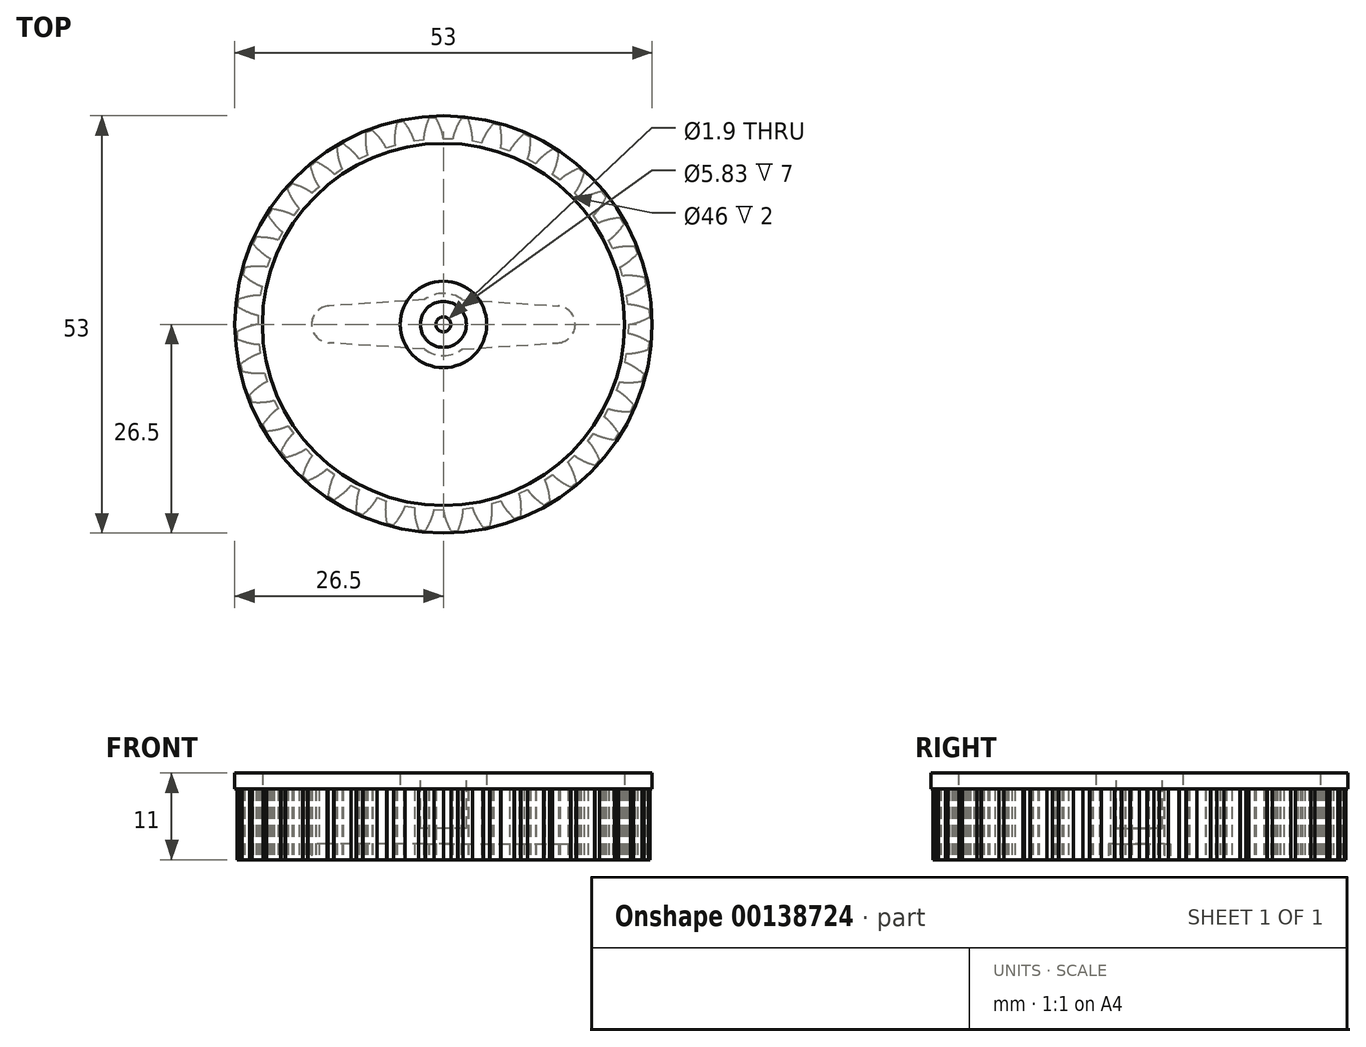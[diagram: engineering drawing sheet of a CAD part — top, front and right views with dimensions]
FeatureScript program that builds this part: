
annotation { "Feature Type Name" : "Feature", "Feature Type Description" : "" }
export const myFeature = defineFeature(function(context is Context, id is Id, definition is map)
    precondition{}
    {
        {
            var Q0;
            Q0=qCreatedBy(makeId("Top.planeOp"),FACE);
            var sketch = newSketch(context, id + "F0", { "sketchPlane" : qUnion([Q0])});
            skLineSegment(sketch, "E0", {"start": v(23.56, 0) * mm, "end": v(23.58, 0) * mm});
            skLineSegment(sketch, "E1", {"start": v(23.58, 0) * mm, "end": v(23.6, 0) * mm});
            skLineSegment(sketch, "E2", {"start": v(23.6, 0) * mm, "end": v(23.62, 0) * mm});
            skLineSegment(sketch, "E3", {"start": v(23.62, 0) * mm, "end": v(23.64, 0.01) * mm});
            skLineSegment(sketch, "E4", {"start": v(23.64, 0.01) * mm, "end": v(23.67, 0.01) * mm});
            skLineSegment(sketch, "E5", {"start": v(23.67, 0.01) * mm, "end": v(23.7, 0.02) * mm});
            skLineSegment(sketch, "E6", {"start": v(23.7, 0.02) * mm, "end": v(23.72, 0.02) * mm});
            skLineSegment(sketch, "E7", {"start": v(23.72, 0.02) * mm, "end": v(23.75, 0.03) * mm});
            skLineSegment(sketch, "E8", {"start": v(23.75, 0.03) * mm, "end": v(23.78, 0.03) * mm});
            skLineSegment(sketch, "E9", {"start": v(23.78, 0.03) * mm, "end": v(23.81, 0.04) * mm});
            skLineSegment(sketch, "E10", {"start": v(23.81, 0.04) * mm, "end": v(23.85, 0.04) * mm});
            skLineSegment(sketch, "E11", {"start": v(23.85, 0.04) * mm, "end": v(23.88, 0.05) * mm});
            skLineSegment(sketch, "E12", {"start": v(23.88, 0.05) * mm, "end": v(23.92, 0.06) * mm});
            skLineSegment(sketch, "E13", {"start": v(23.92, 0.06) * mm, "end": v(23.96, 0.06) * mm});
            skLineSegment(sketch, "E14", {"start": v(23.96, 0.06) * mm, "end": v(24, 0.07) * mm});
            skLineSegment(sketch, "E15", {"start": v(24, 0.07) * mm, "end": v(24.04, 0.08) * mm});
            skLineSegment(sketch, "E16", {"start": v(24.04, 0.08) * mm, "end": v(24.09, 0.1) * mm});
            skLineSegment(sketch, "E17", {"start": v(24.09, 0.1) * mm, "end": v(24.14, 0.1) * mm});
            skLineSegment(sketch, "E18", {"start": v(24.14, 0.1) * mm, "end": v(24.18, 0.11) * mm});
            skLineSegment(sketch, "E19", {"start": v(24.18, 0.11) * mm, "end": v(24.23, 0.13) * mm});
            skLineSegment(sketch, "E20", {"start": v(24.23, 0.13) * mm, "end": v(24.28, 0.14) * mm});
            skLineSegment(sketch, "E21", {"start": v(24.28, 0.14) * mm, "end": v(24.34, 0.15) * mm});
            skLineSegment(sketch, "E22", {"start": v(24.34, 0.15) * mm, "end": v(24.4, 0.17) * mm});
            skLineSegment(sketch, "E23", {"start": v(24.4, 0.17) * mm, "end": v(24.45, 0.19) * mm});
            skLineSegment(sketch, "E24", {"start": v(24.45, 0.19) * mm, "end": v(24.5, 0.2) * mm});
            skLineSegment(sketch, "E25", {"start": v(24.5, 0.2) * mm, "end": v(24.56, 0.22) * mm});
            skLineSegment(sketch, "E26", {"start": v(24.56, 0.22) * mm, "end": v(24.62, 0.24) * mm});
            skLineSegment(sketch, "E27", {"start": v(24.62, 0.24) * mm, "end": v(24.69, 0.26) * mm});
            skLineSegment(sketch, "E28", {"start": v(24.69, 0.26) * mm, "end": v(24.75, 0.28) * mm});
            skLineSegment(sketch, "E29", {"start": v(24.75, 0.28) * mm, "end": v(24.81, 0.3) * mm});
            skLineSegment(sketch, "E30", {"start": v(24.81, 0.3) * mm, "end": v(24.88, 0.33) * mm});
            skLineSegment(sketch, "E31", {"start": v(24.88, 0.33) * mm, "end": v(24.95, 0.35) * mm});
            skLineSegment(sketch, "E32", {"start": v(24.95, 0.35) * mm, "end": v(25.02, 0.38) * mm});
            skLineSegment(sketch, "E33", {"start": v(25.02, 0.38) * mm, "end": v(25.09, 0.4) * mm});
            skLineSegment(sketch, "E34", {"start": v(25.09, 0.4) * mm, "end": v(25.16, 0.44) * mm});
            skLineSegment(sketch, "E35", {"start": v(25.16, 0.44) * mm, "end": v(25.23, 0.47) * mm});
            skLineSegment(sketch, "E36", {"start": v(25.23, 0.47) * mm, "end": v(25.3, 0.5) * mm});
            skLineSegment(sketch, "E37", {"start": v(25.3, 0.5) * mm, "end": v(25.39, 0.53) * mm});
            skLineSegment(sketch, "E38", {"start": v(25.39, 0.53) * mm, "end": v(25.46, 0.57) * mm});
            skLineSegment(sketch, "E39", {"start": v(25.46, 0.57) * mm, "end": v(25.54, 0.6) * mm});
            skLineSegment(sketch, "E40", {"start": v(25.54, 0.6) * mm, "end": v(25.62, 0.64) * mm});
            skLineSegment(sketch, "E41", {"start": v(25.62, 0.64) * mm, "end": v(25.7, 0.68) * mm});
            skLineSegment(sketch, "E42", {"start": v(25.7, 0.68) * mm, "end": v(25.79, 0.72) * mm});
            skLineSegment(sketch, "E43", {"start": v(25.79, 0.72) * mm, "end": v(25.87, 0.76) * mm});
            skLineSegment(sketch, "E44", {"start": v(25.87, 0.76) * mm, "end": v(25.96, 0.8) * mm});
            skLineSegment(sketch, "E45", {"start": v(25.96, 0.8) * mm, "end": v(26.04, 0.85) * mm});
            skLineSegment(sketch, "E46", {"start": v(26.04, 0.85) * mm, "end": v(26.13, 0.9) * mm});
            skLineSegment(sketch, "E47", {"start": v(26.13, 0.9) * mm, "end": v(26.22, 0.94) * mm});
            skLineSegment(sketch, "E48", {"start": v(26.22, 0.94) * mm, "end": v(26.23, 0.99) * mm});
            skLineSegment(sketch, "E49", {"start": v(26.23, 0.99) * mm, "end": v(26.19, 1.82) * mm});
            skLineSegment(sketch, "E50", {"start": v(26.19, 1.82) * mm, "end": v(26.17, 1.86) * mm});
            skLineSegment(sketch, "E51", {"start": v(26.17, 1.86) * mm, "end": v(26.08, 1.9) * mm});
            skLineSegment(sketch, "E52", {"start": v(26.08, 1.9) * mm, "end": v(25.99, 1.94) * mm});
            skLineSegment(sketch, "E53", {"start": v(25.99, 1.94) * mm, "end": v(25.9, 1.97) * mm});
            skLineSegment(sketch, "E54", {"start": v(25.9, 1.97) * mm, "end": v(25.8, 2) * mm});
            skLineSegment(sketch, "E55", {"start": v(25.8, 2) * mm, "end": v(25.72, 2.04) * mm});
            skLineSegment(sketch, "E56", {"start": v(25.72, 2.04) * mm, "end": v(25.63, 2.07) * mm});
            skLineSegment(sketch, "E57", {"start": v(25.63, 2.07) * mm, "end": v(25.55, 2.1) * mm});
            skLineSegment(sketch, "E58", {"start": v(25.55, 2.1) * mm, "end": v(25.46, 2.13) * mm});
            skLineSegment(sketch, "E59", {"start": v(25.46, 2.13) * mm, "end": v(25.38, 2.16) * mm});
            skLineSegment(sketch, "E60", {"start": v(25.38, 2.16) * mm, "end": v(25.3, 2.18) * mm});
            skLineSegment(sketch, "E61", {"start": v(25.3, 2.18) * mm, "end": v(25.22, 2.2) * mm});
            skLineSegment(sketch, "E62", {"start": v(25.22, 2.2) * mm, "end": v(25.14, 2.23) * mm});
            skLineSegment(sketch, "E63", {"start": v(25.14, 2.23) * mm, "end": v(25.06, 2.25) * mm});
            skLineSegment(sketch, "E64", {"start": v(25.06, 2.25) * mm, "end": v(24.99, 2.27) * mm});
            skLineSegment(sketch, "E65", {"start": v(24.99, 2.27) * mm, "end": v(24.92, 2.3) * mm});
            skLineSegment(sketch, "E66", {"start": v(24.92, 2.3) * mm, "end": v(24.84, 2.31) * mm});
            skLineSegment(sketch, "E67", {"start": v(24.84, 2.31) * mm, "end": v(24.77, 2.33) * mm});
            skLineSegment(sketch, "E68", {"start": v(24.77, 2.33) * mm, "end": v(24.7, 2.34) * mm});
            skLineSegment(sketch, "E69", {"start": v(24.7, 2.34) * mm, "end": v(24.64, 2.36) * mm});
            skLineSegment(sketch, "E70", {"start": v(24.64, 2.36) * mm, "end": v(24.57, 2.38) * mm});
            skLineSegment(sketch, "E71", {"start": v(24.57, 2.38) * mm, "end": v(24.5, 2.39) * mm});
            skLineSegment(sketch, "E72", {"start": v(24.5, 2.39) * mm, "end": v(24.45, 2.4) * mm});
            skLineSegment(sketch, "E73", {"start": v(24.45, 2.4) * mm, "end": v(24.39, 2.41) * mm});
            skLineSegment(sketch, "E74", {"start": v(24.39, 2.41) * mm, "end": v(24.33, 2.42) * mm});
            skLineSegment(sketch, "E75", {"start": v(24.33, 2.42) * mm, "end": v(24.27, 2.43) * mm});
            skLineSegment(sketch, "E76", {"start": v(24.27, 2.43) * mm, "end": v(24.21, 2.44) * mm});
            skLineSegment(sketch, "E77", {"start": v(24.21, 2.44) * mm, "end": v(24.16, 2.45) * mm});
            skLineSegment(sketch, "E78", {"start": v(24.16, 2.45) * mm, "end": v(24.1, 2.46) * mm});
            skLineSegment(sketch, "E79", {"start": v(24.1, 2.46) * mm, "end": v(24.06, 2.47) * mm});
            skLineSegment(sketch, "E80", {"start": v(24.06, 2.47) * mm, "end": v(24, 2.47) * mm});
            skLineSegment(sketch, "E81", {"start": v(24, 2.47) * mm, "end": v(23.96, 2.48) * mm});
            skLineSegment(sketch, "E82", {"start": v(23.96, 2.48) * mm, "end": v(23.92, 2.49) * mm});
            skLineSegment(sketch, "E83", {"start": v(23.92, 2.49) * mm, "end": v(23.87, 2.5) * mm});
            skLineSegment(sketch, "E84", {"start": v(23.87, 2.5) * mm, "end": v(23.83, 2.5) * mm});
            skLineSegment(sketch, "E85", {"start": v(23.83, 2.5) * mm, "end": v(23.8, 2.5) * mm});
            skLineSegment(sketch, "E86", {"start": v(23.8, 2.5) * mm, "end": v(23.75, 2.5) * mm});
            skLineSegment(sketch, "E87", {"start": v(23.75, 2.5) * mm, "end": v(23.72, 2.5) * mm});
            skLineSegment(sketch, "E88", {"start": v(23.72, 2.5) * mm, "end": v(23.68, 2.5) * mm});
            skLineSegment(sketch, "E89", {"start": v(23.68, 2.5) * mm, "end": v(23.65, 2.5) * mm});
            skLineSegment(sketch, "E90", {"start": v(23.65, 2.5) * mm, "end": v(23.62, 2.5) * mm});
            skLineSegment(sketch, "E91", {"start": v(23.62, 2.5) * mm, "end": v(23.59, 2.51) * mm});
            skLineSegment(sketch, "E92", {"start": v(23.59, 2.51) * mm, "end": v(23.56, 2.51) * mm});
            skLineSegment(sketch, "E93", {"start": v(23.56, 2.51) * mm, "end": v(23.53, 2.51) * mm});
            skLineSegment(sketch, "E94", {"start": v(23.53, 2.51) * mm, "end": v(23.5, 2.51) * mm});
            skLineSegment(sketch, "E95", {"start": v(23.5, 2.51) * mm, "end": v(23.49, 2.51) * mm});
            skLineSegment(sketch, "E96", {"start": v(23.49, 2.51) * mm, "end": v(23.47, 2.51) * mm});
            skLineSegment(sketch, "E97", {"start": v(23.47, 2.51) * mm, "end": v(23.45, 2.51) * mm});
            skLineSegment(sketch, "E98", {"start": v(23.45, 2.51) * mm, "end": v(23.43, 2.51) * mm});
            skLineSegment(sketch, "E99", {"start": v(23.43, 2.51) * mm, "end": v(23.27, 3.69) * mm});
            skLineSegment(sketch, "E100", {"start": v(23.27, 3.69) * mm, "end": v(23.3, 3.7) * mm});
            skLineSegment(sketch, "E101", {"start": v(23.3, 3.7) * mm, "end": v(23.3, 3.7) * mm});
            skLineSegment(sketch, "E102", {"start": v(23.3, 3.7) * mm, "end": v(23.33, 3.7) * mm});
            skLineSegment(sketch, "E103", {"start": v(23.33, 3.7) * mm, "end": v(23.35, 3.7) * mm});
            skLineSegment(sketch, "E104", {"start": v(23.35, 3.7) * mm, "end": v(23.37, 3.72) * mm});
            skLineSegment(sketch, "E105", {"start": v(23.37, 3.72) * mm, "end": v(23.4, 3.72) * mm});
            skLineSegment(sketch, "E106", {"start": v(23.4, 3.72) * mm, "end": v(23.42, 3.73) * mm});
            skLineSegment(sketch, "E107", {"start": v(23.42, 3.73) * mm, "end": v(23.45, 3.74) * mm});
            skLineSegment(sketch, "E108", {"start": v(23.45, 3.74) * mm, "end": v(23.48, 3.75) * mm});
            skLineSegment(sketch, "E109", {"start": v(23.48, 3.75) * mm, "end": v(23.51, 3.76) * mm});
            skLineSegment(sketch, "E110", {"start": v(23.51, 3.76) * mm, "end": v(23.55, 3.77) * mm});
            skLineSegment(sketch, "E111", {"start": v(23.55, 3.77) * mm, "end": v(23.58, 3.78) * mm});
            skLineSegment(sketch, "E112", {"start": v(23.58, 3.78) * mm, "end": v(23.62, 3.8) * mm});
            skLineSegment(sketch, "E113", {"start": v(23.62, 3.8) * mm, "end": v(23.66, 3.81) * mm});
            skLineSegment(sketch, "E114", {"start": v(23.66, 3.81) * mm, "end": v(23.7, 3.83) * mm});
            skLineSegment(sketch, "E115", {"start": v(23.7, 3.83) * mm, "end": v(23.74, 3.84) * mm});
            skLineSegment(sketch, "E116", {"start": v(23.74, 3.84) * mm, "end": v(23.78, 3.86) * mm});
            skLineSegment(sketch, "E117", {"start": v(23.78, 3.86) * mm, "end": v(23.82, 3.88) * mm});
            skLineSegment(sketch, "E118", {"start": v(23.82, 3.88) * mm, "end": v(23.87, 3.9) * mm});
            skLineSegment(sketch, "E119", {"start": v(23.87, 3.9) * mm, "end": v(23.91, 3.92) * mm});
            skLineSegment(sketch, "E120", {"start": v(23.91, 3.92) * mm, "end": v(23.96, 3.94) * mm});
            skLineSegment(sketch, "E121", {"start": v(23.96, 3.94) * mm, "end": v(24.01, 3.96) * mm});
            skLineSegment(sketch, "E122", {"start": v(24.01, 3.96) * mm, "end": v(24.06, 3.98) * mm});
            skLineSegment(sketch, "E123", {"start": v(24.06, 3.98) * mm, "end": v(24.12, 4) * mm});
            skLineSegment(sketch, "E124", {"start": v(24.12, 4) * mm, "end": v(24.17, 4.03) * mm});
            skLineSegment(sketch, "E125", {"start": v(24.17, 4.03) * mm, "end": v(24.23, 4.06) * mm});
            skLineSegment(sketch, "E126", {"start": v(24.23, 4.06) * mm, "end": v(24.28, 4.09) * mm});
            skLineSegment(sketch, "E127", {"start": v(24.28, 4.09) * mm, "end": v(24.34, 4.12) * mm});
            skLineSegment(sketch, "E128", {"start": v(24.34, 4.12) * mm, "end": v(24.4, 4.15) * mm});
            skLineSegment(sketch, "E129", {"start": v(24.4, 4.15) * mm, "end": v(24.46, 4.18) * mm});
            skLineSegment(sketch, "E130", {"start": v(24.46, 4.18) * mm, "end": v(24.52, 4.22) * mm});
            skLineSegment(sketch, "E131", {"start": v(24.52, 4.22) * mm, "end": v(24.59, 4.25) * mm});
            skLineSegment(sketch, "E132", {"start": v(24.59, 4.25) * mm, "end": v(24.65, 4.29) * mm});
            skLineSegment(sketch, "E133", {"start": v(24.65, 4.29) * mm, "end": v(24.72, 4.33) * mm});
            skLineSegment(sketch, "E134", {"start": v(24.72, 4.33) * mm, "end": v(24.78, 4.37) * mm});
            skLineSegment(sketch, "E135", {"start": v(24.78, 4.37) * mm, "end": v(24.85, 4.4) * mm});
            skLineSegment(sketch, "E136", {"start": v(24.85, 4.4) * mm, "end": v(24.92, 4.45) * mm});
            skLineSegment(sketch, "E137", {"start": v(24.92, 4.45) * mm, "end": v(25, 4.5) * mm});
            skLineSegment(sketch, "E138", {"start": v(25, 4.5) * mm, "end": v(25.06, 4.54) * mm});
            skLineSegment(sketch, "E139", {"start": v(25.06, 4.54) * mm, "end": v(25.13, 4.59) * mm});
            skLineSegment(sketch, "E140", {"start": v(25.13, 4.59) * mm, "end": v(25.2, 4.64) * mm});
            skLineSegment(sketch, "E141", {"start": v(25.2, 4.64) * mm, "end": v(25.28, 4.69) * mm});
            skLineSegment(sketch, "E142", {"start": v(25.28, 4.69) * mm, "end": v(25.36, 4.74) * mm});
            skLineSegment(sketch, "E143", {"start": v(25.36, 4.74) * mm, "end": v(25.44, 4.8) * mm});
            skLineSegment(sketch, "E144", {"start": v(25.44, 4.8) * mm, "end": v(25.51, 4.85) * mm});
            skLineSegment(sketch, "E145", {"start": v(25.51, 4.85) * mm, "end": v(25.6, 4.9) * mm});
            skLineSegment(sketch, "E146", {"start": v(25.6, 4.9) * mm, "end": v(25.67, 4.97) * mm});
            skLineSegment(sketch, "E147", {"start": v(25.67, 4.97) * mm, "end": v(25.75, 5.03) * mm});
            skLineSegment(sketch, "E148", {"start": v(25.75, 5.03) * mm, "end": v(25.75, 5.08) * mm});
            skLineSegment(sketch, "E149", {"start": v(25.75, 5.08) * mm, "end": v(25.58, 5.9) * mm});
            skLineSegment(sketch, "E150", {"start": v(25.58, 5.9) * mm, "end": v(25.56, 5.93) * mm});
            skLineSegment(sketch, "E151", {"start": v(25.56, 5.93) * mm, "end": v(25.46, 5.96) * mm});
            skLineSegment(sketch, "E152", {"start": v(25.46, 5.96) * mm, "end": v(25.36, 5.98) * mm});
            skLineSegment(sketch, "E153", {"start": v(25.36, 5.98) * mm, "end": v(25.27, 6) * mm});
            skLineSegment(sketch, "E154", {"start": v(25.27, 6) * mm, "end": v(25.17, 6.02) * mm});
            skLineSegment(sketch, "E155", {"start": v(25.17, 6.02) * mm, "end": v(25.08, 6.04) * mm});
            skLineSegment(sketch, "E156", {"start": v(25.08, 6.04) * mm, "end": v(25, 6.05) * mm});
            skLineSegment(sketch, "E157", {"start": v(25, 6.05) * mm, "end": v(24.9, 6.07) * mm});
            skLineSegment(sketch, "E158", {"start": v(24.9, 6.07) * mm, "end": v(24.81, 6.09) * mm});
            skLineSegment(sketch, "E159", {"start": v(24.81, 6.09) * mm, "end": v(24.73, 6.1) * mm});
            skLineSegment(sketch, "E160", {"start": v(24.73, 6.1) * mm, "end": v(24.65, 6.11) * mm});
            skLineSegment(sketch, "E161", {"start": v(24.65, 6.11) * mm, "end": v(24.56, 6.12) * mm});
            skLineSegment(sketch, "E162", {"start": v(24.56, 6.12) * mm, "end": v(24.48, 6.13) * mm});
            skLineSegment(sketch, "E163", {"start": v(24.48, 6.13) * mm, "end": v(24.4, 6.14) * mm});
            skLineSegment(sketch, "E164", {"start": v(24.4, 6.14) * mm, "end": v(24.33, 6.15) * mm});
            skLineSegment(sketch, "E165", {"start": v(24.33, 6.15) * mm, "end": v(24.25, 6.16) * mm});
            skLineSegment(sketch, "E166", {"start": v(24.25, 6.16) * mm, "end": v(24.18, 6.17) * mm});
            skLineSegment(sketch, "E167", {"start": v(24.18, 6.17) * mm, "end": v(24.1, 6.17) * mm});
            skLineSegment(sketch, "E168", {"start": v(24.1, 6.17) * mm, "end": v(24.03, 6.18) * mm});
            skLineSegment(sketch, "E169", {"start": v(24.03, 6.18) * mm, "end": v(23.96, 6.19) * mm});
            skLineSegment(sketch, "E170", {"start": v(23.96, 6.19) * mm, "end": v(23.9, 6.19) * mm});
            skLineSegment(sketch, "E171", {"start": v(23.9, 6.19) * mm, "end": v(23.83, 6.2) * mm});
            skLineSegment(sketch, "E172", {"start": v(23.83, 6.2) * mm, "end": v(23.77, 6.2) * mm});
            skLineSegment(sketch, "E173", {"start": v(23.77, 6.2) * mm, "end": v(23.7, 6.2) * mm});
            skLineSegment(sketch, "E174", {"start": v(23.7, 6.2) * mm, "end": v(23.65, 6.2) * mm});
            skLineSegment(sketch, "E175", {"start": v(23.65, 6.2) * mm, "end": v(23.59, 6.2) * mm});
            skLineSegment(sketch, "E176", {"start": v(23.59, 6.2) * mm, "end": v(23.53, 6.2) * mm});
            skLineSegment(sketch, "E177", {"start": v(23.53, 6.2) * mm, "end": v(23.48, 6.2) * mm});
            skLineSegment(sketch, "E178", {"start": v(23.48, 6.2) * mm, "end": v(23.43, 6.2) * mm});
            skLineSegment(sketch, "E179", {"start": v(23.43, 6.2) * mm, "end": v(23.37, 6.2) * mm});
            skLineSegment(sketch, "E180", {"start": v(23.37, 6.2) * mm, "end": v(23.33, 6.2) * mm});
            skLineSegment(sketch, "E181", {"start": v(23.33, 6.2) * mm, "end": v(23.28, 6.2) * mm});
            skLineSegment(sketch, "E182", {"start": v(23.28, 6.2) * mm, "end": v(23.23, 6.2) * mm});
            skLineSegment(sketch, "E183", {"start": v(23.23, 6.2) * mm, "end": v(23.19, 6.2) * mm});
            skLineSegment(sketch, "E184", {"start": v(23.19, 6.2) * mm, "end": v(23.15, 6.2) * mm});
            skLineSegment(sketch, "E185", {"start": v(23.15, 6.2) * mm, "end": v(23.1, 6.19) * mm});
            skLineSegment(sketch, "E186", {"start": v(23.1, 6.19) * mm, "end": v(23.07, 6.19) * mm});
            skLineSegment(sketch, "E187", {"start": v(23.07, 6.19) * mm, "end": v(23.03, 6.18) * mm});
            skLineSegment(sketch, "E188", {"start": v(23.03, 6.18) * mm, "end": v(23, 6.18) * mm});
            skLineSegment(sketch, "E189", {"start": v(23, 6.18) * mm, "end": v(22.96, 6.18) * mm});
            skLineSegment(sketch, "E190", {"start": v(22.96, 6.18) * mm, "end": v(22.93, 6.17) * mm});
            skLineSegment(sketch, "E191", {"start": v(22.93, 6.17) * mm, "end": v(22.9, 6.17) * mm});
            skLineSegment(sketch, "E192", {"start": v(22.9, 6.17) * mm, "end": v(22.88, 6.17) * mm});
            skLineSegment(sketch, "E193", {"start": v(22.88, 6.17) * mm, "end": v(22.85, 6.16) * mm});
            skLineSegment(sketch, "E194", {"start": v(22.85, 6.16) * mm, "end": v(22.83, 6.16) * mm});
            skLineSegment(sketch, "E195", {"start": v(22.83, 6.16) * mm, "end": v(22.8, 6.16) * mm});
            skLineSegment(sketch, "E196", {"start": v(22.8, 6.16) * mm, "end": v(22.78, 6.15) * mm});
            skLineSegment(sketch, "E197", {"start": v(22.78, 6.15) * mm, "end": v(22.77, 6.15) * mm});
            skLineSegment(sketch, "E198", {"start": v(22.77, 6.15) * mm, "end": v(22.75, 6.15) * mm});
            skLineSegment(sketch, "E199", {"start": v(22.75, 6.15) * mm, "end": v(22.4, 7.28) * mm});
            skLineSegment(sketch, "E200", {"start": v(22.4, 7.28) * mm, "end": v(22.43, 7.3) * mm});
            skLineSegment(sketch, "E201", {"start": v(22.43, 7.3) * mm, "end": v(22.44, 7.3) * mm});
            skLineSegment(sketch, "E202", {"start": v(22.44, 7.3) * mm, "end": v(22.46, 7.3) * mm});
            skLineSegment(sketch, "E203", {"start": v(22.46, 7.3) * mm, "end": v(22.48, 7.32) * mm});
            skLineSegment(sketch, "E204", {"start": v(22.48, 7.32) * mm, "end": v(22.5, 7.33) * mm});
            skLineSegment(sketch, "E205", {"start": v(22.5, 7.33) * mm, "end": v(22.53, 7.34) * mm});
            skLineSegment(sketch, "E206", {"start": v(22.53, 7.34) * mm, "end": v(22.55, 7.35) * mm});
            skLineSegment(sketch, "E207", {"start": v(22.55, 7.35) * mm, "end": v(22.58, 7.36) * mm});
            skLineSegment(sketch, "E208", {"start": v(22.58, 7.36) * mm, "end": v(22.6, 7.38) * mm});
            skLineSegment(sketch, "E209", {"start": v(22.6, 7.38) * mm, "end": v(22.64, 7.4) * mm});
            skLineSegment(sketch, "E210", {"start": v(22.64, 7.4) * mm, "end": v(22.67, 7.4) * mm});
            skLineSegment(sketch, "E211", {"start": v(22.67, 7.4) * mm, "end": v(22.7, 7.43) * mm});
            skLineSegment(sketch, "E212", {"start": v(22.7, 7.43) * mm, "end": v(22.73, 7.44) * mm});
            skLineSegment(sketch, "E213", {"start": v(22.73, 7.44) * mm, "end": v(22.77, 7.46) * mm});
            skLineSegment(sketch, "E214", {"start": v(22.77, 7.46) * mm, "end": v(22.8, 7.49) * mm});
            skLineSegment(sketch, "E215", {"start": v(22.8, 7.49) * mm, "end": v(22.84, 7.5) * mm});
            skLineSegment(sketch, "E216", {"start": v(22.84, 7.5) * mm, "end": v(22.88, 7.53) * mm});
            skLineSegment(sketch, "E217", {"start": v(22.88, 7.53) * mm, "end": v(22.92, 7.56) * mm});
            skLineSegment(sketch, "E218", {"start": v(22.92, 7.56) * mm, "end": v(22.96, 7.58) * mm});
            skLineSegment(sketch, "E219", {"start": v(22.96, 7.58) * mm, "end": v(23, 7.6) * mm});
            skLineSegment(sketch, "E220", {"start": v(23, 7.6) * mm, "end": v(23.05, 7.64) * mm});
            skLineSegment(sketch, "E221", {"start": v(23.05, 7.64) * mm, "end": v(23.1, 7.67) * mm});
            skLineSegment(sketch, "E222", {"start": v(23.1, 7.67) * mm, "end": v(23.14, 7.7) * mm});
            skLineSegment(sketch, "E223", {"start": v(23.14, 7.7) * mm, "end": v(23.2, 7.73) * mm});
            skLineSegment(sketch, "E224", {"start": v(23.2, 7.73) * mm, "end": v(23.24, 7.76) * mm});
            skLineSegment(sketch, "E225", {"start": v(23.24, 7.76) * mm, "end": v(23.3, 7.8) * mm});
            skLineSegment(sketch, "E226", {"start": v(23.3, 7.8) * mm, "end": v(23.34, 7.84) * mm});
            skLineSegment(sketch, "E227", {"start": v(23.34, 7.84) * mm, "end": v(23.4, 7.88) * mm});
            skLineSegment(sketch, "E228", {"start": v(23.4, 7.88) * mm, "end": v(23.45, 7.92) * mm});
            skLineSegment(sketch, "E229", {"start": v(23.45, 7.92) * mm, "end": v(23.5, 7.96) * mm});
            skLineSegment(sketch, "E230", {"start": v(23.5, 7.96) * mm, "end": v(23.56, 8) * mm});
            skLineSegment(sketch, "E231", {"start": v(23.56, 8) * mm, "end": v(23.62, 8.05) * mm});
            skLineSegment(sketch, "E232", {"start": v(23.62, 8.05) * mm, "end": v(23.68, 8.1) * mm});
            skLineSegment(sketch, "E233", {"start": v(23.68, 8.1) * mm, "end": v(23.73, 8.14) * mm});
            skLineSegment(sketch, "E234", {"start": v(23.73, 8.14) * mm, "end": v(23.8, 8.2) * mm});
            skLineSegment(sketch, "E235", {"start": v(23.8, 8.2) * mm, "end": v(23.86, 8.24) * mm});
            skLineSegment(sketch, "E236", {"start": v(23.86, 8.24) * mm, "end": v(23.92, 8.3) * mm});
            skLineSegment(sketch, "E237", {"start": v(23.92, 8.3) * mm, "end": v(23.98, 8.35) * mm});
            skLineSegment(sketch, "E238", {"start": v(23.98, 8.35) * mm, "end": v(24.04, 8.4) * mm});
            skLineSegment(sketch, "E239", {"start": v(24.04, 8.4) * mm, "end": v(24.1, 8.46) * mm});
            skLineSegment(sketch, "E240", {"start": v(24.1, 8.46) * mm, "end": v(24.17, 8.53) * mm});
            skLineSegment(sketch, "E241", {"start": v(24.17, 8.53) * mm, "end": v(24.24, 8.59) * mm});
            skLineSegment(sketch, "E242", {"start": v(24.24, 8.59) * mm, "end": v(24.3, 8.65) * mm});
            skLineSegment(sketch, "E243", {"start": v(24.3, 8.65) * mm, "end": v(24.37, 8.72) * mm});
            skLineSegment(sketch, "E244", {"start": v(24.37, 8.72) * mm, "end": v(24.44, 8.78) * mm});
            skLineSegment(sketch, "E245", {"start": v(24.44, 8.78) * mm, "end": v(24.5, 8.85) * mm});
            skLineSegment(sketch, "E246", {"start": v(24.5, 8.85) * mm, "end": v(24.58, 8.92) * mm});
            skLineSegment(sketch, "E247", {"start": v(24.58, 8.92) * mm, "end": v(24.65, 9) * mm});
            skLineSegment(sketch, "E248", {"start": v(24.65, 9) * mm, "end": v(24.64, 9.04) * mm});
            skLineSegment(sketch, "E249", {"start": v(24.64, 9.04) * mm, "end": v(24.34, 9.82) * mm});
            skLineSegment(sketch, "E250", {"start": v(24.34, 9.82) * mm, "end": v(24.32, 9.86) * mm});
            skLineSegment(sketch, "E251", {"start": v(24.32, 9.86) * mm, "end": v(24.21, 9.87) * mm});
            skLineSegment(sketch, "E252", {"start": v(24.21, 9.87) * mm, "end": v(24.12, 9.87) * mm});
            skLineSegment(sketch, "E253", {"start": v(24.12, 9.87) * mm, "end": v(24.02, 9.88) * mm});
            skLineSegment(sketch, "E254", {"start": v(24.02, 9.88) * mm, "end": v(23.92, 9.88) * mm});
            skLineSegment(sketch, "E255", {"start": v(23.92, 9.88) * mm, "end": v(23.83, 9.89) * mm});
            skLineSegment(sketch, "E256", {"start": v(23.83, 9.89) * mm, "end": v(23.74, 9.89) * mm});
            skLineSegment(sketch, "E257", {"start": v(23.74, 9.89) * mm, "end": v(23.65, 9.9) * mm});
            skLineSegment(sketch, "E258", {"start": v(23.65, 9.9) * mm, "end": v(23.56, 9.9) * mm});
            skLineSegment(sketch, "E259", {"start": v(23.56, 9.9) * mm, "end": v(23.47, 9.9) * mm});
            skLineSegment(sketch, "E260", {"start": v(23.47, 9.9) * mm, "end": v(23.39, 9.9) * mm});
            skLineSegment(sketch, "E261", {"start": v(23.39, 9.9) * mm, "end": v(23.3, 9.9) * mm});
            skLineSegment(sketch, "E262", {"start": v(23.3, 9.9) * mm, "end": v(23.22, 9.89) * mm});
            skLineSegment(sketch, "E263", {"start": v(23.22, 9.89) * mm, "end": v(23.14, 9.89) * mm});
            skLineSegment(sketch, "E264", {"start": v(23.14, 9.89) * mm, "end": v(23.06, 9.88) * mm});
            skLineSegment(sketch, "E265", {"start": v(23.06, 9.88) * mm, "end": v(22.99, 9.88) * mm});
            skLineSegment(sketch, "E266", {"start": v(22.99, 9.88) * mm, "end": v(22.91, 9.87) * mm});
            skLineSegment(sketch, "E267", {"start": v(22.91, 9.87) * mm, "end": v(22.84, 9.87) * mm});
            skLineSegment(sketch, "E268", {"start": v(22.84, 9.87) * mm, "end": v(22.77, 9.86) * mm});
            skLineSegment(sketch, "E269", {"start": v(22.77, 9.86) * mm, "end": v(22.7, 9.86) * mm});
            skLineSegment(sketch, "E270", {"start": v(22.7, 9.86) * mm, "end": v(22.64, 9.85) * mm});
            skLineSegment(sketch, "E271", {"start": v(22.64, 9.85) * mm, "end": v(22.57, 9.85) * mm});
            skLineSegment(sketch, "E272", {"start": v(22.57, 9.85) * mm, "end": v(22.5, 9.84) * mm});
            skLineSegment(sketch, "E273", {"start": v(22.5, 9.84) * mm, "end": v(22.45, 9.83) * mm});
            skLineSegment(sketch, "E274", {"start": v(22.45, 9.83) * mm, "end": v(22.39, 9.82) * mm});
            skLineSegment(sketch, "E275", {"start": v(22.39, 9.82) * mm, "end": v(22.33, 9.82) * mm});
            skLineSegment(sketch, "E276", {"start": v(22.33, 9.82) * mm, "end": v(22.27, 9.8) * mm});
            skLineSegment(sketch, "E277", {"start": v(22.27, 9.8) * mm, "end": v(22.22, 9.8) * mm});
            skLineSegment(sketch, "E278", {"start": v(22.22, 9.8) * mm, "end": v(22.17, 9.79) * mm});
            skLineSegment(sketch, "E279", {"start": v(22.17, 9.79) * mm, "end": v(22.12, 9.78) * mm});
            skLineSegment(sketch, "E280", {"start": v(22.12, 9.78) * mm, "end": v(22.07, 9.77) * mm});
            skLineSegment(sketch, "E281", {"start": v(22.07, 9.77) * mm, "end": v(22.02, 9.76) * mm});
            skLineSegment(sketch, "E282", {"start": v(22.02, 9.76) * mm, "end": v(21.98, 9.75) * mm});
            skLineSegment(sketch, "E283", {"start": v(21.98, 9.75) * mm, "end": v(21.93, 9.75) * mm});
            skLineSegment(sketch, "E284", {"start": v(21.93, 9.75) * mm, "end": v(21.9, 9.74) * mm});
            skLineSegment(sketch, "E285", {"start": v(21.9, 9.74) * mm, "end": v(21.85, 9.73) * mm});
            skLineSegment(sketch, "E286", {"start": v(21.85, 9.73) * mm, "end": v(21.82, 9.72) * mm});
            skLineSegment(sketch, "E287", {"start": v(21.82, 9.72) * mm, "end": v(21.78, 9.7) * mm});
            skLineSegment(sketch, "E288", {"start": v(21.78, 9.7) * mm, "end": v(21.75, 9.7) * mm});
            skLineSegment(sketch, "E289", {"start": v(21.75, 9.7) * mm, "end": v(21.72, 9.7) * mm});
            skLineSegment(sketch, "E290", {"start": v(21.72, 9.7) * mm, "end": v(21.69, 9.68) * mm});
            skLineSegment(sketch, "E291", {"start": v(21.69, 9.68) * mm, "end": v(21.66, 9.68) * mm});
            skLineSegment(sketch, "E292", {"start": v(21.66, 9.68) * mm, "end": v(21.63, 9.67) * mm});
            skLineSegment(sketch, "E293", {"start": v(21.63, 9.67) * mm, "end": v(21.6, 9.66) * mm});
            skLineSegment(sketch, "E294", {"start": v(21.6, 9.66) * mm, "end": v(21.58, 9.65) * mm});
            skLineSegment(sketch, "E295", {"start": v(21.58, 9.65) * mm, "end": v(21.56, 9.65) * mm});
            skLineSegment(sketch, "E296", {"start": v(21.56, 9.65) * mm, "end": v(21.54, 9.64) * mm});
            skLineSegment(sketch, "E297", {"start": v(21.54, 9.64) * mm, "end": v(21.52, 9.63) * mm});
            skLineSegment(sketch, "E298", {"start": v(21.52, 9.63) * mm, "end": v(21.5, 9.63) * mm});
            skLineSegment(sketch, "E299", {"start": v(21.5, 9.63) * mm, "end": v(21, 10.7) * mm});
            skLineSegment(sketch, "E300", {"start": v(21, 10.7) * mm, "end": v(21, 10.71) * mm});
            skLineSegment(sketch, "E301", {"start": v(21, 10.71) * mm, "end": v(21.02, 10.72) * mm});
            skLineSegment(sketch, "E302", {"start": v(21.02, 10.72) * mm, "end": v(21.04, 10.73) * mm});
            skLineSegment(sketch, "E303", {"start": v(21.04, 10.73) * mm, "end": v(21.06, 10.74) * mm});
            skLineSegment(sketch, "E304", {"start": v(21.06, 10.74) * mm, "end": v(21.08, 10.76) * mm});
            skLineSegment(sketch, "E305", {"start": v(21.08, 10.76) * mm, "end": v(21.1, 10.77) * mm});
            skLineSegment(sketch, "E306", {"start": v(21.1, 10.77) * mm, "end": v(21.13, 10.79) * mm});
            skLineSegment(sketch, "E307", {"start": v(21.13, 10.79) * mm, "end": v(21.15, 10.8) * mm});
            skLineSegment(sketch, "E308", {"start": v(21.15, 10.8) * mm, "end": v(21.17, 10.82) * mm});
            skLineSegment(sketch, "E309", {"start": v(21.17, 10.82) * mm, "end": v(21.2, 10.84) * mm});
            skLineSegment(sketch, "E310", {"start": v(21.2, 10.84) * mm, "end": v(21.23, 10.86) * mm});
            skLineSegment(sketch, "E311", {"start": v(21.23, 10.86) * mm, "end": v(21.26, 10.89) * mm});
            skLineSegment(sketch, "E312", {"start": v(21.26, 10.89) * mm, "end": v(21.29, 10.9) * mm});
            skLineSegment(sketch, "E313", {"start": v(21.29, 10.9) * mm, "end": v(21.32, 10.93) * mm});
            skLineSegment(sketch, "E314", {"start": v(21.32, 10.93) * mm, "end": v(21.35, 10.96) * mm});
            skLineSegment(sketch, "E315", {"start": v(21.35, 10.96) * mm, "end": v(21.39, 10.99) * mm});
            skLineSegment(sketch, "E316", {"start": v(21.39, 10.99) * mm, "end": v(21.42, 11.02) * mm});
            skLineSegment(sketch, "E317", {"start": v(21.42, 11.02) * mm, "end": v(21.46, 11.05) * mm});
            skLineSegment(sketch, "E318", {"start": v(21.46, 11.05) * mm, "end": v(21.5, 11.08) * mm});
            skLineSegment(sketch, "E319", {"start": v(21.5, 11.08) * mm, "end": v(21.53, 11.11) * mm});
            skLineSegment(sketch, "E320", {"start": v(21.53, 11.11) * mm, "end": v(21.57, 11.15) * mm});
            skLineSegment(sketch, "E321", {"start": v(21.57, 11.15) * mm, "end": v(21.61, 11.19) * mm});
            skLineSegment(sketch, "E322", {"start": v(21.61, 11.19) * mm, "end": v(21.66, 11.22) * mm});
            skLineSegment(sketch, "E323", {"start": v(21.66, 11.22) * mm, "end": v(21.7, 11.26) * mm});
            skLineSegment(sketch, "E324", {"start": v(21.7, 11.26) * mm, "end": v(21.74, 11.3) * mm});
            skLineSegment(sketch, "E325", {"start": v(21.74, 11.3) * mm, "end": v(21.79, 11.35) * mm});
            skLineSegment(sketch, "E326", {"start": v(21.79, 11.35) * mm, "end": v(21.83, 11.4) * mm});
            skLineSegment(sketch, "E327", {"start": v(21.83, 11.4) * mm, "end": v(21.88, 11.44) * mm});
            skLineSegment(sketch, "E328", {"start": v(21.88, 11.44) * mm, "end": v(21.92, 11.49) * mm});
            skLineSegment(sketch, "E329", {"start": v(21.92, 11.49) * mm, "end": v(21.97, 11.54) * mm});
            skLineSegment(sketch, "E330", {"start": v(21.97, 11.54) * mm, "end": v(22.02, 11.59) * mm});
            skLineSegment(sketch, "E331", {"start": v(22.02, 11.59) * mm, "end": v(22.07, 11.64) * mm});
            skLineSegment(sketch, "E332", {"start": v(22.07, 11.64) * mm, "end": v(22.12, 11.7) * mm});
            skLineSegment(sketch, "E333", {"start": v(22.12, 11.7) * mm, "end": v(22.17, 11.75) * mm});
            skLineSegment(sketch, "E334", {"start": v(22.17, 11.75) * mm, "end": v(22.22, 11.81) * mm});
            skLineSegment(sketch, "E335", {"start": v(22.22, 11.81) * mm, "end": v(22.27, 11.87) * mm});
            skLineSegment(sketch, "E336", {"start": v(22.27, 11.87) * mm, "end": v(22.32, 11.93) * mm});
            skLineSegment(sketch, "E337", {"start": v(22.32, 11.93) * mm, "end": v(22.38, 12) * mm});
            skLineSegment(sketch, "E338", {"start": v(22.38, 12) * mm, "end": v(22.43, 12.06) * mm});
            skLineSegment(sketch, "E339", {"start": v(22.43, 12.06) * mm, "end": v(22.49, 12.13) * mm});
            skLineSegment(sketch, "E340", {"start": v(22.49, 12.13) * mm, "end": v(22.54, 12.2) * mm});
            skLineSegment(sketch, "E341", {"start": v(22.54, 12.2) * mm, "end": v(22.6, 12.27) * mm});
            skLineSegment(sketch, "E342", {"start": v(22.6, 12.27) * mm, "end": v(22.65, 12.35) * mm});
            skLineSegment(sketch, "E343", {"start": v(22.65, 12.35) * mm, "end": v(22.7, 12.42) * mm});
            skLineSegment(sketch, "E344", {"start": v(22.7, 12.42) * mm, "end": v(22.76, 12.5) * mm});
            skLineSegment(sketch, "E345", {"start": v(22.76, 12.5) * mm, "end": v(22.82, 12.58) * mm});
            skLineSegment(sketch, "E346", {"start": v(22.82, 12.58) * mm, "end": v(22.88, 12.66) * mm});
            skLineSegment(sketch, "E347", {"start": v(22.88, 12.66) * mm, "end": v(22.94, 12.74) * mm});
            skLineSegment(sketch, "E348", {"start": v(22.94, 12.74) * mm, "end": v(22.92, 12.79) * mm});
            skLineSegment(sketch, "E349", {"start": v(22.92, 12.79) * mm, "end": v(22.5, 13.5) * mm});
            skLineSegment(sketch, "E350", {"start": v(22.5, 13.5) * mm, "end": v(22.47, 13.54) * mm});
            skLineSegment(sketch, "E351", {"start": v(22.47, 13.54) * mm, "end": v(22.37, 13.53) * mm});
            skLineSegment(sketch, "E352", {"start": v(22.37, 13.53) * mm, "end": v(22.27, 13.52) * mm});
            skLineSegment(sketch, "E353", {"start": v(22.27, 13.52) * mm, "end": v(22.18, 13.51) * mm});
            skLineSegment(sketch, "E354", {"start": v(22.18, 13.51) * mm, "end": v(22.08, 13.5) * mm});
            skLineSegment(sketch, "E355", {"start": v(22.08, 13.5) * mm, "end": v(21.99, 13.5) * mm});
            skLineSegment(sketch, "E356", {"start": v(21.99, 13.5) * mm, "end": v(21.9, 13.48) * mm});
            skLineSegment(sketch, "E357", {"start": v(21.9, 13.48) * mm, "end": v(21.8, 13.47) * mm});
            skLineSegment(sketch, "E358", {"start": v(21.8, 13.47) * mm, "end": v(21.72, 13.46) * mm});
            skLineSegment(sketch, "E359", {"start": v(21.72, 13.46) * mm, "end": v(21.63, 13.44) * mm});
            skLineSegment(sketch, "E360", {"start": v(21.63, 13.44) * mm, "end": v(21.55, 13.43) * mm});
            skLineSegment(sketch, "E361", {"start": v(21.55, 13.43) * mm, "end": v(21.47, 13.41) * mm});
            skLineSegment(sketch, "E362", {"start": v(21.47, 13.41) * mm, "end": v(21.39, 13.4) * mm});
            skLineSegment(sketch, "E363", {"start": v(21.39, 13.4) * mm, "end": v(21.31, 13.38) * mm});
            skLineSegment(sketch, "E364", {"start": v(21.31, 13.38) * mm, "end": v(21.23, 13.37) * mm});
            skLineSegment(sketch, "E365", {"start": v(21.23, 13.37) * mm, "end": v(21.16, 13.35) * mm});
            skLineSegment(sketch, "E366", {"start": v(21.16, 13.35) * mm, "end": v(21.09, 13.34) * mm});
            skLineSegment(sketch, "E367", {"start": v(21.09, 13.34) * mm, "end": v(21.02, 13.32) * mm});
            skLineSegment(sketch, "E368", {"start": v(21.02, 13.32) * mm, "end": v(20.95, 13.3) * mm});
            skLineSegment(sketch, "E369", {"start": v(20.95, 13.3) * mm, "end": v(20.88, 13.29) * mm});
            skLineSegment(sketch, "E370", {"start": v(20.88, 13.29) * mm, "end": v(20.82, 13.27) * mm});
            skLineSegment(sketch, "E371", {"start": v(20.82, 13.27) * mm, "end": v(20.75, 13.25) * mm});
            skLineSegment(sketch, "E372", {"start": v(20.75, 13.25) * mm, "end": v(20.7, 13.24) * mm});
            skLineSegment(sketch, "E373", {"start": v(20.7, 13.24) * mm, "end": v(20.63, 13.22) * mm});
            skLineSegment(sketch, "E374", {"start": v(20.63, 13.22) * mm, "end": v(20.57, 13.2) * mm});
            skLineSegment(sketch, "E375", {"start": v(20.57, 13.2) * mm, "end": v(20.52, 13.19) * mm});
            skLineSegment(sketch, "E376", {"start": v(20.52, 13.19) * mm, "end": v(20.46, 13.17) * mm});
            skLineSegment(sketch, "E377", {"start": v(20.46, 13.17) * mm, "end": v(20.41, 13.15) * mm});
            skLineSegment(sketch, "E378", {"start": v(20.41, 13.15) * mm, "end": v(20.36, 13.14) * mm});
            skLineSegment(sketch, "E379", {"start": v(20.36, 13.14) * mm, "end": v(20.31, 13.12) * mm});
            skLineSegment(sketch, "E380", {"start": v(20.31, 13.12) * mm, "end": v(20.27, 13.1) * mm});
            skLineSegment(sketch, "E381", {"start": v(20.27, 13.1) * mm, "end": v(20.22, 13.09) * mm});
            skLineSegment(sketch, "E382", {"start": v(20.22, 13.09) * mm, "end": v(20.18, 13.07) * mm});
            skLineSegment(sketch, "E383", {"start": v(20.18, 13.07) * mm, "end": v(20.14, 13.06) * mm});
            skLineSegment(sketch, "E384", {"start": v(20.14, 13.06) * mm, "end": v(20.1, 13.04) * mm});
            skLineSegment(sketch, "E385", {"start": v(20.1, 13.04) * mm, "end": v(20.06, 13.03) * mm});
            skLineSegment(sketch, "E386", {"start": v(20.06, 13.03) * mm, "end": v(20.03, 13.01) * mm});
            skLineSegment(sketch, "E387", {"start": v(20.03, 13.01) * mm, "end": v(20, 13) * mm});
            skLineSegment(sketch, "E388", {"start": v(20, 13) * mm, "end": v(19.96, 12.98) * mm});
            skLineSegment(sketch, "E389", {"start": v(19.96, 12.98) * mm, "end": v(19.93, 12.97) * mm});
            skLineSegment(sketch, "E390", {"start": v(19.93, 12.97) * mm, "end": v(19.9, 12.96) * mm});
            skLineSegment(sketch, "E391", {"start": v(19.9, 12.96) * mm, "end": v(19.88, 12.94) * mm});
            skLineSegment(sketch, "E392", {"start": v(19.88, 12.94) * mm, "end": v(19.85, 12.93) * mm});
            skLineSegment(sketch, "E393", {"start": v(19.85, 12.93) * mm, "end": v(19.83, 12.92) * mm});
            skLineSegment(sketch, "E394", {"start": v(19.83, 12.92) * mm, "end": v(19.8, 12.91) * mm});
            skLineSegment(sketch, "E395", {"start": v(19.8, 12.91) * mm, "end": v(19.79, 12.9) * mm});
            skLineSegment(sketch, "E396", {"start": v(19.79, 12.9) * mm, "end": v(19.77, 12.9) * mm});
            skLineSegment(sketch, "E397", {"start": v(19.77, 12.9) * mm, "end": v(19.75, 12.88) * mm});
            skLineSegment(sketch, "E398", {"start": v(19.75, 12.88) * mm, "end": v(19.73, 12.88) * mm});
            skLineSegment(sketch, "E399", {"start": v(19.73, 12.88) * mm, "end": v(19.06, 13.85) * mm});
            skLineSegment(sketch, "E400", {"start": v(19.06, 13.85) * mm, "end": v(19.07, 13.87) * mm});
            skLineSegment(sketch, "E401", {"start": v(19.07, 13.87) * mm, "end": v(19.09, 13.88) * mm});
            skLineSegment(sketch, "E402", {"start": v(19.09, 13.88) * mm, "end": v(19.1, 13.9) * mm});
            skLineSegment(sketch, "E403", {"start": v(19.1, 13.9) * mm, "end": v(19.12, 13.9) * mm});
            skLineSegment(sketch, "E404", {"start": v(19.12, 13.9) * mm, "end": v(19.14, 13.92) * mm});
            skLineSegment(sketch, "E405", {"start": v(19.14, 13.92) * mm, "end": v(19.16, 13.94) * mm});
            skLineSegment(sketch, "E406", {"start": v(19.16, 13.94) * mm, "end": v(19.18, 13.96) * mm});
            skLineSegment(sketch, "E407", {"start": v(19.18, 13.96) * mm, "end": v(19.2, 13.98) * mm});
            skLineSegment(sketch, "E408", {"start": v(19.2, 13.98) * mm, "end": v(19.22, 14) * mm});
            skLineSegment(sketch, "E409", {"start": v(19.22, 14) * mm, "end": v(19.24, 14.03) * mm});
            skLineSegment(sketch, "E410", {"start": v(19.24, 14.03) * mm, "end": v(19.27, 14.05) * mm});
            skLineSegment(sketch, "E411", {"start": v(19.27, 14.05) * mm, "end": v(19.3, 14.08) * mm});
            skLineSegment(sketch, "E412", {"start": v(19.3, 14.08) * mm, "end": v(19.32, 14.1) * mm});
            skLineSegment(sketch, "E413", {"start": v(19.32, 14.1) * mm, "end": v(19.35, 14.13) * mm});
            skLineSegment(sketch, "E414", {"start": v(19.35, 14.13) * mm, "end": v(19.38, 14.17) * mm});
            skLineSegment(sketch, "E415", {"start": v(19.38, 14.17) * mm, "end": v(19.4, 14.2) * mm});
            skLineSegment(sketch, "E416", {"start": v(19.4, 14.2) * mm, "end": v(19.44, 14.23) * mm});
            skLineSegment(sketch, "E417", {"start": v(19.44, 14.23) * mm, "end": v(19.47, 14.27) * mm});
            skLineSegment(sketch, "E418", {"start": v(19.47, 14.27) * mm, "end": v(19.5, 14.3) * mm});
            skLineSegment(sketch, "E419", {"start": v(19.5, 14.3) * mm, "end": v(19.53, 14.35) * mm});
            skLineSegment(sketch, "E420", {"start": v(19.53, 14.35) * mm, "end": v(19.56, 14.39) * mm});
            skLineSegment(sketch, "E421", {"start": v(19.56, 14.39) * mm, "end": v(19.6, 14.43) * mm});
            skLineSegment(sketch, "E422", {"start": v(19.6, 14.43) * mm, "end": v(19.63, 14.47) * mm});
            skLineSegment(sketch, "E423", {"start": v(19.63, 14.47) * mm, "end": v(19.67, 14.52) * mm});
            skLineSegment(sketch, "E424", {"start": v(19.67, 14.52) * mm, "end": v(19.7, 14.57) * mm});
            skLineSegment(sketch, "E425", {"start": v(19.7, 14.57) * mm, "end": v(19.74, 14.62) * mm});
            skLineSegment(sketch, "E426", {"start": v(19.74, 14.62) * mm, "end": v(19.78, 14.67) * mm});
            skLineSegment(sketch, "E427", {"start": v(19.78, 14.67) * mm, "end": v(19.82, 14.72) * mm});
            skLineSegment(sketch, "E428", {"start": v(19.82, 14.72) * mm, "end": v(19.86, 14.78) * mm});
            skLineSegment(sketch, "E429", {"start": v(19.86, 14.78) * mm, "end": v(19.9, 14.83) * mm});
            skLineSegment(sketch, "E430", {"start": v(19.9, 14.83) * mm, "end": v(19.94, 14.9) * mm});
            skLineSegment(sketch, "E431", {"start": v(19.94, 14.9) * mm, "end": v(19.98, 14.95) * mm});
            skLineSegment(sketch, "E432", {"start": v(19.98, 14.95) * mm, "end": v(20.02, 15.01) * mm});
            skLineSegment(sketch, "E433", {"start": v(20.02, 15.01) * mm, "end": v(20.06, 15.08) * mm});
            skLineSegment(sketch, "E434", {"start": v(20.06, 15.08) * mm, "end": v(20.1, 15.14) * mm});
            skLineSegment(sketch, "E435", {"start": v(20.1, 15.14) * mm, "end": v(20.14, 15.21) * mm});
            skLineSegment(sketch, "E436", {"start": v(20.14, 15.21) * mm, "end": v(20.18, 15.28) * mm});
            skLineSegment(sketch, "E437", {"start": v(20.18, 15.28) * mm, "end": v(20.23, 15.35) * mm});
            skLineSegment(sketch, "E438", {"start": v(20.23, 15.35) * mm, "end": v(20.27, 15.42) * mm});
            skLineSegment(sketch, "E439", {"start": v(20.27, 15.42) * mm, "end": v(20.31, 15.5) * mm});
            skLineSegment(sketch, "E440", {"start": v(20.31, 15.5) * mm, "end": v(20.35, 15.58) * mm});
            skLineSegment(sketch, "E441", {"start": v(20.35, 15.58) * mm, "end": v(20.4, 15.66) * mm});
            skLineSegment(sketch, "E442", {"start": v(20.4, 15.66) * mm, "end": v(20.44, 15.74) * mm});
            skLineSegment(sketch, "E443", {"start": v(20.44, 15.74) * mm, "end": v(20.49, 15.82) * mm});
            skLineSegment(sketch, "E444", {"start": v(20.49, 15.82) * mm, "end": v(20.53, 15.9) * mm});
            skLineSegment(sketch, "E445", {"start": v(20.53, 15.9) * mm, "end": v(20.57, 16) * mm});
            skLineSegment(sketch, "E446", {"start": v(20.57, 16) * mm, "end": v(20.62, 16.08) * mm});
            skLineSegment(sketch, "E447", {"start": v(20.62, 16.08) * mm, "end": v(20.66, 16.17) * mm});
            skLineSegment(sketch, "E448", {"start": v(20.66, 16.17) * mm, "end": v(20.64, 16.22) * mm});
            skLineSegment(sketch, "E449", {"start": v(20.64, 16.22) * mm, "end": v(20.12, 16.86) * mm});
            skLineSegment(sketch, "E450", {"start": v(20.12, 16.86) * mm, "end": v(20.08, 16.9) * mm});
            skLineSegment(sketch, "E451", {"start": v(20.08, 16.9) * mm, "end": v(19.98, 16.87) * mm});
            skLineSegment(sketch, "E452", {"start": v(19.98, 16.87) * mm, "end": v(19.88, 16.84) * mm});
            skLineSegment(sketch, "E453", {"start": v(19.88, 16.84) * mm, "end": v(19.79, 16.82) * mm});
            skLineSegment(sketch, "E454", {"start": v(19.79, 16.82) * mm, "end": v(19.7, 16.8) * mm});
            skLineSegment(sketch, "E455", {"start": v(19.7, 16.8) * mm, "end": v(19.6, 16.77) * mm});
            skLineSegment(sketch, "E456", {"start": v(19.6, 16.77) * mm, "end": v(19.52, 16.74) * mm});
            skLineSegment(sketch, "E457", {"start": v(19.52, 16.74) * mm, "end": v(19.43, 16.71) * mm});
            skLineSegment(sketch, "E458", {"start": v(19.43, 16.71) * mm, "end": v(19.35, 16.69) * mm});
            skLineSegment(sketch, "E459", {"start": v(19.35, 16.69) * mm, "end": v(19.26, 16.66) * mm});
            skLineSegment(sketch, "E460", {"start": v(19.26, 16.66) * mm, "end": v(19.18, 16.63) * mm});
            skLineSegment(sketch, "E461", {"start": v(19.18, 16.63) * mm, "end": v(19.1, 16.6) * mm});
            skLineSegment(sketch, "E462", {"start": v(19.1, 16.6) * mm, "end": v(19.03, 16.58) * mm});
            skLineSegment(sketch, "E463", {"start": v(19.03, 16.58) * mm, "end": v(18.95, 16.55) * mm});
            skLineSegment(sketch, "E464", {"start": v(18.95, 16.55) * mm, "end": v(18.88, 16.53) * mm});
            skLineSegment(sketch, "E465", {"start": v(18.88, 16.53) * mm, "end": v(18.8, 16.5) * mm});
            skLineSegment(sketch, "E466", {"start": v(18.8, 16.5) * mm, "end": v(18.74, 16.47) * mm});
            skLineSegment(sketch, "E467", {"start": v(18.74, 16.47) * mm, "end": v(18.67, 16.44) * mm});
            skLineSegment(sketch, "E468", {"start": v(18.67, 16.44) * mm, "end": v(18.6, 16.42) * mm});
            skLineSegment(sketch, "E469", {"start": v(18.6, 16.42) * mm, "end": v(18.54, 16.4) * mm});
            skLineSegment(sketch, "E470", {"start": v(18.54, 16.4) * mm, "end": v(18.48, 16.36) * mm});
            skLineSegment(sketch, "E471", {"start": v(18.48, 16.36) * mm, "end": v(18.42, 16.34) * mm});
            skLineSegment(sketch, "E472", {"start": v(18.42, 16.34) * mm, "end": v(18.37, 16.31) * mm});
            skLineSegment(sketch, "E473", {"start": v(18.37, 16.31) * mm, "end": v(18.3, 16.29) * mm});
            skLineSegment(sketch, "E474", {"start": v(18.3, 16.29) * mm, "end": v(18.26, 16.26) * mm});
            skLineSegment(sketch, "E475", {"start": v(18.26, 16.26) * mm, "end": v(18.2, 16.23) * mm});
            skLineSegment(sketch, "E476", {"start": v(18.2, 16.23) * mm, "end": v(18.15, 16.2) * mm});
            skLineSegment(sketch, "E477", {"start": v(18.15, 16.2) * mm, "end": v(18.1, 16.19) * mm});
            skLineSegment(sketch, "E478", {"start": v(18.1, 16.19) * mm, "end": v(18.06, 16.16) * mm});
            skLineSegment(sketch, "E479", {"start": v(18.06, 16.16) * mm, "end": v(18.01, 16.14) * mm});
            skLineSegment(sketch, "E480", {"start": v(18.01, 16.14) * mm, "end": v(17.97, 16.11) * mm});
            skLineSegment(sketch, "E481", {"start": v(17.97, 16.11) * mm, "end": v(17.93, 16.1) * mm});
            skLineSegment(sketch, "E482", {"start": v(17.93, 16.1) * mm, "end": v(17.89, 16.07) * mm});
            skLineSegment(sketch, "E483", {"start": v(17.89, 16.07) * mm, "end": v(17.85, 16.05) * mm});
            skLineSegment(sketch, "E484", {"start": v(17.85, 16.05) * mm, "end": v(17.81, 16.03) * mm});
            skLineSegment(sketch, "E485", {"start": v(17.81, 16.03) * mm, "end": v(17.78, 16) * mm});
            skLineSegment(sketch, "E486", {"start": v(17.78, 16) * mm, "end": v(17.75, 15.98) * mm});
            skLineSegment(sketch, "E487", {"start": v(17.75, 15.98) * mm, "end": v(17.71, 15.97) * mm});
            skLineSegment(sketch, "E488", {"start": v(17.71, 15.97) * mm, "end": v(17.69, 15.95) * mm});
            skLineSegment(sketch, "E489", {"start": v(17.69, 15.95) * mm, "end": v(17.66, 15.93) * mm});
            skLineSegment(sketch, "E490", {"start": v(17.66, 15.93) * mm, "end": v(17.63, 15.91) * mm});
            skLineSegment(sketch, "E491", {"start": v(17.63, 15.91) * mm, "end": v(17.6, 15.9) * mm});
            skLineSegment(sketch, "E492", {"start": v(17.6, 15.9) * mm, "end": v(17.58, 15.88) * mm});
            skLineSegment(sketch, "E493", {"start": v(17.58, 15.88) * mm, "end": v(17.56, 15.86) * mm});
            skLineSegment(sketch, "E494", {"start": v(17.56, 15.86) * mm, "end": v(17.54, 15.85) * mm});
            skLineSegment(sketch, "E495", {"start": v(17.54, 15.85) * mm, "end": v(17.52, 15.84) * mm});
            skLineSegment(sketch, "E496", {"start": v(17.52, 15.84) * mm, "end": v(17.5, 15.83) * mm});
            skLineSegment(sketch, "E497", {"start": v(17.5, 15.83) * mm, "end": v(17.5, 15.81) * mm});
            skLineSegment(sketch, "E498", {"start": v(17.5, 15.81) * mm, "end": v(17.48, 15.8) * mm});
            skLineSegment(sketch, "E499", {"start": v(17.48, 15.8) * mm, "end": v(16.66, 16.66) * mm});
            skLineSegment(sketch, "E500", {"start": v(16.66, 16.66) * mm, "end": v(16.67, 16.68) * mm});
            skLineSegment(sketch, "E501", {"start": v(16.67, 16.68) * mm, "end": v(16.68, 16.7) * mm});
            skLineSegment(sketch, "E502", {"start": v(16.68, 16.7) * mm, "end": v(16.7, 16.7) * mm});
            skLineSegment(sketch, "E503", {"start": v(16.7, 16.7) * mm, "end": v(16.71, 16.73) * mm});
            skLineSegment(sketch, "E504", {"start": v(16.71, 16.73) * mm, "end": v(16.73, 16.75) * mm});
            skLineSegment(sketch, "E505", {"start": v(16.73, 16.75) * mm, "end": v(16.74, 16.77) * mm});
            skLineSegment(sketch, "E506", {"start": v(16.74, 16.77) * mm, "end": v(16.76, 16.79) * mm});
            skLineSegment(sketch, "E507", {"start": v(16.76, 16.79) * mm, "end": v(16.78, 16.81) * mm});
            skLineSegment(sketch, "E508", {"start": v(16.78, 16.81) * mm, "end": v(16.8, 16.84) * mm});
            skLineSegment(sketch, "E509", {"start": v(16.8, 16.84) * mm, "end": v(16.81, 16.86) * mm});
            skLineSegment(sketch, "E510", {"start": v(16.81, 16.86) * mm, "end": v(16.83, 16.9) * mm});
            skLineSegment(sketch, "E511", {"start": v(16.83, 16.9) * mm, "end": v(16.85, 16.92) * mm});
            skLineSegment(sketch, "E512", {"start": v(16.85, 16.92) * mm, "end": v(16.88, 16.95) * mm});
            skLineSegment(sketch, "E513", {"start": v(16.88, 16.95) * mm, "end": v(16.9, 16.99) * mm});
            skLineSegment(sketch, "E514", {"start": v(16.9, 16.99) * mm, "end": v(16.92, 17.02) * mm});
            skLineSegment(sketch, "E515", {"start": v(16.92, 17.02) * mm, "end": v(16.95, 17.06) * mm});
            skLineSegment(sketch, "E516", {"start": v(16.95, 17.06) * mm, "end": v(16.97, 17.1) * mm});
            skLineSegment(sketch, "E517", {"start": v(16.97, 17.1) * mm, "end": v(17, 17.14) * mm});
            skLineSegment(sketch, "E518", {"start": v(17, 17.14) * mm, "end": v(17.02, 17.18) * mm});
            skLineSegment(sketch, "E519", {"start": v(17.02, 17.18) * mm, "end": v(17.05, 17.22) * mm});
            skLineSegment(sketch, "E520", {"start": v(17.05, 17.22) * mm, "end": v(17.07, 17.27) * mm});
            skLineSegment(sketch, "E521", {"start": v(17.07, 17.27) * mm, "end": v(17.1, 17.32) * mm});
            skLineSegment(sketch, "E522", {"start": v(17.1, 17.32) * mm, "end": v(17.13, 17.37) * mm});
            skLineSegment(sketch, "E523", {"start": v(17.13, 17.37) * mm, "end": v(17.16, 17.42) * mm});
            skLineSegment(sketch, "E524", {"start": v(17.16, 17.42) * mm, "end": v(17.18, 17.47) * mm});
            skLineSegment(sketch, "E525", {"start": v(17.18, 17.47) * mm, "end": v(17.21, 17.52) * mm});
            skLineSegment(sketch, "E526", {"start": v(17.21, 17.52) * mm, "end": v(17.24, 17.58) * mm});
            skLineSegment(sketch, "E527", {"start": v(17.24, 17.58) * mm, "end": v(17.27, 17.64) * mm});
            skLineSegment(sketch, "E528", {"start": v(17.27, 17.64) * mm, "end": v(17.3, 17.7) * mm});
            skLineSegment(sketch, "E529", {"start": v(17.3, 17.7) * mm, "end": v(17.33, 17.76) * mm});
            skLineSegment(sketch, "E530", {"start": v(17.33, 17.76) * mm, "end": v(17.36, 17.83) * mm});
            skLineSegment(sketch, "E531", {"start": v(17.36, 17.83) * mm, "end": v(17.4, 17.9) * mm});
            skLineSegment(sketch, "E532", {"start": v(17.4, 17.9) * mm, "end": v(17.42, 17.96) * mm});
            skLineSegment(sketch, "E533", {"start": v(17.42, 17.96) * mm, "end": v(17.45, 18.03) * mm});
            skLineSegment(sketch, "E534", {"start": v(17.45, 18.03) * mm, "end": v(17.48, 18.1) * mm});
            skLineSegment(sketch, "E535", {"start": v(17.48, 18.1) * mm, "end": v(17.51, 18.17) * mm});
            skLineSegment(sketch, "E536", {"start": v(17.51, 18.17) * mm, "end": v(17.54, 18.25) * mm});
            skLineSegment(sketch, "E537", {"start": v(17.54, 18.25) * mm, "end": v(17.57, 18.33) * mm});
            skLineSegment(sketch, "E538", {"start": v(17.57, 18.33) * mm, "end": v(17.6, 18.4) * mm});
            skLineSegment(sketch, "E539", {"start": v(17.6, 18.4) * mm, "end": v(17.64, 18.49) * mm});
            skLineSegment(sketch, "E540", {"start": v(17.64, 18.49) * mm, "end": v(17.67, 18.57) * mm});
            skLineSegment(sketch, "E541", {"start": v(17.67, 18.57) * mm, "end": v(17.7, 18.65) * mm});
            skLineSegment(sketch, "E542", {"start": v(17.7, 18.65) * mm, "end": v(17.73, 18.74) * mm});
            skLineSegment(sketch, "E543", {"start": v(17.73, 18.74) * mm, "end": v(17.76, 18.83) * mm});
            skLineSegment(sketch, "E544", {"start": v(17.76, 18.83) * mm, "end": v(17.79, 18.92) * mm});
            skLineSegment(sketch, "E545", {"start": v(17.79, 18.92) * mm, "end": v(17.82, 19.01) * mm});
            skLineSegment(sketch, "E546", {"start": v(17.82, 19.01) * mm, "end": v(17.85, 19.1) * mm});
            skLineSegment(sketch, "E547", {"start": v(17.85, 19.1) * mm, "end": v(17.88, 19.2) * mm});
            skLineSegment(sketch, "E548", {"start": v(17.88, 19.2) * mm, "end": v(17.85, 19.25) * mm});
            skLineSegment(sketch, "E549", {"start": v(17.85, 19.25) * mm, "end": v(17.23, 19.8) * mm});
            skLineSegment(sketch, "E550", {"start": v(17.23, 19.8) * mm, "end": v(17.19, 19.82) * mm});
            skLineSegment(sketch, "E551", {"start": v(17.19, 19.82) * mm, "end": v(17.1, 19.78) * mm});
            skLineSegment(sketch, "E552", {"start": v(17.1, 19.78) * mm, "end": v(17, 19.75) * mm});
            skLineSegment(sketch, "E553", {"start": v(17, 19.75) * mm, "end": v(16.92, 19.7) * mm});
            skLineSegment(sketch, "E554", {"start": v(16.92, 19.7) * mm, "end": v(16.83, 19.67) * mm});
            skLineSegment(sketch, "E555", {"start": v(16.83, 19.67) * mm, "end": v(16.74, 19.63) * mm});
            skLineSegment(sketch, "E556", {"start": v(16.74, 19.63) * mm, "end": v(16.66, 19.59) * mm});
            skLineSegment(sketch, "E557", {"start": v(16.66, 19.59) * mm, "end": v(16.58, 19.55) * mm});
            skLineSegment(sketch, "E558", {"start": v(16.58, 19.55) * mm, "end": v(16.5, 19.5) * mm});
            skLineSegment(sketch, "E559", {"start": v(16.5, 19.5) * mm, "end": v(16.42, 19.47) * mm});
            skLineSegment(sketch, "E560", {"start": v(16.42, 19.47) * mm, "end": v(16.35, 19.43) * mm});
            skLineSegment(sketch, "E561", {"start": v(16.35, 19.43) * mm, "end": v(16.27, 19.4) * mm});
            skLineSegment(sketch, "E562", {"start": v(16.27, 19.4) * mm, "end": v(16.2, 19.35) * mm});
            skLineSegment(sketch, "E563", {"start": v(16.2, 19.35) * mm, "end": v(16.13, 19.31) * mm});
            skLineSegment(sketch, "E564", {"start": v(16.13, 19.31) * mm, "end": v(16.06, 19.28) * mm});
            skLineSegment(sketch, "E565", {"start": v(16.06, 19.28) * mm, "end": v(16, 19.24) * mm});
            skLineSegment(sketch, "E566", {"start": v(16, 19.24) * mm, "end": v(15.93, 19.2) * mm});
            skLineSegment(sketch, "E567", {"start": v(15.93, 19.2) * mm, "end": v(15.87, 19.16) * mm});
            skLineSegment(sketch, "E568", {"start": v(15.87, 19.16) * mm, "end": v(15.81, 19.13) * mm});
            skLineSegment(sketch, "E569", {"start": v(15.81, 19.13) * mm, "end": v(15.75, 19.1) * mm});
            skLineSegment(sketch, "E570", {"start": v(15.75, 19.1) * mm, "end": v(15.7, 19.05) * mm});
            skLineSegment(sketch, "E571", {"start": v(15.7, 19.05) * mm, "end": v(15.64, 19.02) * mm});
            skLineSegment(sketch, "E572", {"start": v(15.64, 19.02) * mm, "end": v(15.59, 18.98) * mm});
            skLineSegment(sketch, "E573", {"start": v(15.59, 18.98) * mm, "end": v(15.54, 18.95) * mm});
            skLineSegment(sketch, "E574", {"start": v(15.54, 18.95) * mm, "end": v(15.49, 18.92) * mm});
            skLineSegment(sketch, "E575", {"start": v(15.49, 18.92) * mm, "end": v(15.44, 18.88) * mm});
            skLineSegment(sketch, "E576", {"start": v(15.44, 18.88) * mm, "end": v(15.4, 18.85) * mm});
            skLineSegment(sketch, "E577", {"start": v(15.4, 18.85) * mm, "end": v(15.35, 18.82) * mm});
            skLineSegment(sketch, "E578", {"start": v(15.35, 18.82) * mm, "end": v(15.3, 18.79) * mm});
            skLineSegment(sketch, "E579", {"start": v(15.3, 18.79) * mm, "end": v(15.27, 18.76) * mm});
            skLineSegment(sketch, "E580", {"start": v(15.27, 18.76) * mm, "end": v(15.23, 18.73) * mm});
            skLineSegment(sketch, "E581", {"start": v(15.23, 18.73) * mm, "end": v(15.19, 18.7) * mm});
            skLineSegment(sketch, "E582", {"start": v(15.19, 18.7) * mm, "end": v(15.15, 18.67) * mm});
            skLineSegment(sketch, "E583", {"start": v(15.15, 18.67) * mm, "end": v(15.12, 18.64) * mm});
            skLineSegment(sketch, "E584", {"start": v(15.12, 18.64) * mm, "end": v(15.09, 18.61) * mm});
            skLineSegment(sketch, "E585", {"start": v(15.09, 18.61) * mm, "end": v(15.06, 18.59) * mm});
            skLineSegment(sketch, "E586", {"start": v(15.06, 18.59) * mm, "end": v(15.03, 18.56) * mm});
            skLineSegment(sketch, "E587", {"start": v(15.03, 18.56) * mm, "end": v(15, 18.54) * mm});
            skLineSegment(sketch, "E588", {"start": v(15, 18.54) * mm, "end": v(14.97, 18.52) * mm});
            skLineSegment(sketch, "E589", {"start": v(14.97, 18.52) * mm, "end": v(14.95, 18.5) * mm});
            skLineSegment(sketch, "E590", {"start": v(14.95, 18.5) * mm, "end": v(14.93, 18.47) * mm});
            skLineSegment(sketch, "E591", {"start": v(14.93, 18.47) * mm, "end": v(14.9, 18.45) * mm});
            skLineSegment(sketch, "E592", {"start": v(14.9, 18.45) * mm, "end": v(14.88, 18.43) * mm});
            skLineSegment(sketch, "E593", {"start": v(14.88, 18.43) * mm, "end": v(14.86, 18.42) * mm});
            skLineSegment(sketch, "E594", {"start": v(14.86, 18.42) * mm, "end": v(14.85, 18.4) * mm});
            skLineSegment(sketch, "E595", {"start": v(14.85, 18.4) * mm, "end": v(14.83, 18.38) * mm});
            skLineSegment(sketch, "E596", {"start": v(14.83, 18.38) * mm, "end": v(14.82, 18.37) * mm});
            skLineSegment(sketch, "E597", {"start": v(14.82, 18.37) * mm, "end": v(14.8, 18.36) * mm});
            skLineSegment(sketch, "E598", {"start": v(14.8, 18.36) * mm, "end": v(14.79, 18.34) * mm});
            skLineSegment(sketch, "E599", {"start": v(14.79, 18.34) * mm, "end": v(13.85, 19.06) * mm});
            skLineSegment(sketch, "E600", {"start": v(13.85, 19.06) * mm, "end": v(13.86, 19.08) * mm});
            skLineSegment(sketch, "E601", {"start": v(13.86, 19.08) * mm, "end": v(13.87, 19.1) * mm});
            skLineSegment(sketch, "E602", {"start": v(13.87, 19.1) * mm, "end": v(13.88, 19.11) * mm});
            skLineSegment(sketch, "E603", {"start": v(13.88, 19.11) * mm, "end": v(13.89, 19.13) * mm});
            skLineSegment(sketch, "E604", {"start": v(13.89, 19.13) * mm, "end": v(13.9, 19.16) * mm});
            skLineSegment(sketch, "E605", {"start": v(13.9, 19.16) * mm, "end": v(13.91, 19.18) * mm});
            skLineSegment(sketch, "E606", {"start": v(13.91, 19.18) * mm, "end": v(13.93, 19.2) * mm});
            skLineSegment(sketch, "E607", {"start": v(13.93, 19.2) * mm, "end": v(13.94, 19.23) * mm});
            skLineSegment(sketch, "E608", {"start": v(13.94, 19.23) * mm, "end": v(13.95, 19.26) * mm});
            skLineSegment(sketch, "E609", {"start": v(13.95, 19.26) * mm, "end": v(13.97, 19.29) * mm});
            skLineSegment(sketch, "E610", {"start": v(13.97, 19.29) * mm, "end": v(13.98, 19.32) * mm});
            skLineSegment(sketch, "E611", {"start": v(13.98, 19.32) * mm, "end": v(14, 19.35) * mm});
            skLineSegment(sketch, "E612", {"start": v(14, 19.35) * mm, "end": v(14.02, 19.39) * mm});
            skLineSegment(sketch, "E613", {"start": v(14.02, 19.39) * mm, "end": v(14.03, 19.42) * mm});
            skLineSegment(sketch, "E614", {"start": v(14.03, 19.42) * mm, "end": v(14.05, 19.46) * mm});
            skLineSegment(sketch, "E615", {"start": v(14.05, 19.46) * mm, "end": v(14.07, 19.5) * mm});
            skLineSegment(sketch, "E616", {"start": v(14.07, 19.5) * mm, "end": v(14.09, 19.54) * mm});
            skLineSegment(sketch, "E617", {"start": v(14.09, 19.54) * mm, "end": v(14.1, 19.59) * mm});
            skLineSegment(sketch, "E618", {"start": v(14.1, 19.59) * mm, "end": v(14.12, 19.63) * mm});
            skLineSegment(sketch, "E619", {"start": v(14.12, 19.63) * mm, "end": v(14.14, 19.68) * mm});
            skLineSegment(sketch, "E620", {"start": v(14.14, 19.68) * mm, "end": v(14.16, 19.73) * mm});
            skLineSegment(sketch, "E621", {"start": v(14.16, 19.73) * mm, "end": v(14.18, 19.78) * mm});
            skLineSegment(sketch, "E622", {"start": v(14.18, 19.78) * mm, "end": v(14.2, 19.83) * mm});
            skLineSegment(sketch, "E623", {"start": v(14.2, 19.83) * mm, "end": v(14.22, 19.89) * mm});
            skLineSegment(sketch, "E624", {"start": v(14.22, 19.89) * mm, "end": v(14.24, 19.94) * mm});
            skLineSegment(sketch, "E625", {"start": v(14.24, 19.94) * mm, "end": v(14.26, 20) * mm});
            skLineSegment(sketch, "E626", {"start": v(14.26, 20) * mm, "end": v(14.28, 20.06) * mm});
            skLineSegment(sketch, "E627", {"start": v(14.28, 20.06) * mm, "end": v(14.3, 20.12) * mm});
            skLineSegment(sketch, "E628", {"start": v(14.3, 20.12) * mm, "end": v(14.32, 20.19) * mm});
            skLineSegment(sketch, "E629", {"start": v(14.32, 20.19) * mm, "end": v(14.34, 20.25) * mm});
            skLineSegment(sketch, "E630", {"start": v(14.34, 20.25) * mm, "end": v(14.36, 20.32) * mm});
            skLineSegment(sketch, "E631", {"start": v(14.36, 20.32) * mm, "end": v(14.38, 20.4) * mm});
            skLineSegment(sketch, "E632", {"start": v(14.38, 20.4) * mm, "end": v(14.4, 20.46) * mm});
            skLineSegment(sketch, "E633", {"start": v(14.4, 20.46) * mm, "end": v(14.42, 20.54) * mm});
            skLineSegment(sketch, "E634", {"start": v(14.42, 20.54) * mm, "end": v(14.44, 20.61) * mm});
            skLineSegment(sketch, "E635", {"start": v(14.44, 20.61) * mm, "end": v(14.45, 20.69) * mm});
            skLineSegment(sketch, "E636", {"start": v(14.45, 20.69) * mm, "end": v(14.47, 20.77) * mm});
            skLineSegment(sketch, "E637", {"start": v(14.47, 20.77) * mm, "end": v(14.5, 20.85) * mm});
            skLineSegment(sketch, "E638", {"start": v(14.5, 20.85) * mm, "end": v(14.5, 20.93) * mm});
            skLineSegment(sketch, "E639", {"start": v(14.5, 20.93) * mm, "end": v(14.53, 21.02) * mm});
            skLineSegment(sketch, "E640", {"start": v(14.53, 21.02) * mm, "end": v(14.54, 21.1) * mm});
            skLineSegment(sketch, "E641", {"start": v(14.54, 21.1) * mm, "end": v(14.56, 21.2) * mm});
            skLineSegment(sketch, "E642", {"start": v(14.56, 21.2) * mm, "end": v(14.58, 21.28) * mm});
            skLineSegment(sketch, "E643", {"start": v(14.58, 21.28) * mm, "end": v(14.6, 21.38) * mm});
            skLineSegment(sketch, "E644", {"start": v(14.6, 21.38) * mm, "end": v(14.6, 21.47) * mm});
            skLineSegment(sketch, "E645", {"start": v(14.6, 21.47) * mm, "end": v(14.62, 21.57) * mm});
            skLineSegment(sketch, "E646", {"start": v(14.62, 21.57) * mm, "end": v(14.64, 21.67) * mm});
            skLineSegment(sketch, "E647", {"start": v(14.64, 21.67) * mm, "end": v(14.65, 21.77) * mm});
            skLineSegment(sketch, "E648", {"start": v(14.65, 21.77) * mm, "end": v(14.62, 21.8) * mm});
            skLineSegment(sketch, "E649", {"start": v(14.62, 21.8) * mm, "end": v(13.92, 22.25) * mm});
            skLineSegment(sketch, "E650", {"start": v(13.92, 22.25) * mm, "end": v(13.88, 22.27) * mm});
            skLineSegment(sketch, "E651", {"start": v(13.88, 22.27) * mm, "end": v(13.79, 22.22) * mm});
            skLineSegment(sketch, "E652", {"start": v(13.79, 22.22) * mm, "end": v(13.7, 22.16) * mm});
            skLineSegment(sketch, "E653", {"start": v(13.7, 22.16) * mm, "end": v(13.62, 22.1) * mm});
            skLineSegment(sketch, "E654", {"start": v(13.62, 22.1) * mm, "end": v(13.54, 22.06) * mm});
            skLineSegment(sketch, "E655", {"start": v(13.54, 22.06) * mm, "end": v(13.47, 22) * mm});
            skLineSegment(sketch, "E656", {"start": v(13.47, 22) * mm, "end": v(13.4, 21.95) * mm});
            skLineSegment(sketch, "E657", {"start": v(13.4, 21.95) * mm, "end": v(13.32, 21.9) * mm});
            skLineSegment(sketch, "E658", {"start": v(13.32, 21.9) * mm, "end": v(13.24, 21.85) * mm});
            skLineSegment(sketch, "E659", {"start": v(13.24, 21.85) * mm, "end": v(13.17, 21.8) * mm});
            skLineSegment(sketch, "E660", {"start": v(13.17, 21.8) * mm, "end": v(13.1, 21.75) * mm});
            skLineSegment(sketch, "E661", {"start": v(13.1, 21.75) * mm, "end": v(13.04, 21.7) * mm});
            skLineSegment(sketch, "E662", {"start": v(13.04, 21.7) * mm, "end": v(12.97, 21.65) * mm});
            skLineSegment(sketch, "E663", {"start": v(12.97, 21.65) * mm, "end": v(12.91, 21.6) * mm});
            skLineSegment(sketch, "E664", {"start": v(12.91, 21.6) * mm, "end": v(12.85, 21.55) * mm});
            skLineSegment(sketch, "E665", {"start": v(12.85, 21.55) * mm, "end": v(12.8, 21.5) * mm});
            skLineSegment(sketch, "E666", {"start": v(12.8, 21.5) * mm, "end": v(12.73, 21.46) * mm});
            skLineSegment(sketch, "E667", {"start": v(12.73, 21.46) * mm, "end": v(12.68, 21.41) * mm});
            skLineSegment(sketch, "E668", {"start": v(12.68, 21.41) * mm, "end": v(12.62, 21.36) * mm});
            skLineSegment(sketch, "E669", {"start": v(12.62, 21.36) * mm, "end": v(12.57, 21.32) * mm});
            skLineSegment(sketch, "E670", {"start": v(12.57, 21.32) * mm, "end": v(12.52, 21.28) * mm});
            skLineSegment(sketch, "E671", {"start": v(12.52, 21.28) * mm, "end": v(12.47, 21.23) * mm});
            skLineSegment(sketch, "E672", {"start": v(12.47, 21.23) * mm, "end": v(12.43, 21.19) * mm});
            skLineSegment(sketch, "E673", {"start": v(12.43, 21.19) * mm, "end": v(12.38, 21.15) * mm});
            skLineSegment(sketch, "E674", {"start": v(12.38, 21.15) * mm, "end": v(12.34, 21.1) * mm});
            skLineSegment(sketch, "E675", {"start": v(12.34, 21.1) * mm, "end": v(12.3, 21.07) * mm});
            skLineSegment(sketch, "E676", {"start": v(12.3, 21.07) * mm, "end": v(12.26, 21.03) * mm});
            skLineSegment(sketch, "E677", {"start": v(12.26, 21.03) * mm, "end": v(12.22, 20.99) * mm});
            skLineSegment(sketch, "E678", {"start": v(12.22, 20.99) * mm, "end": v(12.18, 20.95) * mm});
            skLineSegment(sketch, "E679", {"start": v(12.18, 20.95) * mm, "end": v(12.14, 20.91) * mm});
            skLineSegment(sketch, "E680", {"start": v(12.14, 20.91) * mm, "end": v(12.1, 20.88) * mm});
            skLineSegment(sketch, "E681", {"start": v(12.1, 20.88) * mm, "end": v(12.08, 20.84) * mm});
            skLineSegment(sketch, "E682", {"start": v(12.08, 20.84) * mm, "end": v(12.05, 20.8) * mm});
            skLineSegment(sketch, "E683", {"start": v(12.05, 20.8) * mm, "end": v(12.02, 20.78) * mm});
            skLineSegment(sketch, "E684", {"start": v(12.02, 20.78) * mm, "end": v(11.99, 20.75) * mm});
            skLineSegment(sketch, "E685", {"start": v(11.99, 20.75) * mm, "end": v(11.96, 20.72) * mm});
            skLineSegment(sketch, "E686", {"start": v(11.96, 20.72) * mm, "end": v(11.94, 20.69) * mm});
            skLineSegment(sketch, "E687", {"start": v(11.94, 20.69) * mm, "end": v(11.91, 20.66) * mm});
            skLineSegment(sketch, "E688", {"start": v(11.91, 20.66) * mm, "end": v(11.9, 20.63) * mm});
            skLineSegment(sketch, "E689", {"start": v(11.9, 20.63) * mm, "end": v(11.87, 20.6) * mm});
            skLineSegment(sketch, "E690", {"start": v(11.87, 20.6) * mm, "end": v(11.85, 20.58) * mm});
            skLineSegment(sketch, "E691", {"start": v(11.85, 20.58) * mm, "end": v(11.83, 20.56) * mm});
            skLineSegment(sketch, "E692", {"start": v(11.83, 20.56) * mm, "end": v(11.82, 20.54) * mm});
            skLineSegment(sketch, "E693", {"start": v(11.82, 20.54) * mm, "end": v(11.8, 20.52) * mm});
            skLineSegment(sketch, "E694", {"start": v(11.8, 20.52) * mm, "end": v(11.79, 20.5) * mm});
            skLineSegment(sketch, "E695", {"start": v(11.79, 20.5) * mm, "end": v(11.77, 20.48) * mm});
            skLineSegment(sketch, "E696", {"start": v(11.77, 20.48) * mm, "end": v(11.76, 20.46) * mm});
            skLineSegment(sketch, "E697", {"start": v(11.76, 20.46) * mm, "end": v(11.75, 20.45) * mm});
            skLineSegment(sketch, "E698", {"start": v(11.75, 20.45) * mm, "end": v(11.74, 20.43) * mm});
            skLineSegment(sketch, "E699", {"start": v(11.74, 20.43) * mm, "end": v(10.7, 21) * mm});
            skLineSegment(sketch, "E700", {"start": v(10.7, 21) * mm, "end": v(10.7, 21.01) * mm});
            skLineSegment(sketch, "E701", {"start": v(10.7, 21.01) * mm, "end": v(10.7, 21.03) * mm});
            skLineSegment(sketch, "E702", {"start": v(10.7, 21.03) * mm, "end": v(10.72, 21.05) * mm});
            skLineSegment(sketch, "E703", {"start": v(10.72, 21.05) * mm, "end": v(10.72, 21.07) * mm});
            skLineSegment(sketch, "E704", {"start": v(10.72, 21.07) * mm, "end": v(10.73, 21.1) * mm});
            skLineSegment(sketch, "E705", {"start": v(10.73, 21.1) * mm, "end": v(10.74, 21.12) * mm});
            skLineSegment(sketch, "E706", {"start": v(10.74, 21.12) * mm, "end": v(10.75, 21.14) * mm});
            skLineSegment(sketch, "E707", {"start": v(10.75, 21.14) * mm, "end": v(10.76, 21.17) * mm});
            skLineSegment(sketch, "E708", {"start": v(10.76, 21.17) * mm, "end": v(10.77, 21.2) * mm});
            skLineSegment(sketch, "E709", {"start": v(10.77, 21.2) * mm, "end": v(10.78, 21.23) * mm});
            skLineSegment(sketch, "E710", {"start": v(10.78, 21.23) * mm, "end": v(10.79, 21.27) * mm});
            skLineSegment(sketch, "E711", {"start": v(10.79, 21.27) * mm, "end": v(10.8, 21.3) * mm});
            skLineSegment(sketch, "E712", {"start": v(10.8, 21.3) * mm, "end": v(10.81, 21.34) * mm});
            skLineSegment(sketch, "E713", {"start": v(10.81, 21.34) * mm, "end": v(10.82, 21.38) * mm});
            skLineSegment(sketch, "E714", {"start": v(10.82, 21.38) * mm, "end": v(10.83, 21.42) * mm});
            skLineSegment(sketch, "E715", {"start": v(10.83, 21.42) * mm, "end": v(10.84, 21.46) * mm});
            skLineSegment(sketch, "E716", {"start": v(10.84, 21.46) * mm, "end": v(10.86, 21.5) * mm});
            skLineSegment(sketch, "E717", {"start": v(10.86, 21.5) * mm, "end": v(10.87, 21.55) * mm});
            skLineSegment(sketch, "E718", {"start": v(10.87, 21.55) * mm, "end": v(10.88, 21.6) * mm});
            skLineSegment(sketch, "E719", {"start": v(10.88, 21.6) * mm, "end": v(10.89, 21.65) * mm});
            skLineSegment(sketch, "E720", {"start": v(10.89, 21.65) * mm, "end": v(10.9, 21.7) * mm});
            skLineSegment(sketch, "E721", {"start": v(10.9, 21.7) * mm, "end": v(10.91, 21.75) * mm});
            skLineSegment(sketch, "E722", {"start": v(10.91, 21.75) * mm, "end": v(10.92, 21.8) * mm});
            skLineSegment(sketch, "E723", {"start": v(10.92, 21.8) * mm, "end": v(10.93, 21.87) * mm});
            skLineSegment(sketch, "E724", {"start": v(10.93, 21.87) * mm, "end": v(10.94, 21.93) * mm});
            skLineSegment(sketch, "E725", {"start": v(10.94, 21.93) * mm, "end": v(10.95, 21.99) * mm});
            skLineSegment(sketch, "E726", {"start": v(10.95, 21.99) * mm, "end": v(10.96, 22.05) * mm});
            skLineSegment(sketch, "E727", {"start": v(10.96, 22.05) * mm, "end": v(10.97, 22.11) * mm});
            skLineSegment(sketch, "E728", {"start": v(10.97, 22.11) * mm, "end": v(10.98, 22.18) * mm});
            skLineSegment(sketch, "E729", {"start": v(10.98, 22.18) * mm, "end": v(11, 22.25) * mm});
            skLineSegment(sketch, "E730", {"start": v(11, 22.25) * mm, "end": v(11, 22.32) * mm});
            skLineSegment(sketch, "E731", {"start": v(11, 22.32) * mm, "end": v(11.01, 22.39) * mm});
            skLineSegment(sketch, "E732", {"start": v(11.01, 22.39) * mm, "end": v(11.02, 22.46) * mm});
            skLineSegment(sketch, "E733", {"start": v(11.02, 22.46) * mm, "end": v(11.03, 22.54) * mm});
            skLineSegment(sketch, "E734", {"start": v(11.03, 22.54) * mm, "end": v(11.03, 22.62) * mm});
            skLineSegment(sketch, "E735", {"start": v(11.03, 22.62) * mm, "end": v(11.04, 22.7) * mm});
            skLineSegment(sketch, "E736", {"start": v(11.04, 22.7) * mm, "end": v(11.05, 22.78) * mm});
            skLineSegment(sketch, "E737", {"start": v(11.05, 22.78) * mm, "end": v(11.05, 22.86) * mm});
            skLineSegment(sketch, "E738", {"start": v(11.05, 22.86) * mm, "end": v(11.06, 22.95) * mm});
            skLineSegment(sketch, "E739", {"start": v(11.06, 22.95) * mm, "end": v(11.06, 23.03) * mm});
            skLineSegment(sketch, "E740", {"start": v(11.06, 23.03) * mm, "end": v(11.06, 23.12) * mm});
            skLineSegment(sketch, "E741", {"start": v(11.06, 23.12) * mm, "end": v(11.07, 23.21) * mm});
            skLineSegment(sketch, "E742", {"start": v(11.07, 23.21) * mm, "end": v(11.07, 23.3) * mm});
            skLineSegment(sketch, "E743", {"start": v(11.07, 23.3) * mm, "end": v(11.07, 23.4) * mm});
            skLineSegment(sketch, "E744", {"start": v(11.07, 23.4) * mm, "end": v(11.07, 23.5) * mm});
            skLineSegment(sketch, "E745", {"start": v(11.07, 23.5) * mm, "end": v(11.07, 23.59) * mm});
            skLineSegment(sketch, "E746", {"start": v(11.07, 23.59) * mm, "end": v(11.07, 23.69) * mm});
            skLineSegment(sketch, "E747", {"start": v(11.07, 23.69) * mm, "end": v(11.07, 23.8) * mm});
            skLineSegment(sketch, "E748", {"start": v(11.07, 23.8) * mm, "end": v(11.03, 23.82) * mm});
            skLineSegment(sketch, "E749", {"start": v(11.03, 23.82) * mm, "end": v(10.27, 24.16) * mm});
            skLineSegment(sketch, "E750", {"start": v(10.27, 24.16) * mm, "end": v(10.22, 24.17) * mm});
            skLineSegment(sketch, "E751", {"start": v(10.22, 24.17) * mm, "end": v(10.14, 24.1) * mm});
            skLineSegment(sketch, "E752", {"start": v(10.14, 24.1) * mm, "end": v(10.07, 24.03) * mm});
            skLineSegment(sketch, "E753", {"start": v(10.07, 24.03) * mm, "end": v(10, 23.97) * mm});
            skLineSegment(sketch, "E754", {"start": v(10, 23.97) * mm, "end": v(9.93, 23.9) * mm});
            skLineSegment(sketch, "E755", {"start": v(9.93, 23.9) * mm, "end": v(9.86, 23.84) * mm});
            skLineSegment(sketch, "E756", {"start": v(9.86, 23.84) * mm, "end": v(9.8, 23.78) * mm});
            skLineSegment(sketch, "E757", {"start": v(9.8, 23.78) * mm, "end": v(9.73, 23.71) * mm});
            skLineSegment(sketch, "E758", {"start": v(9.73, 23.71) * mm, "end": v(9.66, 23.65) * mm});
            skLineSegment(sketch, "E759", {"start": v(9.66, 23.65) * mm, "end": v(9.6, 23.6) * mm});
            skLineSegment(sketch, "E760", {"start": v(9.6, 23.6) * mm, "end": v(9.54, 23.53) * mm});
            skLineSegment(sketch, "E761", {"start": v(9.54, 23.53) * mm, "end": v(9.48, 23.47) * mm});
            skLineSegment(sketch, "E762", {"start": v(9.48, 23.47) * mm, "end": v(9.43, 23.41) * mm});
            skLineSegment(sketch, "E763", {"start": v(9.43, 23.41) * mm, "end": v(9.37, 23.35) * mm});
            skLineSegment(sketch, "E764", {"start": v(9.37, 23.35) * mm, "end": v(9.32, 23.3) * mm});
            skLineSegment(sketch, "E765", {"start": v(9.32, 23.3) * mm, "end": v(9.27, 23.24) * mm});
            skLineSegment(sketch, "E766", {"start": v(9.27, 23.24) * mm, "end": v(9.22, 23.18) * mm});
            skLineSegment(sketch, "E767", {"start": v(9.22, 23.18) * mm, "end": v(9.17, 23.13) * mm});
            skLineSegment(sketch, "E768", {"start": v(9.17, 23.13) * mm, "end": v(9.13, 23.08) * mm});
            skLineSegment(sketch, "E769", {"start": v(9.13, 23.08) * mm, "end": v(9.08, 23.02) * mm});
            skLineSegment(sketch, "E770", {"start": v(9.08, 23.02) * mm, "end": v(9.04, 22.97) * mm});
            skLineSegment(sketch, "E771", {"start": v(9.04, 22.97) * mm, "end": v(9, 22.92) * mm});
            skLineSegment(sketch, "E772", {"start": v(9, 22.92) * mm, "end": v(8.96, 22.87) * mm});
            skLineSegment(sketch, "E773", {"start": v(8.96, 22.87) * mm, "end": v(8.92, 22.82) * mm});
            skLineSegment(sketch, "E774", {"start": v(8.92, 22.82) * mm, "end": v(8.88, 22.78) * mm});
            skLineSegment(sketch, "E775", {"start": v(8.88, 22.78) * mm, "end": v(8.85, 22.73) * mm});
            skLineSegment(sketch, "E776", {"start": v(8.85, 22.73) * mm, "end": v(8.82, 22.68) * mm});
            skLineSegment(sketch, "E777", {"start": v(8.82, 22.68) * mm, "end": v(8.78, 22.64) * mm});
            skLineSegment(sketch, "E778", {"start": v(8.78, 22.64) * mm, "end": v(8.75, 22.6) * mm});
            skLineSegment(sketch, "E779", {"start": v(8.75, 22.6) * mm, "end": v(8.72, 22.56) * mm});
            skLineSegment(sketch, "E780", {"start": v(8.72, 22.56) * mm, "end": v(8.7, 22.52) * mm});
            skLineSegment(sketch, "E781", {"start": v(8.7, 22.52) * mm, "end": v(8.67, 22.48) * mm});
            skLineSegment(sketch, "E782", {"start": v(8.67, 22.48) * mm, "end": v(8.64, 22.44) * mm});
            skLineSegment(sketch, "E783", {"start": v(8.64, 22.44) * mm, "end": v(8.62, 22.4) * mm});
            skLineSegment(sketch, "E784", {"start": v(8.62, 22.4) * mm, "end": v(8.6, 22.37) * mm});
            skLineSegment(sketch, "E785", {"start": v(8.6, 22.37) * mm, "end": v(8.57, 22.33) * mm});
            skLineSegment(sketch, "E786", {"start": v(8.57, 22.33) * mm, "end": v(8.55, 22.3) * mm});
            skLineSegment(sketch, "E787", {"start": v(8.55, 22.3) * mm, "end": v(8.54, 22.27) * mm});
            skLineSegment(sketch, "E788", {"start": v(8.54, 22.27) * mm, "end": v(8.52, 22.24) * mm});
            skLineSegment(sketch, "E789", {"start": v(8.52, 22.24) * mm, "end": v(8.5, 22.2) * mm});
            skLineSegment(sketch, "E790", {"start": v(8.5, 22.2) * mm, "end": v(8.49, 22.18) * mm});
            skLineSegment(sketch, "E791", {"start": v(8.49, 22.18) * mm, "end": v(8.47, 22.16) * mm});
            skLineSegment(sketch, "E792", {"start": v(8.47, 22.16) * mm, "end": v(8.46, 22.13) * mm});
            skLineSegment(sketch, "E793", {"start": v(8.46, 22.13) * mm, "end": v(8.45, 22.1) * mm});
            skLineSegment(sketch, "E794", {"start": v(8.45, 22.1) * mm, "end": v(8.43, 22.09) * mm});
            skLineSegment(sketch, "E795", {"start": v(8.43, 22.09) * mm, "end": v(8.42, 22.07) * mm});
            skLineSegment(sketch, "E796", {"start": v(8.42, 22.07) * mm, "end": v(8.42, 22.05) * mm});
            skLineSegment(sketch, "E797", {"start": v(8.42, 22.05) * mm, "end": v(8.4, 22.03) * mm});
            skLineSegment(sketch, "E798", {"start": v(8.4, 22.03) * mm, "end": v(8.4, 22.02) * mm});
            skLineSegment(sketch, "E799", {"start": v(8.4, 22.02) * mm, "end": v(7.28, 22.4) * mm});
            skLineSegment(sketch, "E800", {"start": v(7.28, 22.4) * mm, "end": v(7.28, 22.43) * mm});
            skLineSegment(sketch, "E801", {"start": v(7.28, 22.43) * mm, "end": v(7.29, 22.45) * mm});
            skLineSegment(sketch, "E802", {"start": v(7.29, 22.45) * mm, "end": v(7.3, 22.47) * mm});
            skLineSegment(sketch, "E803", {"start": v(7.3, 22.47) * mm, "end": v(7.3, 22.49) * mm});
            skLineSegment(sketch, "E804", {"start": v(7.3, 22.49) * mm, "end": v(7.3, 22.51) * mm});
            skLineSegment(sketch, "E805", {"start": v(7.3, 22.51) * mm, "end": v(7.3, 22.54) * mm});
            skLineSegment(sketch, "E806", {"start": v(7.3, 22.54) * mm, "end": v(7.3, 22.57) * mm});
            skLineSegment(sketch, "E807", {"start": v(7.3, 22.57) * mm, "end": v(7.31, 22.6) * mm});
            skLineSegment(sketch, "E808", {"start": v(7.31, 22.6) * mm, "end": v(7.32, 22.63) * mm});
            skLineSegment(sketch, "E809", {"start": v(7.32, 22.63) * mm, "end": v(7.32, 22.66) * mm});
            skLineSegment(sketch, "E810", {"start": v(7.32, 22.66) * mm, "end": v(7.33, 22.7) * mm});
            skLineSegment(sketch, "E811", {"start": v(7.33, 22.7) * mm, "end": v(7.33, 22.73) * mm});
            skLineSegment(sketch, "E812", {"start": v(7.33, 22.73) * mm, "end": v(7.34, 22.77) * mm});
            skLineSegment(sketch, "E813", {"start": v(7.34, 22.77) * mm, "end": v(7.34, 22.8) * mm});
            skLineSegment(sketch, "E814", {"start": v(7.34, 22.8) * mm, "end": v(7.35, 22.85) * mm});
            skLineSegment(sketch, "E815", {"start": v(7.35, 22.85) * mm, "end": v(7.35, 22.9) * mm});
            skLineSegment(sketch, "E816", {"start": v(7.35, 22.9) * mm, "end": v(7.36, 22.94) * mm});
            skLineSegment(sketch, "E817", {"start": v(7.36, 22.94) * mm, "end": v(7.36, 22.99) * mm});
            skLineSegment(sketch, "E818", {"start": v(7.36, 22.99) * mm, "end": v(7.37, 23.03) * mm});
            skLineSegment(sketch, "E819", {"start": v(7.37, 23.03) * mm, "end": v(7.37, 23.09) * mm});
            skLineSegment(sketch, "E820", {"start": v(7.37, 23.09) * mm, "end": v(7.37, 23.14) * mm});
            skLineSegment(sketch, "E821", {"start": v(7.37, 23.14) * mm, "end": v(7.37, 23.2) * mm});
            skLineSegment(sketch, "E822", {"start": v(7.37, 23.2) * mm, "end": v(7.38, 23.25) * mm});
            skLineSegment(sketch, "E823", {"start": v(7.38, 23.25) * mm, "end": v(7.38, 23.3) * mm});
            skLineSegment(sketch, "E824", {"start": v(7.38, 23.3) * mm, "end": v(7.38, 23.37) * mm});
            skLineSegment(sketch, "E825", {"start": v(7.38, 23.37) * mm, "end": v(7.38, 23.43) * mm});
            skLineSegment(sketch, "E826", {"start": v(7.38, 23.43) * mm, "end": v(7.38, 23.5) * mm});
            skLineSegment(sketch, "E827", {"start": v(7.38, 23.5) * mm, "end": v(7.38, 23.56) * mm});
            skLineSegment(sketch, "E828", {"start": v(7.38, 23.56) * mm, "end": v(7.38, 23.62) * mm});
            skLineSegment(sketch, "E829", {"start": v(7.38, 23.62) * mm, "end": v(7.38, 23.7) * mm});
            skLineSegment(sketch, "E830", {"start": v(7.38, 23.7) * mm, "end": v(7.38, 23.76) * mm});
            skLineSegment(sketch, "E831", {"start": v(7.38, 23.76) * mm, "end": v(7.37, 23.84) * mm});
            skLineSegment(sketch, "E832", {"start": v(7.37, 23.84) * mm, "end": v(7.37, 23.91) * mm});
            skLineSegment(sketch, "E833", {"start": v(7.37, 23.91) * mm, "end": v(7.36, 23.99) * mm});
            skLineSegment(sketch, "E834", {"start": v(7.36, 23.99) * mm, "end": v(7.36, 24.06) * mm});
            skLineSegment(sketch, "E835", {"start": v(7.36, 24.06) * mm, "end": v(7.35, 24.14) * mm});
            skLineSegment(sketch, "E836", {"start": v(7.35, 24.14) * mm, "end": v(7.35, 24.22) * mm});
            skLineSegment(sketch, "E837", {"start": v(7.35, 24.22) * mm, "end": v(7.34, 24.3) * mm});
            skLineSegment(sketch, "E838", {"start": v(7.34, 24.3) * mm, "end": v(7.33, 24.4) * mm});
            skLineSegment(sketch, "E839", {"start": v(7.33, 24.4) * mm, "end": v(7.32, 24.48) * mm});
            skLineSegment(sketch, "E840", {"start": v(7.32, 24.48) * mm, "end": v(7.31, 24.57) * mm});
            skLineSegment(sketch, "E841", {"start": v(7.31, 24.57) * mm, "end": v(7.3, 24.66) * mm});
            skLineSegment(sketch, "E842", {"start": v(7.3, 24.66) * mm, "end": v(7.29, 24.75) * mm});
            skLineSegment(sketch, "E843", {"start": v(7.29, 24.75) * mm, "end": v(7.27, 24.84) * mm});
            skLineSegment(sketch, "E844", {"start": v(7.27, 24.84) * mm, "end": v(7.26, 24.93) * mm});
            skLineSegment(sketch, "E845", {"start": v(7.26, 24.93) * mm, "end": v(7.24, 25.03) * mm});
            skLineSegment(sketch, "E846", {"start": v(7.24, 25.03) * mm, "end": v(7.23, 25.13) * mm});
            skLineSegment(sketch, "E847", {"start": v(7.23, 25.13) * mm, "end": v(7.2, 25.23) * mm});
            skLineSegment(sketch, "E848", {"start": v(7.2, 25.23) * mm, "end": v(7.17, 25.25) * mm});
            skLineSegment(sketch, "E849", {"start": v(7.17, 25.25) * mm, "end": v(6.36, 25.47) * mm});
            skLineSegment(sketch, "E850", {"start": v(6.36, 25.47) * mm, "end": v(6.32, 25.47) * mm});
            skLineSegment(sketch, "E851", {"start": v(6.32, 25.47) * mm, "end": v(6.25, 25.39) * mm});
            skLineSegment(sketch, "E852", {"start": v(6.25, 25.39) * mm, "end": v(6.19, 25.31) * mm});
            skLineSegment(sketch, "E853", {"start": v(6.19, 25.31) * mm, "end": v(6.13, 25.24) * mm});
            skLineSegment(sketch, "E854", {"start": v(6.13, 25.24) * mm, "end": v(6.07, 25.16) * mm});
            skLineSegment(sketch, "E855", {"start": v(6.07, 25.16) * mm, "end": v(6, 25.09) * mm});
            skLineSegment(sketch, "E856", {"start": v(6, 25.09) * mm, "end": v(5.95, 25.02) * mm});
            skLineSegment(sketch, "E857", {"start": v(5.95, 25.02) * mm, "end": v(5.9, 24.94) * mm});
            skLineSegment(sketch, "E858", {"start": v(5.9, 24.94) * mm, "end": v(5.84, 24.87) * mm});
            skLineSegment(sketch, "E859", {"start": v(5.84, 24.87) * mm, "end": v(5.8, 24.8) * mm});
            skLineSegment(sketch, "E860", {"start": v(5.8, 24.8) * mm, "end": v(5.74, 24.73) * mm});
            skLineSegment(sketch, "E861", {"start": v(5.74, 24.73) * mm, "end": v(5.7, 24.67) * mm});
            skLineSegment(sketch, "E862", {"start": v(5.7, 24.67) * mm, "end": v(5.65, 24.6) * mm});
            skLineSegment(sketch, "E863", {"start": v(5.65, 24.6) * mm, "end": v(5.6, 24.53) * mm});
            skLineSegment(sketch, "E864", {"start": v(5.6, 24.53) * mm, "end": v(5.56, 24.47) * mm});
            skLineSegment(sketch, "E865", {"start": v(5.56, 24.47) * mm, "end": v(5.52, 24.4) * mm});
            skLineSegment(sketch, "E866", {"start": v(5.52, 24.4) * mm, "end": v(5.48, 24.34) * mm});
            skLineSegment(sketch, "E867", {"start": v(5.48, 24.34) * mm, "end": v(5.44, 24.28) * mm});
            skLineSegment(sketch, "E868", {"start": v(5.44, 24.28) * mm, "end": v(5.4, 24.22) * mm});
            skLineSegment(sketch, "E869", {"start": v(5.4, 24.22) * mm, "end": v(5.37, 24.16) * mm});
            skLineSegment(sketch, "E870", {"start": v(5.37, 24.16) * mm, "end": v(5.33, 24.1) * mm});
            skLineSegment(sketch, "E871", {"start": v(5.33, 24.1) * mm, "end": v(5.3, 24.05) * mm});
            skLineSegment(sketch, "E872", {"start": v(5.3, 24.05) * mm, "end": v(5.27, 24) * mm});
            skLineSegment(sketch, "E873", {"start": v(5.27, 24) * mm, "end": v(5.24, 23.94) * mm});
            skLineSegment(sketch, "E874", {"start": v(5.24, 23.94) * mm, "end": v(5.21, 23.89) * mm});
            skLineSegment(sketch, "E875", {"start": v(5.21, 23.89) * mm, "end": v(5.18, 23.83) * mm});
            skLineSegment(sketch, "E876", {"start": v(5.18, 23.83) * mm, "end": v(5.16, 23.78) * mm});
            skLineSegment(sketch, "E877", {"start": v(5.16, 23.78) * mm, "end": v(5.13, 23.74) * mm});
            skLineSegment(sketch, "E878", {"start": v(5.13, 23.74) * mm, "end": v(5.1, 23.69) * mm});
            skLineSegment(sketch, "E879", {"start": v(5.1, 23.69) * mm, "end": v(5.09, 23.64) * mm});
            skLineSegment(sketch, "E880", {"start": v(5.09, 23.64) * mm, "end": v(5.07, 23.6) * mm});
            skLineSegment(sketch, "E881", {"start": v(5.07, 23.6) * mm, "end": v(5.05, 23.56) * mm});
            skLineSegment(sketch, "E882", {"start": v(5.05, 23.56) * mm, "end": v(5.03, 23.51) * mm});
            skLineSegment(sketch, "E883", {"start": v(5.03, 23.51) * mm, "end": v(5, 23.47) * mm});
            skLineSegment(sketch, "E884", {"start": v(5, 23.47) * mm, "end": v(5, 23.44) * mm});
            skLineSegment(sketch, "E885", {"start": v(5, 23.44) * mm, "end": v(4.98, 23.4) * mm});
            skLineSegment(sketch, "E886", {"start": v(4.98, 23.4) * mm, "end": v(4.96, 23.36) * mm});
            skLineSegment(sketch, "E887", {"start": v(4.96, 23.36) * mm, "end": v(4.95, 23.33) * mm});
            skLineSegment(sketch, "E888", {"start": v(4.95, 23.33) * mm, "end": v(4.93, 23.3) * mm});
            skLineSegment(sketch, "E889", {"start": v(4.93, 23.3) * mm, "end": v(4.92, 23.27) * mm});
            skLineSegment(sketch, "E890", {"start": v(4.92, 23.27) * mm, "end": v(4.91, 23.24) * mm});
            skLineSegment(sketch, "E891", {"start": v(4.91, 23.24) * mm, "end": v(4.9, 23.2) * mm});
            skLineSegment(sketch, "E892", {"start": v(4.9, 23.2) * mm, "end": v(4.9, 23.18) * mm});
            skLineSegment(sketch, "E893", {"start": v(4.9, 23.18) * mm, "end": v(4.88, 23.16) * mm});
            skLineSegment(sketch, "E894", {"start": v(4.88, 23.16) * mm, "end": v(4.88, 23.13) * mm});
            skLineSegment(sketch, "E895", {"start": v(4.88, 23.13) * mm, "end": v(4.87, 23.11) * mm});
            skLineSegment(sketch, "E896", {"start": v(4.87, 23.11) * mm, "end": v(4.86, 23.1) * mm});
            skLineSegment(sketch, "E897", {"start": v(4.86, 23.1) * mm, "end": v(4.86, 23.08) * mm});
            skLineSegment(sketch, "E898", {"start": v(4.86, 23.08) * mm, "end": v(4.85, 23.06) * mm});
            skLineSegment(sketch, "E899", {"start": v(4.85, 23.06) * mm, "end": v(3.69, 23.27) * mm});
            skLineSegment(sketch, "E900", {"start": v(3.69, 23.27) * mm, "end": v(3.68, 23.3) * mm});
            skLineSegment(sketch, "E901", {"start": v(3.68, 23.3) * mm, "end": v(3.69, 23.31) * mm});
            skLineSegment(sketch, "E902", {"start": v(3.69, 23.31) * mm, "end": v(3.69, 23.33) * mm});
            skLineSegment(sketch, "E903", {"start": v(3.69, 23.33) * mm, "end": v(3.69, 23.35) * mm});
            skLineSegment(sketch, "E904", {"start": v(3.69, 23.35) * mm, "end": v(3.69, 23.38) * mm});
            skLineSegment(sketch, "E905", {"start": v(3.69, 23.38) * mm, "end": v(3.69, 23.4) * mm});
            skLineSegment(sketch, "E906", {"start": v(3.69, 23.4) * mm, "end": v(3.69, 23.43) * mm});
            skLineSegment(sketch, "E907", {"start": v(3.69, 23.43) * mm, "end": v(3.7, 23.46) * mm});
            skLineSegment(sketch, "E908", {"start": v(3.7, 23.46) * mm, "end": v(3.7, 23.5) * mm});
            skLineSegment(sketch, "E909", {"start": v(3.7, 23.5) * mm, "end": v(3.7, 23.53) * mm});
            skLineSegment(sketch, "E910", {"start": v(3.7, 23.53) * mm, "end": v(3.69, 23.56) * mm});
            skLineSegment(sketch, "E911", {"start": v(3.69, 23.56) * mm, "end": v(3.69, 23.6) * mm});
            skLineSegment(sketch, "E912", {"start": v(3.69, 23.6) * mm, "end": v(3.69, 23.64) * mm});
            skLineSegment(sketch, "E913", {"start": v(3.69, 23.64) * mm, "end": v(3.69, 23.68) * mm});
            skLineSegment(sketch, "E914", {"start": v(3.69, 23.68) * mm, "end": v(3.68, 23.72) * mm});
            skLineSegment(sketch, "E915", {"start": v(3.68, 23.72) * mm, "end": v(3.68, 23.76) * mm});
            skLineSegment(sketch, "E916", {"start": v(3.68, 23.76) * mm, "end": v(3.68, 23.8) * mm});
            skLineSegment(sketch, "E917", {"start": v(3.68, 23.8) * mm, "end": v(3.68, 23.85) * mm});
            skLineSegment(sketch, "E918", {"start": v(3.68, 23.85) * mm, "end": v(3.67, 23.9) * mm});
            skLineSegment(sketch, "E919", {"start": v(3.67, 23.9) * mm, "end": v(3.67, 23.95) * mm});
            skLineSegment(sketch, "E920", {"start": v(3.67, 23.95) * mm, "end": v(3.66, 24) * mm});
            skLineSegment(sketch, "E921", {"start": v(3.66, 24) * mm, "end": v(3.66, 24.06) * mm});
            skLineSegment(sketch, "E922", {"start": v(3.66, 24.06) * mm, "end": v(3.65, 24.12) * mm});
            skLineSegment(sketch, "E923", {"start": v(3.65, 24.12) * mm, "end": v(3.64, 24.17) * mm});
            skLineSegment(sketch, "E924", {"start": v(3.64, 24.17) * mm, "end": v(3.63, 24.23) * mm});
            skLineSegment(sketch, "E925", {"start": v(3.63, 24.23) * mm, "end": v(3.62, 24.3) * mm});
            skLineSegment(sketch, "E926", {"start": v(3.62, 24.3) * mm, "end": v(3.61, 24.36) * mm});
            skLineSegment(sketch, "E927", {"start": v(3.61, 24.36) * mm, "end": v(3.6, 24.42) * mm});
            skLineSegment(sketch, "E928", {"start": v(3.6, 24.42) * mm, "end": v(3.6, 24.49) * mm});
            skLineSegment(sketch, "E929", {"start": v(3.6, 24.49) * mm, "end": v(3.58, 24.56) * mm});
            skLineSegment(sketch, "E930", {"start": v(3.58, 24.56) * mm, "end": v(3.57, 24.63) * mm});
            skLineSegment(sketch, "E931", {"start": v(3.57, 24.63) * mm, "end": v(3.55, 24.7) * mm});
            skLineSegment(sketch, "E932", {"start": v(3.55, 24.7) * mm, "end": v(3.54, 24.77) * mm});
            skLineSegment(sketch, "E933", {"start": v(3.54, 24.77) * mm, "end": v(3.52, 24.84) * mm});
            skLineSegment(sketch, "E934", {"start": v(3.52, 24.84) * mm, "end": v(3.5, 24.92) * mm});
            skLineSegment(sketch, "E935", {"start": v(3.5, 24.92) * mm, "end": v(3.49, 25) * mm});
            skLineSegment(sketch, "E936", {"start": v(3.49, 25) * mm, "end": v(3.47, 25.08) * mm});
            skLineSegment(sketch, "E937", {"start": v(3.47, 25.08) * mm, "end": v(3.45, 25.16) * mm});
            skLineSegment(sketch, "E938", {"start": v(3.45, 25.16) * mm, "end": v(3.42, 25.24) * mm});
            skLineSegment(sketch, "E939", {"start": v(3.42, 25.24) * mm, "end": v(3.4, 25.32) * mm});
            skLineSegment(sketch, "E940", {"start": v(3.4, 25.32) * mm, "end": v(3.38, 25.4) * mm});
            skLineSegment(sketch, "E941", {"start": v(3.38, 25.4) * mm, "end": v(3.35, 25.5) * mm});
            skLineSegment(sketch, "E942", {"start": v(3.35, 25.5) * mm, "end": v(3.33, 25.58) * mm});
            skLineSegment(sketch, "E943", {"start": v(3.33, 25.58) * mm, "end": v(3.3, 25.67) * mm});
            skLineSegment(sketch, "E944", {"start": v(3.3, 25.67) * mm, "end": v(3.27, 25.76) * mm});
            skLineSegment(sketch, "E945", {"start": v(3.27, 25.76) * mm, "end": v(3.24, 25.86) * mm});
            skLineSegment(sketch, "E946", {"start": v(3.24, 25.86) * mm, "end": v(3.2, 25.95) * mm});
            skLineSegment(sketch, "E947", {"start": v(3.2, 25.95) * mm, "end": v(3.17, 26.05) * mm});
            skLineSegment(sketch, "E948", {"start": v(3.17, 26.05) * mm, "end": v(3.13, 26.06) * mm});
            skLineSegment(sketch, "E949", {"start": v(3.13, 26.06) * mm, "end": v(2.3, 26.15) * mm});
            skLineSegment(sketch, "E950", {"start": v(2.3, 26.15) * mm, "end": v(2.25, 26.14) * mm});
            skLineSegment(sketch, "E951", {"start": v(2.25, 26.14) * mm, "end": v(2.2, 26.05) * mm});
            skLineSegment(sketch, "E952", {"start": v(2.2, 26.05) * mm, "end": v(2.15, 25.97) * mm});
            skLineSegment(sketch, "E953", {"start": v(2.15, 25.97) * mm, "end": v(2.1, 25.88) * mm});
            skLineSegment(sketch, "E954", {"start": v(2.1, 25.88) * mm, "end": v(2.05, 25.8) * mm});
            skLineSegment(sketch, "E955", {"start": v(2.05, 25.8) * mm, "end": v(2, 25.72) * mm});
            skLineSegment(sketch, "E956", {"start": v(2, 25.72) * mm, "end": v(1.96, 25.64) * mm});
            skLineSegment(sketch, "E957", {"start": v(1.96, 25.64) * mm, "end": v(1.92, 25.56) * mm});
            skLineSegment(sketch, "E958", {"start": v(1.92, 25.56) * mm, "end": v(1.88, 25.48) * mm});
            skLineSegment(sketch, "E959", {"start": v(1.88, 25.48) * mm, "end": v(1.84, 25.4) * mm});
            skLineSegment(sketch, "E960", {"start": v(1.84, 25.4) * mm, "end": v(1.8, 25.33) * mm});
            skLineSegment(sketch, "E961", {"start": v(1.8, 25.33) * mm, "end": v(1.77, 25.25) * mm});
            skLineSegment(sketch, "E962", {"start": v(1.77, 25.25) * mm, "end": v(1.73, 25.18) * mm});
            skLineSegment(sketch, "E963", {"start": v(1.73, 25.18) * mm, "end": v(1.7, 25.1) * mm});
            skLineSegment(sketch, "E964", {"start": v(1.7, 25.1) * mm, "end": v(1.67, 25.04) * mm});
            skLineSegment(sketch, "E965", {"start": v(1.67, 25.04) * mm, "end": v(1.63, 24.97) * mm});
            skLineSegment(sketch, "E966", {"start": v(1.63, 24.97) * mm, "end": v(1.6, 24.9) * mm});
            skLineSegment(sketch, "E967", {"start": v(1.6, 24.9) * mm, "end": v(1.58, 24.83) * mm});
            skLineSegment(sketch, "E968", {"start": v(1.58, 24.83) * mm, "end": v(1.55, 24.77) * mm});
            skLineSegment(sketch, "E969", {"start": v(1.55, 24.77) * mm, "end": v(1.52, 24.7) * mm});
            skLineSegment(sketch, "E970", {"start": v(1.52, 24.7) * mm, "end": v(1.5, 24.64) * mm});
            skLineSegment(sketch, "E971", {"start": v(1.5, 24.64) * mm, "end": v(1.47, 24.58) * mm});
            skLineSegment(sketch, "E972", {"start": v(1.47, 24.58) * mm, "end": v(1.45, 24.52) * mm});
            skLineSegment(sketch, "E973", {"start": v(1.45, 24.52) * mm, "end": v(1.43, 24.46) * mm});
            skLineSegment(sketch, "E974", {"start": v(1.43, 24.46) * mm, "end": v(1.41, 24.4) * mm});
            skLineSegment(sketch, "E975", {"start": v(1.41, 24.4) * mm, "end": v(1.4, 24.35) * mm});
            skLineSegment(sketch, "E976", {"start": v(1.4, 24.35) * mm, "end": v(1.37, 24.3) * mm});
            skLineSegment(sketch, "E977", {"start": v(1.37, 24.3) * mm, "end": v(1.36, 24.25) * mm});
            skLineSegment(sketch, "E978", {"start": v(1.36, 24.25) * mm, "end": v(1.34, 24.2) * mm});
            skLineSegment(sketch, "E979", {"start": v(1.34, 24.2) * mm, "end": v(1.33, 24.15) * mm});
            skLineSegment(sketch, "E980", {"start": v(1.33, 24.15) * mm, "end": v(1.31, 24.1) * mm});
            skLineSegment(sketch, "E981", {"start": v(1.31, 24.1) * mm, "end": v(1.3, 24.05) * mm});
            skLineSegment(sketch, "E982", {"start": v(1.3, 24.05) * mm, "end": v(1.29, 24.01) * mm});
            skLineSegment(sketch, "E983", {"start": v(1.29, 24.01) * mm, "end": v(1.27, 23.97) * mm});
            skLineSegment(sketch, "E984", {"start": v(1.27, 23.97) * mm, "end": v(1.26, 23.93) * mm});
            skLineSegment(sketch, "E985", {"start": v(1.26, 23.93) * mm, "end": v(1.25, 23.89) * mm});
            skLineSegment(sketch, "E986", {"start": v(1.25, 23.89) * mm, "end": v(1.25, 23.85) * mm});
            skLineSegment(sketch, "E987", {"start": v(1.25, 23.85) * mm, "end": v(1.24, 23.82) * mm});
            skLineSegment(sketch, "E988", {"start": v(1.24, 23.82) * mm, "end": v(1.23, 23.78) * mm});
            skLineSegment(sketch, "E989", {"start": v(1.23, 23.78) * mm, "end": v(1.22, 23.75) * mm});
            skLineSegment(sketch, "E990", {"start": v(1.22, 23.75) * mm, "end": v(1.22, 23.72) * mm});
            skLineSegment(sketch, "E991", {"start": v(1.22, 23.72) * mm, "end": v(1.21, 23.69) * mm});
            skLineSegment(sketch, "E992", {"start": v(1.21, 23.69) * mm, "end": v(1.2, 23.66) * mm});
            skLineSegment(sketch, "E993", {"start": v(1.2, 23.66) * mm, "end": v(1.2, 23.64) * mm});
            skLineSegment(sketch, "E994", {"start": v(1.2, 23.64) * mm, "end": v(1.2, 23.61) * mm});
            skLineSegment(sketch, "E995", {"start": v(1.2, 23.61) * mm, "end": v(1.2, 23.6) * mm});
            skLineSegment(sketch, "E996", {"start": v(1.2, 23.6) * mm, "end": v(1.2, 23.57) * mm});
            skLineSegment(sketch, "E997", {"start": v(1.2, 23.57) * mm, "end": v(1.19, 23.55) * mm});
            skLineSegment(sketch, "E998", {"start": v(1.19, 23.55) * mm, "end": v(1.18, 23.53) * mm});
            skLineSegment(sketch, "E999", {"start": v(1.18, 23.53) * mm, "end": v(0, 23.56) * mm});
            skLineSegment(sketch, "E1000", {"start": v(0, 23.56) * mm, "end": v(0, 23.58) * mm});
            skLineSegment(sketch, "E1001", {"start": v(0, 23.58) * mm, "end": v(0, 23.6) * mm});
            skLineSegment(sketch, "E1002", {"start": v(0, 23.6) * mm, "end": v(0, 23.62) * mm});
            skLineSegment(sketch, "E1003", {"start": v(0, 23.62) * mm, "end": v(-0.01, 23.64) * mm});
            skLineSegment(sketch, "E1004", {"start": v(-0.01, 23.64) * mm, "end": v(-0.01, 23.67) * mm});
            skLineSegment(sketch, "E1005", {"start": v(-0.01, 23.67) * mm, "end": v(-0.02, 23.7) * mm});
            skLineSegment(sketch, "E1006", {"start": v(-0.02, 23.7) * mm, "end": v(-0.02, 23.72) * mm});
            skLineSegment(sketch, "E1007", {"start": v(-0.02, 23.72) * mm, "end": v(-0.03, 23.75) * mm});
            skLineSegment(sketch, "E1008", {"start": v(-0.03, 23.75) * mm, "end": v(-0.03, 23.78) * mm});
            skLineSegment(sketch, "E1009", {"start": v(-0.03, 23.78) * mm, "end": v(-0.04, 23.81) * mm});
            skLineSegment(sketch, "E1010", {"start": v(-0.04, 23.81) * mm, "end": v(-0.04, 23.85) * mm});
            skLineSegment(sketch, "E1011", {"start": v(-0.04, 23.85) * mm, "end": v(-0.05, 23.88) * mm});
            skLineSegment(sketch, "E1012", {"start": v(-0.05, 23.88) * mm, "end": v(-0.06, 23.92) * mm});
            skLineSegment(sketch, "E1013", {"start": v(-0.06, 23.92) * mm, "end": v(-0.06, 23.96) * mm});
            skLineSegment(sketch, "E1014", {"start": v(-0.06, 23.96) * mm, "end": v(-0.07, 24) * mm});
            skLineSegment(sketch, "E1015", {"start": v(-0.07, 24) * mm, "end": v(-0.08, 24.04) * mm});
            skLineSegment(sketch, "E1016", {"start": v(-0.08, 24.04) * mm, "end": v(-0.1, 24.09) * mm});
            skLineSegment(sketch, "E1017", {"start": v(-0.1, 24.09) * mm, "end": v(-0.1, 24.14) * mm});
            skLineSegment(sketch, "E1018", {"start": v(-0.1, 24.14) * mm, "end": v(-0.11, 24.18) * mm});
            skLineSegment(sketch, "E1019", {"start": v(-0.11, 24.18) * mm, "end": v(-0.13, 24.23) * mm});
            skLineSegment(sketch, "E1020", {"start": v(-0.13, 24.23) * mm, "end": v(-0.14, 24.28) * mm});
            skLineSegment(sketch, "E1021", {"start": v(-0.14, 24.28) * mm, "end": v(-0.15, 24.34) * mm});
            skLineSegment(sketch, "E1022", {"start": v(-0.15, 24.34) * mm, "end": v(-0.17, 24.4) * mm});
            skLineSegment(sketch, "E1023", {"start": v(-0.17, 24.4) * mm, "end": v(-0.19, 24.45) * mm});
            skLineSegment(sketch, "E1024", {"start": v(-0.19, 24.45) * mm, "end": v(-0.2, 24.5) * mm});
            skLineSegment(sketch, "E1025", {"start": v(-0.2, 24.5) * mm, "end": v(-0.22, 24.56) * mm});
            skLineSegment(sketch, "E1026", {"start": v(-0.22, 24.56) * mm, "end": v(-0.24, 24.62) * mm});
            skLineSegment(sketch, "E1027", {"start": v(-0.24, 24.62) * mm, "end": v(-0.26, 24.69) * mm});
            skLineSegment(sketch, "E1028", {"start": v(-0.26, 24.69) * mm, "end": v(-0.28, 24.75) * mm});
            skLineSegment(sketch, "E1029", {"start": v(-0.28, 24.75) * mm, "end": v(-0.3, 24.81) * mm});
            skLineSegment(sketch, "E1030", {"start": v(-0.3, 24.81) * mm, "end": v(-0.33, 24.88) * mm});
            skLineSegment(sketch, "E1031", {"start": v(-0.33, 24.88) * mm, "end": v(-0.35, 24.95) * mm});
            skLineSegment(sketch, "E1032", {"start": v(-0.35, 24.95) * mm, "end": v(-0.38, 25.02) * mm});
            skLineSegment(sketch, "E1033", {"start": v(-0.38, 25.02) * mm, "end": v(-0.4, 25.09) * mm});
            skLineSegment(sketch, "E1034", {"start": v(-0.4, 25.09) * mm, "end": v(-0.44, 25.16) * mm});
            skLineSegment(sketch, "E1035", {"start": v(-0.44, 25.16) * mm, "end": v(-0.47, 25.23) * mm});
            skLineSegment(sketch, "E1036", {"start": v(-0.47, 25.23) * mm, "end": v(-0.5, 25.3) * mm});
            skLineSegment(sketch, "E1037", {"start": v(-0.5, 25.3) * mm, "end": v(-0.53, 25.39) * mm});
            skLineSegment(sketch, "E1038", {"start": v(-0.53, 25.39) * mm, "end": v(-0.57, 25.46) * mm});
            skLineSegment(sketch, "E1039", {"start": v(-0.57, 25.46) * mm, "end": v(-0.6, 25.54) * mm});
            skLineSegment(sketch, "E1040", {"start": v(-0.6, 25.54) * mm, "end": v(-0.64, 25.62) * mm});
            skLineSegment(sketch, "E1041", {"start": v(-0.64, 25.62) * mm, "end": v(-0.68, 25.7) * mm});
            skLineSegment(sketch, "E1042", {"start": v(-0.68, 25.7) * mm, "end": v(-0.72, 25.79) * mm});
            skLineSegment(sketch, "E1043", {"start": v(-0.72, 25.79) * mm, "end": v(-0.76, 25.87) * mm});
            skLineSegment(sketch, "E1044", {"start": v(-0.76, 25.87) * mm, "end": v(-0.8, 25.96) * mm});
            skLineSegment(sketch, "E1045", {"start": v(-0.8, 25.96) * mm, "end": v(-0.85, 26.04) * mm});
            skLineSegment(sketch, "E1046", {"start": v(-0.85, 26.04) * mm, "end": v(-0.9, 26.13) * mm});
            skLineSegment(sketch, "E1047", {"start": v(-0.9, 26.13) * mm, "end": v(-0.94, 26.22) * mm});
            skLineSegment(sketch, "E1048", {"start": v(-0.94, 26.22) * mm, "end": v(-0.99, 26.23) * mm});
            skLineSegment(sketch, "E1049", {"start": v(-0.99, 26.23) * mm, "end": v(-1.82, 26.19) * mm});
            skLineSegment(sketch, "E1050", {"start": v(-1.82, 26.19) * mm, "end": v(-1.86, 26.17) * mm});
            skLineSegment(sketch, "E1051", {"start": v(-1.86, 26.17) * mm, "end": v(-1.9, 26.08) * mm});
            skLineSegment(sketch, "E1052", {"start": v(-1.9, 26.08) * mm, "end": v(-1.94, 25.99) * mm});
            skLineSegment(sketch, "E1053", {"start": v(-1.94, 25.99) * mm, "end": v(-1.97, 25.9) * mm});
            skLineSegment(sketch, "E1054", {"start": v(-1.97, 25.9) * mm, "end": v(-2, 25.8) * mm});
            skLineSegment(sketch, "E1055", {"start": v(-2, 25.8) * mm, "end": v(-2.04, 25.72) * mm});
            skLineSegment(sketch, "E1056", {"start": v(-2.04, 25.72) * mm, "end": v(-2.07, 25.63) * mm});
            skLineSegment(sketch, "E1057", {"start": v(-2.07, 25.63) * mm, "end": v(-2.1, 25.55) * mm});
            skLineSegment(sketch, "E1058", {"start": v(-2.1, 25.55) * mm, "end": v(-2.13, 25.46) * mm});
            skLineSegment(sketch, "E1059", {"start": v(-2.13, 25.46) * mm, "end": v(-2.16, 25.38) * mm});
            skLineSegment(sketch, "E1060", {"start": v(-2.16, 25.38) * mm, "end": v(-2.18, 25.3) * mm});
            skLineSegment(sketch, "E1061", {"start": v(-2.18, 25.3) * mm, "end": v(-2.2, 25.22) * mm});
            skLineSegment(sketch, "E1062", {"start": v(-2.2, 25.22) * mm, "end": v(-2.23, 25.14) * mm});
            skLineSegment(sketch, "E1063", {"start": v(-2.23, 25.14) * mm, "end": v(-2.25, 25.06) * mm});
            skLineSegment(sketch, "E1064", {"start": v(-2.25, 25.06) * mm, "end": v(-2.27, 24.99) * mm});
            skLineSegment(sketch, "E1065", {"start": v(-2.27, 24.99) * mm, "end": v(-2.3, 24.92) * mm});
            skLineSegment(sketch, "E1066", {"start": v(-2.3, 24.92) * mm, "end": v(-2.31, 24.84) * mm});
            skLineSegment(sketch, "E1067", {"start": v(-2.31, 24.84) * mm, "end": v(-2.33, 24.77) * mm});
            skLineSegment(sketch, "E1068", {"start": v(-2.33, 24.77) * mm, "end": v(-2.34, 24.7) * mm});
            skLineSegment(sketch, "E1069", {"start": v(-2.34, 24.7) * mm, "end": v(-2.36, 24.64) * mm});
            skLineSegment(sketch, "E1070", {"start": v(-2.36, 24.64) * mm, "end": v(-2.38, 24.57) * mm});
            skLineSegment(sketch, "E1071", {"start": v(-2.38, 24.57) * mm, "end": v(-2.39, 24.5) * mm});
            skLineSegment(sketch, "E1072", {"start": v(-2.39, 24.5) * mm, "end": v(-2.4, 24.45) * mm});
            skLineSegment(sketch, "E1073", {"start": v(-2.4, 24.45) * mm, "end": v(-2.41, 24.39) * mm});
            skLineSegment(sketch, "E1074", {"start": v(-2.41, 24.39) * mm, "end": v(-2.42, 24.33) * mm});
            skLineSegment(sketch, "E1075", {"start": v(-2.42, 24.33) * mm, "end": v(-2.43, 24.27) * mm});
            skLineSegment(sketch, "E1076", {"start": v(-2.43, 24.27) * mm, "end": v(-2.44, 24.21) * mm});
            skLineSegment(sketch, "E1077", {"start": v(-2.44, 24.21) * mm, "end": v(-2.45, 24.16) * mm});
            skLineSegment(sketch, "E1078", {"start": v(-2.45, 24.16) * mm, "end": v(-2.46, 24.1) * mm});
            skLineSegment(sketch, "E1079", {"start": v(-2.46, 24.1) * mm, "end": v(-2.47, 24.06) * mm});
            skLineSegment(sketch, "E1080", {"start": v(-2.47, 24.06) * mm, "end": v(-2.47, 24) * mm});
            skLineSegment(sketch, "E1081", {"start": v(-2.47, 24) * mm, "end": v(-2.48, 23.96) * mm});
            skLineSegment(sketch, "E1082", {"start": v(-2.48, 23.96) * mm, "end": v(-2.49, 23.92) * mm});
            skLineSegment(sketch, "E1083", {"start": v(-2.49, 23.92) * mm, "end": v(-2.5, 23.87) * mm});
            skLineSegment(sketch, "E1084", {"start": v(-2.5, 23.87) * mm, "end": v(-2.5, 23.83) * mm});
            skLineSegment(sketch, "E1085", {"start": v(-2.5, 23.83) * mm, "end": v(-2.5, 23.8) * mm});
            skLineSegment(sketch, "E1086", {"start": v(-2.5, 23.8) * mm, "end": v(-2.5, 23.75) * mm});
            skLineSegment(sketch, "E1087", {"start": v(-2.5, 23.75) * mm, "end": v(-2.5, 23.72) * mm});
            skLineSegment(sketch, "E1088", {"start": v(-2.5, 23.72) * mm, "end": v(-2.5, 23.68) * mm});
            skLineSegment(sketch, "E1089", {"start": v(-2.5, 23.68) * mm, "end": v(-2.5, 23.65) * mm});
            skLineSegment(sketch, "E1090", {"start": v(-2.5, 23.65) * mm, "end": v(-2.5, 23.62) * mm});
            skLineSegment(sketch, "E1091", {"start": v(-2.5, 23.62) * mm, "end": v(-2.51, 23.59) * mm});
            skLineSegment(sketch, "E1092", {"start": v(-2.51, 23.59) * mm, "end": v(-2.51, 23.56) * mm});
            skLineSegment(sketch, "E1093", {"start": v(-2.51, 23.56) * mm, "end": v(-2.51, 23.53) * mm});
            skLineSegment(sketch, "E1094", {"start": v(-2.51, 23.53) * mm, "end": v(-2.51, 23.5) * mm});
            skLineSegment(sketch, "E1095", {"start": v(-2.51, 23.5) * mm, "end": v(-2.51, 23.49) * mm});
            skLineSegment(sketch, "E1096", {"start": v(-2.51, 23.49) * mm, "end": v(-2.51, 23.47) * mm});
            skLineSegment(sketch, "E1097", {"start": v(-2.51, 23.47) * mm, "end": v(-2.51, 23.45) * mm});
            skLineSegment(sketch, "E1098", {"start": v(-2.51, 23.45) * mm, "end": v(-2.51, 23.43) * mm});
            skLineSegment(sketch, "E1099", {"start": v(-2.51, 23.43) * mm, "end": v(-3.69, 23.27) * mm});
            skLineSegment(sketch, "E1100", {"start": v(-3.69, 23.27) * mm, "end": v(-3.7, 23.3) * mm});
            skLineSegment(sketch, "E1101", {"start": v(-3.7, 23.3) * mm, "end": v(-3.7, 23.3) * mm});
            skLineSegment(sketch, "E1102", {"start": v(-3.7, 23.3) * mm, "end": v(-3.7, 23.33) * mm});
            skLineSegment(sketch, "E1103", {"start": v(-3.7, 23.33) * mm, "end": v(-3.7, 23.35) * mm});
            skLineSegment(sketch, "E1104", {"start": v(-3.7, 23.35) * mm, "end": v(-3.72, 23.37) * mm});
            skLineSegment(sketch, "E1105", {"start": v(-3.72, 23.37) * mm, "end": v(-3.72, 23.4) * mm});
            skLineSegment(sketch, "E1106", {"start": v(-3.72, 23.4) * mm, "end": v(-3.73, 23.42) * mm});
            skLineSegment(sketch, "E1107", {"start": v(-3.73, 23.42) * mm, "end": v(-3.74, 23.45) * mm});
            skLineSegment(sketch, "E1108", {"start": v(-3.74, 23.45) * mm, "end": v(-3.75, 23.48) * mm});
            skLineSegment(sketch, "E1109", {"start": v(-3.75, 23.48) * mm, "end": v(-3.76, 23.51) * mm});
            skLineSegment(sketch, "E1110", {"start": v(-3.76, 23.51) * mm, "end": v(-3.77, 23.55) * mm});
            skLineSegment(sketch, "E1111", {"start": v(-3.77, 23.55) * mm, "end": v(-3.78, 23.58) * mm});
            skLineSegment(sketch, "E1112", {"start": v(-3.78, 23.58) * mm, "end": v(-3.8, 23.62) * mm});
            skLineSegment(sketch, "E1113", {"start": v(-3.8, 23.62) * mm, "end": v(-3.81, 23.66) * mm});
            skLineSegment(sketch, "E1114", {"start": v(-3.81, 23.66) * mm, "end": v(-3.83, 23.7) * mm});
            skLineSegment(sketch, "E1115", {"start": v(-3.83, 23.7) * mm, "end": v(-3.84, 23.74) * mm});
            skLineSegment(sketch, "E1116", {"start": v(-3.84, 23.74) * mm, "end": v(-3.86, 23.78) * mm});
            skLineSegment(sketch, "E1117", {"start": v(-3.86, 23.78) * mm, "end": v(-3.88, 23.82) * mm});
            skLineSegment(sketch, "E1118", {"start": v(-3.88, 23.82) * mm, "end": v(-3.9, 23.87) * mm});
            skLineSegment(sketch, "E1119", {"start": v(-3.9, 23.87) * mm, "end": v(-3.92, 23.91) * mm});
            skLineSegment(sketch, "E1120", {"start": v(-3.92, 23.91) * mm, "end": v(-3.94, 23.96) * mm});
            skLineSegment(sketch, "E1121", {"start": v(-3.94, 23.96) * mm, "end": v(-3.96, 24.01) * mm});
            skLineSegment(sketch, "E1122", {"start": v(-3.96, 24.01) * mm, "end": v(-3.98, 24.06) * mm});
            skLineSegment(sketch, "E1123", {"start": v(-3.98, 24.06) * mm, "end": v(-4, 24.12) * mm});
            skLineSegment(sketch, "E1124", {"start": v(-4, 24.12) * mm, "end": v(-4.03, 24.17) * mm});
            skLineSegment(sketch, "E1125", {"start": v(-4.03, 24.17) * mm, "end": v(-4.06, 24.23) * mm});
            skLineSegment(sketch, "E1126", {"start": v(-4.06, 24.23) * mm, "end": v(-4.09, 24.28) * mm});
            skLineSegment(sketch, "E1127", {"start": v(-4.09, 24.28) * mm, "end": v(-4.12, 24.34) * mm});
            skLineSegment(sketch, "E1128", {"start": v(-4.12, 24.34) * mm, "end": v(-4.15, 24.4) * mm});
            skLineSegment(sketch, "E1129", {"start": v(-4.15, 24.4) * mm, "end": v(-4.18, 24.46) * mm});
            skLineSegment(sketch, "E1130", {"start": v(-4.18, 24.46) * mm, "end": v(-4.22, 24.52) * mm});
            skLineSegment(sketch, "E1131", {"start": v(-4.22, 24.52) * mm, "end": v(-4.25, 24.59) * mm});
            skLineSegment(sketch, "E1132", {"start": v(-4.25, 24.59) * mm, "end": v(-4.29, 24.65) * mm});
            skLineSegment(sketch, "E1133", {"start": v(-4.29, 24.65) * mm, "end": v(-4.33, 24.72) * mm});
            skLineSegment(sketch, "E1134", {"start": v(-4.33, 24.72) * mm, "end": v(-4.37, 24.78) * mm});
            skLineSegment(sketch, "E1135", {"start": v(-4.37, 24.78) * mm, "end": v(-4.4, 24.85) * mm});
            skLineSegment(sketch, "E1136", {"start": v(-4.4, 24.85) * mm, "end": v(-4.45, 24.92) * mm});
            skLineSegment(sketch, "E1137", {"start": v(-4.45, 24.92) * mm, "end": v(-4.5, 25) * mm});
            skLineSegment(sketch, "E1138", {"start": v(-4.5, 25) * mm, "end": v(-4.54, 25.06) * mm});
            skLineSegment(sketch, "E1139", {"start": v(-4.54, 25.06) * mm, "end": v(-4.59, 25.13) * mm});
            skLineSegment(sketch, "E1140", {"start": v(-4.59, 25.13) * mm, "end": v(-4.64, 25.2) * mm});
            skLineSegment(sketch, "E1141", {"start": v(-4.64, 25.2) * mm, "end": v(-4.69, 25.28) * mm});
            skLineSegment(sketch, "E1142", {"start": v(-4.69, 25.28) * mm, "end": v(-4.74, 25.36) * mm});
            skLineSegment(sketch, "E1143", {"start": v(-4.74, 25.36) * mm, "end": v(-4.8, 25.44) * mm});
            skLineSegment(sketch, "E1144", {"start": v(-4.8, 25.44) * mm, "end": v(-4.85, 25.51) * mm});
            skLineSegment(sketch, "E1145", {"start": v(-4.85, 25.51) * mm, "end": v(-4.9, 25.6) * mm});
            skLineSegment(sketch, "E1146", {"start": v(-4.9, 25.6) * mm, "end": v(-4.97, 25.67) * mm});
            skLineSegment(sketch, "E1147", {"start": v(-4.97, 25.67) * mm, "end": v(-5.03, 25.75) * mm});
            skLineSegment(sketch, "E1148", {"start": v(-5.03, 25.75) * mm, "end": v(-5.08, 25.75) * mm});
            skLineSegment(sketch, "E1149", {"start": v(-5.08, 25.75) * mm, "end": v(-5.9, 25.58) * mm});
            skLineSegment(sketch, "E1150", {"start": v(-5.9, 25.58) * mm, "end": v(-5.93, 25.56) * mm});
            skLineSegment(sketch, "E1151", {"start": v(-5.93, 25.56) * mm, "end": v(-5.96, 25.46) * mm});
            skLineSegment(sketch, "E1152", {"start": v(-5.96, 25.46) * mm, "end": v(-5.98, 25.36) * mm});
            skLineSegment(sketch, "E1153", {"start": v(-5.98, 25.36) * mm, "end": v(-6, 25.27) * mm});
            skLineSegment(sketch, "E1154", {"start": v(-6, 25.27) * mm, "end": v(-6.02, 25.17) * mm});
            skLineSegment(sketch, "E1155", {"start": v(-6.02, 25.17) * mm, "end": v(-6.04, 25.08) * mm});
            skLineSegment(sketch, "E1156", {"start": v(-6.04, 25.08) * mm, "end": v(-6.05, 25) * mm});
            skLineSegment(sketch, "E1157", {"start": v(-6.05, 25) * mm, "end": v(-6.07, 24.9) * mm});
            skLineSegment(sketch, "E1158", {"start": v(-6.07, 24.9) * mm, "end": v(-6.09, 24.81) * mm});
            skLineSegment(sketch, "E1159", {"start": v(-6.09, 24.81) * mm, "end": v(-6.1, 24.73) * mm});
            skLineSegment(sketch, "E1160", {"start": v(-6.1, 24.73) * mm, "end": v(-6.11, 24.65) * mm});
            skLineSegment(sketch, "E1161", {"start": v(-6.11, 24.65) * mm, "end": v(-6.12, 24.56) * mm});
            skLineSegment(sketch, "E1162", {"start": v(-6.12, 24.56) * mm, "end": v(-6.13, 24.48) * mm});
            skLineSegment(sketch, "E1163", {"start": v(-6.13, 24.48) * mm, "end": v(-6.14, 24.4) * mm});
            skLineSegment(sketch, "E1164", {"start": v(-6.14, 24.4) * mm, "end": v(-6.15, 24.33) * mm});
            skLineSegment(sketch, "E1165", {"start": v(-6.15, 24.33) * mm, "end": v(-6.16, 24.25) * mm});
            skLineSegment(sketch, "E1166", {"start": v(-6.16, 24.25) * mm, "end": v(-6.17, 24.18) * mm});
            skLineSegment(sketch, "E1167", {"start": v(-6.17, 24.18) * mm, "end": v(-6.17, 24.1) * mm});
            skLineSegment(sketch, "E1168", {"start": v(-6.17, 24.1) * mm, "end": v(-6.18, 24.03) * mm});
            skLineSegment(sketch, "E1169", {"start": v(-6.18, 24.03) * mm, "end": v(-6.19, 23.96) * mm});
            skLineSegment(sketch, "E1170", {"start": v(-6.19, 23.96) * mm, "end": v(-6.19, 23.9) * mm});
            skLineSegment(sketch, "E1171", {"start": v(-6.19, 23.9) * mm, "end": v(-6.2, 23.83) * mm});
            skLineSegment(sketch, "E1172", {"start": v(-6.2, 23.83) * mm, "end": v(-6.2, 23.77) * mm});
            skLineSegment(sketch, "E1173", {"start": v(-6.2, 23.77) * mm, "end": v(-6.2, 23.7) * mm});
            skLineSegment(sketch, "E1174", {"start": v(-6.2, 23.7) * mm, "end": v(-6.2, 23.65) * mm});
            skLineSegment(sketch, "E1175", {"start": v(-6.2, 23.65) * mm, "end": v(-6.2, 23.59) * mm});
            skLineSegment(sketch, "E1176", {"start": v(-6.2, 23.59) * mm, "end": v(-6.2, 23.53) * mm});
            skLineSegment(sketch, "E1177", {"start": v(-6.2, 23.53) * mm, "end": v(-6.2, 23.48) * mm});
            skLineSegment(sketch, "E1178", {"start": v(-6.2, 23.48) * mm, "end": v(-6.2, 23.43) * mm});
            skLineSegment(sketch, "E1179", {"start": v(-6.2, 23.43) * mm, "end": v(-6.2, 23.37) * mm});
            skLineSegment(sketch, "E1180", {"start": v(-6.2, 23.37) * mm, "end": v(-6.2, 23.33) * mm});
            skLineSegment(sketch, "E1181", {"start": v(-6.2, 23.33) * mm, "end": v(-6.2, 23.28) * mm});
            skLineSegment(sketch, "E1182", {"start": v(-6.2, 23.28) * mm, "end": v(-6.2, 23.23) * mm});
            skLineSegment(sketch, "E1183", {"start": v(-6.2, 23.23) * mm, "end": v(-6.2, 23.19) * mm});
            skLineSegment(sketch, "E1184", {"start": v(-6.2, 23.19) * mm, "end": v(-6.2, 23.15) * mm});
            skLineSegment(sketch, "E1185", {"start": v(-6.2, 23.15) * mm, "end": v(-6.19, 23.1) * mm});
            skLineSegment(sketch, "E1186", {"start": v(-6.19, 23.1) * mm, "end": v(-6.19, 23.07) * mm});
            skLineSegment(sketch, "E1187", {"start": v(-6.19, 23.07) * mm, "end": v(-6.18, 23.03) * mm});
            skLineSegment(sketch, "E1188", {"start": v(-6.18, 23.03) * mm, "end": v(-6.18, 23) * mm});
            skLineSegment(sketch, "E1189", {"start": v(-6.18, 23) * mm, "end": v(-6.18, 22.96) * mm});
            skLineSegment(sketch, "E1190", {"start": v(-6.18, 22.96) * mm, "end": v(-6.17, 22.93) * mm});
            skLineSegment(sketch, "E1191", {"start": v(-6.17, 22.93) * mm, "end": v(-6.17, 22.9) * mm});
            skLineSegment(sketch, "E1192", {"start": v(-6.17, 22.9) * mm, "end": v(-6.17, 22.88) * mm});
            skLineSegment(sketch, "E1193", {"start": v(-6.17, 22.88) * mm, "end": v(-6.16, 22.85) * mm});
            skLineSegment(sketch, "E1194", {"start": v(-6.16, 22.85) * mm, "end": v(-6.16, 22.83) * mm});
            skLineSegment(sketch, "E1195", {"start": v(-6.16, 22.83) * mm, "end": v(-6.16, 22.8) * mm});
            skLineSegment(sketch, "E1196", {"start": v(-6.16, 22.8) * mm, "end": v(-6.15, 22.78) * mm});
            skLineSegment(sketch, "E1197", {"start": v(-6.15, 22.78) * mm, "end": v(-6.15, 22.77) * mm});
            skLineSegment(sketch, "E1198", {"start": v(-6.15, 22.77) * mm, "end": v(-6.15, 22.75) * mm});
            skLineSegment(sketch, "E1199", {"start": v(-6.15, 22.75) * mm, "end": v(-7.28, 22.4) * mm});
            skLineSegment(sketch, "E1200", {"start": v(-7.28, 22.4) * mm, "end": v(-7.3, 22.43) * mm});
            skLineSegment(sketch, "E1201", {"start": v(-7.3, 22.43) * mm, "end": v(-7.3, 22.44) * mm});
            skLineSegment(sketch, "E1202", {"start": v(-7.3, 22.44) * mm, "end": v(-7.3, 22.46) * mm});
            skLineSegment(sketch, "E1203", {"start": v(-7.3, 22.46) * mm, "end": v(-7.32, 22.48) * mm});
            skLineSegment(sketch, "E1204", {"start": v(-7.32, 22.48) * mm, "end": v(-7.33, 22.5) * mm});
            skLineSegment(sketch, "E1205", {"start": v(-7.33, 22.5) * mm, "end": v(-7.34, 22.53) * mm});
            skLineSegment(sketch, "E1206", {"start": v(-7.34, 22.53) * mm, "end": v(-7.35, 22.55) * mm});
            skLineSegment(sketch, "E1207", {"start": v(-7.35, 22.55) * mm, "end": v(-7.36, 22.58) * mm});
            skLineSegment(sketch, "E1208", {"start": v(-7.36, 22.58) * mm, "end": v(-7.38, 22.6) * mm});
            skLineSegment(sketch, "E1209", {"start": v(-7.38, 22.6) * mm, "end": v(-7.4, 22.64) * mm});
            skLineSegment(sketch, "E1210", {"start": v(-7.4, 22.64) * mm, "end": v(-7.4, 22.67) * mm});
            skLineSegment(sketch, "E1211", {"start": v(-7.4, 22.67) * mm, "end": v(-7.43, 22.7) * mm});
            skLineSegment(sketch, "E1212", {"start": v(-7.43, 22.7) * mm, "end": v(-7.44, 22.73) * mm});
            skLineSegment(sketch, "E1213", {"start": v(-7.44, 22.73) * mm, "end": v(-7.46, 22.77) * mm});
            skLineSegment(sketch, "E1214", {"start": v(-7.46, 22.77) * mm, "end": v(-7.49, 22.8) * mm});
            skLineSegment(sketch, "E1215", {"start": v(-7.49, 22.8) * mm, "end": v(-7.5, 22.84) * mm});
            skLineSegment(sketch, "E1216", {"start": v(-7.5, 22.84) * mm, "end": v(-7.53, 22.88) * mm});
            skLineSegment(sketch, "E1217", {"start": v(-7.53, 22.88) * mm, "end": v(-7.56, 22.92) * mm});
            skLineSegment(sketch, "E1218", {"start": v(-7.56, 22.92) * mm, "end": v(-7.58, 22.96) * mm});
            skLineSegment(sketch, "E1219", {"start": v(-7.58, 22.96) * mm, "end": v(-7.6, 23) * mm});
            skLineSegment(sketch, "E1220", {"start": v(-7.6, 23) * mm, "end": v(-7.64, 23.05) * mm});
            skLineSegment(sketch, "E1221", {"start": v(-7.64, 23.05) * mm, "end": v(-7.67, 23.1) * mm});
            skLineSegment(sketch, "E1222", {"start": v(-7.67, 23.1) * mm, "end": v(-7.7, 23.14) * mm});
            skLineSegment(sketch, "E1223", {"start": v(-7.7, 23.14) * mm, "end": v(-7.73, 23.2) * mm});
            skLineSegment(sketch, "E1224", {"start": v(-7.73, 23.2) * mm, "end": v(-7.76, 23.24) * mm});
            skLineSegment(sketch, "E1225", {"start": v(-7.76, 23.24) * mm, "end": v(-7.8, 23.3) * mm});
            skLineSegment(sketch, "E1226", {"start": v(-7.8, 23.3) * mm, "end": v(-7.84, 23.34) * mm});
            skLineSegment(sketch, "E1227", {"start": v(-7.84, 23.34) * mm, "end": v(-7.88, 23.4) * mm});
            skLineSegment(sketch, "E1228", {"start": v(-7.88, 23.4) * mm, "end": v(-7.92, 23.45) * mm});
            skLineSegment(sketch, "E1229", {"start": v(-7.92, 23.45) * mm, "end": v(-7.96, 23.5) * mm});
            skLineSegment(sketch, "E1230", {"start": v(-7.96, 23.5) * mm, "end": v(-8, 23.56) * mm});
            skLineSegment(sketch, "E1231", {"start": v(-8, 23.56) * mm, "end": v(-8.05, 23.62) * mm});
            skLineSegment(sketch, "E1232", {"start": v(-8.05, 23.62) * mm, "end": v(-8.1, 23.68) * mm});
            skLineSegment(sketch, "E1233", {"start": v(-8.1, 23.68) * mm, "end": v(-8.14, 23.73) * mm});
            skLineSegment(sketch, "E1234", {"start": v(-8.14, 23.73) * mm, "end": v(-8.2, 23.8) * mm});
            skLineSegment(sketch, "E1235", {"start": v(-8.2, 23.8) * mm, "end": v(-8.24, 23.86) * mm});
            skLineSegment(sketch, "E1236", {"start": v(-8.24, 23.86) * mm, "end": v(-8.3, 23.92) * mm});
            skLineSegment(sketch, "E1237", {"start": v(-8.3, 23.92) * mm, "end": v(-8.35, 23.98) * mm});
            skLineSegment(sketch, "E1238", {"start": v(-8.35, 23.98) * mm, "end": v(-8.4, 24.04) * mm});
            skLineSegment(sketch, "E1239", {"start": v(-8.4, 24.04) * mm, "end": v(-8.46, 24.1) * mm});
            skLineSegment(sketch, "E1240", {"start": v(-8.46, 24.1) * mm, "end": v(-8.53, 24.17) * mm});
            skLineSegment(sketch, "E1241", {"start": v(-8.53, 24.17) * mm, "end": v(-8.59, 24.24) * mm});
            skLineSegment(sketch, "E1242", {"start": v(-8.59, 24.24) * mm, "end": v(-8.65, 24.3) * mm});
            skLineSegment(sketch, "E1243", {"start": v(-8.65, 24.3) * mm, "end": v(-8.72, 24.37) * mm});
            skLineSegment(sketch, "E1244", {"start": v(-8.72, 24.37) * mm, "end": v(-8.78, 24.44) * mm});
            skLineSegment(sketch, "E1245", {"start": v(-8.78, 24.44) * mm, "end": v(-8.85, 24.5) * mm});
            skLineSegment(sketch, "E1246", {"start": v(-8.85, 24.5) * mm, "end": v(-8.92, 24.58) * mm});
            skLineSegment(sketch, "E1247", {"start": v(-8.92, 24.58) * mm, "end": v(-9, 24.65) * mm});
            skLineSegment(sketch, "E1248", {"start": v(-9, 24.65) * mm, "end": v(-9.04, 24.64) * mm});
            skLineSegment(sketch, "E1249", {"start": v(-9.04, 24.64) * mm, "end": v(-9.82, 24.34) * mm});
            skLineSegment(sketch, "E1250", {"start": v(-9.82, 24.34) * mm, "end": v(-9.86, 24.32) * mm});
            skLineSegment(sketch, "E1251", {"start": v(-9.86, 24.32) * mm, "end": v(-9.87, 24.21) * mm});
            skLineSegment(sketch, "E1252", {"start": v(-9.87, 24.21) * mm, "end": v(-9.87, 24.12) * mm});
            skLineSegment(sketch, "E1253", {"start": v(-9.87, 24.12) * mm, "end": v(-9.88, 24.02) * mm});
            skLineSegment(sketch, "E1254", {"start": v(-9.88, 24.02) * mm, "end": v(-9.88, 23.92) * mm});
            skLineSegment(sketch, "E1255", {"start": v(-9.88, 23.92) * mm, "end": v(-9.89, 23.83) * mm});
            skLineSegment(sketch, "E1256", {"start": v(-9.89, 23.83) * mm, "end": v(-9.89, 23.74) * mm});
            skLineSegment(sketch, "E1257", {"start": v(-9.89, 23.74) * mm, "end": v(-9.9, 23.65) * mm});
            skLineSegment(sketch, "E1258", {"start": v(-9.9, 23.65) * mm, "end": v(-9.9, 23.56) * mm});
            skLineSegment(sketch, "E1259", {"start": v(-9.9, 23.56) * mm, "end": v(-9.9, 23.47) * mm});
            skLineSegment(sketch, "E1260", {"start": v(-9.9, 23.47) * mm, "end": v(-9.9, 23.39) * mm});
            skLineSegment(sketch, "E1261", {"start": v(-9.9, 23.39) * mm, "end": v(-9.9, 23.3) * mm});
            skLineSegment(sketch, "E1262", {"start": v(-9.9, 23.3) * mm, "end": v(-9.89, 23.22) * mm});
            skLineSegment(sketch, "E1263", {"start": v(-9.89, 23.22) * mm, "end": v(-9.89, 23.14) * mm});
            skLineSegment(sketch, "E1264", {"start": v(-9.89, 23.14) * mm, "end": v(-9.88, 23.06) * mm});
            skLineSegment(sketch, "E1265", {"start": v(-9.88, 23.06) * mm, "end": v(-9.88, 22.99) * mm});
            skLineSegment(sketch, "E1266", {"start": v(-9.88, 22.99) * mm, "end": v(-9.87, 22.91) * mm});
            skLineSegment(sketch, "E1267", {"start": v(-9.87, 22.91) * mm, "end": v(-9.87, 22.84) * mm});
            skLineSegment(sketch, "E1268", {"start": v(-9.87, 22.84) * mm, "end": v(-9.86, 22.77) * mm});
            skLineSegment(sketch, "E1269", {"start": v(-9.86, 22.77) * mm, "end": v(-9.86, 22.7) * mm});
            skLineSegment(sketch, "E1270", {"start": v(-9.86, 22.7) * mm, "end": v(-9.85, 22.64) * mm});
            skLineSegment(sketch, "E1271", {"start": v(-9.85, 22.64) * mm, "end": v(-9.85, 22.57) * mm});
            skLineSegment(sketch, "E1272", {"start": v(-9.85, 22.57) * mm, "end": v(-9.84, 22.5) * mm});
            skLineSegment(sketch, "E1273", {"start": v(-9.84, 22.5) * mm, "end": v(-9.83, 22.45) * mm});
            skLineSegment(sketch, "E1274", {"start": v(-9.83, 22.45) * mm, "end": v(-9.82, 22.39) * mm});
            skLineSegment(sketch, "E1275", {"start": v(-9.82, 22.39) * mm, "end": v(-9.82, 22.33) * mm});
            skLineSegment(sketch, "E1276", {"start": v(-9.82, 22.33) * mm, "end": v(-9.8, 22.27) * mm});
            skLineSegment(sketch, "E1277", {"start": v(-9.8, 22.27) * mm, "end": v(-9.8, 22.22) * mm});
            skLineSegment(sketch, "E1278", {"start": v(-9.8, 22.22) * mm, "end": v(-9.79, 22.17) * mm});
            skLineSegment(sketch, "E1279", {"start": v(-9.79, 22.17) * mm, "end": v(-9.78, 22.12) * mm});
            skLineSegment(sketch, "E1280", {"start": v(-9.78, 22.12) * mm, "end": v(-9.77, 22.07) * mm});
            skLineSegment(sketch, "E1281", {"start": v(-9.77, 22.07) * mm, "end": v(-9.76, 22.02) * mm});
            skLineSegment(sketch, "E1282", {"start": v(-9.76, 22.02) * mm, "end": v(-9.75, 21.98) * mm});
            skLineSegment(sketch, "E1283", {"start": v(-9.75, 21.98) * mm, "end": v(-9.75, 21.93) * mm});
            skLineSegment(sketch, "E1284", {"start": v(-9.75, 21.93) * mm, "end": v(-9.74, 21.9) * mm});
            skLineSegment(sketch, "E1285", {"start": v(-9.74, 21.9) * mm, "end": v(-9.73, 21.85) * mm});
            skLineSegment(sketch, "E1286", {"start": v(-9.73, 21.85) * mm, "end": v(-9.72, 21.82) * mm});
            skLineSegment(sketch, "E1287", {"start": v(-9.72, 21.82) * mm, "end": v(-9.7, 21.78) * mm});
            skLineSegment(sketch, "E1288", {"start": v(-9.7, 21.78) * mm, "end": v(-9.7, 21.75) * mm});
            skLineSegment(sketch, "E1289", {"start": v(-9.7, 21.75) * mm, "end": v(-9.7, 21.72) * mm});
            skLineSegment(sketch, "E1290", {"start": v(-9.7, 21.72) * mm, "end": v(-9.68, 21.69) * mm});
            skLineSegment(sketch, "E1291", {"start": v(-9.68, 21.69) * mm, "end": v(-9.68, 21.66) * mm});
            skLineSegment(sketch, "E1292", {"start": v(-9.68, 21.66) * mm, "end": v(-9.67, 21.63) * mm});
            skLineSegment(sketch, "E1293", {"start": v(-9.67, 21.63) * mm, "end": v(-9.66, 21.6) * mm});
            skLineSegment(sketch, "E1294", {"start": v(-9.66, 21.6) * mm, "end": v(-9.65, 21.58) * mm});
            skLineSegment(sketch, "E1295", {"start": v(-9.65, 21.58) * mm, "end": v(-9.65, 21.56) * mm});
            skLineSegment(sketch, "E1296", {"start": v(-9.65, 21.56) * mm, "end": v(-9.64, 21.54) * mm});
            skLineSegment(sketch, "E1297", {"start": v(-9.64, 21.54) * mm, "end": v(-9.63, 21.52) * mm});
            skLineSegment(sketch, "E1298", {"start": v(-9.63, 21.52) * mm, "end": v(-9.63, 21.5) * mm});
            skLineSegment(sketch, "E1299", {"start": v(-9.63, 21.5) * mm, "end": v(-10.7, 21) * mm});
            skLineSegment(sketch, "E1300", {"start": v(-10.7, 21) * mm, "end": v(-10.71, 21) * mm});
            skLineSegment(sketch, "E1301", {"start": v(-10.71, 21) * mm, "end": v(-10.72, 21.02) * mm});
            skLineSegment(sketch, "E1302", {"start": v(-10.72, 21.02) * mm, "end": v(-10.73, 21.04) * mm});
            skLineSegment(sketch, "E1303", {"start": v(-10.73, 21.04) * mm, "end": v(-10.74, 21.06) * mm});
            skLineSegment(sketch, "E1304", {"start": v(-10.74, 21.06) * mm, "end": v(-10.76, 21.08) * mm});
            skLineSegment(sketch, "E1305", {"start": v(-10.76, 21.08) * mm, "end": v(-10.77, 21.1) * mm});
            skLineSegment(sketch, "E1306", {"start": v(-10.77, 21.1) * mm, "end": v(-10.79, 21.13) * mm});
            skLineSegment(sketch, "E1307", {"start": v(-10.79, 21.13) * mm, "end": v(-10.8, 21.15) * mm});
            skLineSegment(sketch, "E1308", {"start": v(-10.8, 21.15) * mm, "end": v(-10.82, 21.17) * mm});
            skLineSegment(sketch, "E1309", {"start": v(-10.82, 21.17) * mm, "end": v(-10.84, 21.2) * mm});
            skLineSegment(sketch, "E1310", {"start": v(-10.84, 21.2) * mm, "end": v(-10.86, 21.23) * mm});
            skLineSegment(sketch, "E1311", {"start": v(-10.86, 21.23) * mm, "end": v(-10.89, 21.26) * mm});
            skLineSegment(sketch, "E1312", {"start": v(-10.89, 21.26) * mm, "end": v(-10.9, 21.29) * mm});
            skLineSegment(sketch, "E1313", {"start": v(-10.9, 21.29) * mm, "end": v(-10.93, 21.32) * mm});
            skLineSegment(sketch, "E1314", {"start": v(-10.93, 21.32) * mm, "end": v(-10.96, 21.35) * mm});
            skLineSegment(sketch, "E1315", {"start": v(-10.96, 21.35) * mm, "end": v(-10.99, 21.39) * mm});
            skLineSegment(sketch, "E1316", {"start": v(-10.99, 21.39) * mm, "end": v(-11.02, 21.42) * mm});
            skLineSegment(sketch, "E1317", {"start": v(-11.02, 21.42) * mm, "end": v(-11.05, 21.46) * mm});
            skLineSegment(sketch, "E1318", {"start": v(-11.05, 21.46) * mm, "end": v(-11.08, 21.5) * mm});
            skLineSegment(sketch, "E1319", {"start": v(-11.08, 21.5) * mm, "end": v(-11.11, 21.53) * mm});
            skLineSegment(sketch, "E1320", {"start": v(-11.11, 21.53) * mm, "end": v(-11.15, 21.57) * mm});
            skLineSegment(sketch, "E1321", {"start": v(-11.15, 21.57) * mm, "end": v(-11.19, 21.61) * mm});
            skLineSegment(sketch, "E1322", {"start": v(-11.19, 21.61) * mm, "end": v(-11.22, 21.66) * mm});
            skLineSegment(sketch, "E1323", {"start": v(-11.22, 21.66) * mm, "end": v(-11.26, 21.7) * mm});
            skLineSegment(sketch, "E1324", {"start": v(-11.26, 21.7) * mm, "end": v(-11.3, 21.74) * mm});
            skLineSegment(sketch, "E1325", {"start": v(-11.3, 21.74) * mm, "end": v(-11.35, 21.79) * mm});
            skLineSegment(sketch, "E1326", {"start": v(-11.35, 21.79) * mm, "end": v(-11.4, 21.83) * mm});
            skLineSegment(sketch, "E1327", {"start": v(-11.4, 21.83) * mm, "end": v(-11.44, 21.88) * mm});
            skLineSegment(sketch, "E1328", {"start": v(-11.44, 21.88) * mm, "end": v(-11.49, 21.92) * mm});
            skLineSegment(sketch, "E1329", {"start": v(-11.49, 21.92) * mm, "end": v(-11.54, 21.97) * mm});
            skLineSegment(sketch, "E1330", {"start": v(-11.54, 21.97) * mm, "end": v(-11.59, 22.02) * mm});
            skLineSegment(sketch, "E1331", {"start": v(-11.59, 22.02) * mm, "end": v(-11.64, 22.07) * mm});
            skLineSegment(sketch, "E1332", {"start": v(-11.64, 22.07) * mm, "end": v(-11.7, 22.12) * mm});
            skLineSegment(sketch, "E1333", {"start": v(-11.7, 22.12) * mm, "end": v(-11.75, 22.17) * mm});
            skLineSegment(sketch, "E1334", {"start": v(-11.75, 22.17) * mm, "end": v(-11.81, 22.22) * mm});
            skLineSegment(sketch, "E1335", {"start": v(-11.81, 22.22) * mm, "end": v(-11.87, 22.27) * mm});
            skLineSegment(sketch, "E1336", {"start": v(-11.87, 22.27) * mm, "end": v(-11.93, 22.32) * mm});
            skLineSegment(sketch, "E1337", {"start": v(-11.93, 22.32) * mm, "end": v(-12, 22.38) * mm});
            skLineSegment(sketch, "E1338", {"start": v(-12, 22.38) * mm, "end": v(-12.06, 22.43) * mm});
            skLineSegment(sketch, "E1339", {"start": v(-12.06, 22.43) * mm, "end": v(-12.13, 22.49) * mm});
            skLineSegment(sketch, "E1340", {"start": v(-12.13, 22.49) * mm, "end": v(-12.2, 22.54) * mm});
            skLineSegment(sketch, "E1341", {"start": v(-12.2, 22.54) * mm, "end": v(-12.27, 22.6) * mm});
            skLineSegment(sketch, "E1342", {"start": v(-12.27, 22.6) * mm, "end": v(-12.35, 22.65) * mm});
            skLineSegment(sketch, "E1343", {"start": v(-12.35, 22.65) * mm, "end": v(-12.42, 22.7) * mm});
            skLineSegment(sketch, "E1344", {"start": v(-12.42, 22.7) * mm, "end": v(-12.5, 22.76) * mm});
            skLineSegment(sketch, "E1345", {"start": v(-12.5, 22.76) * mm, "end": v(-12.58, 22.82) * mm});
            skLineSegment(sketch, "E1346", {"start": v(-12.58, 22.82) * mm, "end": v(-12.66, 22.88) * mm});
            skLineSegment(sketch, "E1347", {"start": v(-12.66, 22.88) * mm, "end": v(-12.74, 22.94) * mm});
            skLineSegment(sketch, "E1348", {"start": v(-12.74, 22.94) * mm, "end": v(-12.79, 22.92) * mm});
            skLineSegment(sketch, "E1349", {"start": v(-12.79, 22.92) * mm, "end": v(-13.5, 22.5) * mm});
            skLineSegment(sketch, "E1350", {"start": v(-13.5, 22.5) * mm, "end": v(-13.54, 22.47) * mm});
            skLineSegment(sketch, "E1351", {"start": v(-13.54, 22.47) * mm, "end": v(-13.53, 22.37) * mm});
            skLineSegment(sketch, "E1352", {"start": v(-13.53, 22.37) * mm, "end": v(-13.52, 22.27) * mm});
            skLineSegment(sketch, "E1353", {"start": v(-13.52, 22.27) * mm, "end": v(-13.51, 22.18) * mm});
            skLineSegment(sketch, "E1354", {"start": v(-13.51, 22.18) * mm, "end": v(-13.5, 22.08) * mm});
            skLineSegment(sketch, "E1355", {"start": v(-13.5, 22.08) * mm, "end": v(-13.5, 21.99) * mm});
            skLineSegment(sketch, "E1356", {"start": v(-13.5, 21.99) * mm, "end": v(-13.48, 21.9) * mm});
            skLineSegment(sketch, "E1357", {"start": v(-13.48, 21.9) * mm, "end": v(-13.47, 21.8) * mm});
            skLineSegment(sketch, "E1358", {"start": v(-13.47, 21.8) * mm, "end": v(-13.46, 21.72) * mm});
            skLineSegment(sketch, "E1359", {"start": v(-13.46, 21.72) * mm, "end": v(-13.44, 21.63) * mm});
            skLineSegment(sketch, "E1360", {"start": v(-13.44, 21.63) * mm, "end": v(-13.43, 21.55) * mm});
            skLineSegment(sketch, "E1361", {"start": v(-13.43, 21.55) * mm, "end": v(-13.41, 21.47) * mm});
            skLineSegment(sketch, "E1362", {"start": v(-13.41, 21.47) * mm, "end": v(-13.4, 21.39) * mm});
            skLineSegment(sketch, "E1363", {"start": v(-13.4, 21.39) * mm, "end": v(-13.38, 21.31) * mm});
            skLineSegment(sketch, "E1364", {"start": v(-13.38, 21.31) * mm, "end": v(-13.37, 21.23) * mm});
            skLineSegment(sketch, "E1365", {"start": v(-13.37, 21.23) * mm, "end": v(-13.35, 21.16) * mm});
            skLineSegment(sketch, "E1366", {"start": v(-13.35, 21.16) * mm, "end": v(-13.34, 21.09) * mm});
            skLineSegment(sketch, "E1367", {"start": v(-13.34, 21.09) * mm, "end": v(-13.32, 21.02) * mm});
            skLineSegment(sketch, "E1368", {"start": v(-13.32, 21.02) * mm, "end": v(-13.3, 20.95) * mm});
            skLineSegment(sketch, "E1369", {"start": v(-13.3, 20.95) * mm, "end": v(-13.29, 20.88) * mm});
            skLineSegment(sketch, "E1370", {"start": v(-13.29, 20.88) * mm, "end": v(-13.27, 20.82) * mm});
            skLineSegment(sketch, "E1371", {"start": v(-13.27, 20.82) * mm, "end": v(-13.25, 20.75) * mm});
            skLineSegment(sketch, "E1372", {"start": v(-13.25, 20.75) * mm, "end": v(-13.24, 20.7) * mm});
            skLineSegment(sketch, "E1373", {"start": v(-13.24, 20.7) * mm, "end": v(-13.22, 20.63) * mm});
            skLineSegment(sketch, "E1374", {"start": v(-13.22, 20.63) * mm, "end": v(-13.2, 20.57) * mm});
            skLineSegment(sketch, "E1375", {"start": v(-13.2, 20.57) * mm, "end": v(-13.19, 20.52) * mm});
            skLineSegment(sketch, "E1376", {"start": v(-13.19, 20.52) * mm, "end": v(-13.17, 20.46) * mm});
            skLineSegment(sketch, "E1377", {"start": v(-13.17, 20.46) * mm, "end": v(-13.15, 20.41) * mm});
            skLineSegment(sketch, "E1378", {"start": v(-13.15, 20.41) * mm, "end": v(-13.14, 20.36) * mm});
            skLineSegment(sketch, "E1379", {"start": v(-13.14, 20.36) * mm, "end": v(-13.12, 20.31) * mm});
            skLineSegment(sketch, "E1380", {"start": v(-13.12, 20.31) * mm, "end": v(-13.1, 20.27) * mm});
            skLineSegment(sketch, "E1381", {"start": v(-13.1, 20.27) * mm, "end": v(-13.09, 20.22) * mm});
            skLineSegment(sketch, "E1382", {"start": v(-13.09, 20.22) * mm, "end": v(-13.07, 20.18) * mm});
            skLineSegment(sketch, "E1383", {"start": v(-13.07, 20.18) * mm, "end": v(-13.06, 20.14) * mm});
            skLineSegment(sketch, "E1384", {"start": v(-13.06, 20.14) * mm, "end": v(-13.04, 20.1) * mm});
            skLineSegment(sketch, "E1385", {"start": v(-13.04, 20.1) * mm, "end": v(-13.03, 20.06) * mm});
            skLineSegment(sketch, "E1386", {"start": v(-13.03, 20.06) * mm, "end": v(-13.01, 20.03) * mm});
            skLineSegment(sketch, "E1387", {"start": v(-13.01, 20.03) * mm, "end": v(-13, 20) * mm});
            skLineSegment(sketch, "E1388", {"start": v(-13, 20) * mm, "end": v(-12.98, 19.96) * mm});
            skLineSegment(sketch, "E1389", {"start": v(-12.98, 19.96) * mm, "end": v(-12.97, 19.93) * mm});
            skLineSegment(sketch, "E1390", {"start": v(-12.97, 19.93) * mm, "end": v(-12.96, 19.9) * mm});
            skLineSegment(sketch, "E1391", {"start": v(-12.96, 19.9) * mm, "end": v(-12.94, 19.88) * mm});
            skLineSegment(sketch, "E1392", {"start": v(-12.94, 19.88) * mm, "end": v(-12.93, 19.85) * mm});
            skLineSegment(sketch, "E1393", {"start": v(-12.93, 19.85) * mm, "end": v(-12.92, 19.83) * mm});
            skLineSegment(sketch, "E1394", {"start": v(-12.92, 19.83) * mm, "end": v(-12.91, 19.8) * mm});
            skLineSegment(sketch, "E1395", {"start": v(-12.91, 19.8) * mm, "end": v(-12.9, 19.79) * mm});
            skLineSegment(sketch, "E1396", {"start": v(-12.9, 19.79) * mm, "end": v(-12.9, 19.77) * mm});
            skLineSegment(sketch, "E1397", {"start": v(-12.9, 19.77) * mm, "end": v(-12.88, 19.75) * mm});
            skLineSegment(sketch, "E1398", {"start": v(-12.88, 19.75) * mm, "end": v(-12.88, 19.73) * mm});
            skLineSegment(sketch, "E1399", {"start": v(-12.88, 19.73) * mm, "end": v(-13.85, 19.06) * mm});
            skLineSegment(sketch, "E1400", {"start": v(-13.85, 19.06) * mm, "end": v(-13.87, 19.07) * mm});
            skLineSegment(sketch, "E1401", {"start": v(-13.87, 19.07) * mm, "end": v(-13.88, 19.09) * mm});
            skLineSegment(sketch, "E1402", {"start": v(-13.88, 19.09) * mm, "end": v(-13.9, 19.1) * mm});
            skLineSegment(sketch, "E1403", {"start": v(-13.9, 19.1) * mm, "end": v(-13.9, 19.12) * mm});
            skLineSegment(sketch, "E1404", {"start": v(-13.9, 19.12) * mm, "end": v(-13.92, 19.14) * mm});
            skLineSegment(sketch, "E1405", {"start": v(-13.92, 19.14) * mm, "end": v(-13.94, 19.16) * mm});
            skLineSegment(sketch, "E1406", {"start": v(-13.94, 19.16) * mm, "end": v(-13.96, 19.18) * mm});
            skLineSegment(sketch, "E1407", {"start": v(-13.96, 19.18) * mm, "end": v(-13.98, 19.2) * mm});
            skLineSegment(sketch, "E1408", {"start": v(-13.98, 19.2) * mm, "end": v(-14, 19.22) * mm});
            skLineSegment(sketch, "E1409", {"start": v(-14, 19.22) * mm, "end": v(-14.03, 19.24) * mm});
            skLineSegment(sketch, "E1410", {"start": v(-14.03, 19.24) * mm, "end": v(-14.05, 19.27) * mm});
            skLineSegment(sketch, "E1411", {"start": v(-14.05, 19.27) * mm, "end": v(-14.08, 19.3) * mm});
            skLineSegment(sketch, "E1412", {"start": v(-14.08, 19.3) * mm, "end": v(-14.1, 19.32) * mm});
            skLineSegment(sketch, "E1413", {"start": v(-14.1, 19.32) * mm, "end": v(-14.13, 19.35) * mm});
            skLineSegment(sketch, "E1414", {"start": v(-14.13, 19.35) * mm, "end": v(-14.17, 19.38) * mm});
            skLineSegment(sketch, "E1415", {"start": v(-14.17, 19.38) * mm, "end": v(-14.2, 19.4) * mm});
            skLineSegment(sketch, "E1416", {"start": v(-14.2, 19.4) * mm, "end": v(-14.23, 19.44) * mm});
            skLineSegment(sketch, "E1417", {"start": v(-14.23, 19.44) * mm, "end": v(-14.27, 19.47) * mm});
            skLineSegment(sketch, "E1418", {"start": v(-14.27, 19.47) * mm, "end": v(-14.3, 19.5) * mm});
            skLineSegment(sketch, "E1419", {"start": v(-14.3, 19.5) * mm, "end": v(-14.35, 19.53) * mm});
            skLineSegment(sketch, "E1420", {"start": v(-14.35, 19.53) * mm, "end": v(-14.39, 19.56) * mm});
            skLineSegment(sketch, "E1421", {"start": v(-14.39, 19.56) * mm, "end": v(-14.43, 19.6) * mm});
            skLineSegment(sketch, "E1422", {"start": v(-14.43, 19.6) * mm, "end": v(-14.47, 19.63) * mm});
            skLineSegment(sketch, "E1423", {"start": v(-14.47, 19.63) * mm, "end": v(-14.52, 19.67) * mm});
            skLineSegment(sketch, "E1424", {"start": v(-14.52, 19.67) * mm, "end": v(-14.57, 19.7) * mm});
            skLineSegment(sketch, "E1425", {"start": v(-14.57, 19.7) * mm, "end": v(-14.62, 19.74) * mm});
            skLineSegment(sketch, "E1426", {"start": v(-14.62, 19.74) * mm, "end": v(-14.67, 19.78) * mm});
            skLineSegment(sketch, "E1427", {"start": v(-14.67, 19.78) * mm, "end": v(-14.72, 19.82) * mm});
            skLineSegment(sketch, "E1428", {"start": v(-14.72, 19.82) * mm, "end": v(-14.78, 19.86) * mm});
            skLineSegment(sketch, "E1429", {"start": v(-14.78, 19.86) * mm, "end": v(-14.83, 19.9) * mm});
            skLineSegment(sketch, "E1430", {"start": v(-14.83, 19.9) * mm, "end": v(-14.9, 19.94) * mm});
            skLineSegment(sketch, "E1431", {"start": v(-14.9, 19.94) * mm, "end": v(-14.95, 19.98) * mm});
            skLineSegment(sketch, "E1432", {"start": v(-14.95, 19.98) * mm, "end": v(-15.01, 20.02) * mm});
            skLineSegment(sketch, "E1433", {"start": v(-15.01, 20.02) * mm, "end": v(-15.08, 20.06) * mm});
            skLineSegment(sketch, "E1434", {"start": v(-15.08, 20.06) * mm, "end": v(-15.14, 20.1) * mm});
            skLineSegment(sketch, "E1435", {"start": v(-15.14, 20.1) * mm, "end": v(-15.21, 20.14) * mm});
            skLineSegment(sketch, "E1436", {"start": v(-15.21, 20.14) * mm, "end": v(-15.28, 20.18) * mm});
            skLineSegment(sketch, "E1437", {"start": v(-15.28, 20.18) * mm, "end": v(-15.35, 20.23) * mm});
            skLineSegment(sketch, "E1438", {"start": v(-15.35, 20.23) * mm, "end": v(-15.42, 20.27) * mm});
            skLineSegment(sketch, "E1439", {"start": v(-15.42, 20.27) * mm, "end": v(-15.5, 20.31) * mm});
            skLineSegment(sketch, "E1440", {"start": v(-15.5, 20.31) * mm, "end": v(-15.58, 20.35) * mm});
            skLineSegment(sketch, "E1441", {"start": v(-15.58, 20.35) * mm, "end": v(-15.66, 20.4) * mm});
            skLineSegment(sketch, "E1442", {"start": v(-15.66, 20.4) * mm, "end": v(-15.74, 20.44) * mm});
            skLineSegment(sketch, "E1443", {"start": v(-15.74, 20.44) * mm, "end": v(-15.82, 20.49) * mm});
            skLineSegment(sketch, "E1444", {"start": v(-15.82, 20.49) * mm, "end": v(-15.9, 20.53) * mm});
            skLineSegment(sketch, "E1445", {"start": v(-15.9, 20.53) * mm, "end": v(-16, 20.57) * mm});
            skLineSegment(sketch, "E1446", {"start": v(-16, 20.57) * mm, "end": v(-16.08, 20.62) * mm});
            skLineSegment(sketch, "E1447", {"start": v(-16.08, 20.62) * mm, "end": v(-16.17, 20.66) * mm});
            skLineSegment(sketch, "E1448", {"start": v(-16.17, 20.66) * mm, "end": v(-16.22, 20.64) * mm});
            skLineSegment(sketch, "E1449", {"start": v(-16.22, 20.64) * mm, "end": v(-16.86, 20.12) * mm});
            skLineSegment(sketch, "E1450", {"start": v(-16.86, 20.12) * mm, "end": v(-16.9, 20.08) * mm});
            skLineSegment(sketch, "E1451", {"start": v(-16.9, 20.08) * mm, "end": v(-16.87, 19.98) * mm});
            skLineSegment(sketch, "E1452", {"start": v(-16.87, 19.98) * mm, "end": v(-16.84, 19.88) * mm});
            skLineSegment(sketch, "E1453", {"start": v(-16.84, 19.88) * mm, "end": v(-16.82, 19.79) * mm});
            skLineSegment(sketch, "E1454", {"start": v(-16.82, 19.79) * mm, "end": v(-16.8, 19.7) * mm});
            skLineSegment(sketch, "E1455", {"start": v(-16.8, 19.7) * mm, "end": v(-16.77, 19.6) * mm});
            skLineSegment(sketch, "E1456", {"start": v(-16.77, 19.6) * mm, "end": v(-16.74, 19.52) * mm});
            skLineSegment(sketch, "E1457", {"start": v(-16.74, 19.52) * mm, "end": v(-16.71, 19.43) * mm});
            skLineSegment(sketch, "E1458", {"start": v(-16.71, 19.43) * mm, "end": v(-16.69, 19.35) * mm});
            skLineSegment(sketch, "E1459", {"start": v(-16.69, 19.35) * mm, "end": v(-16.66, 19.26) * mm});
            skLineSegment(sketch, "E1460", {"start": v(-16.66, 19.26) * mm, "end": v(-16.63, 19.18) * mm});
            skLineSegment(sketch, "E1461", {"start": v(-16.63, 19.18) * mm, "end": v(-16.6, 19.1) * mm});
            skLineSegment(sketch, "E1462", {"start": v(-16.6, 19.1) * mm, "end": v(-16.58, 19.03) * mm});
            skLineSegment(sketch, "E1463", {"start": v(-16.58, 19.03) * mm, "end": v(-16.55, 18.95) * mm});
            skLineSegment(sketch, "E1464", {"start": v(-16.55, 18.95) * mm, "end": v(-16.53, 18.88) * mm});
            skLineSegment(sketch, "E1465", {"start": v(-16.53, 18.88) * mm, "end": v(-16.5, 18.8) * mm});
            skLineSegment(sketch, "E1466", {"start": v(-16.5, 18.8) * mm, "end": v(-16.47, 18.74) * mm});
            skLineSegment(sketch, "E1467", {"start": v(-16.47, 18.74) * mm, "end": v(-16.44, 18.67) * mm});
            skLineSegment(sketch, "E1468", {"start": v(-16.44, 18.67) * mm, "end": v(-16.42, 18.6) * mm});
            skLineSegment(sketch, "E1469", {"start": v(-16.42, 18.6) * mm, "end": v(-16.4, 18.54) * mm});
            skLineSegment(sketch, "E1470", {"start": v(-16.4, 18.54) * mm, "end": v(-16.36, 18.48) * mm});
            skLineSegment(sketch, "E1471", {"start": v(-16.36, 18.48) * mm, "end": v(-16.34, 18.42) * mm});
            skLineSegment(sketch, "E1472", {"start": v(-16.34, 18.42) * mm, "end": v(-16.31, 18.37) * mm});
            skLineSegment(sketch, "E1473", {"start": v(-16.31, 18.37) * mm, "end": v(-16.29, 18.3) * mm});
            skLineSegment(sketch, "E1474", {"start": v(-16.29, 18.3) * mm, "end": v(-16.26, 18.26) * mm});
            skLineSegment(sketch, "E1475", {"start": v(-16.26, 18.26) * mm, "end": v(-16.23, 18.2) * mm});
            skLineSegment(sketch, "E1476", {"start": v(-16.23, 18.2) * mm, "end": v(-16.2, 18.15) * mm});
            skLineSegment(sketch, "E1477", {"start": v(-16.2, 18.15) * mm, "end": v(-16.19, 18.1) * mm});
            skLineSegment(sketch, "E1478", {"start": v(-16.19, 18.1) * mm, "end": v(-16.16, 18.06) * mm});
            skLineSegment(sketch, "E1479", {"start": v(-16.16, 18.06) * mm, "end": v(-16.14, 18.01) * mm});
            skLineSegment(sketch, "E1480", {"start": v(-16.14, 18.01) * mm, "end": v(-16.11, 17.97) * mm});
            skLineSegment(sketch, "E1481", {"start": v(-16.11, 17.97) * mm, "end": v(-16.1, 17.93) * mm});
            skLineSegment(sketch, "E1482", {"start": v(-16.1, 17.93) * mm, "end": v(-16.07, 17.89) * mm});
            skLineSegment(sketch, "E1483", {"start": v(-16.07, 17.89) * mm, "end": v(-16.05, 17.85) * mm});
            skLineSegment(sketch, "E1484", {"start": v(-16.05, 17.85) * mm, "end": v(-16.03, 17.81) * mm});
            skLineSegment(sketch, "E1485", {"start": v(-16.03, 17.81) * mm, "end": v(-16, 17.78) * mm});
            skLineSegment(sketch, "E1486", {"start": v(-16, 17.78) * mm, "end": v(-15.98, 17.75) * mm});
            skLineSegment(sketch, "E1487", {"start": v(-15.98, 17.75) * mm, "end": v(-15.97, 17.71) * mm});
            skLineSegment(sketch, "E1488", {"start": v(-15.97, 17.71) * mm, "end": v(-15.95, 17.69) * mm});
            skLineSegment(sketch, "E1489", {"start": v(-15.95, 17.69) * mm, "end": v(-15.93, 17.66) * mm});
            skLineSegment(sketch, "E1490", {"start": v(-15.93, 17.66) * mm, "end": v(-15.91, 17.63) * mm});
            skLineSegment(sketch, "E1491", {"start": v(-15.91, 17.63) * mm, "end": v(-15.9, 17.6) * mm});
            skLineSegment(sketch, "E1492", {"start": v(-15.9, 17.6) * mm, "end": v(-15.88, 17.58) * mm});
            skLineSegment(sketch, "E1493", {"start": v(-15.88, 17.58) * mm, "end": v(-15.86, 17.56) * mm});
            skLineSegment(sketch, "E1494", {"start": v(-15.86, 17.56) * mm, "end": v(-15.85, 17.54) * mm});
            skLineSegment(sketch, "E1495", {"start": v(-15.85, 17.54) * mm, "end": v(-15.84, 17.52) * mm});
            skLineSegment(sketch, "E1496", {"start": v(-15.84, 17.52) * mm, "end": v(-15.83, 17.5) * mm});
            skLineSegment(sketch, "E1497", {"start": v(-15.83, 17.5) * mm, "end": v(-15.81, 17.5) * mm});
            skLineSegment(sketch, "E1498", {"start": v(-15.81, 17.5) * mm, "end": v(-15.8, 17.48) * mm});
            skLineSegment(sketch, "E1499", {"start": v(-15.8, 17.48) * mm, "end": v(-16.66, 16.66) * mm});
            skLineSegment(sketch, "E1500", {"start": v(-16.66, 16.66) * mm, "end": v(-16.68, 16.67) * mm});
            skLineSegment(sketch, "E1501", {"start": v(-16.68, 16.67) * mm, "end": v(-16.7, 16.68) * mm});
            skLineSegment(sketch, "E1502", {"start": v(-16.7, 16.68) * mm, "end": v(-16.7, 16.7) * mm});
            skLineSegment(sketch, "E1503", {"start": v(-16.7, 16.7) * mm, "end": v(-16.73, 16.71) * mm});
            skLineSegment(sketch, "E1504", {"start": v(-16.73, 16.71) * mm, "end": v(-16.75, 16.73) * mm});
            skLineSegment(sketch, "E1505", {"start": v(-16.75, 16.73) * mm, "end": v(-16.77, 16.74) * mm});
            skLineSegment(sketch, "E1506", {"start": v(-16.77, 16.74) * mm, "end": v(-16.79, 16.76) * mm});
            skLineSegment(sketch, "E1507", {"start": v(-16.79, 16.76) * mm, "end": v(-16.81, 16.78) * mm});
            skLineSegment(sketch, "E1508", {"start": v(-16.81, 16.78) * mm, "end": v(-16.84, 16.8) * mm});
            skLineSegment(sketch, "E1509", {"start": v(-16.84, 16.8) * mm, "end": v(-16.86, 16.81) * mm});
            skLineSegment(sketch, "E1510", {"start": v(-16.86, 16.81) * mm, "end": v(-16.9, 16.83) * mm});
            skLineSegment(sketch, "E1511", {"start": v(-16.9, 16.83) * mm, "end": v(-16.92, 16.85) * mm});
            skLineSegment(sketch, "E1512", {"start": v(-16.92, 16.85) * mm, "end": v(-16.95, 16.88) * mm});
            skLineSegment(sketch, "E1513", {"start": v(-16.95, 16.88) * mm, "end": v(-16.99, 16.9) * mm});
            skLineSegment(sketch, "E1514", {"start": v(-16.99, 16.9) * mm, "end": v(-17.02, 16.92) * mm});
            skLineSegment(sketch, "E1515", {"start": v(-17.02, 16.92) * mm, "end": v(-17.06, 16.95) * mm});
            skLineSegment(sketch, "E1516", {"start": v(-17.06, 16.95) * mm, "end": v(-17.1, 16.97) * mm});
            skLineSegment(sketch, "E1517", {"start": v(-17.1, 16.97) * mm, "end": v(-17.14, 17) * mm});
            skLineSegment(sketch, "E1518", {"start": v(-17.14, 17) * mm, "end": v(-17.18, 17.02) * mm});
            skLineSegment(sketch, "E1519", {"start": v(-17.18, 17.02) * mm, "end": v(-17.22, 17.05) * mm});
            skLineSegment(sketch, "E1520", {"start": v(-17.22, 17.05) * mm, "end": v(-17.27, 17.07) * mm});
            skLineSegment(sketch, "E1521", {"start": v(-17.27, 17.07) * mm, "end": v(-17.32, 17.1) * mm});
            skLineSegment(sketch, "E1522", {"start": v(-17.32, 17.1) * mm, "end": v(-17.37, 17.13) * mm});
            skLineSegment(sketch, "E1523", {"start": v(-17.37, 17.13) * mm, "end": v(-17.42, 17.16) * mm});
            skLineSegment(sketch, "E1524", {"start": v(-17.42, 17.16) * mm, "end": v(-17.47, 17.18) * mm});
            skLineSegment(sketch, "E1525", {"start": v(-17.47, 17.18) * mm, "end": v(-17.52, 17.21) * mm});
            skLineSegment(sketch, "E1526", {"start": v(-17.52, 17.21) * mm, "end": v(-17.58, 17.24) * mm});
            skLineSegment(sketch, "E1527", {"start": v(-17.58, 17.24) * mm, "end": v(-17.64, 17.27) * mm});
            skLineSegment(sketch, "E1528", {"start": v(-17.64, 17.27) * mm, "end": v(-17.7, 17.3) * mm});
            skLineSegment(sketch, "E1529", {"start": v(-17.7, 17.3) * mm, "end": v(-17.76, 17.33) * mm});
            skLineSegment(sketch, "E1530", {"start": v(-17.76, 17.33) * mm, "end": v(-17.83, 17.36) * mm});
            skLineSegment(sketch, "E1531", {"start": v(-17.83, 17.36) * mm, "end": v(-17.9, 17.4) * mm});
            skLineSegment(sketch, "E1532", {"start": v(-17.9, 17.4) * mm, "end": v(-17.96, 17.42) * mm});
            skLineSegment(sketch, "E1533", {"start": v(-17.96, 17.42) * mm, "end": v(-18.03, 17.45) * mm});
            skLineSegment(sketch, "E1534", {"start": v(-18.03, 17.45) * mm, "end": v(-18.1, 17.48) * mm});
            skLineSegment(sketch, "E1535", {"start": v(-18.1, 17.48) * mm, "end": v(-18.17, 17.51) * mm});
            skLineSegment(sketch, "E1536", {"start": v(-18.17, 17.51) * mm, "end": v(-18.25, 17.54) * mm});
            skLineSegment(sketch, "E1537", {"start": v(-18.25, 17.54) * mm, "end": v(-18.33, 17.57) * mm});
            skLineSegment(sketch, "E1538", {"start": v(-18.33, 17.57) * mm, "end": v(-18.4, 17.6) * mm});
            skLineSegment(sketch, "E1539", {"start": v(-18.4, 17.6) * mm, "end": v(-18.49, 17.64) * mm});
            skLineSegment(sketch, "E1540", {"start": v(-18.49, 17.64) * mm, "end": v(-18.57, 17.67) * mm});
            skLineSegment(sketch, "E1541", {"start": v(-18.57, 17.67) * mm, "end": v(-18.65, 17.7) * mm});
            skLineSegment(sketch, "E1542", {"start": v(-18.65, 17.7) * mm, "end": v(-18.74, 17.73) * mm});
            skLineSegment(sketch, "E1543", {"start": v(-18.74, 17.73) * mm, "end": v(-18.83, 17.76) * mm});
            skLineSegment(sketch, "E1544", {"start": v(-18.83, 17.76) * mm, "end": v(-18.92, 17.79) * mm});
            skLineSegment(sketch, "E1545", {"start": v(-18.92, 17.79) * mm, "end": v(-19.01, 17.82) * mm});
            skLineSegment(sketch, "E1546", {"start": v(-19.01, 17.82) * mm, "end": v(-19.1, 17.85) * mm});
            skLineSegment(sketch, "E1547", {"start": v(-19.1, 17.85) * mm, "end": v(-19.2, 17.88) * mm});
            skLineSegment(sketch, "E1548", {"start": v(-19.2, 17.88) * mm, "end": v(-19.25, 17.85) * mm});
            skLineSegment(sketch, "E1549", {"start": v(-19.25, 17.85) * mm, "end": v(-19.8, 17.23) * mm});
            skLineSegment(sketch, "E1550", {"start": v(-19.8, 17.23) * mm, "end": v(-19.82, 17.19) * mm});
            skLineSegment(sketch, "E1551", {"start": v(-19.82, 17.19) * mm, "end": v(-19.78, 17.1) * mm});
            skLineSegment(sketch, "E1552", {"start": v(-19.78, 17.1) * mm, "end": v(-19.75, 17) * mm});
            skLineSegment(sketch, "E1553", {"start": v(-19.75, 17) * mm, "end": v(-19.7, 16.92) * mm});
            skLineSegment(sketch, "E1554", {"start": v(-19.7, 16.92) * mm, "end": v(-19.67, 16.83) * mm});
            skLineSegment(sketch, "E1555", {"start": v(-19.67, 16.83) * mm, "end": v(-19.63, 16.74) * mm});
            skLineSegment(sketch, "E1556", {"start": v(-19.63, 16.74) * mm, "end": v(-19.59, 16.66) * mm});
            skLineSegment(sketch, "E1557", {"start": v(-19.59, 16.66) * mm, "end": v(-19.55, 16.58) * mm});
            skLineSegment(sketch, "E1558", {"start": v(-19.55, 16.58) * mm, "end": v(-19.5, 16.5) * mm});
            skLineSegment(sketch, "E1559", {"start": v(-19.5, 16.5) * mm, "end": v(-19.47, 16.42) * mm});
            skLineSegment(sketch, "E1560", {"start": v(-19.47, 16.42) * mm, "end": v(-19.43, 16.35) * mm});
            skLineSegment(sketch, "E1561", {"start": v(-19.43, 16.35) * mm, "end": v(-19.4, 16.27) * mm});
            skLineSegment(sketch, "E1562", {"start": v(-19.4, 16.27) * mm, "end": v(-19.35, 16.2) * mm});
            skLineSegment(sketch, "E1563", {"start": v(-19.35, 16.2) * mm, "end": v(-19.31, 16.13) * mm});
            skLineSegment(sketch, "E1564", {"start": v(-19.31, 16.13) * mm, "end": v(-19.28, 16.06) * mm});
            skLineSegment(sketch, "E1565", {"start": v(-19.28, 16.06) * mm, "end": v(-19.24, 16) * mm});
            skLineSegment(sketch, "E1566", {"start": v(-19.24, 16) * mm, "end": v(-19.2, 15.93) * mm});
            skLineSegment(sketch, "E1567", {"start": v(-19.2, 15.93) * mm, "end": v(-19.16, 15.87) * mm});
            skLineSegment(sketch, "E1568", {"start": v(-19.16, 15.87) * mm, "end": v(-19.13, 15.81) * mm});
            skLineSegment(sketch, "E1569", {"start": v(-19.13, 15.81) * mm, "end": v(-19.1, 15.75) * mm});
            skLineSegment(sketch, "E1570", {"start": v(-19.1, 15.75) * mm, "end": v(-19.05, 15.7) * mm});
            skLineSegment(sketch, "E1571", {"start": v(-19.05, 15.7) * mm, "end": v(-19.02, 15.64) * mm});
            skLineSegment(sketch, "E1572", {"start": v(-19.02, 15.64) * mm, "end": v(-18.98, 15.59) * mm});
            skLineSegment(sketch, "E1573", {"start": v(-18.98, 15.59) * mm, "end": v(-18.95, 15.54) * mm});
            skLineSegment(sketch, "E1574", {"start": v(-18.95, 15.54) * mm, "end": v(-18.92, 15.49) * mm});
            skLineSegment(sketch, "E1575", {"start": v(-18.92, 15.49) * mm, "end": v(-18.88, 15.44) * mm});
            skLineSegment(sketch, "E1576", {"start": v(-18.88, 15.44) * mm, "end": v(-18.85, 15.4) * mm});
            skLineSegment(sketch, "E1577", {"start": v(-18.85, 15.4) * mm, "end": v(-18.82, 15.35) * mm});
            skLineSegment(sketch, "E1578", {"start": v(-18.82, 15.35) * mm, "end": v(-18.79, 15.3) * mm});
            skLineSegment(sketch, "E1579", {"start": v(-18.79, 15.3) * mm, "end": v(-18.76, 15.27) * mm});
            skLineSegment(sketch, "E1580", {"start": v(-18.76, 15.27) * mm, "end": v(-18.73, 15.23) * mm});
            skLineSegment(sketch, "E1581", {"start": v(-18.73, 15.23) * mm, "end": v(-18.7, 15.19) * mm});
            skLineSegment(sketch, "E1582", {"start": v(-18.7, 15.19) * mm, "end": v(-18.67, 15.15) * mm});
            skLineSegment(sketch, "E1583", {"start": v(-18.67, 15.15) * mm, "end": v(-18.64, 15.12) * mm});
            skLineSegment(sketch, "E1584", {"start": v(-18.64, 15.12) * mm, "end": v(-18.61, 15.09) * mm});
            skLineSegment(sketch, "E1585", {"start": v(-18.61, 15.09) * mm, "end": v(-18.59, 15.06) * mm});
            skLineSegment(sketch, "E1586", {"start": v(-18.59, 15.06) * mm, "end": v(-18.56, 15.03) * mm});
            skLineSegment(sketch, "E1587", {"start": v(-18.56, 15.03) * mm, "end": v(-18.54, 15) * mm});
            skLineSegment(sketch, "E1588", {"start": v(-18.54, 15) * mm, "end": v(-18.52, 14.97) * mm});
            skLineSegment(sketch, "E1589", {"start": v(-18.52, 14.97) * mm, "end": v(-18.5, 14.95) * mm});
            skLineSegment(sketch, "E1590", {"start": v(-18.5, 14.95) * mm, "end": v(-18.47, 14.93) * mm});
            skLineSegment(sketch, "E1591", {"start": v(-18.47, 14.93) * mm, "end": v(-18.45, 14.9) * mm});
            skLineSegment(sketch, "E1592", {"start": v(-18.45, 14.9) * mm, "end": v(-18.43, 14.88) * mm});
            skLineSegment(sketch, "E1593", {"start": v(-18.43, 14.88) * mm, "end": v(-18.42, 14.86) * mm});
            skLineSegment(sketch, "E1594", {"start": v(-18.42, 14.86) * mm, "end": v(-18.4, 14.85) * mm});
            skLineSegment(sketch, "E1595", {"start": v(-18.4, 14.85) * mm, "end": v(-18.38, 14.83) * mm});
            skLineSegment(sketch, "E1596", {"start": v(-18.38, 14.83) * mm, "end": v(-18.37, 14.82) * mm});
            skLineSegment(sketch, "E1597", {"start": v(-18.37, 14.82) * mm, "end": v(-18.36, 14.8) * mm});
            skLineSegment(sketch, "E1598", {"start": v(-18.36, 14.8) * mm, "end": v(-18.34, 14.79) * mm});
            skLineSegment(sketch, "E1599", {"start": v(-18.34, 14.79) * mm, "end": v(-19.06, 13.85) * mm});
            skLineSegment(sketch, "E1600", {"start": v(-19.06, 13.85) * mm, "end": v(-19.08, 13.86) * mm});
            skLineSegment(sketch, "E1601", {"start": v(-19.08, 13.86) * mm, "end": v(-19.1, 13.87) * mm});
            skLineSegment(sketch, "E1602", {"start": v(-19.1, 13.87) * mm, "end": v(-19.11, 13.88) * mm});
            skLineSegment(sketch, "E1603", {"start": v(-19.11, 13.88) * mm, "end": v(-19.13, 13.89) * mm});
            skLineSegment(sketch, "E1604", {"start": v(-19.13, 13.89) * mm, "end": v(-19.16, 13.9) * mm});
            skLineSegment(sketch, "E1605", {"start": v(-19.16, 13.9) * mm, "end": v(-19.18, 13.91) * mm});
            skLineSegment(sketch, "E1606", {"start": v(-19.18, 13.91) * mm, "end": v(-19.2, 13.93) * mm});
            skLineSegment(sketch, "E1607", {"start": v(-19.2, 13.93) * mm, "end": v(-19.23, 13.94) * mm});
            skLineSegment(sketch, "E1608", {"start": v(-19.23, 13.94) * mm, "end": v(-19.26, 13.95) * mm});
            skLineSegment(sketch, "E1609", {"start": v(-19.26, 13.95) * mm, "end": v(-19.29, 13.97) * mm});
            skLineSegment(sketch, "E1610", {"start": v(-19.29, 13.97) * mm, "end": v(-19.32, 13.98) * mm});
            skLineSegment(sketch, "E1611", {"start": v(-19.32, 13.98) * mm, "end": v(-19.35, 14) * mm});
            skLineSegment(sketch, "E1612", {"start": v(-19.35, 14) * mm, "end": v(-19.39, 14.02) * mm});
            skLineSegment(sketch, "E1613", {"start": v(-19.39, 14.02) * mm, "end": v(-19.42, 14.03) * mm});
            skLineSegment(sketch, "E1614", {"start": v(-19.42, 14.03) * mm, "end": v(-19.46, 14.05) * mm});
            skLineSegment(sketch, "E1615", {"start": v(-19.46, 14.05) * mm, "end": v(-19.5, 14.07) * mm});
            skLineSegment(sketch, "E1616", {"start": v(-19.5, 14.07) * mm, "end": v(-19.54, 14.09) * mm});
            skLineSegment(sketch, "E1617", {"start": v(-19.54, 14.09) * mm, "end": v(-19.59, 14.1) * mm});
            skLineSegment(sketch, "E1618", {"start": v(-19.59, 14.1) * mm, "end": v(-19.63, 14.12) * mm});
            skLineSegment(sketch, "E1619", {"start": v(-19.63, 14.12) * mm, "end": v(-19.68, 14.14) * mm});
            skLineSegment(sketch, "E1620", {"start": v(-19.68, 14.14) * mm, "end": v(-19.73, 14.16) * mm});
            skLineSegment(sketch, "E1621", {"start": v(-19.73, 14.16) * mm, "end": v(-19.78, 14.18) * mm});
            skLineSegment(sketch, "E1622", {"start": v(-19.78, 14.18) * mm, "end": v(-19.83, 14.2) * mm});
            skLineSegment(sketch, "E1623", {"start": v(-19.83, 14.2) * mm, "end": v(-19.89, 14.22) * mm});
            skLineSegment(sketch, "E1624", {"start": v(-19.89, 14.22) * mm, "end": v(-19.94, 14.24) * mm});
            skLineSegment(sketch, "E1625", {"start": v(-19.94, 14.24) * mm, "end": v(-20, 14.26) * mm});
            skLineSegment(sketch, "E1626", {"start": v(-20, 14.26) * mm, "end": v(-20.06, 14.28) * mm});
            skLineSegment(sketch, "E1627", {"start": v(-20.06, 14.28) * mm, "end": v(-20.12, 14.3) * mm});
            skLineSegment(sketch, "E1628", {"start": v(-20.12, 14.3) * mm, "end": v(-20.19, 14.32) * mm});
            skLineSegment(sketch, "E1629", {"start": v(-20.19, 14.32) * mm, "end": v(-20.25, 14.34) * mm});
            skLineSegment(sketch, "E1630", {"start": v(-20.25, 14.34) * mm, "end": v(-20.32, 14.36) * mm});
            skLineSegment(sketch, "E1631", {"start": v(-20.32, 14.36) * mm, "end": v(-20.4, 14.38) * mm});
            skLineSegment(sketch, "E1632", {"start": v(-20.4, 14.38) * mm, "end": v(-20.46, 14.4) * mm});
            skLineSegment(sketch, "E1633", {"start": v(-20.46, 14.4) * mm, "end": v(-20.54, 14.42) * mm});
            skLineSegment(sketch, "E1634", {"start": v(-20.54, 14.42) * mm, "end": v(-20.61, 14.44) * mm});
            skLineSegment(sketch, "E1635", {"start": v(-20.61, 14.44) * mm, "end": v(-20.69, 14.45) * mm});
            skLineSegment(sketch, "E1636", {"start": v(-20.69, 14.45) * mm, "end": v(-20.77, 14.47) * mm});
            skLineSegment(sketch, "E1637", {"start": v(-20.77, 14.47) * mm, "end": v(-20.85, 14.5) * mm});
            skLineSegment(sketch, "E1638", {"start": v(-20.85, 14.5) * mm, "end": v(-20.93, 14.5) * mm});
            skLineSegment(sketch, "E1639", {"start": v(-20.93, 14.5) * mm, "end": v(-21.02, 14.53) * mm});
            skLineSegment(sketch, "E1640", {"start": v(-21.02, 14.53) * mm, "end": v(-21.1, 14.54) * mm});
            skLineSegment(sketch, "E1641", {"start": v(-21.1, 14.54) * mm, "end": v(-21.2, 14.56) * mm});
            skLineSegment(sketch, "E1642", {"start": v(-21.2, 14.56) * mm, "end": v(-21.28, 14.58) * mm});
            skLineSegment(sketch, "E1643", {"start": v(-21.28, 14.58) * mm, "end": v(-21.38, 14.6) * mm});
            skLineSegment(sketch, "E1644", {"start": v(-21.38, 14.6) * mm, "end": v(-21.47, 14.6) * mm});
            skLineSegment(sketch, "E1645", {"start": v(-21.47, 14.6) * mm, "end": v(-21.57, 14.62) * mm});
            skLineSegment(sketch, "E1646", {"start": v(-21.57, 14.62) * mm, "end": v(-21.67, 14.64) * mm});
            skLineSegment(sketch, "E1647", {"start": v(-21.67, 14.64) * mm, "end": v(-21.77, 14.65) * mm});
            skLineSegment(sketch, "E1648", {"start": v(-21.77, 14.65) * mm, "end": v(-21.8, 14.62) * mm});
            skLineSegment(sketch, "E1649", {"start": v(-21.8, 14.62) * mm, "end": v(-22.25, 13.92) * mm});
            skLineSegment(sketch, "E1650", {"start": v(-22.25, 13.92) * mm, "end": v(-22.27, 13.88) * mm});
            skLineSegment(sketch, "E1651", {"start": v(-22.27, 13.88) * mm, "end": v(-22.22, 13.79) * mm});
            skLineSegment(sketch, "E1652", {"start": v(-22.22, 13.79) * mm, "end": v(-22.16, 13.7) * mm});
            skLineSegment(sketch, "E1653", {"start": v(-22.16, 13.7) * mm, "end": v(-22.1, 13.62) * mm});
            skLineSegment(sketch, "E1654", {"start": v(-22.1, 13.62) * mm, "end": v(-22.06, 13.54) * mm});
            skLineSegment(sketch, "E1655", {"start": v(-22.06, 13.54) * mm, "end": v(-22, 13.47) * mm});
            skLineSegment(sketch, "E1656", {"start": v(-22, 13.47) * mm, "end": v(-21.95, 13.4) * mm});
            skLineSegment(sketch, "E1657", {"start": v(-21.95, 13.4) * mm, "end": v(-21.9, 13.32) * mm});
            skLineSegment(sketch, "E1658", {"start": v(-21.9, 13.32) * mm, "end": v(-21.85, 13.24) * mm});
            skLineSegment(sketch, "E1659", {"start": v(-21.85, 13.24) * mm, "end": v(-21.8, 13.17) * mm});
            skLineSegment(sketch, "E1660", {"start": v(-21.8, 13.17) * mm, "end": v(-21.75, 13.1) * mm});
            skLineSegment(sketch, "E1661", {"start": v(-21.75, 13.1) * mm, "end": v(-21.7, 13.04) * mm});
            skLineSegment(sketch, "E1662", {"start": v(-21.7, 13.04) * mm, "end": v(-21.65, 12.97) * mm});
            skLineSegment(sketch, "E1663", {"start": v(-21.65, 12.97) * mm, "end": v(-21.6, 12.91) * mm});
            skLineSegment(sketch, "E1664", {"start": v(-21.6, 12.91) * mm, "end": v(-21.55, 12.85) * mm});
            skLineSegment(sketch, "E1665", {"start": v(-21.55, 12.85) * mm, "end": v(-21.5, 12.8) * mm});
            skLineSegment(sketch, "E1666", {"start": v(-21.5, 12.8) * mm, "end": v(-21.46, 12.73) * mm});
            skLineSegment(sketch, "E1667", {"start": v(-21.46, 12.73) * mm, "end": v(-21.41, 12.68) * mm});
            skLineSegment(sketch, "E1668", {"start": v(-21.41, 12.68) * mm, "end": v(-21.36, 12.62) * mm});
            skLineSegment(sketch, "E1669", {"start": v(-21.36, 12.62) * mm, "end": v(-21.32, 12.57) * mm});
            skLineSegment(sketch, "E1670", {"start": v(-21.32, 12.57) * mm, "end": v(-21.28, 12.52) * mm});
            skLineSegment(sketch, "E1671", {"start": v(-21.28, 12.52) * mm, "end": v(-21.23, 12.47) * mm});
            skLineSegment(sketch, "E1672", {"start": v(-21.23, 12.47) * mm, "end": v(-21.19, 12.43) * mm});
            skLineSegment(sketch, "E1673", {"start": v(-21.19, 12.43) * mm, "end": v(-21.15, 12.38) * mm});
            skLineSegment(sketch, "E1674", {"start": v(-21.15, 12.38) * mm, "end": v(-21.1, 12.34) * mm});
            skLineSegment(sketch, "E1675", {"start": v(-21.1, 12.34) * mm, "end": v(-21.07, 12.3) * mm});
            skLineSegment(sketch, "E1676", {"start": v(-21.07, 12.3) * mm, "end": v(-21.03, 12.26) * mm});
            skLineSegment(sketch, "E1677", {"start": v(-21.03, 12.26) * mm, "end": v(-20.99, 12.22) * mm});
            skLineSegment(sketch, "E1678", {"start": v(-20.99, 12.22) * mm, "end": v(-20.95, 12.18) * mm});
            skLineSegment(sketch, "E1679", {"start": v(-20.95, 12.18) * mm, "end": v(-20.91, 12.14) * mm});
            skLineSegment(sketch, "E1680", {"start": v(-20.91, 12.14) * mm, "end": v(-20.88, 12.1) * mm});
            skLineSegment(sketch, "E1681", {"start": v(-20.88, 12.1) * mm, "end": v(-20.84, 12.08) * mm});
            skLineSegment(sketch, "E1682", {"start": v(-20.84, 12.08) * mm, "end": v(-20.8, 12.05) * mm});
            skLineSegment(sketch, "E1683", {"start": v(-20.8, 12.05) * mm, "end": v(-20.78, 12.02) * mm});
            skLineSegment(sketch, "E1684", {"start": v(-20.78, 12.02) * mm, "end": v(-20.75, 11.99) * mm});
            skLineSegment(sketch, "E1685", {"start": v(-20.75, 11.99) * mm, "end": v(-20.72, 11.96) * mm});
            skLineSegment(sketch, "E1686", {"start": v(-20.72, 11.96) * mm, "end": v(-20.69, 11.94) * mm});
            skLineSegment(sketch, "E1687", {"start": v(-20.69, 11.94) * mm, "end": v(-20.66, 11.91) * mm});
            skLineSegment(sketch, "E1688", {"start": v(-20.66, 11.91) * mm, "end": v(-20.63, 11.9) * mm});
            skLineSegment(sketch, "E1689", {"start": v(-20.63, 11.9) * mm, "end": v(-20.6, 11.87) * mm});
            skLineSegment(sketch, "E1690", {"start": v(-20.6, 11.87) * mm, "end": v(-20.58, 11.85) * mm});
            skLineSegment(sketch, "E1691", {"start": v(-20.58, 11.85) * mm, "end": v(-20.56, 11.83) * mm});
            skLineSegment(sketch, "E1692", {"start": v(-20.56, 11.83) * mm, "end": v(-20.54, 11.82) * mm});
            skLineSegment(sketch, "E1693", {"start": v(-20.54, 11.82) * mm, "end": v(-20.52, 11.8) * mm});
            skLineSegment(sketch, "E1694", {"start": v(-20.52, 11.8) * mm, "end": v(-20.5, 11.79) * mm});
            skLineSegment(sketch, "E1695", {"start": v(-20.5, 11.79) * mm, "end": v(-20.48, 11.77) * mm});
            skLineSegment(sketch, "E1696", {"start": v(-20.48, 11.77) * mm, "end": v(-20.46, 11.76) * mm});
            skLineSegment(sketch, "E1697", {"start": v(-20.46, 11.76) * mm, "end": v(-20.45, 11.75) * mm});
            skLineSegment(sketch, "E1698", {"start": v(-20.45, 11.75) * mm, "end": v(-20.43, 11.74) * mm});
            skLineSegment(sketch, "E1699", {"start": v(-20.43, 11.74) * mm, "end": v(-21, 10.7) * mm});
            skLineSegment(sketch, "E1700", {"start": v(-21, 10.7) * mm, "end": v(-21.01, 10.7) * mm});
            skLineSegment(sketch, "E1701", {"start": v(-21.01, 10.7) * mm, "end": v(-21.03, 10.7) * mm});
            skLineSegment(sketch, "E1702", {"start": v(-21.03, 10.7) * mm, "end": v(-21.05, 10.72) * mm});
            skLineSegment(sketch, "E1703", {"start": v(-21.05, 10.72) * mm, "end": v(-21.07, 10.72) * mm});
            skLineSegment(sketch, "E1704", {"start": v(-21.07, 10.72) * mm, "end": v(-21.1, 10.73) * mm});
            skLineSegment(sketch, "E1705", {"start": v(-21.1, 10.73) * mm, "end": v(-21.12, 10.74) * mm});
            skLineSegment(sketch, "E1706", {"start": v(-21.12, 10.74) * mm, "end": v(-21.14, 10.75) * mm});
            skLineSegment(sketch, "E1707", {"start": v(-21.14, 10.75) * mm, "end": v(-21.17, 10.76) * mm});
            skLineSegment(sketch, "E1708", {"start": v(-21.17, 10.76) * mm, "end": v(-21.2, 10.77) * mm});
            skLineSegment(sketch, "E1709", {"start": v(-21.2, 10.77) * mm, "end": v(-21.23, 10.78) * mm});
            skLineSegment(sketch, "E1710", {"start": v(-21.23, 10.78) * mm, "end": v(-21.27, 10.79) * mm});
            skLineSegment(sketch, "E1711", {"start": v(-21.27, 10.79) * mm, "end": v(-21.3, 10.8) * mm});
            skLineSegment(sketch, "E1712", {"start": v(-21.3, 10.8) * mm, "end": v(-21.34, 10.81) * mm});
            skLineSegment(sketch, "E1713", {"start": v(-21.34, 10.81) * mm, "end": v(-21.38, 10.82) * mm});
            skLineSegment(sketch, "E1714", {"start": v(-21.38, 10.82) * mm, "end": v(-21.42, 10.83) * mm});
            skLineSegment(sketch, "E1715", {"start": v(-21.42, 10.83) * mm, "end": v(-21.46, 10.84) * mm});
            skLineSegment(sketch, "E1716", {"start": v(-21.46, 10.84) * mm, "end": v(-21.5, 10.86) * mm});
            skLineSegment(sketch, "E1717", {"start": v(-21.5, 10.86) * mm, "end": v(-21.55, 10.87) * mm});
            skLineSegment(sketch, "E1718", {"start": v(-21.55, 10.87) * mm, "end": v(-21.6, 10.88) * mm});
            skLineSegment(sketch, "E1719", {"start": v(-21.6, 10.88) * mm, "end": v(-21.65, 10.89) * mm});
            skLineSegment(sketch, "E1720", {"start": v(-21.65, 10.89) * mm, "end": v(-21.7, 10.9) * mm});
            skLineSegment(sketch, "E1721", {"start": v(-21.7, 10.9) * mm, "end": v(-21.75, 10.91) * mm});
            skLineSegment(sketch, "E1722", {"start": v(-21.75, 10.91) * mm, "end": v(-21.8, 10.92) * mm});
            skLineSegment(sketch, "E1723", {"start": v(-21.8, 10.92) * mm, "end": v(-21.87, 10.93) * mm});
            skLineSegment(sketch, "E1724", {"start": v(-21.87, 10.93) * mm, "end": v(-21.93, 10.94) * mm});
            skLineSegment(sketch, "E1725", {"start": v(-21.93, 10.94) * mm, "end": v(-21.99, 10.95) * mm});
            skLineSegment(sketch, "E1726", {"start": v(-21.99, 10.95) * mm, "end": v(-22.05, 10.96) * mm});
            skLineSegment(sketch, "E1727", {"start": v(-22.05, 10.96) * mm, "end": v(-22.11, 10.97) * mm});
            skLineSegment(sketch, "E1728", {"start": v(-22.11, 10.97) * mm, "end": v(-22.18, 10.98) * mm});
            skLineSegment(sketch, "E1729", {"start": v(-22.18, 10.98) * mm, "end": v(-22.25, 11) * mm});
            skLineSegment(sketch, "E1730", {"start": v(-22.25, 11) * mm, "end": v(-22.32, 11) * mm});
            skLineSegment(sketch, "E1731", {"start": v(-22.32, 11) * mm, "end": v(-22.39, 11.01) * mm});
            skLineSegment(sketch, "E1732", {"start": v(-22.39, 11.01) * mm, "end": v(-22.46, 11.02) * mm});
            skLineSegment(sketch, "E1733", {"start": v(-22.46, 11.02) * mm, "end": v(-22.54, 11.03) * mm});
            skLineSegment(sketch, "E1734", {"start": v(-22.54, 11.03) * mm, "end": v(-22.62, 11.03) * mm});
            skLineSegment(sketch, "E1735", {"start": v(-22.62, 11.03) * mm, "end": v(-22.7, 11.04) * mm});
            skLineSegment(sketch, "E1736", {"start": v(-22.7, 11.04) * mm, "end": v(-22.78, 11.05) * mm});
            skLineSegment(sketch, "E1737", {"start": v(-22.78, 11.05) * mm, "end": v(-22.86, 11.05) * mm});
            skLineSegment(sketch, "E1738", {"start": v(-22.86, 11.05) * mm, "end": v(-22.95, 11.06) * mm});
            skLineSegment(sketch, "E1739", {"start": v(-22.95, 11.06) * mm, "end": v(-23.03, 11.06) * mm});
            skLineSegment(sketch, "E1740", {"start": v(-23.03, 11.06) * mm, "end": v(-23.12, 11.06) * mm});
            skLineSegment(sketch, "E1741", {"start": v(-23.12, 11.06) * mm, "end": v(-23.21, 11.07) * mm});
            skLineSegment(sketch, "E1742", {"start": v(-23.21, 11.07) * mm, "end": v(-23.3, 11.07) * mm});
            skLineSegment(sketch, "E1743", {"start": v(-23.3, 11.07) * mm, "end": v(-23.4, 11.07) * mm});
            skLineSegment(sketch, "E1744", {"start": v(-23.4, 11.07) * mm, "end": v(-23.5, 11.07) * mm});
            skLineSegment(sketch, "E1745", {"start": v(-23.5, 11.07) * mm, "end": v(-23.59, 11.07) * mm});
            skLineSegment(sketch, "E1746", {"start": v(-23.59, 11.07) * mm, "end": v(-23.69, 11.07) * mm});
            skLineSegment(sketch, "E1747", {"start": v(-23.69, 11.07) * mm, "end": v(-23.8, 11.07) * mm});
            skLineSegment(sketch, "E1748", {"start": v(-23.8, 11.07) * mm, "end": v(-23.82, 11.03) * mm});
            skLineSegment(sketch, "E1749", {"start": v(-23.82, 11.03) * mm, "end": v(-24.16, 10.27) * mm});
            skLineSegment(sketch, "E1750", {"start": v(-24.16, 10.27) * mm, "end": v(-24.17, 10.22) * mm});
            skLineSegment(sketch, "E1751", {"start": v(-24.17, 10.22) * mm, "end": v(-24.1, 10.14) * mm});
            skLineSegment(sketch, "E1752", {"start": v(-24.1, 10.14) * mm, "end": v(-24.03, 10.07) * mm});
            skLineSegment(sketch, "E1753", {"start": v(-24.03, 10.07) * mm, "end": v(-23.97, 10) * mm});
            skLineSegment(sketch, "E1754", {"start": v(-23.97, 10) * mm, "end": v(-23.9, 9.93) * mm});
            skLineSegment(sketch, "E1755", {"start": v(-23.9, 9.93) * mm, "end": v(-23.84, 9.86) * mm});
            skLineSegment(sketch, "E1756", {"start": v(-23.84, 9.86) * mm, "end": v(-23.78, 9.8) * mm});
            skLineSegment(sketch, "E1757", {"start": v(-23.78, 9.8) * mm, "end": v(-23.71, 9.73) * mm});
            skLineSegment(sketch, "E1758", {"start": v(-23.71, 9.73) * mm, "end": v(-23.65, 9.66) * mm});
            skLineSegment(sketch, "E1759", {"start": v(-23.65, 9.66) * mm, "end": v(-23.6, 9.6) * mm});
            skLineSegment(sketch, "E1760", {"start": v(-23.6, 9.6) * mm, "end": v(-23.53, 9.54) * mm});
            skLineSegment(sketch, "E1761", {"start": v(-23.53, 9.54) * mm, "end": v(-23.47, 9.48) * mm});
            skLineSegment(sketch, "E1762", {"start": v(-23.47, 9.48) * mm, "end": v(-23.41, 9.43) * mm});
            skLineSegment(sketch, "E1763", {"start": v(-23.41, 9.43) * mm, "end": v(-23.35, 9.37) * mm});
            skLineSegment(sketch, "E1764", {"start": v(-23.35, 9.37) * mm, "end": v(-23.3, 9.32) * mm});
            skLineSegment(sketch, "E1765", {"start": v(-23.3, 9.32) * mm, "end": v(-23.24, 9.27) * mm});
            skLineSegment(sketch, "E1766", {"start": v(-23.24, 9.27) * mm, "end": v(-23.18, 9.22) * mm});
            skLineSegment(sketch, "E1767", {"start": v(-23.18, 9.22) * mm, "end": v(-23.13, 9.17) * mm});
            skLineSegment(sketch, "E1768", {"start": v(-23.13, 9.17) * mm, "end": v(-23.08, 9.13) * mm});
            skLineSegment(sketch, "E1769", {"start": v(-23.08, 9.13) * mm, "end": v(-23.02, 9.08) * mm});
            skLineSegment(sketch, "E1770", {"start": v(-23.02, 9.08) * mm, "end": v(-22.97, 9.04) * mm});
            skLineSegment(sketch, "E1771", {"start": v(-22.97, 9.04) * mm, "end": v(-22.92, 9) * mm});
            skLineSegment(sketch, "E1772", {"start": v(-22.92, 9) * mm, "end": v(-22.87, 8.96) * mm});
            skLineSegment(sketch, "E1773", {"start": v(-22.87, 8.96) * mm, "end": v(-22.82, 8.92) * mm});
            skLineSegment(sketch, "E1774", {"start": v(-22.82, 8.92) * mm, "end": v(-22.78, 8.88) * mm});
            skLineSegment(sketch, "E1775", {"start": v(-22.78, 8.88) * mm, "end": v(-22.73, 8.85) * mm});
            skLineSegment(sketch, "E1776", {"start": v(-22.73, 8.85) * mm, "end": v(-22.68, 8.82) * mm});
            skLineSegment(sketch, "E1777", {"start": v(-22.68, 8.82) * mm, "end": v(-22.64, 8.78) * mm});
            skLineSegment(sketch, "E1778", {"start": v(-22.64, 8.78) * mm, "end": v(-22.6, 8.75) * mm});
            skLineSegment(sketch, "E1779", {"start": v(-22.6, 8.75) * mm, "end": v(-22.56, 8.72) * mm});
            skLineSegment(sketch, "E1780", {"start": v(-22.56, 8.72) * mm, "end": v(-22.52, 8.7) * mm});
            skLineSegment(sketch, "E1781", {"start": v(-22.52, 8.7) * mm, "end": v(-22.48, 8.67) * mm});
            skLineSegment(sketch, "E1782", {"start": v(-22.48, 8.67) * mm, "end": v(-22.44, 8.64) * mm});
            skLineSegment(sketch, "E1783", {"start": v(-22.44, 8.64) * mm, "end": v(-22.4, 8.62) * mm});
            skLineSegment(sketch, "E1784", {"start": v(-22.4, 8.62) * mm, "end": v(-22.37, 8.6) * mm});
            skLineSegment(sketch, "E1785", {"start": v(-22.37, 8.6) * mm, "end": v(-22.33, 8.57) * mm});
            skLineSegment(sketch, "E1786", {"start": v(-22.33, 8.57) * mm, "end": v(-22.3, 8.55) * mm});
            skLineSegment(sketch, "E1787", {"start": v(-22.3, 8.55) * mm, "end": v(-22.27, 8.54) * mm});
            skLineSegment(sketch, "E1788", {"start": v(-22.27, 8.54) * mm, "end": v(-22.24, 8.52) * mm});
            skLineSegment(sketch, "E1789", {"start": v(-22.24, 8.52) * mm, "end": v(-22.2, 8.5) * mm});
            skLineSegment(sketch, "E1790", {"start": v(-22.2, 8.5) * mm, "end": v(-22.18, 8.49) * mm});
            skLineSegment(sketch, "E1791", {"start": v(-22.18, 8.49) * mm, "end": v(-22.16, 8.47) * mm});
            skLineSegment(sketch, "E1792", {"start": v(-22.16, 8.47) * mm, "end": v(-22.13, 8.46) * mm});
            skLineSegment(sketch, "E1793", {"start": v(-22.13, 8.46) * mm, "end": v(-22.1, 8.45) * mm});
            skLineSegment(sketch, "E1794", {"start": v(-22.1, 8.45) * mm, "end": v(-22.09, 8.43) * mm});
            skLineSegment(sketch, "E1795", {"start": v(-22.09, 8.43) * mm, "end": v(-22.07, 8.42) * mm});
            skLineSegment(sketch, "E1796", {"start": v(-22.07, 8.42) * mm, "end": v(-22.05, 8.42) * mm});
            skLineSegment(sketch, "E1797", {"start": v(-22.05, 8.42) * mm, "end": v(-22.03, 8.4) * mm});
            skLineSegment(sketch, "E1798", {"start": v(-22.03, 8.4) * mm, "end": v(-22.02, 8.4) * mm});
            skLineSegment(sketch, "E1799", {"start": v(-22.02, 8.4) * mm, "end": v(-22.4, 7.28) * mm});
            skLineSegment(sketch, "E1800", {"start": v(-22.4, 7.28) * mm, "end": v(-22.43, 7.28) * mm});
            skLineSegment(sketch, "E1801", {"start": v(-22.43, 7.28) * mm, "end": v(-22.45, 7.29) * mm});
            skLineSegment(sketch, "E1802", {"start": v(-22.45, 7.29) * mm, "end": v(-22.47, 7.3) * mm});
            skLineSegment(sketch, "E1803", {"start": v(-22.47, 7.3) * mm, "end": v(-22.49, 7.3) * mm});
            skLineSegment(sketch, "E1804", {"start": v(-22.49, 7.3) * mm, "end": v(-22.51, 7.3) * mm});
            skLineSegment(sketch, "E1805", {"start": v(-22.51, 7.3) * mm, "end": v(-22.54, 7.3) * mm});
            skLineSegment(sketch, "E1806", {"start": v(-22.54, 7.3) * mm, "end": v(-22.57, 7.3) * mm});
            skLineSegment(sketch, "E1807", {"start": v(-22.57, 7.3) * mm, "end": v(-22.6, 7.31) * mm});
            skLineSegment(sketch, "E1808", {"start": v(-22.6, 7.31) * mm, "end": v(-22.63, 7.32) * mm});
            skLineSegment(sketch, "E1809", {"start": v(-22.63, 7.32) * mm, "end": v(-22.66, 7.32) * mm});
            skLineSegment(sketch, "E1810", {"start": v(-22.66, 7.32) * mm, "end": v(-22.7, 7.33) * mm});
            skLineSegment(sketch, "E1811", {"start": v(-22.7, 7.33) * mm, "end": v(-22.73, 7.33) * mm});
            skLineSegment(sketch, "E1812", {"start": v(-22.73, 7.33) * mm, "end": v(-22.77, 7.34) * mm});
            skLineSegment(sketch, "E1813", {"start": v(-22.77, 7.34) * mm, "end": v(-22.8, 7.34) * mm});
            skLineSegment(sketch, "E1814", {"start": v(-22.8, 7.34) * mm, "end": v(-22.85, 7.35) * mm});
            skLineSegment(sketch, "E1815", {"start": v(-22.85, 7.35) * mm, "end": v(-22.9, 7.35) * mm});
            skLineSegment(sketch, "E1816", {"start": v(-22.9, 7.35) * mm, "end": v(-22.94, 7.36) * mm});
            skLineSegment(sketch, "E1817", {"start": v(-22.94, 7.36) * mm, "end": v(-22.99, 7.36) * mm});
            skLineSegment(sketch, "E1818", {"start": v(-22.99, 7.36) * mm, "end": v(-23.03, 7.37) * mm});
            skLineSegment(sketch, "E1819", {"start": v(-23.03, 7.37) * mm, "end": v(-23.09, 7.37) * mm});
            skLineSegment(sketch, "E1820", {"start": v(-23.09, 7.37) * mm, "end": v(-23.14, 7.37) * mm});
            skLineSegment(sketch, "E1821", {"start": v(-23.14, 7.37) * mm, "end": v(-23.2, 7.37) * mm});
            skLineSegment(sketch, "E1822", {"start": v(-23.2, 7.37) * mm, "end": v(-23.25, 7.38) * mm});
            skLineSegment(sketch, "E1823", {"start": v(-23.25, 7.38) * mm, "end": v(-23.3, 7.38) * mm});
            skLineSegment(sketch, "E1824", {"start": v(-23.3, 7.38) * mm, "end": v(-23.37, 7.38) * mm});
            skLineSegment(sketch, "E1825", {"start": v(-23.37, 7.38) * mm, "end": v(-23.43, 7.38) * mm});
            skLineSegment(sketch, "E1826", {"start": v(-23.43, 7.38) * mm, "end": v(-23.5, 7.38) * mm});
            skLineSegment(sketch, "E1827", {"start": v(-23.5, 7.38) * mm, "end": v(-23.56, 7.38) * mm});
            skLineSegment(sketch, "E1828", {"start": v(-23.56, 7.38) * mm, "end": v(-23.62, 7.38) * mm});
            skLineSegment(sketch, "E1829", {"start": v(-23.62, 7.38) * mm, "end": v(-23.7, 7.38) * mm});
            skLineSegment(sketch, "E1830", {"start": v(-23.7, 7.38) * mm, "end": v(-23.76, 7.38) * mm});
            skLineSegment(sketch, "E1831", {"start": v(-23.76, 7.38) * mm, "end": v(-23.84, 7.37) * mm});
            skLineSegment(sketch, "E1832", {"start": v(-23.84, 7.37) * mm, "end": v(-23.91, 7.37) * mm});
            skLineSegment(sketch, "E1833", {"start": v(-23.91, 7.37) * mm, "end": v(-23.99, 7.36) * mm});
            skLineSegment(sketch, "E1834", {"start": v(-23.99, 7.36) * mm, "end": v(-24.06, 7.36) * mm});
            skLineSegment(sketch, "E1835", {"start": v(-24.06, 7.36) * mm, "end": v(-24.14, 7.35) * mm});
            skLineSegment(sketch, "E1836", {"start": v(-24.14, 7.35) * mm, "end": v(-24.22, 7.35) * mm});
            skLineSegment(sketch, "E1837", {"start": v(-24.22, 7.35) * mm, "end": v(-24.3, 7.34) * mm});
            skLineSegment(sketch, "E1838", {"start": v(-24.3, 7.34) * mm, "end": v(-24.4, 7.33) * mm});
            skLineSegment(sketch, "E1839", {"start": v(-24.4, 7.33) * mm, "end": v(-24.48, 7.32) * mm});
            skLineSegment(sketch, "E1840", {"start": v(-24.48, 7.32) * mm, "end": v(-24.57, 7.31) * mm});
            skLineSegment(sketch, "E1841", {"start": v(-24.57, 7.31) * mm, "end": v(-24.66, 7.3) * mm});
            skLineSegment(sketch, "E1842", {"start": v(-24.66, 7.3) * mm, "end": v(-24.75, 7.29) * mm});
            skLineSegment(sketch, "E1843", {"start": v(-24.75, 7.29) * mm, "end": v(-24.84, 7.27) * mm});
            skLineSegment(sketch, "E1844", {"start": v(-24.84, 7.27) * mm, "end": v(-24.93, 7.26) * mm});
            skLineSegment(sketch, "E1845", {"start": v(-24.93, 7.26) * mm, "end": v(-25.03, 7.24) * mm});
            skLineSegment(sketch, "E1846", {"start": v(-25.03, 7.24) * mm, "end": v(-25.13, 7.23) * mm});
            skLineSegment(sketch, "E1847", {"start": v(-25.13, 7.23) * mm, "end": v(-25.23, 7.2) * mm});
            skLineSegment(sketch, "E1848", {"start": v(-25.23, 7.2) * mm, "end": v(-25.25, 7.17) * mm});
            skLineSegment(sketch, "E1849", {"start": v(-25.25, 7.17) * mm, "end": v(-25.47, 6.36) * mm});
            skLineSegment(sketch, "E1850", {"start": v(-25.47, 6.36) * mm, "end": v(-25.47, 6.32) * mm});
            skLineSegment(sketch, "E1851", {"start": v(-25.47, 6.32) * mm, "end": v(-25.39, 6.25) * mm});
            skLineSegment(sketch, "E1852", {"start": v(-25.39, 6.25) * mm, "end": v(-25.31, 6.19) * mm});
            skLineSegment(sketch, "E1853", {"start": v(-25.31, 6.19) * mm, "end": v(-25.24, 6.13) * mm});
            skLineSegment(sketch, "E1854", {"start": v(-25.24, 6.13) * mm, "end": v(-25.16, 6.07) * mm});
            skLineSegment(sketch, "E1855", {"start": v(-25.16, 6.07) * mm, "end": v(-25.09, 6) * mm});
            skLineSegment(sketch, "E1856", {"start": v(-25.09, 6) * mm, "end": v(-25.02, 5.95) * mm});
            skLineSegment(sketch, "E1857", {"start": v(-25.02, 5.95) * mm, "end": v(-24.94, 5.9) * mm});
            skLineSegment(sketch, "E1858", {"start": v(-24.94, 5.9) * mm, "end": v(-24.87, 5.84) * mm});
            skLineSegment(sketch, "E1859", {"start": v(-24.87, 5.84) * mm, "end": v(-24.8, 5.8) * mm});
            skLineSegment(sketch, "E1860", {"start": v(-24.8, 5.8) * mm, "end": v(-24.73, 5.74) * mm});
            skLineSegment(sketch, "E1861", {"start": v(-24.73, 5.74) * mm, "end": v(-24.67, 5.7) * mm});
            skLineSegment(sketch, "E1862", {"start": v(-24.67, 5.7) * mm, "end": v(-24.6, 5.65) * mm});
            skLineSegment(sketch, "E1863", {"start": v(-24.6, 5.65) * mm, "end": v(-24.53, 5.6) * mm});
            skLineSegment(sketch, "E1864", {"start": v(-24.53, 5.6) * mm, "end": v(-24.47, 5.56) * mm});
            skLineSegment(sketch, "E1865", {"start": v(-24.47, 5.56) * mm, "end": v(-24.4, 5.52) * mm});
            skLineSegment(sketch, "E1866", {"start": v(-24.4, 5.52) * mm, "end": v(-24.34, 5.48) * mm});
            skLineSegment(sketch, "E1867", {"start": v(-24.34, 5.48) * mm, "end": v(-24.28, 5.44) * mm});
            skLineSegment(sketch, "E1868", {"start": v(-24.28, 5.44) * mm, "end": v(-24.22, 5.4) * mm});
            skLineSegment(sketch, "E1869", {"start": v(-24.22, 5.4) * mm, "end": v(-24.16, 5.37) * mm});
            skLineSegment(sketch, "E1870", {"start": v(-24.16, 5.37) * mm, "end": v(-24.1, 5.33) * mm});
            skLineSegment(sketch, "E1871", {"start": v(-24.1, 5.33) * mm, "end": v(-24.05, 5.3) * mm});
            skLineSegment(sketch, "E1872", {"start": v(-24.05, 5.3) * mm, "end": v(-24, 5.27) * mm});
            skLineSegment(sketch, "E1873", {"start": v(-24, 5.27) * mm, "end": v(-23.94, 5.24) * mm});
            skLineSegment(sketch, "E1874", {"start": v(-23.94, 5.24) * mm, "end": v(-23.89, 5.21) * mm});
            skLineSegment(sketch, "E1875", {"start": v(-23.89, 5.21) * mm, "end": v(-23.83, 5.18) * mm});
            skLineSegment(sketch, "E1876", {"start": v(-23.83, 5.18) * mm, "end": v(-23.78, 5.16) * mm});
            skLineSegment(sketch, "E1877", {"start": v(-23.78, 5.16) * mm, "end": v(-23.74, 5.13) * mm});
            skLineSegment(sketch, "E1878", {"start": v(-23.74, 5.13) * mm, "end": v(-23.69, 5.1) * mm});
            skLineSegment(sketch, "E1879", {"start": v(-23.69, 5.1) * mm, "end": v(-23.64, 5.09) * mm});
            skLineSegment(sketch, "E1880", {"start": v(-23.64, 5.09) * mm, "end": v(-23.6, 5.07) * mm});
            skLineSegment(sketch, "E1881", {"start": v(-23.6, 5.07) * mm, "end": v(-23.56, 5.05) * mm});
            skLineSegment(sketch, "E1882", {"start": v(-23.56, 5.05) * mm, "end": v(-23.51, 5.03) * mm});
            skLineSegment(sketch, "E1883", {"start": v(-23.51, 5.03) * mm, "end": v(-23.47, 5) * mm});
            skLineSegment(sketch, "E1884", {"start": v(-23.47, 5) * mm, "end": v(-23.44, 5) * mm});
            skLineSegment(sketch, "E1885", {"start": v(-23.44, 5) * mm, "end": v(-23.4, 4.98) * mm});
            skLineSegment(sketch, "E1886", {"start": v(-23.4, 4.98) * mm, "end": v(-23.36, 4.96) * mm});
            skLineSegment(sketch, "E1887", {"start": v(-23.36, 4.96) * mm, "end": v(-23.33, 4.95) * mm});
            skLineSegment(sketch, "E1888", {"start": v(-23.33, 4.95) * mm, "end": v(-23.3, 4.93) * mm});
            skLineSegment(sketch, "E1889", {"start": v(-23.3, 4.93) * mm, "end": v(-23.27, 4.92) * mm});
            skLineSegment(sketch, "E1890", {"start": v(-23.27, 4.92) * mm, "end": v(-23.24, 4.91) * mm});
            skLineSegment(sketch, "E1891", {"start": v(-23.24, 4.91) * mm, "end": v(-23.2, 4.9) * mm});
            skLineSegment(sketch, "E1892", {"start": v(-23.2, 4.9) * mm, "end": v(-23.18, 4.9) * mm});
            skLineSegment(sketch, "E1893", {"start": v(-23.18, 4.9) * mm, "end": v(-23.16, 4.88) * mm});
            skLineSegment(sketch, "E1894", {"start": v(-23.16, 4.88) * mm, "end": v(-23.13, 4.88) * mm});
            skLineSegment(sketch, "E1895", {"start": v(-23.13, 4.88) * mm, "end": v(-23.11, 4.87) * mm});
            skLineSegment(sketch, "E1896", {"start": v(-23.11, 4.87) * mm, "end": v(-23.1, 4.86) * mm});
            skLineSegment(sketch, "E1897", {"start": v(-23.1, 4.86) * mm, "end": v(-23.08, 4.86) * mm});
            skLineSegment(sketch, "E1898", {"start": v(-23.08, 4.86) * mm, "end": v(-23.06, 4.85) * mm});
            skLineSegment(sketch, "E1899", {"start": v(-23.06, 4.85) * mm, "end": v(-23.27, 3.69) * mm});
            skLineSegment(sketch, "E1900", {"start": v(-23.27, 3.69) * mm, "end": v(-23.3, 3.68) * mm});
            skLineSegment(sketch, "E1901", {"start": v(-23.3, 3.68) * mm, "end": v(-23.31, 3.69) * mm});
            skLineSegment(sketch, "E1902", {"start": v(-23.31, 3.69) * mm, "end": v(-23.33, 3.69) * mm});
            skLineSegment(sketch, "E1903", {"start": v(-23.33, 3.69) * mm, "end": v(-23.35, 3.69) * mm});
            skLineSegment(sketch, "E1904", {"start": v(-23.35, 3.69) * mm, "end": v(-23.38, 3.69) * mm});
            skLineSegment(sketch, "E1905", {"start": v(-23.38, 3.69) * mm, "end": v(-23.4, 3.69) * mm});
            skLineSegment(sketch, "E1906", {"start": v(-23.4, 3.69) * mm, "end": v(-23.43, 3.69) * mm});
            skLineSegment(sketch, "E1907", {"start": v(-23.43, 3.69) * mm, "end": v(-23.46, 3.7) * mm});
            skLineSegment(sketch, "E1908", {"start": v(-23.46, 3.7) * mm, "end": v(-23.5, 3.7) * mm});
            skLineSegment(sketch, "E1909", {"start": v(-23.5, 3.7) * mm, "end": v(-23.53, 3.7) * mm});
            skLineSegment(sketch, "E1910", {"start": v(-23.53, 3.7) * mm, "end": v(-23.56, 3.69) * mm});
            skLineSegment(sketch, "E1911", {"start": v(-23.56, 3.69) * mm, "end": v(-23.6, 3.69) * mm});
            skLineSegment(sketch, "E1912", {"start": v(-23.6, 3.69) * mm, "end": v(-23.64, 3.69) * mm});
            skLineSegment(sketch, "E1913", {"start": v(-23.64, 3.69) * mm, "end": v(-23.68, 3.69) * mm});
            skLineSegment(sketch, "E1914", {"start": v(-23.68, 3.69) * mm, "end": v(-23.72, 3.68) * mm});
            skLineSegment(sketch, "E1915", {"start": v(-23.72, 3.68) * mm, "end": v(-23.76, 3.68) * mm});
            skLineSegment(sketch, "E1916", {"start": v(-23.76, 3.68) * mm, "end": v(-23.8, 3.68) * mm});
            skLineSegment(sketch, "E1917", {"start": v(-23.8, 3.68) * mm, "end": v(-23.85, 3.68) * mm});
            skLineSegment(sketch, "E1918", {"start": v(-23.85, 3.68) * mm, "end": v(-23.9, 3.67) * mm});
            skLineSegment(sketch, "E1919", {"start": v(-23.9, 3.67) * mm, "end": v(-23.95, 3.67) * mm});
            skLineSegment(sketch, "E1920", {"start": v(-23.95, 3.67) * mm, "end": v(-24, 3.66) * mm});
            skLineSegment(sketch, "E1921", {"start": v(-24, 3.66) * mm, "end": v(-24.06, 3.66) * mm});
            skLineSegment(sketch, "E1922", {"start": v(-24.06, 3.66) * mm, "end": v(-24.12, 3.65) * mm});
            skLineSegment(sketch, "E1923", {"start": v(-24.12, 3.65) * mm, "end": v(-24.17, 3.64) * mm});
            skLineSegment(sketch, "E1924", {"start": v(-24.17, 3.64) * mm, "end": v(-24.23, 3.63) * mm});
            skLineSegment(sketch, "E1925", {"start": v(-24.23, 3.63) * mm, "end": v(-24.3, 3.62) * mm});
            skLineSegment(sketch, "E1926", {"start": v(-24.3, 3.62) * mm, "end": v(-24.36, 3.61) * mm});
            skLineSegment(sketch, "E1927", {"start": v(-24.36, 3.61) * mm, "end": v(-24.42, 3.6) * mm});
            skLineSegment(sketch, "E1928", {"start": v(-24.42, 3.6) * mm, "end": v(-24.49, 3.6) * mm});
            skLineSegment(sketch, "E1929", {"start": v(-24.49, 3.6) * mm, "end": v(-24.56, 3.58) * mm});
            skLineSegment(sketch, "E1930", {"start": v(-24.56, 3.58) * mm, "end": v(-24.63, 3.57) * mm});
            skLineSegment(sketch, "E1931", {"start": v(-24.63, 3.57) * mm, "end": v(-24.7, 3.55) * mm});
            skLineSegment(sketch, "E1932", {"start": v(-24.7, 3.55) * mm, "end": v(-24.77, 3.54) * mm});
            skLineSegment(sketch, "E1933", {"start": v(-24.77, 3.54) * mm, "end": v(-24.84, 3.52) * mm});
            skLineSegment(sketch, "E1934", {"start": v(-24.84, 3.52) * mm, "end": v(-24.92, 3.5) * mm});
            skLineSegment(sketch, "E1935", {"start": v(-24.92, 3.5) * mm, "end": v(-25, 3.49) * mm});
            skLineSegment(sketch, "E1936", {"start": v(-25, 3.49) * mm, "end": v(-25.08, 3.47) * mm});
            skLineSegment(sketch, "E1937", {"start": v(-25.08, 3.47) * mm, "end": v(-25.16, 3.45) * mm});
            skLineSegment(sketch, "E1938", {"start": v(-25.16, 3.45) * mm, "end": v(-25.24, 3.42) * mm});
            skLineSegment(sketch, "E1939", {"start": v(-25.24, 3.42) * mm, "end": v(-25.32, 3.4) * mm});
            skLineSegment(sketch, "E1940", {"start": v(-25.32, 3.4) * mm, "end": v(-25.4, 3.38) * mm});
            skLineSegment(sketch, "E1941", {"start": v(-25.4, 3.38) * mm, "end": v(-25.5, 3.35) * mm});
            skLineSegment(sketch, "E1942", {"start": v(-25.5, 3.35) * mm, "end": v(-25.58, 3.33) * mm});
            skLineSegment(sketch, "E1943", {"start": v(-25.58, 3.33) * mm, "end": v(-25.67, 3.3) * mm});
            skLineSegment(sketch, "E1944", {"start": v(-25.67, 3.3) * mm, "end": v(-25.76, 3.27) * mm});
            skLineSegment(sketch, "E1945", {"start": v(-25.76, 3.27) * mm, "end": v(-25.86, 3.24) * mm});
            skLineSegment(sketch, "E1946", {"start": v(-25.86, 3.24) * mm, "end": v(-25.95, 3.2) * mm});
            skLineSegment(sketch, "E1947", {"start": v(-25.95, 3.2) * mm, "end": v(-26.05, 3.17) * mm});
            skLineSegment(sketch, "E1948", {"start": v(-26.05, 3.17) * mm, "end": v(-26.06, 3.13) * mm});
            skLineSegment(sketch, "E1949", {"start": v(-26.06, 3.13) * mm, "end": v(-26.15, 2.3) * mm});
            skLineSegment(sketch, "E1950", {"start": v(-26.15, 2.3) * mm, "end": v(-26.14, 2.25) * mm});
            skLineSegment(sketch, "E1951", {"start": v(-26.14, 2.25) * mm, "end": v(-26.05, 2.2) * mm});
            skLineSegment(sketch, "E1952", {"start": v(-26.05, 2.2) * mm, "end": v(-25.97, 2.15) * mm});
            skLineSegment(sketch, "E1953", {"start": v(-25.97, 2.15) * mm, "end": v(-25.88, 2.1) * mm});
            skLineSegment(sketch, "E1954", {"start": v(-25.88, 2.1) * mm, "end": v(-25.8, 2.05) * mm});
            skLineSegment(sketch, "E1955", {"start": v(-25.8, 2.05) * mm, "end": v(-25.72, 2) * mm});
            skLineSegment(sketch, "E1956", {"start": v(-25.72, 2) * mm, "end": v(-25.64, 1.96) * mm});
            skLineSegment(sketch, "E1957", {"start": v(-25.64, 1.96) * mm, "end": v(-25.56, 1.92) * mm});
            skLineSegment(sketch, "E1958", {"start": v(-25.56, 1.92) * mm, "end": v(-25.48, 1.88) * mm});
            skLineSegment(sketch, "E1959", {"start": v(-25.48, 1.88) * mm, "end": v(-25.4, 1.84) * mm});
            skLineSegment(sketch, "E1960", {"start": v(-25.4, 1.84) * mm, "end": v(-25.33, 1.8) * mm});
            skLineSegment(sketch, "E1961", {"start": v(-25.33, 1.8) * mm, "end": v(-25.25, 1.77) * mm});
            skLineSegment(sketch, "E1962", {"start": v(-25.25, 1.77) * mm, "end": v(-25.18, 1.73) * mm});
            skLineSegment(sketch, "E1963", {"start": v(-25.18, 1.73) * mm, "end": v(-25.1, 1.7) * mm});
            skLineSegment(sketch, "E1964", {"start": v(-25.1, 1.7) * mm, "end": v(-25.04, 1.67) * mm});
            skLineSegment(sketch, "E1965", {"start": v(-25.04, 1.67) * mm, "end": v(-24.97, 1.63) * mm});
            skLineSegment(sketch, "E1966", {"start": v(-24.97, 1.63) * mm, "end": v(-24.9, 1.6) * mm});
            skLineSegment(sketch, "E1967", {"start": v(-24.9, 1.6) * mm, "end": v(-24.83, 1.58) * mm});
            skLineSegment(sketch, "E1968", {"start": v(-24.83, 1.58) * mm, "end": v(-24.77, 1.55) * mm});
            skLineSegment(sketch, "E1969", {"start": v(-24.77, 1.55) * mm, "end": v(-24.7, 1.52) * mm});
            skLineSegment(sketch, "E1970", {"start": v(-24.7, 1.52) * mm, "end": v(-24.64, 1.5) * mm});
            skLineSegment(sketch, "E1971", {"start": v(-24.64, 1.5) * mm, "end": v(-24.58, 1.47) * mm});
            skLineSegment(sketch, "E1972", {"start": v(-24.58, 1.47) * mm, "end": v(-24.52, 1.45) * mm});
            skLineSegment(sketch, "E1973", {"start": v(-24.52, 1.45) * mm, "end": v(-24.46, 1.43) * mm});
            skLineSegment(sketch, "E1974", {"start": v(-24.46, 1.43) * mm, "end": v(-24.4, 1.41) * mm});
            skLineSegment(sketch, "E1975", {"start": v(-24.4, 1.41) * mm, "end": v(-24.35, 1.4) * mm});
            skLineSegment(sketch, "E1976", {"start": v(-24.35, 1.4) * mm, "end": v(-24.3, 1.37) * mm});
            skLineSegment(sketch, "E1977", {"start": v(-24.3, 1.37) * mm, "end": v(-24.25, 1.36) * mm});
            skLineSegment(sketch, "E1978", {"start": v(-24.25, 1.36) * mm, "end": v(-24.2, 1.34) * mm});
            skLineSegment(sketch, "E1979", {"start": v(-24.2, 1.34) * mm, "end": v(-24.15, 1.33) * mm});
            skLineSegment(sketch, "E1980", {"start": v(-24.15, 1.33) * mm, "end": v(-24.1, 1.31) * mm});
            skLineSegment(sketch, "E1981", {"start": v(-24.1, 1.31) * mm, "end": v(-24.05, 1.3) * mm});
            skLineSegment(sketch, "E1982", {"start": v(-24.05, 1.3) * mm, "end": v(-24.01, 1.29) * mm});
            skLineSegment(sketch, "E1983", {"start": v(-24.01, 1.29) * mm, "end": v(-23.97, 1.27) * mm});
            skLineSegment(sketch, "E1984", {"start": v(-23.97, 1.27) * mm, "end": v(-23.93, 1.26) * mm});
            skLineSegment(sketch, "E1985", {"start": v(-23.93, 1.26) * mm, "end": v(-23.89, 1.25) * mm});
            skLineSegment(sketch, "E1986", {"start": v(-23.89, 1.25) * mm, "end": v(-23.85, 1.25) * mm});
            skLineSegment(sketch, "E1987", {"start": v(-23.85, 1.25) * mm, "end": v(-23.82, 1.24) * mm});
            skLineSegment(sketch, "E1988", {"start": v(-23.82, 1.24) * mm, "end": v(-23.78, 1.23) * mm});
            skLineSegment(sketch, "E1989", {"start": v(-23.78, 1.23) * mm, "end": v(-23.75, 1.22) * mm});
            skLineSegment(sketch, "E1990", {"start": v(-23.75, 1.22) * mm, "end": v(-23.72, 1.22) * mm});
            skLineSegment(sketch, "E1991", {"start": v(-23.72, 1.22) * mm, "end": v(-23.69, 1.21) * mm});
            skLineSegment(sketch, "E1992", {"start": v(-23.69, 1.21) * mm, "end": v(-23.66, 1.2) * mm});
            skLineSegment(sketch, "E1993", {"start": v(-23.66, 1.2) * mm, "end": v(-23.64, 1.2) * mm});
            skLineSegment(sketch, "E1994", {"start": v(-23.64, 1.2) * mm, "end": v(-23.61, 1.2) * mm});
            skLineSegment(sketch, "E1995", {"start": v(-23.61, 1.2) * mm, "end": v(-23.6, 1.2) * mm});
            skLineSegment(sketch, "E1996", {"start": v(-23.6, 1.2) * mm, "end": v(-23.57, 1.2) * mm});
            skLineSegment(sketch, "E1997", {"start": v(-23.57, 1.2) * mm, "end": v(-23.55, 1.19) * mm});
            skLineSegment(sketch, "E1998", {"start": v(-23.55, 1.19) * mm, "end": v(-23.53, 1.18) * mm});
            skLineSegment(sketch, "E1999", {"start": v(-23.53, 1.18) * mm, "end": v(-23.56, 0) * mm});
            skLineSegment(sketch, "E2000", {"start": v(-23.56, 0) * mm, "end": v(-23.58, 0) * mm});
            skLineSegment(sketch, "E2001", {"start": v(-23.58, 0) * mm, "end": v(-23.6, 0) * mm});
            skLineSegment(sketch, "E2002", {"start": v(-23.6, 0) * mm, "end": v(-23.62, 0) * mm});
            skLineSegment(sketch, "E2003", {"start": v(-23.62, 0) * mm, "end": v(-23.64, -0.01) * mm});
            skLineSegment(sketch, "E2004", {"start": v(-23.64, -0.01) * mm, "end": v(-23.67, -0.01) * mm});
            skLineSegment(sketch, "E2005", {"start": v(-23.67, -0.01) * mm, "end": v(-23.7, -0.02) * mm});
            skLineSegment(sketch, "E2006", {"start": v(-23.7, -0.02) * mm, "end": v(-23.72, -0.02) * mm});
            skLineSegment(sketch, "E2007", {"start": v(-23.72, -0.02) * mm, "end": v(-23.75, -0.03) * mm});
            skLineSegment(sketch, "E2008", {"start": v(-23.75, -0.03) * mm, "end": v(-23.78, -0.03) * mm});
            skLineSegment(sketch, "E2009", {"start": v(-23.78, -0.03) * mm, "end": v(-23.81, -0.04) * mm});
            skLineSegment(sketch, "E2010", {"start": v(-23.81, -0.04) * mm, "end": v(-23.85, -0.04) * mm});
            skLineSegment(sketch, "E2011", {"start": v(-23.85, -0.04) * mm, "end": v(-23.88, -0.05) * mm});
            skLineSegment(sketch, "E2012", {"start": v(-23.88, -0.05) * mm, "end": v(-23.92, -0.06) * mm});
            skLineSegment(sketch, "E2013", {"start": v(-23.92, -0.06) * mm, "end": v(-23.96, -0.06) * mm});
            skLineSegment(sketch, "E2014", {"start": v(-23.96, -0.06) * mm, "end": v(-24, -0.07) * mm});
            skLineSegment(sketch, "E2015", {"start": v(-24, -0.07) * mm, "end": v(-24.04, -0.08) * mm});
            skLineSegment(sketch, "E2016", {"start": v(-24.04, -0.08) * mm, "end": v(-24.09, -0.1) * mm});
            skLineSegment(sketch, "E2017", {"start": v(-24.09, -0.1) * mm, "end": v(-24.14, -0.1) * mm});
            skLineSegment(sketch, "E2018", {"start": v(-24.14, -0.1) * mm, "end": v(-24.18, -0.11) * mm});
            skLineSegment(sketch, "E2019", {"start": v(-24.18, -0.11) * mm, "end": v(-24.23, -0.13) * mm});
            skLineSegment(sketch, "E2020", {"start": v(-24.23, -0.13) * mm, "end": v(-24.28, -0.14) * mm});
            skLineSegment(sketch, "E2021", {"start": v(-24.28, -0.14) * mm, "end": v(-24.34, -0.15) * mm});
            skLineSegment(sketch, "E2022", {"start": v(-24.34, -0.15) * mm, "end": v(-24.4, -0.17) * mm});
            skLineSegment(sketch, "E2023", {"start": v(-24.4, -0.17) * mm, "end": v(-24.45, -0.19) * mm});
            skLineSegment(sketch, "E2024", {"start": v(-24.45, -0.19) * mm, "end": v(-24.5, -0.2) * mm});
            skLineSegment(sketch, "E2025", {"start": v(-24.5, -0.2) * mm, "end": v(-24.56, -0.22) * mm});
            skLineSegment(sketch, "E2026", {"start": v(-24.56, -0.22) * mm, "end": v(-24.62, -0.24) * mm});
            skLineSegment(sketch, "E2027", {"start": v(-24.62, -0.24) * mm, "end": v(-24.69, -0.26) * mm});
            skLineSegment(sketch, "E2028", {"start": v(-24.69, -0.26) * mm, "end": v(-24.75, -0.28) * mm});
            skLineSegment(sketch, "E2029", {"start": v(-24.75, -0.28) * mm, "end": v(-24.81, -0.3) * mm});
            skLineSegment(sketch, "E2030", {"start": v(-24.81, -0.3) * mm, "end": v(-24.88, -0.33) * mm});
            skLineSegment(sketch, "E2031", {"start": v(-24.88, -0.33) * mm, "end": v(-24.95, -0.35) * mm});
            skLineSegment(sketch, "E2032", {"start": v(-24.95, -0.35) * mm, "end": v(-25.02, -0.38) * mm});
            skLineSegment(sketch, "E2033", {"start": v(-25.02, -0.38) * mm, "end": v(-25.09, -0.4) * mm});
            skLineSegment(sketch, "E2034", {"start": v(-25.09, -0.4) * mm, "end": v(-25.16, -0.44) * mm});
            skLineSegment(sketch, "E2035", {"start": v(-25.16, -0.44) * mm, "end": v(-25.23, -0.47) * mm});
            skLineSegment(sketch, "E2036", {"start": v(-25.23, -0.47) * mm, "end": v(-25.3, -0.5) * mm});
            skLineSegment(sketch, "E2037", {"start": v(-25.3, -0.5) * mm, "end": v(-25.39, -0.53) * mm});
            skLineSegment(sketch, "E2038", {"start": v(-25.39, -0.53) * mm, "end": v(-25.46, -0.57) * mm});
            skLineSegment(sketch, "E2039", {"start": v(-25.46, -0.57) * mm, "end": v(-25.54, -0.6) * mm});
            skLineSegment(sketch, "E2040", {"start": v(-25.54, -0.6) * mm, "end": v(-25.62, -0.64) * mm});
            skLineSegment(sketch, "E2041", {"start": v(-25.62, -0.64) * mm, "end": v(-25.7, -0.68) * mm});
            skLineSegment(sketch, "E2042", {"start": v(-25.7, -0.68) * mm, "end": v(-25.79, -0.72) * mm});
            skLineSegment(sketch, "E2043", {"start": v(-25.79, -0.72) * mm, "end": v(-25.87, -0.76) * mm});
            skLineSegment(sketch, "E2044", {"start": v(-25.87, -0.76) * mm, "end": v(-25.96, -0.8) * mm});
            skLineSegment(sketch, "E2045", {"start": v(-25.96, -0.8) * mm, "end": v(-26.04, -0.85) * mm});
            skLineSegment(sketch, "E2046", {"start": v(-26.04, -0.85) * mm, "end": v(-26.13, -0.9) * mm});
            skLineSegment(sketch, "E2047", {"start": v(-26.13, -0.9) * mm, "end": v(-26.22, -0.94) * mm});
            skLineSegment(sketch, "E2048", {"start": v(-26.22, -0.94) * mm, "end": v(-26.23, -0.99) * mm});
            skLineSegment(sketch, "E2049", {"start": v(-26.23, -0.99) * mm, "end": v(-26.19, -1.82) * mm});
            skLineSegment(sketch, "E2050", {"start": v(-26.19, -1.82) * mm, "end": v(-26.17, -1.86) * mm});
            skLineSegment(sketch, "E2051", {"start": v(-26.17, -1.86) * mm, "end": v(-26.08, -1.9) * mm});
            skLineSegment(sketch, "E2052", {"start": v(-26.08, -1.9) * mm, "end": v(-25.99, -1.94) * mm});
            skLineSegment(sketch, "E2053", {"start": v(-25.99, -1.94) * mm, "end": v(-25.9, -1.97) * mm});
            skLineSegment(sketch, "E2054", {"start": v(-25.9, -1.97) * mm, "end": v(-25.8, -2) * mm});
            skLineSegment(sketch, "E2055", {"start": v(-25.8, -2) * mm, "end": v(-25.72, -2.04) * mm});
            skLineSegment(sketch, "E2056", {"start": v(-25.72, -2.04) * mm, "end": v(-25.63, -2.07) * mm});
            skLineSegment(sketch, "E2057", {"start": v(-25.63, -2.07) * mm, "end": v(-25.55, -2.1) * mm});
            skLineSegment(sketch, "E2058", {"start": v(-25.55, -2.1) * mm, "end": v(-25.46, -2.13) * mm});
            skLineSegment(sketch, "E2059", {"start": v(-25.46, -2.13) * mm, "end": v(-25.38, -2.16) * mm});
            skLineSegment(sketch, "E2060", {"start": v(-25.38, -2.16) * mm, "end": v(-25.3, -2.18) * mm});
            skLineSegment(sketch, "E2061", {"start": v(-25.3, -2.18) * mm, "end": v(-25.22, -2.2) * mm});
            skLineSegment(sketch, "E2062", {"start": v(-25.22, -2.2) * mm, "end": v(-25.14, -2.23) * mm});
            skLineSegment(sketch, "E2063", {"start": v(-25.14, -2.23) * mm, "end": v(-25.06, -2.25) * mm});
            skLineSegment(sketch, "E2064", {"start": v(-25.06, -2.25) * mm, "end": v(-24.99, -2.27) * mm});
            skLineSegment(sketch, "E2065", {"start": v(-24.99, -2.27) * mm, "end": v(-24.92, -2.3) * mm});
            skLineSegment(sketch, "E2066", {"start": v(-24.92, -2.3) * mm, "end": v(-24.84, -2.31) * mm});
            skLineSegment(sketch, "E2067", {"start": v(-24.84, -2.31) * mm, "end": v(-24.77, -2.33) * mm});
            skLineSegment(sketch, "E2068", {"start": v(-24.77, -2.33) * mm, "end": v(-24.7, -2.34) * mm});
            skLineSegment(sketch, "E2069", {"start": v(-24.7, -2.34) * mm, "end": v(-24.64, -2.36) * mm});
            skLineSegment(sketch, "E2070", {"start": v(-24.64, -2.36) * mm, "end": v(-24.57, -2.38) * mm});
            skLineSegment(sketch, "E2071", {"start": v(-24.57, -2.38) * mm, "end": v(-24.5, -2.39) * mm});
            skLineSegment(sketch, "E2072", {"start": v(-24.5, -2.39) * mm, "end": v(-24.45, -2.4) * mm});
            skLineSegment(sketch, "E2073", {"start": v(-24.45, -2.4) * mm, "end": v(-24.39, -2.41) * mm});
            skLineSegment(sketch, "E2074", {"start": v(-24.39, -2.41) * mm, "end": v(-24.33, -2.42) * mm});
            skLineSegment(sketch, "E2075", {"start": v(-24.33, -2.42) * mm, "end": v(-24.27, -2.43) * mm});
            skLineSegment(sketch, "E2076", {"start": v(-24.27, -2.43) * mm, "end": v(-24.21, -2.44) * mm});
            skLineSegment(sketch, "E2077", {"start": v(-24.21, -2.44) * mm, "end": v(-24.16, -2.45) * mm});
            skLineSegment(sketch, "E2078", {"start": v(-24.16, -2.45) * mm, "end": v(-24.1, -2.46) * mm});
            skLineSegment(sketch, "E2079", {"start": v(-24.1, -2.46) * mm, "end": v(-24.06, -2.47) * mm});
            skLineSegment(sketch, "E2080", {"start": v(-24.06, -2.47) * mm, "end": v(-24, -2.47) * mm});
            skLineSegment(sketch, "E2081", {"start": v(-24, -2.47) * mm, "end": v(-23.96, -2.48) * mm});
            skLineSegment(sketch, "E2082", {"start": v(-23.96, -2.48) * mm, "end": v(-23.92, -2.49) * mm});
            skLineSegment(sketch, "E2083", {"start": v(-23.92, -2.49) * mm, "end": v(-23.87, -2.5) * mm});
            skLineSegment(sketch, "E2084", {"start": v(-23.87, -2.5) * mm, "end": v(-23.83, -2.5) * mm});
            skLineSegment(sketch, "E2085", {"start": v(-23.83, -2.5) * mm, "end": v(-23.8, -2.5) * mm});
            skLineSegment(sketch, "E2086", {"start": v(-23.8, -2.5) * mm, "end": v(-23.75, -2.5) * mm});
            skLineSegment(sketch, "E2087", {"start": v(-23.75, -2.5) * mm, "end": v(-23.72, -2.5) * mm});
            skLineSegment(sketch, "E2088", {"start": v(-23.72, -2.5) * mm, "end": v(-23.68, -2.5) * mm});
            skLineSegment(sketch, "E2089", {"start": v(-23.68, -2.5) * mm, "end": v(-23.65, -2.5) * mm});
            skLineSegment(sketch, "E2090", {"start": v(-23.65, -2.5) * mm, "end": v(-23.62, -2.5) * mm});
            skLineSegment(sketch, "E2091", {"start": v(-23.62, -2.5) * mm, "end": v(-23.59, -2.51) * mm});
            skLineSegment(sketch, "E2092", {"start": v(-23.59, -2.51) * mm, "end": v(-23.56, -2.51) * mm});
            skLineSegment(sketch, "E2093", {"start": v(-23.56, -2.51) * mm, "end": v(-23.53, -2.51) * mm});
            skLineSegment(sketch, "E2094", {"start": v(-23.53, -2.51) * mm, "end": v(-23.5, -2.51) * mm});
            skLineSegment(sketch, "E2095", {"start": v(-23.5, -2.51) * mm, "end": v(-23.49, -2.51) * mm});
            skLineSegment(sketch, "E2096", {"start": v(-23.49, -2.51) * mm, "end": v(-23.47, -2.51) * mm});
            skLineSegment(sketch, "E2097", {"start": v(-23.47, -2.51) * mm, "end": v(-23.45, -2.51) * mm});
            skLineSegment(sketch, "E2098", {"start": v(-23.45, -2.51) * mm, "end": v(-23.43, -2.51) * mm});
            skLineSegment(sketch, "E2099", {"start": v(-23.43, -2.51) * mm, "end": v(-23.27, -3.69) * mm});
            skLineSegment(sketch, "E2100", {"start": v(-23.27, -3.69) * mm, "end": v(-23.3, -3.7) * mm});
            skLineSegment(sketch, "E2101", {"start": v(-23.3, -3.7) * mm, "end": v(-23.3, -3.7) * mm});
            skLineSegment(sketch, "E2102", {"start": v(-23.3, -3.7) * mm, "end": v(-23.33, -3.7) * mm});
            skLineSegment(sketch, "E2103", {"start": v(-23.33, -3.7) * mm, "end": v(-23.35, -3.7) * mm});
            skLineSegment(sketch, "E2104", {"start": v(-23.35, -3.7) * mm, "end": v(-23.37, -3.72) * mm});
            skLineSegment(sketch, "E2105", {"start": v(-23.37, -3.72) * mm, "end": v(-23.4, -3.72) * mm});
            skLineSegment(sketch, "E2106", {"start": v(-23.4, -3.72) * mm, "end": v(-23.42, -3.73) * mm});
            skLineSegment(sketch, "E2107", {"start": v(-23.42, -3.73) * mm, "end": v(-23.45, -3.74) * mm});
            skLineSegment(sketch, "E2108", {"start": v(-23.45, -3.74) * mm, "end": v(-23.48, -3.75) * mm});
            skLineSegment(sketch, "E2109", {"start": v(-23.48, -3.75) * mm, "end": v(-23.51, -3.76) * mm});
            skLineSegment(sketch, "E2110", {"start": v(-23.51, -3.76) * mm, "end": v(-23.55, -3.77) * mm});
            skLineSegment(sketch, "E2111", {"start": v(-23.55, -3.77) * mm, "end": v(-23.58, -3.78) * mm});
            skLineSegment(sketch, "E2112", {"start": v(-23.58, -3.78) * mm, "end": v(-23.62, -3.8) * mm});
            skLineSegment(sketch, "E2113", {"start": v(-23.62, -3.8) * mm, "end": v(-23.66, -3.81) * mm});
            skLineSegment(sketch, "E2114", {"start": v(-23.66, -3.81) * mm, "end": v(-23.7, -3.83) * mm});
            skLineSegment(sketch, "E2115", {"start": v(-23.7, -3.83) * mm, "end": v(-23.74, -3.84) * mm});
            skLineSegment(sketch, "E2116", {"start": v(-23.74, -3.84) * mm, "end": v(-23.78, -3.86) * mm});
            skLineSegment(sketch, "E2117", {"start": v(-23.78, -3.86) * mm, "end": v(-23.82, -3.88) * mm});
            skLineSegment(sketch, "E2118", {"start": v(-23.82, -3.88) * mm, "end": v(-23.87, -3.9) * mm});
            skLineSegment(sketch, "E2119", {"start": v(-23.87, -3.9) * mm, "end": v(-23.91, -3.92) * mm});
            skLineSegment(sketch, "E2120", {"start": v(-23.91, -3.92) * mm, "end": v(-23.96, -3.94) * mm});
            skLineSegment(sketch, "E2121", {"start": v(-23.96, -3.94) * mm, "end": v(-24.01, -3.96) * mm});
            skLineSegment(sketch, "E2122", {"start": v(-24.01, -3.96) * mm, "end": v(-24.06, -3.98) * mm});
            skLineSegment(sketch, "E2123", {"start": v(-24.06, -3.98) * mm, "end": v(-24.12, -4) * mm});
            skLineSegment(sketch, "E2124", {"start": v(-24.12, -4) * mm, "end": v(-24.17, -4.03) * mm});
            skLineSegment(sketch, "E2125", {"start": v(-24.17, -4.03) * mm, "end": v(-24.23, -4.06) * mm});
            skLineSegment(sketch, "E2126", {"start": v(-24.23, -4.06) * mm, "end": v(-24.28, -4.09) * mm});
            skLineSegment(sketch, "E2127", {"start": v(-24.28, -4.09) * mm, "end": v(-24.34, -4.12) * mm});
            skLineSegment(sketch, "E2128", {"start": v(-24.34, -4.12) * mm, "end": v(-24.4, -4.15) * mm});
            skLineSegment(sketch, "E2129", {"start": v(-24.4, -4.15) * mm, "end": v(-24.46, -4.18) * mm});
            skLineSegment(sketch, "E2130", {"start": v(-24.46, -4.18) * mm, "end": v(-24.52, -4.22) * mm});
            skLineSegment(sketch, "E2131", {"start": v(-24.52, -4.22) * mm, "end": v(-24.59, -4.25) * mm});
            skLineSegment(sketch, "E2132", {"start": v(-24.59, -4.25) * mm, "end": v(-24.65, -4.29) * mm});
            skLineSegment(sketch, "E2133", {"start": v(-24.65, -4.29) * mm, "end": v(-24.72, -4.33) * mm});
            skLineSegment(sketch, "E2134", {"start": v(-24.72, -4.33) * mm, "end": v(-24.78, -4.37) * mm});
            skLineSegment(sketch, "E2135", {"start": v(-24.78, -4.37) * mm, "end": v(-24.85, -4.4) * mm});
            skLineSegment(sketch, "E2136", {"start": v(-24.85, -4.4) * mm, "end": v(-24.92, -4.45) * mm});
            skLineSegment(sketch, "E2137", {"start": v(-24.92, -4.45) * mm, "end": v(-25, -4.5) * mm});
            skLineSegment(sketch, "E2138", {"start": v(-25, -4.5) * mm, "end": v(-25.06, -4.54) * mm});
            skLineSegment(sketch, "E2139", {"start": v(-25.06, -4.54) * mm, "end": v(-25.13, -4.59) * mm});
            skLineSegment(sketch, "E2140", {"start": v(-25.13, -4.59) * mm, "end": v(-25.2, -4.64) * mm});
            skLineSegment(sketch, "E2141", {"start": v(-25.2, -4.64) * mm, "end": v(-25.28, -4.69) * mm});
            skLineSegment(sketch, "E2142", {"start": v(-25.28, -4.69) * mm, "end": v(-25.36, -4.74) * mm});
            skLineSegment(sketch, "E2143", {"start": v(-25.36, -4.74) * mm, "end": v(-25.44, -4.8) * mm});
            skLineSegment(sketch, "E2144", {"start": v(-25.44, -4.8) * mm, "end": v(-25.51, -4.85) * mm});
            skLineSegment(sketch, "E2145", {"start": v(-25.51, -4.85) * mm, "end": v(-25.6, -4.9) * mm});
            skLineSegment(sketch, "E2146", {"start": v(-25.6, -4.9) * mm, "end": v(-25.67, -4.97) * mm});
            skLineSegment(sketch, "E2147", {"start": v(-25.67, -4.97) * mm, "end": v(-25.75, -5.03) * mm});
            skLineSegment(sketch, "E2148", {"start": v(-25.75, -5.03) * mm, "end": v(-25.75, -5.08) * mm});
            skLineSegment(sketch, "E2149", {"start": v(-25.75, -5.08) * mm, "end": v(-25.58, -5.9) * mm});
            skLineSegment(sketch, "E2150", {"start": v(-25.58, -5.9) * mm, "end": v(-25.56, -5.93) * mm});
            skLineSegment(sketch, "E2151", {"start": v(-25.56, -5.93) * mm, "end": v(-25.46, -5.96) * mm});
            skLineSegment(sketch, "E2152", {"start": v(-25.46, -5.96) * mm, "end": v(-25.36, -5.98) * mm});
            skLineSegment(sketch, "E2153", {"start": v(-25.36, -5.98) * mm, "end": v(-25.27, -6) * mm});
            skLineSegment(sketch, "E2154", {"start": v(-25.27, -6) * mm, "end": v(-25.17, -6.02) * mm});
            skLineSegment(sketch, "E2155", {"start": v(-25.17, -6.02) * mm, "end": v(-25.08, -6.04) * mm});
            skLineSegment(sketch, "E2156", {"start": v(-25.08, -6.04) * mm, "end": v(-25, -6.05) * mm});
            skLineSegment(sketch, "E2157", {"start": v(-25, -6.05) * mm, "end": v(-24.9, -6.07) * mm});
            skLineSegment(sketch, "E2158", {"start": v(-24.9, -6.07) * mm, "end": v(-24.81, -6.09) * mm});
            skLineSegment(sketch, "E2159", {"start": v(-24.81, -6.09) * mm, "end": v(-24.73, -6.1) * mm});
            skLineSegment(sketch, "E2160", {"start": v(-24.73, -6.1) * mm, "end": v(-24.65, -6.11) * mm});
            skLineSegment(sketch, "E2161", {"start": v(-24.65, -6.11) * mm, "end": v(-24.56, -6.12) * mm});
            skLineSegment(sketch, "E2162", {"start": v(-24.56, -6.12) * mm, "end": v(-24.48, -6.13) * mm});
            skLineSegment(sketch, "E2163", {"start": v(-24.48, -6.13) * mm, "end": v(-24.4, -6.14) * mm});
            skLineSegment(sketch, "E2164", {"start": v(-24.4, -6.14) * mm, "end": v(-24.33, -6.15) * mm});
            skLineSegment(sketch, "E2165", {"start": v(-24.33, -6.15) * mm, "end": v(-24.25, -6.16) * mm});
            skLineSegment(sketch, "E2166", {"start": v(-24.25, -6.16) * mm, "end": v(-24.18, -6.17) * mm});
            skLineSegment(sketch, "E2167", {"start": v(-24.18, -6.17) * mm, "end": v(-24.1, -6.17) * mm});
            skLineSegment(sketch, "E2168", {"start": v(-24.1, -6.17) * mm, "end": v(-24.03, -6.18) * mm});
            skLineSegment(sketch, "E2169", {"start": v(-24.03, -6.18) * mm, "end": v(-23.96, -6.19) * mm});
            skLineSegment(sketch, "E2170", {"start": v(-23.96, -6.19) * mm, "end": v(-23.9, -6.19) * mm});
            skLineSegment(sketch, "E2171", {"start": v(-23.9, -6.19) * mm, "end": v(-23.83, -6.2) * mm});
            skLineSegment(sketch, "E2172", {"start": v(-23.83, -6.2) * mm, "end": v(-23.77, -6.2) * mm});
            skLineSegment(sketch, "E2173", {"start": v(-23.77, -6.2) * mm, "end": v(-23.7, -6.2) * mm});
            skLineSegment(sketch, "E2174", {"start": v(-23.7, -6.2) * mm, "end": v(-23.65, -6.2) * mm});
            skLineSegment(sketch, "E2175", {"start": v(-23.65, -6.2) * mm, "end": v(-23.59, -6.2) * mm});
            skLineSegment(sketch, "E2176", {"start": v(-23.59, -6.2) * mm, "end": v(-23.53, -6.2) * mm});
            skLineSegment(sketch, "E2177", {"start": v(-23.53, -6.2) * mm, "end": v(-23.48, -6.2) * mm});
            skLineSegment(sketch, "E2178", {"start": v(-23.48, -6.2) * mm, "end": v(-23.43, -6.2) * mm});
            skLineSegment(sketch, "E2179", {"start": v(-23.43, -6.2) * mm, "end": v(-23.37, -6.2) * mm});
            skLineSegment(sketch, "E2180", {"start": v(-23.37, -6.2) * mm, "end": v(-23.33, -6.2) * mm});
            skLineSegment(sketch, "E2181", {"start": v(-23.33, -6.2) * mm, "end": v(-23.28, -6.2) * mm});
            skLineSegment(sketch, "E2182", {"start": v(-23.28, -6.2) * mm, "end": v(-23.23, -6.2) * mm});
            skLineSegment(sketch, "E2183", {"start": v(-23.23, -6.2) * mm, "end": v(-23.19, -6.2) * mm});
            skLineSegment(sketch, "E2184", {"start": v(-23.19, -6.2) * mm, "end": v(-23.15, -6.2) * mm});
            skLineSegment(sketch, "E2185", {"start": v(-23.15, -6.2) * mm, "end": v(-23.1, -6.19) * mm});
            skLineSegment(sketch, "E2186", {"start": v(-23.1, -6.19) * mm, "end": v(-23.07, -6.19) * mm});
            skLineSegment(sketch, "E2187", {"start": v(-23.07, -6.19) * mm, "end": v(-23.03, -6.18) * mm});
            skLineSegment(sketch, "E2188", {"start": v(-23.03, -6.18) * mm, "end": v(-23, -6.18) * mm});
            skLineSegment(sketch, "E2189", {"start": v(-23, -6.18) * mm, "end": v(-22.96, -6.18) * mm});
            skLineSegment(sketch, "E2190", {"start": v(-22.96, -6.18) * mm, "end": v(-22.93, -6.17) * mm});
            skLineSegment(sketch, "E2191", {"start": v(-22.93, -6.17) * mm, "end": v(-22.9, -6.17) * mm});
            skLineSegment(sketch, "E2192", {"start": v(-22.9, -6.17) * mm, "end": v(-22.88, -6.17) * mm});
            skLineSegment(sketch, "E2193", {"start": v(-22.88, -6.17) * mm, "end": v(-22.85, -6.16) * mm});
            skLineSegment(sketch, "E2194", {"start": v(-22.85, -6.16) * mm, "end": v(-22.83, -6.16) * mm});
            skLineSegment(sketch, "E2195", {"start": v(-22.83, -6.16) * mm, "end": v(-22.8, -6.16) * mm});
            skLineSegment(sketch, "E2196", {"start": v(-22.8, -6.16) * mm, "end": v(-22.78, -6.15) * mm});
            skLineSegment(sketch, "E2197", {"start": v(-22.78, -6.15) * mm, "end": v(-22.77, -6.15) * mm});
            skLineSegment(sketch, "E2198", {"start": v(-22.77, -6.15) * mm, "end": v(-22.75, -6.15) * mm});
            skLineSegment(sketch, "E2199", {"start": v(-22.75, -6.15) * mm, "end": v(-22.4, -7.28) * mm});
            skLineSegment(sketch, "E2200", {"start": v(-22.4, -7.28) * mm, "end": v(-22.43, -7.3) * mm});
            skLineSegment(sketch, "E2201", {"start": v(-22.43, -7.3) * mm, "end": v(-22.44, -7.3) * mm});
            skLineSegment(sketch, "E2202", {"start": v(-22.44, -7.3) * mm, "end": v(-22.46, -7.3) * mm});
            skLineSegment(sketch, "E2203", {"start": v(-22.46, -7.3) * mm, "end": v(-22.48, -7.32) * mm});
            skLineSegment(sketch, "E2204", {"start": v(-22.48, -7.32) * mm, "end": v(-22.5, -7.33) * mm});
            skLineSegment(sketch, "E2205", {"start": v(-22.5, -7.33) * mm, "end": v(-22.53, -7.34) * mm});
            skLineSegment(sketch, "E2206", {"start": v(-22.53, -7.34) * mm, "end": v(-22.55, -7.35) * mm});
            skLineSegment(sketch, "E2207", {"start": v(-22.55, -7.35) * mm, "end": v(-22.58, -7.36) * mm});
            skLineSegment(sketch, "E2208", {"start": v(-22.58, -7.36) * mm, "end": v(-22.6, -7.38) * mm});
            skLineSegment(sketch, "E2209", {"start": v(-22.6, -7.38) * mm, "end": v(-22.64, -7.4) * mm});
            skLineSegment(sketch, "E2210", {"start": v(-22.64, -7.4) * mm, "end": v(-22.67, -7.4) * mm});
            skLineSegment(sketch, "E2211", {"start": v(-22.67, -7.4) * mm, "end": v(-22.7, -7.43) * mm});
            skLineSegment(sketch, "E2212", {"start": v(-22.7, -7.43) * mm, "end": v(-22.73, -7.44) * mm});
            skLineSegment(sketch, "E2213", {"start": v(-22.73, -7.44) * mm, "end": v(-22.77, -7.46) * mm});
            skLineSegment(sketch, "E2214", {"start": v(-22.77, -7.46) * mm, "end": v(-22.8, -7.49) * mm});
            skLineSegment(sketch, "E2215", {"start": v(-22.8, -7.49) * mm, "end": v(-22.84, -7.5) * mm});
            skLineSegment(sketch, "E2216", {"start": v(-22.84, -7.5) * mm, "end": v(-22.88, -7.53) * mm});
            skLineSegment(sketch, "E2217", {"start": v(-22.88, -7.53) * mm, "end": v(-22.92, -7.56) * mm});
            skLineSegment(sketch, "E2218", {"start": v(-22.92, -7.56) * mm, "end": v(-22.96, -7.58) * mm});
            skLineSegment(sketch, "E2219", {"start": v(-22.96, -7.58) * mm, "end": v(-23, -7.6) * mm});
            skLineSegment(sketch, "E2220", {"start": v(-23, -7.6) * mm, "end": v(-23.05, -7.64) * mm});
            skLineSegment(sketch, "E2221", {"start": v(-23.05, -7.64) * mm, "end": v(-23.1, -7.67) * mm});
            skLineSegment(sketch, "E2222", {"start": v(-23.1, -7.67) * mm, "end": v(-23.14, -7.7) * mm});
            skLineSegment(sketch, "E2223", {"start": v(-23.14, -7.7) * mm, "end": v(-23.2, -7.73) * mm});
            skLineSegment(sketch, "E2224", {"start": v(-23.2, -7.73) * mm, "end": v(-23.24, -7.76) * mm});
            skLineSegment(sketch, "E2225", {"start": v(-23.24, -7.76) * mm, "end": v(-23.3, -7.8) * mm});
            skLineSegment(sketch, "E2226", {"start": v(-23.3, -7.8) * mm, "end": v(-23.34, -7.84) * mm});
            skLineSegment(sketch, "E2227", {"start": v(-23.34, -7.84) * mm, "end": v(-23.4, -7.88) * mm});
            skLineSegment(sketch, "E2228", {"start": v(-23.4, -7.88) * mm, "end": v(-23.45, -7.92) * mm});
            skLineSegment(sketch, "E2229", {"start": v(-23.45, -7.92) * mm, "end": v(-23.5, -7.96) * mm});
            skLineSegment(sketch, "E2230", {"start": v(-23.5, -7.96) * mm, "end": v(-23.56, -8) * mm});
            skLineSegment(sketch, "E2231", {"start": v(-23.56, -8) * mm, "end": v(-23.62, -8.05) * mm});
            skLineSegment(sketch, "E2232", {"start": v(-23.62, -8.05) * mm, "end": v(-23.68, -8.1) * mm});
            skLineSegment(sketch, "E2233", {"start": v(-23.68, -8.1) * mm, "end": v(-23.73, -8.14) * mm});
            skLineSegment(sketch, "E2234", {"start": v(-23.73, -8.14) * mm, "end": v(-23.8, -8.2) * mm});
            skLineSegment(sketch, "E2235", {"start": v(-23.8, -8.2) * mm, "end": v(-23.86, -8.24) * mm});
            skLineSegment(sketch, "E2236", {"start": v(-23.86, -8.24) * mm, "end": v(-23.92, -8.3) * mm});
            skLineSegment(sketch, "E2237", {"start": v(-23.92, -8.3) * mm, "end": v(-23.98, -8.35) * mm});
            skLineSegment(sketch, "E2238", {"start": v(-23.98, -8.35) * mm, "end": v(-24.04, -8.4) * mm});
            skLineSegment(sketch, "E2239", {"start": v(-24.04, -8.4) * mm, "end": v(-24.1, -8.46) * mm});
            skLineSegment(sketch, "E2240", {"start": v(-24.1, -8.46) * mm, "end": v(-24.17, -8.53) * mm});
            skLineSegment(sketch, "E2241", {"start": v(-24.17, -8.53) * mm, "end": v(-24.24, -8.59) * mm});
            skLineSegment(sketch, "E2242", {"start": v(-24.24, -8.59) * mm, "end": v(-24.3, -8.65) * mm});
            skLineSegment(sketch, "E2243", {"start": v(-24.3, -8.65) * mm, "end": v(-24.37, -8.72) * mm});
            skLineSegment(sketch, "E2244", {"start": v(-24.37, -8.72) * mm, "end": v(-24.44, -8.78) * mm});
            skLineSegment(sketch, "E2245", {"start": v(-24.44, -8.78) * mm, "end": v(-24.5, -8.85) * mm});
            skLineSegment(sketch, "E2246", {"start": v(-24.5, -8.85) * mm, "end": v(-24.58, -8.92) * mm});
            skLineSegment(sketch, "E2247", {"start": v(-24.58, -8.92) * mm, "end": v(-24.65, -9) * mm});
            skLineSegment(sketch, "E2248", {"start": v(-24.65, -9) * mm, "end": v(-24.64, -9.04) * mm});
            skLineSegment(sketch, "E2249", {"start": v(-24.64, -9.04) * mm, "end": v(-24.34, -9.82) * mm});
            skLineSegment(sketch, "E2250", {"start": v(-24.34, -9.82) * mm, "end": v(-24.32, -9.86) * mm});
            skLineSegment(sketch, "E2251", {"start": v(-24.32, -9.86) * mm, "end": v(-24.21, -9.87) * mm});
            skLineSegment(sketch, "E2252", {"start": v(-24.21, -9.87) * mm, "end": v(-24.12, -9.87) * mm});
            skLineSegment(sketch, "E2253", {"start": v(-24.12, -9.87) * mm, "end": v(-24.02, -9.88) * mm});
            skLineSegment(sketch, "E2254", {"start": v(-24.02, -9.88) * mm, "end": v(-23.92, -9.88) * mm});
            skLineSegment(sketch, "E2255", {"start": v(-23.92, -9.88) * mm, "end": v(-23.83, -9.89) * mm});
            skLineSegment(sketch, "E2256", {"start": v(-23.83, -9.89) * mm, "end": v(-23.74, -9.89) * mm});
            skLineSegment(sketch, "E2257", {"start": v(-23.74, -9.89) * mm, "end": v(-23.65, -9.9) * mm});
            skLineSegment(sketch, "E2258", {"start": v(-23.65, -9.9) * mm, "end": v(-23.56, -9.9) * mm});
            skLineSegment(sketch, "E2259", {"start": v(-23.56, -9.9) * mm, "end": v(-23.47, -9.9) * mm});
            skLineSegment(sketch, "E2260", {"start": v(-23.47, -9.9) * mm, "end": v(-23.39, -9.9) * mm});
            skLineSegment(sketch, "E2261", {"start": v(-23.39, -9.9) * mm, "end": v(-23.3, -9.9) * mm});
            skLineSegment(sketch, "E2262", {"start": v(-23.3, -9.9) * mm, "end": v(-23.22, -9.89) * mm});
            skLineSegment(sketch, "E2263", {"start": v(-23.22, -9.89) * mm, "end": v(-23.14, -9.89) * mm});
            skLineSegment(sketch, "E2264", {"start": v(-23.14, -9.89) * mm, "end": v(-23.06, -9.88) * mm});
            skLineSegment(sketch, "E2265", {"start": v(-23.06, -9.88) * mm, "end": v(-22.99, -9.88) * mm});
            skLineSegment(sketch, "E2266", {"start": v(-22.99, -9.88) * mm, "end": v(-22.91, -9.87) * mm});
            skLineSegment(sketch, "E2267", {"start": v(-22.91, -9.87) * mm, "end": v(-22.84, -9.87) * mm});
            skLineSegment(sketch, "E2268", {"start": v(-22.84, -9.87) * mm, "end": v(-22.77, -9.86) * mm});
            skLineSegment(sketch, "E2269", {"start": v(-22.77, -9.86) * mm, "end": v(-22.7, -9.86) * mm});
            skLineSegment(sketch, "E2270", {"start": v(-22.7, -9.86) * mm, "end": v(-22.64, -9.85) * mm});
            skLineSegment(sketch, "E2271", {"start": v(-22.64, -9.85) * mm, "end": v(-22.57, -9.85) * mm});
            skLineSegment(sketch, "E2272", {"start": v(-22.57, -9.85) * mm, "end": v(-22.5, -9.84) * mm});
            skLineSegment(sketch, "E2273", {"start": v(-22.5, -9.84) * mm, "end": v(-22.45, -9.83) * mm});
            skLineSegment(sketch, "E2274", {"start": v(-22.45, -9.83) * mm, "end": v(-22.39, -9.82) * mm});
            skLineSegment(sketch, "E2275", {"start": v(-22.39, -9.82) * mm, "end": v(-22.33, -9.82) * mm});
            skLineSegment(sketch, "E2276", {"start": v(-22.33, -9.82) * mm, "end": v(-22.27, -9.8) * mm});
            skLineSegment(sketch, "E2277", {"start": v(-22.27, -9.8) * mm, "end": v(-22.22, -9.8) * mm});
            skLineSegment(sketch, "E2278", {"start": v(-22.22, -9.8) * mm, "end": v(-22.17, -9.79) * mm});
            skLineSegment(sketch, "E2279", {"start": v(-22.17, -9.79) * mm, "end": v(-22.12, -9.78) * mm});
            skLineSegment(sketch, "E2280", {"start": v(-22.12, -9.78) * mm, "end": v(-22.07, -9.77) * mm});
            skLineSegment(sketch, "E2281", {"start": v(-22.07, -9.77) * mm, "end": v(-22.02, -9.76) * mm});
            skLineSegment(sketch, "E2282", {"start": v(-22.02, -9.76) * mm, "end": v(-21.98, -9.75) * mm});
            skLineSegment(sketch, "E2283", {"start": v(-21.98, -9.75) * mm, "end": v(-21.93, -9.75) * mm});
            skLineSegment(sketch, "E2284", {"start": v(-21.93, -9.75) * mm, "end": v(-21.9, -9.74) * mm});
            skLineSegment(sketch, "E2285", {"start": v(-21.9, -9.74) * mm, "end": v(-21.85, -9.73) * mm});
            skLineSegment(sketch, "E2286", {"start": v(-21.85, -9.73) * mm, "end": v(-21.82, -9.72) * mm});
            skLineSegment(sketch, "E2287", {"start": v(-21.82, -9.72) * mm, "end": v(-21.78, -9.7) * mm});
            skLineSegment(sketch, "E2288", {"start": v(-21.78, -9.7) * mm, "end": v(-21.75, -9.7) * mm});
            skLineSegment(sketch, "E2289", {"start": v(-21.75, -9.7) * mm, "end": v(-21.72, -9.7) * mm});
            skLineSegment(sketch, "E2290", {"start": v(-21.72, -9.7) * mm, "end": v(-21.69, -9.68) * mm});
            skLineSegment(sketch, "E2291", {"start": v(-21.69, -9.68) * mm, "end": v(-21.66, -9.68) * mm});
            skLineSegment(sketch, "E2292", {"start": v(-21.66, -9.68) * mm, "end": v(-21.63, -9.67) * mm});
            skLineSegment(sketch, "E2293", {"start": v(-21.63, -9.67) * mm, "end": v(-21.6, -9.66) * mm});
            skLineSegment(sketch, "E2294", {"start": v(-21.6, -9.66) * mm, "end": v(-21.58, -9.65) * mm});
            skLineSegment(sketch, "E2295", {"start": v(-21.58, -9.65) * mm, "end": v(-21.56, -9.65) * mm});
            skLineSegment(sketch, "E2296", {"start": v(-21.56, -9.65) * mm, "end": v(-21.54, -9.64) * mm});
            skLineSegment(sketch, "E2297", {"start": v(-21.54, -9.64) * mm, "end": v(-21.52, -9.63) * mm});
            skLineSegment(sketch, "E2298", {"start": v(-21.52, -9.63) * mm, "end": v(-21.5, -9.63) * mm});
            skLineSegment(sketch, "E2299", {"start": v(-21.5, -9.63) * mm, "end": v(-21, -10.7) * mm});
            skLineSegment(sketch, "E2300", {"start": v(-21, -10.7) * mm, "end": v(-21, -10.71) * mm});
            skLineSegment(sketch, "E2301", {"start": v(-21, -10.71) * mm, "end": v(-21.02, -10.72) * mm});
            skLineSegment(sketch, "E2302", {"start": v(-21.02, -10.72) * mm, "end": v(-21.04, -10.73) * mm});
            skLineSegment(sketch, "E2303", {"start": v(-21.04, -10.73) * mm, "end": v(-21.06, -10.74) * mm});
            skLineSegment(sketch, "E2304", {"start": v(-21.06, -10.74) * mm, "end": v(-21.08, -10.76) * mm});
            skLineSegment(sketch, "E2305", {"start": v(-21.08, -10.76) * mm, "end": v(-21.1, -10.77) * mm});
            skLineSegment(sketch, "E2306", {"start": v(-21.1, -10.77) * mm, "end": v(-21.13, -10.79) * mm});
            skLineSegment(sketch, "E2307", {"start": v(-21.13, -10.79) * mm, "end": v(-21.15, -10.8) * mm});
            skLineSegment(sketch, "E2308", {"start": v(-21.15, -10.8) * mm, "end": v(-21.17, -10.82) * mm});
            skLineSegment(sketch, "E2309", {"start": v(-21.17, -10.82) * mm, "end": v(-21.2, -10.84) * mm});
            skLineSegment(sketch, "E2310", {"start": v(-21.2, -10.84) * mm, "end": v(-21.23, -10.86) * mm});
            skLineSegment(sketch, "E2311", {"start": v(-21.23, -10.86) * mm, "end": v(-21.26, -10.89) * mm});
            skLineSegment(sketch, "E2312", {"start": v(-21.26, -10.89) * mm, "end": v(-21.29, -10.9) * mm});
            skLineSegment(sketch, "E2313", {"start": v(-21.29, -10.9) * mm, "end": v(-21.32, -10.93) * mm});
            skLineSegment(sketch, "E2314", {"start": v(-21.32, -10.93) * mm, "end": v(-21.35, -10.96) * mm});
            skLineSegment(sketch, "E2315", {"start": v(-21.35, -10.96) * mm, "end": v(-21.39, -10.99) * mm});
            skLineSegment(sketch, "E2316", {"start": v(-21.39, -10.99) * mm, "end": v(-21.42, -11.02) * mm});
            skLineSegment(sketch, "E2317", {"start": v(-21.42, -11.02) * mm, "end": v(-21.46, -11.05) * mm});
            skLineSegment(sketch, "E2318", {"start": v(-21.46, -11.05) * mm, "end": v(-21.5, -11.08) * mm});
            skLineSegment(sketch, "E2319", {"start": v(-21.5, -11.08) * mm, "end": v(-21.53, -11.11) * mm});
            skLineSegment(sketch, "E2320", {"start": v(-21.53, -11.11) * mm, "end": v(-21.57, -11.15) * mm});
            skLineSegment(sketch, "E2321", {"start": v(-21.57, -11.15) * mm, "end": v(-21.61, -11.19) * mm});
            skLineSegment(sketch, "E2322", {"start": v(-21.61, -11.19) * mm, "end": v(-21.66, -11.22) * mm});
            skLineSegment(sketch, "E2323", {"start": v(-21.66, -11.22) * mm, "end": v(-21.7, -11.26) * mm});
            skLineSegment(sketch, "E2324", {"start": v(-21.7, -11.26) * mm, "end": v(-21.74, -11.3) * mm});
            skLineSegment(sketch, "E2325", {"start": v(-21.74, -11.3) * mm, "end": v(-21.79, -11.35) * mm});
            skLineSegment(sketch, "E2326", {"start": v(-21.79, -11.35) * mm, "end": v(-21.83, -11.4) * mm});
            skLineSegment(sketch, "E2327", {"start": v(-21.83, -11.4) * mm, "end": v(-21.88, -11.44) * mm});
            skLineSegment(sketch, "E2328", {"start": v(-21.88, -11.44) * mm, "end": v(-21.92, -11.49) * mm});
            skLineSegment(sketch, "E2329", {"start": v(-21.92, -11.49) * mm, "end": v(-21.97, -11.54) * mm});
            skLineSegment(sketch, "E2330", {"start": v(-21.97, -11.54) * mm, "end": v(-22.02, -11.59) * mm});
            skLineSegment(sketch, "E2331", {"start": v(-22.02, -11.59) * mm, "end": v(-22.07, -11.64) * mm});
            skLineSegment(sketch, "E2332", {"start": v(-22.07, -11.64) * mm, "end": v(-22.12, -11.7) * mm});
            skLineSegment(sketch, "E2333", {"start": v(-22.12, -11.7) * mm, "end": v(-22.17, -11.75) * mm});
            skLineSegment(sketch, "E2334", {"start": v(-22.17, -11.75) * mm, "end": v(-22.22, -11.81) * mm});
            skLineSegment(sketch, "E2335", {"start": v(-22.22, -11.81) * mm, "end": v(-22.27, -11.87) * mm});
            skLineSegment(sketch, "E2336", {"start": v(-22.27, -11.87) * mm, "end": v(-22.32, -11.93) * mm});
            skLineSegment(sketch, "E2337", {"start": v(-22.32, -11.93) * mm, "end": v(-22.38, -12) * mm});
            skLineSegment(sketch, "E2338", {"start": v(-22.38, -12) * mm, "end": v(-22.43, -12.06) * mm});
            skLineSegment(sketch, "E2339", {"start": v(-22.43, -12.06) * mm, "end": v(-22.49, -12.13) * mm});
            skLineSegment(sketch, "E2340", {"start": v(-22.49, -12.13) * mm, "end": v(-22.54, -12.2) * mm});
            skLineSegment(sketch, "E2341", {"start": v(-22.54, -12.2) * mm, "end": v(-22.6, -12.27) * mm});
            skLineSegment(sketch, "E2342", {"start": v(-22.6, -12.27) * mm, "end": v(-22.65, -12.35) * mm});
            skLineSegment(sketch, "E2343", {"start": v(-22.65, -12.35) * mm, "end": v(-22.7, -12.42) * mm});
            skLineSegment(sketch, "E2344", {"start": v(-22.7, -12.42) * mm, "end": v(-22.76, -12.5) * mm});
            skLineSegment(sketch, "E2345", {"start": v(-22.76, -12.5) * mm, "end": v(-22.82, -12.58) * mm});
            skLineSegment(sketch, "E2346", {"start": v(-22.82, -12.58) * mm, "end": v(-22.88, -12.66) * mm});
            skLineSegment(sketch, "E2347", {"start": v(-22.88, -12.66) * mm, "end": v(-22.94, -12.74) * mm});
            skLineSegment(sketch, "E2348", {"start": v(-22.94, -12.74) * mm, "end": v(-22.92, -12.79) * mm});
            skLineSegment(sketch, "E2349", {"start": v(-22.92, -12.79) * mm, "end": v(-22.5, -13.5) * mm});
            skLineSegment(sketch, "E2350", {"start": v(-22.5, -13.5) * mm, "end": v(-22.47, -13.54) * mm});
            skLineSegment(sketch, "E2351", {"start": v(-22.47, -13.54) * mm, "end": v(-22.37, -13.53) * mm});
            skLineSegment(sketch, "E2352", {"start": v(-22.37, -13.53) * mm, "end": v(-22.27, -13.52) * mm});
            skLineSegment(sketch, "E2353", {"start": v(-22.27, -13.52) * mm, "end": v(-22.18, -13.51) * mm});
            skLineSegment(sketch, "E2354", {"start": v(-22.18, -13.51) * mm, "end": v(-22.08, -13.5) * mm});
            skLineSegment(sketch, "E2355", {"start": v(-22.08, -13.5) * mm, "end": v(-21.99, -13.5) * mm});
            skLineSegment(sketch, "E2356", {"start": v(-21.99, -13.5) * mm, "end": v(-21.9, -13.48) * mm});
            skLineSegment(sketch, "E2357", {"start": v(-21.9, -13.48) * mm, "end": v(-21.8, -13.47) * mm});
            skLineSegment(sketch, "E2358", {"start": v(-21.8, -13.47) * mm, "end": v(-21.72, -13.46) * mm});
            skLineSegment(sketch, "E2359", {"start": v(-21.72, -13.46) * mm, "end": v(-21.63, -13.44) * mm});
            skLineSegment(sketch, "E2360", {"start": v(-21.63, -13.44) * mm, "end": v(-21.55, -13.43) * mm});
            skLineSegment(sketch, "E2361", {"start": v(-21.55, -13.43) * mm, "end": v(-21.47, -13.41) * mm});
            skLineSegment(sketch, "E2362", {"start": v(-21.47, -13.41) * mm, "end": v(-21.39, -13.4) * mm});
            skLineSegment(sketch, "E2363", {"start": v(-21.39, -13.4) * mm, "end": v(-21.31, -13.38) * mm});
            skLineSegment(sketch, "E2364", {"start": v(-21.31, -13.38) * mm, "end": v(-21.23, -13.37) * mm});
            skLineSegment(sketch, "E2365", {"start": v(-21.23, -13.37) * mm, "end": v(-21.16, -13.35) * mm});
            skLineSegment(sketch, "E2366", {"start": v(-21.16, -13.35) * mm, "end": v(-21.09, -13.34) * mm});
            skLineSegment(sketch, "E2367", {"start": v(-21.09, -13.34) * mm, "end": v(-21.02, -13.32) * mm});
            skLineSegment(sketch, "E2368", {"start": v(-21.02, -13.32) * mm, "end": v(-20.95, -13.3) * mm});
            skLineSegment(sketch, "E2369", {"start": v(-20.95, -13.3) * mm, "end": v(-20.88, -13.29) * mm});
            skLineSegment(sketch, "E2370", {"start": v(-20.88, -13.29) * mm, "end": v(-20.82, -13.27) * mm});
            skLineSegment(sketch, "E2371", {"start": v(-20.82, -13.27) * mm, "end": v(-20.75, -13.25) * mm});
            skLineSegment(sketch, "E2372", {"start": v(-20.75, -13.25) * mm, "end": v(-20.7, -13.24) * mm});
            skLineSegment(sketch, "E2373", {"start": v(-20.7, -13.24) * mm, "end": v(-20.63, -13.22) * mm});
            skLineSegment(sketch, "E2374", {"start": v(-20.63, -13.22) * mm, "end": v(-20.57, -13.2) * mm});
            skLineSegment(sketch, "E2375", {"start": v(-20.57, -13.2) * mm, "end": v(-20.52, -13.19) * mm});
            skLineSegment(sketch, "E2376", {"start": v(-20.52, -13.19) * mm, "end": v(-20.46, -13.17) * mm});
            skLineSegment(sketch, "E2377", {"start": v(-20.46, -13.17) * mm, "end": v(-20.41, -13.15) * mm});
            skLineSegment(sketch, "E2378", {"start": v(-20.41, -13.15) * mm, "end": v(-20.36, -13.14) * mm});
            skLineSegment(sketch, "E2379", {"start": v(-20.36, -13.14) * mm, "end": v(-20.31, -13.12) * mm});
            skLineSegment(sketch, "E2380", {"start": v(-20.31, -13.12) * mm, "end": v(-20.27, -13.1) * mm});
            skLineSegment(sketch, "E2381", {"start": v(-20.27, -13.1) * mm, "end": v(-20.22, -13.09) * mm});
            skLineSegment(sketch, "E2382", {"start": v(-20.22, -13.09) * mm, "end": v(-20.18, -13.07) * mm});
            skLineSegment(sketch, "E2383", {"start": v(-20.18, -13.07) * mm, "end": v(-20.14, -13.06) * mm});
            skLineSegment(sketch, "E2384", {"start": v(-20.14, -13.06) * mm, "end": v(-20.1, -13.04) * mm});
            skLineSegment(sketch, "E2385", {"start": v(-20.1, -13.04) * mm, "end": v(-20.06, -13.03) * mm});
            skLineSegment(sketch, "E2386", {"start": v(-20.06, -13.03) * mm, "end": v(-20.03, -13.01) * mm});
            skLineSegment(sketch, "E2387", {"start": v(-20.03, -13.01) * mm, "end": v(-20, -13) * mm});
            skLineSegment(sketch, "E2388", {"start": v(-20, -13) * mm, "end": v(-19.96, -12.98) * mm});
            skLineSegment(sketch, "E2389", {"start": v(-19.96, -12.98) * mm, "end": v(-19.93, -12.97) * mm});
            skLineSegment(sketch, "E2390", {"start": v(-19.93, -12.97) * mm, "end": v(-19.9, -12.96) * mm});
            skLineSegment(sketch, "E2391", {"start": v(-19.9, -12.96) * mm, "end": v(-19.88, -12.94) * mm});
            skLineSegment(sketch, "E2392", {"start": v(-19.88, -12.94) * mm, "end": v(-19.85, -12.93) * mm});
            skLineSegment(sketch, "E2393", {"start": v(-19.85, -12.93) * mm, "end": v(-19.83, -12.92) * mm});
            skLineSegment(sketch, "E2394", {"start": v(-19.83, -12.92) * mm, "end": v(-19.8, -12.91) * mm});
            skLineSegment(sketch, "E2395", {"start": v(-19.8, -12.91) * mm, "end": v(-19.79, -12.9) * mm});
            skLineSegment(sketch, "E2396", {"start": v(-19.79, -12.9) * mm, "end": v(-19.77, -12.9) * mm});
            skLineSegment(sketch, "E2397", {"start": v(-19.77, -12.9) * mm, "end": v(-19.75, -12.88) * mm});
            skLineSegment(sketch, "E2398", {"start": v(-19.75, -12.88) * mm, "end": v(-19.73, -12.88) * mm});
            skLineSegment(sketch, "E2399", {"start": v(-19.73, -12.88) * mm, "end": v(-19.06, -13.85) * mm});
            skLineSegment(sketch, "E2400", {"start": v(-19.06, -13.85) * mm, "end": v(-19.07, -13.87) * mm});
            skLineSegment(sketch, "E2401", {"start": v(-19.07, -13.87) * mm, "end": v(-19.09, -13.88) * mm});
            skLineSegment(sketch, "E2402", {"start": v(-19.09, -13.88) * mm, "end": v(-19.1, -13.9) * mm});
            skLineSegment(sketch, "E2403", {"start": v(-19.1, -13.9) * mm, "end": v(-19.12, -13.9) * mm});
            skLineSegment(sketch, "E2404", {"start": v(-19.12, -13.9) * mm, "end": v(-19.14, -13.92) * mm});
            skLineSegment(sketch, "E2405", {"start": v(-19.14, -13.92) * mm, "end": v(-19.16, -13.94) * mm});
            skLineSegment(sketch, "E2406", {"start": v(-19.16, -13.94) * mm, "end": v(-19.18, -13.96) * mm});
            skLineSegment(sketch, "E2407", {"start": v(-19.18, -13.96) * mm, "end": v(-19.2, -13.98) * mm});
            skLineSegment(sketch, "E2408", {"start": v(-19.2, -13.98) * mm, "end": v(-19.22, -14) * mm});
            skLineSegment(sketch, "E2409", {"start": v(-19.22, -14) * mm, "end": v(-19.24, -14.03) * mm});
            skLineSegment(sketch, "E2410", {"start": v(-19.24, -14.03) * mm, "end": v(-19.27, -14.05) * mm});
            skLineSegment(sketch, "E2411", {"start": v(-19.27, -14.05) * mm, "end": v(-19.3, -14.08) * mm});
            skLineSegment(sketch, "E2412", {"start": v(-19.3, -14.08) * mm, "end": v(-19.32, -14.1) * mm});
            skLineSegment(sketch, "E2413", {"start": v(-19.32, -14.1) * mm, "end": v(-19.35, -14.13) * mm});
            skLineSegment(sketch, "E2414", {"start": v(-19.35, -14.13) * mm, "end": v(-19.38, -14.17) * mm});
            skLineSegment(sketch, "E2415", {"start": v(-19.38, -14.17) * mm, "end": v(-19.4, -14.2) * mm});
            skLineSegment(sketch, "E2416", {"start": v(-19.4, -14.2) * mm, "end": v(-19.44, -14.23) * mm});
            skLineSegment(sketch, "E2417", {"start": v(-19.44, -14.23) * mm, "end": v(-19.47, -14.27) * mm});
            skLineSegment(sketch, "E2418", {"start": v(-19.47, -14.27) * mm, "end": v(-19.5, -14.3) * mm});
            skLineSegment(sketch, "E2419", {"start": v(-19.5, -14.3) * mm, "end": v(-19.53, -14.35) * mm});
            skLineSegment(sketch, "E2420", {"start": v(-19.53, -14.35) * mm, "end": v(-19.56, -14.39) * mm});
            skLineSegment(sketch, "E2421", {"start": v(-19.56, -14.39) * mm, "end": v(-19.6, -14.43) * mm});
            skLineSegment(sketch, "E2422", {"start": v(-19.6, -14.43) * mm, "end": v(-19.63, -14.47) * mm});
            skLineSegment(sketch, "E2423", {"start": v(-19.63, -14.47) * mm, "end": v(-19.67, -14.52) * mm});
            skLineSegment(sketch, "E2424", {"start": v(-19.67, -14.52) * mm, "end": v(-19.7, -14.57) * mm});
            skLineSegment(sketch, "E2425", {"start": v(-19.7, -14.57) * mm, "end": v(-19.74, -14.62) * mm});
            skLineSegment(sketch, "E2426", {"start": v(-19.74, -14.62) * mm, "end": v(-19.78, -14.67) * mm});
            skLineSegment(sketch, "E2427", {"start": v(-19.78, -14.67) * mm, "end": v(-19.82, -14.72) * mm});
            skLineSegment(sketch, "E2428", {"start": v(-19.82, -14.72) * mm, "end": v(-19.86, -14.78) * mm});
            skLineSegment(sketch, "E2429", {"start": v(-19.86, -14.78) * mm, "end": v(-19.9, -14.83) * mm});
            skLineSegment(sketch, "E2430", {"start": v(-19.9, -14.83) * mm, "end": v(-19.94, -14.9) * mm});
            skLineSegment(sketch, "E2431", {"start": v(-19.94, -14.9) * mm, "end": v(-19.98, -14.95) * mm});
            skLineSegment(sketch, "E2432", {"start": v(-19.98, -14.95) * mm, "end": v(-20.02, -15.01) * mm});
            skLineSegment(sketch, "E2433", {"start": v(-20.02, -15.01) * mm, "end": v(-20.06, -15.08) * mm});
            skLineSegment(sketch, "E2434", {"start": v(-20.06, -15.08) * mm, "end": v(-20.1, -15.14) * mm});
            skLineSegment(sketch, "E2435", {"start": v(-20.1, -15.14) * mm, "end": v(-20.14, -15.21) * mm});
            skLineSegment(sketch, "E2436", {"start": v(-20.14, -15.21) * mm, "end": v(-20.18, -15.28) * mm});
            skLineSegment(sketch, "E2437", {"start": v(-20.18, -15.28) * mm, "end": v(-20.23, -15.35) * mm});
            skLineSegment(sketch, "E2438", {"start": v(-20.23, -15.35) * mm, "end": v(-20.27, -15.42) * mm});
            skLineSegment(sketch, "E2439", {"start": v(-20.27, -15.42) * mm, "end": v(-20.31, -15.5) * mm});
            skLineSegment(sketch, "E2440", {"start": v(-20.31, -15.5) * mm, "end": v(-20.35, -15.58) * mm});
            skLineSegment(sketch, "E2441", {"start": v(-20.35, -15.58) * mm, "end": v(-20.4, -15.66) * mm});
            skLineSegment(sketch, "E2442", {"start": v(-20.4, -15.66) * mm, "end": v(-20.44, -15.74) * mm});
            skLineSegment(sketch, "E2443", {"start": v(-20.44, -15.74) * mm, "end": v(-20.49, -15.82) * mm});
            skLineSegment(sketch, "E2444", {"start": v(-20.49, -15.82) * mm, "end": v(-20.53, -15.9) * mm});
            skLineSegment(sketch, "E2445", {"start": v(-20.53, -15.9) * mm, "end": v(-20.57, -16) * mm});
            skLineSegment(sketch, "E2446", {"start": v(-20.57, -16) * mm, "end": v(-20.62, -16.08) * mm});
            skLineSegment(sketch, "E2447", {"start": v(-20.62, -16.08) * mm, "end": v(-20.66, -16.17) * mm});
            skLineSegment(sketch, "E2448", {"start": v(-20.66, -16.17) * mm, "end": v(-20.64, -16.22) * mm});
            skLineSegment(sketch, "E2449", {"start": v(-20.64, -16.22) * mm, "end": v(-20.12, -16.86) * mm});
            skLineSegment(sketch, "E2450", {"start": v(-20.12, -16.86) * mm, "end": v(-20.08, -16.9) * mm});
            skLineSegment(sketch, "E2451", {"start": v(-20.08, -16.9) * mm, "end": v(-19.98, -16.87) * mm});
            skLineSegment(sketch, "E2452", {"start": v(-19.98, -16.87) * mm, "end": v(-19.88, -16.84) * mm});
            skLineSegment(sketch, "E2453", {"start": v(-19.88, -16.84) * mm, "end": v(-19.79, -16.82) * mm});
            skLineSegment(sketch, "E2454", {"start": v(-19.79, -16.82) * mm, "end": v(-19.7, -16.8) * mm});
            skLineSegment(sketch, "E2455", {"start": v(-19.7, -16.8) * mm, "end": v(-19.6, -16.77) * mm});
            skLineSegment(sketch, "E2456", {"start": v(-19.6, -16.77) * mm, "end": v(-19.52, -16.74) * mm});
            skLineSegment(sketch, "E2457", {"start": v(-19.52, -16.74) * mm, "end": v(-19.43, -16.71) * mm});
            skLineSegment(sketch, "E2458", {"start": v(-19.43, -16.71) * mm, "end": v(-19.35, -16.69) * mm});
            skLineSegment(sketch, "E2459", {"start": v(-19.35, -16.69) * mm, "end": v(-19.26, -16.66) * mm});
            skLineSegment(sketch, "E2460", {"start": v(-19.26, -16.66) * mm, "end": v(-19.18, -16.63) * mm});
            skLineSegment(sketch, "E2461", {"start": v(-19.18, -16.63) * mm, "end": v(-19.1, -16.6) * mm});
            skLineSegment(sketch, "E2462", {"start": v(-19.1, -16.6) * mm, "end": v(-19.03, -16.58) * mm});
            skLineSegment(sketch, "E2463", {"start": v(-19.03, -16.58) * mm, "end": v(-18.95, -16.55) * mm});
            skLineSegment(sketch, "E2464", {"start": v(-18.95, -16.55) * mm, "end": v(-18.88, -16.53) * mm});
            skLineSegment(sketch, "E2465", {"start": v(-18.88, -16.53) * mm, "end": v(-18.8, -16.5) * mm});
            skLineSegment(sketch, "E2466", {"start": v(-18.8, -16.5) * mm, "end": v(-18.74, -16.47) * mm});
            skLineSegment(sketch, "E2467", {"start": v(-18.74, -16.47) * mm, "end": v(-18.67, -16.44) * mm});
            skLineSegment(sketch, "E2468", {"start": v(-18.67, -16.44) * mm, "end": v(-18.6, -16.42) * mm});
            skLineSegment(sketch, "E2469", {"start": v(-18.6, -16.42) * mm, "end": v(-18.54, -16.4) * mm});
            skLineSegment(sketch, "E2470", {"start": v(-18.54, -16.4) * mm, "end": v(-18.48, -16.36) * mm});
            skLineSegment(sketch, "E2471", {"start": v(-18.48, -16.36) * mm, "end": v(-18.42, -16.34) * mm});
            skLineSegment(sketch, "E2472", {"start": v(-18.42, -16.34) * mm, "end": v(-18.37, -16.31) * mm});
            skLineSegment(sketch, "E2473", {"start": v(-18.37, -16.31) * mm, "end": v(-18.3, -16.29) * mm});
            skLineSegment(sketch, "E2474", {"start": v(-18.3, -16.29) * mm, "end": v(-18.26, -16.26) * mm});
            skLineSegment(sketch, "E2475", {"start": v(-18.26, -16.26) * mm, "end": v(-18.2, -16.23) * mm});
            skLineSegment(sketch, "E2476", {"start": v(-18.2, -16.23) * mm, "end": v(-18.15, -16.2) * mm});
            skLineSegment(sketch, "E2477", {"start": v(-18.15, -16.2) * mm, "end": v(-18.1, -16.19) * mm});
            skLineSegment(sketch, "E2478", {"start": v(-18.1, -16.19) * mm, "end": v(-18.06, -16.16) * mm});
            skLineSegment(sketch, "E2479", {"start": v(-18.06, -16.16) * mm, "end": v(-18.01, -16.14) * mm});
            skLineSegment(sketch, "E2480", {"start": v(-18.01, -16.14) * mm, "end": v(-17.97, -16.11) * mm});
            skLineSegment(sketch, "E2481", {"start": v(-17.97, -16.11) * mm, "end": v(-17.93, -16.1) * mm});
            skLineSegment(sketch, "E2482", {"start": v(-17.93, -16.1) * mm, "end": v(-17.89, -16.07) * mm});
            skLineSegment(sketch, "E2483", {"start": v(-17.89, -16.07) * mm, "end": v(-17.85, -16.05) * mm});
            skLineSegment(sketch, "E2484", {"start": v(-17.85, -16.05) * mm, "end": v(-17.81, -16.03) * mm});
            skLineSegment(sketch, "E2485", {"start": v(-17.81, -16.03) * mm, "end": v(-17.78, -16) * mm});
            skLineSegment(sketch, "E2486", {"start": v(-17.78, -16) * mm, "end": v(-17.75, -15.98) * mm});
            skLineSegment(sketch, "E2487", {"start": v(-17.75, -15.98) * mm, "end": v(-17.71, -15.97) * mm});
            skLineSegment(sketch, "E2488", {"start": v(-17.71, -15.97) * mm, "end": v(-17.69, -15.95) * mm});
            skLineSegment(sketch, "E2489", {"start": v(-17.69, -15.95) * mm, "end": v(-17.66, -15.93) * mm});
            skLineSegment(sketch, "E2490", {"start": v(-17.66, -15.93) * mm, "end": v(-17.63, -15.91) * mm});
            skLineSegment(sketch, "E2491", {"start": v(-17.63, -15.91) * mm, "end": v(-17.6, -15.9) * mm});
            skLineSegment(sketch, "E2492", {"start": v(-17.6, -15.9) * mm, "end": v(-17.58, -15.88) * mm});
            skLineSegment(sketch, "E2493", {"start": v(-17.58, -15.88) * mm, "end": v(-17.56, -15.86) * mm});
            skLineSegment(sketch, "E2494", {"start": v(-17.56, -15.86) * mm, "end": v(-17.54, -15.85) * mm});
            skLineSegment(sketch, "E2495", {"start": v(-17.54, -15.85) * mm, "end": v(-17.52, -15.84) * mm});
            skLineSegment(sketch, "E2496", {"start": v(-17.52, -15.84) * mm, "end": v(-17.5, -15.83) * mm});
            skLineSegment(sketch, "E2497", {"start": v(-17.5, -15.83) * mm, "end": v(-17.5, -15.81) * mm});
            skLineSegment(sketch, "E2498", {"start": v(-17.5, -15.81) * mm, "end": v(-17.48, -15.8) * mm});
            skLineSegment(sketch, "E2499", {"start": v(-17.48, -15.8) * mm, "end": v(-16.66, -16.66) * mm});
            skLineSegment(sketch, "E2500", {"start": v(-16.66, -16.66) * mm, "end": v(-16.67, -16.68) * mm});
            skLineSegment(sketch, "E2501", {"start": v(-16.67, -16.68) * mm, "end": v(-16.68, -16.7) * mm});
            skLineSegment(sketch, "E2502", {"start": v(-16.68, -16.7) * mm, "end": v(-16.7, -16.7) * mm});
            skLineSegment(sketch, "E2503", {"start": v(-16.7, -16.7) * mm, "end": v(-16.71, -16.73) * mm});
            skLineSegment(sketch, "E2504", {"start": v(-16.71, -16.73) * mm, "end": v(-16.73, -16.75) * mm});
            skLineSegment(sketch, "E2505", {"start": v(-16.73, -16.75) * mm, "end": v(-16.74, -16.77) * mm});
            skLineSegment(sketch, "E2506", {"start": v(-16.74, -16.77) * mm, "end": v(-16.76, -16.79) * mm});
            skLineSegment(sketch, "E2507", {"start": v(-16.76, -16.79) * mm, "end": v(-16.78, -16.81) * mm});
            skLineSegment(sketch, "E2508", {"start": v(-16.78, -16.81) * mm, "end": v(-16.8, -16.84) * mm});
            skLineSegment(sketch, "E2509", {"start": v(-16.8, -16.84) * mm, "end": v(-16.81, -16.86) * mm});
            skLineSegment(sketch, "E2510", {"start": v(-16.81, -16.86) * mm, "end": v(-16.83, -16.9) * mm});
            skLineSegment(sketch, "E2511", {"start": v(-16.83, -16.9) * mm, "end": v(-16.85, -16.92) * mm});
            skLineSegment(sketch, "E2512", {"start": v(-16.85, -16.92) * mm, "end": v(-16.88, -16.95) * mm});
            skLineSegment(sketch, "E2513", {"start": v(-16.88, -16.95) * mm, "end": v(-16.9, -16.99) * mm});
            skLineSegment(sketch, "E2514", {"start": v(-16.9, -16.99) * mm, "end": v(-16.92, -17.02) * mm});
            skLineSegment(sketch, "E2515", {"start": v(-16.92, -17.02) * mm, "end": v(-16.95, -17.06) * mm});
            skLineSegment(sketch, "E2516", {"start": v(-16.95, -17.06) * mm, "end": v(-16.97, -17.1) * mm});
            skLineSegment(sketch, "E2517", {"start": v(-16.97, -17.1) * mm, "end": v(-17, -17.14) * mm});
            skLineSegment(sketch, "E2518", {"start": v(-17, -17.14) * mm, "end": v(-17.02, -17.18) * mm});
            skLineSegment(sketch, "E2519", {"start": v(-17.02, -17.18) * mm, "end": v(-17.05, -17.22) * mm});
            skLineSegment(sketch, "E2520", {"start": v(-17.05, -17.22) * mm, "end": v(-17.07, -17.27) * mm});
            skLineSegment(sketch, "E2521", {"start": v(-17.07, -17.27) * mm, "end": v(-17.1, -17.32) * mm});
            skLineSegment(sketch, "E2522", {"start": v(-17.1, -17.32) * mm, "end": v(-17.13, -17.37) * mm});
            skLineSegment(sketch, "E2523", {"start": v(-17.13, -17.37) * mm, "end": v(-17.16, -17.42) * mm});
            skLineSegment(sketch, "E2524", {"start": v(-17.16, -17.42) * mm, "end": v(-17.18, -17.47) * mm});
            skLineSegment(sketch, "E2525", {"start": v(-17.18, -17.47) * mm, "end": v(-17.21, -17.52) * mm});
            skLineSegment(sketch, "E2526", {"start": v(-17.21, -17.52) * mm, "end": v(-17.24, -17.58) * mm});
            skLineSegment(sketch, "E2527", {"start": v(-17.24, -17.58) * mm, "end": v(-17.27, -17.64) * mm});
            skLineSegment(sketch, "E2528", {"start": v(-17.27, -17.64) * mm, "end": v(-17.3, -17.7) * mm});
            skLineSegment(sketch, "E2529", {"start": v(-17.3, -17.7) * mm, "end": v(-17.33, -17.76) * mm});
            skLineSegment(sketch, "E2530", {"start": v(-17.33, -17.76) * mm, "end": v(-17.36, -17.83) * mm});
            skLineSegment(sketch, "E2531", {"start": v(-17.36, -17.83) * mm, "end": v(-17.4, -17.9) * mm});
            skLineSegment(sketch, "E2532", {"start": v(-17.4, -17.9) * mm, "end": v(-17.42, -17.96) * mm});
            skLineSegment(sketch, "E2533", {"start": v(-17.42, -17.96) * mm, "end": v(-17.45, -18.03) * mm});
            skLineSegment(sketch, "E2534", {"start": v(-17.45, -18.03) * mm, "end": v(-17.48, -18.1) * mm});
            skLineSegment(sketch, "E2535", {"start": v(-17.48, -18.1) * mm, "end": v(-17.51, -18.17) * mm});
            skLineSegment(sketch, "E2536", {"start": v(-17.51, -18.17) * mm, "end": v(-17.54, -18.25) * mm});
            skLineSegment(sketch, "E2537", {"start": v(-17.54, -18.25) * mm, "end": v(-17.57, -18.33) * mm});
            skLineSegment(sketch, "E2538", {"start": v(-17.57, -18.33) * mm, "end": v(-17.6, -18.4) * mm});
            skLineSegment(sketch, "E2539", {"start": v(-17.6, -18.4) * mm, "end": v(-17.64, -18.49) * mm});
            skLineSegment(sketch, "E2540", {"start": v(-17.64, -18.49) * mm, "end": v(-17.67, -18.57) * mm});
            skLineSegment(sketch, "E2541", {"start": v(-17.67, -18.57) * mm, "end": v(-17.7, -18.65) * mm});
            skLineSegment(sketch, "E2542", {"start": v(-17.7, -18.65) * mm, "end": v(-17.73, -18.74) * mm});
            skLineSegment(sketch, "E2543", {"start": v(-17.73, -18.74) * mm, "end": v(-17.76, -18.83) * mm});
            skLineSegment(sketch, "E2544", {"start": v(-17.76, -18.83) * mm, "end": v(-17.79, -18.92) * mm});
            skLineSegment(sketch, "E2545", {"start": v(-17.79, -18.92) * mm, "end": v(-17.82, -19.01) * mm});
            skLineSegment(sketch, "E2546", {"start": v(-17.82, -19.01) * mm, "end": v(-17.85, -19.1) * mm});
            skLineSegment(sketch, "E2547", {"start": v(-17.85, -19.1) * mm, "end": v(-17.88, -19.2) * mm});
            skLineSegment(sketch, "E2548", {"start": v(-17.88, -19.2) * mm, "end": v(-17.85, -19.25) * mm});
            skLineSegment(sketch, "E2549", {"start": v(-17.85, -19.25) * mm, "end": v(-17.23, -19.8) * mm});
            skLineSegment(sketch, "E2550", {"start": v(-17.23, -19.8) * mm, "end": v(-17.19, -19.82) * mm});
            skLineSegment(sketch, "E2551", {"start": v(-17.19, -19.82) * mm, "end": v(-17.1, -19.78) * mm});
            skLineSegment(sketch, "E2552", {"start": v(-17.1, -19.78) * mm, "end": v(-17, -19.75) * mm});
            skLineSegment(sketch, "E2553", {"start": v(-17, -19.75) * mm, "end": v(-16.92, -19.7) * mm});
            skLineSegment(sketch, "E2554", {"start": v(-16.92, -19.7) * mm, "end": v(-16.83, -19.67) * mm});
            skLineSegment(sketch, "E2555", {"start": v(-16.83, -19.67) * mm, "end": v(-16.74, -19.63) * mm});
            skLineSegment(sketch, "E2556", {"start": v(-16.74, -19.63) * mm, "end": v(-16.66, -19.59) * mm});
            skLineSegment(sketch, "E2557", {"start": v(-16.66, -19.59) * mm, "end": v(-16.58, -19.55) * mm});
            skLineSegment(sketch, "E2558", {"start": v(-16.58, -19.55) * mm, "end": v(-16.5, -19.5) * mm});
            skLineSegment(sketch, "E2559", {"start": v(-16.5, -19.5) * mm, "end": v(-16.42, -19.47) * mm});
            skLineSegment(sketch, "E2560", {"start": v(-16.42, -19.47) * mm, "end": v(-16.35, -19.43) * mm});
            skLineSegment(sketch, "E2561", {"start": v(-16.35, -19.43) * mm, "end": v(-16.27, -19.4) * mm});
            skLineSegment(sketch, "E2562", {"start": v(-16.27, -19.4) * mm, "end": v(-16.2, -19.35) * mm});
            skLineSegment(sketch, "E2563", {"start": v(-16.2, -19.35) * mm, "end": v(-16.13, -19.31) * mm});
            skLineSegment(sketch, "E2564", {"start": v(-16.13, -19.31) * mm, "end": v(-16.06, -19.28) * mm});
            skLineSegment(sketch, "E2565", {"start": v(-16.06, -19.28) * mm, "end": v(-16, -19.24) * mm});
            skLineSegment(sketch, "E2566", {"start": v(-16, -19.24) * mm, "end": v(-15.93, -19.2) * mm});
            skLineSegment(sketch, "E2567", {"start": v(-15.93, -19.2) * mm, "end": v(-15.87, -19.16) * mm});
            skLineSegment(sketch, "E2568", {"start": v(-15.87, -19.16) * mm, "end": v(-15.81, -19.13) * mm});
            skLineSegment(sketch, "E2569", {"start": v(-15.81, -19.13) * mm, "end": v(-15.75, -19.1) * mm});
            skLineSegment(sketch, "E2570", {"start": v(-15.75, -19.1) * mm, "end": v(-15.7, -19.05) * mm});
            skLineSegment(sketch, "E2571", {"start": v(-15.7, -19.05) * mm, "end": v(-15.64, -19.02) * mm});
            skLineSegment(sketch, "E2572", {"start": v(-15.64, -19.02) * mm, "end": v(-15.59, -18.98) * mm});
            skLineSegment(sketch, "E2573", {"start": v(-15.59, -18.98) * mm, "end": v(-15.54, -18.95) * mm});
            skLineSegment(sketch, "E2574", {"start": v(-15.54, -18.95) * mm, "end": v(-15.49, -18.92) * mm});
            skLineSegment(sketch, "E2575", {"start": v(-15.49, -18.92) * mm, "end": v(-15.44, -18.88) * mm});
            skLineSegment(sketch, "E2576", {"start": v(-15.44, -18.88) * mm, "end": v(-15.4, -18.85) * mm});
            skLineSegment(sketch, "E2577", {"start": v(-15.4, -18.85) * mm, "end": v(-15.35, -18.82) * mm});
            skLineSegment(sketch, "E2578", {"start": v(-15.35, -18.82) * mm, "end": v(-15.3, -18.79) * mm});
            skLineSegment(sketch, "E2579", {"start": v(-15.3, -18.79) * mm, "end": v(-15.27, -18.76) * mm});
            skLineSegment(sketch, "E2580", {"start": v(-15.27, -18.76) * mm, "end": v(-15.23, -18.73) * mm});
            skLineSegment(sketch, "E2581", {"start": v(-15.23, -18.73) * mm, "end": v(-15.19, -18.7) * mm});
            skLineSegment(sketch, "E2582", {"start": v(-15.19, -18.7) * mm, "end": v(-15.15, -18.67) * mm});
            skLineSegment(sketch, "E2583", {"start": v(-15.15, -18.67) * mm, "end": v(-15.12, -18.64) * mm});
            skLineSegment(sketch, "E2584", {"start": v(-15.12, -18.64) * mm, "end": v(-15.09, -18.61) * mm});
            skLineSegment(sketch, "E2585", {"start": v(-15.09, -18.61) * mm, "end": v(-15.06, -18.59) * mm});
            skLineSegment(sketch, "E2586", {"start": v(-15.06, -18.59) * mm, "end": v(-15.03, -18.56) * mm});
            skLineSegment(sketch, "E2587", {"start": v(-15.03, -18.56) * mm, "end": v(-15, -18.54) * mm});
            skLineSegment(sketch, "E2588", {"start": v(-15, -18.54) * mm, "end": v(-14.97, -18.52) * mm});
            skLineSegment(sketch, "E2589", {"start": v(-14.97, -18.52) * mm, "end": v(-14.95, -18.5) * mm});
            skLineSegment(sketch, "E2590", {"start": v(-14.95, -18.5) * mm, "end": v(-14.93, -18.47) * mm});
            skLineSegment(sketch, "E2591", {"start": v(-14.93, -18.47) * mm, "end": v(-14.9, -18.45) * mm});
            skLineSegment(sketch, "E2592", {"start": v(-14.9, -18.45) * mm, "end": v(-14.88, -18.43) * mm});
            skLineSegment(sketch, "E2593", {"start": v(-14.88, -18.43) * mm, "end": v(-14.86, -18.42) * mm});
            skLineSegment(sketch, "E2594", {"start": v(-14.86, -18.42) * mm, "end": v(-14.85, -18.4) * mm});
            skLineSegment(sketch, "E2595", {"start": v(-14.85, -18.4) * mm, "end": v(-14.83, -18.38) * mm});
            skLineSegment(sketch, "E2596", {"start": v(-14.83, -18.38) * mm, "end": v(-14.82, -18.37) * mm});
            skLineSegment(sketch, "E2597", {"start": v(-14.82, -18.37) * mm, "end": v(-14.8, -18.36) * mm});
            skLineSegment(sketch, "E2598", {"start": v(-14.8, -18.36) * mm, "end": v(-14.79, -18.34) * mm});
            skLineSegment(sketch, "E2599", {"start": v(-14.79, -18.34) * mm, "end": v(-13.85, -19.06) * mm});
            skLineSegment(sketch, "E2600", {"start": v(-13.85, -19.06) * mm, "end": v(-13.86, -19.08) * mm});
            skLineSegment(sketch, "E2601", {"start": v(-13.86, -19.08) * mm, "end": v(-13.87, -19.1) * mm});
            skLineSegment(sketch, "E2602", {"start": v(-13.87, -19.1) * mm, "end": v(-13.88, -19.11) * mm});
            skLineSegment(sketch, "E2603", {"start": v(-13.88, -19.11) * mm, "end": v(-13.89, -19.13) * mm});
            skLineSegment(sketch, "E2604", {"start": v(-13.89, -19.13) * mm, "end": v(-13.9, -19.16) * mm});
            skLineSegment(sketch, "E2605", {"start": v(-13.9, -19.16) * mm, "end": v(-13.91, -19.18) * mm});
            skLineSegment(sketch, "E2606", {"start": v(-13.91, -19.18) * mm, "end": v(-13.93, -19.2) * mm});
            skLineSegment(sketch, "E2607", {"start": v(-13.93, -19.2) * mm, "end": v(-13.94, -19.23) * mm});
            skLineSegment(sketch, "E2608", {"start": v(-13.94, -19.23) * mm, "end": v(-13.95, -19.26) * mm});
            skLineSegment(sketch, "E2609", {"start": v(-13.95, -19.26) * mm, "end": v(-13.97, -19.29) * mm});
            skLineSegment(sketch, "E2610", {"start": v(-13.97, -19.29) * mm, "end": v(-13.98, -19.32) * mm});
            skLineSegment(sketch, "E2611", {"start": v(-13.98, -19.32) * mm, "end": v(-14, -19.35) * mm});
            skLineSegment(sketch, "E2612", {"start": v(-14, -19.35) * mm, "end": v(-14.02, -19.39) * mm});
            skLineSegment(sketch, "E2613", {"start": v(-14.02, -19.39) * mm, "end": v(-14.03, -19.42) * mm});
            skLineSegment(sketch, "E2614", {"start": v(-14.03, -19.42) * mm, "end": v(-14.05, -19.46) * mm});
            skLineSegment(sketch, "E2615", {"start": v(-14.05, -19.46) * mm, "end": v(-14.07, -19.5) * mm});
            skLineSegment(sketch, "E2616", {"start": v(-14.07, -19.5) * mm, "end": v(-14.09, -19.54) * mm});
            skLineSegment(sketch, "E2617", {"start": v(-14.09, -19.54) * mm, "end": v(-14.1, -19.59) * mm});
            skLineSegment(sketch, "E2618", {"start": v(-14.1, -19.59) * mm, "end": v(-14.12, -19.63) * mm});
            skLineSegment(sketch, "E2619", {"start": v(-14.12, -19.63) * mm, "end": v(-14.14, -19.68) * mm});
            skLineSegment(sketch, "E2620", {"start": v(-14.14, -19.68) * mm, "end": v(-14.16, -19.73) * mm});
            skLineSegment(sketch, "E2621", {"start": v(-14.16, -19.73) * mm, "end": v(-14.18, -19.78) * mm});
            skLineSegment(sketch, "E2622", {"start": v(-14.18, -19.78) * mm, "end": v(-14.2, -19.83) * mm});
            skLineSegment(sketch, "E2623", {"start": v(-14.2, -19.83) * mm, "end": v(-14.22, -19.89) * mm});
            skLineSegment(sketch, "E2624", {"start": v(-14.22, -19.89) * mm, "end": v(-14.24, -19.94) * mm});
            skLineSegment(sketch, "E2625", {"start": v(-14.24, -19.94) * mm, "end": v(-14.26, -20) * mm});
            skLineSegment(sketch, "E2626", {"start": v(-14.26, -20) * mm, "end": v(-14.28, -20.06) * mm});
            skLineSegment(sketch, "E2627", {"start": v(-14.28, -20.06) * mm, "end": v(-14.3, -20.12) * mm});
            skLineSegment(sketch, "E2628", {"start": v(-14.3, -20.12) * mm, "end": v(-14.32, -20.19) * mm});
            skLineSegment(sketch, "E2629", {"start": v(-14.32, -20.19) * mm, "end": v(-14.34, -20.25) * mm});
            skLineSegment(sketch, "E2630", {"start": v(-14.34, -20.25) * mm, "end": v(-14.36, -20.32) * mm});
            skLineSegment(sketch, "E2631", {"start": v(-14.36, -20.32) * mm, "end": v(-14.38, -20.4) * mm});
            skLineSegment(sketch, "E2632", {"start": v(-14.38, -20.4) * mm, "end": v(-14.4, -20.46) * mm});
            skLineSegment(sketch, "E2633", {"start": v(-14.4, -20.46) * mm, "end": v(-14.42, -20.54) * mm});
            skLineSegment(sketch, "E2634", {"start": v(-14.42, -20.54) * mm, "end": v(-14.44, -20.61) * mm});
            skLineSegment(sketch, "E2635", {"start": v(-14.44, -20.61) * mm, "end": v(-14.45, -20.69) * mm});
            skLineSegment(sketch, "E2636", {"start": v(-14.45, -20.69) * mm, "end": v(-14.47, -20.77) * mm});
            skLineSegment(sketch, "E2637", {"start": v(-14.47, -20.77) * mm, "end": v(-14.5, -20.85) * mm});
            skLineSegment(sketch, "E2638", {"start": v(-14.5, -20.85) * mm, "end": v(-14.5, -20.93) * mm});
            skLineSegment(sketch, "E2639", {"start": v(-14.5, -20.93) * mm, "end": v(-14.53, -21.02) * mm});
            skLineSegment(sketch, "E2640", {"start": v(-14.53, -21.02) * mm, "end": v(-14.54, -21.1) * mm});
            skLineSegment(sketch, "E2641", {"start": v(-14.54, -21.1) * mm, "end": v(-14.56, -21.2) * mm});
            skLineSegment(sketch, "E2642", {"start": v(-14.56, -21.2) * mm, "end": v(-14.58, -21.28) * mm});
            skLineSegment(sketch, "E2643", {"start": v(-14.58, -21.28) * mm, "end": v(-14.6, -21.38) * mm});
            skLineSegment(sketch, "E2644", {"start": v(-14.6, -21.38) * mm, "end": v(-14.6, -21.47) * mm});
            skLineSegment(sketch, "E2645", {"start": v(-14.6, -21.47) * mm, "end": v(-14.62, -21.57) * mm});
            skLineSegment(sketch, "E2646", {"start": v(-14.62, -21.57) * mm, "end": v(-14.64, -21.67) * mm});
            skLineSegment(sketch, "E2647", {"start": v(-14.64, -21.67) * mm, "end": v(-14.65, -21.77) * mm});
            skLineSegment(sketch, "E2648", {"start": v(-14.65, -21.77) * mm, "end": v(-14.62, -21.8) * mm});
            skLineSegment(sketch, "E2649", {"start": v(-14.62, -21.8) * mm, "end": v(-13.92, -22.25) * mm});
            skLineSegment(sketch, "E2650", {"start": v(-13.92, -22.25) * mm, "end": v(-13.88, -22.27) * mm});
            skLineSegment(sketch, "E2651", {"start": v(-13.88, -22.27) * mm, "end": v(-13.79, -22.22) * mm});
            skLineSegment(sketch, "E2652", {"start": v(-13.79, -22.22) * mm, "end": v(-13.7, -22.16) * mm});
            skLineSegment(sketch, "E2653", {"start": v(-13.7, -22.16) * mm, "end": v(-13.62, -22.1) * mm});
            skLineSegment(sketch, "E2654", {"start": v(-13.62, -22.1) * mm, "end": v(-13.54, -22.06) * mm});
            skLineSegment(sketch, "E2655", {"start": v(-13.54, -22.06) * mm, "end": v(-13.47, -22) * mm});
            skLineSegment(sketch, "E2656", {"start": v(-13.47, -22) * mm, "end": v(-13.4, -21.95) * mm});
            skLineSegment(sketch, "E2657", {"start": v(-13.4, -21.95) * mm, "end": v(-13.32, -21.9) * mm});
            skLineSegment(sketch, "E2658", {"start": v(-13.32, -21.9) * mm, "end": v(-13.24, -21.85) * mm});
            skLineSegment(sketch, "E2659", {"start": v(-13.24, -21.85) * mm, "end": v(-13.17, -21.8) * mm});
            skLineSegment(sketch, "E2660", {"start": v(-13.17, -21.8) * mm, "end": v(-13.1, -21.75) * mm});
            skLineSegment(sketch, "E2661", {"start": v(-13.1, -21.75) * mm, "end": v(-13.04, -21.7) * mm});
            skLineSegment(sketch, "E2662", {"start": v(-13.04, -21.7) * mm, "end": v(-12.97, -21.65) * mm});
            skLineSegment(sketch, "E2663", {"start": v(-12.97, -21.65) * mm, "end": v(-12.91, -21.6) * mm});
            skLineSegment(sketch, "E2664", {"start": v(-12.91, -21.6) * mm, "end": v(-12.85, -21.55) * mm});
            skLineSegment(sketch, "E2665", {"start": v(-12.85, -21.55) * mm, "end": v(-12.8, -21.5) * mm});
            skLineSegment(sketch, "E2666", {"start": v(-12.8, -21.5) * mm, "end": v(-12.73, -21.46) * mm});
            skLineSegment(sketch, "E2667", {"start": v(-12.73, -21.46) * mm, "end": v(-12.68, -21.41) * mm});
            skLineSegment(sketch, "E2668", {"start": v(-12.68, -21.41) * mm, "end": v(-12.62, -21.36) * mm});
            skLineSegment(sketch, "E2669", {"start": v(-12.62, -21.36) * mm, "end": v(-12.57, -21.32) * mm});
            skLineSegment(sketch, "E2670", {"start": v(-12.57, -21.32) * mm, "end": v(-12.52, -21.28) * mm});
            skLineSegment(sketch, "E2671", {"start": v(-12.52, -21.28) * mm, "end": v(-12.47, -21.23) * mm});
            skLineSegment(sketch, "E2672", {"start": v(-12.47, -21.23) * mm, "end": v(-12.43, -21.19) * mm});
            skLineSegment(sketch, "E2673", {"start": v(-12.43, -21.19) * mm, "end": v(-12.38, -21.15) * mm});
            skLineSegment(sketch, "E2674", {"start": v(-12.38, -21.15) * mm, "end": v(-12.34, -21.1) * mm});
            skLineSegment(sketch, "E2675", {"start": v(-12.34, -21.1) * mm, "end": v(-12.3, -21.07) * mm});
            skLineSegment(sketch, "E2676", {"start": v(-12.3, -21.07) * mm, "end": v(-12.26, -21.03) * mm});
            skLineSegment(sketch, "E2677", {"start": v(-12.26, -21.03) * mm, "end": v(-12.22, -20.99) * mm});
            skLineSegment(sketch, "E2678", {"start": v(-12.22, -20.99) * mm, "end": v(-12.18, -20.95) * mm});
            skLineSegment(sketch, "E2679", {"start": v(-12.18, -20.95) * mm, "end": v(-12.14, -20.91) * mm});
            skLineSegment(sketch, "E2680", {"start": v(-12.14, -20.91) * mm, "end": v(-12.1, -20.88) * mm});
            skLineSegment(sketch, "E2681", {"start": v(-12.1, -20.88) * mm, "end": v(-12.08, -20.84) * mm});
            skLineSegment(sketch, "E2682", {"start": v(-12.08, -20.84) * mm, "end": v(-12.05, -20.8) * mm});
            skLineSegment(sketch, "E2683", {"start": v(-12.05, -20.8) * mm, "end": v(-12.02, -20.78) * mm});
            skLineSegment(sketch, "E2684", {"start": v(-12.02, -20.78) * mm, "end": v(-11.99, -20.75) * mm});
            skLineSegment(sketch, "E2685", {"start": v(-11.99, -20.75) * mm, "end": v(-11.96, -20.72) * mm});
            skLineSegment(sketch, "E2686", {"start": v(-11.96, -20.72) * mm, "end": v(-11.94, -20.69) * mm});
            skLineSegment(sketch, "E2687", {"start": v(-11.94, -20.69) * mm, "end": v(-11.91, -20.66) * mm});
            skLineSegment(sketch, "E2688", {"start": v(-11.91, -20.66) * mm, "end": v(-11.9, -20.63) * mm});
            skLineSegment(sketch, "E2689", {"start": v(-11.9, -20.63) * mm, "end": v(-11.87, -20.6) * mm});
            skLineSegment(sketch, "E2690", {"start": v(-11.87, -20.6) * mm, "end": v(-11.85, -20.58) * mm});
            skLineSegment(sketch, "E2691", {"start": v(-11.85, -20.58) * mm, "end": v(-11.83, -20.56) * mm});
            skLineSegment(sketch, "E2692", {"start": v(-11.83, -20.56) * mm, "end": v(-11.82, -20.54) * mm});
            skLineSegment(sketch, "E2693", {"start": v(-11.82, -20.54) * mm, "end": v(-11.8, -20.52) * mm});
            skLineSegment(sketch, "E2694", {"start": v(-11.8, -20.52) * mm, "end": v(-11.79, -20.5) * mm});
            skLineSegment(sketch, "E2695", {"start": v(-11.79, -20.5) * mm, "end": v(-11.77, -20.48) * mm});
            skLineSegment(sketch, "E2696", {"start": v(-11.77, -20.48) * mm, "end": v(-11.76, -20.46) * mm});
            skLineSegment(sketch, "E2697", {"start": v(-11.76, -20.46) * mm, "end": v(-11.75, -20.45) * mm});
            skLineSegment(sketch, "E2698", {"start": v(-11.75, -20.45) * mm, "end": v(-11.74, -20.43) * mm});
            skLineSegment(sketch, "E2699", {"start": v(-11.74, -20.43) * mm, "end": v(-10.7, -21) * mm});
            skLineSegment(sketch, "E2700", {"start": v(-10.7, -21) * mm, "end": v(-10.7, -21.01) * mm});
            skLineSegment(sketch, "E2701", {"start": v(-10.7, -21.01) * mm, "end": v(-10.7, -21.03) * mm});
            skLineSegment(sketch, "E2702", {"start": v(-10.7, -21.03) * mm, "end": v(-10.72, -21.05) * mm});
            skLineSegment(sketch, "E2703", {"start": v(-10.72, -21.05) * mm, "end": v(-10.72, -21.07) * mm});
            skLineSegment(sketch, "E2704", {"start": v(-10.72, -21.07) * mm, "end": v(-10.73, -21.1) * mm});
            skLineSegment(sketch, "E2705", {"start": v(-10.73, -21.1) * mm, "end": v(-10.74, -21.12) * mm});
            skLineSegment(sketch, "E2706", {"start": v(-10.74, -21.12) * mm, "end": v(-10.75, -21.14) * mm});
            skLineSegment(sketch, "E2707", {"start": v(-10.75, -21.14) * mm, "end": v(-10.76, -21.17) * mm});
            skLineSegment(sketch, "E2708", {"start": v(-10.76, -21.17) * mm, "end": v(-10.77, -21.2) * mm});
            skLineSegment(sketch, "E2709", {"start": v(-10.77, -21.2) * mm, "end": v(-10.78, -21.23) * mm});
            skLineSegment(sketch, "E2710", {"start": v(-10.78, -21.23) * mm, "end": v(-10.79, -21.27) * mm});
            skLineSegment(sketch, "E2711", {"start": v(-10.79, -21.27) * mm, "end": v(-10.8, -21.3) * mm});
            skLineSegment(sketch, "E2712", {"start": v(-10.8, -21.3) * mm, "end": v(-10.81, -21.34) * mm});
            skLineSegment(sketch, "E2713", {"start": v(-10.81, -21.34) * mm, "end": v(-10.82, -21.38) * mm});
            skLineSegment(sketch, "E2714", {"start": v(-10.82, -21.38) * mm, "end": v(-10.83, -21.42) * mm});
            skLineSegment(sketch, "E2715", {"start": v(-10.83, -21.42) * mm, "end": v(-10.84, -21.46) * mm});
            skLineSegment(sketch, "E2716", {"start": v(-10.84, -21.46) * mm, "end": v(-10.86, -21.5) * mm});
            skLineSegment(sketch, "E2717", {"start": v(-10.86, -21.5) * mm, "end": v(-10.87, -21.55) * mm});
            skLineSegment(sketch, "E2718", {"start": v(-10.87, -21.55) * mm, "end": v(-10.88, -21.6) * mm});
            skLineSegment(sketch, "E2719", {"start": v(-10.88, -21.6) * mm, "end": v(-10.89, -21.65) * mm});
            skLineSegment(sketch, "E2720", {"start": v(-10.89, -21.65) * mm, "end": v(-10.9, -21.7) * mm});
            skLineSegment(sketch, "E2721", {"start": v(-10.9, -21.7) * mm, "end": v(-10.91, -21.75) * mm});
            skLineSegment(sketch, "E2722", {"start": v(-10.91, -21.75) * mm, "end": v(-10.92, -21.8) * mm});
            skLineSegment(sketch, "E2723", {"start": v(-10.92, -21.8) * mm, "end": v(-10.93, -21.87) * mm});
            skLineSegment(sketch, "E2724", {"start": v(-10.93, -21.87) * mm, "end": v(-10.94, -21.93) * mm});
            skLineSegment(sketch, "E2725", {"start": v(-10.94, -21.93) * mm, "end": v(-10.95, -21.99) * mm});
            skLineSegment(sketch, "E2726", {"start": v(-10.95, -21.99) * mm, "end": v(-10.96, -22.05) * mm});
            skLineSegment(sketch, "E2727", {"start": v(-10.96, -22.05) * mm, "end": v(-10.97, -22.11) * mm});
            skLineSegment(sketch, "E2728", {"start": v(-10.97, -22.11) * mm, "end": v(-10.98, -22.18) * mm});
            skLineSegment(sketch, "E2729", {"start": v(-10.98, -22.18) * mm, "end": v(-11, -22.25) * mm});
            skLineSegment(sketch, "E2730", {"start": v(-11, -22.25) * mm, "end": v(-11, -22.32) * mm});
            skLineSegment(sketch, "E2731", {"start": v(-11, -22.32) * mm, "end": v(-11.01, -22.39) * mm});
            skLineSegment(sketch, "E2732", {"start": v(-11.01, -22.39) * mm, "end": v(-11.02, -22.46) * mm});
            skLineSegment(sketch, "E2733", {"start": v(-11.02, -22.46) * mm, "end": v(-11.03, -22.54) * mm});
            skLineSegment(sketch, "E2734", {"start": v(-11.03, -22.54) * mm, "end": v(-11.03, -22.62) * mm});
            skLineSegment(sketch, "E2735", {"start": v(-11.03, -22.62) * mm, "end": v(-11.04, -22.7) * mm});
            skLineSegment(sketch, "E2736", {"start": v(-11.04, -22.7) * mm, "end": v(-11.05, -22.78) * mm});
            skLineSegment(sketch, "E2737", {"start": v(-11.05, -22.78) * mm, "end": v(-11.05, -22.86) * mm});
            skLineSegment(sketch, "E2738", {"start": v(-11.05, -22.86) * mm, "end": v(-11.06, -22.95) * mm});
            skLineSegment(sketch, "E2739", {"start": v(-11.06, -22.95) * mm, "end": v(-11.06, -23.03) * mm});
            skLineSegment(sketch, "E2740", {"start": v(-11.06, -23.03) * mm, "end": v(-11.06, -23.12) * mm});
            skLineSegment(sketch, "E2741", {"start": v(-11.06, -23.12) * mm, "end": v(-11.07, -23.21) * mm});
            skLineSegment(sketch, "E2742", {"start": v(-11.07, -23.21) * mm, "end": v(-11.07, -23.3) * mm});
            skLineSegment(sketch, "E2743", {"start": v(-11.07, -23.3) * mm, "end": v(-11.07, -23.4) * mm});
            skLineSegment(sketch, "E2744", {"start": v(-11.07, -23.4) * mm, "end": v(-11.07, -23.5) * mm});
            skLineSegment(sketch, "E2745", {"start": v(-11.07, -23.5) * mm, "end": v(-11.07, -23.59) * mm});
            skLineSegment(sketch, "E2746", {"start": v(-11.07, -23.59) * mm, "end": v(-11.07, -23.69) * mm});
            skLineSegment(sketch, "E2747", {"start": v(-11.07, -23.69) * mm, "end": v(-11.07, -23.8) * mm});
            skLineSegment(sketch, "E2748", {"start": v(-11.07, -23.8) * mm, "end": v(-11.03, -23.82) * mm});
            skLineSegment(sketch, "E2749", {"start": v(-11.03, -23.82) * mm, "end": v(-10.27, -24.16) * mm});
            skLineSegment(sketch, "E2750", {"start": v(-10.27, -24.16) * mm, "end": v(-10.22, -24.17) * mm});
            skLineSegment(sketch, "E2751", {"start": v(-10.22, -24.17) * mm, "end": v(-10.14, -24.1) * mm});
            skLineSegment(sketch, "E2752", {"start": v(-10.14, -24.1) * mm, "end": v(-10.07, -24.03) * mm});
            skLineSegment(sketch, "E2753", {"start": v(-10.07, -24.03) * mm, "end": v(-10, -23.97) * mm});
            skLineSegment(sketch, "E2754", {"start": v(-10, -23.97) * mm, "end": v(-9.93, -23.9) * mm});
            skLineSegment(sketch, "E2755", {"start": v(-9.93, -23.9) * mm, "end": v(-9.86, -23.84) * mm});
            skLineSegment(sketch, "E2756", {"start": v(-9.86, -23.84) * mm, "end": v(-9.8, -23.78) * mm});
            skLineSegment(sketch, "E2757", {"start": v(-9.8, -23.78) * mm, "end": v(-9.73, -23.71) * mm});
            skLineSegment(sketch, "E2758", {"start": v(-9.73, -23.71) * mm, "end": v(-9.66, -23.65) * mm});
            skLineSegment(sketch, "E2759", {"start": v(-9.66, -23.65) * mm, "end": v(-9.6, -23.6) * mm});
            skLineSegment(sketch, "E2760", {"start": v(-9.6, -23.6) * mm, "end": v(-9.54, -23.53) * mm});
            skLineSegment(sketch, "E2761", {"start": v(-9.54, -23.53) * mm, "end": v(-9.48, -23.47) * mm});
            skLineSegment(sketch, "E2762", {"start": v(-9.48, -23.47) * mm, "end": v(-9.43, -23.41) * mm});
            skLineSegment(sketch, "E2763", {"start": v(-9.43, -23.41) * mm, "end": v(-9.37, -23.35) * mm});
            skLineSegment(sketch, "E2764", {"start": v(-9.37, -23.35) * mm, "end": v(-9.32, -23.3) * mm});
            skLineSegment(sketch, "E2765", {"start": v(-9.32, -23.3) * mm, "end": v(-9.27, -23.24) * mm});
            skLineSegment(sketch, "E2766", {"start": v(-9.27, -23.24) * mm, "end": v(-9.22, -23.18) * mm});
            skLineSegment(sketch, "E2767", {"start": v(-9.22, -23.18) * mm, "end": v(-9.17, -23.13) * mm});
            skLineSegment(sketch, "E2768", {"start": v(-9.17, -23.13) * mm, "end": v(-9.13, -23.08) * mm});
            skLineSegment(sketch, "E2769", {"start": v(-9.13, -23.08) * mm, "end": v(-9.08, -23.02) * mm});
            skLineSegment(sketch, "E2770", {"start": v(-9.08, -23.02) * mm, "end": v(-9.04, -22.97) * mm});
            skLineSegment(sketch, "E2771", {"start": v(-9.04, -22.97) * mm, "end": v(-9, -22.92) * mm});
            skLineSegment(sketch, "E2772", {"start": v(-9, -22.92) * mm, "end": v(-8.96, -22.87) * mm});
            skLineSegment(sketch, "E2773", {"start": v(-8.96, -22.87) * mm, "end": v(-8.92, -22.82) * mm});
            skLineSegment(sketch, "E2774", {"start": v(-8.92, -22.82) * mm, "end": v(-8.88, -22.78) * mm});
            skLineSegment(sketch, "E2775", {"start": v(-8.88, -22.78) * mm, "end": v(-8.85, -22.73) * mm});
            skLineSegment(sketch, "E2776", {"start": v(-8.85, -22.73) * mm, "end": v(-8.82, -22.68) * mm});
            skLineSegment(sketch, "E2777", {"start": v(-8.82, -22.68) * mm, "end": v(-8.78, -22.64) * mm});
            skLineSegment(sketch, "E2778", {"start": v(-8.78, -22.64) * mm, "end": v(-8.75, -22.6) * mm});
            skLineSegment(sketch, "E2779", {"start": v(-8.75, -22.6) * mm, "end": v(-8.72, -22.56) * mm});
            skLineSegment(sketch, "E2780", {"start": v(-8.72, -22.56) * mm, "end": v(-8.7, -22.52) * mm});
            skLineSegment(sketch, "E2781", {"start": v(-8.7, -22.52) * mm, "end": v(-8.67, -22.48) * mm});
            skLineSegment(sketch, "E2782", {"start": v(-8.67, -22.48) * mm, "end": v(-8.64, -22.44) * mm});
            skLineSegment(sketch, "E2783", {"start": v(-8.64, -22.44) * mm, "end": v(-8.62, -22.4) * mm});
            skLineSegment(sketch, "E2784", {"start": v(-8.62, -22.4) * mm, "end": v(-8.6, -22.37) * mm});
            skLineSegment(sketch, "E2785", {"start": v(-8.6, -22.37) * mm, "end": v(-8.57, -22.33) * mm});
            skLineSegment(sketch, "E2786", {"start": v(-8.57, -22.33) * mm, "end": v(-8.55, -22.3) * mm});
            skLineSegment(sketch, "E2787", {"start": v(-8.55, -22.3) * mm, "end": v(-8.54, -22.27) * mm});
            skLineSegment(sketch, "E2788", {"start": v(-8.54, -22.27) * mm, "end": v(-8.52, -22.24) * mm});
            skLineSegment(sketch, "E2789", {"start": v(-8.52, -22.24) * mm, "end": v(-8.5, -22.2) * mm});
            skLineSegment(sketch, "E2790", {"start": v(-8.5, -22.2) * mm, "end": v(-8.49, -22.18) * mm});
            skLineSegment(sketch, "E2791", {"start": v(-8.49, -22.18) * mm, "end": v(-8.47, -22.16) * mm});
            skLineSegment(sketch, "E2792", {"start": v(-8.47, -22.16) * mm, "end": v(-8.46, -22.13) * mm});
            skLineSegment(sketch, "E2793", {"start": v(-8.46, -22.13) * mm, "end": v(-8.45, -22.1) * mm});
            skLineSegment(sketch, "E2794", {"start": v(-8.45, -22.1) * mm, "end": v(-8.43, -22.09) * mm});
            skLineSegment(sketch, "E2795", {"start": v(-8.43, -22.09) * mm, "end": v(-8.42, -22.07) * mm});
            skLineSegment(sketch, "E2796", {"start": v(-8.42, -22.07) * mm, "end": v(-8.42, -22.05) * mm});
            skLineSegment(sketch, "E2797", {"start": v(-8.42, -22.05) * mm, "end": v(-8.4, -22.03) * mm});
            skLineSegment(sketch, "E2798", {"start": v(-8.4, -22.03) * mm, "end": v(-8.4, -22.02) * mm});
            skLineSegment(sketch, "E2799", {"start": v(-8.4, -22.02) * mm, "end": v(-7.28, -22.4) * mm});
            skLineSegment(sketch, "E2800", {"start": v(-7.28, -22.4) * mm, "end": v(-7.28, -22.43) * mm});
            skLineSegment(sketch, "E2801", {"start": v(-7.28, -22.43) * mm, "end": v(-7.29, -22.45) * mm});
            skLineSegment(sketch, "E2802", {"start": v(-7.29, -22.45) * mm, "end": v(-7.3, -22.47) * mm});
            skLineSegment(sketch, "E2803", {"start": v(-7.3, -22.47) * mm, "end": v(-7.3, -22.49) * mm});
            skLineSegment(sketch, "E2804", {"start": v(-7.3, -22.49) * mm, "end": v(-7.3, -22.51) * mm});
            skLineSegment(sketch, "E2805", {"start": v(-7.3, -22.51) * mm, "end": v(-7.3, -22.54) * mm});
            skLineSegment(sketch, "E2806", {"start": v(-7.3, -22.54) * mm, "end": v(-7.3, -22.57) * mm});
            skLineSegment(sketch, "E2807", {"start": v(-7.3, -22.57) * mm, "end": v(-7.31, -22.6) * mm});
            skLineSegment(sketch, "E2808", {"start": v(-7.31, -22.6) * mm, "end": v(-7.32, -22.63) * mm});
            skLineSegment(sketch, "E2809", {"start": v(-7.32, -22.63) * mm, "end": v(-7.32, -22.66) * mm});
            skLineSegment(sketch, "E2810", {"start": v(-7.32, -22.66) * mm, "end": v(-7.33, -22.7) * mm});
            skLineSegment(sketch, "E2811", {"start": v(-7.33, -22.7) * mm, "end": v(-7.33, -22.73) * mm});
            skLineSegment(sketch, "E2812", {"start": v(-7.33, -22.73) * mm, "end": v(-7.34, -22.77) * mm});
            skLineSegment(sketch, "E2813", {"start": v(-7.34, -22.77) * mm, "end": v(-7.34, -22.8) * mm});
            skLineSegment(sketch, "E2814", {"start": v(-7.34, -22.8) * mm, "end": v(-7.35, -22.85) * mm});
            skLineSegment(sketch, "E2815", {"start": v(-7.35, -22.85) * mm, "end": v(-7.35, -22.9) * mm});
            skLineSegment(sketch, "E2816", {"start": v(-7.35, -22.9) * mm, "end": v(-7.36, -22.94) * mm});
            skLineSegment(sketch, "E2817", {"start": v(-7.36, -22.94) * mm, "end": v(-7.36, -22.99) * mm});
            skLineSegment(sketch, "E2818", {"start": v(-7.36, -22.99) * mm, "end": v(-7.37, -23.03) * mm});
            skLineSegment(sketch, "E2819", {"start": v(-7.37, -23.03) * mm, "end": v(-7.37, -23.09) * mm});
            skLineSegment(sketch, "E2820", {"start": v(-7.37, -23.09) * mm, "end": v(-7.37, -23.14) * mm});
            skLineSegment(sketch, "E2821", {"start": v(-7.37, -23.14) * mm, "end": v(-7.37, -23.2) * mm});
            skLineSegment(sketch, "E2822", {"start": v(-7.37, -23.2) * mm, "end": v(-7.38, -23.25) * mm});
            skLineSegment(sketch, "E2823", {"start": v(-7.38, -23.25) * mm, "end": v(-7.38, -23.3) * mm});
            skLineSegment(sketch, "E2824", {"start": v(-7.38, -23.3) * mm, "end": v(-7.38, -23.37) * mm});
            skLineSegment(sketch, "E2825", {"start": v(-7.38, -23.37) * mm, "end": v(-7.38, -23.43) * mm});
            skLineSegment(sketch, "E2826", {"start": v(-7.38, -23.43) * mm, "end": v(-7.38, -23.5) * mm});
            skLineSegment(sketch, "E2827", {"start": v(-7.38, -23.5) * mm, "end": v(-7.38, -23.56) * mm});
            skLineSegment(sketch, "E2828", {"start": v(-7.38, -23.56) * mm, "end": v(-7.38, -23.62) * mm});
            skLineSegment(sketch, "E2829", {"start": v(-7.38, -23.62) * mm, "end": v(-7.38, -23.7) * mm});
            skLineSegment(sketch, "E2830", {"start": v(-7.38, -23.7) * mm, "end": v(-7.38, -23.76) * mm});
            skLineSegment(sketch, "E2831", {"start": v(-7.38, -23.76) * mm, "end": v(-7.37, -23.84) * mm});
            skLineSegment(sketch, "E2832", {"start": v(-7.37, -23.84) * mm, "end": v(-7.37, -23.91) * mm});
            skLineSegment(sketch, "E2833", {"start": v(-7.37, -23.91) * mm, "end": v(-7.36, -23.99) * mm});
            skLineSegment(sketch, "E2834", {"start": v(-7.36, -23.99) * mm, "end": v(-7.36, -24.06) * mm});
            skLineSegment(sketch, "E2835", {"start": v(-7.36, -24.06) * mm, "end": v(-7.35, -24.14) * mm});
            skLineSegment(sketch, "E2836", {"start": v(-7.35, -24.14) * mm, "end": v(-7.35, -24.22) * mm});
            skLineSegment(sketch, "E2837", {"start": v(-7.35, -24.22) * mm, "end": v(-7.34, -24.3) * mm});
            skLineSegment(sketch, "E2838", {"start": v(-7.34, -24.3) * mm, "end": v(-7.33, -24.4) * mm});
            skLineSegment(sketch, "E2839", {"start": v(-7.33, -24.4) * mm, "end": v(-7.32, -24.48) * mm});
            skLineSegment(sketch, "E2840", {"start": v(-7.32, -24.48) * mm, "end": v(-7.31, -24.57) * mm});
            skLineSegment(sketch, "E2841", {"start": v(-7.31, -24.57) * mm, "end": v(-7.3, -24.66) * mm});
            skLineSegment(sketch, "E2842", {"start": v(-7.3, -24.66) * mm, "end": v(-7.29, -24.75) * mm});
            skLineSegment(sketch, "E2843", {"start": v(-7.29, -24.75) * mm, "end": v(-7.27, -24.84) * mm});
            skLineSegment(sketch, "E2844", {"start": v(-7.27, -24.84) * mm, "end": v(-7.26, -24.93) * mm});
            skLineSegment(sketch, "E2845", {"start": v(-7.26, -24.93) * mm, "end": v(-7.24, -25.03) * mm});
            skLineSegment(sketch, "E2846", {"start": v(-7.24, -25.03) * mm, "end": v(-7.23, -25.13) * mm});
            skLineSegment(sketch, "E2847", {"start": v(-7.23, -25.13) * mm, "end": v(-7.2, -25.23) * mm});
            skLineSegment(sketch, "E2848", {"start": v(-7.2, -25.23) * mm, "end": v(-7.17, -25.25) * mm});
            skLineSegment(sketch, "E2849", {"start": v(-7.17, -25.25) * mm, "end": v(-6.36, -25.47) * mm});
            skLineSegment(sketch, "E2850", {"start": v(-6.36, -25.47) * mm, "end": v(-6.32, -25.47) * mm});
            skLineSegment(sketch, "E2851", {"start": v(-6.32, -25.47) * mm, "end": v(-6.25, -25.39) * mm});
            skLineSegment(sketch, "E2852", {"start": v(-6.25, -25.39) * mm, "end": v(-6.19, -25.31) * mm});
            skLineSegment(sketch, "E2853", {"start": v(-6.19, -25.31) * mm, "end": v(-6.13, -25.24) * mm});
            skLineSegment(sketch, "E2854", {"start": v(-6.13, -25.24) * mm, "end": v(-6.07, -25.16) * mm});
            skLineSegment(sketch, "E2855", {"start": v(-6.07, -25.16) * mm, "end": v(-6, -25.09) * mm});
            skLineSegment(sketch, "E2856", {"start": v(-6, -25.09) * mm, "end": v(-5.95, -25.02) * mm});
            skLineSegment(sketch, "E2857", {"start": v(-5.95, -25.02) * mm, "end": v(-5.9, -24.94) * mm});
            skLineSegment(sketch, "E2858", {"start": v(-5.9, -24.94) * mm, "end": v(-5.84, -24.87) * mm});
            skLineSegment(sketch, "E2859", {"start": v(-5.84, -24.87) * mm, "end": v(-5.8, -24.8) * mm});
            skLineSegment(sketch, "E2860", {"start": v(-5.8, -24.8) * mm, "end": v(-5.74, -24.73) * mm});
            skLineSegment(sketch, "E2861", {"start": v(-5.74, -24.73) * mm, "end": v(-5.7, -24.67) * mm});
            skLineSegment(sketch, "E2862", {"start": v(-5.7, -24.67) * mm, "end": v(-5.65, -24.6) * mm});
            skLineSegment(sketch, "E2863", {"start": v(-5.65, -24.6) * mm, "end": v(-5.6, -24.53) * mm});
            skLineSegment(sketch, "E2864", {"start": v(-5.6, -24.53) * mm, "end": v(-5.56, -24.47) * mm});
            skLineSegment(sketch, "E2865", {"start": v(-5.56, -24.47) * mm, "end": v(-5.52, -24.4) * mm});
            skLineSegment(sketch, "E2866", {"start": v(-5.52, -24.4) * mm, "end": v(-5.48, -24.34) * mm});
            skLineSegment(sketch, "E2867", {"start": v(-5.48, -24.34) * mm, "end": v(-5.44, -24.28) * mm});
            skLineSegment(sketch, "E2868", {"start": v(-5.44, -24.28) * mm, "end": v(-5.4, -24.22) * mm});
            skLineSegment(sketch, "E2869", {"start": v(-5.4, -24.22) * mm, "end": v(-5.37, -24.16) * mm});
            skLineSegment(sketch, "E2870", {"start": v(-5.37, -24.16) * mm, "end": v(-5.33, -24.1) * mm});
            skLineSegment(sketch, "E2871", {"start": v(-5.33, -24.1) * mm, "end": v(-5.3, -24.05) * mm});
            skLineSegment(sketch, "E2872", {"start": v(-5.3, -24.05) * mm, "end": v(-5.27, -24) * mm});
            skLineSegment(sketch, "E2873", {"start": v(-5.27, -24) * mm, "end": v(-5.24, -23.94) * mm});
            skLineSegment(sketch, "E2874", {"start": v(-5.24, -23.94) * mm, "end": v(-5.21, -23.89) * mm});
            skLineSegment(sketch, "E2875", {"start": v(-5.21, -23.89) * mm, "end": v(-5.18, -23.83) * mm});
            skLineSegment(sketch, "E2876", {"start": v(-5.18, -23.83) * mm, "end": v(-5.16, -23.78) * mm});
            skLineSegment(sketch, "E2877", {"start": v(-5.16, -23.78) * mm, "end": v(-5.13, -23.74) * mm});
            skLineSegment(sketch, "E2878", {"start": v(-5.13, -23.74) * mm, "end": v(-5.1, -23.69) * mm});
            skLineSegment(sketch, "E2879", {"start": v(-5.1, -23.69) * mm, "end": v(-5.09, -23.64) * mm});
            skLineSegment(sketch, "E2880", {"start": v(-5.09, -23.64) * mm, "end": v(-5.07, -23.6) * mm});
            skLineSegment(sketch, "E2881", {"start": v(-5.07, -23.6) * mm, "end": v(-5.05, -23.56) * mm});
            skLineSegment(sketch, "E2882", {"start": v(-5.05, -23.56) * mm, "end": v(-5.03, -23.51) * mm});
            skLineSegment(sketch, "E2883", {"start": v(-5.03, -23.51) * mm, "end": v(-5, -23.47) * mm});
            skLineSegment(sketch, "E2884", {"start": v(-5, -23.47) * mm, "end": v(-5, -23.44) * mm});
            skLineSegment(sketch, "E2885", {"start": v(-5, -23.44) * mm, "end": v(-4.98, -23.4) * mm});
            skLineSegment(sketch, "E2886", {"start": v(-4.98, -23.4) * mm, "end": v(-4.96, -23.36) * mm});
            skLineSegment(sketch, "E2887", {"start": v(-4.96, -23.36) * mm, "end": v(-4.95, -23.33) * mm});
            skLineSegment(sketch, "E2888", {"start": v(-4.95, -23.33) * mm, "end": v(-4.93, -23.3) * mm});
            skLineSegment(sketch, "E2889", {"start": v(-4.93, -23.3) * mm, "end": v(-4.92, -23.27) * mm});
            skLineSegment(sketch, "E2890", {"start": v(-4.92, -23.27) * mm, "end": v(-4.91, -23.24) * mm});
            skLineSegment(sketch, "E2891", {"start": v(-4.91, -23.24) * mm, "end": v(-4.9, -23.2) * mm});
            skLineSegment(sketch, "E2892", {"start": v(-4.9, -23.2) * mm, "end": v(-4.9, -23.18) * mm});
            skLineSegment(sketch, "E2893", {"start": v(-4.9, -23.18) * mm, "end": v(-4.88, -23.16) * mm});
            skLineSegment(sketch, "E2894", {"start": v(-4.88, -23.16) * mm, "end": v(-4.88, -23.13) * mm});
            skLineSegment(sketch, "E2895", {"start": v(-4.88, -23.13) * mm, "end": v(-4.87, -23.11) * mm});
            skLineSegment(sketch, "E2896", {"start": v(-4.87, -23.11) * mm, "end": v(-4.86, -23.1) * mm});
            skLineSegment(sketch, "E2897", {"start": v(-4.86, -23.1) * mm, "end": v(-4.86, -23.08) * mm});
            skLineSegment(sketch, "E2898", {"start": v(-4.86, -23.08) * mm, "end": v(-4.85, -23.06) * mm});
            skLineSegment(sketch, "E2899", {"start": v(-4.85, -23.06) * mm, "end": v(-3.69, -23.27) * mm});
            skLineSegment(sketch, "E2900", {"start": v(-3.69, -23.27) * mm, "end": v(-3.68, -23.3) * mm});
            skLineSegment(sketch, "E2901", {"start": v(-3.68, -23.3) * mm, "end": v(-3.69, -23.31) * mm});
            skLineSegment(sketch, "E2902", {"start": v(-3.69, -23.31) * mm, "end": v(-3.69, -23.33) * mm});
            skLineSegment(sketch, "E2903", {"start": v(-3.69, -23.33) * mm, "end": v(-3.69, -23.35) * mm});
            skLineSegment(sketch, "E2904", {"start": v(-3.69, -23.35) * mm, "end": v(-3.69, -23.38) * mm});
            skLineSegment(sketch, "E2905", {"start": v(-3.69, -23.38) * mm, "end": v(-3.69, -23.4) * mm});
            skLineSegment(sketch, "E2906", {"start": v(-3.69, -23.4) * mm, "end": v(-3.69, -23.43) * mm});
            skLineSegment(sketch, "E2907", {"start": v(-3.69, -23.43) * mm, "end": v(-3.7, -23.46) * mm});
            skLineSegment(sketch, "E2908", {"start": v(-3.7, -23.46) * mm, "end": v(-3.7, -23.5) * mm});
            skLineSegment(sketch, "E2909", {"start": v(-3.7, -23.5) * mm, "end": v(-3.7, -23.53) * mm});
            skLineSegment(sketch, "E2910", {"start": v(-3.7, -23.53) * mm, "end": v(-3.69, -23.56) * mm});
            skLineSegment(sketch, "E2911", {"start": v(-3.69, -23.56) * mm, "end": v(-3.69, -23.6) * mm});
            skLineSegment(sketch, "E2912", {"start": v(-3.69, -23.6) * mm, "end": v(-3.69, -23.64) * mm});
            skLineSegment(sketch, "E2913", {"start": v(-3.69, -23.64) * mm, "end": v(-3.69, -23.68) * mm});
            skLineSegment(sketch, "E2914", {"start": v(-3.69, -23.68) * mm, "end": v(-3.68, -23.72) * mm});
            skLineSegment(sketch, "E2915", {"start": v(-3.68, -23.72) * mm, "end": v(-3.68, -23.76) * mm});
            skLineSegment(sketch, "E2916", {"start": v(-3.68, -23.76) * mm, "end": v(-3.68, -23.8) * mm});
            skLineSegment(sketch, "E2917", {"start": v(-3.68, -23.8) * mm, "end": v(-3.68, -23.85) * mm});
            skLineSegment(sketch, "E2918", {"start": v(-3.68, -23.85) * mm, "end": v(-3.67, -23.9) * mm});
            skLineSegment(sketch, "E2919", {"start": v(-3.67, -23.9) * mm, "end": v(-3.67, -23.95) * mm});
            skLineSegment(sketch, "E2920", {"start": v(-3.67, -23.95) * mm, "end": v(-3.66, -24) * mm});
            skLineSegment(sketch, "E2921", {"start": v(-3.66, -24) * mm, "end": v(-3.66, -24.06) * mm});
            skLineSegment(sketch, "E2922", {"start": v(-3.66, -24.06) * mm, "end": v(-3.65, -24.12) * mm});
            skLineSegment(sketch, "E2923", {"start": v(-3.65, -24.12) * mm, "end": v(-3.64, -24.17) * mm});
            skLineSegment(sketch, "E2924", {"start": v(-3.64, -24.17) * mm, "end": v(-3.63, -24.23) * mm});
            skLineSegment(sketch, "E2925", {"start": v(-3.63, -24.23) * mm, "end": v(-3.62, -24.3) * mm});
            skLineSegment(sketch, "E2926", {"start": v(-3.62, -24.3) * mm, "end": v(-3.61, -24.36) * mm});
            skLineSegment(sketch, "E2927", {"start": v(-3.61, -24.36) * mm, "end": v(-3.6, -24.42) * mm});
            skLineSegment(sketch, "E2928", {"start": v(-3.6, -24.42) * mm, "end": v(-3.6, -24.49) * mm});
            skLineSegment(sketch, "E2929", {"start": v(-3.6, -24.49) * mm, "end": v(-3.58, -24.56) * mm});
            skLineSegment(sketch, "E2930", {"start": v(-3.58, -24.56) * mm, "end": v(-3.57, -24.63) * mm});
            skLineSegment(sketch, "E2931", {"start": v(-3.57, -24.63) * mm, "end": v(-3.55, -24.7) * mm});
            skLineSegment(sketch, "E2932", {"start": v(-3.55, -24.7) * mm, "end": v(-3.54, -24.77) * mm});
            skLineSegment(sketch, "E2933", {"start": v(-3.54, -24.77) * mm, "end": v(-3.52, -24.84) * mm});
            skLineSegment(sketch, "E2934", {"start": v(-3.52, -24.84) * mm, "end": v(-3.5, -24.92) * mm});
            skLineSegment(sketch, "E2935", {"start": v(-3.5, -24.92) * mm, "end": v(-3.49, -25) * mm});
            skLineSegment(sketch, "E2936", {"start": v(-3.49, -25) * mm, "end": v(-3.47, -25.08) * mm});
            skLineSegment(sketch, "E2937", {"start": v(-3.47, -25.08) * mm, "end": v(-3.45, -25.16) * mm});
            skLineSegment(sketch, "E2938", {"start": v(-3.45, -25.16) * mm, "end": v(-3.42, -25.24) * mm});
            skLineSegment(sketch, "E2939", {"start": v(-3.42, -25.24) * mm, "end": v(-3.4, -25.32) * mm});
            skLineSegment(sketch, "E2940", {"start": v(-3.4, -25.32) * mm, "end": v(-3.38, -25.4) * mm});
            skLineSegment(sketch, "E2941", {"start": v(-3.38, -25.4) * mm, "end": v(-3.35, -25.5) * mm});
            skLineSegment(sketch, "E2942", {"start": v(-3.35, -25.5) * mm, "end": v(-3.33, -25.58) * mm});
            skLineSegment(sketch, "E2943", {"start": v(-3.33, -25.58) * mm, "end": v(-3.3, -25.67) * mm});
            skLineSegment(sketch, "E2944", {"start": v(-3.3, -25.67) * mm, "end": v(-3.27, -25.76) * mm});
            skLineSegment(sketch, "E2945", {"start": v(-3.27, -25.76) * mm, "end": v(-3.24, -25.86) * mm});
            skLineSegment(sketch, "E2946", {"start": v(-3.24, -25.86) * mm, "end": v(-3.2, -25.95) * mm});
            skLineSegment(sketch, "E2947", {"start": v(-3.2, -25.95) * mm, "end": v(-3.17, -26.05) * mm});
            skLineSegment(sketch, "E2948", {"start": v(-3.17, -26.05) * mm, "end": v(-3.13, -26.06) * mm});
            skLineSegment(sketch, "E2949", {"start": v(-3.13, -26.06) * mm, "end": v(-2.3, -26.15) * mm});
            skLineSegment(sketch, "E2950", {"start": v(-2.3, -26.15) * mm, "end": v(-2.25, -26.14) * mm});
            skLineSegment(sketch, "E2951", {"start": v(-2.25, -26.14) * mm, "end": v(-2.2, -26.05) * mm});
            skLineSegment(sketch, "E2952", {"start": v(-2.2, -26.05) * mm, "end": v(-2.15, -25.97) * mm});
            skLineSegment(sketch, "E2953", {"start": v(-2.15, -25.97) * mm, "end": v(-2.1, -25.88) * mm});
            skLineSegment(sketch, "E2954", {"start": v(-2.1, -25.88) * mm, "end": v(-2.05, -25.8) * mm});
            skLineSegment(sketch, "E2955", {"start": v(-2.05, -25.8) * mm, "end": v(-2, -25.72) * mm});
            skLineSegment(sketch, "E2956", {"start": v(-2, -25.72) * mm, "end": v(-1.96, -25.64) * mm});
            skLineSegment(sketch, "E2957", {"start": v(-1.96, -25.64) * mm, "end": v(-1.92, -25.56) * mm});
            skLineSegment(sketch, "E2958", {"start": v(-1.92, -25.56) * mm, "end": v(-1.88, -25.48) * mm});
            skLineSegment(sketch, "E2959", {"start": v(-1.88, -25.48) * mm, "end": v(-1.84, -25.4) * mm});
            skLineSegment(sketch, "E2960", {"start": v(-1.84, -25.4) * mm, "end": v(-1.8, -25.33) * mm});
            skLineSegment(sketch, "E2961", {"start": v(-1.8, -25.33) * mm, "end": v(-1.77, -25.25) * mm});
            skLineSegment(sketch, "E2962", {"start": v(-1.77, -25.25) * mm, "end": v(-1.73, -25.18) * mm});
            skLineSegment(sketch, "E2963", {"start": v(-1.73, -25.18) * mm, "end": v(-1.7, -25.1) * mm});
            skLineSegment(sketch, "E2964", {"start": v(-1.7, -25.1) * mm, "end": v(-1.67, -25.04) * mm});
            skLineSegment(sketch, "E2965", {"start": v(-1.67, -25.04) * mm, "end": v(-1.63, -24.97) * mm});
            skLineSegment(sketch, "E2966", {"start": v(-1.63, -24.97) * mm, "end": v(-1.6, -24.9) * mm});
            skLineSegment(sketch, "E2967", {"start": v(-1.6, -24.9) * mm, "end": v(-1.58, -24.83) * mm});
            skLineSegment(sketch, "E2968", {"start": v(-1.58, -24.83) * mm, "end": v(-1.55, -24.77) * mm});
            skLineSegment(sketch, "E2969", {"start": v(-1.55, -24.77) * mm, "end": v(-1.52, -24.7) * mm});
            skLineSegment(sketch, "E2970", {"start": v(-1.52, -24.7) * mm, "end": v(-1.5, -24.64) * mm});
            skLineSegment(sketch, "E2971", {"start": v(-1.5, -24.64) * mm, "end": v(-1.47, -24.58) * mm});
            skLineSegment(sketch, "E2972", {"start": v(-1.47, -24.58) * mm, "end": v(-1.45, -24.52) * mm});
            skLineSegment(sketch, "E2973", {"start": v(-1.45, -24.52) * mm, "end": v(-1.43, -24.46) * mm});
            skLineSegment(sketch, "E2974", {"start": v(-1.43, -24.46) * mm, "end": v(-1.41, -24.4) * mm});
            skLineSegment(sketch, "E2975", {"start": v(-1.41, -24.4) * mm, "end": v(-1.4, -24.35) * mm});
            skLineSegment(sketch, "E2976", {"start": v(-1.4, -24.35) * mm, "end": v(-1.37, -24.3) * mm});
            skLineSegment(sketch, "E2977", {"start": v(-1.37, -24.3) * mm, "end": v(-1.36, -24.25) * mm});
            skLineSegment(sketch, "E2978", {"start": v(-1.36, -24.25) * mm, "end": v(-1.34, -24.2) * mm});
            skLineSegment(sketch, "E2979", {"start": v(-1.34, -24.2) * mm, "end": v(-1.33, -24.15) * mm});
            skLineSegment(sketch, "E2980", {"start": v(-1.33, -24.15) * mm, "end": v(-1.31, -24.1) * mm});
            skLineSegment(sketch, "E2981", {"start": v(-1.31, -24.1) * mm, "end": v(-1.3, -24.05) * mm});
            skLineSegment(sketch, "E2982", {"start": v(-1.3, -24.05) * mm, "end": v(-1.29, -24.01) * mm});
            skLineSegment(sketch, "E2983", {"start": v(-1.29, -24.01) * mm, "end": v(-1.27, -23.97) * mm});
            skLineSegment(sketch, "E2984", {"start": v(-1.27, -23.97) * mm, "end": v(-1.26, -23.93) * mm});
            skLineSegment(sketch, "E2985", {"start": v(-1.26, -23.93) * mm, "end": v(-1.25, -23.89) * mm});
            skLineSegment(sketch, "E2986", {"start": v(-1.25, -23.89) * mm, "end": v(-1.25, -23.85) * mm});
            skLineSegment(sketch, "E2987", {"start": v(-1.25, -23.85) * mm, "end": v(-1.24, -23.82) * mm});
            skLineSegment(sketch, "E2988", {"start": v(-1.24, -23.82) * mm, "end": v(-1.23, -23.78) * mm});
            skLineSegment(sketch, "E2989", {"start": v(-1.23, -23.78) * mm, "end": v(-1.22, -23.75) * mm});
            skLineSegment(sketch, "E2990", {"start": v(-1.22, -23.75) * mm, "end": v(-1.22, -23.72) * mm});
            skLineSegment(sketch, "E2991", {"start": v(-1.22, -23.72) * mm, "end": v(-1.21, -23.69) * mm});
            skLineSegment(sketch, "E2992", {"start": v(-1.21, -23.69) * mm, "end": v(-1.2, -23.66) * mm});
            skLineSegment(sketch, "E2993", {"start": v(-1.2, -23.66) * mm, "end": v(-1.2, -23.64) * mm});
            skLineSegment(sketch, "E2994", {"start": v(-1.2, -23.64) * mm, "end": v(-1.2, -23.61) * mm});
            skLineSegment(sketch, "E2995", {"start": v(-1.2, -23.61) * mm, "end": v(-1.2, -23.6) * mm});
            skLineSegment(sketch, "E2996", {"start": v(-1.2, -23.6) * mm, "end": v(-1.2, -23.57) * mm});
            skLineSegment(sketch, "E2997", {"start": v(-1.2, -23.57) * mm, "end": v(-1.19, -23.55) * mm});
            skLineSegment(sketch, "E2998", {"start": v(-1.19, -23.55) * mm, "end": v(-1.18, -23.53) * mm});
            skLineSegment(sketch, "E2999", {"start": v(-1.18, -23.53) * mm, "end": v(0, -23.56) * mm});
            skLineSegment(sketch, "E3000", {"start": v(0, -23.56) * mm, "end": v(0, -23.58) * mm});
            skLineSegment(sketch, "E3001", {"start": v(0, -23.58) * mm, "end": v(0, -23.6) * mm});
            skLineSegment(sketch, "E3002", {"start": v(0, -23.6) * mm, "end": v(0, -23.62) * mm});
            skLineSegment(sketch, "E3003", {"start": v(0, -23.62) * mm, "end": v(0.01, -23.64) * mm});
            skLineSegment(sketch, "E3004", {"start": v(0.01, -23.64) * mm, "end": v(0.01, -23.67) * mm});
            skLineSegment(sketch, "E3005", {"start": v(0.01, -23.67) * mm, "end": v(0.02, -23.7) * mm});
            skLineSegment(sketch, "E3006", {"start": v(0.02, -23.7) * mm, "end": v(0.02, -23.72) * mm});
            skLineSegment(sketch, "E3007", {"start": v(0.02, -23.72) * mm, "end": v(0.03, -23.75) * mm});
            skLineSegment(sketch, "E3008", {"start": v(0.03, -23.75) * mm, "end": v(0.03, -23.78) * mm});
            skLineSegment(sketch, "E3009", {"start": v(0.03, -23.78) * mm, "end": v(0.04, -23.81) * mm});
            skLineSegment(sketch, "E3010", {"start": v(0.04, -23.81) * mm, "end": v(0.04, -23.85) * mm});
            skLineSegment(sketch, "E3011", {"start": v(0.04, -23.85) * mm, "end": v(0.05, -23.88) * mm});
            skLineSegment(sketch, "E3012", {"start": v(0.05, -23.88) * mm, "end": v(0.06, -23.92) * mm});
            skLineSegment(sketch, "E3013", {"start": v(0.06, -23.92) * mm, "end": v(0.06, -23.96) * mm});
            skLineSegment(sketch, "E3014", {"start": v(0.06, -23.96) * mm, "end": v(0.07, -24) * mm});
            skLineSegment(sketch, "E3015", {"start": v(0.07, -24) * mm, "end": v(0.08, -24.04) * mm});
            skLineSegment(sketch, "E3016", {"start": v(0.08, -24.04) * mm, "end": v(0.1, -24.09) * mm});
            skLineSegment(sketch, "E3017", {"start": v(0.1, -24.09) * mm, "end": v(0.1, -24.14) * mm});
            skLineSegment(sketch, "E3018", {"start": v(0.1, -24.14) * mm, "end": v(0.11, -24.18) * mm});
            skLineSegment(sketch, "E3019", {"start": v(0.11, -24.18) * mm, "end": v(0.13, -24.23) * mm});
            skLineSegment(sketch, "E3020", {"start": v(0.13, -24.23) * mm, "end": v(0.14, -24.28) * mm});
            skLineSegment(sketch, "E3021", {"start": v(0.14, -24.28) * mm, "end": v(0.15, -24.34) * mm});
            skLineSegment(sketch, "E3022", {"start": v(0.15, -24.34) * mm, "end": v(0.17, -24.4) * mm});
            skLineSegment(sketch, "E3023", {"start": v(0.17, -24.4) * mm, "end": v(0.19, -24.45) * mm});
            skLineSegment(sketch, "E3024", {"start": v(0.19, -24.45) * mm, "end": v(0.2, -24.5) * mm});
            skLineSegment(sketch, "E3025", {"start": v(0.2, -24.5) * mm, "end": v(0.22, -24.56) * mm});
            skLineSegment(sketch, "E3026", {"start": v(0.22, -24.56) * mm, "end": v(0.24, -24.62) * mm});
            skLineSegment(sketch, "E3027", {"start": v(0.24, -24.62) * mm, "end": v(0.26, -24.69) * mm});
            skLineSegment(sketch, "E3028", {"start": v(0.26, -24.69) * mm, "end": v(0.28, -24.75) * mm});
            skLineSegment(sketch, "E3029", {"start": v(0.28, -24.75) * mm, "end": v(0.3, -24.81) * mm});
            skLineSegment(sketch, "E3030", {"start": v(0.3, -24.81) * mm, "end": v(0.33, -24.88) * mm});
            skLineSegment(sketch, "E3031", {"start": v(0.33, -24.88) * mm, "end": v(0.35, -24.95) * mm});
            skLineSegment(sketch, "E3032", {"start": v(0.35, -24.95) * mm, "end": v(0.38, -25.02) * mm});
            skLineSegment(sketch, "E3033", {"start": v(0.38, -25.02) * mm, "end": v(0.4, -25.09) * mm});
            skLineSegment(sketch, "E3034", {"start": v(0.4, -25.09) * mm, "end": v(0.44, -25.16) * mm});
            skLineSegment(sketch, "E3035", {"start": v(0.44, -25.16) * mm, "end": v(0.47, -25.23) * mm});
            skLineSegment(sketch, "E3036", {"start": v(0.47, -25.23) * mm, "end": v(0.5, -25.3) * mm});
            skLineSegment(sketch, "E3037", {"start": v(0.5, -25.3) * mm, "end": v(0.53, -25.39) * mm});
            skLineSegment(sketch, "E3038", {"start": v(0.53, -25.39) * mm, "end": v(0.57, -25.46) * mm});
            skLineSegment(sketch, "E3039", {"start": v(0.57, -25.46) * mm, "end": v(0.6, -25.54) * mm});
            skLineSegment(sketch, "E3040", {"start": v(0.6, -25.54) * mm, "end": v(0.64, -25.62) * mm});
            skLineSegment(sketch, "E3041", {"start": v(0.64, -25.62) * mm, "end": v(0.68, -25.7) * mm});
            skLineSegment(sketch, "E3042", {"start": v(0.68, -25.7) * mm, "end": v(0.72, -25.79) * mm});
            skLineSegment(sketch, "E3043", {"start": v(0.72, -25.79) * mm, "end": v(0.76, -25.87) * mm});
            skLineSegment(sketch, "E3044", {"start": v(0.76, -25.87) * mm, "end": v(0.8, -25.96) * mm});
            skLineSegment(sketch, "E3045", {"start": v(0.8, -25.96) * mm, "end": v(0.85, -26.04) * mm});
            skLineSegment(sketch, "E3046", {"start": v(0.85, -26.04) * mm, "end": v(0.9, -26.13) * mm});
            skLineSegment(sketch, "E3047", {"start": v(0.9, -26.13) * mm, "end": v(0.94, -26.22) * mm});
            skLineSegment(sketch, "E3048", {"start": v(0.94, -26.22) * mm, "end": v(0.99, -26.23) * mm});
            skLineSegment(sketch, "E3049", {"start": v(0.99, -26.23) * mm, "end": v(1.82, -26.19) * mm});
            skLineSegment(sketch, "E3050", {"start": v(1.82, -26.19) * mm, "end": v(1.86, -26.17) * mm});
            skLineSegment(sketch, "E3051", {"start": v(1.86, -26.17) * mm, "end": v(1.9, -26.08) * mm});
            skLineSegment(sketch, "E3052", {"start": v(1.9, -26.08) * mm, "end": v(1.94, -25.99) * mm});
            skLineSegment(sketch, "E3053", {"start": v(1.94, -25.99) * mm, "end": v(1.97, -25.9) * mm});
            skLineSegment(sketch, "E3054", {"start": v(1.97, -25.9) * mm, "end": v(2, -25.8) * mm});
            skLineSegment(sketch, "E3055", {"start": v(2, -25.8) * mm, "end": v(2.04, -25.72) * mm});
            skLineSegment(sketch, "E3056", {"start": v(2.04, -25.72) * mm, "end": v(2.07, -25.63) * mm});
            skLineSegment(sketch, "E3057", {"start": v(2.07, -25.63) * mm, "end": v(2.1, -25.55) * mm});
            skLineSegment(sketch, "E3058", {"start": v(2.1, -25.55) * mm, "end": v(2.13, -25.46) * mm});
            skLineSegment(sketch, "E3059", {"start": v(2.13, -25.46) * mm, "end": v(2.16, -25.38) * mm});
            skLineSegment(sketch, "E3060", {"start": v(2.16, -25.38) * mm, "end": v(2.18, -25.3) * mm});
            skLineSegment(sketch, "E3061", {"start": v(2.18, -25.3) * mm, "end": v(2.2, -25.22) * mm});
            skLineSegment(sketch, "E3062", {"start": v(2.2, -25.22) * mm, "end": v(2.23, -25.14) * mm});
            skLineSegment(sketch, "E3063", {"start": v(2.23, -25.14) * mm, "end": v(2.25, -25.06) * mm});
            skLineSegment(sketch, "E3064", {"start": v(2.25, -25.06) * mm, "end": v(2.27, -24.99) * mm});
            skLineSegment(sketch, "E3065", {"start": v(2.27, -24.99) * mm, "end": v(2.3, -24.92) * mm});
            skLineSegment(sketch, "E3066", {"start": v(2.3, -24.92) * mm, "end": v(2.31, -24.84) * mm});
            skLineSegment(sketch, "E3067", {"start": v(2.31, -24.84) * mm, "end": v(2.33, -24.77) * mm});
            skLineSegment(sketch, "E3068", {"start": v(2.33, -24.77) * mm, "end": v(2.34, -24.7) * mm});
            skLineSegment(sketch, "E3069", {"start": v(2.34, -24.7) * mm, "end": v(2.36, -24.64) * mm});
            skLineSegment(sketch, "E3070", {"start": v(2.36, -24.64) * mm, "end": v(2.38, -24.57) * mm});
            skLineSegment(sketch, "E3071", {"start": v(2.38, -24.57) * mm, "end": v(2.39, -24.5) * mm});
            skLineSegment(sketch, "E3072", {"start": v(2.39, -24.5) * mm, "end": v(2.4, -24.45) * mm});
            skLineSegment(sketch, "E3073", {"start": v(2.4, -24.45) * mm, "end": v(2.41, -24.39) * mm});
            skLineSegment(sketch, "E3074", {"start": v(2.41, -24.39) * mm, "end": v(2.42, -24.33) * mm});
            skLineSegment(sketch, "E3075", {"start": v(2.42, -24.33) * mm, "end": v(2.43, -24.27) * mm});
            skLineSegment(sketch, "E3076", {"start": v(2.43, -24.27) * mm, "end": v(2.44, -24.21) * mm});
            skLineSegment(sketch, "E3077", {"start": v(2.44, -24.21) * mm, "end": v(2.45, -24.16) * mm});
            skLineSegment(sketch, "E3078", {"start": v(2.45, -24.16) * mm, "end": v(2.46, -24.1) * mm});
            skLineSegment(sketch, "E3079", {"start": v(2.46, -24.1) * mm, "end": v(2.47, -24.06) * mm});
            skLineSegment(sketch, "E3080", {"start": v(2.47, -24.06) * mm, "end": v(2.47, -24) * mm});
            skLineSegment(sketch, "E3081", {"start": v(2.47, -24) * mm, "end": v(2.48, -23.96) * mm});
            skLineSegment(sketch, "E3082", {"start": v(2.48, -23.96) * mm, "end": v(2.49, -23.92) * mm});
            skLineSegment(sketch, "E3083", {"start": v(2.49, -23.92) * mm, "end": v(2.5, -23.87) * mm});
            skLineSegment(sketch, "E3084", {"start": v(2.5, -23.87) * mm, "end": v(2.5, -23.83) * mm});
            skLineSegment(sketch, "E3085", {"start": v(2.5, -23.83) * mm, "end": v(2.5, -23.8) * mm});
            skLineSegment(sketch, "E3086", {"start": v(2.5, -23.8) * mm, "end": v(2.5, -23.75) * mm});
            skLineSegment(sketch, "E3087", {"start": v(2.5, -23.75) * mm, "end": v(2.5, -23.72) * mm});
            skLineSegment(sketch, "E3088", {"start": v(2.5, -23.72) * mm, "end": v(2.5, -23.68) * mm});
            skLineSegment(sketch, "E3089", {"start": v(2.5, -23.68) * mm, "end": v(2.5, -23.65) * mm});
            skLineSegment(sketch, "E3090", {"start": v(2.5, -23.65) * mm, "end": v(2.5, -23.62) * mm});
            skLineSegment(sketch, "E3091", {"start": v(2.5, -23.62) * mm, "end": v(2.51, -23.59) * mm});
            skLineSegment(sketch, "E3092", {"start": v(2.51, -23.59) * mm, "end": v(2.51, -23.56) * mm});
            skLineSegment(sketch, "E3093", {"start": v(2.51, -23.56) * mm, "end": v(2.51, -23.53) * mm});
            skLineSegment(sketch, "E3094", {"start": v(2.51, -23.53) * mm, "end": v(2.51, -23.5) * mm});
            skLineSegment(sketch, "E3095", {"start": v(2.51, -23.5) * mm, "end": v(2.51, -23.49) * mm});
            skLineSegment(sketch, "E3096", {"start": v(2.51, -23.49) * mm, "end": v(2.51, -23.47) * mm});
            skLineSegment(sketch, "E3097", {"start": v(2.51, -23.47) * mm, "end": v(2.51, -23.45) * mm});
            skLineSegment(sketch, "E3098", {"start": v(2.51, -23.45) * mm, "end": v(2.51, -23.43) * mm});
            skLineSegment(sketch, "E3099", {"start": v(2.51, -23.43) * mm, "end": v(3.69, -23.27) * mm});
            skLineSegment(sketch, "E3100", {"start": v(3.69, -23.27) * mm, "end": v(3.7, -23.3) * mm});
            skLineSegment(sketch, "E3101", {"start": v(3.7, -23.3) * mm, "end": v(3.7, -23.3) * mm});
            skLineSegment(sketch, "E3102", {"start": v(3.7, -23.3) * mm, "end": v(3.7, -23.33) * mm});
            skLineSegment(sketch, "E3103", {"start": v(3.7, -23.33) * mm, "end": v(3.7, -23.35) * mm});
            skLineSegment(sketch, "E3104", {"start": v(3.7, -23.35) * mm, "end": v(3.72, -23.37) * mm});
            skLineSegment(sketch, "E3105", {"start": v(3.72, -23.37) * mm, "end": v(3.72, -23.4) * mm});
            skLineSegment(sketch, "E3106", {"start": v(3.72, -23.4) * mm, "end": v(3.73, -23.42) * mm});
            skLineSegment(sketch, "E3107", {"start": v(3.73, -23.42) * mm, "end": v(3.74, -23.45) * mm});
            skLineSegment(sketch, "E3108", {"start": v(3.74, -23.45) * mm, "end": v(3.75, -23.48) * mm});
            skLineSegment(sketch, "E3109", {"start": v(3.75, -23.48) * mm, "end": v(3.76, -23.51) * mm});
            skLineSegment(sketch, "E3110", {"start": v(3.76, -23.51) * mm, "end": v(3.77, -23.55) * mm});
            skLineSegment(sketch, "E3111", {"start": v(3.77, -23.55) * mm, "end": v(3.78, -23.58) * mm});
            skLineSegment(sketch, "E3112", {"start": v(3.78, -23.58) * mm, "end": v(3.8, -23.62) * mm});
            skLineSegment(sketch, "E3113", {"start": v(3.8, -23.62) * mm, "end": v(3.81, -23.66) * mm});
            skLineSegment(sketch, "E3114", {"start": v(3.81, -23.66) * mm, "end": v(3.83, -23.7) * mm});
            skLineSegment(sketch, "E3115", {"start": v(3.83, -23.7) * mm, "end": v(3.84, -23.74) * mm});
            skLineSegment(sketch, "E3116", {"start": v(3.84, -23.74) * mm, "end": v(3.86, -23.78) * mm});
            skLineSegment(sketch, "E3117", {"start": v(3.86, -23.78) * mm, "end": v(3.88, -23.82) * mm});
            skLineSegment(sketch, "E3118", {"start": v(3.88, -23.82) * mm, "end": v(3.9, -23.87) * mm});
            skLineSegment(sketch, "E3119", {"start": v(3.9, -23.87) * mm, "end": v(3.92, -23.91) * mm});
            skLineSegment(sketch, "E3120", {"start": v(3.92, -23.91) * mm, "end": v(3.94, -23.96) * mm});
            skLineSegment(sketch, "E3121", {"start": v(3.94, -23.96) * mm, "end": v(3.96, -24.01) * mm});
            skLineSegment(sketch, "E3122", {"start": v(3.96, -24.01) * mm, "end": v(3.98, -24.06) * mm});
            skLineSegment(sketch, "E3123", {"start": v(3.98, -24.06) * mm, "end": v(4, -24.12) * mm});
            skLineSegment(sketch, "E3124", {"start": v(4, -24.12) * mm, "end": v(4.03, -24.17) * mm});
            skLineSegment(sketch, "E3125", {"start": v(4.03, -24.17) * mm, "end": v(4.06, -24.23) * mm});
            skLineSegment(sketch, "E3126", {"start": v(4.06, -24.23) * mm, "end": v(4.09, -24.28) * mm});
            skLineSegment(sketch, "E3127", {"start": v(4.09, -24.28) * mm, "end": v(4.12, -24.34) * mm});
            skLineSegment(sketch, "E3128", {"start": v(4.12, -24.34) * mm, "end": v(4.15, -24.4) * mm});
            skLineSegment(sketch, "E3129", {"start": v(4.15, -24.4) * mm, "end": v(4.18, -24.46) * mm});
            skLineSegment(sketch, "E3130", {"start": v(4.18, -24.46) * mm, "end": v(4.22, -24.52) * mm});
            skLineSegment(sketch, "E3131", {"start": v(4.22, -24.52) * mm, "end": v(4.25, -24.59) * mm});
            skLineSegment(sketch, "E3132", {"start": v(4.25, -24.59) * mm, "end": v(4.29, -24.65) * mm});
            skLineSegment(sketch, "E3133", {"start": v(4.29, -24.65) * mm, "end": v(4.33, -24.72) * mm});
            skLineSegment(sketch, "E3134", {"start": v(4.33, -24.72) * mm, "end": v(4.37, -24.78) * mm});
            skLineSegment(sketch, "E3135", {"start": v(4.37, -24.78) * mm, "end": v(4.4, -24.85) * mm});
            skLineSegment(sketch, "E3136", {"start": v(4.4, -24.85) * mm, "end": v(4.45, -24.92) * mm});
            skLineSegment(sketch, "E3137", {"start": v(4.45, -24.92) * mm, "end": v(4.5, -25) * mm});
            skLineSegment(sketch, "E3138", {"start": v(4.5, -25) * mm, "end": v(4.54, -25.06) * mm});
            skLineSegment(sketch, "E3139", {"start": v(4.54, -25.06) * mm, "end": v(4.59, -25.13) * mm});
            skLineSegment(sketch, "E3140", {"start": v(4.59, -25.13) * mm, "end": v(4.64, -25.2) * mm});
            skLineSegment(sketch, "E3141", {"start": v(4.64, -25.2) * mm, "end": v(4.69, -25.28) * mm});
            skLineSegment(sketch, "E3142", {"start": v(4.69, -25.28) * mm, "end": v(4.74, -25.36) * mm});
            skLineSegment(sketch, "E3143", {"start": v(4.74, -25.36) * mm, "end": v(4.8, -25.44) * mm});
            skLineSegment(sketch, "E3144", {"start": v(4.8, -25.44) * mm, "end": v(4.85, -25.51) * mm});
            skLineSegment(sketch, "E3145", {"start": v(4.85, -25.51) * mm, "end": v(4.9, -25.6) * mm});
            skLineSegment(sketch, "E3146", {"start": v(4.9, -25.6) * mm, "end": v(4.97, -25.67) * mm});
            skLineSegment(sketch, "E3147", {"start": v(4.97, -25.67) * mm, "end": v(5.03, -25.75) * mm});
            skLineSegment(sketch, "E3148", {"start": v(5.03, -25.75) * mm, "end": v(5.08, -25.75) * mm});
            skLineSegment(sketch, "E3149", {"start": v(5.08, -25.75) * mm, "end": v(5.9, -25.58) * mm});
            skLineSegment(sketch, "E3150", {"start": v(5.9, -25.58) * mm, "end": v(5.93, -25.56) * mm});
            skLineSegment(sketch, "E3151", {"start": v(5.93, -25.56) * mm, "end": v(5.96, -25.46) * mm});
            skLineSegment(sketch, "E3152", {"start": v(5.96, -25.46) * mm, "end": v(5.98, -25.36) * mm});
            skLineSegment(sketch, "E3153", {"start": v(5.98, -25.36) * mm, "end": v(6, -25.27) * mm});
            skLineSegment(sketch, "E3154", {"start": v(6, -25.27) * mm, "end": v(6.02, -25.17) * mm});
            skLineSegment(sketch, "E3155", {"start": v(6.02, -25.17) * mm, "end": v(6.04, -25.08) * mm});
            skLineSegment(sketch, "E3156", {"start": v(6.04, -25.08) * mm, "end": v(6.05, -25) * mm});
            skLineSegment(sketch, "E3157", {"start": v(6.05, -25) * mm, "end": v(6.07, -24.9) * mm});
            skLineSegment(sketch, "E3158", {"start": v(6.07, -24.9) * mm, "end": v(6.09, -24.81) * mm});
            skLineSegment(sketch, "E3159", {"start": v(6.09, -24.81) * mm, "end": v(6.1, -24.73) * mm});
            skLineSegment(sketch, "E3160", {"start": v(6.1, -24.73) * mm, "end": v(6.11, -24.65) * mm});
            skLineSegment(sketch, "E3161", {"start": v(6.11, -24.65) * mm, "end": v(6.12, -24.56) * mm});
            skLineSegment(sketch, "E3162", {"start": v(6.12, -24.56) * mm, "end": v(6.13, -24.48) * mm});
            skLineSegment(sketch, "E3163", {"start": v(6.13, -24.48) * mm, "end": v(6.14, -24.4) * mm});
            skLineSegment(sketch, "E3164", {"start": v(6.14, -24.4) * mm, "end": v(6.15, -24.33) * mm});
            skLineSegment(sketch, "E3165", {"start": v(6.15, -24.33) * mm, "end": v(6.16, -24.25) * mm});
            skLineSegment(sketch, "E3166", {"start": v(6.16, -24.25) * mm, "end": v(6.17, -24.18) * mm});
            skLineSegment(sketch, "E3167", {"start": v(6.17, -24.18) * mm, "end": v(6.17, -24.1) * mm});
            skLineSegment(sketch, "E3168", {"start": v(6.17, -24.1) * mm, "end": v(6.18, -24.03) * mm});
            skLineSegment(sketch, "E3169", {"start": v(6.18, -24.03) * mm, "end": v(6.19, -23.96) * mm});
            skLineSegment(sketch, "E3170", {"start": v(6.19, -23.96) * mm, "end": v(6.19, -23.9) * mm});
            skLineSegment(sketch, "E3171", {"start": v(6.19, -23.9) * mm, "end": v(6.2, -23.83) * mm});
            skLineSegment(sketch, "E3172", {"start": v(6.2, -23.83) * mm, "end": v(6.2, -23.77) * mm});
            skLineSegment(sketch, "E3173", {"start": v(6.2, -23.77) * mm, "end": v(6.2, -23.7) * mm});
            skLineSegment(sketch, "E3174", {"start": v(6.2, -23.7) * mm, "end": v(6.2, -23.65) * mm});
            skLineSegment(sketch, "E3175", {"start": v(6.2, -23.65) * mm, "end": v(6.2, -23.59) * mm});
            skLineSegment(sketch, "E3176", {"start": v(6.2, -23.59) * mm, "end": v(6.2, -23.53) * mm});
            skLineSegment(sketch, "E3177", {"start": v(6.2, -23.53) * mm, "end": v(6.2, -23.48) * mm});
            skLineSegment(sketch, "E3178", {"start": v(6.2, -23.48) * mm, "end": v(6.2, -23.43) * mm});
            skLineSegment(sketch, "E3179", {"start": v(6.2, -23.43) * mm, "end": v(6.2, -23.37) * mm});
            skLineSegment(sketch, "E3180", {"start": v(6.2, -23.37) * mm, "end": v(6.2, -23.33) * mm});
            skLineSegment(sketch, "E3181", {"start": v(6.2, -23.33) * mm, "end": v(6.2, -23.28) * mm});
            skLineSegment(sketch, "E3182", {"start": v(6.2, -23.28) * mm, "end": v(6.2, -23.23) * mm});
            skLineSegment(sketch, "E3183", {"start": v(6.2, -23.23) * mm, "end": v(6.2, -23.19) * mm});
            skLineSegment(sketch, "E3184", {"start": v(6.2, -23.19) * mm, "end": v(6.2, -23.15) * mm});
            skLineSegment(sketch, "E3185", {"start": v(6.2, -23.15) * mm, "end": v(6.19, -23.1) * mm});
            skLineSegment(sketch, "E3186", {"start": v(6.19, -23.1) * mm, "end": v(6.19, -23.07) * mm});
            skLineSegment(sketch, "E3187", {"start": v(6.19, -23.07) * mm, "end": v(6.18, -23.03) * mm});
            skLineSegment(sketch, "E3188", {"start": v(6.18, -23.03) * mm, "end": v(6.18, -23) * mm});
            skLineSegment(sketch, "E3189", {"start": v(6.18, -23) * mm, "end": v(6.18, -22.96) * mm});
            skLineSegment(sketch, "E3190", {"start": v(6.18, -22.96) * mm, "end": v(6.17, -22.93) * mm});
            skLineSegment(sketch, "E3191", {"start": v(6.17, -22.93) * mm, "end": v(6.17, -22.9) * mm});
            skLineSegment(sketch, "E3192", {"start": v(6.17, -22.9) * mm, "end": v(6.17, -22.88) * mm});
            skLineSegment(sketch, "E3193", {"start": v(6.17, -22.88) * mm, "end": v(6.16, -22.85) * mm});
            skLineSegment(sketch, "E3194", {"start": v(6.16, -22.85) * mm, "end": v(6.16, -22.83) * mm});
            skLineSegment(sketch, "E3195", {"start": v(6.16, -22.83) * mm, "end": v(6.16, -22.8) * mm});
            skLineSegment(sketch, "E3196", {"start": v(6.16, -22.8) * mm, "end": v(6.15, -22.78) * mm});
            skLineSegment(sketch, "E3197", {"start": v(6.15, -22.78) * mm, "end": v(6.15, -22.77) * mm});
            skLineSegment(sketch, "E3198", {"start": v(6.15, -22.77) * mm, "end": v(6.15, -22.75) * mm});
            skLineSegment(sketch, "E3199", {"start": v(6.15, -22.75) * mm, "end": v(7.28, -22.4) * mm});
            skLineSegment(sketch, "E3200", {"start": v(7.28, -22.4) * mm, "end": v(7.3, -22.43) * mm});
            skLineSegment(sketch, "E3201", {"start": v(7.3, -22.43) * mm, "end": v(7.3, -22.44) * mm});
            skLineSegment(sketch, "E3202", {"start": v(7.3, -22.44) * mm, "end": v(7.3, -22.46) * mm});
            skLineSegment(sketch, "E3203", {"start": v(7.3, -22.46) * mm, "end": v(7.32, -22.48) * mm});
            skLineSegment(sketch, "E3204", {"start": v(7.32, -22.48) * mm, "end": v(7.33, -22.5) * mm});
            skLineSegment(sketch, "E3205", {"start": v(7.33, -22.5) * mm, "end": v(7.34, -22.53) * mm});
            skLineSegment(sketch, "E3206", {"start": v(7.34, -22.53) * mm, "end": v(7.35, -22.55) * mm});
            skLineSegment(sketch, "E3207", {"start": v(7.35, -22.55) * mm, "end": v(7.36, -22.58) * mm});
            skLineSegment(sketch, "E3208", {"start": v(7.36, -22.58) * mm, "end": v(7.38, -22.6) * mm});
            skLineSegment(sketch, "E3209", {"start": v(7.38, -22.6) * mm, "end": v(7.4, -22.64) * mm});
            skLineSegment(sketch, "E3210", {"start": v(7.4, -22.64) * mm, "end": v(7.4, -22.67) * mm});
            skLineSegment(sketch, "E3211", {"start": v(7.4, -22.67) * mm, "end": v(7.43, -22.7) * mm});
            skLineSegment(sketch, "E3212", {"start": v(7.43, -22.7) * mm, "end": v(7.44, -22.73) * mm});
            skLineSegment(sketch, "E3213", {"start": v(7.44, -22.73) * mm, "end": v(7.46, -22.77) * mm});
            skLineSegment(sketch, "E3214", {"start": v(7.46, -22.77) * mm, "end": v(7.49, -22.8) * mm});
            skLineSegment(sketch, "E3215", {"start": v(7.49, -22.8) * mm, "end": v(7.5, -22.84) * mm});
            skLineSegment(sketch, "E3216", {"start": v(7.5, -22.84) * mm, "end": v(7.53, -22.88) * mm});
            skLineSegment(sketch, "E3217", {"start": v(7.53, -22.88) * mm, "end": v(7.56, -22.92) * mm});
            skLineSegment(sketch, "E3218", {"start": v(7.56, -22.92) * mm, "end": v(7.58, -22.96) * mm});
            skLineSegment(sketch, "E3219", {"start": v(7.58, -22.96) * mm, "end": v(7.6, -23) * mm});
            skLineSegment(sketch, "E3220", {"start": v(7.6, -23) * mm, "end": v(7.64, -23.05) * mm});
            skLineSegment(sketch, "E3221", {"start": v(7.64, -23.05) * mm, "end": v(7.67, -23.1) * mm});
            skLineSegment(sketch, "E3222", {"start": v(7.67, -23.1) * mm, "end": v(7.7, -23.14) * mm});
            skLineSegment(sketch, "E3223", {"start": v(7.7, -23.14) * mm, "end": v(7.73, -23.2) * mm});
            skLineSegment(sketch, "E3224", {"start": v(7.73, -23.2) * mm, "end": v(7.76, -23.24) * mm});
            skLineSegment(sketch, "E3225", {"start": v(7.76, -23.24) * mm, "end": v(7.8, -23.3) * mm});
            skLineSegment(sketch, "E3226", {"start": v(7.8, -23.3) * mm, "end": v(7.84, -23.34) * mm});
            skLineSegment(sketch, "E3227", {"start": v(7.84, -23.34) * mm, "end": v(7.88, -23.4) * mm});
            skLineSegment(sketch, "E3228", {"start": v(7.88, -23.4) * mm, "end": v(7.92, -23.45) * mm});
            skLineSegment(sketch, "E3229", {"start": v(7.92, -23.45) * mm, "end": v(7.96, -23.5) * mm});
            skLineSegment(sketch, "E3230", {"start": v(7.96, -23.5) * mm, "end": v(8, -23.56) * mm});
            skLineSegment(sketch, "E3231", {"start": v(8, -23.56) * mm, "end": v(8.05, -23.62) * mm});
            skLineSegment(sketch, "E3232", {"start": v(8.05, -23.62) * mm, "end": v(8.1, -23.68) * mm});
            skLineSegment(sketch, "E3233", {"start": v(8.1, -23.68) * mm, "end": v(8.14, -23.73) * mm});
            skLineSegment(sketch, "E3234", {"start": v(8.14, -23.73) * mm, "end": v(8.2, -23.8) * mm});
            skLineSegment(sketch, "E3235", {"start": v(8.2, -23.8) * mm, "end": v(8.24, -23.86) * mm});
            skLineSegment(sketch, "E3236", {"start": v(8.24, -23.86) * mm, "end": v(8.3, -23.92) * mm});
            skLineSegment(sketch, "E3237", {"start": v(8.3, -23.92) * mm, "end": v(8.35, -23.98) * mm});
            skLineSegment(sketch, "E3238", {"start": v(8.35, -23.98) * mm, "end": v(8.4, -24.04) * mm});
            skLineSegment(sketch, "E3239", {"start": v(8.4, -24.04) * mm, "end": v(8.46, -24.1) * mm});
            skLineSegment(sketch, "E3240", {"start": v(8.46, -24.1) * mm, "end": v(8.53, -24.17) * mm});
            skLineSegment(sketch, "E3241", {"start": v(8.53, -24.17) * mm, "end": v(8.59, -24.24) * mm});
            skLineSegment(sketch, "E3242", {"start": v(8.59, -24.24) * mm, "end": v(8.65, -24.3) * mm});
            skLineSegment(sketch, "E3243", {"start": v(8.65, -24.3) * mm, "end": v(8.72, -24.37) * mm});
            skLineSegment(sketch, "E3244", {"start": v(8.72, -24.37) * mm, "end": v(8.78, -24.44) * mm});
            skLineSegment(sketch, "E3245", {"start": v(8.78, -24.44) * mm, "end": v(8.85, -24.5) * mm});
            skLineSegment(sketch, "E3246", {"start": v(8.85, -24.5) * mm, "end": v(8.92, -24.58) * mm});
            skLineSegment(sketch, "E3247", {"start": v(8.92, -24.58) * mm, "end": v(9, -24.65) * mm});
            skLineSegment(sketch, "E3248", {"start": v(9, -24.65) * mm, "end": v(9.04, -24.64) * mm});
            skLineSegment(sketch, "E3249", {"start": v(9.04, -24.64) * mm, "end": v(9.82, -24.34) * mm});
            skLineSegment(sketch, "E3250", {"start": v(9.82, -24.34) * mm, "end": v(9.86, -24.32) * mm});
            skLineSegment(sketch, "E3251", {"start": v(9.86, -24.32) * mm, "end": v(9.87, -24.21) * mm});
            skLineSegment(sketch, "E3252", {"start": v(9.87, -24.21) * mm, "end": v(9.87, -24.12) * mm});
            skLineSegment(sketch, "E3253", {"start": v(9.87, -24.12) * mm, "end": v(9.88, -24.02) * mm});
            skLineSegment(sketch, "E3254", {"start": v(9.88, -24.02) * mm, "end": v(9.88, -23.92) * mm});
            skLineSegment(sketch, "E3255", {"start": v(9.88, -23.92) * mm, "end": v(9.89, -23.83) * mm});
            skLineSegment(sketch, "E3256", {"start": v(9.89, -23.83) * mm, "end": v(9.89, -23.74) * mm});
            skLineSegment(sketch, "E3257", {"start": v(9.89, -23.74) * mm, "end": v(9.9, -23.65) * mm});
            skLineSegment(sketch, "E3258", {"start": v(9.9, -23.65) * mm, "end": v(9.9, -23.56) * mm});
            skLineSegment(sketch, "E3259", {"start": v(9.9, -23.56) * mm, "end": v(9.9, -23.47) * mm});
            skLineSegment(sketch, "E3260", {"start": v(9.9, -23.47) * mm, "end": v(9.9, -23.39) * mm});
            skLineSegment(sketch, "E3261", {"start": v(9.9, -23.39) * mm, "end": v(9.9, -23.3) * mm});
            skLineSegment(sketch, "E3262", {"start": v(9.9, -23.3) * mm, "end": v(9.89, -23.22) * mm});
            skLineSegment(sketch, "E3263", {"start": v(9.89, -23.22) * mm, "end": v(9.89, -23.14) * mm});
            skLineSegment(sketch, "E3264", {"start": v(9.89, -23.14) * mm, "end": v(9.88, -23.06) * mm});
            skLineSegment(sketch, "E3265", {"start": v(9.88, -23.06) * mm, "end": v(9.88, -22.99) * mm});
            skLineSegment(sketch, "E3266", {"start": v(9.88, -22.99) * mm, "end": v(9.87, -22.91) * mm});
            skLineSegment(sketch, "E3267", {"start": v(9.87, -22.91) * mm, "end": v(9.87, -22.84) * mm});
            skLineSegment(sketch, "E3268", {"start": v(9.87, -22.84) * mm, "end": v(9.86, -22.77) * mm});
            skLineSegment(sketch, "E3269", {"start": v(9.86, -22.77) * mm, "end": v(9.86, -22.7) * mm});
            skLineSegment(sketch, "E3270", {"start": v(9.86, -22.7) * mm, "end": v(9.85, -22.64) * mm});
            skLineSegment(sketch, "E3271", {"start": v(9.85, -22.64) * mm, "end": v(9.85, -22.57) * mm});
            skLineSegment(sketch, "E3272", {"start": v(9.85, -22.57) * mm, "end": v(9.84, -22.5) * mm});
            skLineSegment(sketch, "E3273", {"start": v(9.84, -22.5) * mm, "end": v(9.83, -22.45) * mm});
            skLineSegment(sketch, "E3274", {"start": v(9.83, -22.45) * mm, "end": v(9.82, -22.39) * mm});
            skLineSegment(sketch, "E3275", {"start": v(9.82, -22.39) * mm, "end": v(9.82, -22.33) * mm});
            skLineSegment(sketch, "E3276", {"start": v(9.82, -22.33) * mm, "end": v(9.8, -22.27) * mm});
            skLineSegment(sketch, "E3277", {"start": v(9.8, -22.27) * mm, "end": v(9.8, -22.22) * mm});
            skLineSegment(sketch, "E3278", {"start": v(9.8, -22.22) * mm, "end": v(9.79, -22.17) * mm});
            skLineSegment(sketch, "E3279", {"start": v(9.79, -22.17) * mm, "end": v(9.78, -22.12) * mm});
            skLineSegment(sketch, "E3280", {"start": v(9.78, -22.12) * mm, "end": v(9.77, -22.07) * mm});
            skLineSegment(sketch, "E3281", {"start": v(9.77, -22.07) * mm, "end": v(9.76, -22.02) * mm});
            skLineSegment(sketch, "E3282", {"start": v(9.76, -22.02) * mm, "end": v(9.75, -21.98) * mm});
            skLineSegment(sketch, "E3283", {"start": v(9.75, -21.98) * mm, "end": v(9.75, -21.93) * mm});
            skLineSegment(sketch, "E3284", {"start": v(9.75, -21.93) * mm, "end": v(9.74, -21.9) * mm});
            skLineSegment(sketch, "E3285", {"start": v(9.74, -21.9) * mm, "end": v(9.73, -21.85) * mm});
            skLineSegment(sketch, "E3286", {"start": v(9.73, -21.85) * mm, "end": v(9.72, -21.82) * mm});
            skLineSegment(sketch, "E3287", {"start": v(9.72, -21.82) * mm, "end": v(9.7, -21.78) * mm});
            skLineSegment(sketch, "E3288", {"start": v(9.7, -21.78) * mm, "end": v(9.7, -21.75) * mm});
            skLineSegment(sketch, "E3289", {"start": v(9.7, -21.75) * mm, "end": v(9.7, -21.72) * mm});
            skLineSegment(sketch, "E3290", {"start": v(9.7, -21.72) * mm, "end": v(9.68, -21.69) * mm});
            skLineSegment(sketch, "E3291", {"start": v(9.68, -21.69) * mm, "end": v(9.68, -21.66) * mm});
            skLineSegment(sketch, "E3292", {"start": v(9.68, -21.66) * mm, "end": v(9.67, -21.63) * mm});
            skLineSegment(sketch, "E3293", {"start": v(9.67, -21.63) * mm, "end": v(9.66, -21.6) * mm});
            skLineSegment(sketch, "E3294", {"start": v(9.66, -21.6) * mm, "end": v(9.65, -21.58) * mm});
            skLineSegment(sketch, "E3295", {"start": v(9.65, -21.58) * mm, "end": v(9.65, -21.56) * mm});
            skLineSegment(sketch, "E3296", {"start": v(9.65, -21.56) * mm, "end": v(9.64, -21.54) * mm});
            skLineSegment(sketch, "E3297", {"start": v(9.64, -21.54) * mm, "end": v(9.63, -21.52) * mm});
            skLineSegment(sketch, "E3298", {"start": v(9.63, -21.52) * mm, "end": v(9.63, -21.5) * mm});
            skLineSegment(sketch, "E3299", {"start": v(9.63, -21.5) * mm, "end": v(10.7, -21) * mm});
            skLineSegment(sketch, "E3300", {"start": v(10.7, -21) * mm, "end": v(10.71, -21) * mm});
            skLineSegment(sketch, "E3301", {"start": v(10.71, -21) * mm, "end": v(10.72, -21.02) * mm});
            skLineSegment(sketch, "E3302", {"start": v(10.72, -21.02) * mm, "end": v(10.73, -21.04) * mm});
            skLineSegment(sketch, "E3303", {"start": v(10.73, -21.04) * mm, "end": v(10.74, -21.06) * mm});
            skLineSegment(sketch, "E3304", {"start": v(10.74, -21.06) * mm, "end": v(10.76, -21.08) * mm});
            skLineSegment(sketch, "E3305", {"start": v(10.76, -21.08) * mm, "end": v(10.77, -21.1) * mm});
            skLineSegment(sketch, "E3306", {"start": v(10.77, -21.1) * mm, "end": v(10.79, -21.13) * mm});
            skLineSegment(sketch, "E3307", {"start": v(10.79, -21.13) * mm, "end": v(10.8, -21.15) * mm});
            skLineSegment(sketch, "E3308", {"start": v(10.8, -21.15) * mm, "end": v(10.82, -21.17) * mm});
            skLineSegment(sketch, "E3309", {"start": v(10.82, -21.17) * mm, "end": v(10.84, -21.2) * mm});
            skLineSegment(sketch, "E3310", {"start": v(10.84, -21.2) * mm, "end": v(10.86, -21.23) * mm});
            skLineSegment(sketch, "E3311", {"start": v(10.86, -21.23) * mm, "end": v(10.89, -21.26) * mm});
            skLineSegment(sketch, "E3312", {"start": v(10.89, -21.26) * mm, "end": v(10.9, -21.29) * mm});
            skLineSegment(sketch, "E3313", {"start": v(10.9, -21.29) * mm, "end": v(10.93, -21.32) * mm});
            skLineSegment(sketch, "E3314", {"start": v(10.93, -21.32) * mm, "end": v(10.96, -21.35) * mm});
            skLineSegment(sketch, "E3315", {"start": v(10.96, -21.35) * mm, "end": v(10.99, -21.39) * mm});
            skLineSegment(sketch, "E3316", {"start": v(10.99, -21.39) * mm, "end": v(11.02, -21.42) * mm});
            skLineSegment(sketch, "E3317", {"start": v(11.02, -21.42) * mm, "end": v(11.05, -21.46) * mm});
            skLineSegment(sketch, "E3318", {"start": v(11.05, -21.46) * mm, "end": v(11.08, -21.5) * mm});
            skLineSegment(sketch, "E3319", {"start": v(11.08, -21.5) * mm, "end": v(11.11, -21.53) * mm});
            skLineSegment(sketch, "E3320", {"start": v(11.11, -21.53) * mm, "end": v(11.15, -21.57) * mm});
            skLineSegment(sketch, "E3321", {"start": v(11.15, -21.57) * mm, "end": v(11.19, -21.61) * mm});
            skLineSegment(sketch, "E3322", {"start": v(11.19, -21.61) * mm, "end": v(11.22, -21.66) * mm});
            skLineSegment(sketch, "E3323", {"start": v(11.22, -21.66) * mm, "end": v(11.26, -21.7) * mm});
            skLineSegment(sketch, "E3324", {"start": v(11.26, -21.7) * mm, "end": v(11.3, -21.74) * mm});
            skLineSegment(sketch, "E3325", {"start": v(11.3, -21.74) * mm, "end": v(11.35, -21.79) * mm});
            skLineSegment(sketch, "E3326", {"start": v(11.35, -21.79) * mm, "end": v(11.4, -21.83) * mm});
            skLineSegment(sketch, "E3327", {"start": v(11.4, -21.83) * mm, "end": v(11.44, -21.88) * mm});
            skLineSegment(sketch, "E3328", {"start": v(11.44, -21.88) * mm, "end": v(11.49, -21.92) * mm});
            skLineSegment(sketch, "E3329", {"start": v(11.49, -21.92) * mm, "end": v(11.54, -21.97) * mm});
            skLineSegment(sketch, "E3330", {"start": v(11.54, -21.97) * mm, "end": v(11.59, -22.02) * mm});
            skLineSegment(sketch, "E3331", {"start": v(11.59, -22.02) * mm, "end": v(11.64, -22.07) * mm});
            skLineSegment(sketch, "E3332", {"start": v(11.64, -22.07) * mm, "end": v(11.7, -22.12) * mm});
            skLineSegment(sketch, "E3333", {"start": v(11.7, -22.12) * mm, "end": v(11.75, -22.17) * mm});
            skLineSegment(sketch, "E3334", {"start": v(11.75, -22.17) * mm, "end": v(11.81, -22.22) * mm});
            skLineSegment(sketch, "E3335", {"start": v(11.81, -22.22) * mm, "end": v(11.87, -22.27) * mm});
            skLineSegment(sketch, "E3336", {"start": v(11.87, -22.27) * mm, "end": v(11.93, -22.32) * mm});
            skLineSegment(sketch, "E3337", {"start": v(11.93, -22.32) * mm, "end": v(12, -22.38) * mm});
            skLineSegment(sketch, "E3338", {"start": v(12, -22.38) * mm, "end": v(12.06, -22.43) * mm});
            skLineSegment(sketch, "E3339", {"start": v(12.06, -22.43) * mm, "end": v(12.13, -22.49) * mm});
            skLineSegment(sketch, "E3340", {"start": v(12.13, -22.49) * mm, "end": v(12.2, -22.54) * mm});
            skLineSegment(sketch, "E3341", {"start": v(12.2, -22.54) * mm, "end": v(12.27, -22.6) * mm});
            skLineSegment(sketch, "E3342", {"start": v(12.27, -22.6) * mm, "end": v(12.35, -22.65) * mm});
            skLineSegment(sketch, "E3343", {"start": v(12.35, -22.65) * mm, "end": v(12.42, -22.7) * mm});
            skLineSegment(sketch, "E3344", {"start": v(12.42, -22.7) * mm, "end": v(12.5, -22.76) * mm});
            skLineSegment(sketch, "E3345", {"start": v(12.5, -22.76) * mm, "end": v(12.58, -22.82) * mm});
            skLineSegment(sketch, "E3346", {"start": v(12.58, -22.82) * mm, "end": v(12.66, -22.88) * mm});
            skLineSegment(sketch, "E3347", {"start": v(12.66, -22.88) * mm, "end": v(12.74, -22.94) * mm});
            skLineSegment(sketch, "E3348", {"start": v(12.74, -22.94) * mm, "end": v(12.79, -22.92) * mm});
            skLineSegment(sketch, "E3349", {"start": v(12.79, -22.92) * mm, "end": v(13.5, -22.5) * mm});
            skLineSegment(sketch, "E3350", {"start": v(13.5, -22.5) * mm, "end": v(13.54, -22.47) * mm});
            skLineSegment(sketch, "E3351", {"start": v(13.54, -22.47) * mm, "end": v(13.53, -22.37) * mm});
            skLineSegment(sketch, "E3352", {"start": v(13.53, -22.37) * mm, "end": v(13.52, -22.27) * mm});
            skLineSegment(sketch, "E3353", {"start": v(13.52, -22.27) * mm, "end": v(13.51, -22.18) * mm});
            skLineSegment(sketch, "E3354", {"start": v(13.51, -22.18) * mm, "end": v(13.5, -22.08) * mm});
            skLineSegment(sketch, "E3355", {"start": v(13.5, -22.08) * mm, "end": v(13.5, -21.99) * mm});
            skLineSegment(sketch, "E3356", {"start": v(13.5, -21.99) * mm, "end": v(13.48, -21.9) * mm});
            skLineSegment(sketch, "E3357", {"start": v(13.48, -21.9) * mm, "end": v(13.47, -21.8) * mm});
            skLineSegment(sketch, "E3358", {"start": v(13.47, -21.8) * mm, "end": v(13.46, -21.72) * mm});
            skLineSegment(sketch, "E3359", {"start": v(13.46, -21.72) * mm, "end": v(13.44, -21.63) * mm});
            skLineSegment(sketch, "E3360", {"start": v(13.44, -21.63) * mm, "end": v(13.43, -21.55) * mm});
            skLineSegment(sketch, "E3361", {"start": v(13.43, -21.55) * mm, "end": v(13.41, -21.47) * mm});
            skLineSegment(sketch, "E3362", {"start": v(13.41, -21.47) * mm, "end": v(13.4, -21.39) * mm});
            skLineSegment(sketch, "E3363", {"start": v(13.4, -21.39) * mm, "end": v(13.38, -21.31) * mm});
            skLineSegment(sketch, "E3364", {"start": v(13.38, -21.31) * mm, "end": v(13.37, -21.23) * mm});
            skLineSegment(sketch, "E3365", {"start": v(13.37, -21.23) * mm, "end": v(13.35, -21.16) * mm});
            skLineSegment(sketch, "E3366", {"start": v(13.35, -21.16) * mm, "end": v(13.34, -21.09) * mm});
            skLineSegment(sketch, "E3367", {"start": v(13.34, -21.09) * mm, "end": v(13.32, -21.02) * mm});
            skLineSegment(sketch, "E3368", {"start": v(13.32, -21.02) * mm, "end": v(13.3, -20.95) * mm});
            skLineSegment(sketch, "E3369", {"start": v(13.3, -20.95) * mm, "end": v(13.29, -20.88) * mm});
            skLineSegment(sketch, "E3370", {"start": v(13.29, -20.88) * mm, "end": v(13.27, -20.82) * mm});
            skLineSegment(sketch, "E3371", {"start": v(13.27, -20.82) * mm, "end": v(13.25, -20.75) * mm});
            skLineSegment(sketch, "E3372", {"start": v(13.25, -20.75) * mm, "end": v(13.24, -20.7) * mm});
            skLineSegment(sketch, "E3373", {"start": v(13.24, -20.7) * mm, "end": v(13.22, -20.63) * mm});
            skLineSegment(sketch, "E3374", {"start": v(13.22, -20.63) * mm, "end": v(13.2, -20.57) * mm});
            skLineSegment(sketch, "E3375", {"start": v(13.2, -20.57) * mm, "end": v(13.19, -20.52) * mm});
            skLineSegment(sketch, "E3376", {"start": v(13.19, -20.52) * mm, "end": v(13.17, -20.46) * mm});
            skLineSegment(sketch, "E3377", {"start": v(13.17, -20.46) * mm, "end": v(13.15, -20.41) * mm});
            skLineSegment(sketch, "E3378", {"start": v(13.15, -20.41) * mm, "end": v(13.14, -20.36) * mm});
            skLineSegment(sketch, "E3379", {"start": v(13.14, -20.36) * mm, "end": v(13.12, -20.31) * mm});
            skLineSegment(sketch, "E3380", {"start": v(13.12, -20.31) * mm, "end": v(13.1, -20.27) * mm});
            skLineSegment(sketch, "E3381", {"start": v(13.1, -20.27) * mm, "end": v(13.09, -20.22) * mm});
            skLineSegment(sketch, "E3382", {"start": v(13.09, -20.22) * mm, "end": v(13.07, -20.18) * mm});
            skLineSegment(sketch, "E3383", {"start": v(13.07, -20.18) * mm, "end": v(13.06, -20.14) * mm});
            skLineSegment(sketch, "E3384", {"start": v(13.06, -20.14) * mm, "end": v(13.04, -20.1) * mm});
            skLineSegment(sketch, "E3385", {"start": v(13.04, -20.1) * mm, "end": v(13.03, -20.06) * mm});
            skLineSegment(sketch, "E3386", {"start": v(13.03, -20.06) * mm, "end": v(13.01, -20.03) * mm});
            skLineSegment(sketch, "E3387", {"start": v(13.01, -20.03) * mm, "end": v(13, -20) * mm});
            skLineSegment(sketch, "E3388", {"start": v(13, -20) * mm, "end": v(12.98, -19.96) * mm});
            skLineSegment(sketch, "E3389", {"start": v(12.98, -19.96) * mm, "end": v(12.97, -19.93) * mm});
            skLineSegment(sketch, "E3390", {"start": v(12.97, -19.93) * mm, "end": v(12.96, -19.9) * mm});
            skLineSegment(sketch, "E3391", {"start": v(12.96, -19.9) * mm, "end": v(12.94, -19.88) * mm});
            skLineSegment(sketch, "E3392", {"start": v(12.94, -19.88) * mm, "end": v(12.93, -19.85) * mm});
            skLineSegment(sketch, "E3393", {"start": v(12.93, -19.85) * mm, "end": v(12.92, -19.83) * mm});
            skLineSegment(sketch, "E3394", {"start": v(12.92, -19.83) * mm, "end": v(12.91, -19.8) * mm});
            skLineSegment(sketch, "E3395", {"start": v(12.91, -19.8) * mm, "end": v(12.9, -19.79) * mm});
            skLineSegment(sketch, "E3396", {"start": v(12.9, -19.79) * mm, "end": v(12.9, -19.77) * mm});
            skLineSegment(sketch, "E3397", {"start": v(12.9, -19.77) * mm, "end": v(12.88, -19.75) * mm});
            skLineSegment(sketch, "E3398", {"start": v(12.88, -19.75) * mm, "end": v(12.88, -19.73) * mm});
            skLineSegment(sketch, "E3399", {"start": v(12.88, -19.73) * mm, "end": v(13.85, -19.06) * mm});
            skLineSegment(sketch, "E3400", {"start": v(13.85, -19.06) * mm, "end": v(13.87, -19.07) * mm});
            skLineSegment(sketch, "E3401", {"start": v(13.87, -19.07) * mm, "end": v(13.88, -19.09) * mm});
            skLineSegment(sketch, "E3402", {"start": v(13.88, -19.09) * mm, "end": v(13.9, -19.1) * mm});
            skLineSegment(sketch, "E3403", {"start": v(13.9, -19.1) * mm, "end": v(13.9, -19.12) * mm});
            skLineSegment(sketch, "E3404", {"start": v(13.9, -19.12) * mm, "end": v(13.92, -19.14) * mm});
            skLineSegment(sketch, "E3405", {"start": v(13.92, -19.14) * mm, "end": v(13.94, -19.16) * mm});
            skLineSegment(sketch, "E3406", {"start": v(13.94, -19.16) * mm, "end": v(13.96, -19.18) * mm});
            skLineSegment(sketch, "E3407", {"start": v(13.96, -19.18) * mm, "end": v(13.98, -19.2) * mm});
            skLineSegment(sketch, "E3408", {"start": v(13.98, -19.2) * mm, "end": v(14, -19.22) * mm});
            skLineSegment(sketch, "E3409", {"start": v(14, -19.22) * mm, "end": v(14.03, -19.24) * mm});
            skLineSegment(sketch, "E3410", {"start": v(14.03, -19.24) * mm, "end": v(14.05, -19.27) * mm});
            skLineSegment(sketch, "E3411", {"start": v(14.05, -19.27) * mm, "end": v(14.08, -19.3) * mm});
            skLineSegment(sketch, "E3412", {"start": v(14.08, -19.3) * mm, "end": v(14.1, -19.32) * mm});
            skLineSegment(sketch, "E3413", {"start": v(14.1, -19.32) * mm, "end": v(14.13, -19.35) * mm});
            skLineSegment(sketch, "E3414", {"start": v(14.13, -19.35) * mm, "end": v(14.17, -19.38) * mm});
            skLineSegment(sketch, "E3415", {"start": v(14.17, -19.38) * mm, "end": v(14.2, -19.4) * mm});
            skLineSegment(sketch, "E3416", {"start": v(14.2, -19.4) * mm, "end": v(14.23, -19.44) * mm});
            skLineSegment(sketch, "E3417", {"start": v(14.23, -19.44) * mm, "end": v(14.27, -19.47) * mm});
            skLineSegment(sketch, "E3418", {"start": v(14.27, -19.47) * mm, "end": v(14.3, -19.5) * mm});
            skLineSegment(sketch, "E3419", {"start": v(14.3, -19.5) * mm, "end": v(14.35, -19.53) * mm});
            skLineSegment(sketch, "E3420", {"start": v(14.35, -19.53) * mm, "end": v(14.39, -19.56) * mm});
            skLineSegment(sketch, "E3421", {"start": v(14.39, -19.56) * mm, "end": v(14.43, -19.6) * mm});
            skLineSegment(sketch, "E3422", {"start": v(14.43, -19.6) * mm, "end": v(14.47, -19.63) * mm});
            skLineSegment(sketch, "E3423", {"start": v(14.47, -19.63) * mm, "end": v(14.52, -19.67) * mm});
            skLineSegment(sketch, "E3424", {"start": v(14.52, -19.67) * mm, "end": v(14.57, -19.7) * mm});
            skLineSegment(sketch, "E3425", {"start": v(14.57, -19.7) * mm, "end": v(14.62, -19.74) * mm});
            skLineSegment(sketch, "E3426", {"start": v(14.62, -19.74) * mm, "end": v(14.67, -19.78) * mm});
            skLineSegment(sketch, "E3427", {"start": v(14.67, -19.78) * mm, "end": v(14.72, -19.82) * mm});
            skLineSegment(sketch, "E3428", {"start": v(14.72, -19.82) * mm, "end": v(14.78, -19.86) * mm});
            skLineSegment(sketch, "E3429", {"start": v(14.78, -19.86) * mm, "end": v(14.83, -19.9) * mm});
            skLineSegment(sketch, "E3430", {"start": v(14.83, -19.9) * mm, "end": v(14.9, -19.94) * mm});
            skLineSegment(sketch, "E3431", {"start": v(14.9, -19.94) * mm, "end": v(14.95, -19.98) * mm});
            skLineSegment(sketch, "E3432", {"start": v(14.95, -19.98) * mm, "end": v(15.01, -20.02) * mm});
            skLineSegment(sketch, "E3433", {"start": v(15.01, -20.02) * mm, "end": v(15.08, -20.06) * mm});
            skLineSegment(sketch, "E3434", {"start": v(15.08, -20.06) * mm, "end": v(15.14, -20.1) * mm});
            skLineSegment(sketch, "E3435", {"start": v(15.14, -20.1) * mm, "end": v(15.21, -20.14) * mm});
            skLineSegment(sketch, "E3436", {"start": v(15.21, -20.14) * mm, "end": v(15.28, -20.18) * mm});
            skLineSegment(sketch, "E3437", {"start": v(15.28, -20.18) * mm, "end": v(15.35, -20.23) * mm});
            skLineSegment(sketch, "E3438", {"start": v(15.35, -20.23) * mm, "end": v(15.42, -20.27) * mm});
            skLineSegment(sketch, "E3439", {"start": v(15.42, -20.27) * mm, "end": v(15.5, -20.31) * mm});
            skLineSegment(sketch, "E3440", {"start": v(15.5, -20.31) * mm, "end": v(15.58, -20.35) * mm});
            skLineSegment(sketch, "E3441", {"start": v(15.58, -20.35) * mm, "end": v(15.66, -20.4) * mm});
            skLineSegment(sketch, "E3442", {"start": v(15.66, -20.4) * mm, "end": v(15.74, -20.44) * mm});
            skLineSegment(sketch, "E3443", {"start": v(15.74, -20.44) * mm, "end": v(15.82, -20.49) * mm});
            skLineSegment(sketch, "E3444", {"start": v(15.82, -20.49) * mm, "end": v(15.9, -20.53) * mm});
            skLineSegment(sketch, "E3445", {"start": v(15.9, -20.53) * mm, "end": v(16, -20.57) * mm});
            skLineSegment(sketch, "E3446", {"start": v(16, -20.57) * mm, "end": v(16.08, -20.62) * mm});
            skLineSegment(sketch, "E3447", {"start": v(16.08, -20.62) * mm, "end": v(16.17, -20.66) * mm});
            skLineSegment(sketch, "E3448", {"start": v(16.17, -20.66) * mm, "end": v(16.22, -20.64) * mm});
            skLineSegment(sketch, "E3449", {"start": v(16.22, -20.64) * mm, "end": v(16.86, -20.12) * mm});
            skLineSegment(sketch, "E3450", {"start": v(16.86, -20.12) * mm, "end": v(16.9, -20.08) * mm});
            skLineSegment(sketch, "E3451", {"start": v(16.9, -20.08) * mm, "end": v(16.87, -19.98) * mm});
            skLineSegment(sketch, "E3452", {"start": v(16.87, -19.98) * mm, "end": v(16.84, -19.88) * mm});
            skLineSegment(sketch, "E3453", {"start": v(16.84, -19.88) * mm, "end": v(16.82, -19.79) * mm});
            skLineSegment(sketch, "E3454", {"start": v(16.82, -19.79) * mm, "end": v(16.8, -19.7) * mm});
            skLineSegment(sketch, "E3455", {"start": v(16.8, -19.7) * mm, "end": v(16.77, -19.6) * mm});
            skLineSegment(sketch, "E3456", {"start": v(16.77, -19.6) * mm, "end": v(16.74, -19.52) * mm});
            skLineSegment(sketch, "E3457", {"start": v(16.74, -19.52) * mm, "end": v(16.71, -19.43) * mm});
            skLineSegment(sketch, "E3458", {"start": v(16.71, -19.43) * mm, "end": v(16.69, -19.35) * mm});
            skLineSegment(sketch, "E3459", {"start": v(16.69, -19.35) * mm, "end": v(16.66, -19.26) * mm});
            skLineSegment(sketch, "E3460", {"start": v(16.66, -19.26) * mm, "end": v(16.63, -19.18) * mm});
            skLineSegment(sketch, "E3461", {"start": v(16.63, -19.18) * mm, "end": v(16.6, -19.1) * mm});
            skLineSegment(sketch, "E3462", {"start": v(16.6, -19.1) * mm, "end": v(16.58, -19.03) * mm});
            skLineSegment(sketch, "E3463", {"start": v(16.58, -19.03) * mm, "end": v(16.55, -18.95) * mm});
            skLineSegment(sketch, "E3464", {"start": v(16.55, -18.95) * mm, "end": v(16.53, -18.88) * mm});
            skLineSegment(sketch, "E3465", {"start": v(16.53, -18.88) * mm, "end": v(16.5, -18.8) * mm});
            skLineSegment(sketch, "E3466", {"start": v(16.5, -18.8) * mm, "end": v(16.47, -18.74) * mm});
            skLineSegment(sketch, "E3467", {"start": v(16.47, -18.74) * mm, "end": v(16.44, -18.67) * mm});
            skLineSegment(sketch, "E3468", {"start": v(16.44, -18.67) * mm, "end": v(16.42, -18.6) * mm});
            skLineSegment(sketch, "E3469", {"start": v(16.42, -18.6) * mm, "end": v(16.4, -18.54) * mm});
            skLineSegment(sketch, "E3470", {"start": v(16.4, -18.54) * mm, "end": v(16.36, -18.48) * mm});
            skLineSegment(sketch, "E3471", {"start": v(16.36, -18.48) * mm, "end": v(16.34, -18.42) * mm});
            skLineSegment(sketch, "E3472", {"start": v(16.34, -18.42) * mm, "end": v(16.31, -18.37) * mm});
            skLineSegment(sketch, "E3473", {"start": v(16.31, -18.37) * mm, "end": v(16.29, -18.3) * mm});
            skLineSegment(sketch, "E3474", {"start": v(16.29, -18.3) * mm, "end": v(16.26, -18.26) * mm});
            skLineSegment(sketch, "E3475", {"start": v(16.26, -18.26) * mm, "end": v(16.23, -18.2) * mm});
            skLineSegment(sketch, "E3476", {"start": v(16.23, -18.2) * mm, "end": v(16.2, -18.15) * mm});
            skLineSegment(sketch, "E3477", {"start": v(16.2, -18.15) * mm, "end": v(16.19, -18.1) * mm});
            skLineSegment(sketch, "E3478", {"start": v(16.19, -18.1) * mm, "end": v(16.16, -18.06) * mm});
            skLineSegment(sketch, "E3479", {"start": v(16.16, -18.06) * mm, "end": v(16.14, -18.01) * mm});
            skLineSegment(sketch, "E3480", {"start": v(16.14, -18.01) * mm, "end": v(16.11, -17.97) * mm});
            skLineSegment(sketch, "E3481", {"start": v(16.11, -17.97) * mm, "end": v(16.1, -17.93) * mm});
            skLineSegment(sketch, "E3482", {"start": v(16.1, -17.93) * mm, "end": v(16.07, -17.89) * mm});
            skLineSegment(sketch, "E3483", {"start": v(16.07, -17.89) * mm, "end": v(16.05, -17.85) * mm});
            skLineSegment(sketch, "E3484", {"start": v(16.05, -17.85) * mm, "end": v(16.03, -17.81) * mm});
            skLineSegment(sketch, "E3485", {"start": v(16.03, -17.81) * mm, "end": v(16, -17.78) * mm});
            skLineSegment(sketch, "E3486", {"start": v(16, -17.78) * mm, "end": v(15.98, -17.75) * mm});
            skLineSegment(sketch, "E3487", {"start": v(15.98, -17.75) * mm, "end": v(15.97, -17.71) * mm});
            skLineSegment(sketch, "E3488", {"start": v(15.97, -17.71) * mm, "end": v(15.95, -17.69) * mm});
            skLineSegment(sketch, "E3489", {"start": v(15.95, -17.69) * mm, "end": v(15.93, -17.66) * mm});
            skLineSegment(sketch, "E3490", {"start": v(15.93, -17.66) * mm, "end": v(15.91, -17.63) * mm});
            skLineSegment(sketch, "E3491", {"start": v(15.91, -17.63) * mm, "end": v(15.9, -17.6) * mm});
            skLineSegment(sketch, "E3492", {"start": v(15.9, -17.6) * mm, "end": v(15.88, -17.58) * mm});
            skLineSegment(sketch, "E3493", {"start": v(15.88, -17.58) * mm, "end": v(15.86, -17.56) * mm});
            skLineSegment(sketch, "E3494", {"start": v(15.86, -17.56) * mm, "end": v(15.85, -17.54) * mm});
            skLineSegment(sketch, "E3495", {"start": v(15.85, -17.54) * mm, "end": v(15.84, -17.52) * mm});
            skLineSegment(sketch, "E3496", {"start": v(15.84, -17.52) * mm, "end": v(15.83, -17.5) * mm});
            skLineSegment(sketch, "E3497", {"start": v(15.83, -17.5) * mm, "end": v(15.81, -17.5) * mm});
            skLineSegment(sketch, "E3498", {"start": v(15.81, -17.5) * mm, "end": v(15.8, -17.48) * mm});
            skLineSegment(sketch, "E3499", {"start": v(15.8, -17.48) * mm, "end": v(16.66, -16.66) * mm});
            skLineSegment(sketch, "E3500", {"start": v(16.66, -16.66) * mm, "end": v(16.68, -16.67) * mm});
            skLineSegment(sketch, "E3501", {"start": v(16.68, -16.67) * mm, "end": v(16.7, -16.68) * mm});
            skLineSegment(sketch, "E3502", {"start": v(16.7, -16.68) * mm, "end": v(16.7, -16.7) * mm});
            skLineSegment(sketch, "E3503", {"start": v(16.7, -16.7) * mm, "end": v(16.73, -16.71) * mm});
            skLineSegment(sketch, "E3504", {"start": v(16.73, -16.71) * mm, "end": v(16.75, -16.73) * mm});
            skLineSegment(sketch, "E3505", {"start": v(16.75, -16.73) * mm, "end": v(16.77, -16.74) * mm});
            skLineSegment(sketch, "E3506", {"start": v(16.77, -16.74) * mm, "end": v(16.79, -16.76) * mm});
            skLineSegment(sketch, "E3507", {"start": v(16.79, -16.76) * mm, "end": v(16.81, -16.78) * mm});
            skLineSegment(sketch, "E3508", {"start": v(16.81, -16.78) * mm, "end": v(16.84, -16.8) * mm});
            skLineSegment(sketch, "E3509", {"start": v(16.84, -16.8) * mm, "end": v(16.86, -16.81) * mm});
            skLineSegment(sketch, "E3510", {"start": v(16.86, -16.81) * mm, "end": v(16.9, -16.83) * mm});
            skLineSegment(sketch, "E3511", {"start": v(16.9, -16.83) * mm, "end": v(16.92, -16.85) * mm});
            skLineSegment(sketch, "E3512", {"start": v(16.92, -16.85) * mm, "end": v(16.95, -16.88) * mm});
            skLineSegment(sketch, "E3513", {"start": v(16.95, -16.88) * mm, "end": v(16.99, -16.9) * mm});
            skLineSegment(sketch, "E3514", {"start": v(16.99, -16.9) * mm, "end": v(17.02, -16.92) * mm});
            skLineSegment(sketch, "E3515", {"start": v(17.02, -16.92) * mm, "end": v(17.06, -16.95) * mm});
            skLineSegment(sketch, "E3516", {"start": v(17.06, -16.95) * mm, "end": v(17.1, -16.97) * mm});
            skLineSegment(sketch, "E3517", {"start": v(17.1, -16.97) * mm, "end": v(17.14, -17) * mm});
            skLineSegment(sketch, "E3518", {"start": v(17.14, -17) * mm, "end": v(17.18, -17.02) * mm});
            skLineSegment(sketch, "E3519", {"start": v(17.18, -17.02) * mm, "end": v(17.22, -17.05) * mm});
            skLineSegment(sketch, "E3520", {"start": v(17.22, -17.05) * mm, "end": v(17.27, -17.07) * mm});
            skLineSegment(sketch, "E3521", {"start": v(17.27, -17.07) * mm, "end": v(17.32, -17.1) * mm});
            skLineSegment(sketch, "E3522", {"start": v(17.32, -17.1) * mm, "end": v(17.37, -17.13) * mm});
            skLineSegment(sketch, "E3523", {"start": v(17.37, -17.13) * mm, "end": v(17.42, -17.16) * mm});
            skLineSegment(sketch, "E3524", {"start": v(17.42, -17.16) * mm, "end": v(17.47, -17.18) * mm});
            skLineSegment(sketch, "E3525", {"start": v(17.47, -17.18) * mm, "end": v(17.52, -17.21) * mm});
            skLineSegment(sketch, "E3526", {"start": v(17.52, -17.21) * mm, "end": v(17.58, -17.24) * mm});
            skLineSegment(sketch, "E3527", {"start": v(17.58, -17.24) * mm, "end": v(17.64, -17.27) * mm});
            skLineSegment(sketch, "E3528", {"start": v(17.64, -17.27) * mm, "end": v(17.7, -17.3) * mm});
            skLineSegment(sketch, "E3529", {"start": v(17.7, -17.3) * mm, "end": v(17.76, -17.33) * mm});
            skLineSegment(sketch, "E3530", {"start": v(17.76, -17.33) * mm, "end": v(17.83, -17.36) * mm});
            skLineSegment(sketch, "E3531", {"start": v(17.83, -17.36) * mm, "end": v(17.9, -17.4) * mm});
            skLineSegment(sketch, "E3532", {"start": v(17.9, -17.4) * mm, "end": v(17.96, -17.42) * mm});
            skLineSegment(sketch, "E3533", {"start": v(17.96, -17.42) * mm, "end": v(18.03, -17.45) * mm});
            skLineSegment(sketch, "E3534", {"start": v(18.03, -17.45) * mm, "end": v(18.1, -17.48) * mm});
            skLineSegment(sketch, "E3535", {"start": v(18.1, -17.48) * mm, "end": v(18.17, -17.51) * mm});
            skLineSegment(sketch, "E3536", {"start": v(18.17, -17.51) * mm, "end": v(18.25, -17.54) * mm});
            skLineSegment(sketch, "E3537", {"start": v(18.25, -17.54) * mm, "end": v(18.33, -17.57) * mm});
            skLineSegment(sketch, "E3538", {"start": v(18.33, -17.57) * mm, "end": v(18.4, -17.6) * mm});
            skLineSegment(sketch, "E3539", {"start": v(18.4, -17.6) * mm, "end": v(18.49, -17.64) * mm});
            skLineSegment(sketch, "E3540", {"start": v(18.49, -17.64) * mm, "end": v(18.57, -17.67) * mm});
            skLineSegment(sketch, "E3541", {"start": v(18.57, -17.67) * mm, "end": v(18.65, -17.7) * mm});
            skLineSegment(sketch, "E3542", {"start": v(18.65, -17.7) * mm, "end": v(18.74, -17.73) * mm});
            skLineSegment(sketch, "E3543", {"start": v(18.74, -17.73) * mm, "end": v(18.83, -17.76) * mm});
            skLineSegment(sketch, "E3544", {"start": v(18.83, -17.76) * mm, "end": v(18.92, -17.79) * mm});
            skLineSegment(sketch, "E3545", {"start": v(18.92, -17.79) * mm, "end": v(19.01, -17.82) * mm});
            skLineSegment(sketch, "E3546", {"start": v(19.01, -17.82) * mm, "end": v(19.1, -17.85) * mm});
            skLineSegment(sketch, "E3547", {"start": v(19.1, -17.85) * mm, "end": v(19.2, -17.88) * mm});
            skLineSegment(sketch, "E3548", {"start": v(19.2, -17.88) * mm, "end": v(19.25, -17.85) * mm});
            skLineSegment(sketch, "E3549", {"start": v(19.25, -17.85) * mm, "end": v(19.8, -17.23) * mm});
            skLineSegment(sketch, "E3550", {"start": v(19.8, -17.23) * mm, "end": v(19.82, -17.19) * mm});
            skLineSegment(sketch, "E3551", {"start": v(19.82, -17.19) * mm, "end": v(19.78, -17.1) * mm});
            skLineSegment(sketch, "E3552", {"start": v(19.78, -17.1) * mm, "end": v(19.75, -17) * mm});
            skLineSegment(sketch, "E3553", {"start": v(19.75, -17) * mm, "end": v(19.7, -16.92) * mm});
            skLineSegment(sketch, "E3554", {"start": v(19.7, -16.92) * mm, "end": v(19.67, -16.83) * mm});
            skLineSegment(sketch, "E3555", {"start": v(19.67, -16.83) * mm, "end": v(19.63, -16.74) * mm});
            skLineSegment(sketch, "E3556", {"start": v(19.63, -16.74) * mm, "end": v(19.59, -16.66) * mm});
            skLineSegment(sketch, "E3557", {"start": v(19.59, -16.66) * mm, "end": v(19.55, -16.58) * mm});
            skLineSegment(sketch, "E3558", {"start": v(19.55, -16.58) * mm, "end": v(19.5, -16.5) * mm});
            skLineSegment(sketch, "E3559", {"start": v(19.5, -16.5) * mm, "end": v(19.47, -16.42) * mm});
            skLineSegment(sketch, "E3560", {"start": v(19.47, -16.42) * mm, "end": v(19.43, -16.35) * mm});
            skLineSegment(sketch, "E3561", {"start": v(19.43, -16.35) * mm, "end": v(19.4, -16.27) * mm});
            skLineSegment(sketch, "E3562", {"start": v(19.4, -16.27) * mm, "end": v(19.35, -16.2) * mm});
            skLineSegment(sketch, "E3563", {"start": v(19.35, -16.2) * mm, "end": v(19.31, -16.13) * mm});
            skLineSegment(sketch, "E3564", {"start": v(19.31, -16.13) * mm, "end": v(19.28, -16.06) * mm});
            skLineSegment(sketch, "E3565", {"start": v(19.28, -16.06) * mm, "end": v(19.24, -16) * mm});
            skLineSegment(sketch, "E3566", {"start": v(19.24, -16) * mm, "end": v(19.2, -15.93) * mm});
            skLineSegment(sketch, "E3567", {"start": v(19.2, -15.93) * mm, "end": v(19.16, -15.87) * mm});
            skLineSegment(sketch, "E3568", {"start": v(19.16, -15.87) * mm, "end": v(19.13, -15.81) * mm});
            skLineSegment(sketch, "E3569", {"start": v(19.13, -15.81) * mm, "end": v(19.1, -15.75) * mm});
            skLineSegment(sketch, "E3570", {"start": v(19.1, -15.75) * mm, "end": v(19.05, -15.7) * mm});
            skLineSegment(sketch, "E3571", {"start": v(19.05, -15.7) * mm, "end": v(19.02, -15.64) * mm});
            skLineSegment(sketch, "E3572", {"start": v(19.02, -15.64) * mm, "end": v(18.98, -15.59) * mm});
            skLineSegment(sketch, "E3573", {"start": v(18.98, -15.59) * mm, "end": v(18.95, -15.54) * mm});
            skLineSegment(sketch, "E3574", {"start": v(18.95, -15.54) * mm, "end": v(18.92, -15.49) * mm});
            skLineSegment(sketch, "E3575", {"start": v(18.92, -15.49) * mm, "end": v(18.88, -15.44) * mm});
            skLineSegment(sketch, "E3576", {"start": v(18.88, -15.44) * mm, "end": v(18.85, -15.4) * mm});
            skLineSegment(sketch, "E3577", {"start": v(18.85, -15.4) * mm, "end": v(18.82, -15.35) * mm});
            skLineSegment(sketch, "E3578", {"start": v(18.82, -15.35) * mm, "end": v(18.79, -15.3) * mm});
            skLineSegment(sketch, "E3579", {"start": v(18.79, -15.3) * mm, "end": v(18.76, -15.27) * mm});
            skLineSegment(sketch, "E3580", {"start": v(18.76, -15.27) * mm, "end": v(18.73, -15.23) * mm});
            skLineSegment(sketch, "E3581", {"start": v(18.73, -15.23) * mm, "end": v(18.7, -15.19) * mm});
            skLineSegment(sketch, "E3582", {"start": v(18.7, -15.19) * mm, "end": v(18.67, -15.15) * mm});
            skLineSegment(sketch, "E3583", {"start": v(18.67, -15.15) * mm, "end": v(18.64, -15.12) * mm});
            skLineSegment(sketch, "E3584", {"start": v(18.64, -15.12) * mm, "end": v(18.61, -15.09) * mm});
            skLineSegment(sketch, "E3585", {"start": v(18.61, -15.09) * mm, "end": v(18.59, -15.06) * mm});
            skLineSegment(sketch, "E3586", {"start": v(18.59, -15.06) * mm, "end": v(18.56, -15.03) * mm});
            skLineSegment(sketch, "E3587", {"start": v(18.56, -15.03) * mm, "end": v(18.54, -15) * mm});
            skLineSegment(sketch, "E3588", {"start": v(18.54, -15) * mm, "end": v(18.52, -14.97) * mm});
            skLineSegment(sketch, "E3589", {"start": v(18.52, -14.97) * mm, "end": v(18.5, -14.95) * mm});
            skLineSegment(sketch, "E3590", {"start": v(18.5, -14.95) * mm, "end": v(18.47, -14.93) * mm});
            skLineSegment(sketch, "E3591", {"start": v(18.47, -14.93) * mm, "end": v(18.45, -14.9) * mm});
            skLineSegment(sketch, "E3592", {"start": v(18.45, -14.9) * mm, "end": v(18.43, -14.88) * mm});
            skLineSegment(sketch, "E3593", {"start": v(18.43, -14.88) * mm, "end": v(18.42, -14.86) * mm});
            skLineSegment(sketch, "E3594", {"start": v(18.42, -14.86) * mm, "end": v(18.4, -14.85) * mm});
            skLineSegment(sketch, "E3595", {"start": v(18.4, -14.85) * mm, "end": v(18.38, -14.83) * mm});
            skLineSegment(sketch, "E3596", {"start": v(18.38, -14.83) * mm, "end": v(18.37, -14.82) * mm});
            skLineSegment(sketch, "E3597", {"start": v(18.37, -14.82) * mm, "end": v(18.36, -14.8) * mm});
            skLineSegment(sketch, "E3598", {"start": v(18.36, -14.8) * mm, "end": v(18.34, -14.79) * mm});
            skLineSegment(sketch, "E3599", {"start": v(18.34, -14.79) * mm, "end": v(19.06, -13.85) * mm});
            skLineSegment(sketch, "E3600", {"start": v(19.06, -13.85) * mm, "end": v(19.08, -13.86) * mm});
            skLineSegment(sketch, "E3601", {"start": v(19.08, -13.86) * mm, "end": v(19.1, -13.87) * mm});
            skLineSegment(sketch, "E3602", {"start": v(19.1, -13.87) * mm, "end": v(19.11, -13.88) * mm});
            skLineSegment(sketch, "E3603", {"start": v(19.11, -13.88) * mm, "end": v(19.13, -13.89) * mm});
            skLineSegment(sketch, "E3604", {"start": v(19.13, -13.89) * mm, "end": v(19.16, -13.9) * mm});
            skLineSegment(sketch, "E3605", {"start": v(19.16, -13.9) * mm, "end": v(19.18, -13.91) * mm});
            skLineSegment(sketch, "E3606", {"start": v(19.18, -13.91) * mm, "end": v(19.2, -13.93) * mm});
            skLineSegment(sketch, "E3607", {"start": v(19.2, -13.93) * mm, "end": v(19.23, -13.94) * mm});
            skLineSegment(sketch, "E3608", {"start": v(19.23, -13.94) * mm, "end": v(19.26, -13.95) * mm});
            skLineSegment(sketch, "E3609", {"start": v(19.26, -13.95) * mm, "end": v(19.29, -13.97) * mm});
            skLineSegment(sketch, "E3610", {"start": v(19.29, -13.97) * mm, "end": v(19.32, -13.98) * mm});
            skLineSegment(sketch, "E3611", {"start": v(19.32, -13.98) * mm, "end": v(19.35, -14) * mm});
            skLineSegment(sketch, "E3612", {"start": v(19.35, -14) * mm, "end": v(19.39, -14.02) * mm});
            skLineSegment(sketch, "E3613", {"start": v(19.39, -14.02) * mm, "end": v(19.42, -14.03) * mm});
            skLineSegment(sketch, "E3614", {"start": v(19.42, -14.03) * mm, "end": v(19.46, -14.05) * mm});
            skLineSegment(sketch, "E3615", {"start": v(19.46, -14.05) * mm, "end": v(19.5, -14.07) * mm});
            skLineSegment(sketch, "E3616", {"start": v(19.5, -14.07) * mm, "end": v(19.54, -14.09) * mm});
            skLineSegment(sketch, "E3617", {"start": v(19.54, -14.09) * mm, "end": v(19.59, -14.1) * mm});
            skLineSegment(sketch, "E3618", {"start": v(19.59, -14.1) * mm, "end": v(19.63, -14.12) * mm});
            skLineSegment(sketch, "E3619", {"start": v(19.63, -14.12) * mm, "end": v(19.68, -14.14) * mm});
            skLineSegment(sketch, "E3620", {"start": v(19.68, -14.14) * mm, "end": v(19.73, -14.16) * mm});
            skLineSegment(sketch, "E3621", {"start": v(19.73, -14.16) * mm, "end": v(19.78, -14.18) * mm});
            skLineSegment(sketch, "E3622", {"start": v(19.78, -14.18) * mm, "end": v(19.83, -14.2) * mm});
            skLineSegment(sketch, "E3623", {"start": v(19.83, -14.2) * mm, "end": v(19.89, -14.22) * mm});
            skLineSegment(sketch, "E3624", {"start": v(19.89, -14.22) * mm, "end": v(19.94, -14.24) * mm});
            skLineSegment(sketch, "E3625", {"start": v(19.94, -14.24) * mm, "end": v(20, -14.26) * mm});
            skLineSegment(sketch, "E3626", {"start": v(20, -14.26) * mm, "end": v(20.06, -14.28) * mm});
            skLineSegment(sketch, "E3627", {"start": v(20.06, -14.28) * mm, "end": v(20.12, -14.3) * mm});
            skLineSegment(sketch, "E3628", {"start": v(20.12, -14.3) * mm, "end": v(20.19, -14.32) * mm});
            skLineSegment(sketch, "E3629", {"start": v(20.19, -14.32) * mm, "end": v(20.25, -14.34) * mm});
            skLineSegment(sketch, "E3630", {"start": v(20.25, -14.34) * mm, "end": v(20.32, -14.36) * mm});
            skLineSegment(sketch, "E3631", {"start": v(20.32, -14.36) * mm, "end": v(20.4, -14.38) * mm});
            skLineSegment(sketch, "E3632", {"start": v(20.4, -14.38) * mm, "end": v(20.46, -14.4) * mm});
            skLineSegment(sketch, "E3633", {"start": v(20.46, -14.4) * mm, "end": v(20.54, -14.42) * mm});
            skLineSegment(sketch, "E3634", {"start": v(20.54, -14.42) * mm, "end": v(20.61, -14.44) * mm});
            skLineSegment(sketch, "E3635", {"start": v(20.61, -14.44) * mm, "end": v(20.69, -14.45) * mm});
            skLineSegment(sketch, "E3636", {"start": v(20.69, -14.45) * mm, "end": v(20.77, -14.47) * mm});
            skLineSegment(sketch, "E3637", {"start": v(20.77, -14.47) * mm, "end": v(20.85, -14.5) * mm});
            skLineSegment(sketch, "E3638", {"start": v(20.85, -14.5) * mm, "end": v(20.93, -14.5) * mm});
            skLineSegment(sketch, "E3639", {"start": v(20.93, -14.5) * mm, "end": v(21.02, -14.53) * mm});
            skLineSegment(sketch, "E3640", {"start": v(21.02, -14.53) * mm, "end": v(21.1, -14.54) * mm});
            skLineSegment(sketch, "E3641", {"start": v(21.1, -14.54) * mm, "end": v(21.2, -14.56) * mm});
            skLineSegment(sketch, "E3642", {"start": v(21.2, -14.56) * mm, "end": v(21.28, -14.58) * mm});
            skLineSegment(sketch, "E3643", {"start": v(21.28, -14.58) * mm, "end": v(21.38, -14.6) * mm});
            skLineSegment(sketch, "E3644", {"start": v(21.38, -14.6) * mm, "end": v(21.47, -14.6) * mm});
            skLineSegment(sketch, "E3645", {"start": v(21.47, -14.6) * mm, "end": v(21.57, -14.62) * mm});
            skLineSegment(sketch, "E3646", {"start": v(21.57, -14.62) * mm, "end": v(21.67, -14.64) * mm});
            skLineSegment(sketch, "E3647", {"start": v(21.67, -14.64) * mm, "end": v(21.77, -14.65) * mm});
            skLineSegment(sketch, "E3648", {"start": v(21.77, -14.65) * mm, "end": v(21.8, -14.62) * mm});
            skLineSegment(sketch, "E3649", {"start": v(21.8, -14.62) * mm, "end": v(22.25, -13.92) * mm});
            skLineSegment(sketch, "E3650", {"start": v(22.25, -13.92) * mm, "end": v(22.27, -13.88) * mm});
            skLineSegment(sketch, "E3651", {"start": v(22.27, -13.88) * mm, "end": v(22.22, -13.79) * mm});
            skLineSegment(sketch, "E3652", {"start": v(22.22, -13.79) * mm, "end": v(22.16, -13.7) * mm});
            skLineSegment(sketch, "E3653", {"start": v(22.16, -13.7) * mm, "end": v(22.1, -13.62) * mm});
            skLineSegment(sketch, "E3654", {"start": v(22.1, -13.62) * mm, "end": v(22.06, -13.54) * mm});
            skLineSegment(sketch, "E3655", {"start": v(22.06, -13.54) * mm, "end": v(22, -13.47) * mm});
            skLineSegment(sketch, "E3656", {"start": v(22, -13.47) * mm, "end": v(21.95, -13.4) * mm});
            skLineSegment(sketch, "E3657", {"start": v(21.95, -13.4) * mm, "end": v(21.9, -13.32) * mm});
            skLineSegment(sketch, "E3658", {"start": v(21.9, -13.32) * mm, "end": v(21.85, -13.24) * mm});
            skLineSegment(sketch, "E3659", {"start": v(21.85, -13.24) * mm, "end": v(21.8, -13.17) * mm});
            skLineSegment(sketch, "E3660", {"start": v(21.8, -13.17) * mm, "end": v(21.75, -13.1) * mm});
            skLineSegment(sketch, "E3661", {"start": v(21.75, -13.1) * mm, "end": v(21.7, -13.04) * mm});
            skLineSegment(sketch, "E3662", {"start": v(21.7, -13.04) * mm, "end": v(21.65, -12.97) * mm});
            skLineSegment(sketch, "E3663", {"start": v(21.65, -12.97) * mm, "end": v(21.6, -12.91) * mm});
            skLineSegment(sketch, "E3664", {"start": v(21.6, -12.91) * mm, "end": v(21.55, -12.85) * mm});
            skLineSegment(sketch, "E3665", {"start": v(21.55, -12.85) * mm, "end": v(21.5, -12.8) * mm});
            skLineSegment(sketch, "E3666", {"start": v(21.5, -12.8) * mm, "end": v(21.46, -12.73) * mm});
            skLineSegment(sketch, "E3667", {"start": v(21.46, -12.73) * mm, "end": v(21.41, -12.68) * mm});
            skLineSegment(sketch, "E3668", {"start": v(21.41, -12.68) * mm, "end": v(21.36, -12.62) * mm});
            skLineSegment(sketch, "E3669", {"start": v(21.36, -12.62) * mm, "end": v(21.32, -12.57) * mm});
            skLineSegment(sketch, "E3670", {"start": v(21.32, -12.57) * mm, "end": v(21.28, -12.52) * mm});
            skLineSegment(sketch, "E3671", {"start": v(21.28, -12.52) * mm, "end": v(21.23, -12.47) * mm});
            skLineSegment(sketch, "E3672", {"start": v(21.23, -12.47) * mm, "end": v(21.19, -12.43) * mm});
            skLineSegment(sketch, "E3673", {"start": v(21.19, -12.43) * mm, "end": v(21.15, -12.38) * mm});
            skLineSegment(sketch, "E3674", {"start": v(21.15, -12.38) * mm, "end": v(21.1, -12.34) * mm});
            skLineSegment(sketch, "E3675", {"start": v(21.1, -12.34) * mm, "end": v(21.07, -12.3) * mm});
            skLineSegment(sketch, "E3676", {"start": v(21.07, -12.3) * mm, "end": v(21.03, -12.26) * mm});
            skLineSegment(sketch, "E3677", {"start": v(21.03, -12.26) * mm, "end": v(20.99, -12.22) * mm});
            skLineSegment(sketch, "E3678", {"start": v(20.99, -12.22) * mm, "end": v(20.95, -12.18) * mm});
            skLineSegment(sketch, "E3679", {"start": v(20.95, -12.18) * mm, "end": v(20.91, -12.14) * mm});
            skLineSegment(sketch, "E3680", {"start": v(20.91, -12.14) * mm, "end": v(20.88, -12.1) * mm});
            skLineSegment(sketch, "E3681", {"start": v(20.88, -12.1) * mm, "end": v(20.84, -12.08) * mm});
            skLineSegment(sketch, "E3682", {"start": v(20.84, -12.08) * mm, "end": v(20.8, -12.05) * mm});
            skLineSegment(sketch, "E3683", {"start": v(20.8, -12.05) * mm, "end": v(20.78, -12.02) * mm});
            skLineSegment(sketch, "E3684", {"start": v(20.78, -12.02) * mm, "end": v(20.75, -11.99) * mm});
            skLineSegment(sketch, "E3685", {"start": v(20.75, -11.99) * mm, "end": v(20.72, -11.96) * mm});
            skLineSegment(sketch, "E3686", {"start": v(20.72, -11.96) * mm, "end": v(20.69, -11.94) * mm});
            skLineSegment(sketch, "E3687", {"start": v(20.69, -11.94) * mm, "end": v(20.66, -11.91) * mm});
            skLineSegment(sketch, "E3688", {"start": v(20.66, -11.91) * mm, "end": v(20.63, -11.9) * mm});
            skLineSegment(sketch, "E3689", {"start": v(20.63, -11.9) * mm, "end": v(20.6, -11.87) * mm});
            skLineSegment(sketch, "E3690", {"start": v(20.6, -11.87) * mm, "end": v(20.58, -11.85) * mm});
            skLineSegment(sketch, "E3691", {"start": v(20.58, -11.85) * mm, "end": v(20.56, -11.83) * mm});
            skLineSegment(sketch, "E3692", {"start": v(20.56, -11.83) * mm, "end": v(20.54, -11.82) * mm});
            skLineSegment(sketch, "E3693", {"start": v(20.54, -11.82) * mm, "end": v(20.52, -11.8) * mm});
            skLineSegment(sketch, "E3694", {"start": v(20.52, -11.8) * mm, "end": v(20.5, -11.79) * mm});
            skLineSegment(sketch, "E3695", {"start": v(20.5, -11.79) * mm, "end": v(20.48, -11.77) * mm});
            skLineSegment(sketch, "E3696", {"start": v(20.48, -11.77) * mm, "end": v(20.46, -11.76) * mm});
            skLineSegment(sketch, "E3697", {"start": v(20.46, -11.76) * mm, "end": v(20.45, -11.75) * mm});
            skLineSegment(sketch, "E3698", {"start": v(20.45, -11.75) * mm, "end": v(20.43, -11.74) * mm});
            skLineSegment(sketch, "E3699", {"start": v(20.43, -11.74) * mm, "end": v(21, -10.7) * mm});
            skLineSegment(sketch, "E3700", {"start": v(21, -10.7) * mm, "end": v(21.01, -10.7) * mm});
            skLineSegment(sketch, "E3701", {"start": v(21.01, -10.7) * mm, "end": v(21.03, -10.7) * mm});
            skLineSegment(sketch, "E3702", {"start": v(21.03, -10.7) * mm, "end": v(21.05, -10.72) * mm});
            skLineSegment(sketch, "E3703", {"start": v(21.05, -10.72) * mm, "end": v(21.07, -10.72) * mm});
            skLineSegment(sketch, "E3704", {"start": v(21.07, -10.72) * mm, "end": v(21.1, -10.73) * mm});
            skLineSegment(sketch, "E3705", {"start": v(21.1, -10.73) * mm, "end": v(21.12, -10.74) * mm});
            skLineSegment(sketch, "E3706", {"start": v(21.12, -10.74) * mm, "end": v(21.14, -10.75) * mm});
            skLineSegment(sketch, "E3707", {"start": v(21.14, -10.75) * mm, "end": v(21.17, -10.76) * mm});
            skLineSegment(sketch, "E3708", {"start": v(21.17, -10.76) * mm, "end": v(21.2, -10.77) * mm});
            skLineSegment(sketch, "E3709", {"start": v(21.2, -10.77) * mm, "end": v(21.23, -10.78) * mm});
            skLineSegment(sketch, "E3710", {"start": v(21.23, -10.78) * mm, "end": v(21.27, -10.79) * mm});
            skLineSegment(sketch, "E3711", {"start": v(21.27, -10.79) * mm, "end": v(21.3, -10.8) * mm});
            skLineSegment(sketch, "E3712", {"start": v(21.3, -10.8) * mm, "end": v(21.34, -10.81) * mm});
            skLineSegment(sketch, "E3713", {"start": v(21.34, -10.81) * mm, "end": v(21.38, -10.82) * mm});
            skLineSegment(sketch, "E3714", {"start": v(21.38, -10.82) * mm, "end": v(21.42, -10.83) * mm});
            skLineSegment(sketch, "E3715", {"start": v(21.42, -10.83) * mm, "end": v(21.46, -10.84) * mm});
            skLineSegment(sketch, "E3716", {"start": v(21.46, -10.84) * mm, "end": v(21.5, -10.86) * mm});
            skLineSegment(sketch, "E3717", {"start": v(21.5, -10.86) * mm, "end": v(21.55, -10.87) * mm});
            skLineSegment(sketch, "E3718", {"start": v(21.55, -10.87) * mm, "end": v(21.6, -10.88) * mm});
            skLineSegment(sketch, "E3719", {"start": v(21.6, -10.88) * mm, "end": v(21.65, -10.89) * mm});
            skLineSegment(sketch, "E3720", {"start": v(21.65, -10.89) * mm, "end": v(21.7, -10.9) * mm});
            skLineSegment(sketch, "E3721", {"start": v(21.7, -10.9) * mm, "end": v(21.75, -10.91) * mm});
            skLineSegment(sketch, "E3722", {"start": v(21.75, -10.91) * mm, "end": v(21.8, -10.92) * mm});
            skLineSegment(sketch, "E3723", {"start": v(21.8, -10.92) * mm, "end": v(21.87, -10.93) * mm});
            skLineSegment(sketch, "E3724", {"start": v(21.87, -10.93) * mm, "end": v(21.93, -10.94) * mm});
            skLineSegment(sketch, "E3725", {"start": v(21.93, -10.94) * mm, "end": v(21.99, -10.95) * mm});
            skLineSegment(sketch, "E3726", {"start": v(21.99, -10.95) * mm, "end": v(22.05, -10.96) * mm});
            skLineSegment(sketch, "E3727", {"start": v(22.05, -10.96) * mm, "end": v(22.11, -10.97) * mm});
            skLineSegment(sketch, "E3728", {"start": v(22.11, -10.97) * mm, "end": v(22.18, -10.98) * mm});
            skLineSegment(sketch, "E3729", {"start": v(22.18, -10.98) * mm, "end": v(22.25, -11) * mm});
            skLineSegment(sketch, "E3730", {"start": v(22.25, -11) * mm, "end": v(22.32, -11) * mm});
            skLineSegment(sketch, "E3731", {"start": v(22.32, -11) * mm, "end": v(22.39, -11.01) * mm});
            skLineSegment(sketch, "E3732", {"start": v(22.39, -11.01) * mm, "end": v(22.46, -11.02) * mm});
            skLineSegment(sketch, "E3733", {"start": v(22.46, -11.02) * mm, "end": v(22.54, -11.03) * mm});
            skLineSegment(sketch, "E3734", {"start": v(22.54, -11.03) * mm, "end": v(22.62, -11.03) * mm});
            skLineSegment(sketch, "E3735", {"start": v(22.62, -11.03) * mm, "end": v(22.7, -11.04) * mm});
            skLineSegment(sketch, "E3736", {"start": v(22.7, -11.04) * mm, "end": v(22.78, -11.05) * mm});
            skLineSegment(sketch, "E3737", {"start": v(22.78, -11.05) * mm, "end": v(22.86, -11.05) * mm});
            skLineSegment(sketch, "E3738", {"start": v(22.86, -11.05) * mm, "end": v(22.95, -11.06) * mm});
            skLineSegment(sketch, "E3739", {"start": v(22.95, -11.06) * mm, "end": v(23.03, -11.06) * mm});
            skLineSegment(sketch, "E3740", {"start": v(23.03, -11.06) * mm, "end": v(23.12, -11.06) * mm});
            skLineSegment(sketch, "E3741", {"start": v(23.12, -11.06) * mm, "end": v(23.21, -11.07) * mm});
            skLineSegment(sketch, "E3742", {"start": v(23.21, -11.07) * mm, "end": v(23.3, -11.07) * mm});
            skLineSegment(sketch, "E3743", {"start": v(23.3, -11.07) * mm, "end": v(23.4, -11.07) * mm});
            skLineSegment(sketch, "E3744", {"start": v(23.4, -11.07) * mm, "end": v(23.5, -11.07) * mm});
            skLineSegment(sketch, "E3745", {"start": v(23.5, -11.07) * mm, "end": v(23.59, -11.07) * mm});
            skLineSegment(sketch, "E3746", {"start": v(23.59, -11.07) * mm, "end": v(23.69, -11.07) * mm});
            skLineSegment(sketch, "E3747", {"start": v(23.69, -11.07) * mm, "end": v(23.8, -11.07) * mm});
            skLineSegment(sketch, "E3748", {"start": v(23.8, -11.07) * mm, "end": v(23.82, -11.03) * mm});
            skLineSegment(sketch, "E3749", {"start": v(23.82, -11.03) * mm, "end": v(24.16, -10.27) * mm});
            skLineSegment(sketch, "E3750", {"start": v(24.16, -10.27) * mm, "end": v(24.17, -10.22) * mm});
            skLineSegment(sketch, "E3751", {"start": v(24.17, -10.22) * mm, "end": v(24.1, -10.14) * mm});
            skLineSegment(sketch, "E3752", {"start": v(24.1, -10.14) * mm, "end": v(24.03, -10.07) * mm});
            skLineSegment(sketch, "E3753", {"start": v(24.03, -10.07) * mm, "end": v(23.97, -10) * mm});
            skLineSegment(sketch, "E3754", {"start": v(23.97, -10) * mm, "end": v(23.9, -9.93) * mm});
            skLineSegment(sketch, "E3755", {"start": v(23.9, -9.93) * mm, "end": v(23.84, -9.86) * mm});
            skLineSegment(sketch, "E3756", {"start": v(23.84, -9.86) * mm, "end": v(23.78, -9.8) * mm});
            skLineSegment(sketch, "E3757", {"start": v(23.78, -9.8) * mm, "end": v(23.71, -9.73) * mm});
            skLineSegment(sketch, "E3758", {"start": v(23.71, -9.73) * mm, "end": v(23.65, -9.66) * mm});
            skLineSegment(sketch, "E3759", {"start": v(23.65, -9.66) * mm, "end": v(23.6, -9.6) * mm});
            skLineSegment(sketch, "E3760", {"start": v(23.6, -9.6) * mm, "end": v(23.53, -9.54) * mm});
            skLineSegment(sketch, "E3761", {"start": v(23.53, -9.54) * mm, "end": v(23.47, -9.48) * mm});
            skLineSegment(sketch, "E3762", {"start": v(23.47, -9.48) * mm, "end": v(23.41, -9.43) * mm});
            skLineSegment(sketch, "E3763", {"start": v(23.41, -9.43) * mm, "end": v(23.35, -9.37) * mm});
            skLineSegment(sketch, "E3764", {"start": v(23.35, -9.37) * mm, "end": v(23.3, -9.32) * mm});
            skLineSegment(sketch, "E3765", {"start": v(23.3, -9.32) * mm, "end": v(23.24, -9.27) * mm});
            skLineSegment(sketch, "E3766", {"start": v(23.24, -9.27) * mm, "end": v(23.18, -9.22) * mm});
            skLineSegment(sketch, "E3767", {"start": v(23.18, -9.22) * mm, "end": v(23.13, -9.17) * mm});
            skLineSegment(sketch, "E3768", {"start": v(23.13, -9.17) * mm, "end": v(23.08, -9.13) * mm});
            skLineSegment(sketch, "E3769", {"start": v(23.08, -9.13) * mm, "end": v(23.02, -9.08) * mm});
            skLineSegment(sketch, "E3770", {"start": v(23.02, -9.08) * mm, "end": v(22.97, -9.04) * mm});
            skLineSegment(sketch, "E3771", {"start": v(22.97, -9.04) * mm, "end": v(22.92, -9) * mm});
            skLineSegment(sketch, "E3772", {"start": v(22.92, -9) * mm, "end": v(22.87, -8.96) * mm});
            skLineSegment(sketch, "E3773", {"start": v(22.87, -8.96) * mm, "end": v(22.82, -8.92) * mm});
            skLineSegment(sketch, "E3774", {"start": v(22.82, -8.92) * mm, "end": v(22.78, -8.88) * mm});
            skLineSegment(sketch, "E3775", {"start": v(22.78, -8.88) * mm, "end": v(22.73, -8.85) * mm});
            skLineSegment(sketch, "E3776", {"start": v(22.73, -8.85) * mm, "end": v(22.68, -8.82) * mm});
            skLineSegment(sketch, "E3777", {"start": v(22.68, -8.82) * mm, "end": v(22.64, -8.78) * mm});
            skLineSegment(sketch, "E3778", {"start": v(22.64, -8.78) * mm, "end": v(22.6, -8.75) * mm});
            skLineSegment(sketch, "E3779", {"start": v(22.6, -8.75) * mm, "end": v(22.56, -8.72) * mm});
            skLineSegment(sketch, "E3780", {"start": v(22.56, -8.72) * mm, "end": v(22.52, -8.7) * mm});
            skLineSegment(sketch, "E3781", {"start": v(22.52, -8.7) * mm, "end": v(22.48, -8.67) * mm});
            skLineSegment(sketch, "E3782", {"start": v(22.48, -8.67) * mm, "end": v(22.44, -8.64) * mm});
            skLineSegment(sketch, "E3783", {"start": v(22.44, -8.64) * mm, "end": v(22.4, -8.62) * mm});
            skLineSegment(sketch, "E3784", {"start": v(22.4, -8.62) * mm, "end": v(22.37, -8.6) * mm});
            skLineSegment(sketch, "E3785", {"start": v(22.37, -8.6) * mm, "end": v(22.33, -8.57) * mm});
            skLineSegment(sketch, "E3786", {"start": v(22.33, -8.57) * mm, "end": v(22.3, -8.55) * mm});
            skLineSegment(sketch, "E3787", {"start": v(22.3, -8.55) * mm, "end": v(22.27, -8.54) * mm});
            skLineSegment(sketch, "E3788", {"start": v(22.27, -8.54) * mm, "end": v(22.24, -8.52) * mm});
            skLineSegment(sketch, "E3789", {"start": v(22.24, -8.52) * mm, "end": v(22.2, -8.5) * mm});
            skLineSegment(sketch, "E3790", {"start": v(22.2, -8.5) * mm, "end": v(22.18, -8.49) * mm});
            skLineSegment(sketch, "E3791", {"start": v(22.18, -8.49) * mm, "end": v(22.16, -8.47) * mm});
            skLineSegment(sketch, "E3792", {"start": v(22.16, -8.47) * mm, "end": v(22.13, -8.46) * mm});
            skLineSegment(sketch, "E3793", {"start": v(22.13, -8.46) * mm, "end": v(22.1, -8.45) * mm});
            skLineSegment(sketch, "E3794", {"start": v(22.1, -8.45) * mm, "end": v(22.09, -8.43) * mm});
            skLineSegment(sketch, "E3795", {"start": v(22.09, -8.43) * mm, "end": v(22.07, -8.42) * mm});
            skLineSegment(sketch, "E3796", {"start": v(22.07, -8.42) * mm, "end": v(22.05, -8.42) * mm});
            skLineSegment(sketch, "E3797", {"start": v(22.05, -8.42) * mm, "end": v(22.03, -8.4) * mm});
            skLineSegment(sketch, "E3798", {"start": v(22.03, -8.4) * mm, "end": v(22.02, -8.4) * mm});
            skLineSegment(sketch, "E3799", {"start": v(22.02, -8.4) * mm, "end": v(22.4, -7.28) * mm});
            skLineSegment(sketch, "E3800", {"start": v(22.4, -7.28) * mm, "end": v(22.43, -7.28) * mm});
            skLineSegment(sketch, "E3801", {"start": v(22.43, -7.28) * mm, "end": v(22.45, -7.29) * mm});
            skLineSegment(sketch, "E3802", {"start": v(22.45, -7.29) * mm, "end": v(22.47, -7.3) * mm});
            skLineSegment(sketch, "E3803", {"start": v(22.47, -7.3) * mm, "end": v(22.49, -7.3) * mm});
            skLineSegment(sketch, "E3804", {"start": v(22.49, -7.3) * mm, "end": v(22.51, -7.3) * mm});
            skLineSegment(sketch, "E3805", {"start": v(22.51, -7.3) * mm, "end": v(22.54, -7.3) * mm});
            skLineSegment(sketch, "E3806", {"start": v(22.54, -7.3) * mm, "end": v(22.57, -7.3) * mm});
            skLineSegment(sketch, "E3807", {"start": v(22.57, -7.3) * mm, "end": v(22.6, -7.31) * mm});
            skLineSegment(sketch, "E3808", {"start": v(22.6, -7.31) * mm, "end": v(22.63, -7.32) * mm});
            skLineSegment(sketch, "E3809", {"start": v(22.63, -7.32) * mm, "end": v(22.66, -7.32) * mm});
            skLineSegment(sketch, "E3810", {"start": v(22.66, -7.32) * mm, "end": v(22.7, -7.33) * mm});
            skLineSegment(sketch, "E3811", {"start": v(22.7, -7.33) * mm, "end": v(22.73, -7.33) * mm});
            skLineSegment(sketch, "E3812", {"start": v(22.73, -7.33) * mm, "end": v(22.77, -7.34) * mm});
            skLineSegment(sketch, "E3813", {"start": v(22.77, -7.34) * mm, "end": v(22.8, -7.34) * mm});
            skLineSegment(sketch, "E3814", {"start": v(22.8, -7.34) * mm, "end": v(22.85, -7.35) * mm});
            skLineSegment(sketch, "E3815", {"start": v(22.85, -7.35) * mm, "end": v(22.9, -7.35) * mm});
            skLineSegment(sketch, "E3816", {"start": v(22.9, -7.35) * mm, "end": v(22.94, -7.36) * mm});
            skLineSegment(sketch, "E3817", {"start": v(22.94, -7.36) * mm, "end": v(22.99, -7.36) * mm});
            skLineSegment(sketch, "E3818", {"start": v(22.99, -7.36) * mm, "end": v(23.03, -7.37) * mm});
            skLineSegment(sketch, "E3819", {"start": v(23.03, -7.37) * mm, "end": v(23.09, -7.37) * mm});
            skLineSegment(sketch, "E3820", {"start": v(23.09, -7.37) * mm, "end": v(23.14, -7.37) * mm});
            skLineSegment(sketch, "E3821", {"start": v(23.14, -7.37) * mm, "end": v(23.2, -7.37) * mm});
            skLineSegment(sketch, "E3822", {"start": v(23.2, -7.37) * mm, "end": v(23.25, -7.38) * mm});
            skLineSegment(sketch, "E3823", {"start": v(23.25, -7.38) * mm, "end": v(23.3, -7.38) * mm});
            skLineSegment(sketch, "E3824", {"start": v(23.3, -7.38) * mm, "end": v(23.37, -7.38) * mm});
            skLineSegment(sketch, "E3825", {"start": v(23.37, -7.38) * mm, "end": v(23.43, -7.38) * mm});
            skLineSegment(sketch, "E3826", {"start": v(23.43, -7.38) * mm, "end": v(23.5, -7.38) * mm});
            skLineSegment(sketch, "E3827", {"start": v(23.5, -7.38) * mm, "end": v(23.56, -7.38) * mm});
            skLineSegment(sketch, "E3828", {"start": v(23.56, -7.38) * mm, "end": v(23.62, -7.38) * mm});
            skLineSegment(sketch, "E3829", {"start": v(23.62, -7.38) * mm, "end": v(23.7, -7.38) * mm});
            skLineSegment(sketch, "E3830", {"start": v(23.7, -7.38) * mm, "end": v(23.76, -7.38) * mm});
            skLineSegment(sketch, "E3831", {"start": v(23.76, -7.38) * mm, "end": v(23.84, -7.37) * mm});
            skLineSegment(sketch, "E3832", {"start": v(23.84, -7.37) * mm, "end": v(23.91, -7.37) * mm});
            skLineSegment(sketch, "E3833", {"start": v(23.91, -7.37) * mm, "end": v(23.99, -7.36) * mm});
            skLineSegment(sketch, "E3834", {"start": v(23.99, -7.36) * mm, "end": v(24.06, -7.36) * mm});
            skLineSegment(sketch, "E3835", {"start": v(24.06, -7.36) * mm, "end": v(24.14, -7.35) * mm});
            skLineSegment(sketch, "E3836", {"start": v(24.14, -7.35) * mm, "end": v(24.22, -7.35) * mm});
            skLineSegment(sketch, "E3837", {"start": v(24.22, -7.35) * mm, "end": v(24.3, -7.34) * mm});
            skLineSegment(sketch, "E3838", {"start": v(24.3, -7.34) * mm, "end": v(24.4, -7.33) * mm});
            skLineSegment(sketch, "E3839", {"start": v(24.4, -7.33) * mm, "end": v(24.48, -7.32) * mm});
            skLineSegment(sketch, "E3840", {"start": v(24.48, -7.32) * mm, "end": v(24.57, -7.31) * mm});
            skLineSegment(sketch, "E3841", {"start": v(24.57, -7.31) * mm, "end": v(24.66, -7.3) * mm});
            skLineSegment(sketch, "E3842", {"start": v(24.66, -7.3) * mm, "end": v(24.75, -7.29) * mm});
            skLineSegment(sketch, "E3843", {"start": v(24.75, -7.29) * mm, "end": v(24.84, -7.27) * mm});
            skLineSegment(sketch, "E3844", {"start": v(24.84, -7.27) * mm, "end": v(24.93, -7.26) * mm});
            skLineSegment(sketch, "E3845", {"start": v(24.93, -7.26) * mm, "end": v(25.03, -7.24) * mm});
            skLineSegment(sketch, "E3846", {"start": v(25.03, -7.24) * mm, "end": v(25.13, -7.23) * mm});
            skLineSegment(sketch, "E3847", {"start": v(25.13, -7.23) * mm, "end": v(25.23, -7.2) * mm});
            skLineSegment(sketch, "E3848", {"start": v(25.23, -7.2) * mm, "end": v(25.25, -7.17) * mm});
            skLineSegment(sketch, "E3849", {"start": v(25.25, -7.17) * mm, "end": v(25.47, -6.36) * mm});
            skLineSegment(sketch, "E3850", {"start": v(25.47, -6.36) * mm, "end": v(25.47, -6.32) * mm});
            skLineSegment(sketch, "E3851", {"start": v(25.47, -6.32) * mm, "end": v(25.39, -6.25) * mm});
            skLineSegment(sketch, "E3852", {"start": v(25.39, -6.25) * mm, "end": v(25.31, -6.19) * mm});
            skLineSegment(sketch, "E3853", {"start": v(25.31, -6.19) * mm, "end": v(25.24, -6.13) * mm});
            skLineSegment(sketch, "E3854", {"start": v(25.24, -6.13) * mm, "end": v(25.16, -6.07) * mm});
            skLineSegment(sketch, "E3855", {"start": v(25.16, -6.07) * mm, "end": v(25.09, -6) * mm});
            skLineSegment(sketch, "E3856", {"start": v(25.09, -6) * mm, "end": v(25.02, -5.95) * mm});
            skLineSegment(sketch, "E3857", {"start": v(25.02, -5.95) * mm, "end": v(24.94, -5.9) * mm});
            skLineSegment(sketch, "E3858", {"start": v(24.94, -5.9) * mm, "end": v(24.87, -5.84) * mm});
            skLineSegment(sketch, "E3859", {"start": v(24.87, -5.84) * mm, "end": v(24.8, -5.8) * mm});
            skLineSegment(sketch, "E3860", {"start": v(24.8, -5.8) * mm, "end": v(24.73, -5.74) * mm});
            skLineSegment(sketch, "E3861", {"start": v(24.73, -5.74) * mm, "end": v(24.67, -5.7) * mm});
            skLineSegment(sketch, "E3862", {"start": v(24.67, -5.7) * mm, "end": v(24.6, -5.65) * mm});
            skLineSegment(sketch, "E3863", {"start": v(24.6, -5.65) * mm, "end": v(24.53, -5.6) * mm});
            skLineSegment(sketch, "E3864", {"start": v(24.53, -5.6) * mm, "end": v(24.47, -5.56) * mm});
            skLineSegment(sketch, "E3865", {"start": v(24.47, -5.56) * mm, "end": v(24.4, -5.52) * mm});
            skLineSegment(sketch, "E3866", {"start": v(24.4, -5.52) * mm, "end": v(24.34, -5.48) * mm});
            skLineSegment(sketch, "E3867", {"start": v(24.34, -5.48) * mm, "end": v(24.28, -5.44) * mm});
            skLineSegment(sketch, "E3868", {"start": v(24.28, -5.44) * mm, "end": v(24.22, -5.4) * mm});
            skLineSegment(sketch, "E3869", {"start": v(24.22, -5.4) * mm, "end": v(24.16, -5.37) * mm});
            skLineSegment(sketch, "E3870", {"start": v(24.16, -5.37) * mm, "end": v(24.1, -5.33) * mm});
            skLineSegment(sketch, "E3871", {"start": v(24.1, -5.33) * mm, "end": v(24.05, -5.3) * mm});
            skLineSegment(sketch, "E3872", {"start": v(24.05, -5.3) * mm, "end": v(24, -5.27) * mm});
            skLineSegment(sketch, "E3873", {"start": v(24, -5.27) * mm, "end": v(23.94, -5.24) * mm});
            skLineSegment(sketch, "E3874", {"start": v(23.94, -5.24) * mm, "end": v(23.89, -5.21) * mm});
            skLineSegment(sketch, "E3875", {"start": v(23.89, -5.21) * mm, "end": v(23.83, -5.18) * mm});
            skLineSegment(sketch, "E3876", {"start": v(23.83, -5.18) * mm, "end": v(23.78, -5.16) * mm});
            skLineSegment(sketch, "E3877", {"start": v(23.78, -5.16) * mm, "end": v(23.74, -5.13) * mm});
            skLineSegment(sketch, "E3878", {"start": v(23.74, -5.13) * mm, "end": v(23.69, -5.1) * mm});
            skLineSegment(sketch, "E3879", {"start": v(23.69, -5.1) * mm, "end": v(23.64, -5.09) * mm});
            skLineSegment(sketch, "E3880", {"start": v(23.64, -5.09) * mm, "end": v(23.6, -5.07) * mm});
            skLineSegment(sketch, "E3881", {"start": v(23.6, -5.07) * mm, "end": v(23.56, -5.05) * mm});
            skLineSegment(sketch, "E3882", {"start": v(23.56, -5.05) * mm, "end": v(23.51, -5.03) * mm});
            skLineSegment(sketch, "E3883", {"start": v(23.51, -5.03) * mm, "end": v(23.47, -5) * mm});
            skLineSegment(sketch, "E3884", {"start": v(23.47, -5) * mm, "end": v(23.44, -5) * mm});
            skLineSegment(sketch, "E3885", {"start": v(23.44, -5) * mm, "end": v(23.4, -4.98) * mm});
            skLineSegment(sketch, "E3886", {"start": v(23.4, -4.98) * mm, "end": v(23.36, -4.96) * mm});
            skLineSegment(sketch, "E3887", {"start": v(23.36, -4.96) * mm, "end": v(23.33, -4.95) * mm});
            skLineSegment(sketch, "E3888", {"start": v(23.33, -4.95) * mm, "end": v(23.3, -4.93) * mm});
            skLineSegment(sketch, "E3889", {"start": v(23.3, -4.93) * mm, "end": v(23.27, -4.92) * mm});
            skLineSegment(sketch, "E3890", {"start": v(23.27, -4.92) * mm, "end": v(23.24, -4.91) * mm});
            skLineSegment(sketch, "E3891", {"start": v(23.24, -4.91) * mm, "end": v(23.2, -4.9) * mm});
            skLineSegment(sketch, "E3892", {"start": v(23.2, -4.9) * mm, "end": v(23.18, -4.9) * mm});
            skLineSegment(sketch, "E3893", {"start": v(23.18, -4.9) * mm, "end": v(23.16, -4.88) * mm});
            skLineSegment(sketch, "E3894", {"start": v(23.16, -4.88) * mm, "end": v(23.13, -4.88) * mm});
            skLineSegment(sketch, "E3895", {"start": v(23.13, -4.88) * mm, "end": v(23.11, -4.87) * mm});
            skLineSegment(sketch, "E3896", {"start": v(23.11, -4.87) * mm, "end": v(23.1, -4.86) * mm});
            skLineSegment(sketch, "E3897", {"start": v(23.1, -4.86) * mm, "end": v(23.08, -4.86) * mm});
            skLineSegment(sketch, "E3898", {"start": v(23.08, -4.86) * mm, "end": v(23.06, -4.85) * mm});
            skLineSegment(sketch, "E3899", {"start": v(23.06, -4.85) * mm, "end": v(23.27, -3.69) * mm});
            skLineSegment(sketch, "E3900", {"start": v(23.27, -3.69) * mm, "end": v(23.3, -3.68) * mm});
            skLineSegment(sketch, "E3901", {"start": v(23.3, -3.68) * mm, "end": v(23.31, -3.69) * mm});
            skLineSegment(sketch, "E3902", {"start": v(23.31, -3.69) * mm, "end": v(23.33, -3.69) * mm});
            skLineSegment(sketch, "E3903", {"start": v(23.33, -3.69) * mm, "end": v(23.35, -3.69) * mm});
            skLineSegment(sketch, "E3904", {"start": v(23.35, -3.69) * mm, "end": v(23.38, -3.69) * mm});
            skLineSegment(sketch, "E3905", {"start": v(23.38, -3.69) * mm, "end": v(23.4, -3.69) * mm});
            skLineSegment(sketch, "E3906", {"start": v(23.4, -3.69) * mm, "end": v(23.43, -3.69) * mm});
            skLineSegment(sketch, "E3907", {"start": v(23.43, -3.69) * mm, "end": v(23.46, -3.7) * mm});
            skLineSegment(sketch, "E3908", {"start": v(23.46, -3.7) * mm, "end": v(23.5, -3.7) * mm});
            skLineSegment(sketch, "E3909", {"start": v(23.5, -3.7) * mm, "end": v(23.53, -3.7) * mm});
            skLineSegment(sketch, "E3910", {"start": v(23.53, -3.7) * mm, "end": v(23.56, -3.69) * mm});
            skLineSegment(sketch, "E3911", {"start": v(23.56, -3.69) * mm, "end": v(23.6, -3.69) * mm});
            skLineSegment(sketch, "E3912", {"start": v(23.6, -3.69) * mm, "end": v(23.64, -3.69) * mm});
            skLineSegment(sketch, "E3913", {"start": v(23.64, -3.69) * mm, "end": v(23.68, -3.69) * mm});
            skLineSegment(sketch, "E3914", {"start": v(23.68, -3.69) * mm, "end": v(23.72, -3.68) * mm});
            skLineSegment(sketch, "E3915", {"start": v(23.72, -3.68) * mm, "end": v(23.76, -3.68) * mm});
            skLineSegment(sketch, "E3916", {"start": v(23.76, -3.68) * mm, "end": v(23.8, -3.68) * mm});
            skLineSegment(sketch, "E3917", {"start": v(23.8, -3.68) * mm, "end": v(23.85, -3.68) * mm});
            skLineSegment(sketch, "E3918", {"start": v(23.85, -3.68) * mm, "end": v(23.9, -3.67) * mm});
            skLineSegment(sketch, "E3919", {"start": v(23.9, -3.67) * mm, "end": v(23.95, -3.67) * mm});
            skLineSegment(sketch, "E3920", {"start": v(23.95, -3.67) * mm, "end": v(24, -3.66) * mm});
            skLineSegment(sketch, "E3921", {"start": v(24, -3.66) * mm, "end": v(24.06, -3.66) * mm});
            skLineSegment(sketch, "E3922", {"start": v(24.06, -3.66) * mm, "end": v(24.12, -3.65) * mm});
            skLineSegment(sketch, "E3923", {"start": v(24.12, -3.65) * mm, "end": v(24.17, -3.64) * mm});
            skLineSegment(sketch, "E3924", {"start": v(24.17, -3.64) * mm, "end": v(24.23, -3.63) * mm});
            skLineSegment(sketch, "E3925", {"start": v(24.23, -3.63) * mm, "end": v(24.3, -3.62) * mm});
            skLineSegment(sketch, "E3926", {"start": v(24.3, -3.62) * mm, "end": v(24.36, -3.61) * mm});
            skLineSegment(sketch, "E3927", {"start": v(24.36, -3.61) * mm, "end": v(24.42, -3.6) * mm});
            skLineSegment(sketch, "E3928", {"start": v(24.42, -3.6) * mm, "end": v(24.49, -3.6) * mm});
            skLineSegment(sketch, "E3929", {"start": v(24.49, -3.6) * mm, "end": v(24.56, -3.58) * mm});
            skLineSegment(sketch, "E3930", {"start": v(24.56, -3.58) * mm, "end": v(24.63, -3.57) * mm});
            skLineSegment(sketch, "E3931", {"start": v(24.63, -3.57) * mm, "end": v(24.7, -3.55) * mm});
            skLineSegment(sketch, "E3932", {"start": v(24.7, -3.55) * mm, "end": v(24.77, -3.54) * mm});
            skLineSegment(sketch, "E3933", {"start": v(24.77, -3.54) * mm, "end": v(24.84, -3.52) * mm});
            skLineSegment(sketch, "E3934", {"start": v(24.84, -3.52) * mm, "end": v(24.92, -3.5) * mm});
            skLineSegment(sketch, "E3935", {"start": v(24.92, -3.5) * mm, "end": v(25, -3.49) * mm});
            skLineSegment(sketch, "E3936", {"start": v(25, -3.49) * mm, "end": v(25.08, -3.47) * mm});
            skLineSegment(sketch, "E3937", {"start": v(25.08, -3.47) * mm, "end": v(25.16, -3.45) * mm});
            skLineSegment(sketch, "E3938", {"start": v(25.16, -3.45) * mm, "end": v(25.24, -3.42) * mm});
            skLineSegment(sketch, "E3939", {"start": v(25.24, -3.42) * mm, "end": v(25.32, -3.4) * mm});
            skLineSegment(sketch, "E3940", {"start": v(25.32, -3.4) * mm, "end": v(25.4, -3.38) * mm});
            skLineSegment(sketch, "E3941", {"start": v(25.4, -3.38) * mm, "end": v(25.5, -3.35) * mm});
            skLineSegment(sketch, "E3942", {"start": v(25.5, -3.35) * mm, "end": v(25.58, -3.33) * mm});
            skLineSegment(sketch, "E3943", {"start": v(25.58, -3.33) * mm, "end": v(25.67, -3.3) * mm});
            skLineSegment(sketch, "E3944", {"start": v(25.67, -3.3) * mm, "end": v(25.76, -3.27) * mm});
            skLineSegment(sketch, "E3945", {"start": v(25.76, -3.27) * mm, "end": v(25.86, -3.24) * mm});
            skLineSegment(sketch, "E3946", {"start": v(25.86, -3.24) * mm, "end": v(25.95, -3.2) * mm});
            skLineSegment(sketch, "E3947", {"start": v(25.95, -3.2) * mm, "end": v(26.05, -3.17) * mm});
            skLineSegment(sketch, "E3948", {"start": v(26.05, -3.17) * mm, "end": v(26.06, -3.13) * mm});
            skLineSegment(sketch, "E3949", {"start": v(26.06, -3.13) * mm, "end": v(26.15, -2.3) * mm});
            skLineSegment(sketch, "E3950", {"start": v(26.15, -2.3) * mm, "end": v(26.14, -2.25) * mm});
            skLineSegment(sketch, "E3951", {"start": v(26.14, -2.25) * mm, "end": v(26.05, -2.2) * mm});
            skLineSegment(sketch, "E3952", {"start": v(26.05, -2.2) * mm, "end": v(25.97, -2.15) * mm});
            skLineSegment(sketch, "E3953", {"start": v(25.97, -2.15) * mm, "end": v(25.88, -2.1) * mm});
            skLineSegment(sketch, "E3954", {"start": v(25.88, -2.1) * mm, "end": v(25.8, -2.05) * mm});
            skLineSegment(sketch, "E3955", {"start": v(25.8, -2.05) * mm, "end": v(25.72, -2) * mm});
            skLineSegment(sketch, "E3956", {"start": v(25.72, -2) * mm, "end": v(25.64, -1.96) * mm});
            skLineSegment(sketch, "E3957", {"start": v(25.64, -1.96) * mm, "end": v(25.56, -1.92) * mm});
            skLineSegment(sketch, "E3958", {"start": v(25.56, -1.92) * mm, "end": v(25.48, -1.88) * mm});
            skLineSegment(sketch, "E3959", {"start": v(25.48, -1.88) * mm, "end": v(25.4, -1.84) * mm});
            skLineSegment(sketch, "E3960", {"start": v(25.4, -1.84) * mm, "end": v(25.33, -1.8) * mm});
            skLineSegment(sketch, "E3961", {"start": v(25.33, -1.8) * mm, "end": v(25.25, -1.77) * mm});
            skLineSegment(sketch, "E3962", {"start": v(25.25, -1.77) * mm, "end": v(25.18, -1.73) * mm});
            skLineSegment(sketch, "E3963", {"start": v(25.18, -1.73) * mm, "end": v(25.1, -1.7) * mm});
            skLineSegment(sketch, "E3964", {"start": v(25.1, -1.7) * mm, "end": v(25.04, -1.67) * mm});
            skLineSegment(sketch, "E3965", {"start": v(25.04, -1.67) * mm, "end": v(24.97, -1.63) * mm});
            skLineSegment(sketch, "E3966", {"start": v(24.97, -1.63) * mm, "end": v(24.9, -1.6) * mm});
            skLineSegment(sketch, "E3967", {"start": v(24.9, -1.6) * mm, "end": v(24.83, -1.58) * mm});
            skLineSegment(sketch, "E3968", {"start": v(24.83, -1.58) * mm, "end": v(24.77, -1.55) * mm});
            skLineSegment(sketch, "E3969", {"start": v(24.77, -1.55) * mm, "end": v(24.7, -1.52) * mm});
            skLineSegment(sketch, "E3970", {"start": v(24.7, -1.52) * mm, "end": v(24.64, -1.5) * mm});
            skLineSegment(sketch, "E3971", {"start": v(24.64, -1.5) * mm, "end": v(24.58, -1.47) * mm});
            skLineSegment(sketch, "E3972", {"start": v(24.58, -1.47) * mm, "end": v(24.52, -1.45) * mm});
            skLineSegment(sketch, "E3973", {"start": v(24.52, -1.45) * mm, "end": v(24.46, -1.43) * mm});
            skLineSegment(sketch, "E3974", {"start": v(24.46, -1.43) * mm, "end": v(24.4, -1.41) * mm});
            skLineSegment(sketch, "E3975", {"start": v(24.4, -1.41) * mm, "end": v(24.35, -1.4) * mm});
            skLineSegment(sketch, "E3976", {"start": v(24.35, -1.4) * mm, "end": v(24.3, -1.37) * mm});
            skLineSegment(sketch, "E3977", {"start": v(24.3, -1.37) * mm, "end": v(24.25, -1.36) * mm});
            skLineSegment(sketch, "E3978", {"start": v(24.25, -1.36) * mm, "end": v(24.2, -1.34) * mm});
            skLineSegment(sketch, "E3979", {"start": v(24.2, -1.34) * mm, "end": v(24.15, -1.33) * mm});
            skLineSegment(sketch, "E3980", {"start": v(24.15, -1.33) * mm, "end": v(24.1, -1.31) * mm});
            skLineSegment(sketch, "E3981", {"start": v(24.1, -1.31) * mm, "end": v(24.05, -1.3) * mm});
            skLineSegment(sketch, "E3982", {"start": v(24.05, -1.3) * mm, "end": v(24.01, -1.29) * mm});
            skLineSegment(sketch, "E3983", {"start": v(24.01, -1.29) * mm, "end": v(23.97, -1.27) * mm});
            skLineSegment(sketch, "E3984", {"start": v(23.97, -1.27) * mm, "end": v(23.93, -1.26) * mm});
            skLineSegment(sketch, "E3985", {"start": v(23.93, -1.26) * mm, "end": v(23.89, -1.25) * mm});
            skLineSegment(sketch, "E3986", {"start": v(23.89, -1.25) * mm, "end": v(23.85, -1.25) * mm});
            skLineSegment(sketch, "E3987", {"start": v(23.85, -1.25) * mm, "end": v(23.82, -1.24) * mm});
            skLineSegment(sketch, "E3988", {"start": v(23.82, -1.24) * mm, "end": v(23.78, -1.23) * mm});
            skLineSegment(sketch, "E3989", {"start": v(23.78, -1.23) * mm, "end": v(23.75, -1.22) * mm});
            skLineSegment(sketch, "E3990", {"start": v(23.75, -1.22) * mm, "end": v(23.72, -1.22) * mm});
            skLineSegment(sketch, "E3991", {"start": v(23.72, -1.22) * mm, "end": v(23.69, -1.21) * mm});
            skLineSegment(sketch, "E3992", {"start": v(23.69, -1.21) * mm, "end": v(23.66, -1.2) * mm});
            skLineSegment(sketch, "E3993", {"start": v(23.66, -1.2) * mm, "end": v(23.64, -1.2) * mm});
            skLineSegment(sketch, "E3994", {"start": v(23.64, -1.2) * mm, "end": v(23.61, -1.2) * mm});
            skLineSegment(sketch, "E3995", {"start": v(23.61, -1.2) * mm, "end": v(23.6, -1.2) * mm});
            skLineSegment(sketch, "E3996", {"start": v(23.6, -1.2) * mm, "end": v(23.57, -1.2) * mm});
            skLineSegment(sketch, "E3997", {"start": v(23.57, -1.2) * mm, "end": v(23.55, -1.19) * mm});
            skLineSegment(sketch, "E3998", {"start": v(23.55, -1.19) * mm, "end": v(23.53, -1.18) * mm});
            skLineSegment(sketch, "E3999", {"start": v(23.53, -1.18) * mm, "end": v(23.56, 0) * mm});
            skSolve(sketch);
        }
        {
            var Q0;
            Q0=makeQuery(id+"F0.imprint","IMPRINT",FACE,{"disambiguationData":[TD([[makeQuery(id+"F0.imprint","IMPRINT",EDGE,{"derivedFrom":sQuery(id+"F0.wireOp",EDGE,"E0")}),1.0]])]});
            extrude(context, id + "F1", {"entities" : qUnion([Q0]), "depth" : 9 * mm});
        }
        {
            var Q0;
            Q0=qCreatedBy(makeId("Top.planeOp"),FACE);
            var sketch = newSketch(context, id + "F2", { "sketchPlane" : qUnion([Q0])});
            skCircle(sketch, "E4000", {"center": v(0, 0) * mm, "radius": 0.95 * mm});
            skSolve(sketch);
        }
        {
            var Q0;
            Q0=qSketchRegion(id+"F2",true);
            extrude(context, id + "F3", {"entities" : qUnion([Q0]), "operationType" : NewBodyOperationType.REMOVE, "endBound" : BoundingType.THROUGH_ALL, "depth" : 25 * mm});
        }
        {
            var Q0;
            Q0=makeQuery(id+"F1.opExtrude","CAP_FACE",FACE,{"disambiguationData":[OSD([sQuery(id+"F0.wireOp",EDGE,"E0"),sQuery(id+"F0.wireOp",EDGE,"E1"),sQuery(id+"F0.wireOp",EDGE,"E2"),sQuery(id+"F0.wireOp",EDGE,"E3"),sQuery(id+"F0.wireOp",EDGE,"E4"),sQuery(id+"F0.wireOp",EDGE,"E5"),sQuery(id+"F0.wireOp",EDGE,"E6"),sQuery(id+"F0.wireOp",EDGE,"E7"),sQuery(id+"F0.wireOp",EDGE,"E8"),sQuery(id+"F0.wireOp",EDGE,"E9"),sQuery(id+"F0.wireOp",EDGE,"E10"),sQuery(id+"F0.wireOp",EDGE,"E11"),sQuery(id+"F0.wireOp",EDGE,"E12"),sQuery(id+"F0.wireOp",EDGE,"E13"),sQuery(id+"F0.wireOp",EDGE,"E14"),sQuery(id+"F0.wireOp",EDGE,"E15"),sQuery(id+"F0.wireOp",EDGE,"E16"),sQuery(id+"F0.wireOp",EDGE,"E17"),sQuery(id+"F0.wireOp",EDGE,"E18"),sQuery(id+"F0.wireOp",EDGE,"E19"),sQuery(id+"F0.wireOp",EDGE,"E20"),sQuery(id+"F0.wireOp",EDGE,"E21"),sQuery(id+"F0.wireOp",EDGE,"E22"),sQuery(id+"F0.wireOp",EDGE,"E23"),sQuery(id+"F0.wireOp",EDGE,"E24"),sQuery(id+"F0.wireOp",EDGE,"E25"),sQuery(id+"F0.wireOp",EDGE,"E26"),sQuery(id+"F0.wireOp",EDGE,"E27"),sQuery(id+"F0.wireOp",EDGE,"E28"),sQuery(id+"F0.wireOp",EDGE,"E29"),sQuery(id+"F0.wireOp",EDGE,"E30"),sQuery(id+"F0.wireOp",EDGE,"E31"),sQuery(id+"F0.wireOp",EDGE,"E32"),sQuery(id+"F0.wireOp",EDGE,"E33"),sQuery(id+"F0.wireOp",EDGE,"E34"),sQuery(id+"F0.wireOp",EDGE,"E35"),sQuery(id+"F0.wireOp",EDGE,"E36"),sQuery(id+"F0.wireOp",EDGE,"E37"),sQuery(id+"F0.wireOp",EDGE,"E38"),sQuery(id+"F0.wireOp",EDGE,"E39"),sQuery(id+"F0.wireOp",EDGE,"E40"),sQuery(id+"F0.wireOp",EDGE,"E41"),sQuery(id+"F0.wireOp",EDGE,"E42"),sQuery(id+"F0.wireOp",EDGE,"E43"),sQuery(id+"F0.wireOp",EDGE,"E44"),sQuery(id+"F0.wireOp",EDGE,"E45"),sQuery(id+"F0.wireOp",EDGE,"E46"),sQuery(id+"F0.wireOp",EDGE,"E47"),sQuery(id+"F0.wireOp",EDGE,"E48"),sQuery(id+"F0.wireOp",EDGE,"E49"),sQuery(id+"F0.wireOp",EDGE,"E50"),sQuery(id+"F0.wireOp",EDGE,"E51"),sQuery(id+"F0.wireOp",EDGE,"E52"),sQuery(id+"F0.wireOp",EDGE,"E53"),sQuery(id+"F0.wireOp",EDGE,"E54"),sQuery(id+"F0.wireOp",EDGE,"E55"),sQuery(id+"F0.wireOp",EDGE,"E56"),sQuery(id+"F0.wireOp",EDGE,"E57"),sQuery(id+"F0.wireOp",EDGE,"E58"),sQuery(id+"F0.wireOp",EDGE,"E59"),sQuery(id+"F0.wireOp",EDGE,"E60"),sQuery(id+"F0.wireOp",EDGE,"E61"),sQuery(id+"F0.wireOp",EDGE,"E62"),sQuery(id+"F0.wireOp",EDGE,"E63"),sQuery(id+"F0.wireOp",EDGE,"E64"),sQuery(id+"F0.wireOp",EDGE,"E65"),sQuery(id+"F0.wireOp",EDGE,"E66"),sQuery(id+"F0.wireOp",EDGE,"E67"),sQuery(id+"F0.wireOp",EDGE,"E68"),sQuery(id+"F0.wireOp",EDGE,"E69"),sQuery(id+"F0.wireOp",EDGE,"E70"),sQuery(id+"F0.wireOp",EDGE,"E71"),sQuery(id+"F0.wireOp",EDGE,"E72"),sQuery(id+"F0.wireOp",EDGE,"E73"),sQuery(id+"F0.wireOp",EDGE,"E74"),sQuery(id+"F0.wireOp",EDGE,"E75"),sQuery(id+"F0.wireOp",EDGE,"E76"),sQuery(id+"F0.wireOp",EDGE,"E77"),sQuery(id+"F0.wireOp",EDGE,"E78"),sQuery(id+"F0.wireOp",EDGE,"E79"),sQuery(id+"F0.wireOp",EDGE,"E80"),sQuery(id+"F0.wireOp",EDGE,"E81"),sQuery(id+"F0.wireOp",EDGE,"E82"),sQuery(id+"F0.wireOp",EDGE,"E83"),sQuery(id+"F0.wireOp",EDGE,"E84"),sQuery(id+"F0.wireOp",EDGE,"E85"),sQuery(id+"F0.wireOp",EDGE,"E86"),sQuery(id+"F0.wireOp",EDGE,"E87"),sQuery(id+"F0.wireOp",EDGE,"E88"),sQuery(id+"F0.wireOp",EDGE,"E89"),sQuery(id+"F0.wireOp",EDGE,"E90"),sQuery(id+"F0.wireOp",EDGE,"E91"),sQuery(id+"F0.wireOp",EDGE,"E92"),sQuery(id+"F0.wireOp",EDGE,"E93"),sQuery(id+"F0.wireOp",EDGE,"E94"),sQuery(id+"F0.wireOp",EDGE,"E95"),sQuery(id+"F0.wireOp",EDGE,"E96"),sQuery(id+"F0.wireOp",EDGE,"E97"),sQuery(id+"F0.wireOp",EDGE,"E98"),sQuery(id+"F0.wireOp",EDGE,"E99"),sQuery(id+"F0.wireOp",EDGE,"E100"),sQuery(id+"F0.wireOp",EDGE,"E101"),sQuery(id+"F0.wireOp",EDGE,"E102"),sQuery(id+"F0.wireOp",EDGE,"E103"),sQuery(id+"F0.wireOp",EDGE,"E104"),sQuery(id+"F0.wireOp",EDGE,"E105"),sQuery(id+"F0.wireOp",EDGE,"E106"),sQuery(id+"F0.wireOp",EDGE,"E107"),sQuery(id+"F0.wireOp",EDGE,"E108"),sQuery(id+"F0.wireOp",EDGE,"E109"),sQuery(id+"F0.wireOp",EDGE,"E110"),sQuery(id+"F0.wireOp",EDGE,"E111"),sQuery(id+"F0.wireOp",EDGE,"E112"),sQuery(id+"F0.wireOp",EDGE,"E113"),sQuery(id+"F0.wireOp",EDGE,"E114"),sQuery(id+"F0.wireOp",EDGE,"E115"),sQuery(id+"F0.wireOp",EDGE,"E116"),sQuery(id+"F0.wireOp",EDGE,"E117"),sQuery(id+"F0.wireOp",EDGE,"E118"),sQuery(id+"F0.wireOp",EDGE,"E119"),sQuery(id+"F0.wireOp",EDGE,"E120"),sQuery(id+"F0.wireOp",EDGE,"E121"),sQuery(id+"F0.wireOp",EDGE,"E122"),sQuery(id+"F0.wireOp",EDGE,"E123"),sQuery(id+"F0.wireOp",EDGE,"E124"),sQuery(id+"F0.wireOp",EDGE,"E125"),sQuery(id+"F0.wireOp",EDGE,"E126"),sQuery(id+"F0.wireOp",EDGE,"E127"),sQuery(id+"F0.wireOp",EDGE,"E128"),sQuery(id+"F0.wireOp",EDGE,"E129"),sQuery(id+"F0.wireOp",EDGE,"E130"),sQuery(id+"F0.wireOp",EDGE,"E131"),sQuery(id+"F0.wireOp",EDGE,"E132"),sQuery(id+"F0.wireOp",EDGE,"E133"),sQuery(id+"F0.wireOp",EDGE,"E134"),sQuery(id+"F0.wireOp",EDGE,"E135"),sQuery(id+"F0.wireOp",EDGE,"E136"),sQuery(id+"F0.wireOp",EDGE,"E137"),sQuery(id+"F0.wireOp",EDGE,"E138"),sQuery(id+"F0.wireOp",EDGE,"E139"),sQuery(id+"F0.wireOp",EDGE,"E140"),sQuery(id+"F0.wireOp",EDGE,"E141"),sQuery(id+"F0.wireOp",EDGE,"E142"),sQuery(id+"F0.wireOp",EDGE,"E143"),sQuery(id+"F0.wireOp",EDGE,"E144"),sQuery(id+"F0.wireOp",EDGE,"E145"),sQuery(id+"F0.wireOp",EDGE,"E146"),sQuery(id+"F0.wireOp",EDGE,"E147"),sQuery(id+"F0.wireOp",EDGE,"E148"),sQuery(id+"F0.wireOp",EDGE,"E149"),sQuery(id+"F0.wireOp",EDGE,"E150"),sQuery(id+"F0.wireOp",EDGE,"E151"),sQuery(id+"F0.wireOp",EDGE,"E152"),sQuery(id+"F0.wireOp",EDGE,"E153"),sQuery(id+"F0.wireOp",EDGE,"E154"),sQuery(id+"F0.wireOp",EDGE,"E155"),sQuery(id+"F0.wireOp",EDGE,"E156"),sQuery(id+"F0.wireOp",EDGE,"E157"),sQuery(id+"F0.wireOp",EDGE,"E158"),sQuery(id+"F0.wireOp",EDGE,"E159"),sQuery(id+"F0.wireOp",EDGE,"E160"),sQuery(id+"F0.wireOp",EDGE,"E161"),sQuery(id+"F0.wireOp",EDGE,"E162"),sQuery(id+"F0.wireOp",EDGE,"E163"),sQuery(id+"F0.wireOp",EDGE,"E164"),sQuery(id+"F0.wireOp",EDGE,"E165"),sQuery(id+"F0.wireOp",EDGE,"E166"),sQuery(id+"F0.wireOp",EDGE,"E167"),sQuery(id+"F0.wireOp",EDGE,"E168"),sQuery(id+"F0.wireOp",EDGE,"E169"),sQuery(id+"F0.wireOp",EDGE,"E170"),sQuery(id+"F0.wireOp",EDGE,"E171"),sQuery(id+"F0.wireOp",EDGE,"E172"),sQuery(id+"F0.wireOp",EDGE,"E173"),sQuery(id+"F0.wireOp",EDGE,"E174"),sQuery(id+"F0.wireOp",EDGE,"E175"),sQuery(id+"F0.wireOp",EDGE,"E176"),sQuery(id+"F0.wireOp",EDGE,"E177"),sQuery(id+"F0.wireOp",EDGE,"E178"),sQuery(id+"F0.wireOp",EDGE,"E179"),sQuery(id+"F0.wireOp",EDGE,"E180"),sQuery(id+"F0.wireOp",EDGE,"E181"),sQuery(id+"F0.wireOp",EDGE,"E182"),sQuery(id+"F0.wireOp",EDGE,"E183"),sQuery(id+"F0.wireOp",EDGE,"E184"),sQuery(id+"F0.wireOp",EDGE,"E185"),sQuery(id+"F0.wireOp",EDGE,"E186"),sQuery(id+"F0.wireOp",EDGE,"E187"),sQuery(id+"F0.wireOp",EDGE,"E188"),sQuery(id+"F0.wireOp",EDGE,"E189"),sQuery(id+"F0.wireOp",EDGE,"E190"),sQuery(id+"F0.wireOp",EDGE,"E191"),sQuery(id+"F0.wireOp",EDGE,"E192"),sQuery(id+"F0.wireOp",EDGE,"E193"),sQuery(id+"F0.wireOp",EDGE,"E194"),sQuery(id+"F0.wireOp",EDGE,"E195"),sQuery(id+"F0.wireOp",EDGE,"E196"),sQuery(id+"F0.wireOp",EDGE,"E197"),sQuery(id+"F0.wireOp",EDGE,"E198"),sQuery(id+"F0.wireOp",EDGE,"E199"),sQuery(id+"F0.wireOp",EDGE,"E200"),sQuery(id+"F0.wireOp",EDGE,"E201"),sQuery(id+"F0.wireOp",EDGE,"E202"),sQuery(id+"F0.wireOp",EDGE,"E203"),sQuery(id+"F0.wireOp",EDGE,"E204"),sQuery(id+"F0.wireOp",EDGE,"E205"),sQuery(id+"F0.wireOp",EDGE,"E206"),sQuery(id+"F0.wireOp",EDGE,"E207"),sQuery(id+"F0.wireOp",EDGE,"E208"),sQuery(id+"F0.wireOp",EDGE,"E209"),sQuery(id+"F0.wireOp",EDGE,"E210"),sQuery(id+"F0.wireOp",EDGE,"E211"),sQuery(id+"F0.wireOp",EDGE,"E212"),sQuery(id+"F0.wireOp",EDGE,"E213"),sQuery(id+"F0.wireOp",EDGE,"E214"),sQuery(id+"F0.wireOp",EDGE,"E215"),sQuery(id+"F0.wireOp",EDGE,"E216"),sQuery(id+"F0.wireOp",EDGE,"E217"),sQuery(id+"F0.wireOp",EDGE,"E218"),sQuery(id+"F0.wireOp",EDGE,"E219"),sQuery(id+"F0.wireOp",EDGE,"E220"),sQuery(id+"F0.wireOp",EDGE,"E221"),sQuery(id+"F0.wireOp",EDGE,"E222"),sQuery(id+"F0.wireOp",EDGE,"E223"),sQuery(id+"F0.wireOp",EDGE,"E224"),sQuery(id+"F0.wireOp",EDGE,"E225"),sQuery(id+"F0.wireOp",EDGE,"E226"),sQuery(id+"F0.wireOp",EDGE,"E227"),sQuery(id+"F0.wireOp",EDGE,"E228"),sQuery(id+"F0.wireOp",EDGE,"E229"),sQuery(id+"F0.wireOp",EDGE,"E230"),sQuery(id+"F0.wireOp",EDGE,"E231"),sQuery(id+"F0.wireOp",EDGE,"E232"),sQuery(id+"F0.wireOp",EDGE,"E233"),sQuery(id+"F0.wireOp",EDGE,"E234"),sQuery(id+"F0.wireOp",EDGE,"E235"),sQuery(id+"F0.wireOp",EDGE,"E236"),sQuery(id+"F0.wireOp",EDGE,"E237"),sQuery(id+"F0.wireOp",EDGE,"E238"),sQuery(id+"F0.wireOp",EDGE,"E239"),sQuery(id+"F0.wireOp",EDGE,"E240"),sQuery(id+"F0.wireOp",EDGE,"E241"),sQuery(id+"F0.wireOp",EDGE,"E242"),sQuery(id+"F0.wireOp",EDGE,"E243"),sQuery(id+"F0.wireOp",EDGE,"E244"),sQuery(id+"F0.wireOp",EDGE,"E245"),sQuery(id+"F0.wireOp",EDGE,"E246"),sQuery(id+"F0.wireOp",EDGE,"E247"),sQuery(id+"F0.wireOp",EDGE,"E248"),sQuery(id+"F0.wireOp",EDGE,"E249"),sQuery(id+"F0.wireOp",EDGE,"E250"),sQuery(id+"F0.wireOp",EDGE,"E251"),sQuery(id+"F0.wireOp",EDGE,"E252"),sQuery(id+"F0.wireOp",EDGE,"E253"),sQuery(id+"F0.wireOp",EDGE,"E254"),sQuery(id+"F0.wireOp",EDGE,"E255"),sQuery(id+"F0.wireOp",EDGE,"E256"),sQuery(id+"F0.wireOp",EDGE,"E257"),sQuery(id+"F0.wireOp",EDGE,"E258"),sQuery(id+"F0.wireOp",EDGE,"E259"),sQuery(id+"F0.wireOp",EDGE,"E260"),sQuery(id+"F0.wireOp",EDGE,"E261"),sQuery(id+"F0.wireOp",EDGE,"E262"),sQuery(id+"F0.wireOp",EDGE,"E263"),sQuery(id+"F0.wireOp",EDGE,"E264"),sQuery(id+"F0.wireOp",EDGE,"E265"),sQuery(id+"F0.wireOp",EDGE,"E266"),sQuery(id+"F0.wireOp",EDGE,"E267"),sQuery(id+"F0.wireOp",EDGE,"E268"),sQuery(id+"F0.wireOp",EDGE,"E269"),sQuery(id+"F0.wireOp",EDGE,"E270"),sQuery(id+"F0.wireOp",EDGE,"E271"),sQuery(id+"F0.wireOp",EDGE,"E272"),sQuery(id+"F0.wireOp",EDGE,"E273"),sQuery(id+"F0.wireOp",EDGE,"E274"),sQuery(id+"F0.wireOp",EDGE,"E275"),sQuery(id+"F0.wireOp",EDGE,"E276"),sQuery(id+"F0.wireOp",EDGE,"E277"),sQuery(id+"F0.wireOp",EDGE,"E278"),sQuery(id+"F0.wireOp",EDGE,"E279"),sQuery(id+"F0.wireOp",EDGE,"E280"),sQuery(id+"F0.wireOp",EDGE,"E281"),sQuery(id+"F0.wireOp",EDGE,"E282"),sQuery(id+"F0.wireOp",EDGE,"E283"),sQuery(id+"F0.wireOp",EDGE,"E284"),sQuery(id+"F0.wireOp",EDGE,"E285"),sQuery(id+"F0.wireOp",EDGE,"E286"),sQuery(id+"F0.wireOp",EDGE,"E287"),sQuery(id+"F0.wireOp",EDGE,"E288"),sQuery(id+"F0.wireOp",EDGE,"E289"),sQuery(id+"F0.wireOp",EDGE,"E290"),sQuery(id+"F0.wireOp",EDGE,"E291"),sQuery(id+"F0.wireOp",EDGE,"E292"),sQuery(id+"F0.wireOp",EDGE,"E293"),sQuery(id+"F0.wireOp",EDGE,"E294"),sQuery(id+"F0.wireOp",EDGE,"E295"),sQuery(id+"F0.wireOp",EDGE,"E296"),sQuery(id+"F0.wireOp",EDGE,"E297"),sQuery(id+"F0.wireOp",EDGE,"E298"),sQuery(id+"F0.wireOp",EDGE,"E299"),sQuery(id+"F0.wireOp",EDGE,"E300"),sQuery(id+"F0.wireOp",EDGE,"E301"),sQuery(id+"F0.wireOp",EDGE,"E302"),sQuery(id+"F0.wireOp",EDGE,"E303"),sQuery(id+"F0.wireOp",EDGE,"E304"),sQuery(id+"F0.wireOp",EDGE,"E305"),sQuery(id+"F0.wireOp",EDGE,"E306"),sQuery(id+"F0.wireOp",EDGE,"E307"),sQuery(id+"F0.wireOp",EDGE,"E308"),sQuery(id+"F0.wireOp",EDGE,"E309"),sQuery(id+"F0.wireOp",EDGE,"E310"),sQuery(id+"F0.wireOp",EDGE,"E311"),sQuery(id+"F0.wireOp",EDGE,"E312"),sQuery(id+"F0.wireOp",EDGE,"E313"),sQuery(id+"F0.wireOp",EDGE,"E314"),sQuery(id+"F0.wireOp",EDGE,"E315"),sQuery(id+"F0.wireOp",EDGE,"E316"),sQuery(id+"F0.wireOp",EDGE,"E317"),sQuery(id+"F0.wireOp",EDGE,"E318"),sQuery(id+"F0.wireOp",EDGE,"E319"),sQuery(id+"F0.wireOp",EDGE,"E320"),sQuery(id+"F0.wireOp",EDGE,"E321"),sQuery(id+"F0.wireOp",EDGE,"E322"),sQuery(id+"F0.wireOp",EDGE,"E323"),sQuery(id+"F0.wireOp",EDGE,"E324"),sQuery(id+"F0.wireOp",EDGE,"E325"),sQuery(id+"F0.wireOp",EDGE,"E326"),sQuery(id+"F0.wireOp",EDGE,"E327"),sQuery(id+"F0.wireOp",EDGE,"E328"),sQuery(id+"F0.wireOp",EDGE,"E329"),sQuery(id+"F0.wireOp",EDGE,"E330"),sQuery(id+"F0.wireOp",EDGE,"E331"),sQuery(id+"F0.wireOp",EDGE,"E332"),sQuery(id+"F0.wireOp",EDGE,"E333"),sQuery(id+"F0.wireOp",EDGE,"E334"),sQuery(id+"F0.wireOp",EDGE,"E335"),sQuery(id+"F0.wireOp",EDGE,"E336"),sQuery(id+"F0.wireOp",EDGE,"E337"),sQuery(id+"F0.wireOp",EDGE,"E338"),sQuery(id+"F0.wireOp",EDGE,"E339"),sQuery(id+"F0.wireOp",EDGE,"E340"),sQuery(id+"F0.wireOp",EDGE,"E341"),sQuery(id+"F0.wireOp",EDGE,"E342"),sQuery(id+"F0.wireOp",EDGE,"E343"),sQuery(id+"F0.wireOp",EDGE,"E344"),sQuery(id+"F0.wireOp",EDGE,"E345"),sQuery(id+"F0.wireOp",EDGE,"E346"),sQuery(id+"F0.wireOp",EDGE,"E347"),sQuery(id+"F0.wireOp",EDGE,"E348"),sQuery(id+"F0.wireOp",EDGE,"E349"),sQuery(id+"F0.wireOp",EDGE,"E350"),sQuery(id+"F0.wireOp",EDGE,"E351"),sQuery(id+"F0.wireOp",EDGE,"E352"),sQuery(id+"F0.wireOp",EDGE,"E353"),sQuery(id+"F0.wireOp",EDGE,"E354"),sQuery(id+"F0.wireOp",EDGE,"E355"),sQuery(id+"F0.wireOp",EDGE,"E356"),sQuery(id+"F0.wireOp",EDGE,"E357"),sQuery(id+"F0.wireOp",EDGE,"E358"),sQuery(id+"F0.wireOp",EDGE,"E359"),sQuery(id+"F0.wireOp",EDGE,"E360"),sQuery(id+"F0.wireOp",EDGE,"E361"),sQuery(id+"F0.wireOp",EDGE,"E362"),sQuery(id+"F0.wireOp",EDGE,"E363"),sQuery(id+"F0.wireOp",EDGE,"E364"),sQuery(id+"F0.wireOp",EDGE,"E365"),sQuery(id+"F0.wireOp",EDGE,"E366"),sQuery(id+"F0.wireOp",EDGE,"E367"),sQuery(id+"F0.wireOp",EDGE,"E368"),sQuery(id+"F0.wireOp",EDGE,"E369"),sQuery(id+"F0.wireOp",EDGE,"E370"),sQuery(id+"F0.wireOp",EDGE,"E371"),sQuery(id+"F0.wireOp",EDGE,"E372"),sQuery(id+"F0.wireOp",EDGE,"E373"),sQuery(id+"F0.wireOp",EDGE,"E374"),sQuery(id+"F0.wireOp",EDGE,"E375"),sQuery(id+"F0.wireOp",EDGE,"E376"),sQuery(id+"F0.wireOp",EDGE,"E377"),sQuery(id+"F0.wireOp",EDGE,"E378"),sQuery(id+"F0.wireOp",EDGE,"E379"),sQuery(id+"F0.wireOp",EDGE,"E380"),sQuery(id+"F0.wireOp",EDGE,"E381"),sQuery(id+"F0.wireOp",EDGE,"E382"),sQuery(id+"F0.wireOp",EDGE,"E383"),sQuery(id+"F0.wireOp",EDGE,"E384"),sQuery(id+"F0.wireOp",EDGE,"E385"),sQuery(id+"F0.wireOp",EDGE,"E386"),sQuery(id+"F0.wireOp",EDGE,"E387"),sQuery(id+"F0.wireOp",EDGE,"E388"),sQuery(id+"F0.wireOp",EDGE,"E389"),sQuery(id+"F0.wireOp",EDGE,"E390"),sQuery(id+"F0.wireOp",EDGE,"E391"),sQuery(id+"F0.wireOp",EDGE,"E392"),sQuery(id+"F0.wireOp",EDGE,"E393"),sQuery(id+"F0.wireOp",EDGE,"E394"),sQuery(id+"F0.wireOp",EDGE,"E395"),sQuery(id+"F0.wireOp",EDGE,"E396"),sQuery(id+"F0.wireOp",EDGE,"E397"),sQuery(id+"F0.wireOp",EDGE,"E398"),sQuery(id+"F0.wireOp",EDGE,"E399"),sQuery(id+"F0.wireOp",EDGE,"E400"),sQuery(id+"F0.wireOp",EDGE,"E401"),sQuery(id+"F0.wireOp",EDGE,"E402"),sQuery(id+"F0.wireOp",EDGE,"E403"),sQuery(id+"F0.wireOp",EDGE,"E404"),sQuery(id+"F0.wireOp",EDGE,"E405"),sQuery(id+"F0.wireOp",EDGE,"E406"),sQuery(id+"F0.wireOp",EDGE,"E407"),sQuery(id+"F0.wireOp",EDGE,"E408"),sQuery(id+"F0.wireOp",EDGE,"E409"),sQuery(id+"F0.wireOp",EDGE,"E410"),sQuery(id+"F0.wireOp",EDGE,"E411"),sQuery(id+"F0.wireOp",EDGE,"E412"),sQuery(id+"F0.wireOp",EDGE,"E413"),sQuery(id+"F0.wireOp",EDGE,"E414"),sQuery(id+"F0.wireOp",EDGE,"E415"),sQuery(id+"F0.wireOp",EDGE,"E416"),sQuery(id+"F0.wireOp",EDGE,"E417"),sQuery(id+"F0.wireOp",EDGE,"E418"),sQuery(id+"F0.wireOp",EDGE,"E419"),sQuery(id+"F0.wireOp",EDGE,"E420"),sQuery(id+"F0.wireOp",EDGE,"E421"),sQuery(id+"F0.wireOp",EDGE,"E422"),sQuery(id+"F0.wireOp",EDGE,"E423"),sQuery(id+"F0.wireOp",EDGE,"E424"),sQuery(id+"F0.wireOp",EDGE,"E425"),sQuery(id+"F0.wireOp",EDGE,"E426"),sQuery(id+"F0.wireOp",EDGE,"E427"),sQuery(id+"F0.wireOp",EDGE,"E428"),sQuery(id+"F0.wireOp",EDGE,"E429"),sQuery(id+"F0.wireOp",EDGE,"E430"),sQuery(id+"F0.wireOp",EDGE,"E431"),sQuery(id+"F0.wireOp",EDGE,"E432"),sQuery(id+"F0.wireOp",EDGE,"E433"),sQuery(id+"F0.wireOp",EDGE,"E434"),sQuery(id+"F0.wireOp",EDGE,"E435"),sQuery(id+"F0.wireOp",EDGE,"E436"),sQuery(id+"F0.wireOp",EDGE,"E437"),sQuery(id+"F0.wireOp",EDGE,"E438"),sQuery(id+"F0.wireOp",EDGE,"E439"),sQuery(id+"F0.wireOp",EDGE,"E440"),sQuery(id+"F0.wireOp",EDGE,"E441"),sQuery(id+"F0.wireOp",EDGE,"E442"),sQuery(id+"F0.wireOp",EDGE,"E443"),sQuery(id+"F0.wireOp",EDGE,"E444"),sQuery(id+"F0.wireOp",EDGE,"E445"),sQuery(id+"F0.wireOp",EDGE,"E446"),sQuery(id+"F0.wireOp",EDGE,"E447"),sQuery(id+"F0.wireOp",EDGE,"E448"),sQuery(id+"F0.wireOp",EDGE,"E449"),sQuery(id+"F0.wireOp",EDGE,"E450"),sQuery(id+"F0.wireOp",EDGE,"E451"),sQuery(id+"F0.wireOp",EDGE,"E452"),sQuery(id+"F0.wireOp",EDGE,"E453"),sQuery(id+"F0.wireOp",EDGE,"E454"),sQuery(id+"F0.wireOp",EDGE,"E455"),sQuery(id+"F0.wireOp",EDGE,"E456"),sQuery(id+"F0.wireOp",EDGE,"E457"),sQuery(id+"F0.wireOp",EDGE,"E458"),sQuery(id+"F0.wireOp",EDGE,"E459"),sQuery(id+"F0.wireOp",EDGE,"E460"),sQuery(id+"F0.wireOp",EDGE,"E461"),sQuery(id+"F0.wireOp",EDGE,"E462"),sQuery(id+"F0.wireOp",EDGE,"E463"),sQuery(id+"F0.wireOp",EDGE,"E464"),sQuery(id+"F0.wireOp",EDGE,"E465"),sQuery(id+"F0.wireOp",EDGE,"E466"),sQuery(id+"F0.wireOp",EDGE,"E467"),sQuery(id+"F0.wireOp",EDGE,"E468"),sQuery(id+"F0.wireOp",EDGE,"E469"),sQuery(id+"F0.wireOp",EDGE,"E470"),sQuery(id+"F0.wireOp",EDGE,"E471"),sQuery(id+"F0.wireOp",EDGE,"E472"),sQuery(id+"F0.wireOp",EDGE,"E473"),sQuery(id+"F0.wireOp",EDGE,"E474"),sQuery(id+"F0.wireOp",EDGE,"E475"),sQuery(id+"F0.wireOp",EDGE,"E476"),sQuery(id+"F0.wireOp",EDGE,"E477"),sQuery(id+"F0.wireOp",EDGE,"E478"),sQuery(id+"F0.wireOp",EDGE,"E479"),sQuery(id+"F0.wireOp",EDGE,"E480"),sQuery(id+"F0.wireOp",EDGE,"E481"),sQuery(id+"F0.wireOp",EDGE,"E482"),sQuery(id+"F0.wireOp",EDGE,"E483"),sQuery(id+"F0.wireOp",EDGE,"E484"),sQuery(id+"F0.wireOp",EDGE,"E485"),sQuery(id+"F0.wireOp",EDGE,"E486"),sQuery(id+"F0.wireOp",EDGE,"E487"),sQuery(id+"F0.wireOp",EDGE,"E488"),sQuery(id+"F0.wireOp",EDGE,"E489"),sQuery(id+"F0.wireOp",EDGE,"E490"),sQuery(id+"F0.wireOp",EDGE,"E491"),sQuery(id+"F0.wireOp",EDGE,"E492"),sQuery(id+"F0.wireOp",EDGE,"E493"),sQuery(id+"F0.wireOp",EDGE,"E494"),sQuery(id+"F0.wireOp",EDGE,"E495"),sQuery(id+"F0.wireOp",EDGE,"E496"),sQuery(id+"F0.wireOp",EDGE,"E497"),sQuery(id+"F0.wireOp",EDGE,"E498"),sQuery(id+"F0.wireOp",EDGE,"E499"),sQuery(id+"F0.wireOp",EDGE,"E500"),sQuery(id+"F0.wireOp",EDGE,"E501"),sQuery(id+"F0.wireOp",EDGE,"E502"),sQuery(id+"F0.wireOp",EDGE,"E503"),sQuery(id+"F0.wireOp",EDGE,"E504"),sQuery(id+"F0.wireOp",EDGE,"E505"),sQuery(id+"F0.wireOp",EDGE,"E506"),sQuery(id+"F0.wireOp",EDGE,"E507"),sQuery(id+"F0.wireOp",EDGE,"E508"),sQuery(id+"F0.wireOp",EDGE,"E509"),sQuery(id+"F0.wireOp",EDGE,"E510"),sQuery(id+"F0.wireOp",EDGE,"E511"),sQuery(id+"F0.wireOp",EDGE,"E512"),sQuery(id+"F0.wireOp",EDGE,"E513"),sQuery(id+"F0.wireOp",EDGE,"E514"),sQuery(id+"F0.wireOp",EDGE,"E515"),sQuery(id+"F0.wireOp",EDGE,"E516"),sQuery(id+"F0.wireOp",EDGE,"E517"),sQuery(id+"F0.wireOp",EDGE,"E518"),sQuery(id+"F0.wireOp",EDGE,"E519"),sQuery(id+"F0.wireOp",EDGE,"E520"),sQuery(id+"F0.wireOp",EDGE,"E521"),sQuery(id+"F0.wireOp",EDGE,"E522"),sQuery(id+"F0.wireOp",EDGE,"E523"),sQuery(id+"F0.wireOp",EDGE,"E524"),sQuery(id+"F0.wireOp",EDGE,"E525"),sQuery(id+"F0.wireOp",EDGE,"E526"),sQuery(id+"F0.wireOp",EDGE,"E527"),sQuery(id+"F0.wireOp",EDGE,"E528"),sQuery(id+"F0.wireOp",EDGE,"E529"),sQuery(id+"F0.wireOp",EDGE,"E530"),sQuery(id+"F0.wireOp",EDGE,"E531"),sQuery(id+"F0.wireOp",EDGE,"E532"),sQuery(id+"F0.wireOp",EDGE,"E533"),sQuery(id+"F0.wireOp",EDGE,"E534"),sQuery(id+"F0.wireOp",EDGE,"E535"),sQuery(id+"F0.wireOp",EDGE,"E536"),sQuery(id+"F0.wireOp",EDGE,"E537"),sQuery(id+"F0.wireOp",EDGE,"E538"),sQuery(id+"F0.wireOp",EDGE,"E539"),sQuery(id+"F0.wireOp",EDGE,"E540"),sQuery(id+"F0.wireOp",EDGE,"E541"),sQuery(id+"F0.wireOp",EDGE,"E542"),sQuery(id+"F0.wireOp",EDGE,"E543"),sQuery(id+"F0.wireOp",EDGE,"E544"),sQuery(id+"F0.wireOp",EDGE,"E545"),sQuery(id+"F0.wireOp",EDGE,"E546"),sQuery(id+"F0.wireOp",EDGE,"E547"),sQuery(id+"F0.wireOp",EDGE,"E548"),sQuery(id+"F0.wireOp",EDGE,"E549"),sQuery(id+"F0.wireOp",EDGE,"E550"),sQuery(id+"F0.wireOp",EDGE,"E551"),sQuery(id+"F0.wireOp",EDGE,"E552"),sQuery(id+"F0.wireOp",EDGE,"E553"),sQuery(id+"F0.wireOp",EDGE,"E554"),sQuery(id+"F0.wireOp",EDGE,"E555"),sQuery(id+"F0.wireOp",EDGE,"E556"),sQuery(id+"F0.wireOp",EDGE,"E557"),sQuery(id+"F0.wireOp",EDGE,"E558"),sQuery(id+"F0.wireOp",EDGE,"E559"),sQuery(id+"F0.wireOp",EDGE,"E560"),sQuery(id+"F0.wireOp",EDGE,"E561"),sQuery(id+"F0.wireOp",EDGE,"E562"),sQuery(id+"F0.wireOp",EDGE,"E563"),sQuery(id+"F0.wireOp",EDGE,"E564"),sQuery(id+"F0.wireOp",EDGE,"E565"),sQuery(id+"F0.wireOp",EDGE,"E566"),sQuery(id+"F0.wireOp",EDGE,"E567"),sQuery(id+"F0.wireOp",EDGE,"E568"),sQuery(id+"F0.wireOp",EDGE,"E569"),sQuery(id+"F0.wireOp",EDGE,"E570"),sQuery(id+"F0.wireOp",EDGE,"E571"),sQuery(id+"F0.wireOp",EDGE,"E572"),sQuery(id+"F0.wireOp",EDGE,"E573"),sQuery(id+"F0.wireOp",EDGE,"E574"),sQuery(id+"F0.wireOp",EDGE,"E575"),sQuery(id+"F0.wireOp",EDGE,"E576"),sQuery(id+"F0.wireOp",EDGE,"E577"),sQuery(id+"F0.wireOp",EDGE,"E578"),sQuery(id+"F0.wireOp",EDGE,"E579"),sQuery(id+"F0.wireOp",EDGE,"E580"),sQuery(id+"F0.wireOp",EDGE,"E581"),sQuery(id+"F0.wireOp",EDGE,"E582"),sQuery(id+"F0.wireOp",EDGE,"E583"),sQuery(id+"F0.wireOp",EDGE,"E584"),sQuery(id+"F0.wireOp",EDGE,"E585"),sQuery(id+"F0.wireOp",EDGE,"E586"),sQuery(id+"F0.wireOp",EDGE,"E587"),sQuery(id+"F0.wireOp",EDGE,"E588"),sQuery(id+"F0.wireOp",EDGE,"E589"),sQuery(id+"F0.wireOp",EDGE,"E590"),sQuery(id+"F0.wireOp",EDGE,"E591"),sQuery(id+"F0.wireOp",EDGE,"E592"),sQuery(id+"F0.wireOp",EDGE,"E593"),sQuery(id+"F0.wireOp",EDGE,"E594"),sQuery(id+"F0.wireOp",EDGE,"E595"),sQuery(id+"F0.wireOp",EDGE,"E596"),sQuery(id+"F0.wireOp",EDGE,"E597"),sQuery(id+"F0.wireOp",EDGE,"E598"),sQuery(id+"F0.wireOp",EDGE,"E599"),sQuery(id+"F0.wireOp",EDGE,"E600"),sQuery(id+"F0.wireOp",EDGE,"E601"),sQuery(id+"F0.wireOp",EDGE,"E602"),sQuery(id+"F0.wireOp",EDGE,"E603"),sQuery(id+"F0.wireOp",EDGE,"E604"),sQuery(id+"F0.wireOp",EDGE,"E605"),sQuery(id+"F0.wireOp",EDGE,"E606"),sQuery(id+"F0.wireOp",EDGE,"E607"),sQuery(id+"F0.wireOp",EDGE,"E608"),sQuery(id+"F0.wireOp",EDGE,"E609"),sQuery(id+"F0.wireOp",EDGE,"E610"),sQuery(id+"F0.wireOp",EDGE,"E611"),sQuery(id+"F0.wireOp",EDGE,"E612"),sQuery(id+"F0.wireOp",EDGE,"E613"),sQuery(id+"F0.wireOp",EDGE,"E614"),sQuery(id+"F0.wireOp",EDGE,"E615"),sQuery(id+"F0.wireOp",EDGE,"E616"),sQuery(id+"F0.wireOp",EDGE,"E617"),sQuery(id+"F0.wireOp",EDGE,"E618"),sQuery(id+"F0.wireOp",EDGE,"E619"),sQuery(id+"F0.wireOp",EDGE,"E620"),sQuery(id+"F0.wireOp",EDGE,"E621"),sQuery(id+"F0.wireOp",EDGE,"E622"),sQuery(id+"F0.wireOp",EDGE,"E623"),sQuery(id+"F0.wireOp",EDGE,"E624"),sQuery(id+"F0.wireOp",EDGE,"E625"),sQuery(id+"F0.wireOp",EDGE,"E626"),sQuery(id+"F0.wireOp",EDGE,"E627"),sQuery(id+"F0.wireOp",EDGE,"E628"),sQuery(id+"F0.wireOp",EDGE,"E629"),sQuery(id+"F0.wireOp",EDGE,"E630"),sQuery(id+"F0.wireOp",EDGE,"E631"),sQuery(id+"F0.wireOp",EDGE,"E632"),sQuery(id+"F0.wireOp",EDGE,"E633"),sQuery(id+"F0.wireOp",EDGE,"E634"),sQuery(id+"F0.wireOp",EDGE,"E635"),sQuery(id+"F0.wireOp",EDGE,"E636"),sQuery(id+"F0.wireOp",EDGE,"E637"),sQuery(id+"F0.wireOp",EDGE,"E638"),sQuery(id+"F0.wireOp",EDGE,"E639"),sQuery(id+"F0.wireOp",EDGE,"E640"),sQuery(id+"F0.wireOp",EDGE,"E641"),sQuery(id+"F0.wireOp",EDGE,"E642"),sQuery(id+"F0.wireOp",EDGE,"E643"),sQuery(id+"F0.wireOp",EDGE,"E644"),sQuery(id+"F0.wireOp",EDGE,"E645"),sQuery(id+"F0.wireOp",EDGE,"E646"),sQuery(id+"F0.wireOp",EDGE,"E647"),sQuery(id+"F0.wireOp",EDGE,"E648"),sQuery(id+"F0.wireOp",EDGE,"E649"),sQuery(id+"F0.wireOp",EDGE,"E650"),sQuery(id+"F0.wireOp",EDGE,"E651"),sQuery(id+"F0.wireOp",EDGE,"E652"),sQuery(id+"F0.wireOp",EDGE,"E653"),sQuery(id+"F0.wireOp",EDGE,"E654"),sQuery(id+"F0.wireOp",EDGE,"E655"),sQuery(id+"F0.wireOp",EDGE,"E656"),sQuery(id+"F0.wireOp",EDGE,"E657"),sQuery(id+"F0.wireOp",EDGE,"E658"),sQuery(id+"F0.wireOp",EDGE,"E659"),sQuery(id+"F0.wireOp",EDGE,"E660"),sQuery(id+"F0.wireOp",EDGE,"E661"),sQuery(id+"F0.wireOp",EDGE,"E662"),sQuery(id+"F0.wireOp",EDGE,"E663"),sQuery(id+"F0.wireOp",EDGE,"E664"),sQuery(id+"F0.wireOp",EDGE,"E665"),sQuery(id+"F0.wireOp",EDGE,"E666"),sQuery(id+"F0.wireOp",EDGE,"E667"),sQuery(id+"F0.wireOp",EDGE,"E668"),sQuery(id+"F0.wireOp",EDGE,"E669"),sQuery(id+"F0.wireOp",EDGE,"E670"),sQuery(id+"F0.wireOp",EDGE,"E671"),sQuery(id+"F0.wireOp",EDGE,"E672"),sQuery(id+"F0.wireOp",EDGE,"E673"),sQuery(id+"F0.wireOp",EDGE,"E674"),sQuery(id+"F0.wireOp",EDGE,"E675"),sQuery(id+"F0.wireOp",EDGE,"E676"),sQuery(id+"F0.wireOp",EDGE,"E677"),sQuery(id+"F0.wireOp",EDGE,"E678"),sQuery(id+"F0.wireOp",EDGE,"E679"),sQuery(id+"F0.wireOp",EDGE,"E680"),sQuery(id+"F0.wireOp",EDGE,"E681"),sQuery(id+"F0.wireOp",EDGE,"E682"),sQuery(id+"F0.wireOp",EDGE,"E683"),sQuery(id+"F0.wireOp",EDGE,"E684"),sQuery(id+"F0.wireOp",EDGE,"E685"),sQuery(id+"F0.wireOp",EDGE,"E686"),sQuery(id+"F0.wireOp",EDGE,"E687"),sQuery(id+"F0.wireOp",EDGE,"E688"),sQuery(id+"F0.wireOp",EDGE,"E689"),sQuery(id+"F0.wireOp",EDGE,"E690"),sQuery(id+"F0.wireOp",EDGE,"E691"),sQuery(id+"F0.wireOp",EDGE,"E692"),sQuery(id+"F0.wireOp",EDGE,"E693"),sQuery(id+"F0.wireOp",EDGE,"E694"),sQuery(id+"F0.wireOp",EDGE,"E695"),sQuery(id+"F0.wireOp",EDGE,"E696"),sQuery(id+"F0.wireOp",EDGE,"E697"),sQuery(id+"F0.wireOp",EDGE,"E698"),sQuery(id+"F0.wireOp",EDGE,"E699"),sQuery(id+"F0.wireOp",EDGE,"E700"),sQuery(id+"F0.wireOp",EDGE,"E701"),sQuery(id+"F0.wireOp",EDGE,"E702"),sQuery(id+"F0.wireOp",EDGE,"E703"),sQuery(id+"F0.wireOp",EDGE,"E704"),sQuery(id+"F0.wireOp",EDGE,"E705"),sQuery(id+"F0.wireOp",EDGE,"E706"),sQuery(id+"F0.wireOp",EDGE,"E707"),sQuery(id+"F0.wireOp",EDGE,"E708"),sQuery(id+"F0.wireOp",EDGE,"E709"),sQuery(id+"F0.wireOp",EDGE,"E710"),sQuery(id+"F0.wireOp",EDGE,"E711"),sQuery(id+"F0.wireOp",EDGE,"E712"),sQuery(id+"F0.wireOp",EDGE,"E713"),sQuery(id+"F0.wireOp",EDGE,"E714"),sQuery(id+"F0.wireOp",EDGE,"E715"),sQuery(id+"F0.wireOp",EDGE,"E716"),sQuery(id+"F0.wireOp",EDGE,"E717"),sQuery(id+"F0.wireOp",EDGE,"E718"),sQuery(id+"F0.wireOp",EDGE,"E719"),sQuery(id+"F0.wireOp",EDGE,"E720"),sQuery(id+"F0.wireOp",EDGE,"E721"),sQuery(id+"F0.wireOp",EDGE,"E722"),sQuery(id+"F0.wireOp",EDGE,"E723"),sQuery(id+"F0.wireOp",EDGE,"E724"),sQuery(id+"F0.wireOp",EDGE,"E725"),sQuery(id+"F0.wireOp",EDGE,"E726"),sQuery(id+"F0.wireOp",EDGE,"E727"),sQuery(id+"F0.wireOp",EDGE,"E728"),sQuery(id+"F0.wireOp",EDGE,"E729"),sQuery(id+"F0.wireOp",EDGE,"E730"),sQuery(id+"F0.wireOp",EDGE,"E731"),sQuery(id+"F0.wireOp",EDGE,"E732"),sQuery(id+"F0.wireOp",EDGE,"E733"),sQuery(id+"F0.wireOp",EDGE,"E734"),sQuery(id+"F0.wireOp",EDGE,"E735"),sQuery(id+"F0.wireOp",EDGE,"E736"),sQuery(id+"F0.wireOp",EDGE,"E737"),sQuery(id+"F0.wireOp",EDGE,"E738"),sQuery(id+"F0.wireOp",EDGE,"E739"),sQuery(id+"F0.wireOp",EDGE,"E740"),sQuery(id+"F0.wireOp",EDGE,"E741"),sQuery(id+"F0.wireOp",EDGE,"E742"),sQuery(id+"F0.wireOp",EDGE,"E743"),sQuery(id+"F0.wireOp",EDGE,"E744"),sQuery(id+"F0.wireOp",EDGE,"E745"),sQuery(id+"F0.wireOp",EDGE,"E746"),sQuery(id+"F0.wireOp",EDGE,"E747"),sQuery(id+"F0.wireOp",EDGE,"E748"),sQuery(id+"F0.wireOp",EDGE,"E749"),sQuery(id+"F0.wireOp",EDGE,"E750"),sQuery(id+"F0.wireOp",EDGE,"E751"),sQuery(id+"F0.wireOp",EDGE,"E752"),sQuery(id+"F0.wireOp",EDGE,"E753"),sQuery(id+"F0.wireOp",EDGE,"E754"),sQuery(id+"F0.wireOp",EDGE,"E755"),sQuery(id+"F0.wireOp",EDGE,"E756"),sQuery(id+"F0.wireOp",EDGE,"E757"),sQuery(id+"F0.wireOp",EDGE,"E758"),sQuery(id+"F0.wireOp",EDGE,"E759"),sQuery(id+"F0.wireOp",EDGE,"E760"),sQuery(id+"F0.wireOp",EDGE,"E761"),sQuery(id+"F0.wireOp",EDGE,"E762"),sQuery(id+"F0.wireOp",EDGE,"E763"),sQuery(id+"F0.wireOp",EDGE,"E764"),sQuery(id+"F0.wireOp",EDGE,"E765"),sQuery(id+"F0.wireOp",EDGE,"E766"),sQuery(id+"F0.wireOp",EDGE,"E767"),sQuery(id+"F0.wireOp",EDGE,"E768"),sQuery(id+"F0.wireOp",EDGE,"E769"),sQuery(id+"F0.wireOp",EDGE,"E770"),sQuery(id+"F0.wireOp",EDGE,"E771"),sQuery(id+"F0.wireOp",EDGE,"E772"),sQuery(id+"F0.wireOp",EDGE,"E773"),sQuery(id+"F0.wireOp",EDGE,"E774"),sQuery(id+"F0.wireOp",EDGE,"E775"),sQuery(id+"F0.wireOp",EDGE,"E776"),sQuery(id+"F0.wireOp",EDGE,"E777"),sQuery(id+"F0.wireOp",EDGE,"E778"),sQuery(id+"F0.wireOp",EDGE,"E779"),sQuery(id+"F0.wireOp",EDGE,"E780"),sQuery(id+"F0.wireOp",EDGE,"E781"),sQuery(id+"F0.wireOp",EDGE,"E782"),sQuery(id+"F0.wireOp",EDGE,"E783"),sQuery(id+"F0.wireOp",EDGE,"E784"),sQuery(id+"F0.wireOp",EDGE,"E785"),sQuery(id+"F0.wireOp",EDGE,"E786"),sQuery(id+"F0.wireOp",EDGE,"E787"),sQuery(id+"F0.wireOp",EDGE,"E788"),sQuery(id+"F0.wireOp",EDGE,"E789"),sQuery(id+"F0.wireOp",EDGE,"E790"),sQuery(id+"F0.wireOp",EDGE,"E791"),sQuery(id+"F0.wireOp",EDGE,"E792"),sQuery(id+"F0.wireOp",EDGE,"E793"),sQuery(id+"F0.wireOp",EDGE,"E794"),sQuery(id+"F0.wireOp",EDGE,"E795"),sQuery(id+"F0.wireOp",EDGE,"E796"),sQuery(id+"F0.wireOp",EDGE,"E797"),sQuery(id+"F0.wireOp",EDGE,"E798"),sQuery(id+"F0.wireOp",EDGE,"E799"),sQuery(id+"F0.wireOp",EDGE,"E800"),sQuery(id+"F0.wireOp",EDGE,"E801"),sQuery(id+"F0.wireOp",EDGE,"E802"),sQuery(id+"F0.wireOp",EDGE,"E803"),sQuery(id+"F0.wireOp",EDGE,"E804"),sQuery(id+"F0.wireOp",EDGE,"E805"),sQuery(id+"F0.wireOp",EDGE,"E806"),sQuery(id+"F0.wireOp",EDGE,"E807"),sQuery(id+"F0.wireOp",EDGE,"E808"),sQuery(id+"F0.wireOp",EDGE,"E809"),sQuery(id+"F0.wireOp",EDGE,"E810"),sQuery(id+"F0.wireOp",EDGE,"E811"),sQuery(id+"F0.wireOp",EDGE,"E812"),sQuery(id+"F0.wireOp",EDGE,"E813"),sQuery(id+"F0.wireOp",EDGE,"E814"),sQuery(id+"F0.wireOp",EDGE,"E815"),sQuery(id+"F0.wireOp",EDGE,"E816"),sQuery(id+"F0.wireOp",EDGE,"E817"),sQuery(id+"F0.wireOp",EDGE,"E818"),sQuery(id+"F0.wireOp",EDGE,"E819"),sQuery(id+"F0.wireOp",EDGE,"E820"),sQuery(id+"F0.wireOp",EDGE,"E821"),sQuery(id+"F0.wireOp",EDGE,"E822"),sQuery(id+"F0.wireOp",EDGE,"E823"),sQuery(id+"F0.wireOp",EDGE,"E824"),sQuery(id+"F0.wireOp",EDGE,"E825"),sQuery(id+"F0.wireOp",EDGE,"E826"),sQuery(id+"F0.wireOp",EDGE,"E827"),sQuery(id+"F0.wireOp",EDGE,"E828"),sQuery(id+"F0.wireOp",EDGE,"E829"),sQuery(id+"F0.wireOp",EDGE,"E830"),sQuery(id+"F0.wireOp",EDGE,"E831"),sQuery(id+"F0.wireOp",EDGE,"E832"),sQuery(id+"F0.wireOp",EDGE,"E833"),sQuery(id+"F0.wireOp",EDGE,"E834"),sQuery(id+"F0.wireOp",EDGE,"E835"),sQuery(id+"F0.wireOp",EDGE,"E836"),sQuery(id+"F0.wireOp",EDGE,"E837"),sQuery(id+"F0.wireOp",EDGE,"E838"),sQuery(id+"F0.wireOp",EDGE,"E839"),sQuery(id+"F0.wireOp",EDGE,"E840"),sQuery(id+"F0.wireOp",EDGE,"E841"),sQuery(id+"F0.wireOp",EDGE,"E842"),sQuery(id+"F0.wireOp",EDGE,"E843"),sQuery(id+"F0.wireOp",EDGE,"E844"),sQuery(id+"F0.wireOp",EDGE,"E845"),sQuery(id+"F0.wireOp",EDGE,"E846"),sQuery(id+"F0.wireOp",EDGE,"E847"),sQuery(id+"F0.wireOp",EDGE,"E848"),sQuery(id+"F0.wireOp",EDGE,"E849"),sQuery(id+"F0.wireOp",EDGE,"E850"),sQuery(id+"F0.wireOp",EDGE,"E851"),sQuery(id+"F0.wireOp",EDGE,"E852"),sQuery(id+"F0.wireOp",EDGE,"E853"),sQuery(id+"F0.wireOp",EDGE,"E854"),sQuery(id+"F0.wireOp",EDGE,"E855"),sQuery(id+"F0.wireOp",EDGE,"E856"),sQuery(id+"F0.wireOp",EDGE,"E857"),sQuery(id+"F0.wireOp",EDGE,"E858"),sQuery(id+"F0.wireOp",EDGE,"E859"),sQuery(id+"F0.wireOp",EDGE,"E860"),sQuery(id+"F0.wireOp",EDGE,"E861"),sQuery(id+"F0.wireOp",EDGE,"E862"),sQuery(id+"F0.wireOp",EDGE,"E863"),sQuery(id+"F0.wireOp",EDGE,"E864"),sQuery(id+"F0.wireOp",EDGE,"E865"),sQuery(id+"F0.wireOp",EDGE,"E866"),sQuery(id+"F0.wireOp",EDGE,"E867"),sQuery(id+"F0.wireOp",EDGE,"E868"),sQuery(id+"F0.wireOp",EDGE,"E869"),sQuery(id+"F0.wireOp",EDGE,"E870"),sQuery(id+"F0.wireOp",EDGE,"E871"),sQuery(id+"F0.wireOp",EDGE,"E872"),sQuery(id+"F0.wireOp",EDGE,"E873"),sQuery(id+"F0.wireOp",EDGE,"E874"),sQuery(id+"F0.wireOp",EDGE,"E875"),sQuery(id+"F0.wireOp",EDGE,"E876"),sQuery(id+"F0.wireOp",EDGE,"E877"),sQuery(id+"F0.wireOp",EDGE,"E878"),sQuery(id+"F0.wireOp",EDGE,"E879"),sQuery(id+"F0.wireOp",EDGE,"E880"),sQuery(id+"F0.wireOp",EDGE,"E881"),sQuery(id+"F0.wireOp",EDGE,"E882"),sQuery(id+"F0.wireOp",EDGE,"E883"),sQuery(id+"F0.wireOp",EDGE,"E884"),sQuery(id+"F0.wireOp",EDGE,"E885"),sQuery(id+"F0.wireOp",EDGE,"E886"),sQuery(id+"F0.wireOp",EDGE,"E887"),sQuery(id+"F0.wireOp",EDGE,"E888"),sQuery(id+"F0.wireOp",EDGE,"E889"),sQuery(id+"F0.wireOp",EDGE,"E890"),sQuery(id+"F0.wireOp",EDGE,"E891"),sQuery(id+"F0.wireOp",EDGE,"E892"),sQuery(id+"F0.wireOp",EDGE,"E893"),sQuery(id+"F0.wireOp",EDGE,"E894"),sQuery(id+"F0.wireOp",EDGE,"E895"),sQuery(id+"F0.wireOp",EDGE,"E896"),sQuery(id+"F0.wireOp",EDGE,"E897"),sQuery(id+"F0.wireOp",EDGE,"E898"),sQuery(id+"F0.wireOp",EDGE,"E899"),sQuery(id+"F0.wireOp",EDGE,"E900"),sQuery(id+"F0.wireOp",EDGE,"E901"),sQuery(id+"F0.wireOp",EDGE,"E902"),sQuery(id+"F0.wireOp",EDGE,"E903"),sQuery(id+"F0.wireOp",EDGE,"E904"),sQuery(id+"F0.wireOp",EDGE,"E905"),sQuery(id+"F0.wireOp",EDGE,"E906"),sQuery(id+"F0.wireOp",EDGE,"E907"),sQuery(id+"F0.wireOp",EDGE,"E908"),sQuery(id+"F0.wireOp",EDGE,"E909"),sQuery(id+"F0.wireOp",EDGE,"E910"),sQuery(id+"F0.wireOp",EDGE,"E911"),sQuery(id+"F0.wireOp",EDGE,"E912"),sQuery(id+"F0.wireOp",EDGE,"E913"),sQuery(id+"F0.wireOp",EDGE,"E914"),sQuery(id+"F0.wireOp",EDGE,"E915"),sQuery(id+"F0.wireOp",EDGE,"E916"),sQuery(id+"F0.wireOp",EDGE,"E917"),sQuery(id+"F0.wireOp",EDGE,"E918"),sQuery(id+"F0.wireOp",EDGE,"E919"),sQuery(id+"F0.wireOp",EDGE,"E920"),sQuery(id+"F0.wireOp",EDGE,"E921"),sQuery(id+"F0.wireOp",EDGE,"E922"),sQuery(id+"F0.wireOp",EDGE,"E923"),sQuery(id+"F0.wireOp",EDGE,"E924"),sQuery(id+"F0.wireOp",EDGE,"E925"),sQuery(id+"F0.wireOp",EDGE,"E926"),sQuery(id+"F0.wireOp",EDGE,"E927"),sQuery(id+"F0.wireOp",EDGE,"E928"),sQuery(id+"F0.wireOp",EDGE,"E929"),sQuery(id+"F0.wireOp",EDGE,"E930"),sQuery(id+"F0.wireOp",EDGE,"E931"),sQuery(id+"F0.wireOp",EDGE,"E932"),sQuery(id+"F0.wireOp",EDGE,"E933"),sQuery(id+"F0.wireOp",EDGE,"E934"),sQuery(id+"F0.wireOp",EDGE,"E935"),sQuery(id+"F0.wireOp",EDGE,"E936"),sQuery(id+"F0.wireOp",EDGE,"E937"),sQuery(id+"F0.wireOp",EDGE,"E938"),sQuery(id+"F0.wireOp",EDGE,"E939"),sQuery(id+"F0.wireOp",EDGE,"E940"),sQuery(id+"F0.wireOp",EDGE,"E941"),sQuery(id+"F0.wireOp",EDGE,"E942"),sQuery(id+"F0.wireOp",EDGE,"E943"),sQuery(id+"F0.wireOp",EDGE,"E944"),sQuery(id+"F0.wireOp",EDGE,"E945"),sQuery(id+"F0.wireOp",EDGE,"E946"),sQuery(id+"F0.wireOp",EDGE,"E947"),sQuery(id+"F0.wireOp",EDGE,"E948"),sQuery(id+"F0.wireOp",EDGE,"E949"),sQuery(id+"F0.wireOp",EDGE,"E950"),sQuery(id+"F0.wireOp",EDGE,"E951"),sQuery(id+"F0.wireOp",EDGE,"E952"),sQuery(id+"F0.wireOp",EDGE,"E953"),sQuery(id+"F0.wireOp",EDGE,"E954"),sQuery(id+"F0.wireOp",EDGE,"E955"),sQuery(id+"F0.wireOp",EDGE,"E956"),sQuery(id+"F0.wireOp",EDGE,"E957"),sQuery(id+"F0.wireOp",EDGE,"E958"),sQuery(id+"F0.wireOp",EDGE,"E959"),sQuery(id+"F0.wireOp",EDGE,"E960"),sQuery(id+"F0.wireOp",EDGE,"E961"),sQuery(id+"F0.wireOp",EDGE,"E962"),sQuery(id+"F0.wireOp",EDGE,"E963"),sQuery(id+"F0.wireOp",EDGE,"E964"),sQuery(id+"F0.wireOp",EDGE,"E965"),sQuery(id+"F0.wireOp",EDGE,"E966"),sQuery(id+"F0.wireOp",EDGE,"E967"),sQuery(id+"F0.wireOp",EDGE,"E968"),sQuery(id+"F0.wireOp",EDGE,"E969"),sQuery(id+"F0.wireOp",EDGE,"E970"),sQuery(id+"F0.wireOp",EDGE,"E971"),sQuery(id+"F0.wireOp",EDGE,"E972"),sQuery(id+"F0.wireOp",EDGE,"E973"),sQuery(id+"F0.wireOp",EDGE,"E974"),sQuery(id+"F0.wireOp",EDGE,"E975"),sQuery(id+"F0.wireOp",EDGE,"E976"),sQuery(id+"F0.wireOp",EDGE,"E977"),sQuery(id+"F0.wireOp",EDGE,"E978"),sQuery(id+"F0.wireOp",EDGE,"E979"),sQuery(id+"F0.wireOp",EDGE,"E980"),sQuery(id+"F0.wireOp",EDGE,"E981"),sQuery(id+"F0.wireOp",EDGE,"E982"),sQuery(id+"F0.wireOp",EDGE,"E983"),sQuery(id+"F0.wireOp",EDGE,"E984"),sQuery(id+"F0.wireOp",EDGE,"E985"),sQuery(id+"F0.wireOp",EDGE,"E986"),sQuery(id+"F0.wireOp",EDGE,"E987"),sQuery(id+"F0.wireOp",EDGE,"E988"),sQuery(id+"F0.wireOp",EDGE,"E989"),sQuery(id+"F0.wireOp",EDGE,"E990"),sQuery(id+"F0.wireOp",EDGE,"E991"),sQuery(id+"F0.wireOp",EDGE,"E992"),sQuery(id+"F0.wireOp",EDGE,"E993"),sQuery(id+"F0.wireOp",EDGE,"E994"),sQuery(id+"F0.wireOp",EDGE,"E995"),sQuery(id+"F0.wireOp",EDGE,"E996"),sQuery(id+"F0.wireOp",EDGE,"E997"),sQuery(id+"F0.wireOp",EDGE,"E998"),sQuery(id+"F0.wireOp",EDGE,"E999"),sQuery(id+"F0.wireOp",EDGE,"E1000"),sQuery(id+"F0.wireOp",EDGE,"E1001"),sQuery(id+"F0.wireOp",EDGE,"E1002"),sQuery(id+"F0.wireOp",EDGE,"E1003"),sQuery(id+"F0.wireOp",EDGE,"E1004"),sQuery(id+"F0.wireOp",EDGE,"E1005"),sQuery(id+"F0.wireOp",EDGE,"E1006"),sQuery(id+"F0.wireOp",EDGE,"E1007"),sQuery(id+"F0.wireOp",EDGE,"E1008"),sQuery(id+"F0.wireOp",EDGE,"E1009"),sQuery(id+"F0.wireOp",EDGE,"E1010"),sQuery(id+"F0.wireOp",EDGE,"E1011"),sQuery(id+"F0.wireOp",EDGE,"E1012"),sQuery(id+"F0.wireOp",EDGE,"E1013"),sQuery(id+"F0.wireOp",EDGE,"E1014"),sQuery(id+"F0.wireOp",EDGE,"E1015"),sQuery(id+"F0.wireOp",EDGE,"E1016"),sQuery(id+"F0.wireOp",EDGE,"E1017"),sQuery(id+"F0.wireOp",EDGE,"E1018"),sQuery(id+"F0.wireOp",EDGE,"E1019"),sQuery(id+"F0.wireOp",EDGE,"E1020"),sQuery(id+"F0.wireOp",EDGE,"E1021"),sQuery(id+"F0.wireOp",EDGE,"E1022"),sQuery(id+"F0.wireOp",EDGE,"E1023"),sQuery(id+"F0.wireOp",EDGE,"E1024"),sQuery(id+"F0.wireOp",EDGE,"E1025"),sQuery(id+"F0.wireOp",EDGE,"E1026"),sQuery(id+"F0.wireOp",EDGE,"E1027"),sQuery(id+"F0.wireOp",EDGE,"E1028"),sQuery(id+"F0.wireOp",EDGE,"E1029"),sQuery(id+"F0.wireOp",EDGE,"E1030"),sQuery(id+"F0.wireOp",EDGE,"E1031"),sQuery(id+"F0.wireOp",EDGE,"E1032"),sQuery(id+"F0.wireOp",EDGE,"E1033"),sQuery(id+"F0.wireOp",EDGE,"E1034"),sQuery(id+"F0.wireOp",EDGE,"E1035"),sQuery(id+"F0.wireOp",EDGE,"E1036"),sQuery(id+"F0.wireOp",EDGE,"E1037"),sQuery(id+"F0.wireOp",EDGE,"E1038"),sQuery(id+"F0.wireOp",EDGE,"E1039"),sQuery(id+"F0.wireOp",EDGE,"E1040"),sQuery(id+"F0.wireOp",EDGE,"E1041"),sQuery(id+"F0.wireOp",EDGE,"E1042"),sQuery(id+"F0.wireOp",EDGE,"E1043"),sQuery(id+"F0.wireOp",EDGE,"E1044"),sQuery(id+"F0.wireOp",EDGE,"E1045"),sQuery(id+"F0.wireOp",EDGE,"E1046"),sQuery(id+"F0.wireOp",EDGE,"E1047"),sQuery(id+"F0.wireOp",EDGE,"E1048"),sQuery(id+"F0.wireOp",EDGE,"E1049"),sQuery(id+"F0.wireOp",EDGE,"E1050"),sQuery(id+"F0.wireOp",EDGE,"E1051"),sQuery(id+"F0.wireOp",EDGE,"E1052"),sQuery(id+"F0.wireOp",EDGE,"E1053"),sQuery(id+"F0.wireOp",EDGE,"E1054"),sQuery(id+"F0.wireOp",EDGE,"E1055"),sQuery(id+"F0.wireOp",EDGE,"E1056"),sQuery(id+"F0.wireOp",EDGE,"E1057"),sQuery(id+"F0.wireOp",EDGE,"E1058"),sQuery(id+"F0.wireOp",EDGE,"E1059"),sQuery(id+"F0.wireOp",EDGE,"E1060"),sQuery(id+"F0.wireOp",EDGE,"E1061"),sQuery(id+"F0.wireOp",EDGE,"E1062"),sQuery(id+"F0.wireOp",EDGE,"E1063"),sQuery(id+"F0.wireOp",EDGE,"E1064"),sQuery(id+"F0.wireOp",EDGE,"E1065"),sQuery(id+"F0.wireOp",EDGE,"E1066"),sQuery(id+"F0.wireOp",EDGE,"E1067"),sQuery(id+"F0.wireOp",EDGE,"E1068"),sQuery(id+"F0.wireOp",EDGE,"E1069"),sQuery(id+"F0.wireOp",EDGE,"E1070"),sQuery(id+"F0.wireOp",EDGE,"E1071"),sQuery(id+"F0.wireOp",EDGE,"E1072"),sQuery(id+"F0.wireOp",EDGE,"E1073"),sQuery(id+"F0.wireOp",EDGE,"E1074"),sQuery(id+"F0.wireOp",EDGE,"E1075"),sQuery(id+"F0.wireOp",EDGE,"E1076"),sQuery(id+"F0.wireOp",EDGE,"E1077"),sQuery(id+"F0.wireOp",EDGE,"E1078"),sQuery(id+"F0.wireOp",EDGE,"E1079"),sQuery(id+"F0.wireOp",EDGE,"E1080"),sQuery(id+"F0.wireOp",EDGE,"E1081"),sQuery(id+"F0.wireOp",EDGE,"E1082"),sQuery(id+"F0.wireOp",EDGE,"E1083"),sQuery(id+"F0.wireOp",EDGE,"E1084"),sQuery(id+"F0.wireOp",EDGE,"E1085"),sQuery(id+"F0.wireOp",EDGE,"E1086"),sQuery(id+"F0.wireOp",EDGE,"E1087"),sQuery(id+"F0.wireOp",EDGE,"E1088"),sQuery(id+"F0.wireOp",EDGE,"E1089"),sQuery(id+"F0.wireOp",EDGE,"E1090"),sQuery(id+"F0.wireOp",EDGE,"E1091"),sQuery(id+"F0.wireOp",EDGE,"E1092"),sQuery(id+"F0.wireOp",EDGE,"E1093"),sQuery(id+"F0.wireOp",EDGE,"E1094"),sQuery(id+"F0.wireOp",EDGE,"E1095"),sQuery(id+"F0.wireOp",EDGE,"E1096"),sQuery(id+"F0.wireOp",EDGE,"E1097"),sQuery(id+"F0.wireOp",EDGE,"E1098"),sQuery(id+"F0.wireOp",EDGE,"E1099"),sQuery(id+"F0.wireOp",EDGE,"E1100"),sQuery(id+"F0.wireOp",EDGE,"E1101"),sQuery(id+"F0.wireOp",EDGE,"E1102"),sQuery(id+"F0.wireOp",EDGE,"E1103"),sQuery(id+"F0.wireOp",EDGE,"E1104"),sQuery(id+"F0.wireOp",EDGE,"E1105"),sQuery(id+"F0.wireOp",EDGE,"E1106"),sQuery(id+"F0.wireOp",EDGE,"E1107"),sQuery(id+"F0.wireOp",EDGE,"E1108"),sQuery(id+"F0.wireOp",EDGE,"E1109"),sQuery(id+"F0.wireOp",EDGE,"E1110"),sQuery(id+"F0.wireOp",EDGE,"E1111"),sQuery(id+"F0.wireOp",EDGE,"E1112"),sQuery(id+"F0.wireOp",EDGE,"E1113"),sQuery(id+"F0.wireOp",EDGE,"E1114"),sQuery(id+"F0.wireOp",EDGE,"E1115"),sQuery(id+"F0.wireOp",EDGE,"E1116"),sQuery(id+"F0.wireOp",EDGE,"E1117"),sQuery(id+"F0.wireOp",EDGE,"E1118"),sQuery(id+"F0.wireOp",EDGE,"E1119"),sQuery(id+"F0.wireOp",EDGE,"E1120"),sQuery(id+"F0.wireOp",EDGE,"E1121"),sQuery(id+"F0.wireOp",EDGE,"E1122"),sQuery(id+"F0.wireOp",EDGE,"E1123"),sQuery(id+"F0.wireOp",EDGE,"E1124"),sQuery(id+"F0.wireOp",EDGE,"E1125"),sQuery(id+"F0.wireOp",EDGE,"E1126"),sQuery(id+"F0.wireOp",EDGE,"E1127"),sQuery(id+"F0.wireOp",EDGE,"E1128"),sQuery(id+"F0.wireOp",EDGE,"E1129"),sQuery(id+"F0.wireOp",EDGE,"E1130"),sQuery(id+"F0.wireOp",EDGE,"E1131"),sQuery(id+"F0.wireOp",EDGE,"E1132"),sQuery(id+"F0.wireOp",EDGE,"E1133"),sQuery(id+"F0.wireOp",EDGE,"E1134"),sQuery(id+"F0.wireOp",EDGE,"E1135"),sQuery(id+"F0.wireOp",EDGE,"E1136"),sQuery(id+"F0.wireOp",EDGE,"E1137"),sQuery(id+"F0.wireOp",EDGE,"E1138"),sQuery(id+"F0.wireOp",EDGE,"E1139"),sQuery(id+"F0.wireOp",EDGE,"E1140"),sQuery(id+"F0.wireOp",EDGE,"E1141"),sQuery(id+"F0.wireOp",EDGE,"E1142"),sQuery(id+"F0.wireOp",EDGE,"E1143"),sQuery(id+"F0.wireOp",EDGE,"E1144"),sQuery(id+"F0.wireOp",EDGE,"E1145"),sQuery(id+"F0.wireOp",EDGE,"E1146"),sQuery(id+"F0.wireOp",EDGE,"E1147"),sQuery(id+"F0.wireOp",EDGE,"E1148"),sQuery(id+"F0.wireOp",EDGE,"E1149"),sQuery(id+"F0.wireOp",EDGE,"E1150"),sQuery(id+"F0.wireOp",EDGE,"E1151"),sQuery(id+"F0.wireOp",EDGE,"E1152"),sQuery(id+"F0.wireOp",EDGE,"E1153"),sQuery(id+"F0.wireOp",EDGE,"E1154"),sQuery(id+"F0.wireOp",EDGE,"E1155"),sQuery(id+"F0.wireOp",EDGE,"E1156"),sQuery(id+"F0.wireOp",EDGE,"E1157"),sQuery(id+"F0.wireOp",EDGE,"E1158"),sQuery(id+"F0.wireOp",EDGE,"E1159"),sQuery(id+"F0.wireOp",EDGE,"E1160"),sQuery(id+"F0.wireOp",EDGE,"E1161"),sQuery(id+"F0.wireOp",EDGE,"E1162"),sQuery(id+"F0.wireOp",EDGE,"E1163"),sQuery(id+"F0.wireOp",EDGE,"E1164"),sQuery(id+"F0.wireOp",EDGE,"E1165"),sQuery(id+"F0.wireOp",EDGE,"E1166"),sQuery(id+"F0.wireOp",EDGE,"E1167"),sQuery(id+"F0.wireOp",EDGE,"E1168"),sQuery(id+"F0.wireOp",EDGE,"E1169"),sQuery(id+"F0.wireOp",EDGE,"E1170"),sQuery(id+"F0.wireOp",EDGE,"E1171"),sQuery(id+"F0.wireOp",EDGE,"E1172"),sQuery(id+"F0.wireOp",EDGE,"E1173"),sQuery(id+"F0.wireOp",EDGE,"E1174"),sQuery(id+"F0.wireOp",EDGE,"E1175"),sQuery(id+"F0.wireOp",EDGE,"E1176"),sQuery(id+"F0.wireOp",EDGE,"E1177"),sQuery(id+"F0.wireOp",EDGE,"E1178"),sQuery(id+"F0.wireOp",EDGE,"E1179"),sQuery(id+"F0.wireOp",EDGE,"E1180"),sQuery(id+"F0.wireOp",EDGE,"E1181"),sQuery(id+"F0.wireOp",EDGE,"E1182"),sQuery(id+"F0.wireOp",EDGE,"E1183"),sQuery(id+"F0.wireOp",EDGE,"E1184"),sQuery(id+"F0.wireOp",EDGE,"E1185"),sQuery(id+"F0.wireOp",EDGE,"E1186"),sQuery(id+"F0.wireOp",EDGE,"E1187"),sQuery(id+"F0.wireOp",EDGE,"E1188"),sQuery(id+"F0.wireOp",EDGE,"E1189"),sQuery(id+"F0.wireOp",EDGE,"E1190"),sQuery(id+"F0.wireOp",EDGE,"E1191"),sQuery(id+"F0.wireOp",EDGE,"E1192"),sQuery(id+"F0.wireOp",EDGE,"E1193"),sQuery(id+"F0.wireOp",EDGE,"E1194"),sQuery(id+"F0.wireOp",EDGE,"E1195"),sQuery(id+"F0.wireOp",EDGE,"E1196"),sQuery(id+"F0.wireOp",EDGE,"E1197"),sQuery(id+"F0.wireOp",EDGE,"E1198"),sQuery(id+"F0.wireOp",EDGE,"E1199"),sQuery(id+"F0.wireOp",EDGE,"E1200"),sQuery(id+"F0.wireOp",EDGE,"E1201"),sQuery(id+"F0.wireOp",EDGE,"E1202"),sQuery(id+"F0.wireOp",EDGE,"E1203"),sQuery(id+"F0.wireOp",EDGE,"E1204"),sQuery(id+"F0.wireOp",EDGE,"E1205"),sQuery(id+"F0.wireOp",EDGE,"E1206"),sQuery(id+"F0.wireOp",EDGE,"E1207"),sQuery(id+"F0.wireOp",EDGE,"E1208"),sQuery(id+"F0.wireOp",EDGE,"E1209"),sQuery(id+"F0.wireOp",EDGE,"E1210"),sQuery(id+"F0.wireOp",EDGE,"E1211"),sQuery(id+"F0.wireOp",EDGE,"E1212"),sQuery(id+"F0.wireOp",EDGE,"E1213"),sQuery(id+"F0.wireOp",EDGE,"E1214"),sQuery(id+"F0.wireOp",EDGE,"E1215"),sQuery(id+"F0.wireOp",EDGE,"E1216"),sQuery(id+"F0.wireOp",EDGE,"E1217"),sQuery(id+"F0.wireOp",EDGE,"E1218"),sQuery(id+"F0.wireOp",EDGE,"E1219"),sQuery(id+"F0.wireOp",EDGE,"E1220"),sQuery(id+"F0.wireOp",EDGE,"E1221"),sQuery(id+"F0.wireOp",EDGE,"E1222"),sQuery(id+"F0.wireOp",EDGE,"E1223"),sQuery(id+"F0.wireOp",EDGE,"E1224"),sQuery(id+"F0.wireOp",EDGE,"E1225"),sQuery(id+"F0.wireOp",EDGE,"E1226"),sQuery(id+"F0.wireOp",EDGE,"E1227"),sQuery(id+"F0.wireOp",EDGE,"E1228"),sQuery(id+"F0.wireOp",EDGE,"E1229"),sQuery(id+"F0.wireOp",EDGE,"E1230"),sQuery(id+"F0.wireOp",EDGE,"E1231"),sQuery(id+"F0.wireOp",EDGE,"E1232"),sQuery(id+"F0.wireOp",EDGE,"E1233"),sQuery(id+"F0.wireOp",EDGE,"E1234"),sQuery(id+"F0.wireOp",EDGE,"E1235"),sQuery(id+"F0.wireOp",EDGE,"E1236"),sQuery(id+"F0.wireOp",EDGE,"E1237"),sQuery(id+"F0.wireOp",EDGE,"E1238"),sQuery(id+"F0.wireOp",EDGE,"E1239"),sQuery(id+"F0.wireOp",EDGE,"E1240"),sQuery(id+"F0.wireOp",EDGE,"E1241"),sQuery(id+"F0.wireOp",EDGE,"E1242"),sQuery(id+"F0.wireOp",EDGE,"E1243"),sQuery(id+"F0.wireOp",EDGE,"E1244"),sQuery(id+"F0.wireOp",EDGE,"E1245"),sQuery(id+"F0.wireOp",EDGE,"E1246"),sQuery(id+"F0.wireOp",EDGE,"E1247"),sQuery(id+"F0.wireOp",EDGE,"E1248"),sQuery(id+"F0.wireOp",EDGE,"E1249"),sQuery(id+"F0.wireOp",EDGE,"E1250"),sQuery(id+"F0.wireOp",EDGE,"E1251"),sQuery(id+"F0.wireOp",EDGE,"E1252"),sQuery(id+"F0.wireOp",EDGE,"E1253"),sQuery(id+"F0.wireOp",EDGE,"E1254"),sQuery(id+"F0.wireOp",EDGE,"E1255"),sQuery(id+"F0.wireOp",EDGE,"E1256"),sQuery(id+"F0.wireOp",EDGE,"E1257"),sQuery(id+"F0.wireOp",EDGE,"E1258"),sQuery(id+"F0.wireOp",EDGE,"E1259"),sQuery(id+"F0.wireOp",EDGE,"E1260"),sQuery(id+"F0.wireOp",EDGE,"E1261"),sQuery(id+"F0.wireOp",EDGE,"E1262"),sQuery(id+"F0.wireOp",EDGE,"E1263"),sQuery(id+"F0.wireOp",EDGE,"E1264"),sQuery(id+"F0.wireOp",EDGE,"E1265"),sQuery(id+"F0.wireOp",EDGE,"E1266"),sQuery(id+"F0.wireOp",EDGE,"E1267"),sQuery(id+"F0.wireOp",EDGE,"E1268"),sQuery(id+"F0.wireOp",EDGE,"E1269"),sQuery(id+"F0.wireOp",EDGE,"E1270"),sQuery(id+"F0.wireOp",EDGE,"E1271"),sQuery(id+"F0.wireOp",EDGE,"E1272"),sQuery(id+"F0.wireOp",EDGE,"E1273"),sQuery(id+"F0.wireOp",EDGE,"E1274"),sQuery(id+"F0.wireOp",EDGE,"E1275"),sQuery(id+"F0.wireOp",EDGE,"E1276"),sQuery(id+"F0.wireOp",EDGE,"E1277"),sQuery(id+"F0.wireOp",EDGE,"E1278"),sQuery(id+"F0.wireOp",EDGE,"E1279"),sQuery(id+"F0.wireOp",EDGE,"E1280"),sQuery(id+"F0.wireOp",EDGE,"E1281"),sQuery(id+"F0.wireOp",EDGE,"E1282"),sQuery(id+"F0.wireOp",EDGE,"E1283"),sQuery(id+"F0.wireOp",EDGE,"E1284"),sQuery(id+"F0.wireOp",EDGE,"E1285"),sQuery(id+"F0.wireOp",EDGE,"E1286"),sQuery(id+"F0.wireOp",EDGE,"E1287"),sQuery(id+"F0.wireOp",EDGE,"E1288"),sQuery(id+"F0.wireOp",EDGE,"E1289"),sQuery(id+"F0.wireOp",EDGE,"E1290"),sQuery(id+"F0.wireOp",EDGE,"E1291"),sQuery(id+"F0.wireOp",EDGE,"E1292"),sQuery(id+"F0.wireOp",EDGE,"E1293"),sQuery(id+"F0.wireOp",EDGE,"E1294"),sQuery(id+"F0.wireOp",EDGE,"E1295"),sQuery(id+"F0.wireOp",EDGE,"E1296"),sQuery(id+"F0.wireOp",EDGE,"E1297"),sQuery(id+"F0.wireOp",EDGE,"E1298"),sQuery(id+"F0.wireOp",EDGE,"E1299"),sQuery(id+"F0.wireOp",EDGE,"E1300"),sQuery(id+"F0.wireOp",EDGE,"E1301"),sQuery(id+"F0.wireOp",EDGE,"E1302"),sQuery(id+"F0.wireOp",EDGE,"E1303"),sQuery(id+"F0.wireOp",EDGE,"E1304"),sQuery(id+"F0.wireOp",EDGE,"E1305"),sQuery(id+"F0.wireOp",EDGE,"E1306"),sQuery(id+"F0.wireOp",EDGE,"E1307"),sQuery(id+"F0.wireOp",EDGE,"E1308"),sQuery(id+"F0.wireOp",EDGE,"E1309"),sQuery(id+"F0.wireOp",EDGE,"E1310"),sQuery(id+"F0.wireOp",EDGE,"E1311"),sQuery(id+"F0.wireOp",EDGE,"E1312"),sQuery(id+"F0.wireOp",EDGE,"E1313"),sQuery(id+"F0.wireOp",EDGE,"E1314"),sQuery(id+"F0.wireOp",EDGE,"E1315"),sQuery(id+"F0.wireOp",EDGE,"E1316"),sQuery(id+"F0.wireOp",EDGE,"E1317"),sQuery(id+"F0.wireOp",EDGE,"E1318"),sQuery(id+"F0.wireOp",EDGE,"E1319"),sQuery(id+"F0.wireOp",EDGE,"E1320"),sQuery(id+"F0.wireOp",EDGE,"E1321"),sQuery(id+"F0.wireOp",EDGE,"E1322"),sQuery(id+"F0.wireOp",EDGE,"E1323"),sQuery(id+"F0.wireOp",EDGE,"E1324"),sQuery(id+"F0.wireOp",EDGE,"E1325"),sQuery(id+"F0.wireOp",EDGE,"E1326"),sQuery(id+"F0.wireOp",EDGE,"E1327"),sQuery(id+"F0.wireOp",EDGE,"E1328"),sQuery(id+"F0.wireOp",EDGE,"E1329"),sQuery(id+"F0.wireOp",EDGE,"E1330"),sQuery(id+"F0.wireOp",EDGE,"E1331"),sQuery(id+"F0.wireOp",EDGE,"E1332"),sQuery(id+"F0.wireOp",EDGE,"E1333"),sQuery(id+"F0.wireOp",EDGE,"E1334"),sQuery(id+"F0.wireOp",EDGE,"E1335"),sQuery(id+"F0.wireOp",EDGE,"E1336"),sQuery(id+"F0.wireOp",EDGE,"E1337"),sQuery(id+"F0.wireOp",EDGE,"E1338"),sQuery(id+"F0.wireOp",EDGE,"E1339"),sQuery(id+"F0.wireOp",EDGE,"E1340"),sQuery(id+"F0.wireOp",EDGE,"E1341"),sQuery(id+"F0.wireOp",EDGE,"E1342"),sQuery(id+"F0.wireOp",EDGE,"E1343"),sQuery(id+"F0.wireOp",EDGE,"E1344"),sQuery(id+"F0.wireOp",EDGE,"E1345"),sQuery(id+"F0.wireOp",EDGE,"E1346"),sQuery(id+"F0.wireOp",EDGE,"E1347"),sQuery(id+"F0.wireOp",EDGE,"E1348"),sQuery(id+"F0.wireOp",EDGE,"E1349"),sQuery(id+"F0.wireOp",EDGE,"E1350"),sQuery(id+"F0.wireOp",EDGE,"E1351"),sQuery(id+"F0.wireOp",EDGE,"E1352"),sQuery(id+"F0.wireOp",EDGE,"E1353"),sQuery(id+"F0.wireOp",EDGE,"E1354"),sQuery(id+"F0.wireOp",EDGE,"E1355"),sQuery(id+"F0.wireOp",EDGE,"E1356"),sQuery(id+"F0.wireOp",EDGE,"E1357"),sQuery(id+"F0.wireOp",EDGE,"E1358"),sQuery(id+"F0.wireOp",EDGE,"E1359"),sQuery(id+"F0.wireOp",EDGE,"E1360"),sQuery(id+"F0.wireOp",EDGE,"E1361"),sQuery(id+"F0.wireOp",EDGE,"E1362"),sQuery(id+"F0.wireOp",EDGE,"E1363"),sQuery(id+"F0.wireOp",EDGE,"E1364"),sQuery(id+"F0.wireOp",EDGE,"E1365"),sQuery(id+"F0.wireOp",EDGE,"E1366"),sQuery(id+"F0.wireOp",EDGE,"E1367"),sQuery(id+"F0.wireOp",EDGE,"E1368"),sQuery(id+"F0.wireOp",EDGE,"E1369"),sQuery(id+"F0.wireOp",EDGE,"E1370"),sQuery(id+"F0.wireOp",EDGE,"E1371"),sQuery(id+"F0.wireOp",EDGE,"E1372"),sQuery(id+"F0.wireOp",EDGE,"E1373"),sQuery(id+"F0.wireOp",EDGE,"E1374"),sQuery(id+"F0.wireOp",EDGE,"E1375"),sQuery(id+"F0.wireOp",EDGE,"E1376"),sQuery(id+"F0.wireOp",EDGE,"E1377"),sQuery(id+"F0.wireOp",EDGE,"E1378"),sQuery(id+"F0.wireOp",EDGE,"E1379"),sQuery(id+"F0.wireOp",EDGE,"E1380"),sQuery(id+"F0.wireOp",EDGE,"E1381"),sQuery(id+"F0.wireOp",EDGE,"E1382"),sQuery(id+"F0.wireOp",EDGE,"E1383"),sQuery(id+"F0.wireOp",EDGE,"E1384"),sQuery(id+"F0.wireOp",EDGE,"E1385"),sQuery(id+"F0.wireOp",EDGE,"E1386"),sQuery(id+"F0.wireOp",EDGE,"E1387"),sQuery(id+"F0.wireOp",EDGE,"E1388"),sQuery(id+"F0.wireOp",EDGE,"E1389"),sQuery(id+"F0.wireOp",EDGE,"E1390"),sQuery(id+"F0.wireOp",EDGE,"E1391"),sQuery(id+"F0.wireOp",EDGE,"E1392"),sQuery(id+"F0.wireOp",EDGE,"E1393"),sQuery(id+"F0.wireOp",EDGE,"E1394"),sQuery(id+"F0.wireOp",EDGE,"E1395"),sQuery(id+"F0.wireOp",EDGE,"E1396"),sQuery(id+"F0.wireOp",EDGE,"E1397"),sQuery(id+"F0.wireOp",EDGE,"E1398"),sQuery(id+"F0.wireOp",EDGE,"E1399"),sQuery(id+"F0.wireOp",EDGE,"E1400"),sQuery(id+"F0.wireOp",EDGE,"E1401"),sQuery(id+"F0.wireOp",EDGE,"E1402"),sQuery(id+"F0.wireOp",EDGE,"E1403"),sQuery(id+"F0.wireOp",EDGE,"E1404"),sQuery(id+"F0.wireOp",EDGE,"E1405"),sQuery(id+"F0.wireOp",EDGE,"E1406"),sQuery(id+"F0.wireOp",EDGE,"E1407"),sQuery(id+"F0.wireOp",EDGE,"E1408"),sQuery(id+"F0.wireOp",EDGE,"E1409"),sQuery(id+"F0.wireOp",EDGE,"E1410"),sQuery(id+"F0.wireOp",EDGE,"E1411"),sQuery(id+"F0.wireOp",EDGE,"E1412"),sQuery(id+"F0.wireOp",EDGE,"E1413"),sQuery(id+"F0.wireOp",EDGE,"E1414"),sQuery(id+"F0.wireOp",EDGE,"E1415"),sQuery(id+"F0.wireOp",EDGE,"E1416"),sQuery(id+"F0.wireOp",EDGE,"E1417"),sQuery(id+"F0.wireOp",EDGE,"E1418"),sQuery(id+"F0.wireOp",EDGE,"E1419"),sQuery(id+"F0.wireOp",EDGE,"E1420"),sQuery(id+"F0.wireOp",EDGE,"E1421"),sQuery(id+"F0.wireOp",EDGE,"E1422"),sQuery(id+"F0.wireOp",EDGE,"E1423"),sQuery(id+"F0.wireOp",EDGE,"E1424"),sQuery(id+"F0.wireOp",EDGE,"E1425"),sQuery(id+"F0.wireOp",EDGE,"E1426"),sQuery(id+"F0.wireOp",EDGE,"E1427"),sQuery(id+"F0.wireOp",EDGE,"E1428"),sQuery(id+"F0.wireOp",EDGE,"E1429"),sQuery(id+"F0.wireOp",EDGE,"E1430"),sQuery(id+"F0.wireOp",EDGE,"E1431"),sQuery(id+"F0.wireOp",EDGE,"E1432"),sQuery(id+"F0.wireOp",EDGE,"E1433"),sQuery(id+"F0.wireOp",EDGE,"E1434"),sQuery(id+"F0.wireOp",EDGE,"E1435"),sQuery(id+"F0.wireOp",EDGE,"E1436"),sQuery(id+"F0.wireOp",EDGE,"E1437"),sQuery(id+"F0.wireOp",EDGE,"E1438"),sQuery(id+"F0.wireOp",EDGE,"E1439"),sQuery(id+"F0.wireOp",EDGE,"E1440"),sQuery(id+"F0.wireOp",EDGE,"E1441"),sQuery(id+"F0.wireOp",EDGE,"E1442"),sQuery(id+"F0.wireOp",EDGE,"E1443"),sQuery(id+"F0.wireOp",EDGE,"E1444"),sQuery(id+"F0.wireOp",EDGE,"E1445"),sQuery(id+"F0.wireOp",EDGE,"E1446"),sQuery(id+"F0.wireOp",EDGE,"E1447"),sQuery(id+"F0.wireOp",EDGE,"E1448"),sQuery(id+"F0.wireOp",EDGE,"E1449"),sQuery(id+"F0.wireOp",EDGE,"E1450"),sQuery(id+"F0.wireOp",EDGE,"E1451"),sQuery(id+"F0.wireOp",EDGE,"E1452"),sQuery(id+"F0.wireOp",EDGE,"E1453"),sQuery(id+"F0.wireOp",EDGE,"E1454"),sQuery(id+"F0.wireOp",EDGE,"E1455"),sQuery(id+"F0.wireOp",EDGE,"E1456"),sQuery(id+"F0.wireOp",EDGE,"E1457"),sQuery(id+"F0.wireOp",EDGE,"E1458"),sQuery(id+"F0.wireOp",EDGE,"E1459"),sQuery(id+"F0.wireOp",EDGE,"E1460"),sQuery(id+"F0.wireOp",EDGE,"E1461"),sQuery(id+"F0.wireOp",EDGE,"E1462"),sQuery(id+"F0.wireOp",EDGE,"E1463"),sQuery(id+"F0.wireOp",EDGE,"E1464"),sQuery(id+"F0.wireOp",EDGE,"E1465"),sQuery(id+"F0.wireOp",EDGE,"E1466"),sQuery(id+"F0.wireOp",EDGE,"E1467"),sQuery(id+"F0.wireOp",EDGE,"E1468"),sQuery(id+"F0.wireOp",EDGE,"E1469"),sQuery(id+"F0.wireOp",EDGE,"E1470"),sQuery(id+"F0.wireOp",EDGE,"E1471"),sQuery(id+"F0.wireOp",EDGE,"E1472"),sQuery(id+"F0.wireOp",EDGE,"E1473"),sQuery(id+"F0.wireOp",EDGE,"E1474"),sQuery(id+"F0.wireOp",EDGE,"E1475"),sQuery(id+"F0.wireOp",EDGE,"E1476"),sQuery(id+"F0.wireOp",EDGE,"E1477"),sQuery(id+"F0.wireOp",EDGE,"E1478"),sQuery(id+"F0.wireOp",EDGE,"E1479"),sQuery(id+"F0.wireOp",EDGE,"E1480"),sQuery(id+"F0.wireOp",EDGE,"E1481"),sQuery(id+"F0.wireOp",EDGE,"E1482"),sQuery(id+"F0.wireOp",EDGE,"E1483"),sQuery(id+"F0.wireOp",EDGE,"E1484"),sQuery(id+"F0.wireOp",EDGE,"E1485"),sQuery(id+"F0.wireOp",EDGE,"E1486"),sQuery(id+"F0.wireOp",EDGE,"E1487"),sQuery(id+"F0.wireOp",EDGE,"E1488"),sQuery(id+"F0.wireOp",EDGE,"E1489"),sQuery(id+"F0.wireOp",EDGE,"E1490"),sQuery(id+"F0.wireOp",EDGE,"E1491"),sQuery(id+"F0.wireOp",EDGE,"E1492"),sQuery(id+"F0.wireOp",EDGE,"E1493"),sQuery(id+"F0.wireOp",EDGE,"E1494"),sQuery(id+"F0.wireOp",EDGE,"E1495"),sQuery(id+"F0.wireOp",EDGE,"E1496"),sQuery(id+"F0.wireOp",EDGE,"E1497"),sQuery(id+"F0.wireOp",EDGE,"E1498"),sQuery(id+"F0.wireOp",EDGE,"E1499"),sQuery(id+"F0.wireOp",EDGE,"E1500"),sQuery(id+"F0.wireOp",EDGE,"E1501"),sQuery(id+"F0.wireOp",EDGE,"E1502"),sQuery(id+"F0.wireOp",EDGE,"E1503"),sQuery(id+"F0.wireOp",EDGE,"E1504"),sQuery(id+"F0.wireOp",EDGE,"E1505"),sQuery(id+"F0.wireOp",EDGE,"E1506"),sQuery(id+"F0.wireOp",EDGE,"E1507"),sQuery(id+"F0.wireOp",EDGE,"E1508"),sQuery(id+"F0.wireOp",EDGE,"E1509"),sQuery(id+"F0.wireOp",EDGE,"E1510"),sQuery(id+"F0.wireOp",EDGE,"E1511"),sQuery(id+"F0.wireOp",EDGE,"E1512"),sQuery(id+"F0.wireOp",EDGE,"E1513"),sQuery(id+"F0.wireOp",EDGE,"E1514"),sQuery(id+"F0.wireOp",EDGE,"E1515"),sQuery(id+"F0.wireOp",EDGE,"E1516"),sQuery(id+"F0.wireOp",EDGE,"E1517"),sQuery(id+"F0.wireOp",EDGE,"E1518"),sQuery(id+"F0.wireOp",EDGE,"E1519"),sQuery(id+"F0.wireOp",EDGE,"E1520"),sQuery(id+"F0.wireOp",EDGE,"E1521"),sQuery(id+"F0.wireOp",EDGE,"E1522"),sQuery(id+"F0.wireOp",EDGE,"E1523"),sQuery(id+"F0.wireOp",EDGE,"E1524"),sQuery(id+"F0.wireOp",EDGE,"E1525"),sQuery(id+"F0.wireOp",EDGE,"E1526"),sQuery(id+"F0.wireOp",EDGE,"E1527"),sQuery(id+"F0.wireOp",EDGE,"E1528"),sQuery(id+"F0.wireOp",EDGE,"E1529"),sQuery(id+"F0.wireOp",EDGE,"E1530"),sQuery(id+"F0.wireOp",EDGE,"E1531"),sQuery(id+"F0.wireOp",EDGE,"E1532"),sQuery(id+"F0.wireOp",EDGE,"E1533"),sQuery(id+"F0.wireOp",EDGE,"E1534"),sQuery(id+"F0.wireOp",EDGE,"E1535"),sQuery(id+"F0.wireOp",EDGE,"E1536"),sQuery(id+"F0.wireOp",EDGE,"E1537"),sQuery(id+"F0.wireOp",EDGE,"E1538"),sQuery(id+"F0.wireOp",EDGE,"E1539"),sQuery(id+"F0.wireOp",EDGE,"E1540"),sQuery(id+"F0.wireOp",EDGE,"E1541"),sQuery(id+"F0.wireOp",EDGE,"E1542"),sQuery(id+"F0.wireOp",EDGE,"E1543"),sQuery(id+"F0.wireOp",EDGE,"E1544"),sQuery(id+"F0.wireOp",EDGE,"E1545"),sQuery(id+"F0.wireOp",EDGE,"E1546"),sQuery(id+"F0.wireOp",EDGE,"E1547"),sQuery(id+"F0.wireOp",EDGE,"E1548"),sQuery(id+"F0.wireOp",EDGE,"E1549"),sQuery(id+"F0.wireOp",EDGE,"E1550"),sQuery(id+"F0.wireOp",EDGE,"E1551"),sQuery(id+"F0.wireOp",EDGE,"E1552"),sQuery(id+"F0.wireOp",EDGE,"E1553"),sQuery(id+"F0.wireOp",EDGE,"E1554"),sQuery(id+"F0.wireOp",EDGE,"E1555"),sQuery(id+"F0.wireOp",EDGE,"E1556"),sQuery(id+"F0.wireOp",EDGE,"E1557"),sQuery(id+"F0.wireOp",EDGE,"E1558"),sQuery(id+"F0.wireOp",EDGE,"E1559"),sQuery(id+"F0.wireOp",EDGE,"E1560"),sQuery(id+"F0.wireOp",EDGE,"E1561"),sQuery(id+"F0.wireOp",EDGE,"E1562"),sQuery(id+"F0.wireOp",EDGE,"E1563"),sQuery(id+"F0.wireOp",EDGE,"E1564"),sQuery(id+"F0.wireOp",EDGE,"E1565"),sQuery(id+"F0.wireOp",EDGE,"E1566"),sQuery(id+"F0.wireOp",EDGE,"E1567"),sQuery(id+"F0.wireOp",EDGE,"E1568"),sQuery(id+"F0.wireOp",EDGE,"E1569"),sQuery(id+"F0.wireOp",EDGE,"E1570"),sQuery(id+"F0.wireOp",EDGE,"E1571"),sQuery(id+"F0.wireOp",EDGE,"E1572"),sQuery(id+"F0.wireOp",EDGE,"E1573"),sQuery(id+"F0.wireOp",EDGE,"E1574"),sQuery(id+"F0.wireOp",EDGE,"E1575"),sQuery(id+"F0.wireOp",EDGE,"E1576"),sQuery(id+"F0.wireOp",EDGE,"E1577"),sQuery(id+"F0.wireOp",EDGE,"E1578"),sQuery(id+"F0.wireOp",EDGE,"E1579"),sQuery(id+"F0.wireOp",EDGE,"E1580"),sQuery(id+"F0.wireOp",EDGE,"E1581"),sQuery(id+"F0.wireOp",EDGE,"E1582"),sQuery(id+"F0.wireOp",EDGE,"E1583"),sQuery(id+"F0.wireOp",EDGE,"E1584"),sQuery(id+"F0.wireOp",EDGE,"E1585"),sQuery(id+"F0.wireOp",EDGE,"E1586"),sQuery(id+"F0.wireOp",EDGE,"E1587"),sQuery(id+"F0.wireOp",EDGE,"E1588"),sQuery(id+"F0.wireOp",EDGE,"E1589"),sQuery(id+"F0.wireOp",EDGE,"E1590"),sQuery(id+"F0.wireOp",EDGE,"E1591"),sQuery(id+"F0.wireOp",EDGE,"E1592"),sQuery(id+"F0.wireOp",EDGE,"E1593"),sQuery(id+"F0.wireOp",EDGE,"E1594"),sQuery(id+"F0.wireOp",EDGE,"E1595"),sQuery(id+"F0.wireOp",EDGE,"E1596"),sQuery(id+"F0.wireOp",EDGE,"E1597"),sQuery(id+"F0.wireOp",EDGE,"E1598"),sQuery(id+"F0.wireOp",EDGE,"E1599"),sQuery(id+"F0.wireOp",EDGE,"E1600"),sQuery(id+"F0.wireOp",EDGE,"E1601"),sQuery(id+"F0.wireOp",EDGE,"E1602"),sQuery(id+"F0.wireOp",EDGE,"E1603"),sQuery(id+"F0.wireOp",EDGE,"E1604"),sQuery(id+"F0.wireOp",EDGE,"E1605"),sQuery(id+"F0.wireOp",EDGE,"E1606"),sQuery(id+"F0.wireOp",EDGE,"E1607"),sQuery(id+"F0.wireOp",EDGE,"E1608"),sQuery(id+"F0.wireOp",EDGE,"E1609"),sQuery(id+"F0.wireOp",EDGE,"E1610"),sQuery(id+"F0.wireOp",EDGE,"E1611"),sQuery(id+"F0.wireOp",EDGE,"E1612"),sQuery(id+"F0.wireOp",EDGE,"E1613"),sQuery(id+"F0.wireOp",EDGE,"E1614"),sQuery(id+"F0.wireOp",EDGE,"E1615"),sQuery(id+"F0.wireOp",EDGE,"E1616"),sQuery(id+"F0.wireOp",EDGE,"E1617"),sQuery(id+"F0.wireOp",EDGE,"E1618"),sQuery(id+"F0.wireOp",EDGE,"E1619"),sQuery(id+"F0.wireOp",EDGE,"E1620"),sQuery(id+"F0.wireOp",EDGE,"E1621"),sQuery(id+"F0.wireOp",EDGE,"E1622"),sQuery(id+"F0.wireOp",EDGE,"E1623"),sQuery(id+"F0.wireOp",EDGE,"E1624"),sQuery(id+"F0.wireOp",EDGE,"E1625"),sQuery(id+"F0.wireOp",EDGE,"E1626"),sQuery(id+"F0.wireOp",EDGE,"E1627"),sQuery(id+"F0.wireOp",EDGE,"E1628"),sQuery(id+"F0.wireOp",EDGE,"E1629"),sQuery(id+"F0.wireOp",EDGE,"E1630"),sQuery(id+"F0.wireOp",EDGE,"E1631"),sQuery(id+"F0.wireOp",EDGE,"E1632"),sQuery(id+"F0.wireOp",EDGE,"E1633"),sQuery(id+"F0.wireOp",EDGE,"E1634"),sQuery(id+"F0.wireOp",EDGE,"E1635"),sQuery(id+"F0.wireOp",EDGE,"E1636"),sQuery(id+"F0.wireOp",EDGE,"E1637"),sQuery(id+"F0.wireOp",EDGE,"E1638"),sQuery(id+"F0.wireOp",EDGE,"E1639"),sQuery(id+"F0.wireOp",EDGE,"E1640"),sQuery(id+"F0.wireOp",EDGE,"E1641"),sQuery(id+"F0.wireOp",EDGE,"E1642"),sQuery(id+"F0.wireOp",EDGE,"E1643"),sQuery(id+"F0.wireOp",EDGE,"E1644"),sQuery(id+"F0.wireOp",EDGE,"E1645"),sQuery(id+"F0.wireOp",EDGE,"E1646"),sQuery(id+"F0.wireOp",EDGE,"E1647"),sQuery(id+"F0.wireOp",EDGE,"E1648"),sQuery(id+"F0.wireOp",EDGE,"E1649"),sQuery(id+"F0.wireOp",EDGE,"E1650"),sQuery(id+"F0.wireOp",EDGE,"E1651"),sQuery(id+"F0.wireOp",EDGE,"E1652"),sQuery(id+"F0.wireOp",EDGE,"E1653"),sQuery(id+"F0.wireOp",EDGE,"E1654"),sQuery(id+"F0.wireOp",EDGE,"E1655"),sQuery(id+"F0.wireOp",EDGE,"E1656"),sQuery(id+"F0.wireOp",EDGE,"E1657"),sQuery(id+"F0.wireOp",EDGE,"E1658"),sQuery(id+"F0.wireOp",EDGE,"E1659"),sQuery(id+"F0.wireOp",EDGE,"E1660"),sQuery(id+"F0.wireOp",EDGE,"E1661"),sQuery(id+"F0.wireOp",EDGE,"E1662"),sQuery(id+"F0.wireOp",EDGE,"E1663"),sQuery(id+"F0.wireOp",EDGE,"E1664"),sQuery(id+"F0.wireOp",EDGE,"E1665"),sQuery(id+"F0.wireOp",EDGE,"E1666"),sQuery(id+"F0.wireOp",EDGE,"E1667"),sQuery(id+"F0.wireOp",EDGE,"E1668"),sQuery(id+"F0.wireOp",EDGE,"E1669"),sQuery(id+"F0.wireOp",EDGE,"E1670"),sQuery(id+"F0.wireOp",EDGE,"E1671"),sQuery(id+"F0.wireOp",EDGE,"E1672"),sQuery(id+"F0.wireOp",EDGE,"E1673"),sQuery(id+"F0.wireOp",EDGE,"E1674"),sQuery(id+"F0.wireOp",EDGE,"E1675"),sQuery(id+"F0.wireOp",EDGE,"E1676"),sQuery(id+"F0.wireOp",EDGE,"E1677"),sQuery(id+"F0.wireOp",EDGE,"E1678"),sQuery(id+"F0.wireOp",EDGE,"E1679"),sQuery(id+"F0.wireOp",EDGE,"E1680"),sQuery(id+"F0.wireOp",EDGE,"E1681"),sQuery(id+"F0.wireOp",EDGE,"E1682"),sQuery(id+"F0.wireOp",EDGE,"E1683"),sQuery(id+"F0.wireOp",EDGE,"E1684"),sQuery(id+"F0.wireOp",EDGE,"E1685"),sQuery(id+"F0.wireOp",EDGE,"E1686"),sQuery(id+"F0.wireOp",EDGE,"E1687"),sQuery(id+"F0.wireOp",EDGE,"E1688"),sQuery(id+"F0.wireOp",EDGE,"E1689"),sQuery(id+"F0.wireOp",EDGE,"E1690"),sQuery(id+"F0.wireOp",EDGE,"E1691"),sQuery(id+"F0.wireOp",EDGE,"E1692"),sQuery(id+"F0.wireOp",EDGE,"E1693"),sQuery(id+"F0.wireOp",EDGE,"E1694"),sQuery(id+"F0.wireOp",EDGE,"E1695"),sQuery(id+"F0.wireOp",EDGE,"E1696"),sQuery(id+"F0.wireOp",EDGE,"E1697"),sQuery(id+"F0.wireOp",EDGE,"E1698"),sQuery(id+"F0.wireOp",EDGE,"E1699"),sQuery(id+"F0.wireOp",EDGE,"E1700"),sQuery(id+"F0.wireOp",EDGE,"E1701"),sQuery(id+"F0.wireOp",EDGE,"E1702"),sQuery(id+"F0.wireOp",EDGE,"E1703"),sQuery(id+"F0.wireOp",EDGE,"E1704"),sQuery(id+"F0.wireOp",EDGE,"E1705"),sQuery(id+"F0.wireOp",EDGE,"E1706"),sQuery(id+"F0.wireOp",EDGE,"E1707"),sQuery(id+"F0.wireOp",EDGE,"E1708"),sQuery(id+"F0.wireOp",EDGE,"E1709"),sQuery(id+"F0.wireOp",EDGE,"E1710"),sQuery(id+"F0.wireOp",EDGE,"E1711"),sQuery(id+"F0.wireOp",EDGE,"E1712"),sQuery(id+"F0.wireOp",EDGE,"E1713"),sQuery(id+"F0.wireOp",EDGE,"E1714"),sQuery(id+"F0.wireOp",EDGE,"E1715"),sQuery(id+"F0.wireOp",EDGE,"E1716"),sQuery(id+"F0.wireOp",EDGE,"E1717"),sQuery(id+"F0.wireOp",EDGE,"E1718"),sQuery(id+"F0.wireOp",EDGE,"E1719"),sQuery(id+"F0.wireOp",EDGE,"E1720"),sQuery(id+"F0.wireOp",EDGE,"E1721"),sQuery(id+"F0.wireOp",EDGE,"E1722"),sQuery(id+"F0.wireOp",EDGE,"E1723"),sQuery(id+"F0.wireOp",EDGE,"E1724"),sQuery(id+"F0.wireOp",EDGE,"E1725"),sQuery(id+"F0.wireOp",EDGE,"E1726"),sQuery(id+"F0.wireOp",EDGE,"E1727"),sQuery(id+"F0.wireOp",EDGE,"E1728"),sQuery(id+"F0.wireOp",EDGE,"E1729"),sQuery(id+"F0.wireOp",EDGE,"E1730"),sQuery(id+"F0.wireOp",EDGE,"E1731"),sQuery(id+"F0.wireOp",EDGE,"E1732"),sQuery(id+"F0.wireOp",EDGE,"E1733"),sQuery(id+"F0.wireOp",EDGE,"E1734"),sQuery(id+"F0.wireOp",EDGE,"E1735"),sQuery(id+"F0.wireOp",EDGE,"E1736"),sQuery(id+"F0.wireOp",EDGE,"E1737"),sQuery(id+"F0.wireOp",EDGE,"E1738"),sQuery(id+"F0.wireOp",EDGE,"E1739"),sQuery(id+"F0.wireOp",EDGE,"E1740"),sQuery(id+"F0.wireOp",EDGE,"E1741"),sQuery(id+"F0.wireOp",EDGE,"E1742"),sQuery(id+"F0.wireOp",EDGE,"E1743"),sQuery(id+"F0.wireOp",EDGE,"E1744"),sQuery(id+"F0.wireOp",EDGE,"E1745"),sQuery(id+"F0.wireOp",EDGE,"E1746"),sQuery(id+"F0.wireOp",EDGE,"E1747"),sQuery(id+"F0.wireOp",EDGE,"E1748"),sQuery(id+"F0.wireOp",EDGE,"E1749"),sQuery(id+"F0.wireOp",EDGE,"E1750"),sQuery(id+"F0.wireOp",EDGE,"E1751"),sQuery(id+"F0.wireOp",EDGE,"E1752"),sQuery(id+"F0.wireOp",EDGE,"E1753"),sQuery(id+"F0.wireOp",EDGE,"E1754"),sQuery(id+"F0.wireOp",EDGE,"E1755"),sQuery(id+"F0.wireOp",EDGE,"E1756"),sQuery(id+"F0.wireOp",EDGE,"E1757"),sQuery(id+"F0.wireOp",EDGE,"E1758"),sQuery(id+"F0.wireOp",EDGE,"E1759"),sQuery(id+"F0.wireOp",EDGE,"E1760"),sQuery(id+"F0.wireOp",EDGE,"E1761"),sQuery(id+"F0.wireOp",EDGE,"E1762"),sQuery(id+"F0.wireOp",EDGE,"E1763"),sQuery(id+"F0.wireOp",EDGE,"E1764"),sQuery(id+"F0.wireOp",EDGE,"E1765"),sQuery(id+"F0.wireOp",EDGE,"E1766"),sQuery(id+"F0.wireOp",EDGE,"E1767"),sQuery(id+"F0.wireOp",EDGE,"E1768"),sQuery(id+"F0.wireOp",EDGE,"E1769"),sQuery(id+"F0.wireOp",EDGE,"E1770"),sQuery(id+"F0.wireOp",EDGE,"E1771"),sQuery(id+"F0.wireOp",EDGE,"E1772"),sQuery(id+"F0.wireOp",EDGE,"E1773"),sQuery(id+"F0.wireOp",EDGE,"E1774"),sQuery(id+"F0.wireOp",EDGE,"E1775"),sQuery(id+"F0.wireOp",EDGE,"E1776"),sQuery(id+"F0.wireOp",EDGE,"E1777"),sQuery(id+"F0.wireOp",EDGE,"E1778"),sQuery(id+"F0.wireOp",EDGE,"E1779"),sQuery(id+"F0.wireOp",EDGE,"E1780"),sQuery(id+"F0.wireOp",EDGE,"E1781"),sQuery(id+"F0.wireOp",EDGE,"E1782"),sQuery(id+"F0.wireOp",EDGE,"E1783"),sQuery(id+"F0.wireOp",EDGE,"E1784"),sQuery(id+"F0.wireOp",EDGE,"E1785"),sQuery(id+"F0.wireOp",EDGE,"E1786"),sQuery(id+"F0.wireOp",EDGE,"E1787"),sQuery(id+"F0.wireOp",EDGE,"E1788"),sQuery(id+"F0.wireOp",EDGE,"E1789"),sQuery(id+"F0.wireOp",EDGE,"E1790"),sQuery(id+"F0.wireOp",EDGE,"E1791"),sQuery(id+"F0.wireOp",EDGE,"E1792"),sQuery(id+"F0.wireOp",EDGE,"E1793"),sQuery(id+"F0.wireOp",EDGE,"E1794"),sQuery(id+"F0.wireOp",EDGE,"E1795"),sQuery(id+"F0.wireOp",EDGE,"E1796"),sQuery(id+"F0.wireOp",EDGE,"E1797"),sQuery(id+"F0.wireOp",EDGE,"E1798"),sQuery(id+"F0.wireOp",EDGE,"E1799"),sQuery(id+"F0.wireOp",EDGE,"E1800"),sQuery(id+"F0.wireOp",EDGE,"E1801"),sQuery(id+"F0.wireOp",EDGE,"E1802"),sQuery(id+"F0.wireOp",EDGE,"E1803"),sQuery(id+"F0.wireOp",EDGE,"E1804"),sQuery(id+"F0.wireOp",EDGE,"E1805"),sQuery(id+"F0.wireOp",EDGE,"E1806"),sQuery(id+"F0.wireOp",EDGE,"E1807"),sQuery(id+"F0.wireOp",EDGE,"E1808"),sQuery(id+"F0.wireOp",EDGE,"E1809"),sQuery(id+"F0.wireOp",EDGE,"E1810"),sQuery(id+"F0.wireOp",EDGE,"E1811"),sQuery(id+"F0.wireOp",EDGE,"E1812"),sQuery(id+"F0.wireOp",EDGE,"E1813"),sQuery(id+"F0.wireOp",EDGE,"E1814"),sQuery(id+"F0.wireOp",EDGE,"E1815"),sQuery(id+"F0.wireOp",EDGE,"E1816"),sQuery(id+"F0.wireOp",EDGE,"E1817"),sQuery(id+"F0.wireOp",EDGE,"E1818"),sQuery(id+"F0.wireOp",EDGE,"E1819"),sQuery(id+"F0.wireOp",EDGE,"E1820"),sQuery(id+"F0.wireOp",EDGE,"E1821"),sQuery(id+"F0.wireOp",EDGE,"E1822"),sQuery(id+"F0.wireOp",EDGE,"E1823"),sQuery(id+"F0.wireOp",EDGE,"E1824"),sQuery(id+"F0.wireOp",EDGE,"E1825"),sQuery(id+"F0.wireOp",EDGE,"E1826"),sQuery(id+"F0.wireOp",EDGE,"E1827"),sQuery(id+"F0.wireOp",EDGE,"E1828"),sQuery(id+"F0.wireOp",EDGE,"E1829"),sQuery(id+"F0.wireOp",EDGE,"E1830"),sQuery(id+"F0.wireOp",EDGE,"E1831"),sQuery(id+"F0.wireOp",EDGE,"E1832"),sQuery(id+"F0.wireOp",EDGE,"E1833"),sQuery(id+"F0.wireOp",EDGE,"E1834"),sQuery(id+"F0.wireOp",EDGE,"E1835"),sQuery(id+"F0.wireOp",EDGE,"E1836"),sQuery(id+"F0.wireOp",EDGE,"E1837"),sQuery(id+"F0.wireOp",EDGE,"E1838"),sQuery(id+"F0.wireOp",EDGE,"E1839"),sQuery(id+"F0.wireOp",EDGE,"E1840"),sQuery(id+"F0.wireOp",EDGE,"E1841"),sQuery(id+"F0.wireOp",EDGE,"E1842"),sQuery(id+"F0.wireOp",EDGE,"E1843"),sQuery(id+"F0.wireOp",EDGE,"E1844"),sQuery(id+"F0.wireOp",EDGE,"E1845"),sQuery(id+"F0.wireOp",EDGE,"E1846"),sQuery(id+"F0.wireOp",EDGE,"E1847"),sQuery(id+"F0.wireOp",EDGE,"E1848"),sQuery(id+"F0.wireOp",EDGE,"E1849"),sQuery(id+"F0.wireOp",EDGE,"E1850"),sQuery(id+"F0.wireOp",EDGE,"E1851"),sQuery(id+"F0.wireOp",EDGE,"E1852"),sQuery(id+"F0.wireOp",EDGE,"E1853"),sQuery(id+"F0.wireOp",EDGE,"E1854"),sQuery(id+"F0.wireOp",EDGE,"E1855"),sQuery(id+"F0.wireOp",EDGE,"E1856"),sQuery(id+"F0.wireOp",EDGE,"E1857"),sQuery(id+"F0.wireOp",EDGE,"E1858"),sQuery(id+"F0.wireOp",EDGE,"E1859"),sQuery(id+"F0.wireOp",EDGE,"E1860"),sQuery(id+"F0.wireOp",EDGE,"E1861"),sQuery(id+"F0.wireOp",EDGE,"E1862"),sQuery(id+"F0.wireOp",EDGE,"E1863"),sQuery(id+"F0.wireOp",EDGE,"E1864"),sQuery(id+"F0.wireOp",EDGE,"E1865"),sQuery(id+"F0.wireOp",EDGE,"E1866"),sQuery(id+"F0.wireOp",EDGE,"E1867"),sQuery(id+"F0.wireOp",EDGE,"E1868"),sQuery(id+"F0.wireOp",EDGE,"E1869"),sQuery(id+"F0.wireOp",EDGE,"E1870"),sQuery(id+"F0.wireOp",EDGE,"E1871"),sQuery(id+"F0.wireOp",EDGE,"E1872"),sQuery(id+"F0.wireOp",EDGE,"E1873"),sQuery(id+"F0.wireOp",EDGE,"E1874"),sQuery(id+"F0.wireOp",EDGE,"E1875"),sQuery(id+"F0.wireOp",EDGE,"E1876"),sQuery(id+"F0.wireOp",EDGE,"E1877"),sQuery(id+"F0.wireOp",EDGE,"E1878"),sQuery(id+"F0.wireOp",EDGE,"E1879"),sQuery(id+"F0.wireOp",EDGE,"E1880"),sQuery(id+"F0.wireOp",EDGE,"E1881"),sQuery(id+"F0.wireOp",EDGE,"E1882"),sQuery(id+"F0.wireOp",EDGE,"E1883"),sQuery(id+"F0.wireOp",EDGE,"E1884"),sQuery(id+"F0.wireOp",EDGE,"E1885"),sQuery(id+"F0.wireOp",EDGE,"E1886"),sQuery(id+"F0.wireOp",EDGE,"E1887"),sQuery(id+"F0.wireOp",EDGE,"E1888"),sQuery(id+"F0.wireOp",EDGE,"E1889"),sQuery(id+"F0.wireOp",EDGE,"E1890"),sQuery(id+"F0.wireOp",EDGE,"E1891"),sQuery(id+"F0.wireOp",EDGE,"E1892"),sQuery(id+"F0.wireOp",EDGE,"E1893"),sQuery(id+"F0.wireOp",EDGE,"E1894"),sQuery(id+"F0.wireOp",EDGE,"E1895"),sQuery(id+"F0.wireOp",EDGE,"E1896"),sQuery(id+"F0.wireOp",EDGE,"E1897"),sQuery(id+"F0.wireOp",EDGE,"E1898"),sQuery(id+"F0.wireOp",EDGE,"E1899"),sQuery(id+"F0.wireOp",EDGE,"E1900"),sQuery(id+"F0.wireOp",EDGE,"E1901"),sQuery(id+"F0.wireOp",EDGE,"E1902"),sQuery(id+"F0.wireOp",EDGE,"E1903"),sQuery(id+"F0.wireOp",EDGE,"E1904"),sQuery(id+"F0.wireOp",EDGE,"E1905"),sQuery(id+"F0.wireOp",EDGE,"E1906"),sQuery(id+"F0.wireOp",EDGE,"E1907"),sQuery(id+"F0.wireOp",EDGE,"E1908"),sQuery(id+"F0.wireOp",EDGE,"E1909"),sQuery(id+"F0.wireOp",EDGE,"E1910"),sQuery(id+"F0.wireOp",EDGE,"E1911"),sQuery(id+"F0.wireOp",EDGE,"E1912"),sQuery(id+"F0.wireOp",EDGE,"E1913"),sQuery(id+"F0.wireOp",EDGE,"E1914"),sQuery(id+"F0.wireOp",EDGE,"E1915"),sQuery(id+"F0.wireOp",EDGE,"E1916"),sQuery(id+"F0.wireOp",EDGE,"E1917"),sQuery(id+"F0.wireOp",EDGE,"E1918"),sQuery(id+"F0.wireOp",EDGE,"E1919"),sQuery(id+"F0.wireOp",EDGE,"E1920"),sQuery(id+"F0.wireOp",EDGE,"E1921"),sQuery(id+"F0.wireOp",EDGE,"E1922"),sQuery(id+"F0.wireOp",EDGE,"E1923"),sQuery(id+"F0.wireOp",EDGE,"E1924"),sQuery(id+"F0.wireOp",EDGE,"E1925"),sQuery(id+"F0.wireOp",EDGE,"E1926"),sQuery(id+"F0.wireOp",EDGE,"E1927"),sQuery(id+"F0.wireOp",EDGE,"E1928"),sQuery(id+"F0.wireOp",EDGE,"E1929"),sQuery(id+"F0.wireOp",EDGE,"E1930"),sQuery(id+"F0.wireOp",EDGE,"E1931"),sQuery(id+"F0.wireOp",EDGE,"E1932"),sQuery(id+"F0.wireOp",EDGE,"E1933"),sQuery(id+"F0.wireOp",EDGE,"E1934"),sQuery(id+"F0.wireOp",EDGE,"E1935"),sQuery(id+"F0.wireOp",EDGE,"E1936"),sQuery(id+"F0.wireOp",EDGE,"E1937"),sQuery(id+"F0.wireOp",EDGE,"E1938"),sQuery(id+"F0.wireOp",EDGE,"E1939"),sQuery(id+"F0.wireOp",EDGE,"E1940"),sQuery(id+"F0.wireOp",EDGE,"E1941"),sQuery(id+"F0.wireOp",EDGE,"E1942"),sQuery(id+"F0.wireOp",EDGE,"E1943"),sQuery(id+"F0.wireOp",EDGE,"E1944"),sQuery(id+"F0.wireOp",EDGE,"E1945"),sQuery(id+"F0.wireOp",EDGE,"E1946"),sQuery(id+"F0.wireOp",EDGE,"E1947"),sQuery(id+"F0.wireOp",EDGE,"E1948"),sQuery(id+"F0.wireOp",EDGE,"E1949"),sQuery(id+"F0.wireOp",EDGE,"E1950"),sQuery(id+"F0.wireOp",EDGE,"E1951"),sQuery(id+"F0.wireOp",EDGE,"E1952"),sQuery(id+"F0.wireOp",EDGE,"E1953"),sQuery(id+"F0.wireOp",EDGE,"E1954"),sQuery(id+"F0.wireOp",EDGE,"E1955"),sQuery(id+"F0.wireOp",EDGE,"E1956"),sQuery(id+"F0.wireOp",EDGE,"E1957"),sQuery(id+"F0.wireOp",EDGE,"E1958"),sQuery(id+"F0.wireOp",EDGE,"E1959"),sQuery(id+"F0.wireOp",EDGE,"E1960"),sQuery(id+"F0.wireOp",EDGE,"E1961"),sQuery(id+"F0.wireOp",EDGE,"E1962"),sQuery(id+"F0.wireOp",EDGE,"E1963"),sQuery(id+"F0.wireOp",EDGE,"E1964"),sQuery(id+"F0.wireOp",EDGE,"E1965"),sQuery(id+"F0.wireOp",EDGE,"E1966"),sQuery(id+"F0.wireOp",EDGE,"E1967"),sQuery(id+"F0.wireOp",EDGE,"E1968"),sQuery(id+"F0.wireOp",EDGE,"E1969"),sQuery(id+"F0.wireOp",EDGE,"E1970"),sQuery(id+"F0.wireOp",EDGE,"E1971"),sQuery(id+"F0.wireOp",EDGE,"E1972"),sQuery(id+"F0.wireOp",EDGE,"E1973"),sQuery(id+"F0.wireOp",EDGE,"E1974"),sQuery(id+"F0.wireOp",EDGE,"E1975"),sQuery(id+"F0.wireOp",EDGE,"E1976"),sQuery(id+"F0.wireOp",EDGE,"E1977"),sQuery(id+"F0.wireOp",EDGE,"E1978"),sQuery(id+"F0.wireOp",EDGE,"E1979"),sQuery(id+"F0.wireOp",EDGE,"E1980"),sQuery(id+"F0.wireOp",EDGE,"E1981"),sQuery(id+"F0.wireOp",EDGE,"E1982"),sQuery(id+"F0.wireOp",EDGE,"E1983"),sQuery(id+"F0.wireOp",EDGE,"E1984"),sQuery(id+"F0.wireOp",EDGE,"E1985"),sQuery(id+"F0.wireOp",EDGE,"E1986"),sQuery(id+"F0.wireOp",EDGE,"E1987"),sQuery(id+"F0.wireOp",EDGE,"E1988"),sQuery(id+"F0.wireOp",EDGE,"E1989"),sQuery(id+"F0.wireOp",EDGE,"E1990"),sQuery(id+"F0.wireOp",EDGE,"E1991"),sQuery(id+"F0.wireOp",EDGE,"E1992"),sQuery(id+"F0.wireOp",EDGE,"E1993"),sQuery(id+"F0.wireOp",EDGE,"E1994"),sQuery(id+"F0.wireOp",EDGE,"E1995"),sQuery(id+"F0.wireOp",EDGE,"E1996"),sQuery(id+"F0.wireOp",EDGE,"E1997"),sQuery(id+"F0.wireOp",EDGE,"E1998"),sQuery(id+"F0.wireOp",EDGE,"E1999"),sQuery(id+"F0.wireOp",EDGE,"E2000"),sQuery(id+"F0.wireOp",EDGE,"E2001"),sQuery(id+"F0.wireOp",EDGE,"E2002"),sQuery(id+"F0.wireOp",EDGE,"E2003"),sQuery(id+"F0.wireOp",EDGE,"E2004"),sQuery(id+"F0.wireOp",EDGE,"E2005"),sQuery(id+"F0.wireOp",EDGE,"E2006"),sQuery(id+"F0.wireOp",EDGE,"E2007"),sQuery(id+"F0.wireOp",EDGE,"E2008"),sQuery(id+"F0.wireOp",EDGE,"E2009"),sQuery(id+"F0.wireOp",EDGE,"E2010"),sQuery(id+"F0.wireOp",EDGE,"E2011"),sQuery(id+"F0.wireOp",EDGE,"E2012"),sQuery(id+"F0.wireOp",EDGE,"E2013"),sQuery(id+"F0.wireOp",EDGE,"E2014"),sQuery(id+"F0.wireOp",EDGE,"E2015"),sQuery(id+"F0.wireOp",EDGE,"E2016"),sQuery(id+"F0.wireOp",EDGE,"E2017"),sQuery(id+"F0.wireOp",EDGE,"E2018"),sQuery(id+"F0.wireOp",EDGE,"E2019"),sQuery(id+"F0.wireOp",EDGE,"E2020"),sQuery(id+"F0.wireOp",EDGE,"E2021"),sQuery(id+"F0.wireOp",EDGE,"E2022"),sQuery(id+"F0.wireOp",EDGE,"E2023"),sQuery(id+"F0.wireOp",EDGE,"E2024"),sQuery(id+"F0.wireOp",EDGE,"E2025"),sQuery(id+"F0.wireOp",EDGE,"E2026"),sQuery(id+"F0.wireOp",EDGE,"E2027"),sQuery(id+"F0.wireOp",EDGE,"E2028"),sQuery(id+"F0.wireOp",EDGE,"E2029"),sQuery(id+"F0.wireOp",EDGE,"E2030"),sQuery(id+"F0.wireOp",EDGE,"E2031"),sQuery(id+"F0.wireOp",EDGE,"E2032"),sQuery(id+"F0.wireOp",EDGE,"E2033"),sQuery(id+"F0.wireOp",EDGE,"E2034"),sQuery(id+"F0.wireOp",EDGE,"E2035"),sQuery(id+"F0.wireOp",EDGE,"E2036"),sQuery(id+"F0.wireOp",EDGE,"E2037"),sQuery(id+"F0.wireOp",EDGE,"E2038"),sQuery(id+"F0.wireOp",EDGE,"E2039"),sQuery(id+"F0.wireOp",EDGE,"E2040"),sQuery(id+"F0.wireOp",EDGE,"E2041"),sQuery(id+"F0.wireOp",EDGE,"E2042"),sQuery(id+"F0.wireOp",EDGE,"E2043"),sQuery(id+"F0.wireOp",EDGE,"E2044"),sQuery(id+"F0.wireOp",EDGE,"E2045"),sQuery(id+"F0.wireOp",EDGE,"E2046"),sQuery(id+"F0.wireOp",EDGE,"E2047"),sQuery(id+"F0.wireOp",EDGE,"E2048"),sQuery(id+"F0.wireOp",EDGE,"E2049"),sQuery(id+"F0.wireOp",EDGE,"E2050"),sQuery(id+"F0.wireOp",EDGE,"E2051"),sQuery(id+"F0.wireOp",EDGE,"E2052"),sQuery(id+"F0.wireOp",EDGE,"E2053"),sQuery(id+"F0.wireOp",EDGE,"E2054"),sQuery(id+"F0.wireOp",EDGE,"E2055"),sQuery(id+"F0.wireOp",EDGE,"E2056"),sQuery(id+"F0.wireOp",EDGE,"E2057"),sQuery(id+"F0.wireOp",EDGE,"E2058"),sQuery(id+"F0.wireOp",EDGE,"E2059"),sQuery(id+"F0.wireOp",EDGE,"E2060"),sQuery(id+"F0.wireOp",EDGE,"E2061"),sQuery(id+"F0.wireOp",EDGE,"E2062"),sQuery(id+"F0.wireOp",EDGE,"E2063"),sQuery(id+"F0.wireOp",EDGE,"E2064"),sQuery(id+"F0.wireOp",EDGE,"E2065"),sQuery(id+"F0.wireOp",EDGE,"E2066"),sQuery(id+"F0.wireOp",EDGE,"E2067"),sQuery(id+"F0.wireOp",EDGE,"E2068"),sQuery(id+"F0.wireOp",EDGE,"E2069"),sQuery(id+"F0.wireOp",EDGE,"E2070"),sQuery(id+"F0.wireOp",EDGE,"E2071"),sQuery(id+"F0.wireOp",EDGE,"E2072"),sQuery(id+"F0.wireOp",EDGE,"E2073"),sQuery(id+"F0.wireOp",EDGE,"E2074"),sQuery(id+"F0.wireOp",EDGE,"E2075"),sQuery(id+"F0.wireOp",EDGE,"E2076"),sQuery(id+"F0.wireOp",EDGE,"E2077"),sQuery(id+"F0.wireOp",EDGE,"E2078"),sQuery(id+"F0.wireOp",EDGE,"E2079"),sQuery(id+"F0.wireOp",EDGE,"E2080"),sQuery(id+"F0.wireOp",EDGE,"E2081"),sQuery(id+"F0.wireOp",EDGE,"E2082"),sQuery(id+"F0.wireOp",EDGE,"E2083"),sQuery(id+"F0.wireOp",EDGE,"E2084"),sQuery(id+"F0.wireOp",EDGE,"E2085"),sQuery(id+"F0.wireOp",EDGE,"E2086"),sQuery(id+"F0.wireOp",EDGE,"E2087"),sQuery(id+"F0.wireOp",EDGE,"E2088"),sQuery(id+"F0.wireOp",EDGE,"E2089"),sQuery(id+"F0.wireOp",EDGE,"E2090"),sQuery(id+"F0.wireOp",EDGE,"E2091"),sQuery(id+"F0.wireOp",EDGE,"E2092"),sQuery(id+"F0.wireOp",EDGE,"E2093"),sQuery(id+"F0.wireOp",EDGE,"E2094"),sQuery(id+"F0.wireOp",EDGE,"E2095"),sQuery(id+"F0.wireOp",EDGE,"E2096"),sQuery(id+"F0.wireOp",EDGE,"E2097"),sQuery(id+"F0.wireOp",EDGE,"E2098"),sQuery(id+"F0.wireOp",EDGE,"E2099"),sQuery(id+"F0.wireOp",EDGE,"E2100"),sQuery(id+"F0.wireOp",EDGE,"E2101"),sQuery(id+"F0.wireOp",EDGE,"E2102"),sQuery(id+"F0.wireOp",EDGE,"E2103"),sQuery(id+"F0.wireOp",EDGE,"E2104"),sQuery(id+"F0.wireOp",EDGE,"E2105"),sQuery(id+"F0.wireOp",EDGE,"E2106"),sQuery(id+"F0.wireOp",EDGE,"E2107"),sQuery(id+"F0.wireOp",EDGE,"E2108"),sQuery(id+"F0.wireOp",EDGE,"E2109"),sQuery(id+"F0.wireOp",EDGE,"E2110"),sQuery(id+"F0.wireOp",EDGE,"E2111"),sQuery(id+"F0.wireOp",EDGE,"E2112"),sQuery(id+"F0.wireOp",EDGE,"E2113"),sQuery(id+"F0.wireOp",EDGE,"E2114"),sQuery(id+"F0.wireOp",EDGE,"E2115"),sQuery(id+"F0.wireOp",EDGE,"E2116"),sQuery(id+"F0.wireOp",EDGE,"E2117"),sQuery(id+"F0.wireOp",EDGE,"E2118"),sQuery(id+"F0.wireOp",EDGE,"E2119"),sQuery(id+"F0.wireOp",EDGE,"E2120"),sQuery(id+"F0.wireOp",EDGE,"E2121"),sQuery(id+"F0.wireOp",EDGE,"E2122"),sQuery(id+"F0.wireOp",EDGE,"E2123"),sQuery(id+"F0.wireOp",EDGE,"E2124"),sQuery(id+"F0.wireOp",EDGE,"E2125"),sQuery(id+"F0.wireOp",EDGE,"E2126"),sQuery(id+"F0.wireOp",EDGE,"E2127"),sQuery(id+"F0.wireOp",EDGE,"E2128"),sQuery(id+"F0.wireOp",EDGE,"E2129"),sQuery(id+"F0.wireOp",EDGE,"E2130"),sQuery(id+"F0.wireOp",EDGE,"E2131"),sQuery(id+"F0.wireOp",EDGE,"E2132"),sQuery(id+"F0.wireOp",EDGE,"E2133"),sQuery(id+"F0.wireOp",EDGE,"E2134"),sQuery(id+"F0.wireOp",EDGE,"E2135"),sQuery(id+"F0.wireOp",EDGE,"E2136"),sQuery(id+"F0.wireOp",EDGE,"E2137"),sQuery(id+"F0.wireOp",EDGE,"E2138"),sQuery(id+"F0.wireOp",EDGE,"E2139"),sQuery(id+"F0.wireOp",EDGE,"E2140"),sQuery(id+"F0.wireOp",EDGE,"E2141"),sQuery(id+"F0.wireOp",EDGE,"E2142"),sQuery(id+"F0.wireOp",EDGE,"E2143"),sQuery(id+"F0.wireOp",EDGE,"E2144"),sQuery(id+"F0.wireOp",EDGE,"E2145"),sQuery(id+"F0.wireOp",EDGE,"E2146"),sQuery(id+"F0.wireOp",EDGE,"E2147"),sQuery(id+"F0.wireOp",EDGE,"E2148"),sQuery(id+"F0.wireOp",EDGE,"E2149"),sQuery(id+"F0.wireOp",EDGE,"E2150"),sQuery(id+"F0.wireOp",EDGE,"E2151"),sQuery(id+"F0.wireOp",EDGE,"E2152"),sQuery(id+"F0.wireOp",EDGE,"E2153"),sQuery(id+"F0.wireOp",EDGE,"E2154"),sQuery(id+"F0.wireOp",EDGE,"E2155"),sQuery(id+"F0.wireOp",EDGE,"E2156"),sQuery(id+"F0.wireOp",EDGE,"E2157"),sQuery(id+"F0.wireOp",EDGE,"E2158"),sQuery(id+"F0.wireOp",EDGE,"E2159"),sQuery(id+"F0.wireOp",EDGE,"E2160"),sQuery(id+"F0.wireOp",EDGE,"E2161"),sQuery(id+"F0.wireOp",EDGE,"E2162"),sQuery(id+"F0.wireOp",EDGE,"E2163"),sQuery(id+"F0.wireOp",EDGE,"E2164"),sQuery(id+"F0.wireOp",EDGE,"E2165"),sQuery(id+"F0.wireOp",EDGE,"E2166"),sQuery(id+"F0.wireOp",EDGE,"E2167"),sQuery(id+"F0.wireOp",EDGE,"E2168"),sQuery(id+"F0.wireOp",EDGE,"E2169"),sQuery(id+"F0.wireOp",EDGE,"E2170"),sQuery(id+"F0.wireOp",EDGE,"E2171"),sQuery(id+"F0.wireOp",EDGE,"E2172"),sQuery(id+"F0.wireOp",EDGE,"E2173"),sQuery(id+"F0.wireOp",EDGE,"E2174"),sQuery(id+"F0.wireOp",EDGE,"E2175"),sQuery(id+"F0.wireOp",EDGE,"E2176"),sQuery(id+"F0.wireOp",EDGE,"E2177"),sQuery(id+"F0.wireOp",EDGE,"E2178"),sQuery(id+"F0.wireOp",EDGE,"E2179"),sQuery(id+"F0.wireOp",EDGE,"E2180"),sQuery(id+"F0.wireOp",EDGE,"E2181"),sQuery(id+"F0.wireOp",EDGE,"E2182"),sQuery(id+"F0.wireOp",EDGE,"E2183"),sQuery(id+"F0.wireOp",EDGE,"E2184"),sQuery(id+"F0.wireOp",EDGE,"E2185"),sQuery(id+"F0.wireOp",EDGE,"E2186"),sQuery(id+"F0.wireOp",EDGE,"E2187"),sQuery(id+"F0.wireOp",EDGE,"E2188"),sQuery(id+"F0.wireOp",EDGE,"E2189"),sQuery(id+"F0.wireOp",EDGE,"E2190"),sQuery(id+"F0.wireOp",EDGE,"E2191"),sQuery(id+"F0.wireOp",EDGE,"E2192"),sQuery(id+"F0.wireOp",EDGE,"E2193"),sQuery(id+"F0.wireOp",EDGE,"E2194"),sQuery(id+"F0.wireOp",EDGE,"E2195"),sQuery(id+"F0.wireOp",EDGE,"E2196"),sQuery(id+"F0.wireOp",EDGE,"E2197"),sQuery(id+"F0.wireOp",EDGE,"E2198"),sQuery(id+"F0.wireOp",EDGE,"E2199"),sQuery(id+"F0.wireOp",EDGE,"E2200"),sQuery(id+"F0.wireOp",EDGE,"E2201"),sQuery(id+"F0.wireOp",EDGE,"E2202"),sQuery(id+"F0.wireOp",EDGE,"E2203"),sQuery(id+"F0.wireOp",EDGE,"E2204"),sQuery(id+"F0.wireOp",EDGE,"E2205"),sQuery(id+"F0.wireOp",EDGE,"E2206"),sQuery(id+"F0.wireOp",EDGE,"E2207"),sQuery(id+"F0.wireOp",EDGE,"E2208"),sQuery(id+"F0.wireOp",EDGE,"E2209"),sQuery(id+"F0.wireOp",EDGE,"E2210"),sQuery(id+"F0.wireOp",EDGE,"E2211"),sQuery(id+"F0.wireOp",EDGE,"E2212"),sQuery(id+"F0.wireOp",EDGE,"E2213"),sQuery(id+"F0.wireOp",EDGE,"E2214"),sQuery(id+"F0.wireOp",EDGE,"E2215"),sQuery(id+"F0.wireOp",EDGE,"E2216"),sQuery(id+"F0.wireOp",EDGE,"E2217"),sQuery(id+"F0.wireOp",EDGE,"E2218"),sQuery(id+"F0.wireOp",EDGE,"E2219"),sQuery(id+"F0.wireOp",EDGE,"E2220"),sQuery(id+"F0.wireOp",EDGE,"E2221"),sQuery(id+"F0.wireOp",EDGE,"E2222"),sQuery(id+"F0.wireOp",EDGE,"E2223"),sQuery(id+"F0.wireOp",EDGE,"E2224"),sQuery(id+"F0.wireOp",EDGE,"E2225"),sQuery(id+"F0.wireOp",EDGE,"E2226"),sQuery(id+"F0.wireOp",EDGE,"E2227"),sQuery(id+"F0.wireOp",EDGE,"E2228"),sQuery(id+"F0.wireOp",EDGE,"E2229"),sQuery(id+"F0.wireOp",EDGE,"E2230"),sQuery(id+"F0.wireOp",EDGE,"E2231"),sQuery(id+"F0.wireOp",EDGE,"E2232"),sQuery(id+"F0.wireOp",EDGE,"E2233"),sQuery(id+"F0.wireOp",EDGE,"E2234"),sQuery(id+"F0.wireOp",EDGE,"E2235"),sQuery(id+"F0.wireOp",EDGE,"E2236"),sQuery(id+"F0.wireOp",EDGE,"E2237"),sQuery(id+"F0.wireOp",EDGE,"E2238"),sQuery(id+"F0.wireOp",EDGE,"E2239"),sQuery(id+"F0.wireOp",EDGE,"E2240"),sQuery(id+"F0.wireOp",EDGE,"E2241"),sQuery(id+"F0.wireOp",EDGE,"E2242"),sQuery(id+"F0.wireOp",EDGE,"E2243"),sQuery(id+"F0.wireOp",EDGE,"E2244"),sQuery(id+"F0.wireOp",EDGE,"E2245"),sQuery(id+"F0.wireOp",EDGE,"E2246"),sQuery(id+"F0.wireOp",EDGE,"E2247"),sQuery(id+"F0.wireOp",EDGE,"E2248"),sQuery(id+"F0.wireOp",EDGE,"E2249"),sQuery(id+"F0.wireOp",EDGE,"E2250"),sQuery(id+"F0.wireOp",EDGE,"E2251"),sQuery(id+"F0.wireOp",EDGE,"E2252"),sQuery(id+"F0.wireOp",EDGE,"E2253"),sQuery(id+"F0.wireOp",EDGE,"E2254"),sQuery(id+"F0.wireOp",EDGE,"E2255"),sQuery(id+"F0.wireOp",EDGE,"E2256"),sQuery(id+"F0.wireOp",EDGE,"E2257"),sQuery(id+"F0.wireOp",EDGE,"E2258"),sQuery(id+"F0.wireOp",EDGE,"E2259"),sQuery(id+"F0.wireOp",EDGE,"E2260"),sQuery(id+"F0.wireOp",EDGE,"E2261"),sQuery(id+"F0.wireOp",EDGE,"E2262"),sQuery(id+"F0.wireOp",EDGE,"E2263"),sQuery(id+"F0.wireOp",EDGE,"E2264"),sQuery(id+"F0.wireOp",EDGE,"E2265"),sQuery(id+"F0.wireOp",EDGE,"E2266"),sQuery(id+"F0.wireOp",EDGE,"E2267"),sQuery(id+"F0.wireOp",EDGE,"E2268"),sQuery(id+"F0.wireOp",EDGE,"E2269"),sQuery(id+"F0.wireOp",EDGE,"E2270"),sQuery(id+"F0.wireOp",EDGE,"E2271"),sQuery(id+"F0.wireOp",EDGE,"E2272"),sQuery(id+"F0.wireOp",EDGE,"E2273"),sQuery(id+"F0.wireOp",EDGE,"E2274"),sQuery(id+"F0.wireOp",EDGE,"E2275"),sQuery(id+"F0.wireOp",EDGE,"E2276"),sQuery(id+"F0.wireOp",EDGE,"E2277"),sQuery(id+"F0.wireOp",EDGE,"E2278"),sQuery(id+"F0.wireOp",EDGE,"E2279"),sQuery(id+"F0.wireOp",EDGE,"E2280"),sQuery(id+"F0.wireOp",EDGE,"E2281"),sQuery(id+"F0.wireOp",EDGE,"E2282"),sQuery(id+"F0.wireOp",EDGE,"E2283"),sQuery(id+"F0.wireOp",EDGE,"E2284"),sQuery(id+"F0.wireOp",EDGE,"E2285"),sQuery(id+"F0.wireOp",EDGE,"E2286"),sQuery(id+"F0.wireOp",EDGE,"E2287"),sQuery(id+"F0.wireOp",EDGE,"E2288"),sQuery(id+"F0.wireOp",EDGE,"E2289"),sQuery(id+"F0.wireOp",EDGE,"E2290"),sQuery(id+"F0.wireOp",EDGE,"E2291"),sQuery(id+"F0.wireOp",EDGE,"E2292"),sQuery(id+"F0.wireOp",EDGE,"E2293"),sQuery(id+"F0.wireOp",EDGE,"E2294"),sQuery(id+"F0.wireOp",EDGE,"E2295"),sQuery(id+"F0.wireOp",EDGE,"E2296"),sQuery(id+"F0.wireOp",EDGE,"E2297"),sQuery(id+"F0.wireOp",EDGE,"E2298"),sQuery(id+"F0.wireOp",EDGE,"E2299"),sQuery(id+"F0.wireOp",EDGE,"E2300"),sQuery(id+"F0.wireOp",EDGE,"E2301"),sQuery(id+"F0.wireOp",EDGE,"E2302"),sQuery(id+"F0.wireOp",EDGE,"E2303"),sQuery(id+"F0.wireOp",EDGE,"E2304"),sQuery(id+"F0.wireOp",EDGE,"E2305"),sQuery(id+"F0.wireOp",EDGE,"E2306"),sQuery(id+"F0.wireOp",EDGE,"E2307"),sQuery(id+"F0.wireOp",EDGE,"E2308"),sQuery(id+"F0.wireOp",EDGE,"E2309"),sQuery(id+"F0.wireOp",EDGE,"E2310"),sQuery(id+"F0.wireOp",EDGE,"E2311"),sQuery(id+"F0.wireOp",EDGE,"E2312"),sQuery(id+"F0.wireOp",EDGE,"E2313"),sQuery(id+"F0.wireOp",EDGE,"E2314"),sQuery(id+"F0.wireOp",EDGE,"E2315"),sQuery(id+"F0.wireOp",EDGE,"E2316"),sQuery(id+"F0.wireOp",EDGE,"E2317"),sQuery(id+"F0.wireOp",EDGE,"E2318"),sQuery(id+"F0.wireOp",EDGE,"E2319"),sQuery(id+"F0.wireOp",EDGE,"E2320"),sQuery(id+"F0.wireOp",EDGE,"E2321"),sQuery(id+"F0.wireOp",EDGE,"E2322"),sQuery(id+"F0.wireOp",EDGE,"E2323"),sQuery(id+"F0.wireOp",EDGE,"E2324"),sQuery(id+"F0.wireOp",EDGE,"E2325"),sQuery(id+"F0.wireOp",EDGE,"E2326"),sQuery(id+"F0.wireOp",EDGE,"E2327"),sQuery(id+"F0.wireOp",EDGE,"E2328"),sQuery(id+"F0.wireOp",EDGE,"E2329"),sQuery(id+"F0.wireOp",EDGE,"E2330"),sQuery(id+"F0.wireOp",EDGE,"E2331"),sQuery(id+"F0.wireOp",EDGE,"E2332"),sQuery(id+"F0.wireOp",EDGE,"E2333"),sQuery(id+"F0.wireOp",EDGE,"E2334"),sQuery(id+"F0.wireOp",EDGE,"E2335"),sQuery(id+"F0.wireOp",EDGE,"E2336"),sQuery(id+"F0.wireOp",EDGE,"E2337"),sQuery(id+"F0.wireOp",EDGE,"E2338"),sQuery(id+"F0.wireOp",EDGE,"E2339"),sQuery(id+"F0.wireOp",EDGE,"E2340"),sQuery(id+"F0.wireOp",EDGE,"E2341"),sQuery(id+"F0.wireOp",EDGE,"E2342"),sQuery(id+"F0.wireOp",EDGE,"E2343"),sQuery(id+"F0.wireOp",EDGE,"E2344"),sQuery(id+"F0.wireOp",EDGE,"E2345"),sQuery(id+"F0.wireOp",EDGE,"E2346"),sQuery(id+"F0.wireOp",EDGE,"E2347"),sQuery(id+"F0.wireOp",EDGE,"E2348"),sQuery(id+"F0.wireOp",EDGE,"E2349"),sQuery(id+"F0.wireOp",EDGE,"E2350"),sQuery(id+"F0.wireOp",EDGE,"E2351"),sQuery(id+"F0.wireOp",EDGE,"E2352"),sQuery(id+"F0.wireOp",EDGE,"E2353"),sQuery(id+"F0.wireOp",EDGE,"E2354"),sQuery(id+"F0.wireOp",EDGE,"E2355"),sQuery(id+"F0.wireOp",EDGE,"E2356"),sQuery(id+"F0.wireOp",EDGE,"E2357"),sQuery(id+"F0.wireOp",EDGE,"E2358"),sQuery(id+"F0.wireOp",EDGE,"E2359"),sQuery(id+"F0.wireOp",EDGE,"E2360"),sQuery(id+"F0.wireOp",EDGE,"E2361"),sQuery(id+"F0.wireOp",EDGE,"E2362"),sQuery(id+"F0.wireOp",EDGE,"E2363"),sQuery(id+"F0.wireOp",EDGE,"E2364"),sQuery(id+"F0.wireOp",EDGE,"E2365"),sQuery(id+"F0.wireOp",EDGE,"E2366"),sQuery(id+"F0.wireOp",EDGE,"E2367"),sQuery(id+"F0.wireOp",EDGE,"E2368"),sQuery(id+"F0.wireOp",EDGE,"E2369"),sQuery(id+"F0.wireOp",EDGE,"E2370"),sQuery(id+"F0.wireOp",EDGE,"E2371"),sQuery(id+"F0.wireOp",EDGE,"E2372"),sQuery(id+"F0.wireOp",EDGE,"E2373"),sQuery(id+"F0.wireOp",EDGE,"E2374"),sQuery(id+"F0.wireOp",EDGE,"E2375"),sQuery(id+"F0.wireOp",EDGE,"E2376"),sQuery(id+"F0.wireOp",EDGE,"E2377"),sQuery(id+"F0.wireOp",EDGE,"E2378"),sQuery(id+"F0.wireOp",EDGE,"E2379"),sQuery(id+"F0.wireOp",EDGE,"E2380"),sQuery(id+"F0.wireOp",EDGE,"E2381"),sQuery(id+"F0.wireOp",EDGE,"E2382"),sQuery(id+"F0.wireOp",EDGE,"E2383"),sQuery(id+"F0.wireOp",EDGE,"E2384"),sQuery(id+"F0.wireOp",EDGE,"E2385"),sQuery(id+"F0.wireOp",EDGE,"E2386"),sQuery(id+"F0.wireOp",EDGE,"E2387"),sQuery(id+"F0.wireOp",EDGE,"E2388"),sQuery(id+"F0.wireOp",EDGE,"E2389"),sQuery(id+"F0.wireOp",EDGE,"E2390"),sQuery(id+"F0.wireOp",EDGE,"E2391"),sQuery(id+"F0.wireOp",EDGE,"E2392"),sQuery(id+"F0.wireOp",EDGE,"E2393"),sQuery(id+"F0.wireOp",EDGE,"E2394"),sQuery(id+"F0.wireOp",EDGE,"E2395"),sQuery(id+"F0.wireOp",EDGE,"E2396"),sQuery(id+"F0.wireOp",EDGE,"E2397"),sQuery(id+"F0.wireOp",EDGE,"E2398"),sQuery(id+"F0.wireOp",EDGE,"E2399"),sQuery(id+"F0.wireOp",EDGE,"E2400"),sQuery(id+"F0.wireOp",EDGE,"E2401"),sQuery(id+"F0.wireOp",EDGE,"E2402"),sQuery(id+"F0.wireOp",EDGE,"E2403"),sQuery(id+"F0.wireOp",EDGE,"E2404"),sQuery(id+"F0.wireOp",EDGE,"E2405"),sQuery(id+"F0.wireOp",EDGE,"E2406"),sQuery(id+"F0.wireOp",EDGE,"E2407"),sQuery(id+"F0.wireOp",EDGE,"E2408"),sQuery(id+"F0.wireOp",EDGE,"E2409"),sQuery(id+"F0.wireOp",EDGE,"E2410"),sQuery(id+"F0.wireOp",EDGE,"E2411"),sQuery(id+"F0.wireOp",EDGE,"E2412"),sQuery(id+"F0.wireOp",EDGE,"E2413"),sQuery(id+"F0.wireOp",EDGE,"E2414"),sQuery(id+"F0.wireOp",EDGE,"E2415"),sQuery(id+"F0.wireOp",EDGE,"E2416"),sQuery(id+"F0.wireOp",EDGE,"E2417"),sQuery(id+"F0.wireOp",EDGE,"E2418"),sQuery(id+"F0.wireOp",EDGE,"E2419"),sQuery(id+"F0.wireOp",EDGE,"E2420"),sQuery(id+"F0.wireOp",EDGE,"E2421"),sQuery(id+"F0.wireOp",EDGE,"E2422"),sQuery(id+"F0.wireOp",EDGE,"E2423"),sQuery(id+"F0.wireOp",EDGE,"E2424"),sQuery(id+"F0.wireOp",EDGE,"E2425"),sQuery(id+"F0.wireOp",EDGE,"E2426"),sQuery(id+"F0.wireOp",EDGE,"E2427"),sQuery(id+"F0.wireOp",EDGE,"E2428"),sQuery(id+"F0.wireOp",EDGE,"E2429"),sQuery(id+"F0.wireOp",EDGE,"E2430"),sQuery(id+"F0.wireOp",EDGE,"E2431"),sQuery(id+"F0.wireOp",EDGE,"E2432"),sQuery(id+"F0.wireOp",EDGE,"E2433"),sQuery(id+"F0.wireOp",EDGE,"E2434"),sQuery(id+"F0.wireOp",EDGE,"E2435"),sQuery(id+"F0.wireOp",EDGE,"E2436"),sQuery(id+"F0.wireOp",EDGE,"E2437"),sQuery(id+"F0.wireOp",EDGE,"E2438"),sQuery(id+"F0.wireOp",EDGE,"E2439"),sQuery(id+"F0.wireOp",EDGE,"E2440"),sQuery(id+"F0.wireOp",EDGE,"E2441"),sQuery(id+"F0.wireOp",EDGE,"E2442"),sQuery(id+"F0.wireOp",EDGE,"E2443"),sQuery(id+"F0.wireOp",EDGE,"E2444"),sQuery(id+"F0.wireOp",EDGE,"E2445"),sQuery(id+"F0.wireOp",EDGE,"E2446"),sQuery(id+"F0.wireOp",EDGE,"E2447"),sQuery(id+"F0.wireOp",EDGE,"E2448"),sQuery(id+"F0.wireOp",EDGE,"E2449"),sQuery(id+"F0.wireOp",EDGE,"E2450"),sQuery(id+"F0.wireOp",EDGE,"E2451"),sQuery(id+"F0.wireOp",EDGE,"E2452"),sQuery(id+"F0.wireOp",EDGE,"E2453"),sQuery(id+"F0.wireOp",EDGE,"E2454"),sQuery(id+"F0.wireOp",EDGE,"E2455"),sQuery(id+"F0.wireOp",EDGE,"E2456"),sQuery(id+"F0.wireOp",EDGE,"E2457"),sQuery(id+"F0.wireOp",EDGE,"E2458"),sQuery(id+"F0.wireOp",EDGE,"E2459"),sQuery(id+"F0.wireOp",EDGE,"E2460"),sQuery(id+"F0.wireOp",EDGE,"E2461"),sQuery(id+"F0.wireOp",EDGE,"E2462"),sQuery(id+"F0.wireOp",EDGE,"E2463"),sQuery(id+"F0.wireOp",EDGE,"E2464"),sQuery(id+"F0.wireOp",EDGE,"E2465"),sQuery(id+"F0.wireOp",EDGE,"E2466"),sQuery(id+"F0.wireOp",EDGE,"E2467"),sQuery(id+"F0.wireOp",EDGE,"E2468"),sQuery(id+"F0.wireOp",EDGE,"E2469"),sQuery(id+"F0.wireOp",EDGE,"E2470"),sQuery(id+"F0.wireOp",EDGE,"E2471"),sQuery(id+"F0.wireOp",EDGE,"E2472"),sQuery(id+"F0.wireOp",EDGE,"E2473"),sQuery(id+"F0.wireOp",EDGE,"E2474"),sQuery(id+"F0.wireOp",EDGE,"E2475"),sQuery(id+"F0.wireOp",EDGE,"E2476"),sQuery(id+"F0.wireOp",EDGE,"E2477"),sQuery(id+"F0.wireOp",EDGE,"E2478"),sQuery(id+"F0.wireOp",EDGE,"E2479"),sQuery(id+"F0.wireOp",EDGE,"E2480"),sQuery(id+"F0.wireOp",EDGE,"E2481"),sQuery(id+"F0.wireOp",EDGE,"E2482"),sQuery(id+"F0.wireOp",EDGE,"E2483"),sQuery(id+"F0.wireOp",EDGE,"E2484"),sQuery(id+"F0.wireOp",EDGE,"E2485"),sQuery(id+"F0.wireOp",EDGE,"E2486"),sQuery(id+"F0.wireOp",EDGE,"E2487"),sQuery(id+"F0.wireOp",EDGE,"E2488"),sQuery(id+"F0.wireOp",EDGE,"E2489"),sQuery(id+"F0.wireOp",EDGE,"E2490"),sQuery(id+"F0.wireOp",EDGE,"E2491"),sQuery(id+"F0.wireOp",EDGE,"E2492"),sQuery(id+"F0.wireOp",EDGE,"E2493"),sQuery(id+"F0.wireOp",EDGE,"E2494"),sQuery(id+"F0.wireOp",EDGE,"E2495"),sQuery(id+"F0.wireOp",EDGE,"E2496"),sQuery(id+"F0.wireOp",EDGE,"E2497"),sQuery(id+"F0.wireOp",EDGE,"E2498"),sQuery(id+"F0.wireOp",EDGE,"E2499"),sQuery(id+"F0.wireOp",EDGE,"E2500"),sQuery(id+"F0.wireOp",EDGE,"E2501"),sQuery(id+"F0.wireOp",EDGE,"E2502"),sQuery(id+"F0.wireOp",EDGE,"E2503"),sQuery(id+"F0.wireOp",EDGE,"E2504"),sQuery(id+"F0.wireOp",EDGE,"E2505"),sQuery(id+"F0.wireOp",EDGE,"E2506"),sQuery(id+"F0.wireOp",EDGE,"E2507"),sQuery(id+"F0.wireOp",EDGE,"E2508"),sQuery(id+"F0.wireOp",EDGE,"E2509"),sQuery(id+"F0.wireOp",EDGE,"E2510"),sQuery(id+"F0.wireOp",EDGE,"E2511"),sQuery(id+"F0.wireOp",EDGE,"E2512"),sQuery(id+"F0.wireOp",EDGE,"E2513"),sQuery(id+"F0.wireOp",EDGE,"E2514"),sQuery(id+"F0.wireOp",EDGE,"E2515"),sQuery(id+"F0.wireOp",EDGE,"E2516"),sQuery(id+"F0.wireOp",EDGE,"E2517"),sQuery(id+"F0.wireOp",EDGE,"E2518"),sQuery(id+"F0.wireOp",EDGE,"E2519"),sQuery(id+"F0.wireOp",EDGE,"E2520"),sQuery(id+"F0.wireOp",EDGE,"E2521"),sQuery(id+"F0.wireOp",EDGE,"E2522"),sQuery(id+"F0.wireOp",EDGE,"E2523"),sQuery(id+"F0.wireOp",EDGE,"E2524"),sQuery(id+"F0.wireOp",EDGE,"E2525"),sQuery(id+"F0.wireOp",EDGE,"E2526"),sQuery(id+"F0.wireOp",EDGE,"E2527"),sQuery(id+"F0.wireOp",EDGE,"E2528"),sQuery(id+"F0.wireOp",EDGE,"E2529"),sQuery(id+"F0.wireOp",EDGE,"E2530"),sQuery(id+"F0.wireOp",EDGE,"E2531"),sQuery(id+"F0.wireOp",EDGE,"E2532"),sQuery(id+"F0.wireOp",EDGE,"E2533"),sQuery(id+"F0.wireOp",EDGE,"E2534"),sQuery(id+"F0.wireOp",EDGE,"E2535"),sQuery(id+"F0.wireOp",EDGE,"E2536"),sQuery(id+"F0.wireOp",EDGE,"E2537"),sQuery(id+"F0.wireOp",EDGE,"E2538"),sQuery(id+"F0.wireOp",EDGE,"E2539"),sQuery(id+"F0.wireOp",EDGE,"E2540"),sQuery(id+"F0.wireOp",EDGE,"E2541"),sQuery(id+"F0.wireOp",EDGE,"E2542"),sQuery(id+"F0.wireOp",EDGE,"E2543"),sQuery(id+"F0.wireOp",EDGE,"E2544"),sQuery(id+"F0.wireOp",EDGE,"E2545"),sQuery(id+"F0.wireOp",EDGE,"E2546"),sQuery(id+"F0.wireOp",EDGE,"E2547"),sQuery(id+"F0.wireOp",EDGE,"E2548"),sQuery(id+"F0.wireOp",EDGE,"E2549"),sQuery(id+"F0.wireOp",EDGE,"E2550"),sQuery(id+"F0.wireOp",EDGE,"E2551"),sQuery(id+"F0.wireOp",EDGE,"E2552"),sQuery(id+"F0.wireOp",EDGE,"E2553"),sQuery(id+"F0.wireOp",EDGE,"E2554"),sQuery(id+"F0.wireOp",EDGE,"E2555"),sQuery(id+"F0.wireOp",EDGE,"E2556"),sQuery(id+"F0.wireOp",EDGE,"E2557"),sQuery(id+"F0.wireOp",EDGE,"E2558"),sQuery(id+"F0.wireOp",EDGE,"E2559"),sQuery(id+"F0.wireOp",EDGE,"E2560"),sQuery(id+"F0.wireOp",EDGE,"E2561"),sQuery(id+"F0.wireOp",EDGE,"E2562"),sQuery(id+"F0.wireOp",EDGE,"E2563"),sQuery(id+"F0.wireOp",EDGE,"E2564"),sQuery(id+"F0.wireOp",EDGE,"E2565"),sQuery(id+"F0.wireOp",EDGE,"E2566"),sQuery(id+"F0.wireOp",EDGE,"E2567"),sQuery(id+"F0.wireOp",EDGE,"E2568"),sQuery(id+"F0.wireOp",EDGE,"E2569"),sQuery(id+"F0.wireOp",EDGE,"E2570"),sQuery(id+"F0.wireOp",EDGE,"E2571"),sQuery(id+"F0.wireOp",EDGE,"E2572"),sQuery(id+"F0.wireOp",EDGE,"E2573"),sQuery(id+"F0.wireOp",EDGE,"E2574"),sQuery(id+"F0.wireOp",EDGE,"E2575"),sQuery(id+"F0.wireOp",EDGE,"E2576"),sQuery(id+"F0.wireOp",EDGE,"E2577"),sQuery(id+"F0.wireOp",EDGE,"E2578"),sQuery(id+"F0.wireOp",EDGE,"E2579"),sQuery(id+"F0.wireOp",EDGE,"E2580"),sQuery(id+"F0.wireOp",EDGE,"E2581"),sQuery(id+"F0.wireOp",EDGE,"E2582"),sQuery(id+"F0.wireOp",EDGE,"E2583"),sQuery(id+"F0.wireOp",EDGE,"E2584"),sQuery(id+"F0.wireOp",EDGE,"E2585"),sQuery(id+"F0.wireOp",EDGE,"E2586"),sQuery(id+"F0.wireOp",EDGE,"E2587"),sQuery(id+"F0.wireOp",EDGE,"E2588"),sQuery(id+"F0.wireOp",EDGE,"E2589"),sQuery(id+"F0.wireOp",EDGE,"E2590"),sQuery(id+"F0.wireOp",EDGE,"E2591"),sQuery(id+"F0.wireOp",EDGE,"E2592"),sQuery(id+"F0.wireOp",EDGE,"E2593"),sQuery(id+"F0.wireOp",EDGE,"E2594"),sQuery(id+"F0.wireOp",EDGE,"E2595"),sQuery(id+"F0.wireOp",EDGE,"E2596"),sQuery(id+"F0.wireOp",EDGE,"E2597"),sQuery(id+"F0.wireOp",EDGE,"E2598"),sQuery(id+"F0.wireOp",EDGE,"E2599"),sQuery(id+"F0.wireOp",EDGE,"E2600"),sQuery(id+"F0.wireOp",EDGE,"E2601"),sQuery(id+"F0.wireOp",EDGE,"E2602"),sQuery(id+"F0.wireOp",EDGE,"E2603"),sQuery(id+"F0.wireOp",EDGE,"E2604"),sQuery(id+"F0.wireOp",EDGE,"E2605"),sQuery(id+"F0.wireOp",EDGE,"E2606"),sQuery(id+"F0.wireOp",EDGE,"E2607"),sQuery(id+"F0.wireOp",EDGE,"E2608"),sQuery(id+"F0.wireOp",EDGE,"E2609"),sQuery(id+"F0.wireOp",EDGE,"E2610"),sQuery(id+"F0.wireOp",EDGE,"E2611"),sQuery(id+"F0.wireOp",EDGE,"E2612"),sQuery(id+"F0.wireOp",EDGE,"E2613"),sQuery(id+"F0.wireOp",EDGE,"E2614"),sQuery(id+"F0.wireOp",EDGE,"E2615"),sQuery(id+"F0.wireOp",EDGE,"E2616"),sQuery(id+"F0.wireOp",EDGE,"E2617"),sQuery(id+"F0.wireOp",EDGE,"E2618"),sQuery(id+"F0.wireOp",EDGE,"E2619"),sQuery(id+"F0.wireOp",EDGE,"E2620"),sQuery(id+"F0.wireOp",EDGE,"E2621"),sQuery(id+"F0.wireOp",EDGE,"E2622"),sQuery(id+"F0.wireOp",EDGE,"E2623"),sQuery(id+"F0.wireOp",EDGE,"E2624"),sQuery(id+"F0.wireOp",EDGE,"E2625"),sQuery(id+"F0.wireOp",EDGE,"E2626"),sQuery(id+"F0.wireOp",EDGE,"E2627"),sQuery(id+"F0.wireOp",EDGE,"E2628"),sQuery(id+"F0.wireOp",EDGE,"E2629"),sQuery(id+"F0.wireOp",EDGE,"E2630"),sQuery(id+"F0.wireOp",EDGE,"E2631"),sQuery(id+"F0.wireOp",EDGE,"E2632"),sQuery(id+"F0.wireOp",EDGE,"E2633"),sQuery(id+"F0.wireOp",EDGE,"E2634"),sQuery(id+"F0.wireOp",EDGE,"E2635"),sQuery(id+"F0.wireOp",EDGE,"E2636"),sQuery(id+"F0.wireOp",EDGE,"E2637"),sQuery(id+"F0.wireOp",EDGE,"E2638"),sQuery(id+"F0.wireOp",EDGE,"E2639"),sQuery(id+"F0.wireOp",EDGE,"E2640"),sQuery(id+"F0.wireOp",EDGE,"E2641"),sQuery(id+"F0.wireOp",EDGE,"E2642"),sQuery(id+"F0.wireOp",EDGE,"E2643"),sQuery(id+"F0.wireOp",EDGE,"E2644"),sQuery(id+"F0.wireOp",EDGE,"E2645"),sQuery(id+"F0.wireOp",EDGE,"E2646"),sQuery(id+"F0.wireOp",EDGE,"E2647"),sQuery(id+"F0.wireOp",EDGE,"E2648"),sQuery(id+"F0.wireOp",EDGE,"E2649"),sQuery(id+"F0.wireOp",EDGE,"E2650"),sQuery(id+"F0.wireOp",EDGE,"E2651"),sQuery(id+"F0.wireOp",EDGE,"E2652"),sQuery(id+"F0.wireOp",EDGE,"E2653"),sQuery(id+"F0.wireOp",EDGE,"E2654"),sQuery(id+"F0.wireOp",EDGE,"E2655"),sQuery(id+"F0.wireOp",EDGE,"E2656"),sQuery(id+"F0.wireOp",EDGE,"E2657"),sQuery(id+"F0.wireOp",EDGE,"E2658"),sQuery(id+"F0.wireOp",EDGE,"E2659"),sQuery(id+"F0.wireOp",EDGE,"E2660"),sQuery(id+"F0.wireOp",EDGE,"E2661"),sQuery(id+"F0.wireOp",EDGE,"E2662"),sQuery(id+"F0.wireOp",EDGE,"E2663"),sQuery(id+"F0.wireOp",EDGE,"E2664"),sQuery(id+"F0.wireOp",EDGE,"E2665"),sQuery(id+"F0.wireOp",EDGE,"E2666"),sQuery(id+"F0.wireOp",EDGE,"E2667"),sQuery(id+"F0.wireOp",EDGE,"E2668"),sQuery(id+"F0.wireOp",EDGE,"E2669"),sQuery(id+"F0.wireOp",EDGE,"E2670"),sQuery(id+"F0.wireOp",EDGE,"E2671"),sQuery(id+"F0.wireOp",EDGE,"E2672"),sQuery(id+"F0.wireOp",EDGE,"E2673"),sQuery(id+"F0.wireOp",EDGE,"E2674"),sQuery(id+"F0.wireOp",EDGE,"E2675"),sQuery(id+"F0.wireOp",EDGE,"E2676"),sQuery(id+"F0.wireOp",EDGE,"E2677"),sQuery(id+"F0.wireOp",EDGE,"E2678"),sQuery(id+"F0.wireOp",EDGE,"E2679"),sQuery(id+"F0.wireOp",EDGE,"E2680"),sQuery(id+"F0.wireOp",EDGE,"E2681"),sQuery(id+"F0.wireOp",EDGE,"E2682"),sQuery(id+"F0.wireOp",EDGE,"E2683"),sQuery(id+"F0.wireOp",EDGE,"E2684"),sQuery(id+"F0.wireOp",EDGE,"E2685"),sQuery(id+"F0.wireOp",EDGE,"E2686"),sQuery(id+"F0.wireOp",EDGE,"E2687"),sQuery(id+"F0.wireOp",EDGE,"E2688"),sQuery(id+"F0.wireOp",EDGE,"E2689"),sQuery(id+"F0.wireOp",EDGE,"E2690"),sQuery(id+"F0.wireOp",EDGE,"E2691"),sQuery(id+"F0.wireOp",EDGE,"E2692"),sQuery(id+"F0.wireOp",EDGE,"E2693"),sQuery(id+"F0.wireOp",EDGE,"E2694"),sQuery(id+"F0.wireOp",EDGE,"E2695"),sQuery(id+"F0.wireOp",EDGE,"E2696"),sQuery(id+"F0.wireOp",EDGE,"E2697"),sQuery(id+"F0.wireOp",EDGE,"E2698"),sQuery(id+"F0.wireOp",EDGE,"E2699"),sQuery(id+"F0.wireOp",EDGE,"E2700"),sQuery(id+"F0.wireOp",EDGE,"E2701"),sQuery(id+"F0.wireOp",EDGE,"E2702"),sQuery(id+"F0.wireOp",EDGE,"E2703"),sQuery(id+"F0.wireOp",EDGE,"E2704"),sQuery(id+"F0.wireOp",EDGE,"E2705"),sQuery(id+"F0.wireOp",EDGE,"E2706"),sQuery(id+"F0.wireOp",EDGE,"E2707"),sQuery(id+"F0.wireOp",EDGE,"E2708"),sQuery(id+"F0.wireOp",EDGE,"E2709"),sQuery(id+"F0.wireOp",EDGE,"E2710"),sQuery(id+"F0.wireOp",EDGE,"E2711"),sQuery(id+"F0.wireOp",EDGE,"E2712"),sQuery(id+"F0.wireOp",EDGE,"E2713"),sQuery(id+"F0.wireOp",EDGE,"E2714"),sQuery(id+"F0.wireOp",EDGE,"E2715"),sQuery(id+"F0.wireOp",EDGE,"E2716"),sQuery(id+"F0.wireOp",EDGE,"E2717"),sQuery(id+"F0.wireOp",EDGE,"E2718"),sQuery(id+"F0.wireOp",EDGE,"E2719"),sQuery(id+"F0.wireOp",EDGE,"E2720"),sQuery(id+"F0.wireOp",EDGE,"E2721"),sQuery(id+"F0.wireOp",EDGE,"E2722"),sQuery(id+"F0.wireOp",EDGE,"E2723"),sQuery(id+"F0.wireOp",EDGE,"E2724"),sQuery(id+"F0.wireOp",EDGE,"E2725"),sQuery(id+"F0.wireOp",EDGE,"E2726"),sQuery(id+"F0.wireOp",EDGE,"E2727"),sQuery(id+"F0.wireOp",EDGE,"E2728"),sQuery(id+"F0.wireOp",EDGE,"E2729"),sQuery(id+"F0.wireOp",EDGE,"E2730"),sQuery(id+"F0.wireOp",EDGE,"E2731"),sQuery(id+"F0.wireOp",EDGE,"E2732"),sQuery(id+"F0.wireOp",EDGE,"E2733"),sQuery(id+"F0.wireOp",EDGE,"E2734"),sQuery(id+"F0.wireOp",EDGE,"E2735"),sQuery(id+"F0.wireOp",EDGE,"E2736"),sQuery(id+"F0.wireOp",EDGE,"E2737"),sQuery(id+"F0.wireOp",EDGE,"E2738"),sQuery(id+"F0.wireOp",EDGE,"E2739"),sQuery(id+"F0.wireOp",EDGE,"E2740"),sQuery(id+"F0.wireOp",EDGE,"E2741"),sQuery(id+"F0.wireOp",EDGE,"E2742"),sQuery(id+"F0.wireOp",EDGE,"E2743"),sQuery(id+"F0.wireOp",EDGE,"E2744"),sQuery(id+"F0.wireOp",EDGE,"E2745"),sQuery(id+"F0.wireOp",EDGE,"E2746"),sQuery(id+"F0.wireOp",EDGE,"E2747"),sQuery(id+"F0.wireOp",EDGE,"E2748"),sQuery(id+"F0.wireOp",EDGE,"E2749"),sQuery(id+"F0.wireOp",EDGE,"E2750"),sQuery(id+"F0.wireOp",EDGE,"E2751"),sQuery(id+"F0.wireOp",EDGE,"E2752"),sQuery(id+"F0.wireOp",EDGE,"E2753"),sQuery(id+"F0.wireOp",EDGE,"E2754"),sQuery(id+"F0.wireOp",EDGE,"E2755"),sQuery(id+"F0.wireOp",EDGE,"E2756"),sQuery(id+"F0.wireOp",EDGE,"E2757"),sQuery(id+"F0.wireOp",EDGE,"E2758"),sQuery(id+"F0.wireOp",EDGE,"E2759"),sQuery(id+"F0.wireOp",EDGE,"E2760"),sQuery(id+"F0.wireOp",EDGE,"E2761"),sQuery(id+"F0.wireOp",EDGE,"E2762"),sQuery(id+"F0.wireOp",EDGE,"E2763"),sQuery(id+"F0.wireOp",EDGE,"E2764"),sQuery(id+"F0.wireOp",EDGE,"E2765"),sQuery(id+"F0.wireOp",EDGE,"E2766"),sQuery(id+"F0.wireOp",EDGE,"E2767"),sQuery(id+"F0.wireOp",EDGE,"E2768"),sQuery(id+"F0.wireOp",EDGE,"E2769"),sQuery(id+"F0.wireOp",EDGE,"E2770"),sQuery(id+"F0.wireOp",EDGE,"E2771"),sQuery(id+"F0.wireOp",EDGE,"E2772"),sQuery(id+"F0.wireOp",EDGE,"E2773"),sQuery(id+"F0.wireOp",EDGE,"E2774"),sQuery(id+"F0.wireOp",EDGE,"E2775"),sQuery(id+"F0.wireOp",EDGE,"E2776"),sQuery(id+"F0.wireOp",EDGE,"E2777"),sQuery(id+"F0.wireOp",EDGE,"E2778"),sQuery(id+"F0.wireOp",EDGE,"E2779"),sQuery(id+"F0.wireOp",EDGE,"E2780"),sQuery(id+"F0.wireOp",EDGE,"E2781"),sQuery(id+"F0.wireOp",EDGE,"E2782"),sQuery(id+"F0.wireOp",EDGE,"E2783"),sQuery(id+"F0.wireOp",EDGE,"E2784"),sQuery(id+"F0.wireOp",EDGE,"E2785"),sQuery(id+"F0.wireOp",EDGE,"E2786"),sQuery(id+"F0.wireOp",EDGE,"E2787"),sQuery(id+"F0.wireOp",EDGE,"E2788"),sQuery(id+"F0.wireOp",EDGE,"E2789"),sQuery(id+"F0.wireOp",EDGE,"E2790"),sQuery(id+"F0.wireOp",EDGE,"E2791"),sQuery(id+"F0.wireOp",EDGE,"E2792"),sQuery(id+"F0.wireOp",EDGE,"E2793"),sQuery(id+"F0.wireOp",EDGE,"E2794"),sQuery(id+"F0.wireOp",EDGE,"E2795"),sQuery(id+"F0.wireOp",EDGE,"E2796"),sQuery(id+"F0.wireOp",EDGE,"E2797"),sQuery(id+"F0.wireOp",EDGE,"E2798"),sQuery(id+"F0.wireOp",EDGE,"E2799"),sQuery(id+"F0.wireOp",EDGE,"E2800"),sQuery(id+"F0.wireOp",EDGE,"E2801"),sQuery(id+"F0.wireOp",EDGE,"E2802"),sQuery(id+"F0.wireOp",EDGE,"E2803"),sQuery(id+"F0.wireOp",EDGE,"E2804"),sQuery(id+"F0.wireOp",EDGE,"E2805"),sQuery(id+"F0.wireOp",EDGE,"E2806"),sQuery(id+"F0.wireOp",EDGE,"E2807"),sQuery(id+"F0.wireOp",EDGE,"E2808"),sQuery(id+"F0.wireOp",EDGE,"E2809"),sQuery(id+"F0.wireOp",EDGE,"E2810"),sQuery(id+"F0.wireOp",EDGE,"E2811"),sQuery(id+"F0.wireOp",EDGE,"E2812"),sQuery(id+"F0.wireOp",EDGE,"E2813"),sQuery(id+"F0.wireOp",EDGE,"E2814"),sQuery(id+"F0.wireOp",EDGE,"E2815"),sQuery(id+"F0.wireOp",EDGE,"E2816"),sQuery(id+"F0.wireOp",EDGE,"E2817"),sQuery(id+"F0.wireOp",EDGE,"E2818"),sQuery(id+"F0.wireOp",EDGE,"E2819"),sQuery(id+"F0.wireOp",EDGE,"E2820"),sQuery(id+"F0.wireOp",EDGE,"E2821"),sQuery(id+"F0.wireOp",EDGE,"E2822"),sQuery(id+"F0.wireOp",EDGE,"E2823"),sQuery(id+"F0.wireOp",EDGE,"E2824"),sQuery(id+"F0.wireOp",EDGE,"E2825"),sQuery(id+"F0.wireOp",EDGE,"E2826"),sQuery(id+"F0.wireOp",EDGE,"E2827"),sQuery(id+"F0.wireOp",EDGE,"E2828"),sQuery(id+"F0.wireOp",EDGE,"E2829"),sQuery(id+"F0.wireOp",EDGE,"E2830"),sQuery(id+"F0.wireOp",EDGE,"E2831"),sQuery(id+"F0.wireOp",EDGE,"E2832"),sQuery(id+"F0.wireOp",EDGE,"E2833"),sQuery(id+"F0.wireOp",EDGE,"E2834"),sQuery(id+"F0.wireOp",EDGE,"E2835"),sQuery(id+"F0.wireOp",EDGE,"E2836"),sQuery(id+"F0.wireOp",EDGE,"E2837"),sQuery(id+"F0.wireOp",EDGE,"E2838"),sQuery(id+"F0.wireOp",EDGE,"E2839"),sQuery(id+"F0.wireOp",EDGE,"E2840"),sQuery(id+"F0.wireOp",EDGE,"E2841"),sQuery(id+"F0.wireOp",EDGE,"E2842"),sQuery(id+"F0.wireOp",EDGE,"E2843"),sQuery(id+"F0.wireOp",EDGE,"E2844"),sQuery(id+"F0.wireOp",EDGE,"E2845"),sQuery(id+"F0.wireOp",EDGE,"E2846"),sQuery(id+"F0.wireOp",EDGE,"E2847"),sQuery(id+"F0.wireOp",EDGE,"E2848"),sQuery(id+"F0.wireOp",EDGE,"E2849"),sQuery(id+"F0.wireOp",EDGE,"E2850"),sQuery(id+"F0.wireOp",EDGE,"E2851"),sQuery(id+"F0.wireOp",EDGE,"E2852"),sQuery(id+"F0.wireOp",EDGE,"E2853"),sQuery(id+"F0.wireOp",EDGE,"E2854"),sQuery(id+"F0.wireOp",EDGE,"E2855"),sQuery(id+"F0.wireOp",EDGE,"E2856"),sQuery(id+"F0.wireOp",EDGE,"E2857"),sQuery(id+"F0.wireOp",EDGE,"E2858"),sQuery(id+"F0.wireOp",EDGE,"E2859"),sQuery(id+"F0.wireOp",EDGE,"E2860"),sQuery(id+"F0.wireOp",EDGE,"E2861"),sQuery(id+"F0.wireOp",EDGE,"E2862"),sQuery(id+"F0.wireOp",EDGE,"E2863"),sQuery(id+"F0.wireOp",EDGE,"E2864"),sQuery(id+"F0.wireOp",EDGE,"E2865"),sQuery(id+"F0.wireOp",EDGE,"E2866"),sQuery(id+"F0.wireOp",EDGE,"E2867"),sQuery(id+"F0.wireOp",EDGE,"E2868"),sQuery(id+"F0.wireOp",EDGE,"E2869"),sQuery(id+"F0.wireOp",EDGE,"E2870"),sQuery(id+"F0.wireOp",EDGE,"E2871"),sQuery(id+"F0.wireOp",EDGE,"E2872"),sQuery(id+"F0.wireOp",EDGE,"E2873"),sQuery(id+"F0.wireOp",EDGE,"E2874"),sQuery(id+"F0.wireOp",EDGE,"E2875"),sQuery(id+"F0.wireOp",EDGE,"E2876"),sQuery(id+"F0.wireOp",EDGE,"E2877"),sQuery(id+"F0.wireOp",EDGE,"E2878"),sQuery(id+"F0.wireOp",EDGE,"E2879"),sQuery(id+"F0.wireOp",EDGE,"E2880"),sQuery(id+"F0.wireOp",EDGE,"E2881"),sQuery(id+"F0.wireOp",EDGE,"E2882"),sQuery(id+"F0.wireOp",EDGE,"E2883"),sQuery(id+"F0.wireOp",EDGE,"E2884"),sQuery(id+"F0.wireOp",EDGE,"E2885"),sQuery(id+"F0.wireOp",EDGE,"E2886"),sQuery(id+"F0.wireOp",EDGE,"E2887"),sQuery(id+"F0.wireOp",EDGE,"E2888"),sQuery(id+"F0.wireOp",EDGE,"E2889"),sQuery(id+"F0.wireOp",EDGE,"E2890"),sQuery(id+"F0.wireOp",EDGE,"E2891"),sQuery(id+"F0.wireOp",EDGE,"E2892"),sQuery(id+"F0.wireOp",EDGE,"E2893"),sQuery(id+"F0.wireOp",EDGE,"E2894"),sQuery(id+"F0.wireOp",EDGE,"E2895"),sQuery(id+"F0.wireOp",EDGE,"E2896"),sQuery(id+"F0.wireOp",EDGE,"E2897"),sQuery(id+"F0.wireOp",EDGE,"E2898"),sQuery(id+"F0.wireOp",EDGE,"E2899"),sQuery(id+"F0.wireOp",EDGE,"E2900"),sQuery(id+"F0.wireOp",EDGE,"E2901"),sQuery(id+"F0.wireOp",EDGE,"E2902"),sQuery(id+"F0.wireOp",EDGE,"E2903"),sQuery(id+"F0.wireOp",EDGE,"E2904"),sQuery(id+"F0.wireOp",EDGE,"E2905"),sQuery(id+"F0.wireOp",EDGE,"E2906"),sQuery(id+"F0.wireOp",EDGE,"E2907"),sQuery(id+"F0.wireOp",EDGE,"E2908"),sQuery(id+"F0.wireOp",EDGE,"E2909"),sQuery(id+"F0.wireOp",EDGE,"E2910"),sQuery(id+"F0.wireOp",EDGE,"E2911"),sQuery(id+"F0.wireOp",EDGE,"E2912"),sQuery(id+"F0.wireOp",EDGE,"E2913"),sQuery(id+"F0.wireOp",EDGE,"E2914"),sQuery(id+"F0.wireOp",EDGE,"E2915"),sQuery(id+"F0.wireOp",EDGE,"E2916"),sQuery(id+"F0.wireOp",EDGE,"E2917"),sQuery(id+"F0.wireOp",EDGE,"E2918"),sQuery(id+"F0.wireOp",EDGE,"E2919"),sQuery(id+"F0.wireOp",EDGE,"E2920"),sQuery(id+"F0.wireOp",EDGE,"E2921"),sQuery(id+"F0.wireOp",EDGE,"E2922"),sQuery(id+"F0.wireOp",EDGE,"E2923"),sQuery(id+"F0.wireOp",EDGE,"E2924"),sQuery(id+"F0.wireOp",EDGE,"E2925"),sQuery(id+"F0.wireOp",EDGE,"E2926"),sQuery(id+"F0.wireOp",EDGE,"E2927"),sQuery(id+"F0.wireOp",EDGE,"E2928"),sQuery(id+"F0.wireOp",EDGE,"E2929"),sQuery(id+"F0.wireOp",EDGE,"E2930"),sQuery(id+"F0.wireOp",EDGE,"E2931"),sQuery(id+"F0.wireOp",EDGE,"E2932"),sQuery(id+"F0.wireOp",EDGE,"E2933"),sQuery(id+"F0.wireOp",EDGE,"E2934"),sQuery(id+"F0.wireOp",EDGE,"E2935"),sQuery(id+"F0.wireOp",EDGE,"E2936"),sQuery(id+"F0.wireOp",EDGE,"E2937"),sQuery(id+"F0.wireOp",EDGE,"E2938"),sQuery(id+"F0.wireOp",EDGE,"E2939"),sQuery(id+"F0.wireOp",EDGE,"E2940"),sQuery(id+"F0.wireOp",EDGE,"E2941"),sQuery(id+"F0.wireOp",EDGE,"E2942"),sQuery(id+"F0.wireOp",EDGE,"E2943"),sQuery(id+"F0.wireOp",EDGE,"E2944"),sQuery(id+"F0.wireOp",EDGE,"E2945"),sQuery(id+"F0.wireOp",EDGE,"E2946"),sQuery(id+"F0.wireOp",EDGE,"E2947"),sQuery(id+"F0.wireOp",EDGE,"E2948"),sQuery(id+"F0.wireOp",EDGE,"E2949"),sQuery(id+"F0.wireOp",EDGE,"E2950"),sQuery(id+"F0.wireOp",EDGE,"E2951"),sQuery(id+"F0.wireOp",EDGE,"E2952"),sQuery(id+"F0.wireOp",EDGE,"E2953"),sQuery(id+"F0.wireOp",EDGE,"E2954"),sQuery(id+"F0.wireOp",EDGE,"E2955"),sQuery(id+"F0.wireOp",EDGE,"E2956"),sQuery(id+"F0.wireOp",EDGE,"E2957"),sQuery(id+"F0.wireOp",EDGE,"E2958"),sQuery(id+"F0.wireOp",EDGE,"E2959"),sQuery(id+"F0.wireOp",EDGE,"E2960"),sQuery(id+"F0.wireOp",EDGE,"E2961"),sQuery(id+"F0.wireOp",EDGE,"E2962"),sQuery(id+"F0.wireOp",EDGE,"E2963"),sQuery(id+"F0.wireOp",EDGE,"E2964"),sQuery(id+"F0.wireOp",EDGE,"E2965"),sQuery(id+"F0.wireOp",EDGE,"E2966"),sQuery(id+"F0.wireOp",EDGE,"E2967"),sQuery(id+"F0.wireOp",EDGE,"E2968"),sQuery(id+"F0.wireOp",EDGE,"E2969"),sQuery(id+"F0.wireOp",EDGE,"E2970"),sQuery(id+"F0.wireOp",EDGE,"E2971"),sQuery(id+"F0.wireOp",EDGE,"E2972"),sQuery(id+"F0.wireOp",EDGE,"E2973"),sQuery(id+"F0.wireOp",EDGE,"E2974"),sQuery(id+"F0.wireOp",EDGE,"E2975"),sQuery(id+"F0.wireOp",EDGE,"E2976"),sQuery(id+"F0.wireOp",EDGE,"E2977"),sQuery(id+"F0.wireOp",EDGE,"E2978"),sQuery(id+"F0.wireOp",EDGE,"E2979"),sQuery(id+"F0.wireOp",EDGE,"E2980"),sQuery(id+"F0.wireOp",EDGE,"E2981"),sQuery(id+"F0.wireOp",EDGE,"E2982"),sQuery(id+"F0.wireOp",EDGE,"E2983"),sQuery(id+"F0.wireOp",EDGE,"E2984"),sQuery(id+"F0.wireOp",EDGE,"E2985"),sQuery(id+"F0.wireOp",EDGE,"E2986"),sQuery(id+"F0.wireOp",EDGE,"E2987"),sQuery(id+"F0.wireOp",EDGE,"E2988"),sQuery(id+"F0.wireOp",EDGE,"E2989"),sQuery(id+"F0.wireOp",EDGE,"E2990"),sQuery(id+"F0.wireOp",EDGE,"E2991"),sQuery(id+"F0.wireOp",EDGE,"E2992"),sQuery(id+"F0.wireOp",EDGE,"E2993"),sQuery(id+"F0.wireOp",EDGE,"E2994"),sQuery(id+"F0.wireOp",EDGE,"E2995"),sQuery(id+"F0.wireOp",EDGE,"E2996"),sQuery(id+"F0.wireOp",EDGE,"E2997"),sQuery(id+"F0.wireOp",EDGE,"E2998"),sQuery(id+"F0.wireOp",EDGE,"E2999"),sQuery(id+"F0.wireOp",EDGE,"E3000"),sQuery(id+"F0.wireOp",EDGE,"E3001"),sQuery(id+"F0.wireOp",EDGE,"E3002"),sQuery(id+"F0.wireOp",EDGE,"E3003"),sQuery(id+"F0.wireOp",EDGE,"E3004"),sQuery(id+"F0.wireOp",EDGE,"E3005"),sQuery(id+"F0.wireOp",EDGE,"E3006"),sQuery(id+"F0.wireOp",EDGE,"E3007"),sQuery(id+"F0.wireOp",EDGE,"E3008"),sQuery(id+"F0.wireOp",EDGE,"E3009"),sQuery(id+"F0.wireOp",EDGE,"E3010"),sQuery(id+"F0.wireOp",EDGE,"E3011"),sQuery(id+"F0.wireOp",EDGE,"E3012"),sQuery(id+"F0.wireOp",EDGE,"E3013"),sQuery(id+"F0.wireOp",EDGE,"E3014"),sQuery(id+"F0.wireOp",EDGE,"E3015"),sQuery(id+"F0.wireOp",EDGE,"E3016"),sQuery(id+"F0.wireOp",EDGE,"E3017"),sQuery(id+"F0.wireOp",EDGE,"E3018"),sQuery(id+"F0.wireOp",EDGE,"E3019"),sQuery(id+"F0.wireOp",EDGE,"E3020"),sQuery(id+"F0.wireOp",EDGE,"E3021"),sQuery(id+"F0.wireOp",EDGE,"E3022"),sQuery(id+"F0.wireOp",EDGE,"E3023"),sQuery(id+"F0.wireOp",EDGE,"E3024"),sQuery(id+"F0.wireOp",EDGE,"E3025"),sQuery(id+"F0.wireOp",EDGE,"E3026"),sQuery(id+"F0.wireOp",EDGE,"E3027"),sQuery(id+"F0.wireOp",EDGE,"E3028"),sQuery(id+"F0.wireOp",EDGE,"E3029"),sQuery(id+"F0.wireOp",EDGE,"E3030"),sQuery(id+"F0.wireOp",EDGE,"E3031"),sQuery(id+"F0.wireOp",EDGE,"E3032"),sQuery(id+"F0.wireOp",EDGE,"E3033"),sQuery(id+"F0.wireOp",EDGE,"E3034"),sQuery(id+"F0.wireOp",EDGE,"E3035"),sQuery(id+"F0.wireOp",EDGE,"E3036"),sQuery(id+"F0.wireOp",EDGE,"E3037"),sQuery(id+"F0.wireOp",EDGE,"E3038"),sQuery(id+"F0.wireOp",EDGE,"E3039"),sQuery(id+"F0.wireOp",EDGE,"E3040"),sQuery(id+"F0.wireOp",EDGE,"E3041"),sQuery(id+"F0.wireOp",EDGE,"E3042"),sQuery(id+"F0.wireOp",EDGE,"E3043"),sQuery(id+"F0.wireOp",EDGE,"E3044"),sQuery(id+"F0.wireOp",EDGE,"E3045"),sQuery(id+"F0.wireOp",EDGE,"E3046"),sQuery(id+"F0.wireOp",EDGE,"E3047"),sQuery(id+"F0.wireOp",EDGE,"E3048"),sQuery(id+"F0.wireOp",EDGE,"E3049"),sQuery(id+"F0.wireOp",EDGE,"E3050"),sQuery(id+"F0.wireOp",EDGE,"E3051"),sQuery(id+"F0.wireOp",EDGE,"E3052"),sQuery(id+"F0.wireOp",EDGE,"E3053"),sQuery(id+"F0.wireOp",EDGE,"E3054"),sQuery(id+"F0.wireOp",EDGE,"E3055"),sQuery(id+"F0.wireOp",EDGE,"E3056"),sQuery(id+"F0.wireOp",EDGE,"E3057"),sQuery(id+"F0.wireOp",EDGE,"E3058"),sQuery(id+"F0.wireOp",EDGE,"E3059"),sQuery(id+"F0.wireOp",EDGE,"E3060"),sQuery(id+"F0.wireOp",EDGE,"E3061"),sQuery(id+"F0.wireOp",EDGE,"E3062"),sQuery(id+"F0.wireOp",EDGE,"E3063"),sQuery(id+"F0.wireOp",EDGE,"E3064"),sQuery(id+"F0.wireOp",EDGE,"E3065"),sQuery(id+"F0.wireOp",EDGE,"E3066"),sQuery(id+"F0.wireOp",EDGE,"E3067"),sQuery(id+"F0.wireOp",EDGE,"E3068"),sQuery(id+"F0.wireOp",EDGE,"E3069"),sQuery(id+"F0.wireOp",EDGE,"E3070"),sQuery(id+"F0.wireOp",EDGE,"E3071"),sQuery(id+"F0.wireOp",EDGE,"E3072"),sQuery(id+"F0.wireOp",EDGE,"E3073"),sQuery(id+"F0.wireOp",EDGE,"E3074"),sQuery(id+"F0.wireOp",EDGE,"E3075"),sQuery(id+"F0.wireOp",EDGE,"E3076"),sQuery(id+"F0.wireOp",EDGE,"E3077"),sQuery(id+"F0.wireOp",EDGE,"E3078"),sQuery(id+"F0.wireOp",EDGE,"E3079"),sQuery(id+"F0.wireOp",EDGE,"E3080"),sQuery(id+"F0.wireOp",EDGE,"E3081"),sQuery(id+"F0.wireOp",EDGE,"E3082"),sQuery(id+"F0.wireOp",EDGE,"E3083"),sQuery(id+"F0.wireOp",EDGE,"E3084"),sQuery(id+"F0.wireOp",EDGE,"E3085"),sQuery(id+"F0.wireOp",EDGE,"E3086"),sQuery(id+"F0.wireOp",EDGE,"E3087"),sQuery(id+"F0.wireOp",EDGE,"E3088"),sQuery(id+"F0.wireOp",EDGE,"E3089"),sQuery(id+"F0.wireOp",EDGE,"E3090"),sQuery(id+"F0.wireOp",EDGE,"E3091"),sQuery(id+"F0.wireOp",EDGE,"E3092"),sQuery(id+"F0.wireOp",EDGE,"E3093"),sQuery(id+"F0.wireOp",EDGE,"E3094"),sQuery(id+"F0.wireOp",EDGE,"E3095"),sQuery(id+"F0.wireOp",EDGE,"E3096"),sQuery(id+"F0.wireOp",EDGE,"E3097"),sQuery(id+"F0.wireOp",EDGE,"E3098"),sQuery(id+"F0.wireOp",EDGE,"E3099"),sQuery(id+"F0.wireOp",EDGE,"E3100"),sQuery(id+"F0.wireOp",EDGE,"E3101"),sQuery(id+"F0.wireOp",EDGE,"E3102"),sQuery(id+"F0.wireOp",EDGE,"E3103"),sQuery(id+"F0.wireOp",EDGE,"E3104"),sQuery(id+"F0.wireOp",EDGE,"E3105"),sQuery(id+"F0.wireOp",EDGE,"E3106"),sQuery(id+"F0.wireOp",EDGE,"E3107"),sQuery(id+"F0.wireOp",EDGE,"E3108"),sQuery(id+"F0.wireOp",EDGE,"E3109"),sQuery(id+"F0.wireOp",EDGE,"E3110"),sQuery(id+"F0.wireOp",EDGE,"E3111"),sQuery(id+"F0.wireOp",EDGE,"E3112"),sQuery(id+"F0.wireOp",EDGE,"E3113"),sQuery(id+"F0.wireOp",EDGE,"E3114"),sQuery(id+"F0.wireOp",EDGE,"E3115"),sQuery(id+"F0.wireOp",EDGE,"E3116"),sQuery(id+"F0.wireOp",EDGE,"E3117"),sQuery(id+"F0.wireOp",EDGE,"E3118"),sQuery(id+"F0.wireOp",EDGE,"E3119"),sQuery(id+"F0.wireOp",EDGE,"E3120"),sQuery(id+"F0.wireOp",EDGE,"E3121"),sQuery(id+"F0.wireOp",EDGE,"E3122"),sQuery(id+"F0.wireOp",EDGE,"E3123"),sQuery(id+"F0.wireOp",EDGE,"E3124"),sQuery(id+"F0.wireOp",EDGE,"E3125"),sQuery(id+"F0.wireOp",EDGE,"E3126"),sQuery(id+"F0.wireOp",EDGE,"E3127"),sQuery(id+"F0.wireOp",EDGE,"E3128"),sQuery(id+"F0.wireOp",EDGE,"E3129"),sQuery(id+"F0.wireOp",EDGE,"E3130"),sQuery(id+"F0.wireOp",EDGE,"E3131"),sQuery(id+"F0.wireOp",EDGE,"E3132"),sQuery(id+"F0.wireOp",EDGE,"E3133"),sQuery(id+"F0.wireOp",EDGE,"E3134"),sQuery(id+"F0.wireOp",EDGE,"E3135"),sQuery(id+"F0.wireOp",EDGE,"E3136"),sQuery(id+"F0.wireOp",EDGE,"E3137"),sQuery(id+"F0.wireOp",EDGE,"E3138"),sQuery(id+"F0.wireOp",EDGE,"E3139"),sQuery(id+"F0.wireOp",EDGE,"E3140"),sQuery(id+"F0.wireOp",EDGE,"E3141"),sQuery(id+"F0.wireOp",EDGE,"E3142"),sQuery(id+"F0.wireOp",EDGE,"E3143"),sQuery(id+"F0.wireOp",EDGE,"E3144"),sQuery(id+"F0.wireOp",EDGE,"E3145"),sQuery(id+"F0.wireOp",EDGE,"E3146"),sQuery(id+"F0.wireOp",EDGE,"E3147"),sQuery(id+"F0.wireOp",EDGE,"E3148"),sQuery(id+"F0.wireOp",EDGE,"E3149"),sQuery(id+"F0.wireOp",EDGE,"E3150"),sQuery(id+"F0.wireOp",EDGE,"E3151"),sQuery(id+"F0.wireOp",EDGE,"E3152"),sQuery(id+"F0.wireOp",EDGE,"E3153"),sQuery(id+"F0.wireOp",EDGE,"E3154"),sQuery(id+"F0.wireOp",EDGE,"E3155"),sQuery(id+"F0.wireOp",EDGE,"E3156"),sQuery(id+"F0.wireOp",EDGE,"E3157"),sQuery(id+"F0.wireOp",EDGE,"E3158"),sQuery(id+"F0.wireOp",EDGE,"E3159"),sQuery(id+"F0.wireOp",EDGE,"E3160"),sQuery(id+"F0.wireOp",EDGE,"E3161"),sQuery(id+"F0.wireOp",EDGE,"E3162"),sQuery(id+"F0.wireOp",EDGE,"E3163"),sQuery(id+"F0.wireOp",EDGE,"E3164"),sQuery(id+"F0.wireOp",EDGE,"E3165"),sQuery(id+"F0.wireOp",EDGE,"E3166"),sQuery(id+"F0.wireOp",EDGE,"E3167"),sQuery(id+"F0.wireOp",EDGE,"E3168"),sQuery(id+"F0.wireOp",EDGE,"E3169"),sQuery(id+"F0.wireOp",EDGE,"E3170"),sQuery(id+"F0.wireOp",EDGE,"E3171"),sQuery(id+"F0.wireOp",EDGE,"E3172"),sQuery(id+"F0.wireOp",EDGE,"E3173"),sQuery(id+"F0.wireOp",EDGE,"E3174"),sQuery(id+"F0.wireOp",EDGE,"E3175"),sQuery(id+"F0.wireOp",EDGE,"E3176"),sQuery(id+"F0.wireOp",EDGE,"E3177"),sQuery(id+"F0.wireOp",EDGE,"E3178"),sQuery(id+"F0.wireOp",EDGE,"E3179"),sQuery(id+"F0.wireOp",EDGE,"E3180"),sQuery(id+"F0.wireOp",EDGE,"E3181"),sQuery(id+"F0.wireOp",EDGE,"E3182"),sQuery(id+"F0.wireOp",EDGE,"E3183"),sQuery(id+"F0.wireOp",EDGE,"E3184"),sQuery(id+"F0.wireOp",EDGE,"E3185"),sQuery(id+"F0.wireOp",EDGE,"E3186"),sQuery(id+"F0.wireOp",EDGE,"E3187"),sQuery(id+"F0.wireOp",EDGE,"E3188"),sQuery(id+"F0.wireOp",EDGE,"E3189"),sQuery(id+"F0.wireOp",EDGE,"E3190"),sQuery(id+"F0.wireOp",EDGE,"E3191"),sQuery(id+"F0.wireOp",EDGE,"E3192"),sQuery(id+"F0.wireOp",EDGE,"E3193"),sQuery(id+"F0.wireOp",EDGE,"E3194"),sQuery(id+"F0.wireOp",EDGE,"E3195"),sQuery(id+"F0.wireOp",EDGE,"E3196"),sQuery(id+"F0.wireOp",EDGE,"E3197"),sQuery(id+"F0.wireOp",EDGE,"E3198"),sQuery(id+"F0.wireOp",EDGE,"E3199"),sQuery(id+"F0.wireOp",EDGE,"E3200"),sQuery(id+"F0.wireOp",EDGE,"E3201"),sQuery(id+"F0.wireOp",EDGE,"E3202"),sQuery(id+"F0.wireOp",EDGE,"E3203"),sQuery(id+"F0.wireOp",EDGE,"E3204"),sQuery(id+"F0.wireOp",EDGE,"E3205"),sQuery(id+"F0.wireOp",EDGE,"E3206"),sQuery(id+"F0.wireOp",EDGE,"E3207"),sQuery(id+"F0.wireOp",EDGE,"E3208"),sQuery(id+"F0.wireOp",EDGE,"E3209"),sQuery(id+"F0.wireOp",EDGE,"E3210"),sQuery(id+"F0.wireOp",EDGE,"E3211"),sQuery(id+"F0.wireOp",EDGE,"E3212"),sQuery(id+"F0.wireOp",EDGE,"E3213"),sQuery(id+"F0.wireOp",EDGE,"E3214"),sQuery(id+"F0.wireOp",EDGE,"E3215"),sQuery(id+"F0.wireOp",EDGE,"E3216"),sQuery(id+"F0.wireOp",EDGE,"E3217"),sQuery(id+"F0.wireOp",EDGE,"E3218"),sQuery(id+"F0.wireOp",EDGE,"E3219"),sQuery(id+"F0.wireOp",EDGE,"E3220"),sQuery(id+"F0.wireOp",EDGE,"E3221"),sQuery(id+"F0.wireOp",EDGE,"E3222"),sQuery(id+"F0.wireOp",EDGE,"E3223"),sQuery(id+"F0.wireOp",EDGE,"E3224"),sQuery(id+"F0.wireOp",EDGE,"E3225"),sQuery(id+"F0.wireOp",EDGE,"E3226"),sQuery(id+"F0.wireOp",EDGE,"E3227"),sQuery(id+"F0.wireOp",EDGE,"E3228"),sQuery(id+"F0.wireOp",EDGE,"E3229"),sQuery(id+"F0.wireOp",EDGE,"E3230"),sQuery(id+"F0.wireOp",EDGE,"E3231"),sQuery(id+"F0.wireOp",EDGE,"E3232"),sQuery(id+"F0.wireOp",EDGE,"E3233"),sQuery(id+"F0.wireOp",EDGE,"E3234"),sQuery(id+"F0.wireOp",EDGE,"E3235"),sQuery(id+"F0.wireOp",EDGE,"E3236"),sQuery(id+"F0.wireOp",EDGE,"E3237"),sQuery(id+"F0.wireOp",EDGE,"E3238"),sQuery(id+"F0.wireOp",EDGE,"E3239"),sQuery(id+"F0.wireOp",EDGE,"E3240"),sQuery(id+"F0.wireOp",EDGE,"E3241"),sQuery(id+"F0.wireOp",EDGE,"E3242"),sQuery(id+"F0.wireOp",EDGE,"E3243"),sQuery(id+"F0.wireOp",EDGE,"E3244"),sQuery(id+"F0.wireOp",EDGE,"E3245"),sQuery(id+"F0.wireOp",EDGE,"E3246"),sQuery(id+"F0.wireOp",EDGE,"E3247"),sQuery(id+"F0.wireOp",EDGE,"E3248"),sQuery(id+"F0.wireOp",EDGE,"E3249"),sQuery(id+"F0.wireOp",EDGE,"E3250"),sQuery(id+"F0.wireOp",EDGE,"E3251"),sQuery(id+"F0.wireOp",EDGE,"E3252"),sQuery(id+"F0.wireOp",EDGE,"E3253"),sQuery(id+"F0.wireOp",EDGE,"E3254"),sQuery(id+"F0.wireOp",EDGE,"E3255"),sQuery(id+"F0.wireOp",EDGE,"E3256"),sQuery(id+"F0.wireOp",EDGE,"E3257"),sQuery(id+"F0.wireOp",EDGE,"E3258"),sQuery(id+"F0.wireOp",EDGE,"E3259"),sQuery(id+"F0.wireOp",EDGE,"E3260"),sQuery(id+"F0.wireOp",EDGE,"E3261"),sQuery(id+"F0.wireOp",EDGE,"E3262"),sQuery(id+"F0.wireOp",EDGE,"E3263"),sQuery(id+"F0.wireOp",EDGE,"E3264"),sQuery(id+"F0.wireOp",EDGE,"E3265"),sQuery(id+"F0.wireOp",EDGE,"E3266"),sQuery(id+"F0.wireOp",EDGE,"E3267"),sQuery(id+"F0.wireOp",EDGE,"E3268"),sQuery(id+"F0.wireOp",EDGE,"E3269"),sQuery(id+"F0.wireOp",EDGE,"E3270"),sQuery(id+"F0.wireOp",EDGE,"E3271"),sQuery(id+"F0.wireOp",EDGE,"E3272"),sQuery(id+"F0.wireOp",EDGE,"E3273"),sQuery(id+"F0.wireOp",EDGE,"E3274"),sQuery(id+"F0.wireOp",EDGE,"E3275"),sQuery(id+"F0.wireOp",EDGE,"E3276"),sQuery(id+"F0.wireOp",EDGE,"E3277"),sQuery(id+"F0.wireOp",EDGE,"E3278"),sQuery(id+"F0.wireOp",EDGE,"E3279"),sQuery(id+"F0.wireOp",EDGE,"E3280"),sQuery(id+"F0.wireOp",EDGE,"E3281"),sQuery(id+"F0.wireOp",EDGE,"E3282"),sQuery(id+"F0.wireOp",EDGE,"E3283"),sQuery(id+"F0.wireOp",EDGE,"E3284"),sQuery(id+"F0.wireOp",EDGE,"E3285"),sQuery(id+"F0.wireOp",EDGE,"E3286"),sQuery(id+"F0.wireOp",EDGE,"E3287"),sQuery(id+"F0.wireOp",EDGE,"E3288"),sQuery(id+"F0.wireOp",EDGE,"E3289"),sQuery(id+"F0.wireOp",EDGE,"E3290"),sQuery(id+"F0.wireOp",EDGE,"E3291"),sQuery(id+"F0.wireOp",EDGE,"E3292"),sQuery(id+"F0.wireOp",EDGE,"E3293"),sQuery(id+"F0.wireOp",EDGE,"E3294"),sQuery(id+"F0.wireOp",EDGE,"E3295"),sQuery(id+"F0.wireOp",EDGE,"E3296"),sQuery(id+"F0.wireOp",EDGE,"E3297"),sQuery(id+"F0.wireOp",EDGE,"E3298"),sQuery(id+"F0.wireOp",EDGE,"E3299"),sQuery(id+"F0.wireOp",EDGE,"E3300"),sQuery(id+"F0.wireOp",EDGE,"E3301"),sQuery(id+"F0.wireOp",EDGE,"E3302"),sQuery(id+"F0.wireOp",EDGE,"E3303"),sQuery(id+"F0.wireOp",EDGE,"E3304"),sQuery(id+"F0.wireOp",EDGE,"E3305"),sQuery(id+"F0.wireOp",EDGE,"E3306"),sQuery(id+"F0.wireOp",EDGE,"E3307"),sQuery(id+"F0.wireOp",EDGE,"E3308"),sQuery(id+"F0.wireOp",EDGE,"E3309"),sQuery(id+"F0.wireOp",EDGE,"E3310"),sQuery(id+"F0.wireOp",EDGE,"E3311"),sQuery(id+"F0.wireOp",EDGE,"E3312"),sQuery(id+"F0.wireOp",EDGE,"E3313"),sQuery(id+"F0.wireOp",EDGE,"E3314"),sQuery(id+"F0.wireOp",EDGE,"E3315"),sQuery(id+"F0.wireOp",EDGE,"E3316"),sQuery(id+"F0.wireOp",EDGE,"E3317"),sQuery(id+"F0.wireOp",EDGE,"E3318"),sQuery(id+"F0.wireOp",EDGE,"E3319"),sQuery(id+"F0.wireOp",EDGE,"E3320"),sQuery(id+"F0.wireOp",EDGE,"E3321"),sQuery(id+"F0.wireOp",EDGE,"E3322"),sQuery(id+"F0.wireOp",EDGE,"E3323"),sQuery(id+"F0.wireOp",EDGE,"E3324"),sQuery(id+"F0.wireOp",EDGE,"E3325"),sQuery(id+"F0.wireOp",EDGE,"E3326"),sQuery(id+"F0.wireOp",EDGE,"E3327"),sQuery(id+"F0.wireOp",EDGE,"E3328"),sQuery(id+"F0.wireOp",EDGE,"E3329"),sQuery(id+"F0.wireOp",EDGE,"E3330"),sQuery(id+"F0.wireOp",EDGE,"E3331"),sQuery(id+"F0.wireOp",EDGE,"E3332"),sQuery(id+"F0.wireOp",EDGE,"E3333"),sQuery(id+"F0.wireOp",EDGE,"E3334"),sQuery(id+"F0.wireOp",EDGE,"E3335"),sQuery(id+"F0.wireOp",EDGE,"E3336"),sQuery(id+"F0.wireOp",EDGE,"E3337"),sQuery(id+"F0.wireOp",EDGE,"E3338"),sQuery(id+"F0.wireOp",EDGE,"E3339"),sQuery(id+"F0.wireOp",EDGE,"E3340"),sQuery(id+"F0.wireOp",EDGE,"E3341"),sQuery(id+"F0.wireOp",EDGE,"E3342"),sQuery(id+"F0.wireOp",EDGE,"E3343"),sQuery(id+"F0.wireOp",EDGE,"E3344"),sQuery(id+"F0.wireOp",EDGE,"E3345"),sQuery(id+"F0.wireOp",EDGE,"E3346"),sQuery(id+"F0.wireOp",EDGE,"E3347"),sQuery(id+"F0.wireOp",EDGE,"E3348"),sQuery(id+"F0.wireOp",EDGE,"E3349"),sQuery(id+"F0.wireOp",EDGE,"E3350"),sQuery(id+"F0.wireOp",EDGE,"E3351"),sQuery(id+"F0.wireOp",EDGE,"E3352"),sQuery(id+"F0.wireOp",EDGE,"E3353"),sQuery(id+"F0.wireOp",EDGE,"E3354"),sQuery(id+"F0.wireOp",EDGE,"E3355"),sQuery(id+"F0.wireOp",EDGE,"E3356"),sQuery(id+"F0.wireOp",EDGE,"E3357"),sQuery(id+"F0.wireOp",EDGE,"E3358"),sQuery(id+"F0.wireOp",EDGE,"E3359"),sQuery(id+"F0.wireOp",EDGE,"E3360"),sQuery(id+"F0.wireOp",EDGE,"E3361"),sQuery(id+"F0.wireOp",EDGE,"E3362"),sQuery(id+"F0.wireOp",EDGE,"E3363"),sQuery(id+"F0.wireOp",EDGE,"E3364"),sQuery(id+"F0.wireOp",EDGE,"E3365"),sQuery(id+"F0.wireOp",EDGE,"E3366"),sQuery(id+"F0.wireOp",EDGE,"E3367"),sQuery(id+"F0.wireOp",EDGE,"E3368"),sQuery(id+"F0.wireOp",EDGE,"E3369"),sQuery(id+"F0.wireOp",EDGE,"E3370"),sQuery(id+"F0.wireOp",EDGE,"E3371"),sQuery(id+"F0.wireOp",EDGE,"E3372"),sQuery(id+"F0.wireOp",EDGE,"E3373"),sQuery(id+"F0.wireOp",EDGE,"E3374"),sQuery(id+"F0.wireOp",EDGE,"E3375"),sQuery(id+"F0.wireOp",EDGE,"E3376"),sQuery(id+"F0.wireOp",EDGE,"E3377"),sQuery(id+"F0.wireOp",EDGE,"E3378"),sQuery(id+"F0.wireOp",EDGE,"E3379"),sQuery(id+"F0.wireOp",EDGE,"E3380"),sQuery(id+"F0.wireOp",EDGE,"E3381"),sQuery(id+"F0.wireOp",EDGE,"E3382"),sQuery(id+"F0.wireOp",EDGE,"E3383"),sQuery(id+"F0.wireOp",EDGE,"E3384"),sQuery(id+"F0.wireOp",EDGE,"E3385"),sQuery(id+"F0.wireOp",EDGE,"E3386"),sQuery(id+"F0.wireOp",EDGE,"E3387"),sQuery(id+"F0.wireOp",EDGE,"E3388"),sQuery(id+"F0.wireOp",EDGE,"E3389"),sQuery(id+"F0.wireOp",EDGE,"E3390"),sQuery(id+"F0.wireOp",EDGE,"E3391"),sQuery(id+"F0.wireOp",EDGE,"E3392"),sQuery(id+"F0.wireOp",EDGE,"E3393"),sQuery(id+"F0.wireOp",EDGE,"E3394"),sQuery(id+"F0.wireOp",EDGE,"E3395"),sQuery(id+"F0.wireOp",EDGE,"E3396"),sQuery(id+"F0.wireOp",EDGE,"E3397"),sQuery(id+"F0.wireOp",EDGE,"E3398"),sQuery(id+"F0.wireOp",EDGE,"E3399"),sQuery(id+"F0.wireOp",EDGE,"E3400"),sQuery(id+"F0.wireOp",EDGE,"E3401"),sQuery(id+"F0.wireOp",EDGE,"E3402"),sQuery(id+"F0.wireOp",EDGE,"E3403"),sQuery(id+"F0.wireOp",EDGE,"E3404"),sQuery(id+"F0.wireOp",EDGE,"E3405"),sQuery(id+"F0.wireOp",EDGE,"E3406"),sQuery(id+"F0.wireOp",EDGE,"E3407"),sQuery(id+"F0.wireOp",EDGE,"E3408"),sQuery(id+"F0.wireOp",EDGE,"E3409"),sQuery(id+"F0.wireOp",EDGE,"E3410"),sQuery(id+"F0.wireOp",EDGE,"E3411"),sQuery(id+"F0.wireOp",EDGE,"E3412"),sQuery(id+"F0.wireOp",EDGE,"E3413"),sQuery(id+"F0.wireOp",EDGE,"E3414"),sQuery(id+"F0.wireOp",EDGE,"E3415"),sQuery(id+"F0.wireOp",EDGE,"E3416"),sQuery(id+"F0.wireOp",EDGE,"E3417"),sQuery(id+"F0.wireOp",EDGE,"E3418"),sQuery(id+"F0.wireOp",EDGE,"E3419"),sQuery(id+"F0.wireOp",EDGE,"E3420"),sQuery(id+"F0.wireOp",EDGE,"E3421"),sQuery(id+"F0.wireOp",EDGE,"E3422"),sQuery(id+"F0.wireOp",EDGE,"E3423"),sQuery(id+"F0.wireOp",EDGE,"E3424"),sQuery(id+"F0.wireOp",EDGE,"E3425"),sQuery(id+"F0.wireOp",EDGE,"E3426"),sQuery(id+"F0.wireOp",EDGE,"E3427"),sQuery(id+"F0.wireOp",EDGE,"E3428"),sQuery(id+"F0.wireOp",EDGE,"E3429"),sQuery(id+"F0.wireOp",EDGE,"E3430"),sQuery(id+"F0.wireOp",EDGE,"E3431"),sQuery(id+"F0.wireOp",EDGE,"E3432"),sQuery(id+"F0.wireOp",EDGE,"E3433"),sQuery(id+"F0.wireOp",EDGE,"E3434"),sQuery(id+"F0.wireOp",EDGE,"E3435"),sQuery(id+"F0.wireOp",EDGE,"E3436"),sQuery(id+"F0.wireOp",EDGE,"E3437"),sQuery(id+"F0.wireOp",EDGE,"E3438"),sQuery(id+"F0.wireOp",EDGE,"E3439"),sQuery(id+"F0.wireOp",EDGE,"E3440"),sQuery(id+"F0.wireOp",EDGE,"E3441"),sQuery(id+"F0.wireOp",EDGE,"E3442"),sQuery(id+"F0.wireOp",EDGE,"E3443"),sQuery(id+"F0.wireOp",EDGE,"E3444"),sQuery(id+"F0.wireOp",EDGE,"E3445"),sQuery(id+"F0.wireOp",EDGE,"E3446"),sQuery(id+"F0.wireOp",EDGE,"E3447"),sQuery(id+"F0.wireOp",EDGE,"E3448"),sQuery(id+"F0.wireOp",EDGE,"E3449"),sQuery(id+"F0.wireOp",EDGE,"E3450"),sQuery(id+"F0.wireOp",EDGE,"E3451"),sQuery(id+"F0.wireOp",EDGE,"E3452"),sQuery(id+"F0.wireOp",EDGE,"E3453"),sQuery(id+"F0.wireOp",EDGE,"E3454"),sQuery(id+"F0.wireOp",EDGE,"E3455"),sQuery(id+"F0.wireOp",EDGE,"E3456"),sQuery(id+"F0.wireOp",EDGE,"E3457"),sQuery(id+"F0.wireOp",EDGE,"E3458"),sQuery(id+"F0.wireOp",EDGE,"E3459"),sQuery(id+"F0.wireOp",EDGE,"E3460"),sQuery(id+"F0.wireOp",EDGE,"E3461"),sQuery(id+"F0.wireOp",EDGE,"E3462"),sQuery(id+"F0.wireOp",EDGE,"E3463"),sQuery(id+"F0.wireOp",EDGE,"E3464"),sQuery(id+"F0.wireOp",EDGE,"E3465"),sQuery(id+"F0.wireOp",EDGE,"E3466"),sQuery(id+"F0.wireOp",EDGE,"E3467"),sQuery(id+"F0.wireOp",EDGE,"E3468"),sQuery(id+"F0.wireOp",EDGE,"E3469"),sQuery(id+"F0.wireOp",EDGE,"E3470"),sQuery(id+"F0.wireOp",EDGE,"E3471"),sQuery(id+"F0.wireOp",EDGE,"E3472"),sQuery(id+"F0.wireOp",EDGE,"E3473"),sQuery(id+"F0.wireOp",EDGE,"E3474"),sQuery(id+"F0.wireOp",EDGE,"E3475"),sQuery(id+"F0.wireOp",EDGE,"E3476"),sQuery(id+"F0.wireOp",EDGE,"E3477"),sQuery(id+"F0.wireOp",EDGE,"E3478"),sQuery(id+"F0.wireOp",EDGE,"E3479"),sQuery(id+"F0.wireOp",EDGE,"E3480"),sQuery(id+"F0.wireOp",EDGE,"E3481"),sQuery(id+"F0.wireOp",EDGE,"E3482"),sQuery(id+"F0.wireOp",EDGE,"E3483"),sQuery(id+"F0.wireOp",EDGE,"E3484"),sQuery(id+"F0.wireOp",EDGE,"E3485"),sQuery(id+"F0.wireOp",EDGE,"E3486"),sQuery(id+"F0.wireOp",EDGE,"E3487"),sQuery(id+"F0.wireOp",EDGE,"E3488"),sQuery(id+"F0.wireOp",EDGE,"E3489"),sQuery(id+"F0.wireOp",EDGE,"E3490"),sQuery(id+"F0.wireOp",EDGE,"E3491"),sQuery(id+"F0.wireOp",EDGE,"E3492"),sQuery(id+"F0.wireOp",EDGE,"E3493"),sQuery(id+"F0.wireOp",EDGE,"E3494"),sQuery(id+"F0.wireOp",EDGE,"E3495"),sQuery(id+"F0.wireOp",EDGE,"E3496"),sQuery(id+"F0.wireOp",EDGE,"E3497"),sQuery(id+"F0.wireOp",EDGE,"E3498"),sQuery(id+"F0.wireOp",EDGE,"E3499"),sQuery(id+"F0.wireOp",EDGE,"E3500"),sQuery(id+"F0.wireOp",EDGE,"E3501"),sQuery(id+"F0.wireOp",EDGE,"E3502"),sQuery(id+"F0.wireOp",EDGE,"E3503"),sQuery(id+"F0.wireOp",EDGE,"E3504"),sQuery(id+"F0.wireOp",EDGE,"E3505"),sQuery(id+"F0.wireOp",EDGE,"E3506"),sQuery(id+"F0.wireOp",EDGE,"E3507"),sQuery(id+"F0.wireOp",EDGE,"E3508"),sQuery(id+"F0.wireOp",EDGE,"E3509"),sQuery(id+"F0.wireOp",EDGE,"E3510"),sQuery(id+"F0.wireOp",EDGE,"E3511"),sQuery(id+"F0.wireOp",EDGE,"E3512"),sQuery(id+"F0.wireOp",EDGE,"E3513"),sQuery(id+"F0.wireOp",EDGE,"E3514"),sQuery(id+"F0.wireOp",EDGE,"E3515"),sQuery(id+"F0.wireOp",EDGE,"E3516"),sQuery(id+"F0.wireOp",EDGE,"E3517"),sQuery(id+"F0.wireOp",EDGE,"E3518"),sQuery(id+"F0.wireOp",EDGE,"E3519"),sQuery(id+"F0.wireOp",EDGE,"E3520"),sQuery(id+"F0.wireOp",EDGE,"E3521"),sQuery(id+"F0.wireOp",EDGE,"E3522"),sQuery(id+"F0.wireOp",EDGE,"E3523"),sQuery(id+"F0.wireOp",EDGE,"E3524"),sQuery(id+"F0.wireOp",EDGE,"E3525"),sQuery(id+"F0.wireOp",EDGE,"E3526"),sQuery(id+"F0.wireOp",EDGE,"E3527"),sQuery(id+"F0.wireOp",EDGE,"E3528"),sQuery(id+"F0.wireOp",EDGE,"E3529"),sQuery(id+"F0.wireOp",EDGE,"E3530"),sQuery(id+"F0.wireOp",EDGE,"E3531"),sQuery(id+"F0.wireOp",EDGE,"E3532"),sQuery(id+"F0.wireOp",EDGE,"E3533"),sQuery(id+"F0.wireOp",EDGE,"E3534"),sQuery(id+"F0.wireOp",EDGE,"E3535"),sQuery(id+"F0.wireOp",EDGE,"E3536"),sQuery(id+"F0.wireOp",EDGE,"E3537"),sQuery(id+"F0.wireOp",EDGE,"E3538"),sQuery(id+"F0.wireOp",EDGE,"E3539"),sQuery(id+"F0.wireOp",EDGE,"E3540"),sQuery(id+"F0.wireOp",EDGE,"E3541"),sQuery(id+"F0.wireOp",EDGE,"E3542"),sQuery(id+"F0.wireOp",EDGE,"E3543"),sQuery(id+"F0.wireOp",EDGE,"E3544"),sQuery(id+"F0.wireOp",EDGE,"E3545"),sQuery(id+"F0.wireOp",EDGE,"E3546"),sQuery(id+"F0.wireOp",EDGE,"E3547"),sQuery(id+"F0.wireOp",EDGE,"E3548"),sQuery(id+"F0.wireOp",EDGE,"E3549"),sQuery(id+"F0.wireOp",EDGE,"E3550"),sQuery(id+"F0.wireOp",EDGE,"E3551"),sQuery(id+"F0.wireOp",EDGE,"E3552"),sQuery(id+"F0.wireOp",EDGE,"E3553"),sQuery(id+"F0.wireOp",EDGE,"E3554"),sQuery(id+"F0.wireOp",EDGE,"E3555"),sQuery(id+"F0.wireOp",EDGE,"E3556"),sQuery(id+"F0.wireOp",EDGE,"E3557"),sQuery(id+"F0.wireOp",EDGE,"E3558"),sQuery(id+"F0.wireOp",EDGE,"E3559"),sQuery(id+"F0.wireOp",EDGE,"E3560"),sQuery(id+"F0.wireOp",EDGE,"E3561"),sQuery(id+"F0.wireOp",EDGE,"E3562"),sQuery(id+"F0.wireOp",EDGE,"E3563"),sQuery(id+"F0.wireOp",EDGE,"E3564"),sQuery(id+"F0.wireOp",EDGE,"E3565"),sQuery(id+"F0.wireOp",EDGE,"E3566"),sQuery(id+"F0.wireOp",EDGE,"E3567"),sQuery(id+"F0.wireOp",EDGE,"E3568"),sQuery(id+"F0.wireOp",EDGE,"E3569"),sQuery(id+"F0.wireOp",EDGE,"E3570"),sQuery(id+"F0.wireOp",EDGE,"E3571"),sQuery(id+"F0.wireOp",EDGE,"E3572"),sQuery(id+"F0.wireOp",EDGE,"E3573"),sQuery(id+"F0.wireOp",EDGE,"E3574"),sQuery(id+"F0.wireOp",EDGE,"E3575"),sQuery(id+"F0.wireOp",EDGE,"E3576"),sQuery(id+"F0.wireOp",EDGE,"E3577"),sQuery(id+"F0.wireOp",EDGE,"E3578"),sQuery(id+"F0.wireOp",EDGE,"E3579"),sQuery(id+"F0.wireOp",EDGE,"E3580"),sQuery(id+"F0.wireOp",EDGE,"E3581"),sQuery(id+"F0.wireOp",EDGE,"E3582"),sQuery(id+"F0.wireOp",EDGE,"E3583"),sQuery(id+"F0.wireOp",EDGE,"E3584"),sQuery(id+"F0.wireOp",EDGE,"E3585"),sQuery(id+"F0.wireOp",EDGE,"E3586"),sQuery(id+"F0.wireOp",EDGE,"E3587"),sQuery(id+"F0.wireOp",EDGE,"E3588"),sQuery(id+"F0.wireOp",EDGE,"E3589"),sQuery(id+"F0.wireOp",EDGE,"E3590"),sQuery(id+"F0.wireOp",EDGE,"E3591"),sQuery(id+"F0.wireOp",EDGE,"E3592"),sQuery(id+"F0.wireOp",EDGE,"E3593"),sQuery(id+"F0.wireOp",EDGE,"E3594"),sQuery(id+"F0.wireOp",EDGE,"E3595"),sQuery(id+"F0.wireOp",EDGE,"E3596"),sQuery(id+"F0.wireOp",EDGE,"E3597"),sQuery(id+"F0.wireOp",EDGE,"E3598"),sQuery(id+"F0.wireOp",EDGE,"E3599"),sQuery(id+"F0.wireOp",EDGE,"E3600"),sQuery(id+"F0.wireOp",EDGE,"E3601"),sQuery(id+"F0.wireOp",EDGE,"E3602"),sQuery(id+"F0.wireOp",EDGE,"E3603"),sQuery(id+"F0.wireOp",EDGE,"E3604"),sQuery(id+"F0.wireOp",EDGE,"E3605"),sQuery(id+"F0.wireOp",EDGE,"E3606"),sQuery(id+"F0.wireOp",EDGE,"E3607"),sQuery(id+"F0.wireOp",EDGE,"E3608"),sQuery(id+"F0.wireOp",EDGE,"E3609"),sQuery(id+"F0.wireOp",EDGE,"E3610"),sQuery(id+"F0.wireOp",EDGE,"E3611"),sQuery(id+"F0.wireOp",EDGE,"E3612"),sQuery(id+"F0.wireOp",EDGE,"E3613"),sQuery(id+"F0.wireOp",EDGE,"E3614"),sQuery(id+"F0.wireOp",EDGE,"E3615"),sQuery(id+"F0.wireOp",EDGE,"E3616"),sQuery(id+"F0.wireOp",EDGE,"E3617"),sQuery(id+"F0.wireOp",EDGE,"E3618"),sQuery(id+"F0.wireOp",EDGE,"E3619"),sQuery(id+"F0.wireOp",EDGE,"E3620"),sQuery(id+"F0.wireOp",EDGE,"E3621"),sQuery(id+"F0.wireOp",EDGE,"E3622"),sQuery(id+"F0.wireOp",EDGE,"E3623"),sQuery(id+"F0.wireOp",EDGE,"E3624"),sQuery(id+"F0.wireOp",EDGE,"E3625"),sQuery(id+"F0.wireOp",EDGE,"E3626"),sQuery(id+"F0.wireOp",EDGE,"E3627"),sQuery(id+"F0.wireOp",EDGE,"E3628"),sQuery(id+"F0.wireOp",EDGE,"E3629"),sQuery(id+"F0.wireOp",EDGE,"E3630"),sQuery(id+"F0.wireOp",EDGE,"E3631"),sQuery(id+"F0.wireOp",EDGE,"E3632"),sQuery(id+"F0.wireOp",EDGE,"E3633"),sQuery(id+"F0.wireOp",EDGE,"E3634"),sQuery(id+"F0.wireOp",EDGE,"E3635"),sQuery(id+"F0.wireOp",EDGE,"E3636"),sQuery(id+"F0.wireOp",EDGE,"E3637"),sQuery(id+"F0.wireOp",EDGE,"E3638"),sQuery(id+"F0.wireOp",EDGE,"E3639"),sQuery(id+"F0.wireOp",EDGE,"E3640"),sQuery(id+"F0.wireOp",EDGE,"E3641"),sQuery(id+"F0.wireOp",EDGE,"E3642"),sQuery(id+"F0.wireOp",EDGE,"E3643"),sQuery(id+"F0.wireOp",EDGE,"E3644"),sQuery(id+"F0.wireOp",EDGE,"E3645"),sQuery(id+"F0.wireOp",EDGE,"E3646"),sQuery(id+"F0.wireOp",EDGE,"E3647"),sQuery(id+"F0.wireOp",EDGE,"E3648"),sQuery(id+"F0.wireOp",EDGE,"E3649"),sQuery(id+"F0.wireOp",EDGE,"E3650"),sQuery(id+"F0.wireOp",EDGE,"E3651"),sQuery(id+"F0.wireOp",EDGE,"E3652"),sQuery(id+"F0.wireOp",EDGE,"E3653"),sQuery(id+"F0.wireOp",EDGE,"E3654"),sQuery(id+"F0.wireOp",EDGE,"E3655"),sQuery(id+"F0.wireOp",EDGE,"E3656"),sQuery(id+"F0.wireOp",EDGE,"E3657"),sQuery(id+"F0.wireOp",EDGE,"E3658"),sQuery(id+"F0.wireOp",EDGE,"E3659"),sQuery(id+"F0.wireOp",EDGE,"E3660"),sQuery(id+"F0.wireOp",EDGE,"E3661"),sQuery(id+"F0.wireOp",EDGE,"E3662"),sQuery(id+"F0.wireOp",EDGE,"E3663"),sQuery(id+"F0.wireOp",EDGE,"E3664"),sQuery(id+"F0.wireOp",EDGE,"E3665"),sQuery(id+"F0.wireOp",EDGE,"E3666"),sQuery(id+"F0.wireOp",EDGE,"E3667"),sQuery(id+"F0.wireOp",EDGE,"E3668"),sQuery(id+"F0.wireOp",EDGE,"E3669"),sQuery(id+"F0.wireOp",EDGE,"E3670"),sQuery(id+"F0.wireOp",EDGE,"E3671"),sQuery(id+"F0.wireOp",EDGE,"E3672"),sQuery(id+"F0.wireOp",EDGE,"E3673"),sQuery(id+"F0.wireOp",EDGE,"E3674"),sQuery(id+"F0.wireOp",EDGE,"E3675"),sQuery(id+"F0.wireOp",EDGE,"E3676"),sQuery(id+"F0.wireOp",EDGE,"E3677"),sQuery(id+"F0.wireOp",EDGE,"E3678"),sQuery(id+"F0.wireOp",EDGE,"E3679"),sQuery(id+"F0.wireOp",EDGE,"E3680"),sQuery(id+"F0.wireOp",EDGE,"E3681"),sQuery(id+"F0.wireOp",EDGE,"E3682"),sQuery(id+"F0.wireOp",EDGE,"E3683"),sQuery(id+"F0.wireOp",EDGE,"E3684"),sQuery(id+"F0.wireOp",EDGE,"E3685"),sQuery(id+"F0.wireOp",EDGE,"E3686"),sQuery(id+"F0.wireOp",EDGE,"E3687"),sQuery(id+"F0.wireOp",EDGE,"E3688"),sQuery(id+"F0.wireOp",EDGE,"E3689"),sQuery(id+"F0.wireOp",EDGE,"E3690"),sQuery(id+"F0.wireOp",EDGE,"E3691"),sQuery(id+"F0.wireOp",EDGE,"E3692"),sQuery(id+"F0.wireOp",EDGE,"E3693"),sQuery(id+"F0.wireOp",EDGE,"E3694"),sQuery(id+"F0.wireOp",EDGE,"E3695"),sQuery(id+"F0.wireOp",EDGE,"E3696"),sQuery(id+"F0.wireOp",EDGE,"E3697"),sQuery(id+"F0.wireOp",EDGE,"E3698"),sQuery(id+"F0.wireOp",EDGE,"E3699"),sQuery(id+"F0.wireOp",EDGE,"E3700"),sQuery(id+"F0.wireOp",EDGE,"E3701"),sQuery(id+"F0.wireOp",EDGE,"E3702"),sQuery(id+"F0.wireOp",EDGE,"E3703"),sQuery(id+"F0.wireOp",EDGE,"E3704"),sQuery(id+"F0.wireOp",EDGE,"E3705"),sQuery(id+"F0.wireOp",EDGE,"E3706"),sQuery(id+"F0.wireOp",EDGE,"E3707"),sQuery(id+"F0.wireOp",EDGE,"E3708"),sQuery(id+"F0.wireOp",EDGE,"E3709"),sQuery(id+"F0.wireOp",EDGE,"E3710"),sQuery(id+"F0.wireOp",EDGE,"E3711"),sQuery(id+"F0.wireOp",EDGE,"E3712"),sQuery(id+"F0.wireOp",EDGE,"E3713"),sQuery(id+"F0.wireOp",EDGE,"E3714"),sQuery(id+"F0.wireOp",EDGE,"E3715"),sQuery(id+"F0.wireOp",EDGE,"E3716"),sQuery(id+"F0.wireOp",EDGE,"E3717"),sQuery(id+"F0.wireOp",EDGE,"E3718"),sQuery(id+"F0.wireOp",EDGE,"E3719"),sQuery(id+"F0.wireOp",EDGE,"E3720"),sQuery(id+"F0.wireOp",EDGE,"E3721"),sQuery(id+"F0.wireOp",EDGE,"E3722"),sQuery(id+"F0.wireOp",EDGE,"E3723"),sQuery(id+"F0.wireOp",EDGE,"E3724"),sQuery(id+"F0.wireOp",EDGE,"E3725"),sQuery(id+"F0.wireOp",EDGE,"E3726"),sQuery(id+"F0.wireOp",EDGE,"E3727"),sQuery(id+"F0.wireOp",EDGE,"E3728"),sQuery(id+"F0.wireOp",EDGE,"E3729"),sQuery(id+"F0.wireOp",EDGE,"E3730"),sQuery(id+"F0.wireOp",EDGE,"E3731"),sQuery(id+"F0.wireOp",EDGE,"E3732"),sQuery(id+"F0.wireOp",EDGE,"E3733"),sQuery(id+"F0.wireOp",EDGE,"E3734"),sQuery(id+"F0.wireOp",EDGE,"E3735"),sQuery(id+"F0.wireOp",EDGE,"E3736"),sQuery(id+"F0.wireOp",EDGE,"E3737"),sQuery(id+"F0.wireOp",EDGE,"E3738"),sQuery(id+"F0.wireOp",EDGE,"E3739"),sQuery(id+"F0.wireOp",EDGE,"E3740"),sQuery(id+"F0.wireOp",EDGE,"E3741"),sQuery(id+"F0.wireOp",EDGE,"E3742"),sQuery(id+"F0.wireOp",EDGE,"E3743"),sQuery(id+"F0.wireOp",EDGE,"E3744"),sQuery(id+"F0.wireOp",EDGE,"E3745"),sQuery(id+"F0.wireOp",EDGE,"E3746"),sQuery(id+"F0.wireOp",EDGE,"E3747"),sQuery(id+"F0.wireOp",EDGE,"E3748"),sQuery(id+"F0.wireOp",EDGE,"E3749"),sQuery(id+"F0.wireOp",EDGE,"E3750"),sQuery(id+"F0.wireOp",EDGE,"E3751"),sQuery(id+"F0.wireOp",EDGE,"E3752"),sQuery(id+"F0.wireOp",EDGE,"E3753"),sQuery(id+"F0.wireOp",EDGE,"E3754"),sQuery(id+"F0.wireOp",EDGE,"E3755"),sQuery(id+"F0.wireOp",EDGE,"E3756"),sQuery(id+"F0.wireOp",EDGE,"E3757"),sQuery(id+"F0.wireOp",EDGE,"E3758"),sQuery(id+"F0.wireOp",EDGE,"E3759"),sQuery(id+"F0.wireOp",EDGE,"E3760"),sQuery(id+"F0.wireOp",EDGE,"E3761"),sQuery(id+"F0.wireOp",EDGE,"E3762"),sQuery(id+"F0.wireOp",EDGE,"E3763"),sQuery(id+"F0.wireOp",EDGE,"E3764"),sQuery(id+"F0.wireOp",EDGE,"E3765"),sQuery(id+"F0.wireOp",EDGE,"E3766"),sQuery(id+"F0.wireOp",EDGE,"E3767"),sQuery(id+"F0.wireOp",EDGE,"E3768"),sQuery(id+"F0.wireOp",EDGE,"E3769"),sQuery(id+"F0.wireOp",EDGE,"E3770"),sQuery(id+"F0.wireOp",EDGE,"E3771"),sQuery(id+"F0.wireOp",EDGE,"E3772"),sQuery(id+"F0.wireOp",EDGE,"E3773"),sQuery(id+"F0.wireOp",EDGE,"E3774"),sQuery(id+"F0.wireOp",EDGE,"E3775"),sQuery(id+"F0.wireOp",EDGE,"E3776"),sQuery(id+"F0.wireOp",EDGE,"E3777"),sQuery(id+"F0.wireOp",EDGE,"E3778"),sQuery(id+"F0.wireOp",EDGE,"E3779"),sQuery(id+"F0.wireOp",EDGE,"E3780"),sQuery(id+"F0.wireOp",EDGE,"E3781"),sQuery(id+"F0.wireOp",EDGE,"E3782"),sQuery(id+"F0.wireOp",EDGE,"E3783"),sQuery(id+"F0.wireOp",EDGE,"E3784"),sQuery(id+"F0.wireOp",EDGE,"E3785"),sQuery(id+"F0.wireOp",EDGE,"E3786"),sQuery(id+"F0.wireOp",EDGE,"E3787"),sQuery(id+"F0.wireOp",EDGE,"E3788"),sQuery(id+"F0.wireOp",EDGE,"E3789"),sQuery(id+"F0.wireOp",EDGE,"E3790"),sQuery(id+"F0.wireOp",EDGE,"E3791"),sQuery(id+"F0.wireOp",EDGE,"E3792"),sQuery(id+"F0.wireOp",EDGE,"E3793"),sQuery(id+"F0.wireOp",EDGE,"E3794"),sQuery(id+"F0.wireOp",EDGE,"E3795"),sQuery(id+"F0.wireOp",EDGE,"E3796"),sQuery(id+"F0.wireOp",EDGE,"E3797"),sQuery(id+"F0.wireOp",EDGE,"E3798"),sQuery(id+"F0.wireOp",EDGE,"E3799"),sQuery(id+"F0.wireOp",EDGE,"E3800"),sQuery(id+"F0.wireOp",EDGE,"E3801"),sQuery(id+"F0.wireOp",EDGE,"E3802"),sQuery(id+"F0.wireOp",EDGE,"E3803"),sQuery(id+"F0.wireOp",EDGE,"E3804"),sQuery(id+"F0.wireOp",EDGE,"E3805"),sQuery(id+"F0.wireOp",EDGE,"E3806"),sQuery(id+"F0.wireOp",EDGE,"E3807"),sQuery(id+"F0.wireOp",EDGE,"E3808"),sQuery(id+"F0.wireOp",EDGE,"E3809"),sQuery(id+"F0.wireOp",EDGE,"E3810"),sQuery(id+"F0.wireOp",EDGE,"E3811"),sQuery(id+"F0.wireOp",EDGE,"E3812"),sQuery(id+"F0.wireOp",EDGE,"E3813"),sQuery(id+"F0.wireOp",EDGE,"E3814"),sQuery(id+"F0.wireOp",EDGE,"E3815"),sQuery(id+"F0.wireOp",EDGE,"E3816"),sQuery(id+"F0.wireOp",EDGE,"E3817"),sQuery(id+"F0.wireOp",EDGE,"E3818"),sQuery(id+"F0.wireOp",EDGE,"E3819"),sQuery(id+"F0.wireOp",EDGE,"E3820"),sQuery(id+"F0.wireOp",EDGE,"E3821"),sQuery(id+"F0.wireOp",EDGE,"E3822"),sQuery(id+"F0.wireOp",EDGE,"E3823"),sQuery(id+"F0.wireOp",EDGE,"E3824"),sQuery(id+"F0.wireOp",EDGE,"E3825"),sQuery(id+"F0.wireOp",EDGE,"E3826"),sQuery(id+"F0.wireOp",EDGE,"E3827"),sQuery(id+"F0.wireOp",EDGE,"E3828"),sQuery(id+"F0.wireOp",EDGE,"E3829"),sQuery(id+"F0.wireOp",EDGE,"E3830"),sQuery(id+"F0.wireOp",EDGE,"E3831"),sQuery(id+"F0.wireOp",EDGE,"E3832"),sQuery(id+"F0.wireOp",EDGE,"E3833"),sQuery(id+"F0.wireOp",EDGE,"E3834"),sQuery(id+"F0.wireOp",EDGE,"E3835"),sQuery(id+"F0.wireOp",EDGE,"E3836"),sQuery(id+"F0.wireOp",EDGE,"E3837"),sQuery(id+"F0.wireOp",EDGE,"E3838"),sQuery(id+"F0.wireOp",EDGE,"E3839"),sQuery(id+"F0.wireOp",EDGE,"E3840"),sQuery(id+"F0.wireOp",EDGE,"E3841"),sQuery(id+"F0.wireOp",EDGE,"E3842"),sQuery(id+"F0.wireOp",EDGE,"E3843"),sQuery(id+"F0.wireOp",EDGE,"E3844"),sQuery(id+"F0.wireOp",EDGE,"E3845"),sQuery(id+"F0.wireOp",EDGE,"E3846"),sQuery(id+"F0.wireOp",EDGE,"E3847"),sQuery(id+"F0.wireOp",EDGE,"E3848"),sQuery(id+"F0.wireOp",EDGE,"E3849"),sQuery(id+"F0.wireOp",EDGE,"E3850"),sQuery(id+"F0.wireOp",EDGE,"E3851"),sQuery(id+"F0.wireOp",EDGE,"E3852"),sQuery(id+"F0.wireOp",EDGE,"E3853"),sQuery(id+"F0.wireOp",EDGE,"E3854"),sQuery(id+"F0.wireOp",EDGE,"E3855"),sQuery(id+"F0.wireOp",EDGE,"E3856"),sQuery(id+"F0.wireOp",EDGE,"E3857"),sQuery(id+"F0.wireOp",EDGE,"E3858"),sQuery(id+"F0.wireOp",EDGE,"E3859"),sQuery(id+"F0.wireOp",EDGE,"E3860"),sQuery(id+"F0.wireOp",EDGE,"E3861"),sQuery(id+"F0.wireOp",EDGE,"E3862"),sQuery(id+"F0.wireOp",EDGE,"E3863"),sQuery(id+"F0.wireOp",EDGE,"E3864"),sQuery(id+"F0.wireOp",EDGE,"E3865"),sQuery(id+"F0.wireOp",EDGE,"E3866"),sQuery(id+"F0.wireOp",EDGE,"E3867"),sQuery(id+"F0.wireOp",EDGE,"E3868"),sQuery(id+"F0.wireOp",EDGE,"E3869"),sQuery(id+"F0.wireOp",EDGE,"E3870"),sQuery(id+"F0.wireOp",EDGE,"E3871"),sQuery(id+"F0.wireOp",EDGE,"E3872"),sQuery(id+"F0.wireOp",EDGE,"E3873"),sQuery(id+"F0.wireOp",EDGE,"E3874"),sQuery(id+"F0.wireOp",EDGE,"E3875"),sQuery(id+"F0.wireOp",EDGE,"E3876"),sQuery(id+"F0.wireOp",EDGE,"E3877"),sQuery(id+"F0.wireOp",EDGE,"E3878"),sQuery(id+"F0.wireOp",EDGE,"E3879"),sQuery(id+"F0.wireOp",EDGE,"E3880"),sQuery(id+"F0.wireOp",EDGE,"E3881"),sQuery(id+"F0.wireOp",EDGE,"E3882"),sQuery(id+"F0.wireOp",EDGE,"E3883"),sQuery(id+"F0.wireOp",EDGE,"E3884"),sQuery(id+"F0.wireOp",EDGE,"E3885"),sQuery(id+"F0.wireOp",EDGE,"E3886"),sQuery(id+"F0.wireOp",EDGE,"E3887"),sQuery(id+"F0.wireOp",EDGE,"E3888"),sQuery(id+"F0.wireOp",EDGE,"E3889"),sQuery(id+"F0.wireOp",EDGE,"E3890"),sQuery(id+"F0.wireOp",EDGE,"E3891"),sQuery(id+"F0.wireOp",EDGE,"E3892"),sQuery(id+"F0.wireOp",EDGE,"E3893"),sQuery(id+"F0.wireOp",EDGE,"E3894"),sQuery(id+"F0.wireOp",EDGE,"E3895"),sQuery(id+"F0.wireOp",EDGE,"E3896"),sQuery(id+"F0.wireOp",EDGE,"E3897"),sQuery(id+"F0.wireOp",EDGE,"E3898"),sQuery(id+"F0.wireOp",EDGE,"E3899"),sQuery(id+"F0.wireOp",EDGE,"E3900"),sQuery(id+"F0.wireOp",EDGE,"E3901"),sQuery(id+"F0.wireOp",EDGE,"E3902"),sQuery(id+"F0.wireOp",EDGE,"E3903"),sQuery(id+"F0.wireOp",EDGE,"E3904"),sQuery(id+"F0.wireOp",EDGE,"E3905"),sQuery(id+"F0.wireOp",EDGE,"E3906"),sQuery(id+"F0.wireOp",EDGE,"E3907"),sQuery(id+"F0.wireOp",EDGE,"E3908"),sQuery(id+"F0.wireOp",EDGE,"E3909"),sQuery(id+"F0.wireOp",EDGE,"E3910"),sQuery(id+"F0.wireOp",EDGE,"E3911"),sQuery(id+"F0.wireOp",EDGE,"E3912"),sQuery(id+"F0.wireOp",EDGE,"E3913"),sQuery(id+"F0.wireOp",EDGE,"E3914"),sQuery(id+"F0.wireOp",EDGE,"E3915"),sQuery(id+"F0.wireOp",EDGE,"E3916"),sQuery(id+"F0.wireOp",EDGE,"E3917"),sQuery(id+"F0.wireOp",EDGE,"E3918"),sQuery(id+"F0.wireOp",EDGE,"E3919"),sQuery(id+"F0.wireOp",EDGE,"E3920"),sQuery(id+"F0.wireOp",EDGE,"E3921"),sQuery(id+"F0.wireOp",EDGE,"E3922"),sQuery(id+"F0.wireOp",EDGE,"E3923"),sQuery(id+"F0.wireOp",EDGE,"E3924"),sQuery(id+"F0.wireOp",EDGE,"E3925"),sQuery(id+"F0.wireOp",EDGE,"E3926"),sQuery(id+"F0.wireOp",EDGE,"E3927"),sQuery(id+"F0.wireOp",EDGE,"E3928"),sQuery(id+"F0.wireOp",EDGE,"E3929"),sQuery(id+"F0.wireOp",EDGE,"E3930"),sQuery(id+"F0.wireOp",EDGE,"E3931"),sQuery(id+"F0.wireOp",EDGE,"E3932"),sQuery(id+"F0.wireOp",EDGE,"E3933"),sQuery(id+"F0.wireOp",EDGE,"E3934"),sQuery(id+"F0.wireOp",EDGE,"E3935"),sQuery(id+"F0.wireOp",EDGE,"E3936"),sQuery(id+"F0.wireOp",EDGE,"E3937"),sQuery(id+"F0.wireOp",EDGE,"E3938"),sQuery(id+"F0.wireOp",EDGE,"E3939"),sQuery(id+"F0.wireOp",EDGE,"E3940"),sQuery(id+"F0.wireOp",EDGE,"E3941"),sQuery(id+"F0.wireOp",EDGE,"E3942"),sQuery(id+"F0.wireOp",EDGE,"E3943"),sQuery(id+"F0.wireOp",EDGE,"E3944"),sQuery(id+"F0.wireOp",EDGE,"E3945"),sQuery(id+"F0.wireOp",EDGE,"E3946"),sQuery(id+"F0.wireOp",EDGE,"E3947"),sQuery(id+"F0.wireOp",EDGE,"E3948"),sQuery(id+"F0.wireOp",EDGE,"E3949"),sQuery(id+"F0.wireOp",EDGE,"E3950"),sQuery(id+"F0.wireOp",EDGE,"E3951"),sQuery(id+"F0.wireOp",EDGE,"E3952"),sQuery(id+"F0.wireOp",EDGE,"E3953"),sQuery(id+"F0.wireOp",EDGE,"E3954"),sQuery(id+"F0.wireOp",EDGE,"E3955"),sQuery(id+"F0.wireOp",EDGE,"E3956"),sQuery(id+"F0.wireOp",EDGE,"E3957"),sQuery(id+"F0.wireOp",EDGE,"E3958"),sQuery(id+"F0.wireOp",EDGE,"E3959"),sQuery(id+"F0.wireOp",EDGE,"E3960"),sQuery(id+"F0.wireOp",EDGE,"E3961"),sQuery(id+"F0.wireOp",EDGE,"E3962"),sQuery(id+"F0.wireOp",EDGE,"E3963"),sQuery(id+"F0.wireOp",EDGE,"E3964"),sQuery(id+"F0.wireOp",EDGE,"E3965"),sQuery(id+"F0.wireOp",EDGE,"E3966"),sQuery(id+"F0.wireOp",EDGE,"E3967"),sQuery(id+"F0.wireOp",EDGE,"E3968"),sQuery(id+"F0.wireOp",EDGE,"E3969"),sQuery(id+"F0.wireOp",EDGE,"E3970"),sQuery(id+"F0.wireOp",EDGE,"E3971"),sQuery(id+"F0.wireOp",EDGE,"E3972"),sQuery(id+"F0.wireOp",EDGE,"E3973"),sQuery(id+"F0.wireOp",EDGE,"E3974"),sQuery(id+"F0.wireOp",EDGE,"E3975"),sQuery(id+"F0.wireOp",EDGE,"E3976"),sQuery(id+"F0.wireOp",EDGE,"E3977"),sQuery(id+"F0.wireOp",EDGE,"E3978"),sQuery(id+"F0.wireOp",EDGE,"E3979"),sQuery(id+"F0.wireOp",EDGE,"E3980"),sQuery(id+"F0.wireOp",EDGE,"E3981"),sQuery(id+"F0.wireOp",EDGE,"E3982"),sQuery(id+"F0.wireOp",EDGE,"E3983"),sQuery(id+"F0.wireOp",EDGE,"E3984"),sQuery(id+"F0.wireOp",EDGE,"E3985"),sQuery(id+"F0.wireOp",EDGE,"E3986"),sQuery(id+"F0.wireOp",EDGE,"E3987"),sQuery(id+"F0.wireOp",EDGE,"E3988"),sQuery(id+"F0.wireOp",EDGE,"E3989"),sQuery(id+"F0.wireOp",EDGE,"E3990"),sQuery(id+"F0.wireOp",EDGE,"E3991"),sQuery(id+"F0.wireOp",EDGE,"E3992"),sQuery(id+"F0.wireOp",EDGE,"E3993"),sQuery(id+"F0.wireOp",EDGE,"E3994"),sQuery(id+"F0.wireOp",EDGE,"E3995"),sQuery(id+"F0.wireOp",EDGE,"E3996"),sQuery(id+"F0.wireOp",EDGE,"E3997"),sQuery(id+"F0.wireOp",EDGE,"E3998"),sQuery(id+"F0.wireOp",EDGE,"E3999")])],"isStart":false});
            var sketch = newSketch(context, id + "F4", { "sketchPlane" : qUnion([Q0])});
            skCircle(sketch, "E4001", {"center": v(0, 0) * mm, "radius": 2.92 * mm});
            skSolve(sketch);
        }
        {
            var Q0;
            Q0=qSketchRegion(id+"F4",true);
            extrude(context, id + "F5", {"entities" : qUnion([Q0]), "operationType" : NewBodyOperationType.REMOVE, "oppositeDirection" : true, "depth" : 5 * mm});
        }
        {
            var Q0;
            Q0=qCreatedBy(makeId("Top.planeOp"),FACE);
            var sketch = newSketch(context, id + "F6", { "sketchPlane" : qUnion([Q0])});
            skArc(sketch, "E4002", {"start": v(-2.4, -3.14) * mm, "mid": v(0, -3.95) * mm, "end": v(2.4, -3.14) * mm});
            skPoint(sketch, "E4003", {"position": v(-14.4, 0) * mm});
            skPoint(sketch, "E4004", {"position": v(14.4, 0) * mm});
            skArc(sketch, "E4005", {"start": v(-14.55, 2.34) * mm, "mid": v(-16.75, 0) * mm, "end": v(-14.55, -2.34) * mm});
            skArc(sketch, "E4006", {"start": v(14.55, -2.34) * mm, "mid": v(16.75, 0) * mm, "end": v(14.55, 2.34) * mm});
            skArc(sketch, "E4007", {"start": v(0.43, -3.27) * mm, "mid": v(3.3, 0) * mm, "end": v(0.43, 3.27) * mm, "construction": true});
            skLineSegment(sketch, "E4008", {"start": v(0, 3.3) * mm, "end": v(-0.43, 3.27) * mm});
            skLineSegment(sketch, "E4009", {"start": v(0, -3.3) * mm, "end": v(-0.43, -3.27) * mm});
            skLineSegment(sketch, "E4010", {"start": v(0, 3.3) * mm, "end": v(0.43, 3.27) * mm});
            skLineSegment(sketch, "E4011", {"start": v(0, -3.3) * mm, "end": v(0.43, -3.27) * mm});
            skLineSegment(sketch, "E4012.trimOffspring", {"start": v(-2.4, 3.14) * mm, "end": v(-14.55, 2.34) * mm});
            skLineSegment(sketch, "E4013.trimOffspring", {"start": v(2.4, 3.14) * mm, "end": v(14.55, 2.34) * mm});
            skLineSegment(sketch, "E4014.trimOffspring", {"start": v(2.4, -3.14) * mm, "end": v(14.55, -2.34) * mm});
            skLineSegment(sketch, "E4015.trimOffspring", {"start": v(-2.4, -3.14) * mm, "end": v(-14.55, -2.34) * mm});
            skArc(sketch, "E4016.trimOffspring", {"start": v(-0.43, 3.27) * mm, "mid": v(-3.3, 0) * mm, "end": v(-0.43, -3.27) * mm, "construction": true});
            skArc(sketch, "E4017.trimOffspring", {"start": v(2.4, 3.14) * mm, "mid": v(0, 3.95) * mm, "end": v(-2.4, 3.14) * mm});
            skSolve(sketch);
        }
        {
            var Q0;
            Q0=qSketchRegion(id+"F6",true);
            extrude(context, id + "F7", {"entities" : qUnion([Q0]), "operationType" : NewBodyOperationType.REMOVE, "depth" : 2 * mm});
        }
        {
            var Q0;
            Q0=makeQuery(id+"F1.opExtrude","CAP_FACE",FACE,{"disambiguationData":[OSD([sQuery(id+"F0.wireOp",EDGE,"E0"),sQuery(id+"F0.wireOp",EDGE,"E1"),sQuery(id+"F0.wireOp",EDGE,"E2"),sQuery(id+"F0.wireOp",EDGE,"E3"),sQuery(id+"F0.wireOp",EDGE,"E4"),sQuery(id+"F0.wireOp",EDGE,"E5"),sQuery(id+"F0.wireOp",EDGE,"E6"),sQuery(id+"F0.wireOp",EDGE,"E7"),sQuery(id+"F0.wireOp",EDGE,"E8"),sQuery(id+"F0.wireOp",EDGE,"E9"),sQuery(id+"F0.wireOp",EDGE,"E10"),sQuery(id+"F0.wireOp",EDGE,"E11"),sQuery(id+"F0.wireOp",EDGE,"E12"),sQuery(id+"F0.wireOp",EDGE,"E13"),sQuery(id+"F0.wireOp",EDGE,"E14"),sQuery(id+"F0.wireOp",EDGE,"E15"),sQuery(id+"F0.wireOp",EDGE,"E16"),sQuery(id+"F0.wireOp",EDGE,"E17"),sQuery(id+"F0.wireOp",EDGE,"E18"),sQuery(id+"F0.wireOp",EDGE,"E19"),sQuery(id+"F0.wireOp",EDGE,"E20"),sQuery(id+"F0.wireOp",EDGE,"E21"),sQuery(id+"F0.wireOp",EDGE,"E22"),sQuery(id+"F0.wireOp",EDGE,"E23"),sQuery(id+"F0.wireOp",EDGE,"E24"),sQuery(id+"F0.wireOp",EDGE,"E25"),sQuery(id+"F0.wireOp",EDGE,"E26"),sQuery(id+"F0.wireOp",EDGE,"E27"),sQuery(id+"F0.wireOp",EDGE,"E28"),sQuery(id+"F0.wireOp",EDGE,"E29"),sQuery(id+"F0.wireOp",EDGE,"E30"),sQuery(id+"F0.wireOp",EDGE,"E31"),sQuery(id+"F0.wireOp",EDGE,"E32"),sQuery(id+"F0.wireOp",EDGE,"E33"),sQuery(id+"F0.wireOp",EDGE,"E34"),sQuery(id+"F0.wireOp",EDGE,"E35"),sQuery(id+"F0.wireOp",EDGE,"E36"),sQuery(id+"F0.wireOp",EDGE,"E37"),sQuery(id+"F0.wireOp",EDGE,"E38"),sQuery(id+"F0.wireOp",EDGE,"E39"),sQuery(id+"F0.wireOp",EDGE,"E40"),sQuery(id+"F0.wireOp",EDGE,"E41"),sQuery(id+"F0.wireOp",EDGE,"E42"),sQuery(id+"F0.wireOp",EDGE,"E43"),sQuery(id+"F0.wireOp",EDGE,"E44"),sQuery(id+"F0.wireOp",EDGE,"E45"),sQuery(id+"F0.wireOp",EDGE,"E46"),sQuery(id+"F0.wireOp",EDGE,"E47"),sQuery(id+"F0.wireOp",EDGE,"E48"),sQuery(id+"F0.wireOp",EDGE,"E49"),sQuery(id+"F0.wireOp",EDGE,"E50"),sQuery(id+"F0.wireOp",EDGE,"E51"),sQuery(id+"F0.wireOp",EDGE,"E52"),sQuery(id+"F0.wireOp",EDGE,"E53"),sQuery(id+"F0.wireOp",EDGE,"E54"),sQuery(id+"F0.wireOp",EDGE,"E55"),sQuery(id+"F0.wireOp",EDGE,"E56"),sQuery(id+"F0.wireOp",EDGE,"E57"),sQuery(id+"F0.wireOp",EDGE,"E58"),sQuery(id+"F0.wireOp",EDGE,"E59"),sQuery(id+"F0.wireOp",EDGE,"E60"),sQuery(id+"F0.wireOp",EDGE,"E61"),sQuery(id+"F0.wireOp",EDGE,"E62"),sQuery(id+"F0.wireOp",EDGE,"E63"),sQuery(id+"F0.wireOp",EDGE,"E64"),sQuery(id+"F0.wireOp",EDGE,"E65"),sQuery(id+"F0.wireOp",EDGE,"E66"),sQuery(id+"F0.wireOp",EDGE,"E67"),sQuery(id+"F0.wireOp",EDGE,"E68"),sQuery(id+"F0.wireOp",EDGE,"E69"),sQuery(id+"F0.wireOp",EDGE,"E70"),sQuery(id+"F0.wireOp",EDGE,"E71"),sQuery(id+"F0.wireOp",EDGE,"E72"),sQuery(id+"F0.wireOp",EDGE,"E73"),sQuery(id+"F0.wireOp",EDGE,"E74"),sQuery(id+"F0.wireOp",EDGE,"E75"),sQuery(id+"F0.wireOp",EDGE,"E76"),sQuery(id+"F0.wireOp",EDGE,"E77"),sQuery(id+"F0.wireOp",EDGE,"E78"),sQuery(id+"F0.wireOp",EDGE,"E79"),sQuery(id+"F0.wireOp",EDGE,"E80"),sQuery(id+"F0.wireOp",EDGE,"E81"),sQuery(id+"F0.wireOp",EDGE,"E82"),sQuery(id+"F0.wireOp",EDGE,"E83"),sQuery(id+"F0.wireOp",EDGE,"E84"),sQuery(id+"F0.wireOp",EDGE,"E85"),sQuery(id+"F0.wireOp",EDGE,"E86"),sQuery(id+"F0.wireOp",EDGE,"E87"),sQuery(id+"F0.wireOp",EDGE,"E88"),sQuery(id+"F0.wireOp",EDGE,"E89"),sQuery(id+"F0.wireOp",EDGE,"E90"),sQuery(id+"F0.wireOp",EDGE,"E91"),sQuery(id+"F0.wireOp",EDGE,"E92"),sQuery(id+"F0.wireOp",EDGE,"E93"),sQuery(id+"F0.wireOp",EDGE,"E94"),sQuery(id+"F0.wireOp",EDGE,"E95"),sQuery(id+"F0.wireOp",EDGE,"E96"),sQuery(id+"F0.wireOp",EDGE,"E97"),sQuery(id+"F0.wireOp",EDGE,"E98"),sQuery(id+"F0.wireOp",EDGE,"E99"),sQuery(id+"F0.wireOp",EDGE,"E100"),sQuery(id+"F0.wireOp",EDGE,"E101"),sQuery(id+"F0.wireOp",EDGE,"E102"),sQuery(id+"F0.wireOp",EDGE,"E103"),sQuery(id+"F0.wireOp",EDGE,"E104"),sQuery(id+"F0.wireOp",EDGE,"E105"),sQuery(id+"F0.wireOp",EDGE,"E106"),sQuery(id+"F0.wireOp",EDGE,"E107"),sQuery(id+"F0.wireOp",EDGE,"E108"),sQuery(id+"F0.wireOp",EDGE,"E109"),sQuery(id+"F0.wireOp",EDGE,"E110"),sQuery(id+"F0.wireOp",EDGE,"E111"),sQuery(id+"F0.wireOp",EDGE,"E112"),sQuery(id+"F0.wireOp",EDGE,"E113"),sQuery(id+"F0.wireOp",EDGE,"E114"),sQuery(id+"F0.wireOp",EDGE,"E115"),sQuery(id+"F0.wireOp",EDGE,"E116"),sQuery(id+"F0.wireOp",EDGE,"E117"),sQuery(id+"F0.wireOp",EDGE,"E118"),sQuery(id+"F0.wireOp",EDGE,"E119"),sQuery(id+"F0.wireOp",EDGE,"E120"),sQuery(id+"F0.wireOp",EDGE,"E121"),sQuery(id+"F0.wireOp",EDGE,"E122"),sQuery(id+"F0.wireOp",EDGE,"E123"),sQuery(id+"F0.wireOp",EDGE,"E124"),sQuery(id+"F0.wireOp",EDGE,"E125"),sQuery(id+"F0.wireOp",EDGE,"E126"),sQuery(id+"F0.wireOp",EDGE,"E127"),sQuery(id+"F0.wireOp",EDGE,"E128"),sQuery(id+"F0.wireOp",EDGE,"E129"),sQuery(id+"F0.wireOp",EDGE,"E130"),sQuery(id+"F0.wireOp",EDGE,"E131"),sQuery(id+"F0.wireOp",EDGE,"E132"),sQuery(id+"F0.wireOp",EDGE,"E133"),sQuery(id+"F0.wireOp",EDGE,"E134"),sQuery(id+"F0.wireOp",EDGE,"E135"),sQuery(id+"F0.wireOp",EDGE,"E136"),sQuery(id+"F0.wireOp",EDGE,"E137"),sQuery(id+"F0.wireOp",EDGE,"E138"),sQuery(id+"F0.wireOp",EDGE,"E139"),sQuery(id+"F0.wireOp",EDGE,"E140"),sQuery(id+"F0.wireOp",EDGE,"E141"),sQuery(id+"F0.wireOp",EDGE,"E142"),sQuery(id+"F0.wireOp",EDGE,"E143"),sQuery(id+"F0.wireOp",EDGE,"E144"),sQuery(id+"F0.wireOp",EDGE,"E145"),sQuery(id+"F0.wireOp",EDGE,"E146"),sQuery(id+"F0.wireOp",EDGE,"E147"),sQuery(id+"F0.wireOp",EDGE,"E148"),sQuery(id+"F0.wireOp",EDGE,"E149"),sQuery(id+"F0.wireOp",EDGE,"E150"),sQuery(id+"F0.wireOp",EDGE,"E151"),sQuery(id+"F0.wireOp",EDGE,"E152"),sQuery(id+"F0.wireOp",EDGE,"E153"),sQuery(id+"F0.wireOp",EDGE,"E154"),sQuery(id+"F0.wireOp",EDGE,"E155"),sQuery(id+"F0.wireOp",EDGE,"E156"),sQuery(id+"F0.wireOp",EDGE,"E157"),sQuery(id+"F0.wireOp",EDGE,"E158"),sQuery(id+"F0.wireOp",EDGE,"E159"),sQuery(id+"F0.wireOp",EDGE,"E160"),sQuery(id+"F0.wireOp",EDGE,"E161"),sQuery(id+"F0.wireOp",EDGE,"E162"),sQuery(id+"F0.wireOp",EDGE,"E163"),sQuery(id+"F0.wireOp",EDGE,"E164"),sQuery(id+"F0.wireOp",EDGE,"E165"),sQuery(id+"F0.wireOp",EDGE,"E166"),sQuery(id+"F0.wireOp",EDGE,"E167"),sQuery(id+"F0.wireOp",EDGE,"E168"),sQuery(id+"F0.wireOp",EDGE,"E169"),sQuery(id+"F0.wireOp",EDGE,"E170"),sQuery(id+"F0.wireOp",EDGE,"E171"),sQuery(id+"F0.wireOp",EDGE,"E172"),sQuery(id+"F0.wireOp",EDGE,"E173"),sQuery(id+"F0.wireOp",EDGE,"E174"),sQuery(id+"F0.wireOp",EDGE,"E175"),sQuery(id+"F0.wireOp",EDGE,"E176"),sQuery(id+"F0.wireOp",EDGE,"E177"),sQuery(id+"F0.wireOp",EDGE,"E178"),sQuery(id+"F0.wireOp",EDGE,"E179"),sQuery(id+"F0.wireOp",EDGE,"E180"),sQuery(id+"F0.wireOp",EDGE,"E181"),sQuery(id+"F0.wireOp",EDGE,"E182"),sQuery(id+"F0.wireOp",EDGE,"E183"),sQuery(id+"F0.wireOp",EDGE,"E184"),sQuery(id+"F0.wireOp",EDGE,"E185"),sQuery(id+"F0.wireOp",EDGE,"E186"),sQuery(id+"F0.wireOp",EDGE,"E187"),sQuery(id+"F0.wireOp",EDGE,"E188"),sQuery(id+"F0.wireOp",EDGE,"E189"),sQuery(id+"F0.wireOp",EDGE,"E190"),sQuery(id+"F0.wireOp",EDGE,"E191"),sQuery(id+"F0.wireOp",EDGE,"E192"),sQuery(id+"F0.wireOp",EDGE,"E193"),sQuery(id+"F0.wireOp",EDGE,"E194"),sQuery(id+"F0.wireOp",EDGE,"E195"),sQuery(id+"F0.wireOp",EDGE,"E196"),sQuery(id+"F0.wireOp",EDGE,"E197"),sQuery(id+"F0.wireOp",EDGE,"E198"),sQuery(id+"F0.wireOp",EDGE,"E199"),sQuery(id+"F0.wireOp",EDGE,"E200"),sQuery(id+"F0.wireOp",EDGE,"E201"),sQuery(id+"F0.wireOp",EDGE,"E202"),sQuery(id+"F0.wireOp",EDGE,"E203"),sQuery(id+"F0.wireOp",EDGE,"E204"),sQuery(id+"F0.wireOp",EDGE,"E205"),sQuery(id+"F0.wireOp",EDGE,"E206"),sQuery(id+"F0.wireOp",EDGE,"E207"),sQuery(id+"F0.wireOp",EDGE,"E208"),sQuery(id+"F0.wireOp",EDGE,"E209"),sQuery(id+"F0.wireOp",EDGE,"E210"),sQuery(id+"F0.wireOp",EDGE,"E211"),sQuery(id+"F0.wireOp",EDGE,"E212"),sQuery(id+"F0.wireOp",EDGE,"E213"),sQuery(id+"F0.wireOp",EDGE,"E214"),sQuery(id+"F0.wireOp",EDGE,"E215"),sQuery(id+"F0.wireOp",EDGE,"E216"),sQuery(id+"F0.wireOp",EDGE,"E217"),sQuery(id+"F0.wireOp",EDGE,"E218"),sQuery(id+"F0.wireOp",EDGE,"E219"),sQuery(id+"F0.wireOp",EDGE,"E220"),sQuery(id+"F0.wireOp",EDGE,"E221"),sQuery(id+"F0.wireOp",EDGE,"E222"),sQuery(id+"F0.wireOp",EDGE,"E223"),sQuery(id+"F0.wireOp",EDGE,"E224"),sQuery(id+"F0.wireOp",EDGE,"E225"),sQuery(id+"F0.wireOp",EDGE,"E226"),sQuery(id+"F0.wireOp",EDGE,"E227"),sQuery(id+"F0.wireOp",EDGE,"E228"),sQuery(id+"F0.wireOp",EDGE,"E229"),sQuery(id+"F0.wireOp",EDGE,"E230"),sQuery(id+"F0.wireOp",EDGE,"E231"),sQuery(id+"F0.wireOp",EDGE,"E232"),sQuery(id+"F0.wireOp",EDGE,"E233"),sQuery(id+"F0.wireOp",EDGE,"E234"),sQuery(id+"F0.wireOp",EDGE,"E235"),sQuery(id+"F0.wireOp",EDGE,"E236"),sQuery(id+"F0.wireOp",EDGE,"E237"),sQuery(id+"F0.wireOp",EDGE,"E238"),sQuery(id+"F0.wireOp",EDGE,"E239"),sQuery(id+"F0.wireOp",EDGE,"E240"),sQuery(id+"F0.wireOp",EDGE,"E241"),sQuery(id+"F0.wireOp",EDGE,"E242"),sQuery(id+"F0.wireOp",EDGE,"E243"),sQuery(id+"F0.wireOp",EDGE,"E244"),sQuery(id+"F0.wireOp",EDGE,"E245"),sQuery(id+"F0.wireOp",EDGE,"E246"),sQuery(id+"F0.wireOp",EDGE,"E247"),sQuery(id+"F0.wireOp",EDGE,"E248"),sQuery(id+"F0.wireOp",EDGE,"E249"),sQuery(id+"F0.wireOp",EDGE,"E250"),sQuery(id+"F0.wireOp",EDGE,"E251"),sQuery(id+"F0.wireOp",EDGE,"E252"),sQuery(id+"F0.wireOp",EDGE,"E253"),sQuery(id+"F0.wireOp",EDGE,"E254"),sQuery(id+"F0.wireOp",EDGE,"E255"),sQuery(id+"F0.wireOp",EDGE,"E256"),sQuery(id+"F0.wireOp",EDGE,"E257"),sQuery(id+"F0.wireOp",EDGE,"E258"),sQuery(id+"F0.wireOp",EDGE,"E259"),sQuery(id+"F0.wireOp",EDGE,"E260"),sQuery(id+"F0.wireOp",EDGE,"E261"),sQuery(id+"F0.wireOp",EDGE,"E262"),sQuery(id+"F0.wireOp",EDGE,"E263"),sQuery(id+"F0.wireOp",EDGE,"E264"),sQuery(id+"F0.wireOp",EDGE,"E265"),sQuery(id+"F0.wireOp",EDGE,"E266"),sQuery(id+"F0.wireOp",EDGE,"E267"),sQuery(id+"F0.wireOp",EDGE,"E268"),sQuery(id+"F0.wireOp",EDGE,"E269"),sQuery(id+"F0.wireOp",EDGE,"E270"),sQuery(id+"F0.wireOp",EDGE,"E271"),sQuery(id+"F0.wireOp",EDGE,"E272"),sQuery(id+"F0.wireOp",EDGE,"E273"),sQuery(id+"F0.wireOp",EDGE,"E274"),sQuery(id+"F0.wireOp",EDGE,"E275"),sQuery(id+"F0.wireOp",EDGE,"E276"),sQuery(id+"F0.wireOp",EDGE,"E277"),sQuery(id+"F0.wireOp",EDGE,"E278"),sQuery(id+"F0.wireOp",EDGE,"E279"),sQuery(id+"F0.wireOp",EDGE,"E280"),sQuery(id+"F0.wireOp",EDGE,"E281"),sQuery(id+"F0.wireOp",EDGE,"E282"),sQuery(id+"F0.wireOp",EDGE,"E283"),sQuery(id+"F0.wireOp",EDGE,"E284"),sQuery(id+"F0.wireOp",EDGE,"E285"),sQuery(id+"F0.wireOp",EDGE,"E286"),sQuery(id+"F0.wireOp",EDGE,"E287"),sQuery(id+"F0.wireOp",EDGE,"E288"),sQuery(id+"F0.wireOp",EDGE,"E289"),sQuery(id+"F0.wireOp",EDGE,"E290"),sQuery(id+"F0.wireOp",EDGE,"E291"),sQuery(id+"F0.wireOp",EDGE,"E292"),sQuery(id+"F0.wireOp",EDGE,"E293"),sQuery(id+"F0.wireOp",EDGE,"E294"),sQuery(id+"F0.wireOp",EDGE,"E295"),sQuery(id+"F0.wireOp",EDGE,"E296"),sQuery(id+"F0.wireOp",EDGE,"E297"),sQuery(id+"F0.wireOp",EDGE,"E298"),sQuery(id+"F0.wireOp",EDGE,"E299"),sQuery(id+"F0.wireOp",EDGE,"E300"),sQuery(id+"F0.wireOp",EDGE,"E301"),sQuery(id+"F0.wireOp",EDGE,"E302"),sQuery(id+"F0.wireOp",EDGE,"E303"),sQuery(id+"F0.wireOp",EDGE,"E304"),sQuery(id+"F0.wireOp",EDGE,"E305"),sQuery(id+"F0.wireOp",EDGE,"E306"),sQuery(id+"F0.wireOp",EDGE,"E307"),sQuery(id+"F0.wireOp",EDGE,"E308"),sQuery(id+"F0.wireOp",EDGE,"E309"),sQuery(id+"F0.wireOp",EDGE,"E310"),sQuery(id+"F0.wireOp",EDGE,"E311"),sQuery(id+"F0.wireOp",EDGE,"E312"),sQuery(id+"F0.wireOp",EDGE,"E313"),sQuery(id+"F0.wireOp",EDGE,"E314"),sQuery(id+"F0.wireOp",EDGE,"E315"),sQuery(id+"F0.wireOp",EDGE,"E316"),sQuery(id+"F0.wireOp",EDGE,"E317"),sQuery(id+"F0.wireOp",EDGE,"E318"),sQuery(id+"F0.wireOp",EDGE,"E319"),sQuery(id+"F0.wireOp",EDGE,"E320"),sQuery(id+"F0.wireOp",EDGE,"E321"),sQuery(id+"F0.wireOp",EDGE,"E322"),sQuery(id+"F0.wireOp",EDGE,"E323"),sQuery(id+"F0.wireOp",EDGE,"E324"),sQuery(id+"F0.wireOp",EDGE,"E325"),sQuery(id+"F0.wireOp",EDGE,"E326"),sQuery(id+"F0.wireOp",EDGE,"E327"),sQuery(id+"F0.wireOp",EDGE,"E328"),sQuery(id+"F0.wireOp",EDGE,"E329"),sQuery(id+"F0.wireOp",EDGE,"E330"),sQuery(id+"F0.wireOp",EDGE,"E331"),sQuery(id+"F0.wireOp",EDGE,"E332"),sQuery(id+"F0.wireOp",EDGE,"E333"),sQuery(id+"F0.wireOp",EDGE,"E334"),sQuery(id+"F0.wireOp",EDGE,"E335"),sQuery(id+"F0.wireOp",EDGE,"E336"),sQuery(id+"F0.wireOp",EDGE,"E337"),sQuery(id+"F0.wireOp",EDGE,"E338"),sQuery(id+"F0.wireOp",EDGE,"E339"),sQuery(id+"F0.wireOp",EDGE,"E340"),sQuery(id+"F0.wireOp",EDGE,"E341"),sQuery(id+"F0.wireOp",EDGE,"E342"),sQuery(id+"F0.wireOp",EDGE,"E343"),sQuery(id+"F0.wireOp",EDGE,"E344"),sQuery(id+"F0.wireOp",EDGE,"E345"),sQuery(id+"F0.wireOp",EDGE,"E346"),sQuery(id+"F0.wireOp",EDGE,"E347"),sQuery(id+"F0.wireOp",EDGE,"E348"),sQuery(id+"F0.wireOp",EDGE,"E349"),sQuery(id+"F0.wireOp",EDGE,"E350"),sQuery(id+"F0.wireOp",EDGE,"E351"),sQuery(id+"F0.wireOp",EDGE,"E352"),sQuery(id+"F0.wireOp",EDGE,"E353"),sQuery(id+"F0.wireOp",EDGE,"E354"),sQuery(id+"F0.wireOp",EDGE,"E355"),sQuery(id+"F0.wireOp",EDGE,"E356"),sQuery(id+"F0.wireOp",EDGE,"E357"),sQuery(id+"F0.wireOp",EDGE,"E358"),sQuery(id+"F0.wireOp",EDGE,"E359"),sQuery(id+"F0.wireOp",EDGE,"E360"),sQuery(id+"F0.wireOp",EDGE,"E361"),sQuery(id+"F0.wireOp",EDGE,"E362"),sQuery(id+"F0.wireOp",EDGE,"E363"),sQuery(id+"F0.wireOp",EDGE,"E364"),sQuery(id+"F0.wireOp",EDGE,"E365"),sQuery(id+"F0.wireOp",EDGE,"E366"),sQuery(id+"F0.wireOp",EDGE,"E367"),sQuery(id+"F0.wireOp",EDGE,"E368"),sQuery(id+"F0.wireOp",EDGE,"E369"),sQuery(id+"F0.wireOp",EDGE,"E370"),sQuery(id+"F0.wireOp",EDGE,"E371"),sQuery(id+"F0.wireOp",EDGE,"E372"),sQuery(id+"F0.wireOp",EDGE,"E373"),sQuery(id+"F0.wireOp",EDGE,"E374"),sQuery(id+"F0.wireOp",EDGE,"E375"),sQuery(id+"F0.wireOp",EDGE,"E376"),sQuery(id+"F0.wireOp",EDGE,"E377"),sQuery(id+"F0.wireOp",EDGE,"E378"),sQuery(id+"F0.wireOp",EDGE,"E379"),sQuery(id+"F0.wireOp",EDGE,"E380"),sQuery(id+"F0.wireOp",EDGE,"E381"),sQuery(id+"F0.wireOp",EDGE,"E382"),sQuery(id+"F0.wireOp",EDGE,"E383"),sQuery(id+"F0.wireOp",EDGE,"E384"),sQuery(id+"F0.wireOp",EDGE,"E385"),sQuery(id+"F0.wireOp",EDGE,"E386"),sQuery(id+"F0.wireOp",EDGE,"E387"),sQuery(id+"F0.wireOp",EDGE,"E388"),sQuery(id+"F0.wireOp",EDGE,"E389"),sQuery(id+"F0.wireOp",EDGE,"E390"),sQuery(id+"F0.wireOp",EDGE,"E391"),sQuery(id+"F0.wireOp",EDGE,"E392"),sQuery(id+"F0.wireOp",EDGE,"E393"),sQuery(id+"F0.wireOp",EDGE,"E394"),sQuery(id+"F0.wireOp",EDGE,"E395"),sQuery(id+"F0.wireOp",EDGE,"E396"),sQuery(id+"F0.wireOp",EDGE,"E397"),sQuery(id+"F0.wireOp",EDGE,"E398"),sQuery(id+"F0.wireOp",EDGE,"E399"),sQuery(id+"F0.wireOp",EDGE,"E400"),sQuery(id+"F0.wireOp",EDGE,"E401"),sQuery(id+"F0.wireOp",EDGE,"E402"),sQuery(id+"F0.wireOp",EDGE,"E403"),sQuery(id+"F0.wireOp",EDGE,"E404"),sQuery(id+"F0.wireOp",EDGE,"E405"),sQuery(id+"F0.wireOp",EDGE,"E406"),sQuery(id+"F0.wireOp",EDGE,"E407"),sQuery(id+"F0.wireOp",EDGE,"E408"),sQuery(id+"F0.wireOp",EDGE,"E409"),sQuery(id+"F0.wireOp",EDGE,"E410"),sQuery(id+"F0.wireOp",EDGE,"E411"),sQuery(id+"F0.wireOp",EDGE,"E412"),sQuery(id+"F0.wireOp",EDGE,"E413"),sQuery(id+"F0.wireOp",EDGE,"E414"),sQuery(id+"F0.wireOp",EDGE,"E415"),sQuery(id+"F0.wireOp",EDGE,"E416"),sQuery(id+"F0.wireOp",EDGE,"E417"),sQuery(id+"F0.wireOp",EDGE,"E418"),sQuery(id+"F0.wireOp",EDGE,"E419"),sQuery(id+"F0.wireOp",EDGE,"E420"),sQuery(id+"F0.wireOp",EDGE,"E421"),sQuery(id+"F0.wireOp",EDGE,"E422"),sQuery(id+"F0.wireOp",EDGE,"E423"),sQuery(id+"F0.wireOp",EDGE,"E424"),sQuery(id+"F0.wireOp",EDGE,"E425"),sQuery(id+"F0.wireOp",EDGE,"E426"),sQuery(id+"F0.wireOp",EDGE,"E427"),sQuery(id+"F0.wireOp",EDGE,"E428"),sQuery(id+"F0.wireOp",EDGE,"E429"),sQuery(id+"F0.wireOp",EDGE,"E430"),sQuery(id+"F0.wireOp",EDGE,"E431"),sQuery(id+"F0.wireOp",EDGE,"E432"),sQuery(id+"F0.wireOp",EDGE,"E433"),sQuery(id+"F0.wireOp",EDGE,"E434"),sQuery(id+"F0.wireOp",EDGE,"E435"),sQuery(id+"F0.wireOp",EDGE,"E436"),sQuery(id+"F0.wireOp",EDGE,"E437"),sQuery(id+"F0.wireOp",EDGE,"E438"),sQuery(id+"F0.wireOp",EDGE,"E439"),sQuery(id+"F0.wireOp",EDGE,"E440"),sQuery(id+"F0.wireOp",EDGE,"E441"),sQuery(id+"F0.wireOp",EDGE,"E442"),sQuery(id+"F0.wireOp",EDGE,"E443"),sQuery(id+"F0.wireOp",EDGE,"E444"),sQuery(id+"F0.wireOp",EDGE,"E445"),sQuery(id+"F0.wireOp",EDGE,"E446"),sQuery(id+"F0.wireOp",EDGE,"E447"),sQuery(id+"F0.wireOp",EDGE,"E448"),sQuery(id+"F0.wireOp",EDGE,"E449"),sQuery(id+"F0.wireOp",EDGE,"E450"),sQuery(id+"F0.wireOp",EDGE,"E451"),sQuery(id+"F0.wireOp",EDGE,"E452"),sQuery(id+"F0.wireOp",EDGE,"E453"),sQuery(id+"F0.wireOp",EDGE,"E454"),sQuery(id+"F0.wireOp",EDGE,"E455"),sQuery(id+"F0.wireOp",EDGE,"E456"),sQuery(id+"F0.wireOp",EDGE,"E457"),sQuery(id+"F0.wireOp",EDGE,"E458"),sQuery(id+"F0.wireOp",EDGE,"E459"),sQuery(id+"F0.wireOp",EDGE,"E460"),sQuery(id+"F0.wireOp",EDGE,"E461"),sQuery(id+"F0.wireOp",EDGE,"E462"),sQuery(id+"F0.wireOp",EDGE,"E463"),sQuery(id+"F0.wireOp",EDGE,"E464"),sQuery(id+"F0.wireOp",EDGE,"E465"),sQuery(id+"F0.wireOp",EDGE,"E466"),sQuery(id+"F0.wireOp",EDGE,"E467"),sQuery(id+"F0.wireOp",EDGE,"E468"),sQuery(id+"F0.wireOp",EDGE,"E469"),sQuery(id+"F0.wireOp",EDGE,"E470"),sQuery(id+"F0.wireOp",EDGE,"E471"),sQuery(id+"F0.wireOp",EDGE,"E472"),sQuery(id+"F0.wireOp",EDGE,"E473"),sQuery(id+"F0.wireOp",EDGE,"E474"),sQuery(id+"F0.wireOp",EDGE,"E475"),sQuery(id+"F0.wireOp",EDGE,"E476"),sQuery(id+"F0.wireOp",EDGE,"E477"),sQuery(id+"F0.wireOp",EDGE,"E478"),sQuery(id+"F0.wireOp",EDGE,"E479"),sQuery(id+"F0.wireOp",EDGE,"E480"),sQuery(id+"F0.wireOp",EDGE,"E481"),sQuery(id+"F0.wireOp",EDGE,"E482"),sQuery(id+"F0.wireOp",EDGE,"E483"),sQuery(id+"F0.wireOp",EDGE,"E484"),sQuery(id+"F0.wireOp",EDGE,"E485"),sQuery(id+"F0.wireOp",EDGE,"E486"),sQuery(id+"F0.wireOp",EDGE,"E487"),sQuery(id+"F0.wireOp",EDGE,"E488"),sQuery(id+"F0.wireOp",EDGE,"E489"),sQuery(id+"F0.wireOp",EDGE,"E490"),sQuery(id+"F0.wireOp",EDGE,"E491"),sQuery(id+"F0.wireOp",EDGE,"E492"),sQuery(id+"F0.wireOp",EDGE,"E493"),sQuery(id+"F0.wireOp",EDGE,"E494"),sQuery(id+"F0.wireOp",EDGE,"E495"),sQuery(id+"F0.wireOp",EDGE,"E496"),sQuery(id+"F0.wireOp",EDGE,"E497"),sQuery(id+"F0.wireOp",EDGE,"E498"),sQuery(id+"F0.wireOp",EDGE,"E499"),sQuery(id+"F0.wireOp",EDGE,"E500"),sQuery(id+"F0.wireOp",EDGE,"E501"),sQuery(id+"F0.wireOp",EDGE,"E502"),sQuery(id+"F0.wireOp",EDGE,"E503"),sQuery(id+"F0.wireOp",EDGE,"E504"),sQuery(id+"F0.wireOp",EDGE,"E505"),sQuery(id+"F0.wireOp",EDGE,"E506"),sQuery(id+"F0.wireOp",EDGE,"E507"),sQuery(id+"F0.wireOp",EDGE,"E508"),sQuery(id+"F0.wireOp",EDGE,"E509"),sQuery(id+"F0.wireOp",EDGE,"E510"),sQuery(id+"F0.wireOp",EDGE,"E511"),sQuery(id+"F0.wireOp",EDGE,"E512"),sQuery(id+"F0.wireOp",EDGE,"E513"),sQuery(id+"F0.wireOp",EDGE,"E514"),sQuery(id+"F0.wireOp",EDGE,"E515"),sQuery(id+"F0.wireOp",EDGE,"E516"),sQuery(id+"F0.wireOp",EDGE,"E517"),sQuery(id+"F0.wireOp",EDGE,"E518"),sQuery(id+"F0.wireOp",EDGE,"E519"),sQuery(id+"F0.wireOp",EDGE,"E520"),sQuery(id+"F0.wireOp",EDGE,"E521"),sQuery(id+"F0.wireOp",EDGE,"E522"),sQuery(id+"F0.wireOp",EDGE,"E523"),sQuery(id+"F0.wireOp",EDGE,"E524"),sQuery(id+"F0.wireOp",EDGE,"E525"),sQuery(id+"F0.wireOp",EDGE,"E526"),sQuery(id+"F0.wireOp",EDGE,"E527"),sQuery(id+"F0.wireOp",EDGE,"E528"),sQuery(id+"F0.wireOp",EDGE,"E529"),sQuery(id+"F0.wireOp",EDGE,"E530"),sQuery(id+"F0.wireOp",EDGE,"E531"),sQuery(id+"F0.wireOp",EDGE,"E532"),sQuery(id+"F0.wireOp",EDGE,"E533"),sQuery(id+"F0.wireOp",EDGE,"E534"),sQuery(id+"F0.wireOp",EDGE,"E535"),sQuery(id+"F0.wireOp",EDGE,"E536"),sQuery(id+"F0.wireOp",EDGE,"E537"),sQuery(id+"F0.wireOp",EDGE,"E538"),sQuery(id+"F0.wireOp",EDGE,"E539"),sQuery(id+"F0.wireOp",EDGE,"E540"),sQuery(id+"F0.wireOp",EDGE,"E541"),sQuery(id+"F0.wireOp",EDGE,"E542"),sQuery(id+"F0.wireOp",EDGE,"E543"),sQuery(id+"F0.wireOp",EDGE,"E544"),sQuery(id+"F0.wireOp",EDGE,"E545"),sQuery(id+"F0.wireOp",EDGE,"E546"),sQuery(id+"F0.wireOp",EDGE,"E547"),sQuery(id+"F0.wireOp",EDGE,"E548"),sQuery(id+"F0.wireOp",EDGE,"E549"),sQuery(id+"F0.wireOp",EDGE,"E550"),sQuery(id+"F0.wireOp",EDGE,"E551"),sQuery(id+"F0.wireOp",EDGE,"E552"),sQuery(id+"F0.wireOp",EDGE,"E553"),sQuery(id+"F0.wireOp",EDGE,"E554"),sQuery(id+"F0.wireOp",EDGE,"E555"),sQuery(id+"F0.wireOp",EDGE,"E556"),sQuery(id+"F0.wireOp",EDGE,"E557"),sQuery(id+"F0.wireOp",EDGE,"E558"),sQuery(id+"F0.wireOp",EDGE,"E559"),sQuery(id+"F0.wireOp",EDGE,"E560"),sQuery(id+"F0.wireOp",EDGE,"E561"),sQuery(id+"F0.wireOp",EDGE,"E562"),sQuery(id+"F0.wireOp",EDGE,"E563"),sQuery(id+"F0.wireOp",EDGE,"E564"),sQuery(id+"F0.wireOp",EDGE,"E565"),sQuery(id+"F0.wireOp",EDGE,"E566"),sQuery(id+"F0.wireOp",EDGE,"E567"),sQuery(id+"F0.wireOp",EDGE,"E568"),sQuery(id+"F0.wireOp",EDGE,"E569"),sQuery(id+"F0.wireOp",EDGE,"E570"),sQuery(id+"F0.wireOp",EDGE,"E571"),sQuery(id+"F0.wireOp",EDGE,"E572"),sQuery(id+"F0.wireOp",EDGE,"E573"),sQuery(id+"F0.wireOp",EDGE,"E574"),sQuery(id+"F0.wireOp",EDGE,"E575"),sQuery(id+"F0.wireOp",EDGE,"E576"),sQuery(id+"F0.wireOp",EDGE,"E577"),sQuery(id+"F0.wireOp",EDGE,"E578"),sQuery(id+"F0.wireOp",EDGE,"E579"),sQuery(id+"F0.wireOp",EDGE,"E580"),sQuery(id+"F0.wireOp",EDGE,"E581"),sQuery(id+"F0.wireOp",EDGE,"E582"),sQuery(id+"F0.wireOp",EDGE,"E583"),sQuery(id+"F0.wireOp",EDGE,"E584"),sQuery(id+"F0.wireOp",EDGE,"E585"),sQuery(id+"F0.wireOp",EDGE,"E586"),sQuery(id+"F0.wireOp",EDGE,"E587"),sQuery(id+"F0.wireOp",EDGE,"E588"),sQuery(id+"F0.wireOp",EDGE,"E589"),sQuery(id+"F0.wireOp",EDGE,"E590"),sQuery(id+"F0.wireOp",EDGE,"E591"),sQuery(id+"F0.wireOp",EDGE,"E592"),sQuery(id+"F0.wireOp",EDGE,"E593"),sQuery(id+"F0.wireOp",EDGE,"E594"),sQuery(id+"F0.wireOp",EDGE,"E595"),sQuery(id+"F0.wireOp",EDGE,"E596"),sQuery(id+"F0.wireOp",EDGE,"E597"),sQuery(id+"F0.wireOp",EDGE,"E598"),sQuery(id+"F0.wireOp",EDGE,"E599"),sQuery(id+"F0.wireOp",EDGE,"E600"),sQuery(id+"F0.wireOp",EDGE,"E601"),sQuery(id+"F0.wireOp",EDGE,"E602"),sQuery(id+"F0.wireOp",EDGE,"E603"),sQuery(id+"F0.wireOp",EDGE,"E604"),sQuery(id+"F0.wireOp",EDGE,"E605"),sQuery(id+"F0.wireOp",EDGE,"E606"),sQuery(id+"F0.wireOp",EDGE,"E607"),sQuery(id+"F0.wireOp",EDGE,"E608"),sQuery(id+"F0.wireOp",EDGE,"E609"),sQuery(id+"F0.wireOp",EDGE,"E610"),sQuery(id+"F0.wireOp",EDGE,"E611"),sQuery(id+"F0.wireOp",EDGE,"E612"),sQuery(id+"F0.wireOp",EDGE,"E613"),sQuery(id+"F0.wireOp",EDGE,"E614"),sQuery(id+"F0.wireOp",EDGE,"E615"),sQuery(id+"F0.wireOp",EDGE,"E616"),sQuery(id+"F0.wireOp",EDGE,"E617"),sQuery(id+"F0.wireOp",EDGE,"E618"),sQuery(id+"F0.wireOp",EDGE,"E619"),sQuery(id+"F0.wireOp",EDGE,"E620"),sQuery(id+"F0.wireOp",EDGE,"E621"),sQuery(id+"F0.wireOp",EDGE,"E622"),sQuery(id+"F0.wireOp",EDGE,"E623"),sQuery(id+"F0.wireOp",EDGE,"E624"),sQuery(id+"F0.wireOp",EDGE,"E625"),sQuery(id+"F0.wireOp",EDGE,"E626"),sQuery(id+"F0.wireOp",EDGE,"E627"),sQuery(id+"F0.wireOp",EDGE,"E628"),sQuery(id+"F0.wireOp",EDGE,"E629"),sQuery(id+"F0.wireOp",EDGE,"E630"),sQuery(id+"F0.wireOp",EDGE,"E631"),sQuery(id+"F0.wireOp",EDGE,"E632"),sQuery(id+"F0.wireOp",EDGE,"E633"),sQuery(id+"F0.wireOp",EDGE,"E634"),sQuery(id+"F0.wireOp",EDGE,"E635"),sQuery(id+"F0.wireOp",EDGE,"E636"),sQuery(id+"F0.wireOp",EDGE,"E637"),sQuery(id+"F0.wireOp",EDGE,"E638"),sQuery(id+"F0.wireOp",EDGE,"E639"),sQuery(id+"F0.wireOp",EDGE,"E640"),sQuery(id+"F0.wireOp",EDGE,"E641"),sQuery(id+"F0.wireOp",EDGE,"E642"),sQuery(id+"F0.wireOp",EDGE,"E643"),sQuery(id+"F0.wireOp",EDGE,"E644"),sQuery(id+"F0.wireOp",EDGE,"E645"),sQuery(id+"F0.wireOp",EDGE,"E646"),sQuery(id+"F0.wireOp",EDGE,"E647"),sQuery(id+"F0.wireOp",EDGE,"E648"),sQuery(id+"F0.wireOp",EDGE,"E649"),sQuery(id+"F0.wireOp",EDGE,"E650"),sQuery(id+"F0.wireOp",EDGE,"E651"),sQuery(id+"F0.wireOp",EDGE,"E652"),sQuery(id+"F0.wireOp",EDGE,"E653"),sQuery(id+"F0.wireOp",EDGE,"E654"),sQuery(id+"F0.wireOp",EDGE,"E655"),sQuery(id+"F0.wireOp",EDGE,"E656"),sQuery(id+"F0.wireOp",EDGE,"E657"),sQuery(id+"F0.wireOp",EDGE,"E658"),sQuery(id+"F0.wireOp",EDGE,"E659"),sQuery(id+"F0.wireOp",EDGE,"E660"),sQuery(id+"F0.wireOp",EDGE,"E661"),sQuery(id+"F0.wireOp",EDGE,"E662"),sQuery(id+"F0.wireOp",EDGE,"E663"),sQuery(id+"F0.wireOp",EDGE,"E664"),sQuery(id+"F0.wireOp",EDGE,"E665"),sQuery(id+"F0.wireOp",EDGE,"E666"),sQuery(id+"F0.wireOp",EDGE,"E667"),sQuery(id+"F0.wireOp",EDGE,"E668"),sQuery(id+"F0.wireOp",EDGE,"E669"),sQuery(id+"F0.wireOp",EDGE,"E670"),sQuery(id+"F0.wireOp",EDGE,"E671"),sQuery(id+"F0.wireOp",EDGE,"E672"),sQuery(id+"F0.wireOp",EDGE,"E673"),sQuery(id+"F0.wireOp",EDGE,"E674"),sQuery(id+"F0.wireOp",EDGE,"E675"),sQuery(id+"F0.wireOp",EDGE,"E676"),sQuery(id+"F0.wireOp",EDGE,"E677"),sQuery(id+"F0.wireOp",EDGE,"E678"),sQuery(id+"F0.wireOp",EDGE,"E679"),sQuery(id+"F0.wireOp",EDGE,"E680"),sQuery(id+"F0.wireOp",EDGE,"E681"),sQuery(id+"F0.wireOp",EDGE,"E682"),sQuery(id+"F0.wireOp",EDGE,"E683"),sQuery(id+"F0.wireOp",EDGE,"E684"),sQuery(id+"F0.wireOp",EDGE,"E685"),sQuery(id+"F0.wireOp",EDGE,"E686"),sQuery(id+"F0.wireOp",EDGE,"E687"),sQuery(id+"F0.wireOp",EDGE,"E688"),sQuery(id+"F0.wireOp",EDGE,"E689"),sQuery(id+"F0.wireOp",EDGE,"E690"),sQuery(id+"F0.wireOp",EDGE,"E691"),sQuery(id+"F0.wireOp",EDGE,"E692"),sQuery(id+"F0.wireOp",EDGE,"E693"),sQuery(id+"F0.wireOp",EDGE,"E694"),sQuery(id+"F0.wireOp",EDGE,"E695"),sQuery(id+"F0.wireOp",EDGE,"E696"),sQuery(id+"F0.wireOp",EDGE,"E697"),sQuery(id+"F0.wireOp",EDGE,"E698"),sQuery(id+"F0.wireOp",EDGE,"E699"),sQuery(id+"F0.wireOp",EDGE,"E700"),sQuery(id+"F0.wireOp",EDGE,"E701"),sQuery(id+"F0.wireOp",EDGE,"E702"),sQuery(id+"F0.wireOp",EDGE,"E703"),sQuery(id+"F0.wireOp",EDGE,"E704"),sQuery(id+"F0.wireOp",EDGE,"E705"),sQuery(id+"F0.wireOp",EDGE,"E706"),sQuery(id+"F0.wireOp",EDGE,"E707"),sQuery(id+"F0.wireOp",EDGE,"E708"),sQuery(id+"F0.wireOp",EDGE,"E709"),sQuery(id+"F0.wireOp",EDGE,"E710"),sQuery(id+"F0.wireOp",EDGE,"E711"),sQuery(id+"F0.wireOp",EDGE,"E712"),sQuery(id+"F0.wireOp",EDGE,"E713"),sQuery(id+"F0.wireOp",EDGE,"E714"),sQuery(id+"F0.wireOp",EDGE,"E715"),sQuery(id+"F0.wireOp",EDGE,"E716"),sQuery(id+"F0.wireOp",EDGE,"E717"),sQuery(id+"F0.wireOp",EDGE,"E718"),sQuery(id+"F0.wireOp",EDGE,"E719"),sQuery(id+"F0.wireOp",EDGE,"E720"),sQuery(id+"F0.wireOp",EDGE,"E721"),sQuery(id+"F0.wireOp",EDGE,"E722"),sQuery(id+"F0.wireOp",EDGE,"E723"),sQuery(id+"F0.wireOp",EDGE,"E724"),sQuery(id+"F0.wireOp",EDGE,"E725"),sQuery(id+"F0.wireOp",EDGE,"E726"),sQuery(id+"F0.wireOp",EDGE,"E727"),sQuery(id+"F0.wireOp",EDGE,"E728"),sQuery(id+"F0.wireOp",EDGE,"E729"),sQuery(id+"F0.wireOp",EDGE,"E730"),sQuery(id+"F0.wireOp",EDGE,"E731"),sQuery(id+"F0.wireOp",EDGE,"E732"),sQuery(id+"F0.wireOp",EDGE,"E733"),sQuery(id+"F0.wireOp",EDGE,"E734"),sQuery(id+"F0.wireOp",EDGE,"E735"),sQuery(id+"F0.wireOp",EDGE,"E736"),sQuery(id+"F0.wireOp",EDGE,"E737"),sQuery(id+"F0.wireOp",EDGE,"E738"),sQuery(id+"F0.wireOp",EDGE,"E739"),sQuery(id+"F0.wireOp",EDGE,"E740"),sQuery(id+"F0.wireOp",EDGE,"E741"),sQuery(id+"F0.wireOp",EDGE,"E742"),sQuery(id+"F0.wireOp",EDGE,"E743"),sQuery(id+"F0.wireOp",EDGE,"E744"),sQuery(id+"F0.wireOp",EDGE,"E745"),sQuery(id+"F0.wireOp",EDGE,"E746"),sQuery(id+"F0.wireOp",EDGE,"E747"),sQuery(id+"F0.wireOp",EDGE,"E748"),sQuery(id+"F0.wireOp",EDGE,"E749"),sQuery(id+"F0.wireOp",EDGE,"E750"),sQuery(id+"F0.wireOp",EDGE,"E751"),sQuery(id+"F0.wireOp",EDGE,"E752"),sQuery(id+"F0.wireOp",EDGE,"E753"),sQuery(id+"F0.wireOp",EDGE,"E754"),sQuery(id+"F0.wireOp",EDGE,"E755"),sQuery(id+"F0.wireOp",EDGE,"E756"),sQuery(id+"F0.wireOp",EDGE,"E757"),sQuery(id+"F0.wireOp",EDGE,"E758"),sQuery(id+"F0.wireOp",EDGE,"E759"),sQuery(id+"F0.wireOp",EDGE,"E760"),sQuery(id+"F0.wireOp",EDGE,"E761"),sQuery(id+"F0.wireOp",EDGE,"E762"),sQuery(id+"F0.wireOp",EDGE,"E763"),sQuery(id+"F0.wireOp",EDGE,"E764"),sQuery(id+"F0.wireOp",EDGE,"E765"),sQuery(id+"F0.wireOp",EDGE,"E766"),sQuery(id+"F0.wireOp",EDGE,"E767"),sQuery(id+"F0.wireOp",EDGE,"E768"),sQuery(id+"F0.wireOp",EDGE,"E769"),sQuery(id+"F0.wireOp",EDGE,"E770"),sQuery(id+"F0.wireOp",EDGE,"E771"),sQuery(id+"F0.wireOp",EDGE,"E772"),sQuery(id+"F0.wireOp",EDGE,"E773"),sQuery(id+"F0.wireOp",EDGE,"E774"),sQuery(id+"F0.wireOp",EDGE,"E775"),sQuery(id+"F0.wireOp",EDGE,"E776"),sQuery(id+"F0.wireOp",EDGE,"E777"),sQuery(id+"F0.wireOp",EDGE,"E778"),sQuery(id+"F0.wireOp",EDGE,"E779"),sQuery(id+"F0.wireOp",EDGE,"E780"),sQuery(id+"F0.wireOp",EDGE,"E781"),sQuery(id+"F0.wireOp",EDGE,"E782"),sQuery(id+"F0.wireOp",EDGE,"E783"),sQuery(id+"F0.wireOp",EDGE,"E784"),sQuery(id+"F0.wireOp",EDGE,"E785"),sQuery(id+"F0.wireOp",EDGE,"E786"),sQuery(id+"F0.wireOp",EDGE,"E787"),sQuery(id+"F0.wireOp",EDGE,"E788"),sQuery(id+"F0.wireOp",EDGE,"E789"),sQuery(id+"F0.wireOp",EDGE,"E790"),sQuery(id+"F0.wireOp",EDGE,"E791"),sQuery(id+"F0.wireOp",EDGE,"E792"),sQuery(id+"F0.wireOp",EDGE,"E793"),sQuery(id+"F0.wireOp",EDGE,"E794"),sQuery(id+"F0.wireOp",EDGE,"E795"),sQuery(id+"F0.wireOp",EDGE,"E796"),sQuery(id+"F0.wireOp",EDGE,"E797"),sQuery(id+"F0.wireOp",EDGE,"E798"),sQuery(id+"F0.wireOp",EDGE,"E799"),sQuery(id+"F0.wireOp",EDGE,"E800"),sQuery(id+"F0.wireOp",EDGE,"E801"),sQuery(id+"F0.wireOp",EDGE,"E802"),sQuery(id+"F0.wireOp",EDGE,"E803"),sQuery(id+"F0.wireOp",EDGE,"E804"),sQuery(id+"F0.wireOp",EDGE,"E805"),sQuery(id+"F0.wireOp",EDGE,"E806"),sQuery(id+"F0.wireOp",EDGE,"E807"),sQuery(id+"F0.wireOp",EDGE,"E808"),sQuery(id+"F0.wireOp",EDGE,"E809"),sQuery(id+"F0.wireOp",EDGE,"E810"),sQuery(id+"F0.wireOp",EDGE,"E811"),sQuery(id+"F0.wireOp",EDGE,"E812"),sQuery(id+"F0.wireOp",EDGE,"E813"),sQuery(id+"F0.wireOp",EDGE,"E814"),sQuery(id+"F0.wireOp",EDGE,"E815"),sQuery(id+"F0.wireOp",EDGE,"E816"),sQuery(id+"F0.wireOp",EDGE,"E817"),sQuery(id+"F0.wireOp",EDGE,"E818"),sQuery(id+"F0.wireOp",EDGE,"E819"),sQuery(id+"F0.wireOp",EDGE,"E820"),sQuery(id+"F0.wireOp",EDGE,"E821"),sQuery(id+"F0.wireOp",EDGE,"E822"),sQuery(id+"F0.wireOp",EDGE,"E823"),sQuery(id+"F0.wireOp",EDGE,"E824"),sQuery(id+"F0.wireOp",EDGE,"E825"),sQuery(id+"F0.wireOp",EDGE,"E826"),sQuery(id+"F0.wireOp",EDGE,"E827"),sQuery(id+"F0.wireOp",EDGE,"E828"),sQuery(id+"F0.wireOp",EDGE,"E829"),sQuery(id+"F0.wireOp",EDGE,"E830"),sQuery(id+"F0.wireOp",EDGE,"E831"),sQuery(id+"F0.wireOp",EDGE,"E832"),sQuery(id+"F0.wireOp",EDGE,"E833"),sQuery(id+"F0.wireOp",EDGE,"E834"),sQuery(id+"F0.wireOp",EDGE,"E835"),sQuery(id+"F0.wireOp",EDGE,"E836"),sQuery(id+"F0.wireOp",EDGE,"E837"),sQuery(id+"F0.wireOp",EDGE,"E838"),sQuery(id+"F0.wireOp",EDGE,"E839"),sQuery(id+"F0.wireOp",EDGE,"E840"),sQuery(id+"F0.wireOp",EDGE,"E841"),sQuery(id+"F0.wireOp",EDGE,"E842"),sQuery(id+"F0.wireOp",EDGE,"E843"),sQuery(id+"F0.wireOp",EDGE,"E844"),sQuery(id+"F0.wireOp",EDGE,"E845"),sQuery(id+"F0.wireOp",EDGE,"E846"),sQuery(id+"F0.wireOp",EDGE,"E847"),sQuery(id+"F0.wireOp",EDGE,"E848"),sQuery(id+"F0.wireOp",EDGE,"E849"),sQuery(id+"F0.wireOp",EDGE,"E850"),sQuery(id+"F0.wireOp",EDGE,"E851"),sQuery(id+"F0.wireOp",EDGE,"E852"),sQuery(id+"F0.wireOp",EDGE,"E853"),sQuery(id+"F0.wireOp",EDGE,"E854"),sQuery(id+"F0.wireOp",EDGE,"E855"),sQuery(id+"F0.wireOp",EDGE,"E856"),sQuery(id+"F0.wireOp",EDGE,"E857"),sQuery(id+"F0.wireOp",EDGE,"E858"),sQuery(id+"F0.wireOp",EDGE,"E859"),sQuery(id+"F0.wireOp",EDGE,"E860"),sQuery(id+"F0.wireOp",EDGE,"E861"),sQuery(id+"F0.wireOp",EDGE,"E862"),sQuery(id+"F0.wireOp",EDGE,"E863"),sQuery(id+"F0.wireOp",EDGE,"E864"),sQuery(id+"F0.wireOp",EDGE,"E865"),sQuery(id+"F0.wireOp",EDGE,"E866"),sQuery(id+"F0.wireOp",EDGE,"E867"),sQuery(id+"F0.wireOp",EDGE,"E868"),sQuery(id+"F0.wireOp",EDGE,"E869"),sQuery(id+"F0.wireOp",EDGE,"E870"),sQuery(id+"F0.wireOp",EDGE,"E871"),sQuery(id+"F0.wireOp",EDGE,"E872"),sQuery(id+"F0.wireOp",EDGE,"E873"),sQuery(id+"F0.wireOp",EDGE,"E874"),sQuery(id+"F0.wireOp",EDGE,"E875"),sQuery(id+"F0.wireOp",EDGE,"E876"),sQuery(id+"F0.wireOp",EDGE,"E877"),sQuery(id+"F0.wireOp",EDGE,"E878"),sQuery(id+"F0.wireOp",EDGE,"E879"),sQuery(id+"F0.wireOp",EDGE,"E880"),sQuery(id+"F0.wireOp",EDGE,"E881"),sQuery(id+"F0.wireOp",EDGE,"E882"),sQuery(id+"F0.wireOp",EDGE,"E883"),sQuery(id+"F0.wireOp",EDGE,"E884"),sQuery(id+"F0.wireOp",EDGE,"E885"),sQuery(id+"F0.wireOp",EDGE,"E886"),sQuery(id+"F0.wireOp",EDGE,"E887"),sQuery(id+"F0.wireOp",EDGE,"E888"),sQuery(id+"F0.wireOp",EDGE,"E889"),sQuery(id+"F0.wireOp",EDGE,"E890"),sQuery(id+"F0.wireOp",EDGE,"E891"),sQuery(id+"F0.wireOp",EDGE,"E892"),sQuery(id+"F0.wireOp",EDGE,"E893"),sQuery(id+"F0.wireOp",EDGE,"E894"),sQuery(id+"F0.wireOp",EDGE,"E895"),sQuery(id+"F0.wireOp",EDGE,"E896"),sQuery(id+"F0.wireOp",EDGE,"E897"),sQuery(id+"F0.wireOp",EDGE,"E898"),sQuery(id+"F0.wireOp",EDGE,"E899"),sQuery(id+"F0.wireOp",EDGE,"E900"),sQuery(id+"F0.wireOp",EDGE,"E901"),sQuery(id+"F0.wireOp",EDGE,"E902"),sQuery(id+"F0.wireOp",EDGE,"E903"),sQuery(id+"F0.wireOp",EDGE,"E904"),sQuery(id+"F0.wireOp",EDGE,"E905"),sQuery(id+"F0.wireOp",EDGE,"E906"),sQuery(id+"F0.wireOp",EDGE,"E907"),sQuery(id+"F0.wireOp",EDGE,"E908"),sQuery(id+"F0.wireOp",EDGE,"E909"),sQuery(id+"F0.wireOp",EDGE,"E910"),sQuery(id+"F0.wireOp",EDGE,"E911"),sQuery(id+"F0.wireOp",EDGE,"E912"),sQuery(id+"F0.wireOp",EDGE,"E913"),sQuery(id+"F0.wireOp",EDGE,"E914"),sQuery(id+"F0.wireOp",EDGE,"E915"),sQuery(id+"F0.wireOp",EDGE,"E916"),sQuery(id+"F0.wireOp",EDGE,"E917"),sQuery(id+"F0.wireOp",EDGE,"E918"),sQuery(id+"F0.wireOp",EDGE,"E919"),sQuery(id+"F0.wireOp",EDGE,"E920"),sQuery(id+"F0.wireOp",EDGE,"E921"),sQuery(id+"F0.wireOp",EDGE,"E922"),sQuery(id+"F0.wireOp",EDGE,"E923"),sQuery(id+"F0.wireOp",EDGE,"E924"),sQuery(id+"F0.wireOp",EDGE,"E925"),sQuery(id+"F0.wireOp",EDGE,"E926"),sQuery(id+"F0.wireOp",EDGE,"E927"),sQuery(id+"F0.wireOp",EDGE,"E928"),sQuery(id+"F0.wireOp",EDGE,"E929"),sQuery(id+"F0.wireOp",EDGE,"E930"),sQuery(id+"F0.wireOp",EDGE,"E931"),sQuery(id+"F0.wireOp",EDGE,"E932"),sQuery(id+"F0.wireOp",EDGE,"E933"),sQuery(id+"F0.wireOp",EDGE,"E934"),sQuery(id+"F0.wireOp",EDGE,"E935"),sQuery(id+"F0.wireOp",EDGE,"E936"),sQuery(id+"F0.wireOp",EDGE,"E937"),sQuery(id+"F0.wireOp",EDGE,"E938"),sQuery(id+"F0.wireOp",EDGE,"E939"),sQuery(id+"F0.wireOp",EDGE,"E940"),sQuery(id+"F0.wireOp",EDGE,"E941"),sQuery(id+"F0.wireOp",EDGE,"E942"),sQuery(id+"F0.wireOp",EDGE,"E943"),sQuery(id+"F0.wireOp",EDGE,"E944"),sQuery(id+"F0.wireOp",EDGE,"E945"),sQuery(id+"F0.wireOp",EDGE,"E946"),sQuery(id+"F0.wireOp",EDGE,"E947"),sQuery(id+"F0.wireOp",EDGE,"E948"),sQuery(id+"F0.wireOp",EDGE,"E949"),sQuery(id+"F0.wireOp",EDGE,"E950"),sQuery(id+"F0.wireOp",EDGE,"E951"),sQuery(id+"F0.wireOp",EDGE,"E952"),sQuery(id+"F0.wireOp",EDGE,"E953"),sQuery(id+"F0.wireOp",EDGE,"E954"),sQuery(id+"F0.wireOp",EDGE,"E955"),sQuery(id+"F0.wireOp",EDGE,"E956"),sQuery(id+"F0.wireOp",EDGE,"E957"),sQuery(id+"F0.wireOp",EDGE,"E958"),sQuery(id+"F0.wireOp",EDGE,"E959"),sQuery(id+"F0.wireOp",EDGE,"E960"),sQuery(id+"F0.wireOp",EDGE,"E961"),sQuery(id+"F0.wireOp",EDGE,"E962"),sQuery(id+"F0.wireOp",EDGE,"E963"),sQuery(id+"F0.wireOp",EDGE,"E964"),sQuery(id+"F0.wireOp",EDGE,"E965"),sQuery(id+"F0.wireOp",EDGE,"E966"),sQuery(id+"F0.wireOp",EDGE,"E967"),sQuery(id+"F0.wireOp",EDGE,"E968"),sQuery(id+"F0.wireOp",EDGE,"E969"),sQuery(id+"F0.wireOp",EDGE,"E970"),sQuery(id+"F0.wireOp",EDGE,"E971"),sQuery(id+"F0.wireOp",EDGE,"E972"),sQuery(id+"F0.wireOp",EDGE,"E973"),sQuery(id+"F0.wireOp",EDGE,"E974"),sQuery(id+"F0.wireOp",EDGE,"E975"),sQuery(id+"F0.wireOp",EDGE,"E976"),sQuery(id+"F0.wireOp",EDGE,"E977"),sQuery(id+"F0.wireOp",EDGE,"E978"),sQuery(id+"F0.wireOp",EDGE,"E979"),sQuery(id+"F0.wireOp",EDGE,"E980"),sQuery(id+"F0.wireOp",EDGE,"E981"),sQuery(id+"F0.wireOp",EDGE,"E982"),sQuery(id+"F0.wireOp",EDGE,"E983"),sQuery(id+"F0.wireOp",EDGE,"E984"),sQuery(id+"F0.wireOp",EDGE,"E985"),sQuery(id+"F0.wireOp",EDGE,"E986"),sQuery(id+"F0.wireOp",EDGE,"E987"),sQuery(id+"F0.wireOp",EDGE,"E988"),sQuery(id+"F0.wireOp",EDGE,"E989"),sQuery(id+"F0.wireOp",EDGE,"E990"),sQuery(id+"F0.wireOp",EDGE,"E991"),sQuery(id+"F0.wireOp",EDGE,"E992"),sQuery(id+"F0.wireOp",EDGE,"E993"),sQuery(id+"F0.wireOp",EDGE,"E994"),sQuery(id+"F0.wireOp",EDGE,"E995"),sQuery(id+"F0.wireOp",EDGE,"E996"),sQuery(id+"F0.wireOp",EDGE,"E997"),sQuery(id+"F0.wireOp",EDGE,"E998"),sQuery(id+"F0.wireOp",EDGE,"E999"),sQuery(id+"F0.wireOp",EDGE,"E1000"),sQuery(id+"F0.wireOp",EDGE,"E1001"),sQuery(id+"F0.wireOp",EDGE,"E1002"),sQuery(id+"F0.wireOp",EDGE,"E1003"),sQuery(id+"F0.wireOp",EDGE,"E1004"),sQuery(id+"F0.wireOp",EDGE,"E1005"),sQuery(id+"F0.wireOp",EDGE,"E1006"),sQuery(id+"F0.wireOp",EDGE,"E1007"),sQuery(id+"F0.wireOp",EDGE,"E1008"),sQuery(id+"F0.wireOp",EDGE,"E1009"),sQuery(id+"F0.wireOp",EDGE,"E1010"),sQuery(id+"F0.wireOp",EDGE,"E1011"),sQuery(id+"F0.wireOp",EDGE,"E1012"),sQuery(id+"F0.wireOp",EDGE,"E1013"),sQuery(id+"F0.wireOp",EDGE,"E1014"),sQuery(id+"F0.wireOp",EDGE,"E1015"),sQuery(id+"F0.wireOp",EDGE,"E1016"),sQuery(id+"F0.wireOp",EDGE,"E1017"),sQuery(id+"F0.wireOp",EDGE,"E1018"),sQuery(id+"F0.wireOp",EDGE,"E1019"),sQuery(id+"F0.wireOp",EDGE,"E1020"),sQuery(id+"F0.wireOp",EDGE,"E1021"),sQuery(id+"F0.wireOp",EDGE,"E1022"),sQuery(id+"F0.wireOp",EDGE,"E1023"),sQuery(id+"F0.wireOp",EDGE,"E1024"),sQuery(id+"F0.wireOp",EDGE,"E1025"),sQuery(id+"F0.wireOp",EDGE,"E1026"),sQuery(id+"F0.wireOp",EDGE,"E1027"),sQuery(id+"F0.wireOp",EDGE,"E1028"),sQuery(id+"F0.wireOp",EDGE,"E1029"),sQuery(id+"F0.wireOp",EDGE,"E1030"),sQuery(id+"F0.wireOp",EDGE,"E1031"),sQuery(id+"F0.wireOp",EDGE,"E1032"),sQuery(id+"F0.wireOp",EDGE,"E1033"),sQuery(id+"F0.wireOp",EDGE,"E1034"),sQuery(id+"F0.wireOp",EDGE,"E1035"),sQuery(id+"F0.wireOp",EDGE,"E1036"),sQuery(id+"F0.wireOp",EDGE,"E1037"),sQuery(id+"F0.wireOp",EDGE,"E1038"),sQuery(id+"F0.wireOp",EDGE,"E1039"),sQuery(id+"F0.wireOp",EDGE,"E1040"),sQuery(id+"F0.wireOp",EDGE,"E1041"),sQuery(id+"F0.wireOp",EDGE,"E1042"),sQuery(id+"F0.wireOp",EDGE,"E1043"),sQuery(id+"F0.wireOp",EDGE,"E1044"),sQuery(id+"F0.wireOp",EDGE,"E1045"),sQuery(id+"F0.wireOp",EDGE,"E1046"),sQuery(id+"F0.wireOp",EDGE,"E1047"),sQuery(id+"F0.wireOp",EDGE,"E1048"),sQuery(id+"F0.wireOp",EDGE,"E1049"),sQuery(id+"F0.wireOp",EDGE,"E1050"),sQuery(id+"F0.wireOp",EDGE,"E1051"),sQuery(id+"F0.wireOp",EDGE,"E1052"),sQuery(id+"F0.wireOp",EDGE,"E1053"),sQuery(id+"F0.wireOp",EDGE,"E1054"),sQuery(id+"F0.wireOp",EDGE,"E1055"),sQuery(id+"F0.wireOp",EDGE,"E1056"),sQuery(id+"F0.wireOp",EDGE,"E1057"),sQuery(id+"F0.wireOp",EDGE,"E1058"),sQuery(id+"F0.wireOp",EDGE,"E1059"),sQuery(id+"F0.wireOp",EDGE,"E1060"),sQuery(id+"F0.wireOp",EDGE,"E1061"),sQuery(id+"F0.wireOp",EDGE,"E1062"),sQuery(id+"F0.wireOp",EDGE,"E1063"),sQuery(id+"F0.wireOp",EDGE,"E1064"),sQuery(id+"F0.wireOp",EDGE,"E1065"),sQuery(id+"F0.wireOp",EDGE,"E1066"),sQuery(id+"F0.wireOp",EDGE,"E1067"),sQuery(id+"F0.wireOp",EDGE,"E1068"),sQuery(id+"F0.wireOp",EDGE,"E1069"),sQuery(id+"F0.wireOp",EDGE,"E1070"),sQuery(id+"F0.wireOp",EDGE,"E1071"),sQuery(id+"F0.wireOp",EDGE,"E1072"),sQuery(id+"F0.wireOp",EDGE,"E1073"),sQuery(id+"F0.wireOp",EDGE,"E1074"),sQuery(id+"F0.wireOp",EDGE,"E1075"),sQuery(id+"F0.wireOp",EDGE,"E1076"),sQuery(id+"F0.wireOp",EDGE,"E1077"),sQuery(id+"F0.wireOp",EDGE,"E1078"),sQuery(id+"F0.wireOp",EDGE,"E1079"),sQuery(id+"F0.wireOp",EDGE,"E1080"),sQuery(id+"F0.wireOp",EDGE,"E1081"),sQuery(id+"F0.wireOp",EDGE,"E1082"),sQuery(id+"F0.wireOp",EDGE,"E1083"),sQuery(id+"F0.wireOp",EDGE,"E1084"),sQuery(id+"F0.wireOp",EDGE,"E1085"),sQuery(id+"F0.wireOp",EDGE,"E1086"),sQuery(id+"F0.wireOp",EDGE,"E1087"),sQuery(id+"F0.wireOp",EDGE,"E1088"),sQuery(id+"F0.wireOp",EDGE,"E1089"),sQuery(id+"F0.wireOp",EDGE,"E1090"),sQuery(id+"F0.wireOp",EDGE,"E1091"),sQuery(id+"F0.wireOp",EDGE,"E1092"),sQuery(id+"F0.wireOp",EDGE,"E1093"),sQuery(id+"F0.wireOp",EDGE,"E1094"),sQuery(id+"F0.wireOp",EDGE,"E1095"),sQuery(id+"F0.wireOp",EDGE,"E1096"),sQuery(id+"F0.wireOp",EDGE,"E1097"),sQuery(id+"F0.wireOp",EDGE,"E1098"),sQuery(id+"F0.wireOp",EDGE,"E1099"),sQuery(id+"F0.wireOp",EDGE,"E1100"),sQuery(id+"F0.wireOp",EDGE,"E1101"),sQuery(id+"F0.wireOp",EDGE,"E1102"),sQuery(id+"F0.wireOp",EDGE,"E1103"),sQuery(id+"F0.wireOp",EDGE,"E1104"),sQuery(id+"F0.wireOp",EDGE,"E1105"),sQuery(id+"F0.wireOp",EDGE,"E1106"),sQuery(id+"F0.wireOp",EDGE,"E1107"),sQuery(id+"F0.wireOp",EDGE,"E1108"),sQuery(id+"F0.wireOp",EDGE,"E1109"),sQuery(id+"F0.wireOp",EDGE,"E1110"),sQuery(id+"F0.wireOp",EDGE,"E1111"),sQuery(id+"F0.wireOp",EDGE,"E1112"),sQuery(id+"F0.wireOp",EDGE,"E1113"),sQuery(id+"F0.wireOp",EDGE,"E1114"),sQuery(id+"F0.wireOp",EDGE,"E1115"),sQuery(id+"F0.wireOp",EDGE,"E1116"),sQuery(id+"F0.wireOp",EDGE,"E1117"),sQuery(id+"F0.wireOp",EDGE,"E1118"),sQuery(id+"F0.wireOp",EDGE,"E1119"),sQuery(id+"F0.wireOp",EDGE,"E1120"),sQuery(id+"F0.wireOp",EDGE,"E1121"),sQuery(id+"F0.wireOp",EDGE,"E1122"),sQuery(id+"F0.wireOp",EDGE,"E1123"),sQuery(id+"F0.wireOp",EDGE,"E1124"),sQuery(id+"F0.wireOp",EDGE,"E1125"),sQuery(id+"F0.wireOp",EDGE,"E1126"),sQuery(id+"F0.wireOp",EDGE,"E1127"),sQuery(id+"F0.wireOp",EDGE,"E1128"),sQuery(id+"F0.wireOp",EDGE,"E1129"),sQuery(id+"F0.wireOp",EDGE,"E1130"),sQuery(id+"F0.wireOp",EDGE,"E1131"),sQuery(id+"F0.wireOp",EDGE,"E1132"),sQuery(id+"F0.wireOp",EDGE,"E1133"),sQuery(id+"F0.wireOp",EDGE,"E1134"),sQuery(id+"F0.wireOp",EDGE,"E1135"),sQuery(id+"F0.wireOp",EDGE,"E1136"),sQuery(id+"F0.wireOp",EDGE,"E1137"),sQuery(id+"F0.wireOp",EDGE,"E1138"),sQuery(id+"F0.wireOp",EDGE,"E1139"),sQuery(id+"F0.wireOp",EDGE,"E1140"),sQuery(id+"F0.wireOp",EDGE,"E1141"),sQuery(id+"F0.wireOp",EDGE,"E1142"),sQuery(id+"F0.wireOp",EDGE,"E1143"),sQuery(id+"F0.wireOp",EDGE,"E1144"),sQuery(id+"F0.wireOp",EDGE,"E1145"),sQuery(id+"F0.wireOp",EDGE,"E1146"),sQuery(id+"F0.wireOp",EDGE,"E1147"),sQuery(id+"F0.wireOp",EDGE,"E1148"),sQuery(id+"F0.wireOp",EDGE,"E1149"),sQuery(id+"F0.wireOp",EDGE,"E1150"),sQuery(id+"F0.wireOp",EDGE,"E1151"),sQuery(id+"F0.wireOp",EDGE,"E1152"),sQuery(id+"F0.wireOp",EDGE,"E1153"),sQuery(id+"F0.wireOp",EDGE,"E1154"),sQuery(id+"F0.wireOp",EDGE,"E1155"),sQuery(id+"F0.wireOp",EDGE,"E1156"),sQuery(id+"F0.wireOp",EDGE,"E1157"),sQuery(id+"F0.wireOp",EDGE,"E1158"),sQuery(id+"F0.wireOp",EDGE,"E1159"),sQuery(id+"F0.wireOp",EDGE,"E1160"),sQuery(id+"F0.wireOp",EDGE,"E1161"),sQuery(id+"F0.wireOp",EDGE,"E1162"),sQuery(id+"F0.wireOp",EDGE,"E1163"),sQuery(id+"F0.wireOp",EDGE,"E1164"),sQuery(id+"F0.wireOp",EDGE,"E1165"),sQuery(id+"F0.wireOp",EDGE,"E1166"),sQuery(id+"F0.wireOp",EDGE,"E1167"),sQuery(id+"F0.wireOp",EDGE,"E1168"),sQuery(id+"F0.wireOp",EDGE,"E1169"),sQuery(id+"F0.wireOp",EDGE,"E1170"),sQuery(id+"F0.wireOp",EDGE,"E1171"),sQuery(id+"F0.wireOp",EDGE,"E1172"),sQuery(id+"F0.wireOp",EDGE,"E1173"),sQuery(id+"F0.wireOp",EDGE,"E1174"),sQuery(id+"F0.wireOp",EDGE,"E1175"),sQuery(id+"F0.wireOp",EDGE,"E1176"),sQuery(id+"F0.wireOp",EDGE,"E1177"),sQuery(id+"F0.wireOp",EDGE,"E1178"),sQuery(id+"F0.wireOp",EDGE,"E1179"),sQuery(id+"F0.wireOp",EDGE,"E1180"),sQuery(id+"F0.wireOp",EDGE,"E1181"),sQuery(id+"F0.wireOp",EDGE,"E1182"),sQuery(id+"F0.wireOp",EDGE,"E1183"),sQuery(id+"F0.wireOp",EDGE,"E1184"),sQuery(id+"F0.wireOp",EDGE,"E1185"),sQuery(id+"F0.wireOp",EDGE,"E1186"),sQuery(id+"F0.wireOp",EDGE,"E1187"),sQuery(id+"F0.wireOp",EDGE,"E1188"),sQuery(id+"F0.wireOp",EDGE,"E1189"),sQuery(id+"F0.wireOp",EDGE,"E1190"),sQuery(id+"F0.wireOp",EDGE,"E1191"),sQuery(id+"F0.wireOp",EDGE,"E1192"),sQuery(id+"F0.wireOp",EDGE,"E1193"),sQuery(id+"F0.wireOp",EDGE,"E1194"),sQuery(id+"F0.wireOp",EDGE,"E1195"),sQuery(id+"F0.wireOp",EDGE,"E1196"),sQuery(id+"F0.wireOp",EDGE,"E1197"),sQuery(id+"F0.wireOp",EDGE,"E1198"),sQuery(id+"F0.wireOp",EDGE,"E1199"),sQuery(id+"F0.wireOp",EDGE,"E1200"),sQuery(id+"F0.wireOp",EDGE,"E1201"),sQuery(id+"F0.wireOp",EDGE,"E1202"),sQuery(id+"F0.wireOp",EDGE,"E1203"),sQuery(id+"F0.wireOp",EDGE,"E1204"),sQuery(id+"F0.wireOp",EDGE,"E1205"),sQuery(id+"F0.wireOp",EDGE,"E1206"),sQuery(id+"F0.wireOp",EDGE,"E1207"),sQuery(id+"F0.wireOp",EDGE,"E1208"),sQuery(id+"F0.wireOp",EDGE,"E1209"),sQuery(id+"F0.wireOp",EDGE,"E1210"),sQuery(id+"F0.wireOp",EDGE,"E1211"),sQuery(id+"F0.wireOp",EDGE,"E1212"),sQuery(id+"F0.wireOp",EDGE,"E1213"),sQuery(id+"F0.wireOp",EDGE,"E1214"),sQuery(id+"F0.wireOp",EDGE,"E1215"),sQuery(id+"F0.wireOp",EDGE,"E1216"),sQuery(id+"F0.wireOp",EDGE,"E1217"),sQuery(id+"F0.wireOp",EDGE,"E1218"),sQuery(id+"F0.wireOp",EDGE,"E1219"),sQuery(id+"F0.wireOp",EDGE,"E1220"),sQuery(id+"F0.wireOp",EDGE,"E1221"),sQuery(id+"F0.wireOp",EDGE,"E1222"),sQuery(id+"F0.wireOp",EDGE,"E1223"),sQuery(id+"F0.wireOp",EDGE,"E1224"),sQuery(id+"F0.wireOp",EDGE,"E1225"),sQuery(id+"F0.wireOp",EDGE,"E1226"),sQuery(id+"F0.wireOp",EDGE,"E1227"),sQuery(id+"F0.wireOp",EDGE,"E1228"),sQuery(id+"F0.wireOp",EDGE,"E1229"),sQuery(id+"F0.wireOp",EDGE,"E1230"),sQuery(id+"F0.wireOp",EDGE,"E1231"),sQuery(id+"F0.wireOp",EDGE,"E1232"),sQuery(id+"F0.wireOp",EDGE,"E1233"),sQuery(id+"F0.wireOp",EDGE,"E1234"),sQuery(id+"F0.wireOp",EDGE,"E1235"),sQuery(id+"F0.wireOp",EDGE,"E1236"),sQuery(id+"F0.wireOp",EDGE,"E1237"),sQuery(id+"F0.wireOp",EDGE,"E1238"),sQuery(id+"F0.wireOp",EDGE,"E1239"),sQuery(id+"F0.wireOp",EDGE,"E1240"),sQuery(id+"F0.wireOp",EDGE,"E1241"),sQuery(id+"F0.wireOp",EDGE,"E1242"),sQuery(id+"F0.wireOp",EDGE,"E1243"),sQuery(id+"F0.wireOp",EDGE,"E1244"),sQuery(id+"F0.wireOp",EDGE,"E1245"),sQuery(id+"F0.wireOp",EDGE,"E1246"),sQuery(id+"F0.wireOp",EDGE,"E1247"),sQuery(id+"F0.wireOp",EDGE,"E1248"),sQuery(id+"F0.wireOp",EDGE,"E1249"),sQuery(id+"F0.wireOp",EDGE,"E1250"),sQuery(id+"F0.wireOp",EDGE,"E1251"),sQuery(id+"F0.wireOp",EDGE,"E1252"),sQuery(id+"F0.wireOp",EDGE,"E1253"),sQuery(id+"F0.wireOp",EDGE,"E1254"),sQuery(id+"F0.wireOp",EDGE,"E1255"),sQuery(id+"F0.wireOp",EDGE,"E1256"),sQuery(id+"F0.wireOp",EDGE,"E1257"),sQuery(id+"F0.wireOp",EDGE,"E1258"),sQuery(id+"F0.wireOp",EDGE,"E1259"),sQuery(id+"F0.wireOp",EDGE,"E1260"),sQuery(id+"F0.wireOp",EDGE,"E1261"),sQuery(id+"F0.wireOp",EDGE,"E1262"),sQuery(id+"F0.wireOp",EDGE,"E1263"),sQuery(id+"F0.wireOp",EDGE,"E1264"),sQuery(id+"F0.wireOp",EDGE,"E1265"),sQuery(id+"F0.wireOp",EDGE,"E1266"),sQuery(id+"F0.wireOp",EDGE,"E1267"),sQuery(id+"F0.wireOp",EDGE,"E1268"),sQuery(id+"F0.wireOp",EDGE,"E1269"),sQuery(id+"F0.wireOp",EDGE,"E1270"),sQuery(id+"F0.wireOp",EDGE,"E1271"),sQuery(id+"F0.wireOp",EDGE,"E1272"),sQuery(id+"F0.wireOp",EDGE,"E1273"),sQuery(id+"F0.wireOp",EDGE,"E1274"),sQuery(id+"F0.wireOp",EDGE,"E1275"),sQuery(id+"F0.wireOp",EDGE,"E1276"),sQuery(id+"F0.wireOp",EDGE,"E1277"),sQuery(id+"F0.wireOp",EDGE,"E1278"),sQuery(id+"F0.wireOp",EDGE,"E1279"),sQuery(id+"F0.wireOp",EDGE,"E1280"),sQuery(id+"F0.wireOp",EDGE,"E1281"),sQuery(id+"F0.wireOp",EDGE,"E1282"),sQuery(id+"F0.wireOp",EDGE,"E1283"),sQuery(id+"F0.wireOp",EDGE,"E1284"),sQuery(id+"F0.wireOp",EDGE,"E1285"),sQuery(id+"F0.wireOp",EDGE,"E1286"),sQuery(id+"F0.wireOp",EDGE,"E1287"),sQuery(id+"F0.wireOp",EDGE,"E1288"),sQuery(id+"F0.wireOp",EDGE,"E1289"),sQuery(id+"F0.wireOp",EDGE,"E1290"),sQuery(id+"F0.wireOp",EDGE,"E1291"),sQuery(id+"F0.wireOp",EDGE,"E1292"),sQuery(id+"F0.wireOp",EDGE,"E1293"),sQuery(id+"F0.wireOp",EDGE,"E1294"),sQuery(id+"F0.wireOp",EDGE,"E1295"),sQuery(id+"F0.wireOp",EDGE,"E1296"),sQuery(id+"F0.wireOp",EDGE,"E1297"),sQuery(id+"F0.wireOp",EDGE,"E1298"),sQuery(id+"F0.wireOp",EDGE,"E1299"),sQuery(id+"F0.wireOp",EDGE,"E1300"),sQuery(id+"F0.wireOp",EDGE,"E1301"),sQuery(id+"F0.wireOp",EDGE,"E1302"),sQuery(id+"F0.wireOp",EDGE,"E1303"),sQuery(id+"F0.wireOp",EDGE,"E1304"),sQuery(id+"F0.wireOp",EDGE,"E1305"),sQuery(id+"F0.wireOp",EDGE,"E1306"),sQuery(id+"F0.wireOp",EDGE,"E1307"),sQuery(id+"F0.wireOp",EDGE,"E1308"),sQuery(id+"F0.wireOp",EDGE,"E1309"),sQuery(id+"F0.wireOp",EDGE,"E1310"),sQuery(id+"F0.wireOp",EDGE,"E1311"),sQuery(id+"F0.wireOp",EDGE,"E1312"),sQuery(id+"F0.wireOp",EDGE,"E1313"),sQuery(id+"F0.wireOp",EDGE,"E1314"),sQuery(id+"F0.wireOp",EDGE,"E1315"),sQuery(id+"F0.wireOp",EDGE,"E1316"),sQuery(id+"F0.wireOp",EDGE,"E1317"),sQuery(id+"F0.wireOp",EDGE,"E1318"),sQuery(id+"F0.wireOp",EDGE,"E1319"),sQuery(id+"F0.wireOp",EDGE,"E1320"),sQuery(id+"F0.wireOp",EDGE,"E1321"),sQuery(id+"F0.wireOp",EDGE,"E1322"),sQuery(id+"F0.wireOp",EDGE,"E1323"),sQuery(id+"F0.wireOp",EDGE,"E1324"),sQuery(id+"F0.wireOp",EDGE,"E1325"),sQuery(id+"F0.wireOp",EDGE,"E1326"),sQuery(id+"F0.wireOp",EDGE,"E1327"),sQuery(id+"F0.wireOp",EDGE,"E1328"),sQuery(id+"F0.wireOp",EDGE,"E1329"),sQuery(id+"F0.wireOp",EDGE,"E1330"),sQuery(id+"F0.wireOp",EDGE,"E1331"),sQuery(id+"F0.wireOp",EDGE,"E1332"),sQuery(id+"F0.wireOp",EDGE,"E1333"),sQuery(id+"F0.wireOp",EDGE,"E1334"),sQuery(id+"F0.wireOp",EDGE,"E1335"),sQuery(id+"F0.wireOp",EDGE,"E1336"),sQuery(id+"F0.wireOp",EDGE,"E1337"),sQuery(id+"F0.wireOp",EDGE,"E1338"),sQuery(id+"F0.wireOp",EDGE,"E1339"),sQuery(id+"F0.wireOp",EDGE,"E1340"),sQuery(id+"F0.wireOp",EDGE,"E1341"),sQuery(id+"F0.wireOp",EDGE,"E1342"),sQuery(id+"F0.wireOp",EDGE,"E1343"),sQuery(id+"F0.wireOp",EDGE,"E1344"),sQuery(id+"F0.wireOp",EDGE,"E1345"),sQuery(id+"F0.wireOp",EDGE,"E1346"),sQuery(id+"F0.wireOp",EDGE,"E1347"),sQuery(id+"F0.wireOp",EDGE,"E1348"),sQuery(id+"F0.wireOp",EDGE,"E1349"),sQuery(id+"F0.wireOp",EDGE,"E1350"),sQuery(id+"F0.wireOp",EDGE,"E1351"),sQuery(id+"F0.wireOp",EDGE,"E1352"),sQuery(id+"F0.wireOp",EDGE,"E1353"),sQuery(id+"F0.wireOp",EDGE,"E1354"),sQuery(id+"F0.wireOp",EDGE,"E1355"),sQuery(id+"F0.wireOp",EDGE,"E1356"),sQuery(id+"F0.wireOp",EDGE,"E1357"),sQuery(id+"F0.wireOp",EDGE,"E1358"),sQuery(id+"F0.wireOp",EDGE,"E1359"),sQuery(id+"F0.wireOp",EDGE,"E1360"),sQuery(id+"F0.wireOp",EDGE,"E1361"),sQuery(id+"F0.wireOp",EDGE,"E1362"),sQuery(id+"F0.wireOp",EDGE,"E1363"),sQuery(id+"F0.wireOp",EDGE,"E1364"),sQuery(id+"F0.wireOp",EDGE,"E1365"),sQuery(id+"F0.wireOp",EDGE,"E1366"),sQuery(id+"F0.wireOp",EDGE,"E1367"),sQuery(id+"F0.wireOp",EDGE,"E1368"),sQuery(id+"F0.wireOp",EDGE,"E1369"),sQuery(id+"F0.wireOp",EDGE,"E1370"),sQuery(id+"F0.wireOp",EDGE,"E1371"),sQuery(id+"F0.wireOp",EDGE,"E1372"),sQuery(id+"F0.wireOp",EDGE,"E1373"),sQuery(id+"F0.wireOp",EDGE,"E1374"),sQuery(id+"F0.wireOp",EDGE,"E1375"),sQuery(id+"F0.wireOp",EDGE,"E1376"),sQuery(id+"F0.wireOp",EDGE,"E1377"),sQuery(id+"F0.wireOp",EDGE,"E1378"),sQuery(id+"F0.wireOp",EDGE,"E1379"),sQuery(id+"F0.wireOp",EDGE,"E1380"),sQuery(id+"F0.wireOp",EDGE,"E1381"),sQuery(id+"F0.wireOp",EDGE,"E1382"),sQuery(id+"F0.wireOp",EDGE,"E1383"),sQuery(id+"F0.wireOp",EDGE,"E1384"),sQuery(id+"F0.wireOp",EDGE,"E1385"),sQuery(id+"F0.wireOp",EDGE,"E1386"),sQuery(id+"F0.wireOp",EDGE,"E1387"),sQuery(id+"F0.wireOp",EDGE,"E1388"),sQuery(id+"F0.wireOp",EDGE,"E1389"),sQuery(id+"F0.wireOp",EDGE,"E1390"),sQuery(id+"F0.wireOp",EDGE,"E1391"),sQuery(id+"F0.wireOp",EDGE,"E1392"),sQuery(id+"F0.wireOp",EDGE,"E1393"),sQuery(id+"F0.wireOp",EDGE,"E1394"),sQuery(id+"F0.wireOp",EDGE,"E1395"),sQuery(id+"F0.wireOp",EDGE,"E1396"),sQuery(id+"F0.wireOp",EDGE,"E1397"),sQuery(id+"F0.wireOp",EDGE,"E1398"),sQuery(id+"F0.wireOp",EDGE,"E1399"),sQuery(id+"F0.wireOp",EDGE,"E1400"),sQuery(id+"F0.wireOp",EDGE,"E1401"),sQuery(id+"F0.wireOp",EDGE,"E1402"),sQuery(id+"F0.wireOp",EDGE,"E1403"),sQuery(id+"F0.wireOp",EDGE,"E1404"),sQuery(id+"F0.wireOp",EDGE,"E1405"),sQuery(id+"F0.wireOp",EDGE,"E1406"),sQuery(id+"F0.wireOp",EDGE,"E1407"),sQuery(id+"F0.wireOp",EDGE,"E1408"),sQuery(id+"F0.wireOp",EDGE,"E1409"),sQuery(id+"F0.wireOp",EDGE,"E1410"),sQuery(id+"F0.wireOp",EDGE,"E1411"),sQuery(id+"F0.wireOp",EDGE,"E1412"),sQuery(id+"F0.wireOp",EDGE,"E1413"),sQuery(id+"F0.wireOp",EDGE,"E1414"),sQuery(id+"F0.wireOp",EDGE,"E1415"),sQuery(id+"F0.wireOp",EDGE,"E1416"),sQuery(id+"F0.wireOp",EDGE,"E1417"),sQuery(id+"F0.wireOp",EDGE,"E1418"),sQuery(id+"F0.wireOp",EDGE,"E1419"),sQuery(id+"F0.wireOp",EDGE,"E1420"),sQuery(id+"F0.wireOp",EDGE,"E1421"),sQuery(id+"F0.wireOp",EDGE,"E1422"),sQuery(id+"F0.wireOp",EDGE,"E1423"),sQuery(id+"F0.wireOp",EDGE,"E1424"),sQuery(id+"F0.wireOp",EDGE,"E1425"),sQuery(id+"F0.wireOp",EDGE,"E1426"),sQuery(id+"F0.wireOp",EDGE,"E1427"),sQuery(id+"F0.wireOp",EDGE,"E1428"),sQuery(id+"F0.wireOp",EDGE,"E1429"),sQuery(id+"F0.wireOp",EDGE,"E1430"),sQuery(id+"F0.wireOp",EDGE,"E1431"),sQuery(id+"F0.wireOp",EDGE,"E1432"),sQuery(id+"F0.wireOp",EDGE,"E1433"),sQuery(id+"F0.wireOp",EDGE,"E1434"),sQuery(id+"F0.wireOp",EDGE,"E1435"),sQuery(id+"F0.wireOp",EDGE,"E1436"),sQuery(id+"F0.wireOp",EDGE,"E1437"),sQuery(id+"F0.wireOp",EDGE,"E1438"),sQuery(id+"F0.wireOp",EDGE,"E1439"),sQuery(id+"F0.wireOp",EDGE,"E1440"),sQuery(id+"F0.wireOp",EDGE,"E1441"),sQuery(id+"F0.wireOp",EDGE,"E1442"),sQuery(id+"F0.wireOp",EDGE,"E1443"),sQuery(id+"F0.wireOp",EDGE,"E1444"),sQuery(id+"F0.wireOp",EDGE,"E1445"),sQuery(id+"F0.wireOp",EDGE,"E1446"),sQuery(id+"F0.wireOp",EDGE,"E1447"),sQuery(id+"F0.wireOp",EDGE,"E1448"),sQuery(id+"F0.wireOp",EDGE,"E1449"),sQuery(id+"F0.wireOp",EDGE,"E1450"),sQuery(id+"F0.wireOp",EDGE,"E1451"),sQuery(id+"F0.wireOp",EDGE,"E1452"),sQuery(id+"F0.wireOp",EDGE,"E1453"),sQuery(id+"F0.wireOp",EDGE,"E1454"),sQuery(id+"F0.wireOp",EDGE,"E1455"),sQuery(id+"F0.wireOp",EDGE,"E1456"),sQuery(id+"F0.wireOp",EDGE,"E1457"),sQuery(id+"F0.wireOp",EDGE,"E1458"),sQuery(id+"F0.wireOp",EDGE,"E1459"),sQuery(id+"F0.wireOp",EDGE,"E1460"),sQuery(id+"F0.wireOp",EDGE,"E1461"),sQuery(id+"F0.wireOp",EDGE,"E1462"),sQuery(id+"F0.wireOp",EDGE,"E1463"),sQuery(id+"F0.wireOp",EDGE,"E1464"),sQuery(id+"F0.wireOp",EDGE,"E1465"),sQuery(id+"F0.wireOp",EDGE,"E1466"),sQuery(id+"F0.wireOp",EDGE,"E1467"),sQuery(id+"F0.wireOp",EDGE,"E1468"),sQuery(id+"F0.wireOp",EDGE,"E1469"),sQuery(id+"F0.wireOp",EDGE,"E1470"),sQuery(id+"F0.wireOp",EDGE,"E1471"),sQuery(id+"F0.wireOp",EDGE,"E1472"),sQuery(id+"F0.wireOp",EDGE,"E1473"),sQuery(id+"F0.wireOp",EDGE,"E1474"),sQuery(id+"F0.wireOp",EDGE,"E1475"),sQuery(id+"F0.wireOp",EDGE,"E1476"),sQuery(id+"F0.wireOp",EDGE,"E1477"),sQuery(id+"F0.wireOp",EDGE,"E1478"),sQuery(id+"F0.wireOp",EDGE,"E1479"),sQuery(id+"F0.wireOp",EDGE,"E1480"),sQuery(id+"F0.wireOp",EDGE,"E1481"),sQuery(id+"F0.wireOp",EDGE,"E1482"),sQuery(id+"F0.wireOp",EDGE,"E1483"),sQuery(id+"F0.wireOp",EDGE,"E1484"),sQuery(id+"F0.wireOp",EDGE,"E1485"),sQuery(id+"F0.wireOp",EDGE,"E1486"),sQuery(id+"F0.wireOp",EDGE,"E1487"),sQuery(id+"F0.wireOp",EDGE,"E1488"),sQuery(id+"F0.wireOp",EDGE,"E1489"),sQuery(id+"F0.wireOp",EDGE,"E1490"),sQuery(id+"F0.wireOp",EDGE,"E1491"),sQuery(id+"F0.wireOp",EDGE,"E1492"),sQuery(id+"F0.wireOp",EDGE,"E1493"),sQuery(id+"F0.wireOp",EDGE,"E1494"),sQuery(id+"F0.wireOp",EDGE,"E1495"),sQuery(id+"F0.wireOp",EDGE,"E1496"),sQuery(id+"F0.wireOp",EDGE,"E1497"),sQuery(id+"F0.wireOp",EDGE,"E1498"),sQuery(id+"F0.wireOp",EDGE,"E1499"),sQuery(id+"F0.wireOp",EDGE,"E1500"),sQuery(id+"F0.wireOp",EDGE,"E1501"),sQuery(id+"F0.wireOp",EDGE,"E1502"),sQuery(id+"F0.wireOp",EDGE,"E1503"),sQuery(id+"F0.wireOp",EDGE,"E1504"),sQuery(id+"F0.wireOp",EDGE,"E1505"),sQuery(id+"F0.wireOp",EDGE,"E1506"),sQuery(id+"F0.wireOp",EDGE,"E1507"),sQuery(id+"F0.wireOp",EDGE,"E1508"),sQuery(id+"F0.wireOp",EDGE,"E1509"),sQuery(id+"F0.wireOp",EDGE,"E1510"),sQuery(id+"F0.wireOp",EDGE,"E1511"),sQuery(id+"F0.wireOp",EDGE,"E1512"),sQuery(id+"F0.wireOp",EDGE,"E1513"),sQuery(id+"F0.wireOp",EDGE,"E1514"),sQuery(id+"F0.wireOp",EDGE,"E1515"),sQuery(id+"F0.wireOp",EDGE,"E1516"),sQuery(id+"F0.wireOp",EDGE,"E1517"),sQuery(id+"F0.wireOp",EDGE,"E1518"),sQuery(id+"F0.wireOp",EDGE,"E1519"),sQuery(id+"F0.wireOp",EDGE,"E1520"),sQuery(id+"F0.wireOp",EDGE,"E1521"),sQuery(id+"F0.wireOp",EDGE,"E1522"),sQuery(id+"F0.wireOp",EDGE,"E1523"),sQuery(id+"F0.wireOp",EDGE,"E1524"),sQuery(id+"F0.wireOp",EDGE,"E1525"),sQuery(id+"F0.wireOp",EDGE,"E1526"),sQuery(id+"F0.wireOp",EDGE,"E1527"),sQuery(id+"F0.wireOp",EDGE,"E1528"),sQuery(id+"F0.wireOp",EDGE,"E1529"),sQuery(id+"F0.wireOp",EDGE,"E1530"),sQuery(id+"F0.wireOp",EDGE,"E1531"),sQuery(id+"F0.wireOp",EDGE,"E1532"),sQuery(id+"F0.wireOp",EDGE,"E1533"),sQuery(id+"F0.wireOp",EDGE,"E1534"),sQuery(id+"F0.wireOp",EDGE,"E1535"),sQuery(id+"F0.wireOp",EDGE,"E1536"),sQuery(id+"F0.wireOp",EDGE,"E1537"),sQuery(id+"F0.wireOp",EDGE,"E1538"),sQuery(id+"F0.wireOp",EDGE,"E1539"),sQuery(id+"F0.wireOp",EDGE,"E1540"),sQuery(id+"F0.wireOp",EDGE,"E1541"),sQuery(id+"F0.wireOp",EDGE,"E1542"),sQuery(id+"F0.wireOp",EDGE,"E1543"),sQuery(id+"F0.wireOp",EDGE,"E1544"),sQuery(id+"F0.wireOp",EDGE,"E1545"),sQuery(id+"F0.wireOp",EDGE,"E1546"),sQuery(id+"F0.wireOp",EDGE,"E1547"),sQuery(id+"F0.wireOp",EDGE,"E1548"),sQuery(id+"F0.wireOp",EDGE,"E1549"),sQuery(id+"F0.wireOp",EDGE,"E1550"),sQuery(id+"F0.wireOp",EDGE,"E1551"),sQuery(id+"F0.wireOp",EDGE,"E1552"),sQuery(id+"F0.wireOp",EDGE,"E1553"),sQuery(id+"F0.wireOp",EDGE,"E1554"),sQuery(id+"F0.wireOp",EDGE,"E1555"),sQuery(id+"F0.wireOp",EDGE,"E1556"),sQuery(id+"F0.wireOp",EDGE,"E1557"),sQuery(id+"F0.wireOp",EDGE,"E1558"),sQuery(id+"F0.wireOp",EDGE,"E1559"),sQuery(id+"F0.wireOp",EDGE,"E1560"),sQuery(id+"F0.wireOp",EDGE,"E1561"),sQuery(id+"F0.wireOp",EDGE,"E1562"),sQuery(id+"F0.wireOp",EDGE,"E1563"),sQuery(id+"F0.wireOp",EDGE,"E1564"),sQuery(id+"F0.wireOp",EDGE,"E1565"),sQuery(id+"F0.wireOp",EDGE,"E1566"),sQuery(id+"F0.wireOp",EDGE,"E1567"),sQuery(id+"F0.wireOp",EDGE,"E1568"),sQuery(id+"F0.wireOp",EDGE,"E1569"),sQuery(id+"F0.wireOp",EDGE,"E1570"),sQuery(id+"F0.wireOp",EDGE,"E1571"),sQuery(id+"F0.wireOp",EDGE,"E1572"),sQuery(id+"F0.wireOp",EDGE,"E1573"),sQuery(id+"F0.wireOp",EDGE,"E1574"),sQuery(id+"F0.wireOp",EDGE,"E1575"),sQuery(id+"F0.wireOp",EDGE,"E1576"),sQuery(id+"F0.wireOp",EDGE,"E1577"),sQuery(id+"F0.wireOp",EDGE,"E1578"),sQuery(id+"F0.wireOp",EDGE,"E1579"),sQuery(id+"F0.wireOp",EDGE,"E1580"),sQuery(id+"F0.wireOp",EDGE,"E1581"),sQuery(id+"F0.wireOp",EDGE,"E1582"),sQuery(id+"F0.wireOp",EDGE,"E1583"),sQuery(id+"F0.wireOp",EDGE,"E1584"),sQuery(id+"F0.wireOp",EDGE,"E1585"),sQuery(id+"F0.wireOp",EDGE,"E1586"),sQuery(id+"F0.wireOp",EDGE,"E1587"),sQuery(id+"F0.wireOp",EDGE,"E1588"),sQuery(id+"F0.wireOp",EDGE,"E1589"),sQuery(id+"F0.wireOp",EDGE,"E1590"),sQuery(id+"F0.wireOp",EDGE,"E1591"),sQuery(id+"F0.wireOp",EDGE,"E1592"),sQuery(id+"F0.wireOp",EDGE,"E1593"),sQuery(id+"F0.wireOp",EDGE,"E1594"),sQuery(id+"F0.wireOp",EDGE,"E1595"),sQuery(id+"F0.wireOp",EDGE,"E1596"),sQuery(id+"F0.wireOp",EDGE,"E1597"),sQuery(id+"F0.wireOp",EDGE,"E1598"),sQuery(id+"F0.wireOp",EDGE,"E1599"),sQuery(id+"F0.wireOp",EDGE,"E1600"),sQuery(id+"F0.wireOp",EDGE,"E1601"),sQuery(id+"F0.wireOp",EDGE,"E1602"),sQuery(id+"F0.wireOp",EDGE,"E1603"),sQuery(id+"F0.wireOp",EDGE,"E1604"),sQuery(id+"F0.wireOp",EDGE,"E1605"),sQuery(id+"F0.wireOp",EDGE,"E1606"),sQuery(id+"F0.wireOp",EDGE,"E1607"),sQuery(id+"F0.wireOp",EDGE,"E1608"),sQuery(id+"F0.wireOp",EDGE,"E1609"),sQuery(id+"F0.wireOp",EDGE,"E1610"),sQuery(id+"F0.wireOp",EDGE,"E1611"),sQuery(id+"F0.wireOp",EDGE,"E1612"),sQuery(id+"F0.wireOp",EDGE,"E1613"),sQuery(id+"F0.wireOp",EDGE,"E1614"),sQuery(id+"F0.wireOp",EDGE,"E1615"),sQuery(id+"F0.wireOp",EDGE,"E1616"),sQuery(id+"F0.wireOp",EDGE,"E1617"),sQuery(id+"F0.wireOp",EDGE,"E1618"),sQuery(id+"F0.wireOp",EDGE,"E1619"),sQuery(id+"F0.wireOp",EDGE,"E1620"),sQuery(id+"F0.wireOp",EDGE,"E1621"),sQuery(id+"F0.wireOp",EDGE,"E1622"),sQuery(id+"F0.wireOp",EDGE,"E1623"),sQuery(id+"F0.wireOp",EDGE,"E1624"),sQuery(id+"F0.wireOp",EDGE,"E1625"),sQuery(id+"F0.wireOp",EDGE,"E1626"),sQuery(id+"F0.wireOp",EDGE,"E1627"),sQuery(id+"F0.wireOp",EDGE,"E1628"),sQuery(id+"F0.wireOp",EDGE,"E1629"),sQuery(id+"F0.wireOp",EDGE,"E1630"),sQuery(id+"F0.wireOp",EDGE,"E1631"),sQuery(id+"F0.wireOp",EDGE,"E1632"),sQuery(id+"F0.wireOp",EDGE,"E1633"),sQuery(id+"F0.wireOp",EDGE,"E1634"),sQuery(id+"F0.wireOp",EDGE,"E1635"),sQuery(id+"F0.wireOp",EDGE,"E1636"),sQuery(id+"F0.wireOp",EDGE,"E1637"),sQuery(id+"F0.wireOp",EDGE,"E1638"),sQuery(id+"F0.wireOp",EDGE,"E1639"),sQuery(id+"F0.wireOp",EDGE,"E1640"),sQuery(id+"F0.wireOp",EDGE,"E1641"),sQuery(id+"F0.wireOp",EDGE,"E1642"),sQuery(id+"F0.wireOp",EDGE,"E1643"),sQuery(id+"F0.wireOp",EDGE,"E1644"),sQuery(id+"F0.wireOp",EDGE,"E1645"),sQuery(id+"F0.wireOp",EDGE,"E1646"),sQuery(id+"F0.wireOp",EDGE,"E1647"),sQuery(id+"F0.wireOp",EDGE,"E1648"),sQuery(id+"F0.wireOp",EDGE,"E1649"),sQuery(id+"F0.wireOp",EDGE,"E1650"),sQuery(id+"F0.wireOp",EDGE,"E1651"),sQuery(id+"F0.wireOp",EDGE,"E1652"),sQuery(id+"F0.wireOp",EDGE,"E1653"),sQuery(id+"F0.wireOp",EDGE,"E1654"),sQuery(id+"F0.wireOp",EDGE,"E1655"),sQuery(id+"F0.wireOp",EDGE,"E1656"),sQuery(id+"F0.wireOp",EDGE,"E1657"),sQuery(id+"F0.wireOp",EDGE,"E1658"),sQuery(id+"F0.wireOp",EDGE,"E1659"),sQuery(id+"F0.wireOp",EDGE,"E1660"),sQuery(id+"F0.wireOp",EDGE,"E1661"),sQuery(id+"F0.wireOp",EDGE,"E1662"),sQuery(id+"F0.wireOp",EDGE,"E1663"),sQuery(id+"F0.wireOp",EDGE,"E1664"),sQuery(id+"F0.wireOp",EDGE,"E1665"),sQuery(id+"F0.wireOp",EDGE,"E1666"),sQuery(id+"F0.wireOp",EDGE,"E1667"),sQuery(id+"F0.wireOp",EDGE,"E1668"),sQuery(id+"F0.wireOp",EDGE,"E1669"),sQuery(id+"F0.wireOp",EDGE,"E1670"),sQuery(id+"F0.wireOp",EDGE,"E1671"),sQuery(id+"F0.wireOp",EDGE,"E1672"),sQuery(id+"F0.wireOp",EDGE,"E1673"),sQuery(id+"F0.wireOp",EDGE,"E1674"),sQuery(id+"F0.wireOp",EDGE,"E1675"),sQuery(id+"F0.wireOp",EDGE,"E1676"),sQuery(id+"F0.wireOp",EDGE,"E1677"),sQuery(id+"F0.wireOp",EDGE,"E1678"),sQuery(id+"F0.wireOp",EDGE,"E1679"),sQuery(id+"F0.wireOp",EDGE,"E1680"),sQuery(id+"F0.wireOp",EDGE,"E1681"),sQuery(id+"F0.wireOp",EDGE,"E1682"),sQuery(id+"F0.wireOp",EDGE,"E1683"),sQuery(id+"F0.wireOp",EDGE,"E1684"),sQuery(id+"F0.wireOp",EDGE,"E1685"),sQuery(id+"F0.wireOp",EDGE,"E1686"),sQuery(id+"F0.wireOp",EDGE,"E1687"),sQuery(id+"F0.wireOp",EDGE,"E1688"),sQuery(id+"F0.wireOp",EDGE,"E1689"),sQuery(id+"F0.wireOp",EDGE,"E1690"),sQuery(id+"F0.wireOp",EDGE,"E1691"),sQuery(id+"F0.wireOp",EDGE,"E1692"),sQuery(id+"F0.wireOp",EDGE,"E1693"),sQuery(id+"F0.wireOp",EDGE,"E1694"),sQuery(id+"F0.wireOp",EDGE,"E1695"),sQuery(id+"F0.wireOp",EDGE,"E1696"),sQuery(id+"F0.wireOp",EDGE,"E1697"),sQuery(id+"F0.wireOp",EDGE,"E1698"),sQuery(id+"F0.wireOp",EDGE,"E1699"),sQuery(id+"F0.wireOp",EDGE,"E1700"),sQuery(id+"F0.wireOp",EDGE,"E1701"),sQuery(id+"F0.wireOp",EDGE,"E1702"),sQuery(id+"F0.wireOp",EDGE,"E1703"),sQuery(id+"F0.wireOp",EDGE,"E1704"),sQuery(id+"F0.wireOp",EDGE,"E1705"),sQuery(id+"F0.wireOp",EDGE,"E1706"),sQuery(id+"F0.wireOp",EDGE,"E1707"),sQuery(id+"F0.wireOp",EDGE,"E1708"),sQuery(id+"F0.wireOp",EDGE,"E1709"),sQuery(id+"F0.wireOp",EDGE,"E1710"),sQuery(id+"F0.wireOp",EDGE,"E1711"),sQuery(id+"F0.wireOp",EDGE,"E1712"),sQuery(id+"F0.wireOp",EDGE,"E1713"),sQuery(id+"F0.wireOp",EDGE,"E1714"),sQuery(id+"F0.wireOp",EDGE,"E1715"),sQuery(id+"F0.wireOp",EDGE,"E1716"),sQuery(id+"F0.wireOp",EDGE,"E1717"),sQuery(id+"F0.wireOp",EDGE,"E1718"),sQuery(id+"F0.wireOp",EDGE,"E1719"),sQuery(id+"F0.wireOp",EDGE,"E1720"),sQuery(id+"F0.wireOp",EDGE,"E1721"),sQuery(id+"F0.wireOp",EDGE,"E1722"),sQuery(id+"F0.wireOp",EDGE,"E1723"),sQuery(id+"F0.wireOp",EDGE,"E1724"),sQuery(id+"F0.wireOp",EDGE,"E1725"),sQuery(id+"F0.wireOp",EDGE,"E1726"),sQuery(id+"F0.wireOp",EDGE,"E1727"),sQuery(id+"F0.wireOp",EDGE,"E1728"),sQuery(id+"F0.wireOp",EDGE,"E1729"),sQuery(id+"F0.wireOp",EDGE,"E1730"),sQuery(id+"F0.wireOp",EDGE,"E1731"),sQuery(id+"F0.wireOp",EDGE,"E1732"),sQuery(id+"F0.wireOp",EDGE,"E1733"),sQuery(id+"F0.wireOp",EDGE,"E1734"),sQuery(id+"F0.wireOp",EDGE,"E1735"),sQuery(id+"F0.wireOp",EDGE,"E1736"),sQuery(id+"F0.wireOp",EDGE,"E1737"),sQuery(id+"F0.wireOp",EDGE,"E1738"),sQuery(id+"F0.wireOp",EDGE,"E1739"),sQuery(id+"F0.wireOp",EDGE,"E1740"),sQuery(id+"F0.wireOp",EDGE,"E1741"),sQuery(id+"F0.wireOp",EDGE,"E1742"),sQuery(id+"F0.wireOp",EDGE,"E1743"),sQuery(id+"F0.wireOp",EDGE,"E1744"),sQuery(id+"F0.wireOp",EDGE,"E1745"),sQuery(id+"F0.wireOp",EDGE,"E1746"),sQuery(id+"F0.wireOp",EDGE,"E1747"),sQuery(id+"F0.wireOp",EDGE,"E1748"),sQuery(id+"F0.wireOp",EDGE,"E1749"),sQuery(id+"F0.wireOp",EDGE,"E1750"),sQuery(id+"F0.wireOp",EDGE,"E1751"),sQuery(id+"F0.wireOp",EDGE,"E1752"),sQuery(id+"F0.wireOp",EDGE,"E1753"),sQuery(id+"F0.wireOp",EDGE,"E1754"),sQuery(id+"F0.wireOp",EDGE,"E1755"),sQuery(id+"F0.wireOp",EDGE,"E1756"),sQuery(id+"F0.wireOp",EDGE,"E1757"),sQuery(id+"F0.wireOp",EDGE,"E1758"),sQuery(id+"F0.wireOp",EDGE,"E1759"),sQuery(id+"F0.wireOp",EDGE,"E1760"),sQuery(id+"F0.wireOp",EDGE,"E1761"),sQuery(id+"F0.wireOp",EDGE,"E1762"),sQuery(id+"F0.wireOp",EDGE,"E1763"),sQuery(id+"F0.wireOp",EDGE,"E1764"),sQuery(id+"F0.wireOp",EDGE,"E1765"),sQuery(id+"F0.wireOp",EDGE,"E1766"),sQuery(id+"F0.wireOp",EDGE,"E1767"),sQuery(id+"F0.wireOp",EDGE,"E1768"),sQuery(id+"F0.wireOp",EDGE,"E1769"),sQuery(id+"F0.wireOp",EDGE,"E1770"),sQuery(id+"F0.wireOp",EDGE,"E1771"),sQuery(id+"F0.wireOp",EDGE,"E1772"),sQuery(id+"F0.wireOp",EDGE,"E1773"),sQuery(id+"F0.wireOp",EDGE,"E1774"),sQuery(id+"F0.wireOp",EDGE,"E1775"),sQuery(id+"F0.wireOp",EDGE,"E1776"),sQuery(id+"F0.wireOp",EDGE,"E1777"),sQuery(id+"F0.wireOp",EDGE,"E1778"),sQuery(id+"F0.wireOp",EDGE,"E1779"),sQuery(id+"F0.wireOp",EDGE,"E1780"),sQuery(id+"F0.wireOp",EDGE,"E1781"),sQuery(id+"F0.wireOp",EDGE,"E1782"),sQuery(id+"F0.wireOp",EDGE,"E1783"),sQuery(id+"F0.wireOp",EDGE,"E1784"),sQuery(id+"F0.wireOp",EDGE,"E1785"),sQuery(id+"F0.wireOp",EDGE,"E1786"),sQuery(id+"F0.wireOp",EDGE,"E1787"),sQuery(id+"F0.wireOp",EDGE,"E1788"),sQuery(id+"F0.wireOp",EDGE,"E1789"),sQuery(id+"F0.wireOp",EDGE,"E1790"),sQuery(id+"F0.wireOp",EDGE,"E1791"),sQuery(id+"F0.wireOp",EDGE,"E1792"),sQuery(id+"F0.wireOp",EDGE,"E1793"),sQuery(id+"F0.wireOp",EDGE,"E1794"),sQuery(id+"F0.wireOp",EDGE,"E1795"),sQuery(id+"F0.wireOp",EDGE,"E1796"),sQuery(id+"F0.wireOp",EDGE,"E1797"),sQuery(id+"F0.wireOp",EDGE,"E1798"),sQuery(id+"F0.wireOp",EDGE,"E1799"),sQuery(id+"F0.wireOp",EDGE,"E1800"),sQuery(id+"F0.wireOp",EDGE,"E1801"),sQuery(id+"F0.wireOp",EDGE,"E1802"),sQuery(id+"F0.wireOp",EDGE,"E1803"),sQuery(id+"F0.wireOp",EDGE,"E1804"),sQuery(id+"F0.wireOp",EDGE,"E1805"),sQuery(id+"F0.wireOp",EDGE,"E1806"),sQuery(id+"F0.wireOp",EDGE,"E1807"),sQuery(id+"F0.wireOp",EDGE,"E1808"),sQuery(id+"F0.wireOp",EDGE,"E1809"),sQuery(id+"F0.wireOp",EDGE,"E1810"),sQuery(id+"F0.wireOp",EDGE,"E1811"),sQuery(id+"F0.wireOp",EDGE,"E1812"),sQuery(id+"F0.wireOp",EDGE,"E1813"),sQuery(id+"F0.wireOp",EDGE,"E1814"),sQuery(id+"F0.wireOp",EDGE,"E1815"),sQuery(id+"F0.wireOp",EDGE,"E1816"),sQuery(id+"F0.wireOp",EDGE,"E1817"),sQuery(id+"F0.wireOp",EDGE,"E1818"),sQuery(id+"F0.wireOp",EDGE,"E1819"),sQuery(id+"F0.wireOp",EDGE,"E1820"),sQuery(id+"F0.wireOp",EDGE,"E1821"),sQuery(id+"F0.wireOp",EDGE,"E1822"),sQuery(id+"F0.wireOp",EDGE,"E1823"),sQuery(id+"F0.wireOp",EDGE,"E1824"),sQuery(id+"F0.wireOp",EDGE,"E1825"),sQuery(id+"F0.wireOp",EDGE,"E1826"),sQuery(id+"F0.wireOp",EDGE,"E1827"),sQuery(id+"F0.wireOp",EDGE,"E1828"),sQuery(id+"F0.wireOp",EDGE,"E1829"),sQuery(id+"F0.wireOp",EDGE,"E1830"),sQuery(id+"F0.wireOp",EDGE,"E1831"),sQuery(id+"F0.wireOp",EDGE,"E1832"),sQuery(id+"F0.wireOp",EDGE,"E1833"),sQuery(id+"F0.wireOp",EDGE,"E1834"),sQuery(id+"F0.wireOp",EDGE,"E1835"),sQuery(id+"F0.wireOp",EDGE,"E1836"),sQuery(id+"F0.wireOp",EDGE,"E1837"),sQuery(id+"F0.wireOp",EDGE,"E1838"),sQuery(id+"F0.wireOp",EDGE,"E1839"),sQuery(id+"F0.wireOp",EDGE,"E1840"),sQuery(id+"F0.wireOp",EDGE,"E1841"),sQuery(id+"F0.wireOp",EDGE,"E1842"),sQuery(id+"F0.wireOp",EDGE,"E1843"),sQuery(id+"F0.wireOp",EDGE,"E1844"),sQuery(id+"F0.wireOp",EDGE,"E1845"),sQuery(id+"F0.wireOp",EDGE,"E1846"),sQuery(id+"F0.wireOp",EDGE,"E1847"),sQuery(id+"F0.wireOp",EDGE,"E1848"),sQuery(id+"F0.wireOp",EDGE,"E1849"),sQuery(id+"F0.wireOp",EDGE,"E1850"),sQuery(id+"F0.wireOp",EDGE,"E1851"),sQuery(id+"F0.wireOp",EDGE,"E1852"),sQuery(id+"F0.wireOp",EDGE,"E1853"),sQuery(id+"F0.wireOp",EDGE,"E1854"),sQuery(id+"F0.wireOp",EDGE,"E1855"),sQuery(id+"F0.wireOp",EDGE,"E1856"),sQuery(id+"F0.wireOp",EDGE,"E1857"),sQuery(id+"F0.wireOp",EDGE,"E1858"),sQuery(id+"F0.wireOp",EDGE,"E1859"),sQuery(id+"F0.wireOp",EDGE,"E1860"),sQuery(id+"F0.wireOp",EDGE,"E1861"),sQuery(id+"F0.wireOp",EDGE,"E1862"),sQuery(id+"F0.wireOp",EDGE,"E1863"),sQuery(id+"F0.wireOp",EDGE,"E1864"),sQuery(id+"F0.wireOp",EDGE,"E1865"),sQuery(id+"F0.wireOp",EDGE,"E1866"),sQuery(id+"F0.wireOp",EDGE,"E1867"),sQuery(id+"F0.wireOp",EDGE,"E1868"),sQuery(id+"F0.wireOp",EDGE,"E1869"),sQuery(id+"F0.wireOp",EDGE,"E1870"),sQuery(id+"F0.wireOp",EDGE,"E1871"),sQuery(id+"F0.wireOp",EDGE,"E1872"),sQuery(id+"F0.wireOp",EDGE,"E1873"),sQuery(id+"F0.wireOp",EDGE,"E1874"),sQuery(id+"F0.wireOp",EDGE,"E1875"),sQuery(id+"F0.wireOp",EDGE,"E1876"),sQuery(id+"F0.wireOp",EDGE,"E1877"),sQuery(id+"F0.wireOp",EDGE,"E1878"),sQuery(id+"F0.wireOp",EDGE,"E1879"),sQuery(id+"F0.wireOp",EDGE,"E1880"),sQuery(id+"F0.wireOp",EDGE,"E1881"),sQuery(id+"F0.wireOp",EDGE,"E1882"),sQuery(id+"F0.wireOp",EDGE,"E1883"),sQuery(id+"F0.wireOp",EDGE,"E1884"),sQuery(id+"F0.wireOp",EDGE,"E1885"),sQuery(id+"F0.wireOp",EDGE,"E1886"),sQuery(id+"F0.wireOp",EDGE,"E1887"),sQuery(id+"F0.wireOp",EDGE,"E1888"),sQuery(id+"F0.wireOp",EDGE,"E1889"),sQuery(id+"F0.wireOp",EDGE,"E1890"),sQuery(id+"F0.wireOp",EDGE,"E1891"),sQuery(id+"F0.wireOp",EDGE,"E1892"),sQuery(id+"F0.wireOp",EDGE,"E1893"),sQuery(id+"F0.wireOp",EDGE,"E1894"),sQuery(id+"F0.wireOp",EDGE,"E1895"),sQuery(id+"F0.wireOp",EDGE,"E1896"),sQuery(id+"F0.wireOp",EDGE,"E1897"),sQuery(id+"F0.wireOp",EDGE,"E1898"),sQuery(id+"F0.wireOp",EDGE,"E1899"),sQuery(id+"F0.wireOp",EDGE,"E1900"),sQuery(id+"F0.wireOp",EDGE,"E1901"),sQuery(id+"F0.wireOp",EDGE,"E1902"),sQuery(id+"F0.wireOp",EDGE,"E1903"),sQuery(id+"F0.wireOp",EDGE,"E1904"),sQuery(id+"F0.wireOp",EDGE,"E1905"),sQuery(id+"F0.wireOp",EDGE,"E1906"),sQuery(id+"F0.wireOp",EDGE,"E1907"),sQuery(id+"F0.wireOp",EDGE,"E1908"),sQuery(id+"F0.wireOp",EDGE,"E1909"),sQuery(id+"F0.wireOp",EDGE,"E1910"),sQuery(id+"F0.wireOp",EDGE,"E1911"),sQuery(id+"F0.wireOp",EDGE,"E1912"),sQuery(id+"F0.wireOp",EDGE,"E1913"),sQuery(id+"F0.wireOp",EDGE,"E1914"),sQuery(id+"F0.wireOp",EDGE,"E1915"),sQuery(id+"F0.wireOp",EDGE,"E1916"),sQuery(id+"F0.wireOp",EDGE,"E1917"),sQuery(id+"F0.wireOp",EDGE,"E1918"),sQuery(id+"F0.wireOp",EDGE,"E1919"),sQuery(id+"F0.wireOp",EDGE,"E1920"),sQuery(id+"F0.wireOp",EDGE,"E1921"),sQuery(id+"F0.wireOp",EDGE,"E1922"),sQuery(id+"F0.wireOp",EDGE,"E1923"),sQuery(id+"F0.wireOp",EDGE,"E1924"),sQuery(id+"F0.wireOp",EDGE,"E1925"),sQuery(id+"F0.wireOp",EDGE,"E1926"),sQuery(id+"F0.wireOp",EDGE,"E1927"),sQuery(id+"F0.wireOp",EDGE,"E1928"),sQuery(id+"F0.wireOp",EDGE,"E1929"),sQuery(id+"F0.wireOp",EDGE,"E1930"),sQuery(id+"F0.wireOp",EDGE,"E1931"),sQuery(id+"F0.wireOp",EDGE,"E1932"),sQuery(id+"F0.wireOp",EDGE,"E1933"),sQuery(id+"F0.wireOp",EDGE,"E1934"),sQuery(id+"F0.wireOp",EDGE,"E1935"),sQuery(id+"F0.wireOp",EDGE,"E1936"),sQuery(id+"F0.wireOp",EDGE,"E1937"),sQuery(id+"F0.wireOp",EDGE,"E1938"),sQuery(id+"F0.wireOp",EDGE,"E1939"),sQuery(id+"F0.wireOp",EDGE,"E1940"),sQuery(id+"F0.wireOp",EDGE,"E1941"),sQuery(id+"F0.wireOp",EDGE,"E1942"),sQuery(id+"F0.wireOp",EDGE,"E1943"),sQuery(id+"F0.wireOp",EDGE,"E1944"),sQuery(id+"F0.wireOp",EDGE,"E1945"),sQuery(id+"F0.wireOp",EDGE,"E1946"),sQuery(id+"F0.wireOp",EDGE,"E1947"),sQuery(id+"F0.wireOp",EDGE,"E1948"),sQuery(id+"F0.wireOp",EDGE,"E1949"),sQuery(id+"F0.wireOp",EDGE,"E1950"),sQuery(id+"F0.wireOp",EDGE,"E1951"),sQuery(id+"F0.wireOp",EDGE,"E1952"),sQuery(id+"F0.wireOp",EDGE,"E1953"),sQuery(id+"F0.wireOp",EDGE,"E1954"),sQuery(id+"F0.wireOp",EDGE,"E1955"),sQuery(id+"F0.wireOp",EDGE,"E1956"),sQuery(id+"F0.wireOp",EDGE,"E1957"),sQuery(id+"F0.wireOp",EDGE,"E1958"),sQuery(id+"F0.wireOp",EDGE,"E1959"),sQuery(id+"F0.wireOp",EDGE,"E1960"),sQuery(id+"F0.wireOp",EDGE,"E1961"),sQuery(id+"F0.wireOp",EDGE,"E1962"),sQuery(id+"F0.wireOp",EDGE,"E1963"),sQuery(id+"F0.wireOp",EDGE,"E1964"),sQuery(id+"F0.wireOp",EDGE,"E1965"),sQuery(id+"F0.wireOp",EDGE,"E1966"),sQuery(id+"F0.wireOp",EDGE,"E1967"),sQuery(id+"F0.wireOp",EDGE,"E1968"),sQuery(id+"F0.wireOp",EDGE,"E1969"),sQuery(id+"F0.wireOp",EDGE,"E1970"),sQuery(id+"F0.wireOp",EDGE,"E1971"),sQuery(id+"F0.wireOp",EDGE,"E1972"),sQuery(id+"F0.wireOp",EDGE,"E1973"),sQuery(id+"F0.wireOp",EDGE,"E1974"),sQuery(id+"F0.wireOp",EDGE,"E1975"),sQuery(id+"F0.wireOp",EDGE,"E1976"),sQuery(id+"F0.wireOp",EDGE,"E1977"),sQuery(id+"F0.wireOp",EDGE,"E1978"),sQuery(id+"F0.wireOp",EDGE,"E1979"),sQuery(id+"F0.wireOp",EDGE,"E1980"),sQuery(id+"F0.wireOp",EDGE,"E1981"),sQuery(id+"F0.wireOp",EDGE,"E1982"),sQuery(id+"F0.wireOp",EDGE,"E1983"),sQuery(id+"F0.wireOp",EDGE,"E1984"),sQuery(id+"F0.wireOp",EDGE,"E1985"),sQuery(id+"F0.wireOp",EDGE,"E1986"),sQuery(id+"F0.wireOp",EDGE,"E1987"),sQuery(id+"F0.wireOp",EDGE,"E1988"),sQuery(id+"F0.wireOp",EDGE,"E1989"),sQuery(id+"F0.wireOp",EDGE,"E1990"),sQuery(id+"F0.wireOp",EDGE,"E1991"),sQuery(id+"F0.wireOp",EDGE,"E1992"),sQuery(id+"F0.wireOp",EDGE,"E1993"),sQuery(id+"F0.wireOp",EDGE,"E1994"),sQuery(id+"F0.wireOp",EDGE,"E1995"),sQuery(id+"F0.wireOp",EDGE,"E1996"),sQuery(id+"F0.wireOp",EDGE,"E1997"),sQuery(id+"F0.wireOp",EDGE,"E1998"),sQuery(id+"F0.wireOp",EDGE,"E1999"),sQuery(id+"F0.wireOp",EDGE,"E2000"),sQuery(id+"F0.wireOp",EDGE,"E2001"),sQuery(id+"F0.wireOp",EDGE,"E2002"),sQuery(id+"F0.wireOp",EDGE,"E2003"),sQuery(id+"F0.wireOp",EDGE,"E2004"),sQuery(id+"F0.wireOp",EDGE,"E2005"),sQuery(id+"F0.wireOp",EDGE,"E2006"),sQuery(id+"F0.wireOp",EDGE,"E2007"),sQuery(id+"F0.wireOp",EDGE,"E2008"),sQuery(id+"F0.wireOp",EDGE,"E2009"),sQuery(id+"F0.wireOp",EDGE,"E2010"),sQuery(id+"F0.wireOp",EDGE,"E2011"),sQuery(id+"F0.wireOp",EDGE,"E2012"),sQuery(id+"F0.wireOp",EDGE,"E2013"),sQuery(id+"F0.wireOp",EDGE,"E2014"),sQuery(id+"F0.wireOp",EDGE,"E2015"),sQuery(id+"F0.wireOp",EDGE,"E2016"),sQuery(id+"F0.wireOp",EDGE,"E2017"),sQuery(id+"F0.wireOp",EDGE,"E2018"),sQuery(id+"F0.wireOp",EDGE,"E2019"),sQuery(id+"F0.wireOp",EDGE,"E2020"),sQuery(id+"F0.wireOp",EDGE,"E2021"),sQuery(id+"F0.wireOp",EDGE,"E2022"),sQuery(id+"F0.wireOp",EDGE,"E2023"),sQuery(id+"F0.wireOp",EDGE,"E2024"),sQuery(id+"F0.wireOp",EDGE,"E2025"),sQuery(id+"F0.wireOp",EDGE,"E2026"),sQuery(id+"F0.wireOp",EDGE,"E2027"),sQuery(id+"F0.wireOp",EDGE,"E2028"),sQuery(id+"F0.wireOp",EDGE,"E2029"),sQuery(id+"F0.wireOp",EDGE,"E2030"),sQuery(id+"F0.wireOp",EDGE,"E2031"),sQuery(id+"F0.wireOp",EDGE,"E2032"),sQuery(id+"F0.wireOp",EDGE,"E2033"),sQuery(id+"F0.wireOp",EDGE,"E2034"),sQuery(id+"F0.wireOp",EDGE,"E2035"),sQuery(id+"F0.wireOp",EDGE,"E2036"),sQuery(id+"F0.wireOp",EDGE,"E2037"),sQuery(id+"F0.wireOp",EDGE,"E2038"),sQuery(id+"F0.wireOp",EDGE,"E2039"),sQuery(id+"F0.wireOp",EDGE,"E2040"),sQuery(id+"F0.wireOp",EDGE,"E2041"),sQuery(id+"F0.wireOp",EDGE,"E2042"),sQuery(id+"F0.wireOp",EDGE,"E2043"),sQuery(id+"F0.wireOp",EDGE,"E2044"),sQuery(id+"F0.wireOp",EDGE,"E2045"),sQuery(id+"F0.wireOp",EDGE,"E2046"),sQuery(id+"F0.wireOp",EDGE,"E2047"),sQuery(id+"F0.wireOp",EDGE,"E2048"),sQuery(id+"F0.wireOp",EDGE,"E2049"),sQuery(id+"F0.wireOp",EDGE,"E2050"),sQuery(id+"F0.wireOp",EDGE,"E2051"),sQuery(id+"F0.wireOp",EDGE,"E2052"),sQuery(id+"F0.wireOp",EDGE,"E2053"),sQuery(id+"F0.wireOp",EDGE,"E2054"),sQuery(id+"F0.wireOp",EDGE,"E2055"),sQuery(id+"F0.wireOp",EDGE,"E2056"),sQuery(id+"F0.wireOp",EDGE,"E2057"),sQuery(id+"F0.wireOp",EDGE,"E2058"),sQuery(id+"F0.wireOp",EDGE,"E2059"),sQuery(id+"F0.wireOp",EDGE,"E2060"),sQuery(id+"F0.wireOp",EDGE,"E2061"),sQuery(id+"F0.wireOp",EDGE,"E2062"),sQuery(id+"F0.wireOp",EDGE,"E2063"),sQuery(id+"F0.wireOp",EDGE,"E2064"),sQuery(id+"F0.wireOp",EDGE,"E2065"),sQuery(id+"F0.wireOp",EDGE,"E2066"),sQuery(id+"F0.wireOp",EDGE,"E2067"),sQuery(id+"F0.wireOp",EDGE,"E2068"),sQuery(id+"F0.wireOp",EDGE,"E2069"),sQuery(id+"F0.wireOp",EDGE,"E2070"),sQuery(id+"F0.wireOp",EDGE,"E2071"),sQuery(id+"F0.wireOp",EDGE,"E2072"),sQuery(id+"F0.wireOp",EDGE,"E2073"),sQuery(id+"F0.wireOp",EDGE,"E2074"),sQuery(id+"F0.wireOp",EDGE,"E2075"),sQuery(id+"F0.wireOp",EDGE,"E2076"),sQuery(id+"F0.wireOp",EDGE,"E2077"),sQuery(id+"F0.wireOp",EDGE,"E2078"),sQuery(id+"F0.wireOp",EDGE,"E2079"),sQuery(id+"F0.wireOp",EDGE,"E2080"),sQuery(id+"F0.wireOp",EDGE,"E2081"),sQuery(id+"F0.wireOp",EDGE,"E2082"),sQuery(id+"F0.wireOp",EDGE,"E2083"),sQuery(id+"F0.wireOp",EDGE,"E2084"),sQuery(id+"F0.wireOp",EDGE,"E2085"),sQuery(id+"F0.wireOp",EDGE,"E2086"),sQuery(id+"F0.wireOp",EDGE,"E2087"),sQuery(id+"F0.wireOp",EDGE,"E2088"),sQuery(id+"F0.wireOp",EDGE,"E2089"),sQuery(id+"F0.wireOp",EDGE,"E2090"),sQuery(id+"F0.wireOp",EDGE,"E2091"),sQuery(id+"F0.wireOp",EDGE,"E2092"),sQuery(id+"F0.wireOp",EDGE,"E2093"),sQuery(id+"F0.wireOp",EDGE,"E2094"),sQuery(id+"F0.wireOp",EDGE,"E2095"),sQuery(id+"F0.wireOp",EDGE,"E2096"),sQuery(id+"F0.wireOp",EDGE,"E2097"),sQuery(id+"F0.wireOp",EDGE,"E2098"),sQuery(id+"F0.wireOp",EDGE,"E2099"),sQuery(id+"F0.wireOp",EDGE,"E2100"),sQuery(id+"F0.wireOp",EDGE,"E2101"),sQuery(id+"F0.wireOp",EDGE,"E2102"),sQuery(id+"F0.wireOp",EDGE,"E2103"),sQuery(id+"F0.wireOp",EDGE,"E2104"),sQuery(id+"F0.wireOp",EDGE,"E2105"),sQuery(id+"F0.wireOp",EDGE,"E2106"),sQuery(id+"F0.wireOp",EDGE,"E2107"),sQuery(id+"F0.wireOp",EDGE,"E2108"),sQuery(id+"F0.wireOp",EDGE,"E2109"),sQuery(id+"F0.wireOp",EDGE,"E2110"),sQuery(id+"F0.wireOp",EDGE,"E2111"),sQuery(id+"F0.wireOp",EDGE,"E2112"),sQuery(id+"F0.wireOp",EDGE,"E2113"),sQuery(id+"F0.wireOp",EDGE,"E2114"),sQuery(id+"F0.wireOp",EDGE,"E2115"),sQuery(id+"F0.wireOp",EDGE,"E2116"),sQuery(id+"F0.wireOp",EDGE,"E2117"),sQuery(id+"F0.wireOp",EDGE,"E2118"),sQuery(id+"F0.wireOp",EDGE,"E2119"),sQuery(id+"F0.wireOp",EDGE,"E2120"),sQuery(id+"F0.wireOp",EDGE,"E2121"),sQuery(id+"F0.wireOp",EDGE,"E2122"),sQuery(id+"F0.wireOp",EDGE,"E2123"),sQuery(id+"F0.wireOp",EDGE,"E2124"),sQuery(id+"F0.wireOp",EDGE,"E2125"),sQuery(id+"F0.wireOp",EDGE,"E2126"),sQuery(id+"F0.wireOp",EDGE,"E2127"),sQuery(id+"F0.wireOp",EDGE,"E2128"),sQuery(id+"F0.wireOp",EDGE,"E2129"),sQuery(id+"F0.wireOp",EDGE,"E2130"),sQuery(id+"F0.wireOp",EDGE,"E2131"),sQuery(id+"F0.wireOp",EDGE,"E2132"),sQuery(id+"F0.wireOp",EDGE,"E2133"),sQuery(id+"F0.wireOp",EDGE,"E2134"),sQuery(id+"F0.wireOp",EDGE,"E2135"),sQuery(id+"F0.wireOp",EDGE,"E2136"),sQuery(id+"F0.wireOp",EDGE,"E2137"),sQuery(id+"F0.wireOp",EDGE,"E2138"),sQuery(id+"F0.wireOp",EDGE,"E2139"),sQuery(id+"F0.wireOp",EDGE,"E2140"),sQuery(id+"F0.wireOp",EDGE,"E2141"),sQuery(id+"F0.wireOp",EDGE,"E2142"),sQuery(id+"F0.wireOp",EDGE,"E2143"),sQuery(id+"F0.wireOp",EDGE,"E2144"),sQuery(id+"F0.wireOp",EDGE,"E2145"),sQuery(id+"F0.wireOp",EDGE,"E2146"),sQuery(id+"F0.wireOp",EDGE,"E2147"),sQuery(id+"F0.wireOp",EDGE,"E2148"),sQuery(id+"F0.wireOp",EDGE,"E2149"),sQuery(id+"F0.wireOp",EDGE,"E2150"),sQuery(id+"F0.wireOp",EDGE,"E2151"),sQuery(id+"F0.wireOp",EDGE,"E2152"),sQuery(id+"F0.wireOp",EDGE,"E2153"),sQuery(id+"F0.wireOp",EDGE,"E2154"),sQuery(id+"F0.wireOp",EDGE,"E2155"),sQuery(id+"F0.wireOp",EDGE,"E2156"),sQuery(id+"F0.wireOp",EDGE,"E2157"),sQuery(id+"F0.wireOp",EDGE,"E2158"),sQuery(id+"F0.wireOp",EDGE,"E2159"),sQuery(id+"F0.wireOp",EDGE,"E2160"),sQuery(id+"F0.wireOp",EDGE,"E2161"),sQuery(id+"F0.wireOp",EDGE,"E2162"),sQuery(id+"F0.wireOp",EDGE,"E2163"),sQuery(id+"F0.wireOp",EDGE,"E2164"),sQuery(id+"F0.wireOp",EDGE,"E2165"),sQuery(id+"F0.wireOp",EDGE,"E2166"),sQuery(id+"F0.wireOp",EDGE,"E2167"),sQuery(id+"F0.wireOp",EDGE,"E2168"),sQuery(id+"F0.wireOp",EDGE,"E2169"),sQuery(id+"F0.wireOp",EDGE,"E2170"),sQuery(id+"F0.wireOp",EDGE,"E2171"),sQuery(id+"F0.wireOp",EDGE,"E2172"),sQuery(id+"F0.wireOp",EDGE,"E2173"),sQuery(id+"F0.wireOp",EDGE,"E2174"),sQuery(id+"F0.wireOp",EDGE,"E2175"),sQuery(id+"F0.wireOp",EDGE,"E2176"),sQuery(id+"F0.wireOp",EDGE,"E2177"),sQuery(id+"F0.wireOp",EDGE,"E2178"),sQuery(id+"F0.wireOp",EDGE,"E2179"),sQuery(id+"F0.wireOp",EDGE,"E2180"),sQuery(id+"F0.wireOp",EDGE,"E2181"),sQuery(id+"F0.wireOp",EDGE,"E2182"),sQuery(id+"F0.wireOp",EDGE,"E2183"),sQuery(id+"F0.wireOp",EDGE,"E2184"),sQuery(id+"F0.wireOp",EDGE,"E2185"),sQuery(id+"F0.wireOp",EDGE,"E2186"),sQuery(id+"F0.wireOp",EDGE,"E2187"),sQuery(id+"F0.wireOp",EDGE,"E2188"),sQuery(id+"F0.wireOp",EDGE,"E2189"),sQuery(id+"F0.wireOp",EDGE,"E2190"),sQuery(id+"F0.wireOp",EDGE,"E2191"),sQuery(id+"F0.wireOp",EDGE,"E2192"),sQuery(id+"F0.wireOp",EDGE,"E2193"),sQuery(id+"F0.wireOp",EDGE,"E2194"),sQuery(id+"F0.wireOp",EDGE,"E2195"),sQuery(id+"F0.wireOp",EDGE,"E2196"),sQuery(id+"F0.wireOp",EDGE,"E2197"),sQuery(id+"F0.wireOp",EDGE,"E2198"),sQuery(id+"F0.wireOp",EDGE,"E2199"),sQuery(id+"F0.wireOp",EDGE,"E2200"),sQuery(id+"F0.wireOp",EDGE,"E2201"),sQuery(id+"F0.wireOp",EDGE,"E2202"),sQuery(id+"F0.wireOp",EDGE,"E2203"),sQuery(id+"F0.wireOp",EDGE,"E2204"),sQuery(id+"F0.wireOp",EDGE,"E2205"),sQuery(id+"F0.wireOp",EDGE,"E2206"),sQuery(id+"F0.wireOp",EDGE,"E2207"),sQuery(id+"F0.wireOp",EDGE,"E2208"),sQuery(id+"F0.wireOp",EDGE,"E2209"),sQuery(id+"F0.wireOp",EDGE,"E2210"),sQuery(id+"F0.wireOp",EDGE,"E2211"),sQuery(id+"F0.wireOp",EDGE,"E2212"),sQuery(id+"F0.wireOp",EDGE,"E2213"),sQuery(id+"F0.wireOp",EDGE,"E2214"),sQuery(id+"F0.wireOp",EDGE,"E2215"),sQuery(id+"F0.wireOp",EDGE,"E2216"),sQuery(id+"F0.wireOp",EDGE,"E2217"),sQuery(id+"F0.wireOp",EDGE,"E2218"),sQuery(id+"F0.wireOp",EDGE,"E2219"),sQuery(id+"F0.wireOp",EDGE,"E2220"),sQuery(id+"F0.wireOp",EDGE,"E2221"),sQuery(id+"F0.wireOp",EDGE,"E2222"),sQuery(id+"F0.wireOp",EDGE,"E2223"),sQuery(id+"F0.wireOp",EDGE,"E2224"),sQuery(id+"F0.wireOp",EDGE,"E2225"),sQuery(id+"F0.wireOp",EDGE,"E2226"),sQuery(id+"F0.wireOp",EDGE,"E2227"),sQuery(id+"F0.wireOp",EDGE,"E2228"),sQuery(id+"F0.wireOp",EDGE,"E2229"),sQuery(id+"F0.wireOp",EDGE,"E2230"),sQuery(id+"F0.wireOp",EDGE,"E2231"),sQuery(id+"F0.wireOp",EDGE,"E2232"),sQuery(id+"F0.wireOp",EDGE,"E2233"),sQuery(id+"F0.wireOp",EDGE,"E2234"),sQuery(id+"F0.wireOp",EDGE,"E2235"),sQuery(id+"F0.wireOp",EDGE,"E2236"),sQuery(id+"F0.wireOp",EDGE,"E2237"),sQuery(id+"F0.wireOp",EDGE,"E2238"),sQuery(id+"F0.wireOp",EDGE,"E2239"),sQuery(id+"F0.wireOp",EDGE,"E2240"),sQuery(id+"F0.wireOp",EDGE,"E2241"),sQuery(id+"F0.wireOp",EDGE,"E2242"),sQuery(id+"F0.wireOp",EDGE,"E2243"),sQuery(id+"F0.wireOp",EDGE,"E2244"),sQuery(id+"F0.wireOp",EDGE,"E2245"),sQuery(id+"F0.wireOp",EDGE,"E2246"),sQuery(id+"F0.wireOp",EDGE,"E2247"),sQuery(id+"F0.wireOp",EDGE,"E2248"),sQuery(id+"F0.wireOp",EDGE,"E2249"),sQuery(id+"F0.wireOp",EDGE,"E2250"),sQuery(id+"F0.wireOp",EDGE,"E2251"),sQuery(id+"F0.wireOp",EDGE,"E2252"),sQuery(id+"F0.wireOp",EDGE,"E2253"),sQuery(id+"F0.wireOp",EDGE,"E2254"),sQuery(id+"F0.wireOp",EDGE,"E2255"),sQuery(id+"F0.wireOp",EDGE,"E2256"),sQuery(id+"F0.wireOp",EDGE,"E2257"),sQuery(id+"F0.wireOp",EDGE,"E2258"),sQuery(id+"F0.wireOp",EDGE,"E2259"),sQuery(id+"F0.wireOp",EDGE,"E2260"),sQuery(id+"F0.wireOp",EDGE,"E2261"),sQuery(id+"F0.wireOp",EDGE,"E2262"),sQuery(id+"F0.wireOp",EDGE,"E2263"),sQuery(id+"F0.wireOp",EDGE,"E2264"),sQuery(id+"F0.wireOp",EDGE,"E2265"),sQuery(id+"F0.wireOp",EDGE,"E2266"),sQuery(id+"F0.wireOp",EDGE,"E2267"),sQuery(id+"F0.wireOp",EDGE,"E2268"),sQuery(id+"F0.wireOp",EDGE,"E2269"),sQuery(id+"F0.wireOp",EDGE,"E2270"),sQuery(id+"F0.wireOp",EDGE,"E2271"),sQuery(id+"F0.wireOp",EDGE,"E2272"),sQuery(id+"F0.wireOp",EDGE,"E2273"),sQuery(id+"F0.wireOp",EDGE,"E2274"),sQuery(id+"F0.wireOp",EDGE,"E2275"),sQuery(id+"F0.wireOp",EDGE,"E2276"),sQuery(id+"F0.wireOp",EDGE,"E2277"),sQuery(id+"F0.wireOp",EDGE,"E2278"),sQuery(id+"F0.wireOp",EDGE,"E2279"),sQuery(id+"F0.wireOp",EDGE,"E2280"),sQuery(id+"F0.wireOp",EDGE,"E2281"),sQuery(id+"F0.wireOp",EDGE,"E2282"),sQuery(id+"F0.wireOp",EDGE,"E2283"),sQuery(id+"F0.wireOp",EDGE,"E2284"),sQuery(id+"F0.wireOp",EDGE,"E2285"),sQuery(id+"F0.wireOp",EDGE,"E2286"),sQuery(id+"F0.wireOp",EDGE,"E2287"),sQuery(id+"F0.wireOp",EDGE,"E2288"),sQuery(id+"F0.wireOp",EDGE,"E2289"),sQuery(id+"F0.wireOp",EDGE,"E2290"),sQuery(id+"F0.wireOp",EDGE,"E2291"),sQuery(id+"F0.wireOp",EDGE,"E2292"),sQuery(id+"F0.wireOp",EDGE,"E2293"),sQuery(id+"F0.wireOp",EDGE,"E2294"),sQuery(id+"F0.wireOp",EDGE,"E2295"),sQuery(id+"F0.wireOp",EDGE,"E2296"),sQuery(id+"F0.wireOp",EDGE,"E2297"),sQuery(id+"F0.wireOp",EDGE,"E2298"),sQuery(id+"F0.wireOp",EDGE,"E2299"),sQuery(id+"F0.wireOp",EDGE,"E2300"),sQuery(id+"F0.wireOp",EDGE,"E2301"),sQuery(id+"F0.wireOp",EDGE,"E2302"),sQuery(id+"F0.wireOp",EDGE,"E2303"),sQuery(id+"F0.wireOp",EDGE,"E2304"),sQuery(id+"F0.wireOp",EDGE,"E2305"),sQuery(id+"F0.wireOp",EDGE,"E2306"),sQuery(id+"F0.wireOp",EDGE,"E2307"),sQuery(id+"F0.wireOp",EDGE,"E2308"),sQuery(id+"F0.wireOp",EDGE,"E2309"),sQuery(id+"F0.wireOp",EDGE,"E2310"),sQuery(id+"F0.wireOp",EDGE,"E2311"),sQuery(id+"F0.wireOp",EDGE,"E2312"),sQuery(id+"F0.wireOp",EDGE,"E2313"),sQuery(id+"F0.wireOp",EDGE,"E2314"),sQuery(id+"F0.wireOp",EDGE,"E2315"),sQuery(id+"F0.wireOp",EDGE,"E2316"),sQuery(id+"F0.wireOp",EDGE,"E2317"),sQuery(id+"F0.wireOp",EDGE,"E2318"),sQuery(id+"F0.wireOp",EDGE,"E2319"),sQuery(id+"F0.wireOp",EDGE,"E2320"),sQuery(id+"F0.wireOp",EDGE,"E2321"),sQuery(id+"F0.wireOp",EDGE,"E2322"),sQuery(id+"F0.wireOp",EDGE,"E2323"),sQuery(id+"F0.wireOp",EDGE,"E2324"),sQuery(id+"F0.wireOp",EDGE,"E2325"),sQuery(id+"F0.wireOp",EDGE,"E2326"),sQuery(id+"F0.wireOp",EDGE,"E2327"),sQuery(id+"F0.wireOp",EDGE,"E2328"),sQuery(id+"F0.wireOp",EDGE,"E2329"),sQuery(id+"F0.wireOp",EDGE,"E2330"),sQuery(id+"F0.wireOp",EDGE,"E2331"),sQuery(id+"F0.wireOp",EDGE,"E2332"),sQuery(id+"F0.wireOp",EDGE,"E2333"),sQuery(id+"F0.wireOp",EDGE,"E2334"),sQuery(id+"F0.wireOp",EDGE,"E2335"),sQuery(id+"F0.wireOp",EDGE,"E2336"),sQuery(id+"F0.wireOp",EDGE,"E2337"),sQuery(id+"F0.wireOp",EDGE,"E2338"),sQuery(id+"F0.wireOp",EDGE,"E2339"),sQuery(id+"F0.wireOp",EDGE,"E2340"),sQuery(id+"F0.wireOp",EDGE,"E2341"),sQuery(id+"F0.wireOp",EDGE,"E2342"),sQuery(id+"F0.wireOp",EDGE,"E2343"),sQuery(id+"F0.wireOp",EDGE,"E2344"),sQuery(id+"F0.wireOp",EDGE,"E2345"),sQuery(id+"F0.wireOp",EDGE,"E2346"),sQuery(id+"F0.wireOp",EDGE,"E2347"),sQuery(id+"F0.wireOp",EDGE,"E2348"),sQuery(id+"F0.wireOp",EDGE,"E2349"),sQuery(id+"F0.wireOp",EDGE,"E2350"),sQuery(id+"F0.wireOp",EDGE,"E2351"),sQuery(id+"F0.wireOp",EDGE,"E2352"),sQuery(id+"F0.wireOp",EDGE,"E2353"),sQuery(id+"F0.wireOp",EDGE,"E2354"),sQuery(id+"F0.wireOp",EDGE,"E2355"),sQuery(id+"F0.wireOp",EDGE,"E2356"),sQuery(id+"F0.wireOp",EDGE,"E2357"),sQuery(id+"F0.wireOp",EDGE,"E2358"),sQuery(id+"F0.wireOp",EDGE,"E2359"),sQuery(id+"F0.wireOp",EDGE,"E2360"),sQuery(id+"F0.wireOp",EDGE,"E2361"),sQuery(id+"F0.wireOp",EDGE,"E2362"),sQuery(id+"F0.wireOp",EDGE,"E2363"),sQuery(id+"F0.wireOp",EDGE,"E2364"),sQuery(id+"F0.wireOp",EDGE,"E2365"),sQuery(id+"F0.wireOp",EDGE,"E2366"),sQuery(id+"F0.wireOp",EDGE,"E2367"),sQuery(id+"F0.wireOp",EDGE,"E2368"),sQuery(id+"F0.wireOp",EDGE,"E2369"),sQuery(id+"F0.wireOp",EDGE,"E2370"),sQuery(id+"F0.wireOp",EDGE,"E2371"),sQuery(id+"F0.wireOp",EDGE,"E2372"),sQuery(id+"F0.wireOp",EDGE,"E2373"),sQuery(id+"F0.wireOp",EDGE,"E2374"),sQuery(id+"F0.wireOp",EDGE,"E2375"),sQuery(id+"F0.wireOp",EDGE,"E2376"),sQuery(id+"F0.wireOp",EDGE,"E2377"),sQuery(id+"F0.wireOp",EDGE,"E2378"),sQuery(id+"F0.wireOp",EDGE,"E2379"),sQuery(id+"F0.wireOp",EDGE,"E2380"),sQuery(id+"F0.wireOp",EDGE,"E2381"),sQuery(id+"F0.wireOp",EDGE,"E2382"),sQuery(id+"F0.wireOp",EDGE,"E2383"),sQuery(id+"F0.wireOp",EDGE,"E2384"),sQuery(id+"F0.wireOp",EDGE,"E2385"),sQuery(id+"F0.wireOp",EDGE,"E2386"),sQuery(id+"F0.wireOp",EDGE,"E2387"),sQuery(id+"F0.wireOp",EDGE,"E2388"),sQuery(id+"F0.wireOp",EDGE,"E2389"),sQuery(id+"F0.wireOp",EDGE,"E2390"),sQuery(id+"F0.wireOp",EDGE,"E2391"),sQuery(id+"F0.wireOp",EDGE,"E2392"),sQuery(id+"F0.wireOp",EDGE,"E2393"),sQuery(id+"F0.wireOp",EDGE,"E2394"),sQuery(id+"F0.wireOp",EDGE,"E2395"),sQuery(id+"F0.wireOp",EDGE,"E2396"),sQuery(id+"F0.wireOp",EDGE,"E2397"),sQuery(id+"F0.wireOp",EDGE,"E2398"),sQuery(id+"F0.wireOp",EDGE,"E2399"),sQuery(id+"F0.wireOp",EDGE,"E2400"),sQuery(id+"F0.wireOp",EDGE,"E2401"),sQuery(id+"F0.wireOp",EDGE,"E2402"),sQuery(id+"F0.wireOp",EDGE,"E2403"),sQuery(id+"F0.wireOp",EDGE,"E2404"),sQuery(id+"F0.wireOp",EDGE,"E2405"),sQuery(id+"F0.wireOp",EDGE,"E2406"),sQuery(id+"F0.wireOp",EDGE,"E2407"),sQuery(id+"F0.wireOp",EDGE,"E2408"),sQuery(id+"F0.wireOp",EDGE,"E2409"),sQuery(id+"F0.wireOp",EDGE,"E2410"),sQuery(id+"F0.wireOp",EDGE,"E2411"),sQuery(id+"F0.wireOp",EDGE,"E2412"),sQuery(id+"F0.wireOp",EDGE,"E2413"),sQuery(id+"F0.wireOp",EDGE,"E2414"),sQuery(id+"F0.wireOp",EDGE,"E2415"),sQuery(id+"F0.wireOp",EDGE,"E2416"),sQuery(id+"F0.wireOp",EDGE,"E2417"),sQuery(id+"F0.wireOp",EDGE,"E2418"),sQuery(id+"F0.wireOp",EDGE,"E2419"),sQuery(id+"F0.wireOp",EDGE,"E2420"),sQuery(id+"F0.wireOp",EDGE,"E2421"),sQuery(id+"F0.wireOp",EDGE,"E2422"),sQuery(id+"F0.wireOp",EDGE,"E2423"),sQuery(id+"F0.wireOp",EDGE,"E2424"),sQuery(id+"F0.wireOp",EDGE,"E2425"),sQuery(id+"F0.wireOp",EDGE,"E2426"),sQuery(id+"F0.wireOp",EDGE,"E2427"),sQuery(id+"F0.wireOp",EDGE,"E2428"),sQuery(id+"F0.wireOp",EDGE,"E2429"),sQuery(id+"F0.wireOp",EDGE,"E2430"),sQuery(id+"F0.wireOp",EDGE,"E2431"),sQuery(id+"F0.wireOp",EDGE,"E2432"),sQuery(id+"F0.wireOp",EDGE,"E2433"),sQuery(id+"F0.wireOp",EDGE,"E2434"),sQuery(id+"F0.wireOp",EDGE,"E2435"),sQuery(id+"F0.wireOp",EDGE,"E2436"),sQuery(id+"F0.wireOp",EDGE,"E2437"),sQuery(id+"F0.wireOp",EDGE,"E2438"),sQuery(id+"F0.wireOp",EDGE,"E2439"),sQuery(id+"F0.wireOp",EDGE,"E2440"),sQuery(id+"F0.wireOp",EDGE,"E2441"),sQuery(id+"F0.wireOp",EDGE,"E2442"),sQuery(id+"F0.wireOp",EDGE,"E2443"),sQuery(id+"F0.wireOp",EDGE,"E2444"),sQuery(id+"F0.wireOp",EDGE,"E2445"),sQuery(id+"F0.wireOp",EDGE,"E2446"),sQuery(id+"F0.wireOp",EDGE,"E2447"),sQuery(id+"F0.wireOp",EDGE,"E2448"),sQuery(id+"F0.wireOp",EDGE,"E2449"),sQuery(id+"F0.wireOp",EDGE,"E2450"),sQuery(id+"F0.wireOp",EDGE,"E2451"),sQuery(id+"F0.wireOp",EDGE,"E2452"),sQuery(id+"F0.wireOp",EDGE,"E2453"),sQuery(id+"F0.wireOp",EDGE,"E2454"),sQuery(id+"F0.wireOp",EDGE,"E2455"),sQuery(id+"F0.wireOp",EDGE,"E2456"),sQuery(id+"F0.wireOp",EDGE,"E2457"),sQuery(id+"F0.wireOp",EDGE,"E2458"),sQuery(id+"F0.wireOp",EDGE,"E2459"),sQuery(id+"F0.wireOp",EDGE,"E2460"),sQuery(id+"F0.wireOp",EDGE,"E2461"),sQuery(id+"F0.wireOp",EDGE,"E2462"),sQuery(id+"F0.wireOp",EDGE,"E2463"),sQuery(id+"F0.wireOp",EDGE,"E2464"),sQuery(id+"F0.wireOp",EDGE,"E2465"),sQuery(id+"F0.wireOp",EDGE,"E2466"),sQuery(id+"F0.wireOp",EDGE,"E2467"),sQuery(id+"F0.wireOp",EDGE,"E2468"),sQuery(id+"F0.wireOp",EDGE,"E2469"),sQuery(id+"F0.wireOp",EDGE,"E2470"),sQuery(id+"F0.wireOp",EDGE,"E2471"),sQuery(id+"F0.wireOp",EDGE,"E2472"),sQuery(id+"F0.wireOp",EDGE,"E2473"),sQuery(id+"F0.wireOp",EDGE,"E2474"),sQuery(id+"F0.wireOp",EDGE,"E2475"),sQuery(id+"F0.wireOp",EDGE,"E2476"),sQuery(id+"F0.wireOp",EDGE,"E2477"),sQuery(id+"F0.wireOp",EDGE,"E2478"),sQuery(id+"F0.wireOp",EDGE,"E2479"),sQuery(id+"F0.wireOp",EDGE,"E2480"),sQuery(id+"F0.wireOp",EDGE,"E2481"),sQuery(id+"F0.wireOp",EDGE,"E2482"),sQuery(id+"F0.wireOp",EDGE,"E2483"),sQuery(id+"F0.wireOp",EDGE,"E2484"),sQuery(id+"F0.wireOp",EDGE,"E2485"),sQuery(id+"F0.wireOp",EDGE,"E2486"),sQuery(id+"F0.wireOp",EDGE,"E2487"),sQuery(id+"F0.wireOp",EDGE,"E2488"),sQuery(id+"F0.wireOp",EDGE,"E2489"),sQuery(id+"F0.wireOp",EDGE,"E2490"),sQuery(id+"F0.wireOp",EDGE,"E2491"),sQuery(id+"F0.wireOp",EDGE,"E2492"),sQuery(id+"F0.wireOp",EDGE,"E2493"),sQuery(id+"F0.wireOp",EDGE,"E2494"),sQuery(id+"F0.wireOp",EDGE,"E2495"),sQuery(id+"F0.wireOp",EDGE,"E2496"),sQuery(id+"F0.wireOp",EDGE,"E2497"),sQuery(id+"F0.wireOp",EDGE,"E2498"),sQuery(id+"F0.wireOp",EDGE,"E2499"),sQuery(id+"F0.wireOp",EDGE,"E2500"),sQuery(id+"F0.wireOp",EDGE,"E2501"),sQuery(id+"F0.wireOp",EDGE,"E2502"),sQuery(id+"F0.wireOp",EDGE,"E2503"),sQuery(id+"F0.wireOp",EDGE,"E2504"),sQuery(id+"F0.wireOp",EDGE,"E2505"),sQuery(id+"F0.wireOp",EDGE,"E2506"),sQuery(id+"F0.wireOp",EDGE,"E2507"),sQuery(id+"F0.wireOp",EDGE,"E2508"),sQuery(id+"F0.wireOp",EDGE,"E2509"),sQuery(id+"F0.wireOp",EDGE,"E2510"),sQuery(id+"F0.wireOp",EDGE,"E2511"),sQuery(id+"F0.wireOp",EDGE,"E2512"),sQuery(id+"F0.wireOp",EDGE,"E2513"),sQuery(id+"F0.wireOp",EDGE,"E2514"),sQuery(id+"F0.wireOp",EDGE,"E2515"),sQuery(id+"F0.wireOp",EDGE,"E2516"),sQuery(id+"F0.wireOp",EDGE,"E2517"),sQuery(id+"F0.wireOp",EDGE,"E2518"),sQuery(id+"F0.wireOp",EDGE,"E2519"),sQuery(id+"F0.wireOp",EDGE,"E2520"),sQuery(id+"F0.wireOp",EDGE,"E2521"),sQuery(id+"F0.wireOp",EDGE,"E2522"),sQuery(id+"F0.wireOp",EDGE,"E2523"),sQuery(id+"F0.wireOp",EDGE,"E2524"),sQuery(id+"F0.wireOp",EDGE,"E2525"),sQuery(id+"F0.wireOp",EDGE,"E2526"),sQuery(id+"F0.wireOp",EDGE,"E2527"),sQuery(id+"F0.wireOp",EDGE,"E2528"),sQuery(id+"F0.wireOp",EDGE,"E2529"),sQuery(id+"F0.wireOp",EDGE,"E2530"),sQuery(id+"F0.wireOp",EDGE,"E2531"),sQuery(id+"F0.wireOp",EDGE,"E2532"),sQuery(id+"F0.wireOp",EDGE,"E2533"),sQuery(id+"F0.wireOp",EDGE,"E2534"),sQuery(id+"F0.wireOp",EDGE,"E2535"),sQuery(id+"F0.wireOp",EDGE,"E2536"),sQuery(id+"F0.wireOp",EDGE,"E2537"),sQuery(id+"F0.wireOp",EDGE,"E2538"),sQuery(id+"F0.wireOp",EDGE,"E2539"),sQuery(id+"F0.wireOp",EDGE,"E2540"),sQuery(id+"F0.wireOp",EDGE,"E2541"),sQuery(id+"F0.wireOp",EDGE,"E2542"),sQuery(id+"F0.wireOp",EDGE,"E2543"),sQuery(id+"F0.wireOp",EDGE,"E2544"),sQuery(id+"F0.wireOp",EDGE,"E2545"),sQuery(id+"F0.wireOp",EDGE,"E2546"),sQuery(id+"F0.wireOp",EDGE,"E2547"),sQuery(id+"F0.wireOp",EDGE,"E2548"),sQuery(id+"F0.wireOp",EDGE,"E2549"),sQuery(id+"F0.wireOp",EDGE,"E2550"),sQuery(id+"F0.wireOp",EDGE,"E2551"),sQuery(id+"F0.wireOp",EDGE,"E2552"),sQuery(id+"F0.wireOp",EDGE,"E2553"),sQuery(id+"F0.wireOp",EDGE,"E2554"),sQuery(id+"F0.wireOp",EDGE,"E2555"),sQuery(id+"F0.wireOp",EDGE,"E2556"),sQuery(id+"F0.wireOp",EDGE,"E2557"),sQuery(id+"F0.wireOp",EDGE,"E2558"),sQuery(id+"F0.wireOp",EDGE,"E2559"),sQuery(id+"F0.wireOp",EDGE,"E2560"),sQuery(id+"F0.wireOp",EDGE,"E2561"),sQuery(id+"F0.wireOp",EDGE,"E2562"),sQuery(id+"F0.wireOp",EDGE,"E2563"),sQuery(id+"F0.wireOp",EDGE,"E2564"),sQuery(id+"F0.wireOp",EDGE,"E2565"),sQuery(id+"F0.wireOp",EDGE,"E2566"),sQuery(id+"F0.wireOp",EDGE,"E2567"),sQuery(id+"F0.wireOp",EDGE,"E2568"),sQuery(id+"F0.wireOp",EDGE,"E2569"),sQuery(id+"F0.wireOp",EDGE,"E2570"),sQuery(id+"F0.wireOp",EDGE,"E2571"),sQuery(id+"F0.wireOp",EDGE,"E2572"),sQuery(id+"F0.wireOp",EDGE,"E2573"),sQuery(id+"F0.wireOp",EDGE,"E2574"),sQuery(id+"F0.wireOp",EDGE,"E2575"),sQuery(id+"F0.wireOp",EDGE,"E2576"),sQuery(id+"F0.wireOp",EDGE,"E2577"),sQuery(id+"F0.wireOp",EDGE,"E2578"),sQuery(id+"F0.wireOp",EDGE,"E2579"),sQuery(id+"F0.wireOp",EDGE,"E2580"),sQuery(id+"F0.wireOp",EDGE,"E2581"),sQuery(id+"F0.wireOp",EDGE,"E2582"),sQuery(id+"F0.wireOp",EDGE,"E2583"),sQuery(id+"F0.wireOp",EDGE,"E2584"),sQuery(id+"F0.wireOp",EDGE,"E2585"),sQuery(id+"F0.wireOp",EDGE,"E2586"),sQuery(id+"F0.wireOp",EDGE,"E2587"),sQuery(id+"F0.wireOp",EDGE,"E2588"),sQuery(id+"F0.wireOp",EDGE,"E2589"),sQuery(id+"F0.wireOp",EDGE,"E2590"),sQuery(id+"F0.wireOp",EDGE,"E2591"),sQuery(id+"F0.wireOp",EDGE,"E2592"),sQuery(id+"F0.wireOp",EDGE,"E2593"),sQuery(id+"F0.wireOp",EDGE,"E2594"),sQuery(id+"F0.wireOp",EDGE,"E2595"),sQuery(id+"F0.wireOp",EDGE,"E2596"),sQuery(id+"F0.wireOp",EDGE,"E2597"),sQuery(id+"F0.wireOp",EDGE,"E2598"),sQuery(id+"F0.wireOp",EDGE,"E2599"),sQuery(id+"F0.wireOp",EDGE,"E2600"),sQuery(id+"F0.wireOp",EDGE,"E2601"),sQuery(id+"F0.wireOp",EDGE,"E2602"),sQuery(id+"F0.wireOp",EDGE,"E2603"),sQuery(id+"F0.wireOp",EDGE,"E2604"),sQuery(id+"F0.wireOp",EDGE,"E2605"),sQuery(id+"F0.wireOp",EDGE,"E2606"),sQuery(id+"F0.wireOp",EDGE,"E2607"),sQuery(id+"F0.wireOp",EDGE,"E2608"),sQuery(id+"F0.wireOp",EDGE,"E2609"),sQuery(id+"F0.wireOp",EDGE,"E2610"),sQuery(id+"F0.wireOp",EDGE,"E2611"),sQuery(id+"F0.wireOp",EDGE,"E2612"),sQuery(id+"F0.wireOp",EDGE,"E2613"),sQuery(id+"F0.wireOp",EDGE,"E2614"),sQuery(id+"F0.wireOp",EDGE,"E2615"),sQuery(id+"F0.wireOp",EDGE,"E2616"),sQuery(id+"F0.wireOp",EDGE,"E2617"),sQuery(id+"F0.wireOp",EDGE,"E2618"),sQuery(id+"F0.wireOp",EDGE,"E2619"),sQuery(id+"F0.wireOp",EDGE,"E2620"),sQuery(id+"F0.wireOp",EDGE,"E2621"),sQuery(id+"F0.wireOp",EDGE,"E2622"),sQuery(id+"F0.wireOp",EDGE,"E2623"),sQuery(id+"F0.wireOp",EDGE,"E2624"),sQuery(id+"F0.wireOp",EDGE,"E2625"),sQuery(id+"F0.wireOp",EDGE,"E2626"),sQuery(id+"F0.wireOp",EDGE,"E2627"),sQuery(id+"F0.wireOp",EDGE,"E2628"),sQuery(id+"F0.wireOp",EDGE,"E2629"),sQuery(id+"F0.wireOp",EDGE,"E2630"),sQuery(id+"F0.wireOp",EDGE,"E2631"),sQuery(id+"F0.wireOp",EDGE,"E2632"),sQuery(id+"F0.wireOp",EDGE,"E2633"),sQuery(id+"F0.wireOp",EDGE,"E2634"),sQuery(id+"F0.wireOp",EDGE,"E2635"),sQuery(id+"F0.wireOp",EDGE,"E2636"),sQuery(id+"F0.wireOp",EDGE,"E2637"),sQuery(id+"F0.wireOp",EDGE,"E2638"),sQuery(id+"F0.wireOp",EDGE,"E2639"),sQuery(id+"F0.wireOp",EDGE,"E2640"),sQuery(id+"F0.wireOp",EDGE,"E2641"),sQuery(id+"F0.wireOp",EDGE,"E2642"),sQuery(id+"F0.wireOp",EDGE,"E2643"),sQuery(id+"F0.wireOp",EDGE,"E2644"),sQuery(id+"F0.wireOp",EDGE,"E2645"),sQuery(id+"F0.wireOp",EDGE,"E2646"),sQuery(id+"F0.wireOp",EDGE,"E2647"),sQuery(id+"F0.wireOp",EDGE,"E2648"),sQuery(id+"F0.wireOp",EDGE,"E2649"),sQuery(id+"F0.wireOp",EDGE,"E2650"),sQuery(id+"F0.wireOp",EDGE,"E2651"),sQuery(id+"F0.wireOp",EDGE,"E2652"),sQuery(id+"F0.wireOp",EDGE,"E2653"),sQuery(id+"F0.wireOp",EDGE,"E2654"),sQuery(id+"F0.wireOp",EDGE,"E2655"),sQuery(id+"F0.wireOp",EDGE,"E2656"),sQuery(id+"F0.wireOp",EDGE,"E2657"),sQuery(id+"F0.wireOp",EDGE,"E2658"),sQuery(id+"F0.wireOp",EDGE,"E2659"),sQuery(id+"F0.wireOp",EDGE,"E2660"),sQuery(id+"F0.wireOp",EDGE,"E2661"),sQuery(id+"F0.wireOp",EDGE,"E2662"),sQuery(id+"F0.wireOp",EDGE,"E2663"),sQuery(id+"F0.wireOp",EDGE,"E2664"),sQuery(id+"F0.wireOp",EDGE,"E2665"),sQuery(id+"F0.wireOp",EDGE,"E2666"),sQuery(id+"F0.wireOp",EDGE,"E2667"),sQuery(id+"F0.wireOp",EDGE,"E2668"),sQuery(id+"F0.wireOp",EDGE,"E2669"),sQuery(id+"F0.wireOp",EDGE,"E2670"),sQuery(id+"F0.wireOp",EDGE,"E2671"),sQuery(id+"F0.wireOp",EDGE,"E2672"),sQuery(id+"F0.wireOp",EDGE,"E2673"),sQuery(id+"F0.wireOp",EDGE,"E2674"),sQuery(id+"F0.wireOp",EDGE,"E2675"),sQuery(id+"F0.wireOp",EDGE,"E2676"),sQuery(id+"F0.wireOp",EDGE,"E2677"),sQuery(id+"F0.wireOp",EDGE,"E2678"),sQuery(id+"F0.wireOp",EDGE,"E2679"),sQuery(id+"F0.wireOp",EDGE,"E2680"),sQuery(id+"F0.wireOp",EDGE,"E2681"),sQuery(id+"F0.wireOp",EDGE,"E2682"),sQuery(id+"F0.wireOp",EDGE,"E2683"),sQuery(id+"F0.wireOp",EDGE,"E2684"),sQuery(id+"F0.wireOp",EDGE,"E2685"),sQuery(id+"F0.wireOp",EDGE,"E2686"),sQuery(id+"F0.wireOp",EDGE,"E2687"),sQuery(id+"F0.wireOp",EDGE,"E2688"),sQuery(id+"F0.wireOp",EDGE,"E2689"),sQuery(id+"F0.wireOp",EDGE,"E2690"),sQuery(id+"F0.wireOp",EDGE,"E2691"),sQuery(id+"F0.wireOp",EDGE,"E2692"),sQuery(id+"F0.wireOp",EDGE,"E2693"),sQuery(id+"F0.wireOp",EDGE,"E2694"),sQuery(id+"F0.wireOp",EDGE,"E2695"),sQuery(id+"F0.wireOp",EDGE,"E2696"),sQuery(id+"F0.wireOp",EDGE,"E2697"),sQuery(id+"F0.wireOp",EDGE,"E2698"),sQuery(id+"F0.wireOp",EDGE,"E2699"),sQuery(id+"F0.wireOp",EDGE,"E2700"),sQuery(id+"F0.wireOp",EDGE,"E2701"),sQuery(id+"F0.wireOp",EDGE,"E2702"),sQuery(id+"F0.wireOp",EDGE,"E2703"),sQuery(id+"F0.wireOp",EDGE,"E2704"),sQuery(id+"F0.wireOp",EDGE,"E2705"),sQuery(id+"F0.wireOp",EDGE,"E2706"),sQuery(id+"F0.wireOp",EDGE,"E2707"),sQuery(id+"F0.wireOp",EDGE,"E2708"),sQuery(id+"F0.wireOp",EDGE,"E2709"),sQuery(id+"F0.wireOp",EDGE,"E2710"),sQuery(id+"F0.wireOp",EDGE,"E2711"),sQuery(id+"F0.wireOp",EDGE,"E2712"),sQuery(id+"F0.wireOp",EDGE,"E2713"),sQuery(id+"F0.wireOp",EDGE,"E2714"),sQuery(id+"F0.wireOp",EDGE,"E2715"),sQuery(id+"F0.wireOp",EDGE,"E2716"),sQuery(id+"F0.wireOp",EDGE,"E2717"),sQuery(id+"F0.wireOp",EDGE,"E2718"),sQuery(id+"F0.wireOp",EDGE,"E2719"),sQuery(id+"F0.wireOp",EDGE,"E2720"),sQuery(id+"F0.wireOp",EDGE,"E2721"),sQuery(id+"F0.wireOp",EDGE,"E2722"),sQuery(id+"F0.wireOp",EDGE,"E2723"),sQuery(id+"F0.wireOp",EDGE,"E2724"),sQuery(id+"F0.wireOp",EDGE,"E2725"),sQuery(id+"F0.wireOp",EDGE,"E2726"),sQuery(id+"F0.wireOp",EDGE,"E2727"),sQuery(id+"F0.wireOp",EDGE,"E2728"),sQuery(id+"F0.wireOp",EDGE,"E2729"),sQuery(id+"F0.wireOp",EDGE,"E2730"),sQuery(id+"F0.wireOp",EDGE,"E2731"),sQuery(id+"F0.wireOp",EDGE,"E2732"),sQuery(id+"F0.wireOp",EDGE,"E2733"),sQuery(id+"F0.wireOp",EDGE,"E2734"),sQuery(id+"F0.wireOp",EDGE,"E2735"),sQuery(id+"F0.wireOp",EDGE,"E2736"),sQuery(id+"F0.wireOp",EDGE,"E2737"),sQuery(id+"F0.wireOp",EDGE,"E2738"),sQuery(id+"F0.wireOp",EDGE,"E2739"),sQuery(id+"F0.wireOp",EDGE,"E2740"),sQuery(id+"F0.wireOp",EDGE,"E2741"),sQuery(id+"F0.wireOp",EDGE,"E2742"),sQuery(id+"F0.wireOp",EDGE,"E2743"),sQuery(id+"F0.wireOp",EDGE,"E2744"),sQuery(id+"F0.wireOp",EDGE,"E2745"),sQuery(id+"F0.wireOp",EDGE,"E2746"),sQuery(id+"F0.wireOp",EDGE,"E2747"),sQuery(id+"F0.wireOp",EDGE,"E2748"),sQuery(id+"F0.wireOp",EDGE,"E2749"),sQuery(id+"F0.wireOp",EDGE,"E2750"),sQuery(id+"F0.wireOp",EDGE,"E2751"),sQuery(id+"F0.wireOp",EDGE,"E2752"),sQuery(id+"F0.wireOp",EDGE,"E2753"),sQuery(id+"F0.wireOp",EDGE,"E2754"),sQuery(id+"F0.wireOp",EDGE,"E2755"),sQuery(id+"F0.wireOp",EDGE,"E2756"),sQuery(id+"F0.wireOp",EDGE,"E2757"),sQuery(id+"F0.wireOp",EDGE,"E2758"),sQuery(id+"F0.wireOp",EDGE,"E2759"),sQuery(id+"F0.wireOp",EDGE,"E2760"),sQuery(id+"F0.wireOp",EDGE,"E2761"),sQuery(id+"F0.wireOp",EDGE,"E2762"),sQuery(id+"F0.wireOp",EDGE,"E2763"),sQuery(id+"F0.wireOp",EDGE,"E2764"),sQuery(id+"F0.wireOp",EDGE,"E2765"),sQuery(id+"F0.wireOp",EDGE,"E2766"),sQuery(id+"F0.wireOp",EDGE,"E2767"),sQuery(id+"F0.wireOp",EDGE,"E2768"),sQuery(id+"F0.wireOp",EDGE,"E2769"),sQuery(id+"F0.wireOp",EDGE,"E2770"),sQuery(id+"F0.wireOp",EDGE,"E2771"),sQuery(id+"F0.wireOp",EDGE,"E2772"),sQuery(id+"F0.wireOp",EDGE,"E2773"),sQuery(id+"F0.wireOp",EDGE,"E2774"),sQuery(id+"F0.wireOp",EDGE,"E2775"),sQuery(id+"F0.wireOp",EDGE,"E2776"),sQuery(id+"F0.wireOp",EDGE,"E2777"),sQuery(id+"F0.wireOp",EDGE,"E2778"),sQuery(id+"F0.wireOp",EDGE,"E2779"),sQuery(id+"F0.wireOp",EDGE,"E2780"),sQuery(id+"F0.wireOp",EDGE,"E2781"),sQuery(id+"F0.wireOp",EDGE,"E2782"),sQuery(id+"F0.wireOp",EDGE,"E2783"),sQuery(id+"F0.wireOp",EDGE,"E2784"),sQuery(id+"F0.wireOp",EDGE,"E2785"),sQuery(id+"F0.wireOp",EDGE,"E2786"),sQuery(id+"F0.wireOp",EDGE,"E2787"),sQuery(id+"F0.wireOp",EDGE,"E2788"),sQuery(id+"F0.wireOp",EDGE,"E2789"),sQuery(id+"F0.wireOp",EDGE,"E2790"),sQuery(id+"F0.wireOp",EDGE,"E2791"),sQuery(id+"F0.wireOp",EDGE,"E2792"),sQuery(id+"F0.wireOp",EDGE,"E2793"),sQuery(id+"F0.wireOp",EDGE,"E2794"),sQuery(id+"F0.wireOp",EDGE,"E2795"),sQuery(id+"F0.wireOp",EDGE,"E2796"),sQuery(id+"F0.wireOp",EDGE,"E2797"),sQuery(id+"F0.wireOp",EDGE,"E2798"),sQuery(id+"F0.wireOp",EDGE,"E2799"),sQuery(id+"F0.wireOp",EDGE,"E2800"),sQuery(id+"F0.wireOp",EDGE,"E2801"),sQuery(id+"F0.wireOp",EDGE,"E2802"),sQuery(id+"F0.wireOp",EDGE,"E2803"),sQuery(id+"F0.wireOp",EDGE,"E2804"),sQuery(id+"F0.wireOp",EDGE,"E2805"),sQuery(id+"F0.wireOp",EDGE,"E2806"),sQuery(id+"F0.wireOp",EDGE,"E2807"),sQuery(id+"F0.wireOp",EDGE,"E2808"),sQuery(id+"F0.wireOp",EDGE,"E2809"),sQuery(id+"F0.wireOp",EDGE,"E2810"),sQuery(id+"F0.wireOp",EDGE,"E2811"),sQuery(id+"F0.wireOp",EDGE,"E2812"),sQuery(id+"F0.wireOp",EDGE,"E2813"),sQuery(id+"F0.wireOp",EDGE,"E2814"),sQuery(id+"F0.wireOp",EDGE,"E2815"),sQuery(id+"F0.wireOp",EDGE,"E2816"),sQuery(id+"F0.wireOp",EDGE,"E2817"),sQuery(id+"F0.wireOp",EDGE,"E2818"),sQuery(id+"F0.wireOp",EDGE,"E2819"),sQuery(id+"F0.wireOp",EDGE,"E2820"),sQuery(id+"F0.wireOp",EDGE,"E2821"),sQuery(id+"F0.wireOp",EDGE,"E2822"),sQuery(id+"F0.wireOp",EDGE,"E2823"),sQuery(id+"F0.wireOp",EDGE,"E2824"),sQuery(id+"F0.wireOp",EDGE,"E2825"),sQuery(id+"F0.wireOp",EDGE,"E2826"),sQuery(id+"F0.wireOp",EDGE,"E2827"),sQuery(id+"F0.wireOp",EDGE,"E2828"),sQuery(id+"F0.wireOp",EDGE,"E2829"),sQuery(id+"F0.wireOp",EDGE,"E2830"),sQuery(id+"F0.wireOp",EDGE,"E2831"),sQuery(id+"F0.wireOp",EDGE,"E2832"),sQuery(id+"F0.wireOp",EDGE,"E2833"),sQuery(id+"F0.wireOp",EDGE,"E2834"),sQuery(id+"F0.wireOp",EDGE,"E2835"),sQuery(id+"F0.wireOp",EDGE,"E2836"),sQuery(id+"F0.wireOp",EDGE,"E2837"),sQuery(id+"F0.wireOp",EDGE,"E2838"),sQuery(id+"F0.wireOp",EDGE,"E2839"),sQuery(id+"F0.wireOp",EDGE,"E2840"),sQuery(id+"F0.wireOp",EDGE,"E2841"),sQuery(id+"F0.wireOp",EDGE,"E2842"),sQuery(id+"F0.wireOp",EDGE,"E2843"),sQuery(id+"F0.wireOp",EDGE,"E2844"),sQuery(id+"F0.wireOp",EDGE,"E2845"),sQuery(id+"F0.wireOp",EDGE,"E2846"),sQuery(id+"F0.wireOp",EDGE,"E2847"),sQuery(id+"F0.wireOp",EDGE,"E2848"),sQuery(id+"F0.wireOp",EDGE,"E2849"),sQuery(id+"F0.wireOp",EDGE,"E2850"),sQuery(id+"F0.wireOp",EDGE,"E2851"),sQuery(id+"F0.wireOp",EDGE,"E2852"),sQuery(id+"F0.wireOp",EDGE,"E2853"),sQuery(id+"F0.wireOp",EDGE,"E2854"),sQuery(id+"F0.wireOp",EDGE,"E2855"),sQuery(id+"F0.wireOp",EDGE,"E2856"),sQuery(id+"F0.wireOp",EDGE,"E2857"),sQuery(id+"F0.wireOp",EDGE,"E2858"),sQuery(id+"F0.wireOp",EDGE,"E2859"),sQuery(id+"F0.wireOp",EDGE,"E2860"),sQuery(id+"F0.wireOp",EDGE,"E2861"),sQuery(id+"F0.wireOp",EDGE,"E2862"),sQuery(id+"F0.wireOp",EDGE,"E2863"),sQuery(id+"F0.wireOp",EDGE,"E2864"),sQuery(id+"F0.wireOp",EDGE,"E2865"),sQuery(id+"F0.wireOp",EDGE,"E2866"),sQuery(id+"F0.wireOp",EDGE,"E2867"),sQuery(id+"F0.wireOp",EDGE,"E2868"),sQuery(id+"F0.wireOp",EDGE,"E2869"),sQuery(id+"F0.wireOp",EDGE,"E2870"),sQuery(id+"F0.wireOp",EDGE,"E2871"),sQuery(id+"F0.wireOp",EDGE,"E2872"),sQuery(id+"F0.wireOp",EDGE,"E2873"),sQuery(id+"F0.wireOp",EDGE,"E2874"),sQuery(id+"F0.wireOp",EDGE,"E2875"),sQuery(id+"F0.wireOp",EDGE,"E2876"),sQuery(id+"F0.wireOp",EDGE,"E2877"),sQuery(id+"F0.wireOp",EDGE,"E2878"),sQuery(id+"F0.wireOp",EDGE,"E2879"),sQuery(id+"F0.wireOp",EDGE,"E2880"),sQuery(id+"F0.wireOp",EDGE,"E2881"),sQuery(id+"F0.wireOp",EDGE,"E2882"),sQuery(id+"F0.wireOp",EDGE,"E2883"),sQuery(id+"F0.wireOp",EDGE,"E2884"),sQuery(id+"F0.wireOp",EDGE,"E2885"),sQuery(id+"F0.wireOp",EDGE,"E2886"),sQuery(id+"F0.wireOp",EDGE,"E2887"),sQuery(id+"F0.wireOp",EDGE,"E2888"),sQuery(id+"F0.wireOp",EDGE,"E2889"),sQuery(id+"F0.wireOp",EDGE,"E2890"),sQuery(id+"F0.wireOp",EDGE,"E2891"),sQuery(id+"F0.wireOp",EDGE,"E2892"),sQuery(id+"F0.wireOp",EDGE,"E2893"),sQuery(id+"F0.wireOp",EDGE,"E2894"),sQuery(id+"F0.wireOp",EDGE,"E2895"),sQuery(id+"F0.wireOp",EDGE,"E2896"),sQuery(id+"F0.wireOp",EDGE,"E2897"),sQuery(id+"F0.wireOp",EDGE,"E2898"),sQuery(id+"F0.wireOp",EDGE,"E2899"),sQuery(id+"F0.wireOp",EDGE,"E2900"),sQuery(id+"F0.wireOp",EDGE,"E2901"),sQuery(id+"F0.wireOp",EDGE,"E2902"),sQuery(id+"F0.wireOp",EDGE,"E2903"),sQuery(id+"F0.wireOp",EDGE,"E2904"),sQuery(id+"F0.wireOp",EDGE,"E2905"),sQuery(id+"F0.wireOp",EDGE,"E2906"),sQuery(id+"F0.wireOp",EDGE,"E2907"),sQuery(id+"F0.wireOp",EDGE,"E2908"),sQuery(id+"F0.wireOp",EDGE,"E2909"),sQuery(id+"F0.wireOp",EDGE,"E2910"),sQuery(id+"F0.wireOp",EDGE,"E2911"),sQuery(id+"F0.wireOp",EDGE,"E2912"),sQuery(id+"F0.wireOp",EDGE,"E2913"),sQuery(id+"F0.wireOp",EDGE,"E2914"),sQuery(id+"F0.wireOp",EDGE,"E2915"),sQuery(id+"F0.wireOp",EDGE,"E2916"),sQuery(id+"F0.wireOp",EDGE,"E2917"),sQuery(id+"F0.wireOp",EDGE,"E2918"),sQuery(id+"F0.wireOp",EDGE,"E2919"),sQuery(id+"F0.wireOp",EDGE,"E2920"),sQuery(id+"F0.wireOp",EDGE,"E2921"),sQuery(id+"F0.wireOp",EDGE,"E2922"),sQuery(id+"F0.wireOp",EDGE,"E2923"),sQuery(id+"F0.wireOp",EDGE,"E2924"),sQuery(id+"F0.wireOp",EDGE,"E2925"),sQuery(id+"F0.wireOp",EDGE,"E2926"),sQuery(id+"F0.wireOp",EDGE,"E2927"),sQuery(id+"F0.wireOp",EDGE,"E2928"),sQuery(id+"F0.wireOp",EDGE,"E2929"),sQuery(id+"F0.wireOp",EDGE,"E2930"),sQuery(id+"F0.wireOp",EDGE,"E2931"),sQuery(id+"F0.wireOp",EDGE,"E2932"),sQuery(id+"F0.wireOp",EDGE,"E2933"),sQuery(id+"F0.wireOp",EDGE,"E2934"),sQuery(id+"F0.wireOp",EDGE,"E2935"),sQuery(id+"F0.wireOp",EDGE,"E2936"),sQuery(id+"F0.wireOp",EDGE,"E2937"),sQuery(id+"F0.wireOp",EDGE,"E2938"),sQuery(id+"F0.wireOp",EDGE,"E2939"),sQuery(id+"F0.wireOp",EDGE,"E2940"),sQuery(id+"F0.wireOp",EDGE,"E2941"),sQuery(id+"F0.wireOp",EDGE,"E2942"),sQuery(id+"F0.wireOp",EDGE,"E2943"),sQuery(id+"F0.wireOp",EDGE,"E2944"),sQuery(id+"F0.wireOp",EDGE,"E2945"),sQuery(id+"F0.wireOp",EDGE,"E2946"),sQuery(id+"F0.wireOp",EDGE,"E2947"),sQuery(id+"F0.wireOp",EDGE,"E2948"),sQuery(id+"F0.wireOp",EDGE,"E2949"),sQuery(id+"F0.wireOp",EDGE,"E2950"),sQuery(id+"F0.wireOp",EDGE,"E2951"),sQuery(id+"F0.wireOp",EDGE,"E2952"),sQuery(id+"F0.wireOp",EDGE,"E2953"),sQuery(id+"F0.wireOp",EDGE,"E2954"),sQuery(id+"F0.wireOp",EDGE,"E2955"),sQuery(id+"F0.wireOp",EDGE,"E2956"),sQuery(id+"F0.wireOp",EDGE,"E2957"),sQuery(id+"F0.wireOp",EDGE,"E2958"),sQuery(id+"F0.wireOp",EDGE,"E2959"),sQuery(id+"F0.wireOp",EDGE,"E2960"),sQuery(id+"F0.wireOp",EDGE,"E2961"),sQuery(id+"F0.wireOp",EDGE,"E2962"),sQuery(id+"F0.wireOp",EDGE,"E2963"),sQuery(id+"F0.wireOp",EDGE,"E2964"),sQuery(id+"F0.wireOp",EDGE,"E2965"),sQuery(id+"F0.wireOp",EDGE,"E2966"),sQuery(id+"F0.wireOp",EDGE,"E2967"),sQuery(id+"F0.wireOp",EDGE,"E2968"),sQuery(id+"F0.wireOp",EDGE,"E2969"),sQuery(id+"F0.wireOp",EDGE,"E2970"),sQuery(id+"F0.wireOp",EDGE,"E2971"),sQuery(id+"F0.wireOp",EDGE,"E2972"),sQuery(id+"F0.wireOp",EDGE,"E2973"),sQuery(id+"F0.wireOp",EDGE,"E2974"),sQuery(id+"F0.wireOp",EDGE,"E2975"),sQuery(id+"F0.wireOp",EDGE,"E2976"),sQuery(id+"F0.wireOp",EDGE,"E2977"),sQuery(id+"F0.wireOp",EDGE,"E2978"),sQuery(id+"F0.wireOp",EDGE,"E2979"),sQuery(id+"F0.wireOp",EDGE,"E2980"),sQuery(id+"F0.wireOp",EDGE,"E2981"),sQuery(id+"F0.wireOp",EDGE,"E2982"),sQuery(id+"F0.wireOp",EDGE,"E2983"),sQuery(id+"F0.wireOp",EDGE,"E2984"),sQuery(id+"F0.wireOp",EDGE,"E2985"),sQuery(id+"F0.wireOp",EDGE,"E2986"),sQuery(id+"F0.wireOp",EDGE,"E2987"),sQuery(id+"F0.wireOp",EDGE,"E2988"),sQuery(id+"F0.wireOp",EDGE,"E2989"),sQuery(id+"F0.wireOp",EDGE,"E2990"),sQuery(id+"F0.wireOp",EDGE,"E2991"),sQuery(id+"F0.wireOp",EDGE,"E2992"),sQuery(id+"F0.wireOp",EDGE,"E2993"),sQuery(id+"F0.wireOp",EDGE,"E2994"),sQuery(id+"F0.wireOp",EDGE,"E2995"),sQuery(id+"F0.wireOp",EDGE,"E2996"),sQuery(id+"F0.wireOp",EDGE,"E2997"),sQuery(id+"F0.wireOp",EDGE,"E2998"),sQuery(id+"F0.wireOp",EDGE,"E2999"),sQuery(id+"F0.wireOp",EDGE,"E3000"),sQuery(id+"F0.wireOp",EDGE,"E3001"),sQuery(id+"F0.wireOp",EDGE,"E3002"),sQuery(id+"F0.wireOp",EDGE,"E3003"),sQuery(id+"F0.wireOp",EDGE,"E3004"),sQuery(id+"F0.wireOp",EDGE,"E3005"),sQuery(id+"F0.wireOp",EDGE,"E3006"),sQuery(id+"F0.wireOp",EDGE,"E3007"),sQuery(id+"F0.wireOp",EDGE,"E3008"),sQuery(id+"F0.wireOp",EDGE,"E3009"),sQuery(id+"F0.wireOp",EDGE,"E3010"),sQuery(id+"F0.wireOp",EDGE,"E3011"),sQuery(id+"F0.wireOp",EDGE,"E3012"),sQuery(id+"F0.wireOp",EDGE,"E3013"),sQuery(id+"F0.wireOp",EDGE,"E3014"),sQuery(id+"F0.wireOp",EDGE,"E3015"),sQuery(id+"F0.wireOp",EDGE,"E3016"),sQuery(id+"F0.wireOp",EDGE,"E3017"),sQuery(id+"F0.wireOp",EDGE,"E3018"),sQuery(id+"F0.wireOp",EDGE,"E3019"),sQuery(id+"F0.wireOp",EDGE,"E3020"),sQuery(id+"F0.wireOp",EDGE,"E3021"),sQuery(id+"F0.wireOp",EDGE,"E3022"),sQuery(id+"F0.wireOp",EDGE,"E3023"),sQuery(id+"F0.wireOp",EDGE,"E3024"),sQuery(id+"F0.wireOp",EDGE,"E3025"),sQuery(id+"F0.wireOp",EDGE,"E3026"),sQuery(id+"F0.wireOp",EDGE,"E3027"),sQuery(id+"F0.wireOp",EDGE,"E3028"),sQuery(id+"F0.wireOp",EDGE,"E3029"),sQuery(id+"F0.wireOp",EDGE,"E3030"),sQuery(id+"F0.wireOp",EDGE,"E3031"),sQuery(id+"F0.wireOp",EDGE,"E3032"),sQuery(id+"F0.wireOp",EDGE,"E3033"),sQuery(id+"F0.wireOp",EDGE,"E3034"),sQuery(id+"F0.wireOp",EDGE,"E3035"),sQuery(id+"F0.wireOp",EDGE,"E3036"),sQuery(id+"F0.wireOp",EDGE,"E3037"),sQuery(id+"F0.wireOp",EDGE,"E3038"),sQuery(id+"F0.wireOp",EDGE,"E3039"),sQuery(id+"F0.wireOp",EDGE,"E3040"),sQuery(id+"F0.wireOp",EDGE,"E3041"),sQuery(id+"F0.wireOp",EDGE,"E3042"),sQuery(id+"F0.wireOp",EDGE,"E3043"),sQuery(id+"F0.wireOp",EDGE,"E3044"),sQuery(id+"F0.wireOp",EDGE,"E3045"),sQuery(id+"F0.wireOp",EDGE,"E3046"),sQuery(id+"F0.wireOp",EDGE,"E3047"),sQuery(id+"F0.wireOp",EDGE,"E3048"),sQuery(id+"F0.wireOp",EDGE,"E3049"),sQuery(id+"F0.wireOp",EDGE,"E3050"),sQuery(id+"F0.wireOp",EDGE,"E3051"),sQuery(id+"F0.wireOp",EDGE,"E3052"),sQuery(id+"F0.wireOp",EDGE,"E3053"),sQuery(id+"F0.wireOp",EDGE,"E3054"),sQuery(id+"F0.wireOp",EDGE,"E3055"),sQuery(id+"F0.wireOp",EDGE,"E3056"),sQuery(id+"F0.wireOp",EDGE,"E3057"),sQuery(id+"F0.wireOp",EDGE,"E3058"),sQuery(id+"F0.wireOp",EDGE,"E3059"),sQuery(id+"F0.wireOp",EDGE,"E3060"),sQuery(id+"F0.wireOp",EDGE,"E3061"),sQuery(id+"F0.wireOp",EDGE,"E3062"),sQuery(id+"F0.wireOp",EDGE,"E3063"),sQuery(id+"F0.wireOp",EDGE,"E3064"),sQuery(id+"F0.wireOp",EDGE,"E3065"),sQuery(id+"F0.wireOp",EDGE,"E3066"),sQuery(id+"F0.wireOp",EDGE,"E3067"),sQuery(id+"F0.wireOp",EDGE,"E3068"),sQuery(id+"F0.wireOp",EDGE,"E3069"),sQuery(id+"F0.wireOp",EDGE,"E3070"),sQuery(id+"F0.wireOp",EDGE,"E3071"),sQuery(id+"F0.wireOp",EDGE,"E3072"),sQuery(id+"F0.wireOp",EDGE,"E3073"),sQuery(id+"F0.wireOp",EDGE,"E3074"),sQuery(id+"F0.wireOp",EDGE,"E3075"),sQuery(id+"F0.wireOp",EDGE,"E3076"),sQuery(id+"F0.wireOp",EDGE,"E3077"),sQuery(id+"F0.wireOp",EDGE,"E3078"),sQuery(id+"F0.wireOp",EDGE,"E3079"),sQuery(id+"F0.wireOp",EDGE,"E3080"),sQuery(id+"F0.wireOp",EDGE,"E3081"),sQuery(id+"F0.wireOp",EDGE,"E3082"),sQuery(id+"F0.wireOp",EDGE,"E3083"),sQuery(id+"F0.wireOp",EDGE,"E3084"),sQuery(id+"F0.wireOp",EDGE,"E3085"),sQuery(id+"F0.wireOp",EDGE,"E3086"),sQuery(id+"F0.wireOp",EDGE,"E3087"),sQuery(id+"F0.wireOp",EDGE,"E3088"),sQuery(id+"F0.wireOp",EDGE,"E3089"),sQuery(id+"F0.wireOp",EDGE,"E3090"),sQuery(id+"F0.wireOp",EDGE,"E3091"),sQuery(id+"F0.wireOp",EDGE,"E3092"),sQuery(id+"F0.wireOp",EDGE,"E3093"),sQuery(id+"F0.wireOp",EDGE,"E3094"),sQuery(id+"F0.wireOp",EDGE,"E3095"),sQuery(id+"F0.wireOp",EDGE,"E3096"),sQuery(id+"F0.wireOp",EDGE,"E3097"),sQuery(id+"F0.wireOp",EDGE,"E3098"),sQuery(id+"F0.wireOp",EDGE,"E3099"),sQuery(id+"F0.wireOp",EDGE,"E3100"),sQuery(id+"F0.wireOp",EDGE,"E3101"),sQuery(id+"F0.wireOp",EDGE,"E3102"),sQuery(id+"F0.wireOp",EDGE,"E3103"),sQuery(id+"F0.wireOp",EDGE,"E3104"),sQuery(id+"F0.wireOp",EDGE,"E3105"),sQuery(id+"F0.wireOp",EDGE,"E3106"),sQuery(id+"F0.wireOp",EDGE,"E3107"),sQuery(id+"F0.wireOp",EDGE,"E3108"),sQuery(id+"F0.wireOp",EDGE,"E3109"),sQuery(id+"F0.wireOp",EDGE,"E3110"),sQuery(id+"F0.wireOp",EDGE,"E3111"),sQuery(id+"F0.wireOp",EDGE,"E3112"),sQuery(id+"F0.wireOp",EDGE,"E3113"),sQuery(id+"F0.wireOp",EDGE,"E3114"),sQuery(id+"F0.wireOp",EDGE,"E3115"),sQuery(id+"F0.wireOp",EDGE,"E3116"),sQuery(id+"F0.wireOp",EDGE,"E3117"),sQuery(id+"F0.wireOp",EDGE,"E3118"),sQuery(id+"F0.wireOp",EDGE,"E3119"),sQuery(id+"F0.wireOp",EDGE,"E3120"),sQuery(id+"F0.wireOp",EDGE,"E3121"),sQuery(id+"F0.wireOp",EDGE,"E3122"),sQuery(id+"F0.wireOp",EDGE,"E3123"),sQuery(id+"F0.wireOp",EDGE,"E3124"),sQuery(id+"F0.wireOp",EDGE,"E3125"),sQuery(id+"F0.wireOp",EDGE,"E3126"),sQuery(id+"F0.wireOp",EDGE,"E3127"),sQuery(id+"F0.wireOp",EDGE,"E3128"),sQuery(id+"F0.wireOp",EDGE,"E3129"),sQuery(id+"F0.wireOp",EDGE,"E3130"),sQuery(id+"F0.wireOp",EDGE,"E3131"),sQuery(id+"F0.wireOp",EDGE,"E3132"),sQuery(id+"F0.wireOp",EDGE,"E3133"),sQuery(id+"F0.wireOp",EDGE,"E3134"),sQuery(id+"F0.wireOp",EDGE,"E3135"),sQuery(id+"F0.wireOp",EDGE,"E3136"),sQuery(id+"F0.wireOp",EDGE,"E3137"),sQuery(id+"F0.wireOp",EDGE,"E3138"),sQuery(id+"F0.wireOp",EDGE,"E3139"),sQuery(id+"F0.wireOp",EDGE,"E3140"),sQuery(id+"F0.wireOp",EDGE,"E3141"),sQuery(id+"F0.wireOp",EDGE,"E3142"),sQuery(id+"F0.wireOp",EDGE,"E3143"),sQuery(id+"F0.wireOp",EDGE,"E3144"),sQuery(id+"F0.wireOp",EDGE,"E3145"),sQuery(id+"F0.wireOp",EDGE,"E3146"),sQuery(id+"F0.wireOp",EDGE,"E3147"),sQuery(id+"F0.wireOp",EDGE,"E3148"),sQuery(id+"F0.wireOp",EDGE,"E3149"),sQuery(id+"F0.wireOp",EDGE,"E3150"),sQuery(id+"F0.wireOp",EDGE,"E3151"),sQuery(id+"F0.wireOp",EDGE,"E3152"),sQuery(id+"F0.wireOp",EDGE,"E3153"),sQuery(id+"F0.wireOp",EDGE,"E3154"),sQuery(id+"F0.wireOp",EDGE,"E3155"),sQuery(id+"F0.wireOp",EDGE,"E3156"),sQuery(id+"F0.wireOp",EDGE,"E3157"),sQuery(id+"F0.wireOp",EDGE,"E3158"),sQuery(id+"F0.wireOp",EDGE,"E3159"),sQuery(id+"F0.wireOp",EDGE,"E3160"),sQuery(id+"F0.wireOp",EDGE,"E3161"),sQuery(id+"F0.wireOp",EDGE,"E3162"),sQuery(id+"F0.wireOp",EDGE,"E3163"),sQuery(id+"F0.wireOp",EDGE,"E3164"),sQuery(id+"F0.wireOp",EDGE,"E3165"),sQuery(id+"F0.wireOp",EDGE,"E3166"),sQuery(id+"F0.wireOp",EDGE,"E3167"),sQuery(id+"F0.wireOp",EDGE,"E3168"),sQuery(id+"F0.wireOp",EDGE,"E3169"),sQuery(id+"F0.wireOp",EDGE,"E3170"),sQuery(id+"F0.wireOp",EDGE,"E3171"),sQuery(id+"F0.wireOp",EDGE,"E3172"),sQuery(id+"F0.wireOp",EDGE,"E3173"),sQuery(id+"F0.wireOp",EDGE,"E3174"),sQuery(id+"F0.wireOp",EDGE,"E3175"),sQuery(id+"F0.wireOp",EDGE,"E3176"),sQuery(id+"F0.wireOp",EDGE,"E3177"),sQuery(id+"F0.wireOp",EDGE,"E3178"),sQuery(id+"F0.wireOp",EDGE,"E3179"),sQuery(id+"F0.wireOp",EDGE,"E3180"),sQuery(id+"F0.wireOp",EDGE,"E3181"),sQuery(id+"F0.wireOp",EDGE,"E3182"),sQuery(id+"F0.wireOp",EDGE,"E3183"),sQuery(id+"F0.wireOp",EDGE,"E3184"),sQuery(id+"F0.wireOp",EDGE,"E3185"),sQuery(id+"F0.wireOp",EDGE,"E3186"),sQuery(id+"F0.wireOp",EDGE,"E3187"),sQuery(id+"F0.wireOp",EDGE,"E3188"),sQuery(id+"F0.wireOp",EDGE,"E3189"),sQuery(id+"F0.wireOp",EDGE,"E3190"),sQuery(id+"F0.wireOp",EDGE,"E3191"),sQuery(id+"F0.wireOp",EDGE,"E3192"),sQuery(id+"F0.wireOp",EDGE,"E3193"),sQuery(id+"F0.wireOp",EDGE,"E3194"),sQuery(id+"F0.wireOp",EDGE,"E3195"),sQuery(id+"F0.wireOp",EDGE,"E3196"),sQuery(id+"F0.wireOp",EDGE,"E3197"),sQuery(id+"F0.wireOp",EDGE,"E3198"),sQuery(id+"F0.wireOp",EDGE,"E3199"),sQuery(id+"F0.wireOp",EDGE,"E3200"),sQuery(id+"F0.wireOp",EDGE,"E3201"),sQuery(id+"F0.wireOp",EDGE,"E3202"),sQuery(id+"F0.wireOp",EDGE,"E3203"),sQuery(id+"F0.wireOp",EDGE,"E3204"),sQuery(id+"F0.wireOp",EDGE,"E3205"),sQuery(id+"F0.wireOp",EDGE,"E3206"),sQuery(id+"F0.wireOp",EDGE,"E3207"),sQuery(id+"F0.wireOp",EDGE,"E3208"),sQuery(id+"F0.wireOp",EDGE,"E3209"),sQuery(id+"F0.wireOp",EDGE,"E3210"),sQuery(id+"F0.wireOp",EDGE,"E3211"),sQuery(id+"F0.wireOp",EDGE,"E3212"),sQuery(id+"F0.wireOp",EDGE,"E3213"),sQuery(id+"F0.wireOp",EDGE,"E3214"),sQuery(id+"F0.wireOp",EDGE,"E3215"),sQuery(id+"F0.wireOp",EDGE,"E3216"),sQuery(id+"F0.wireOp",EDGE,"E3217"),sQuery(id+"F0.wireOp",EDGE,"E3218"),sQuery(id+"F0.wireOp",EDGE,"E3219"),sQuery(id+"F0.wireOp",EDGE,"E3220"),sQuery(id+"F0.wireOp",EDGE,"E3221"),sQuery(id+"F0.wireOp",EDGE,"E3222"),sQuery(id+"F0.wireOp",EDGE,"E3223"),sQuery(id+"F0.wireOp",EDGE,"E3224"),sQuery(id+"F0.wireOp",EDGE,"E3225"),sQuery(id+"F0.wireOp",EDGE,"E3226"),sQuery(id+"F0.wireOp",EDGE,"E3227"),sQuery(id+"F0.wireOp",EDGE,"E3228"),sQuery(id+"F0.wireOp",EDGE,"E3229"),sQuery(id+"F0.wireOp",EDGE,"E3230"),sQuery(id+"F0.wireOp",EDGE,"E3231"),sQuery(id+"F0.wireOp",EDGE,"E3232"),sQuery(id+"F0.wireOp",EDGE,"E3233"),sQuery(id+"F0.wireOp",EDGE,"E3234"),sQuery(id+"F0.wireOp",EDGE,"E3235"),sQuery(id+"F0.wireOp",EDGE,"E3236"),sQuery(id+"F0.wireOp",EDGE,"E3237"),sQuery(id+"F0.wireOp",EDGE,"E3238"),sQuery(id+"F0.wireOp",EDGE,"E3239"),sQuery(id+"F0.wireOp",EDGE,"E3240"),sQuery(id+"F0.wireOp",EDGE,"E3241"),sQuery(id+"F0.wireOp",EDGE,"E3242"),sQuery(id+"F0.wireOp",EDGE,"E3243"),sQuery(id+"F0.wireOp",EDGE,"E3244"),sQuery(id+"F0.wireOp",EDGE,"E3245"),sQuery(id+"F0.wireOp",EDGE,"E3246"),sQuery(id+"F0.wireOp",EDGE,"E3247"),sQuery(id+"F0.wireOp",EDGE,"E3248"),sQuery(id+"F0.wireOp",EDGE,"E3249"),sQuery(id+"F0.wireOp",EDGE,"E3250"),sQuery(id+"F0.wireOp",EDGE,"E3251"),sQuery(id+"F0.wireOp",EDGE,"E3252"),sQuery(id+"F0.wireOp",EDGE,"E3253"),sQuery(id+"F0.wireOp",EDGE,"E3254"),sQuery(id+"F0.wireOp",EDGE,"E3255"),sQuery(id+"F0.wireOp",EDGE,"E3256"),sQuery(id+"F0.wireOp",EDGE,"E3257"),sQuery(id+"F0.wireOp",EDGE,"E3258"),sQuery(id+"F0.wireOp",EDGE,"E3259"),sQuery(id+"F0.wireOp",EDGE,"E3260"),sQuery(id+"F0.wireOp",EDGE,"E3261"),sQuery(id+"F0.wireOp",EDGE,"E3262"),sQuery(id+"F0.wireOp",EDGE,"E3263"),sQuery(id+"F0.wireOp",EDGE,"E3264"),sQuery(id+"F0.wireOp",EDGE,"E3265"),sQuery(id+"F0.wireOp",EDGE,"E3266"),sQuery(id+"F0.wireOp",EDGE,"E3267"),sQuery(id+"F0.wireOp",EDGE,"E3268"),sQuery(id+"F0.wireOp",EDGE,"E3269"),sQuery(id+"F0.wireOp",EDGE,"E3270"),sQuery(id+"F0.wireOp",EDGE,"E3271"),sQuery(id+"F0.wireOp",EDGE,"E3272"),sQuery(id+"F0.wireOp",EDGE,"E3273"),sQuery(id+"F0.wireOp",EDGE,"E3274"),sQuery(id+"F0.wireOp",EDGE,"E3275"),sQuery(id+"F0.wireOp",EDGE,"E3276"),sQuery(id+"F0.wireOp",EDGE,"E3277"),sQuery(id+"F0.wireOp",EDGE,"E3278"),sQuery(id+"F0.wireOp",EDGE,"E3279"),sQuery(id+"F0.wireOp",EDGE,"E3280"),sQuery(id+"F0.wireOp",EDGE,"E3281"),sQuery(id+"F0.wireOp",EDGE,"E3282"),sQuery(id+"F0.wireOp",EDGE,"E3283"),sQuery(id+"F0.wireOp",EDGE,"E3284"),sQuery(id+"F0.wireOp",EDGE,"E3285"),sQuery(id+"F0.wireOp",EDGE,"E3286"),sQuery(id+"F0.wireOp",EDGE,"E3287"),sQuery(id+"F0.wireOp",EDGE,"E3288"),sQuery(id+"F0.wireOp",EDGE,"E3289"),sQuery(id+"F0.wireOp",EDGE,"E3290"),sQuery(id+"F0.wireOp",EDGE,"E3291"),sQuery(id+"F0.wireOp",EDGE,"E3292"),sQuery(id+"F0.wireOp",EDGE,"E3293"),sQuery(id+"F0.wireOp",EDGE,"E3294"),sQuery(id+"F0.wireOp",EDGE,"E3295"),sQuery(id+"F0.wireOp",EDGE,"E3296"),sQuery(id+"F0.wireOp",EDGE,"E3297"),sQuery(id+"F0.wireOp",EDGE,"E3298"),sQuery(id+"F0.wireOp",EDGE,"E3299"),sQuery(id+"F0.wireOp",EDGE,"E3300"),sQuery(id+"F0.wireOp",EDGE,"E3301"),sQuery(id+"F0.wireOp",EDGE,"E3302"),sQuery(id+"F0.wireOp",EDGE,"E3303"),sQuery(id+"F0.wireOp",EDGE,"E3304"),sQuery(id+"F0.wireOp",EDGE,"E3305"),sQuery(id+"F0.wireOp",EDGE,"E3306"),sQuery(id+"F0.wireOp",EDGE,"E3307"),sQuery(id+"F0.wireOp",EDGE,"E3308"),sQuery(id+"F0.wireOp",EDGE,"E3309"),sQuery(id+"F0.wireOp",EDGE,"E3310"),sQuery(id+"F0.wireOp",EDGE,"E3311"),sQuery(id+"F0.wireOp",EDGE,"E3312"),sQuery(id+"F0.wireOp",EDGE,"E3313"),sQuery(id+"F0.wireOp",EDGE,"E3314"),sQuery(id+"F0.wireOp",EDGE,"E3315"),sQuery(id+"F0.wireOp",EDGE,"E3316"),sQuery(id+"F0.wireOp",EDGE,"E3317"),sQuery(id+"F0.wireOp",EDGE,"E3318"),sQuery(id+"F0.wireOp",EDGE,"E3319"),sQuery(id+"F0.wireOp",EDGE,"E3320"),sQuery(id+"F0.wireOp",EDGE,"E3321"),sQuery(id+"F0.wireOp",EDGE,"E3322"),sQuery(id+"F0.wireOp",EDGE,"E3323"),sQuery(id+"F0.wireOp",EDGE,"E3324"),sQuery(id+"F0.wireOp",EDGE,"E3325"),sQuery(id+"F0.wireOp",EDGE,"E3326"),sQuery(id+"F0.wireOp",EDGE,"E3327"),sQuery(id+"F0.wireOp",EDGE,"E3328"),sQuery(id+"F0.wireOp",EDGE,"E3329"),sQuery(id+"F0.wireOp",EDGE,"E3330"),sQuery(id+"F0.wireOp",EDGE,"E3331"),sQuery(id+"F0.wireOp",EDGE,"E3332"),sQuery(id+"F0.wireOp",EDGE,"E3333"),sQuery(id+"F0.wireOp",EDGE,"E3334"),sQuery(id+"F0.wireOp",EDGE,"E3335"),sQuery(id+"F0.wireOp",EDGE,"E3336"),sQuery(id+"F0.wireOp",EDGE,"E3337"),sQuery(id+"F0.wireOp",EDGE,"E3338"),sQuery(id+"F0.wireOp",EDGE,"E3339"),sQuery(id+"F0.wireOp",EDGE,"E3340"),sQuery(id+"F0.wireOp",EDGE,"E3341"),sQuery(id+"F0.wireOp",EDGE,"E3342"),sQuery(id+"F0.wireOp",EDGE,"E3343"),sQuery(id+"F0.wireOp",EDGE,"E3344"),sQuery(id+"F0.wireOp",EDGE,"E3345"),sQuery(id+"F0.wireOp",EDGE,"E3346"),sQuery(id+"F0.wireOp",EDGE,"E3347"),sQuery(id+"F0.wireOp",EDGE,"E3348"),sQuery(id+"F0.wireOp",EDGE,"E3349"),sQuery(id+"F0.wireOp",EDGE,"E3350"),sQuery(id+"F0.wireOp",EDGE,"E3351"),sQuery(id+"F0.wireOp",EDGE,"E3352"),sQuery(id+"F0.wireOp",EDGE,"E3353"),sQuery(id+"F0.wireOp",EDGE,"E3354"),sQuery(id+"F0.wireOp",EDGE,"E3355"),sQuery(id+"F0.wireOp",EDGE,"E3356"),sQuery(id+"F0.wireOp",EDGE,"E3357"),sQuery(id+"F0.wireOp",EDGE,"E3358"),sQuery(id+"F0.wireOp",EDGE,"E3359"),sQuery(id+"F0.wireOp",EDGE,"E3360"),sQuery(id+"F0.wireOp",EDGE,"E3361"),sQuery(id+"F0.wireOp",EDGE,"E3362"),sQuery(id+"F0.wireOp",EDGE,"E3363"),sQuery(id+"F0.wireOp",EDGE,"E3364"),sQuery(id+"F0.wireOp",EDGE,"E3365"),sQuery(id+"F0.wireOp",EDGE,"E3366"),sQuery(id+"F0.wireOp",EDGE,"E3367"),sQuery(id+"F0.wireOp",EDGE,"E3368"),sQuery(id+"F0.wireOp",EDGE,"E3369"),sQuery(id+"F0.wireOp",EDGE,"E3370"),sQuery(id+"F0.wireOp",EDGE,"E3371"),sQuery(id+"F0.wireOp",EDGE,"E3372"),sQuery(id+"F0.wireOp",EDGE,"E3373"),sQuery(id+"F0.wireOp",EDGE,"E3374"),sQuery(id+"F0.wireOp",EDGE,"E3375"),sQuery(id+"F0.wireOp",EDGE,"E3376"),sQuery(id+"F0.wireOp",EDGE,"E3377"),sQuery(id+"F0.wireOp",EDGE,"E3378"),sQuery(id+"F0.wireOp",EDGE,"E3379"),sQuery(id+"F0.wireOp",EDGE,"E3380"),sQuery(id+"F0.wireOp",EDGE,"E3381"),sQuery(id+"F0.wireOp",EDGE,"E3382"),sQuery(id+"F0.wireOp",EDGE,"E3383"),sQuery(id+"F0.wireOp",EDGE,"E3384"),sQuery(id+"F0.wireOp",EDGE,"E3385"),sQuery(id+"F0.wireOp",EDGE,"E3386"),sQuery(id+"F0.wireOp",EDGE,"E3387"),sQuery(id+"F0.wireOp",EDGE,"E3388"),sQuery(id+"F0.wireOp",EDGE,"E3389"),sQuery(id+"F0.wireOp",EDGE,"E3390"),sQuery(id+"F0.wireOp",EDGE,"E3391"),sQuery(id+"F0.wireOp",EDGE,"E3392"),sQuery(id+"F0.wireOp",EDGE,"E3393"),sQuery(id+"F0.wireOp",EDGE,"E3394"),sQuery(id+"F0.wireOp",EDGE,"E3395"),sQuery(id+"F0.wireOp",EDGE,"E3396"),sQuery(id+"F0.wireOp",EDGE,"E3397"),sQuery(id+"F0.wireOp",EDGE,"E3398"),sQuery(id+"F0.wireOp",EDGE,"E3399"),sQuery(id+"F0.wireOp",EDGE,"E3400"),sQuery(id+"F0.wireOp",EDGE,"E3401"),sQuery(id+"F0.wireOp",EDGE,"E3402"),sQuery(id+"F0.wireOp",EDGE,"E3403"),sQuery(id+"F0.wireOp",EDGE,"E3404"),sQuery(id+"F0.wireOp",EDGE,"E3405"),sQuery(id+"F0.wireOp",EDGE,"E3406"),sQuery(id+"F0.wireOp",EDGE,"E3407"),sQuery(id+"F0.wireOp",EDGE,"E3408"),sQuery(id+"F0.wireOp",EDGE,"E3409"),sQuery(id+"F0.wireOp",EDGE,"E3410"),sQuery(id+"F0.wireOp",EDGE,"E3411"),sQuery(id+"F0.wireOp",EDGE,"E3412"),sQuery(id+"F0.wireOp",EDGE,"E3413"),sQuery(id+"F0.wireOp",EDGE,"E3414"),sQuery(id+"F0.wireOp",EDGE,"E3415"),sQuery(id+"F0.wireOp",EDGE,"E3416"),sQuery(id+"F0.wireOp",EDGE,"E3417"),sQuery(id+"F0.wireOp",EDGE,"E3418"),sQuery(id+"F0.wireOp",EDGE,"E3419"),sQuery(id+"F0.wireOp",EDGE,"E3420"),sQuery(id+"F0.wireOp",EDGE,"E3421"),sQuery(id+"F0.wireOp",EDGE,"E3422"),sQuery(id+"F0.wireOp",EDGE,"E3423"),sQuery(id+"F0.wireOp",EDGE,"E3424"),sQuery(id+"F0.wireOp",EDGE,"E3425"),sQuery(id+"F0.wireOp",EDGE,"E3426"),sQuery(id+"F0.wireOp",EDGE,"E3427"),sQuery(id+"F0.wireOp",EDGE,"E3428"),sQuery(id+"F0.wireOp",EDGE,"E3429"),sQuery(id+"F0.wireOp",EDGE,"E3430"),sQuery(id+"F0.wireOp",EDGE,"E3431"),sQuery(id+"F0.wireOp",EDGE,"E3432"),sQuery(id+"F0.wireOp",EDGE,"E3433"),sQuery(id+"F0.wireOp",EDGE,"E3434"),sQuery(id+"F0.wireOp",EDGE,"E3435"),sQuery(id+"F0.wireOp",EDGE,"E3436"),sQuery(id+"F0.wireOp",EDGE,"E3437"),sQuery(id+"F0.wireOp",EDGE,"E3438"),sQuery(id+"F0.wireOp",EDGE,"E3439"),sQuery(id+"F0.wireOp",EDGE,"E3440"),sQuery(id+"F0.wireOp",EDGE,"E3441"),sQuery(id+"F0.wireOp",EDGE,"E3442"),sQuery(id+"F0.wireOp",EDGE,"E3443"),sQuery(id+"F0.wireOp",EDGE,"E3444"),sQuery(id+"F0.wireOp",EDGE,"E3445"),sQuery(id+"F0.wireOp",EDGE,"E3446"),sQuery(id+"F0.wireOp",EDGE,"E3447"),sQuery(id+"F0.wireOp",EDGE,"E3448"),sQuery(id+"F0.wireOp",EDGE,"E3449"),sQuery(id+"F0.wireOp",EDGE,"E3450"),sQuery(id+"F0.wireOp",EDGE,"E3451"),sQuery(id+"F0.wireOp",EDGE,"E3452"),sQuery(id+"F0.wireOp",EDGE,"E3453"),sQuery(id+"F0.wireOp",EDGE,"E3454"),sQuery(id+"F0.wireOp",EDGE,"E3455"),sQuery(id+"F0.wireOp",EDGE,"E3456"),sQuery(id+"F0.wireOp",EDGE,"E3457"),sQuery(id+"F0.wireOp",EDGE,"E3458"),sQuery(id+"F0.wireOp",EDGE,"E3459"),sQuery(id+"F0.wireOp",EDGE,"E3460"),sQuery(id+"F0.wireOp",EDGE,"E3461"),sQuery(id+"F0.wireOp",EDGE,"E3462"),sQuery(id+"F0.wireOp",EDGE,"E3463"),sQuery(id+"F0.wireOp",EDGE,"E3464"),sQuery(id+"F0.wireOp",EDGE,"E3465"),sQuery(id+"F0.wireOp",EDGE,"E3466"),sQuery(id+"F0.wireOp",EDGE,"E3467"),sQuery(id+"F0.wireOp",EDGE,"E3468"),sQuery(id+"F0.wireOp",EDGE,"E3469"),sQuery(id+"F0.wireOp",EDGE,"E3470"),sQuery(id+"F0.wireOp",EDGE,"E3471"),sQuery(id+"F0.wireOp",EDGE,"E3472"),sQuery(id+"F0.wireOp",EDGE,"E3473"),sQuery(id+"F0.wireOp",EDGE,"E3474"),sQuery(id+"F0.wireOp",EDGE,"E3475"),sQuery(id+"F0.wireOp",EDGE,"E3476"),sQuery(id+"F0.wireOp",EDGE,"E3477"),sQuery(id+"F0.wireOp",EDGE,"E3478"),sQuery(id+"F0.wireOp",EDGE,"E3479"),sQuery(id+"F0.wireOp",EDGE,"E3480"),sQuery(id+"F0.wireOp",EDGE,"E3481"),sQuery(id+"F0.wireOp",EDGE,"E3482"),sQuery(id+"F0.wireOp",EDGE,"E3483"),sQuery(id+"F0.wireOp",EDGE,"E3484"),sQuery(id+"F0.wireOp",EDGE,"E3485"),sQuery(id+"F0.wireOp",EDGE,"E3486"),sQuery(id+"F0.wireOp",EDGE,"E3487"),sQuery(id+"F0.wireOp",EDGE,"E3488"),sQuery(id+"F0.wireOp",EDGE,"E3489"),sQuery(id+"F0.wireOp",EDGE,"E3490"),sQuery(id+"F0.wireOp",EDGE,"E3491"),sQuery(id+"F0.wireOp",EDGE,"E3492"),sQuery(id+"F0.wireOp",EDGE,"E3493"),sQuery(id+"F0.wireOp",EDGE,"E3494"),sQuery(id+"F0.wireOp",EDGE,"E3495"),sQuery(id+"F0.wireOp",EDGE,"E3496"),sQuery(id+"F0.wireOp",EDGE,"E3497"),sQuery(id+"F0.wireOp",EDGE,"E3498"),sQuery(id+"F0.wireOp",EDGE,"E3499"),sQuery(id+"F0.wireOp",EDGE,"E3500"),sQuery(id+"F0.wireOp",EDGE,"E3501"),sQuery(id+"F0.wireOp",EDGE,"E3502"),sQuery(id+"F0.wireOp",EDGE,"E3503"),sQuery(id+"F0.wireOp",EDGE,"E3504"),sQuery(id+"F0.wireOp",EDGE,"E3505"),sQuery(id+"F0.wireOp",EDGE,"E3506"),sQuery(id+"F0.wireOp",EDGE,"E3507"),sQuery(id+"F0.wireOp",EDGE,"E3508"),sQuery(id+"F0.wireOp",EDGE,"E3509"),sQuery(id+"F0.wireOp",EDGE,"E3510"),sQuery(id+"F0.wireOp",EDGE,"E3511"),sQuery(id+"F0.wireOp",EDGE,"E3512"),sQuery(id+"F0.wireOp",EDGE,"E3513"),sQuery(id+"F0.wireOp",EDGE,"E3514"),sQuery(id+"F0.wireOp",EDGE,"E3515"),sQuery(id+"F0.wireOp",EDGE,"E3516"),sQuery(id+"F0.wireOp",EDGE,"E3517"),sQuery(id+"F0.wireOp",EDGE,"E3518"),sQuery(id+"F0.wireOp",EDGE,"E3519"),sQuery(id+"F0.wireOp",EDGE,"E3520"),sQuery(id+"F0.wireOp",EDGE,"E3521"),sQuery(id+"F0.wireOp",EDGE,"E3522"),sQuery(id+"F0.wireOp",EDGE,"E3523"),sQuery(id+"F0.wireOp",EDGE,"E3524"),sQuery(id+"F0.wireOp",EDGE,"E3525"),sQuery(id+"F0.wireOp",EDGE,"E3526"),sQuery(id+"F0.wireOp",EDGE,"E3527"),sQuery(id+"F0.wireOp",EDGE,"E3528"),sQuery(id+"F0.wireOp",EDGE,"E3529"),sQuery(id+"F0.wireOp",EDGE,"E3530"),sQuery(id+"F0.wireOp",EDGE,"E3531"),sQuery(id+"F0.wireOp",EDGE,"E3532"),sQuery(id+"F0.wireOp",EDGE,"E3533"),sQuery(id+"F0.wireOp",EDGE,"E3534"),sQuery(id+"F0.wireOp",EDGE,"E3535"),sQuery(id+"F0.wireOp",EDGE,"E3536"),sQuery(id+"F0.wireOp",EDGE,"E3537"),sQuery(id+"F0.wireOp",EDGE,"E3538"),sQuery(id+"F0.wireOp",EDGE,"E3539"),sQuery(id+"F0.wireOp",EDGE,"E3540"),sQuery(id+"F0.wireOp",EDGE,"E3541"),sQuery(id+"F0.wireOp",EDGE,"E3542"),sQuery(id+"F0.wireOp",EDGE,"E3543"),sQuery(id+"F0.wireOp",EDGE,"E3544"),sQuery(id+"F0.wireOp",EDGE,"E3545"),sQuery(id+"F0.wireOp",EDGE,"E3546"),sQuery(id+"F0.wireOp",EDGE,"E3547"),sQuery(id+"F0.wireOp",EDGE,"E3548"),sQuery(id+"F0.wireOp",EDGE,"E3549"),sQuery(id+"F0.wireOp",EDGE,"E3550"),sQuery(id+"F0.wireOp",EDGE,"E3551"),sQuery(id+"F0.wireOp",EDGE,"E3552"),sQuery(id+"F0.wireOp",EDGE,"E3553"),sQuery(id+"F0.wireOp",EDGE,"E3554"),sQuery(id+"F0.wireOp",EDGE,"E3555"),sQuery(id+"F0.wireOp",EDGE,"E3556"),sQuery(id+"F0.wireOp",EDGE,"E3557"),sQuery(id+"F0.wireOp",EDGE,"E3558"),sQuery(id+"F0.wireOp",EDGE,"E3559"),sQuery(id+"F0.wireOp",EDGE,"E3560"),sQuery(id+"F0.wireOp",EDGE,"E3561"),sQuery(id+"F0.wireOp",EDGE,"E3562"),sQuery(id+"F0.wireOp",EDGE,"E3563"),sQuery(id+"F0.wireOp",EDGE,"E3564"),sQuery(id+"F0.wireOp",EDGE,"E3565"),sQuery(id+"F0.wireOp",EDGE,"E3566"),sQuery(id+"F0.wireOp",EDGE,"E3567"),sQuery(id+"F0.wireOp",EDGE,"E3568"),sQuery(id+"F0.wireOp",EDGE,"E3569"),sQuery(id+"F0.wireOp",EDGE,"E3570"),sQuery(id+"F0.wireOp",EDGE,"E3571"),sQuery(id+"F0.wireOp",EDGE,"E3572"),sQuery(id+"F0.wireOp",EDGE,"E3573"),sQuery(id+"F0.wireOp",EDGE,"E3574"),sQuery(id+"F0.wireOp",EDGE,"E3575"),sQuery(id+"F0.wireOp",EDGE,"E3576"),sQuery(id+"F0.wireOp",EDGE,"E3577"),sQuery(id+"F0.wireOp",EDGE,"E3578"),sQuery(id+"F0.wireOp",EDGE,"E3579"),sQuery(id+"F0.wireOp",EDGE,"E3580"),sQuery(id+"F0.wireOp",EDGE,"E3581"),sQuery(id+"F0.wireOp",EDGE,"E3582"),sQuery(id+"F0.wireOp",EDGE,"E3583"),sQuery(id+"F0.wireOp",EDGE,"E3584"),sQuery(id+"F0.wireOp",EDGE,"E3585"),sQuery(id+"F0.wireOp",EDGE,"E3586"),sQuery(id+"F0.wireOp",EDGE,"E3587"),sQuery(id+"F0.wireOp",EDGE,"E3588"),sQuery(id+"F0.wireOp",EDGE,"E3589"),sQuery(id+"F0.wireOp",EDGE,"E3590"),sQuery(id+"F0.wireOp",EDGE,"E3591"),sQuery(id+"F0.wireOp",EDGE,"E3592"),sQuery(id+"F0.wireOp",EDGE,"E3593"),sQuery(id+"F0.wireOp",EDGE,"E3594"),sQuery(id+"F0.wireOp",EDGE,"E3595"),sQuery(id+"F0.wireOp",EDGE,"E3596"),sQuery(id+"F0.wireOp",EDGE,"E3597"),sQuery(id+"F0.wireOp",EDGE,"E3598"),sQuery(id+"F0.wireOp",EDGE,"E3599"),sQuery(id+"F0.wireOp",EDGE,"E3600"),sQuery(id+"F0.wireOp",EDGE,"E3601"),sQuery(id+"F0.wireOp",EDGE,"E3602"),sQuery(id+"F0.wireOp",EDGE,"E3603"),sQuery(id+"F0.wireOp",EDGE,"E3604"),sQuery(id+"F0.wireOp",EDGE,"E3605"),sQuery(id+"F0.wireOp",EDGE,"E3606"),sQuery(id+"F0.wireOp",EDGE,"E3607"),sQuery(id+"F0.wireOp",EDGE,"E3608"),sQuery(id+"F0.wireOp",EDGE,"E3609"),sQuery(id+"F0.wireOp",EDGE,"E3610"),sQuery(id+"F0.wireOp",EDGE,"E3611"),sQuery(id+"F0.wireOp",EDGE,"E3612"),sQuery(id+"F0.wireOp",EDGE,"E3613"),sQuery(id+"F0.wireOp",EDGE,"E3614"),sQuery(id+"F0.wireOp",EDGE,"E3615"),sQuery(id+"F0.wireOp",EDGE,"E3616"),sQuery(id+"F0.wireOp",EDGE,"E3617"),sQuery(id+"F0.wireOp",EDGE,"E3618"),sQuery(id+"F0.wireOp",EDGE,"E3619"),sQuery(id+"F0.wireOp",EDGE,"E3620"),sQuery(id+"F0.wireOp",EDGE,"E3621"),sQuery(id+"F0.wireOp",EDGE,"E3622"),sQuery(id+"F0.wireOp",EDGE,"E3623"),sQuery(id+"F0.wireOp",EDGE,"E3624"),sQuery(id+"F0.wireOp",EDGE,"E3625"),sQuery(id+"F0.wireOp",EDGE,"E3626"),sQuery(id+"F0.wireOp",EDGE,"E3627"),sQuery(id+"F0.wireOp",EDGE,"E3628"),sQuery(id+"F0.wireOp",EDGE,"E3629"),sQuery(id+"F0.wireOp",EDGE,"E3630"),sQuery(id+"F0.wireOp",EDGE,"E3631"),sQuery(id+"F0.wireOp",EDGE,"E3632"),sQuery(id+"F0.wireOp",EDGE,"E3633"),sQuery(id+"F0.wireOp",EDGE,"E3634"),sQuery(id+"F0.wireOp",EDGE,"E3635"),sQuery(id+"F0.wireOp",EDGE,"E3636"),sQuery(id+"F0.wireOp",EDGE,"E3637"),sQuery(id+"F0.wireOp",EDGE,"E3638"),sQuery(id+"F0.wireOp",EDGE,"E3639"),sQuery(id+"F0.wireOp",EDGE,"E3640"),sQuery(id+"F0.wireOp",EDGE,"E3641"),sQuery(id+"F0.wireOp",EDGE,"E3642"),sQuery(id+"F0.wireOp",EDGE,"E3643"),sQuery(id+"F0.wireOp",EDGE,"E3644"),sQuery(id+"F0.wireOp",EDGE,"E3645"),sQuery(id+"F0.wireOp",EDGE,"E3646"),sQuery(id+"F0.wireOp",EDGE,"E3647"),sQuery(id+"F0.wireOp",EDGE,"E3648"),sQuery(id+"F0.wireOp",EDGE,"E3649"),sQuery(id+"F0.wireOp",EDGE,"E3650"),sQuery(id+"F0.wireOp",EDGE,"E3651"),sQuery(id+"F0.wireOp",EDGE,"E3652"),sQuery(id+"F0.wireOp",EDGE,"E3653"),sQuery(id+"F0.wireOp",EDGE,"E3654"),sQuery(id+"F0.wireOp",EDGE,"E3655"),sQuery(id+"F0.wireOp",EDGE,"E3656"),sQuery(id+"F0.wireOp",EDGE,"E3657"),sQuery(id+"F0.wireOp",EDGE,"E3658"),sQuery(id+"F0.wireOp",EDGE,"E3659"),sQuery(id+"F0.wireOp",EDGE,"E3660"),sQuery(id+"F0.wireOp",EDGE,"E3661"),sQuery(id+"F0.wireOp",EDGE,"E3662"),sQuery(id+"F0.wireOp",EDGE,"E3663"),sQuery(id+"F0.wireOp",EDGE,"E3664"),sQuery(id+"F0.wireOp",EDGE,"E3665"),sQuery(id+"F0.wireOp",EDGE,"E3666"),sQuery(id+"F0.wireOp",EDGE,"E3667"),sQuery(id+"F0.wireOp",EDGE,"E3668"),sQuery(id+"F0.wireOp",EDGE,"E3669"),sQuery(id+"F0.wireOp",EDGE,"E3670"),sQuery(id+"F0.wireOp",EDGE,"E3671"),sQuery(id+"F0.wireOp",EDGE,"E3672"),sQuery(id+"F0.wireOp",EDGE,"E3673"),sQuery(id+"F0.wireOp",EDGE,"E3674"),sQuery(id+"F0.wireOp",EDGE,"E3675"),sQuery(id+"F0.wireOp",EDGE,"E3676"),sQuery(id+"F0.wireOp",EDGE,"E3677"),sQuery(id+"F0.wireOp",EDGE,"E3678"),sQuery(id+"F0.wireOp",EDGE,"E3679"),sQuery(id+"F0.wireOp",EDGE,"E3680"),sQuery(id+"F0.wireOp",EDGE,"E3681"),sQuery(id+"F0.wireOp",EDGE,"E3682"),sQuery(id+"F0.wireOp",EDGE,"E3683"),sQuery(id+"F0.wireOp",EDGE,"E3684"),sQuery(id+"F0.wireOp",EDGE,"E3685"),sQuery(id+"F0.wireOp",EDGE,"E3686"),sQuery(id+"F0.wireOp",EDGE,"E3687"),sQuery(id+"F0.wireOp",EDGE,"E3688"),sQuery(id+"F0.wireOp",EDGE,"E3689"),sQuery(id+"F0.wireOp",EDGE,"E3690"),sQuery(id+"F0.wireOp",EDGE,"E3691"),sQuery(id+"F0.wireOp",EDGE,"E3692"),sQuery(id+"F0.wireOp",EDGE,"E3693"),sQuery(id+"F0.wireOp",EDGE,"E3694"),sQuery(id+"F0.wireOp",EDGE,"E3695"),sQuery(id+"F0.wireOp",EDGE,"E3696"),sQuery(id+"F0.wireOp",EDGE,"E3697"),sQuery(id+"F0.wireOp",EDGE,"E3698"),sQuery(id+"F0.wireOp",EDGE,"E3699"),sQuery(id+"F0.wireOp",EDGE,"E3700"),sQuery(id+"F0.wireOp",EDGE,"E3701"),sQuery(id+"F0.wireOp",EDGE,"E3702"),sQuery(id+"F0.wireOp",EDGE,"E3703"),sQuery(id+"F0.wireOp",EDGE,"E3704"),sQuery(id+"F0.wireOp",EDGE,"E3705"),sQuery(id+"F0.wireOp",EDGE,"E3706"),sQuery(id+"F0.wireOp",EDGE,"E3707"),sQuery(id+"F0.wireOp",EDGE,"E3708"),sQuery(id+"F0.wireOp",EDGE,"E3709"),sQuery(id+"F0.wireOp",EDGE,"E3710"),sQuery(id+"F0.wireOp",EDGE,"E3711"),sQuery(id+"F0.wireOp",EDGE,"E3712"),sQuery(id+"F0.wireOp",EDGE,"E3713"),sQuery(id+"F0.wireOp",EDGE,"E3714"),sQuery(id+"F0.wireOp",EDGE,"E3715"),sQuery(id+"F0.wireOp",EDGE,"E3716"),sQuery(id+"F0.wireOp",EDGE,"E3717"),sQuery(id+"F0.wireOp",EDGE,"E3718"),sQuery(id+"F0.wireOp",EDGE,"E3719"),sQuery(id+"F0.wireOp",EDGE,"E3720"),sQuery(id+"F0.wireOp",EDGE,"E3721"),sQuery(id+"F0.wireOp",EDGE,"E3722"),sQuery(id+"F0.wireOp",EDGE,"E3723"),sQuery(id+"F0.wireOp",EDGE,"E3724"),sQuery(id+"F0.wireOp",EDGE,"E3725"),sQuery(id+"F0.wireOp",EDGE,"E3726"),sQuery(id+"F0.wireOp",EDGE,"E3727"),sQuery(id+"F0.wireOp",EDGE,"E3728"),sQuery(id+"F0.wireOp",EDGE,"E3729"),sQuery(id+"F0.wireOp",EDGE,"E3730"),sQuery(id+"F0.wireOp",EDGE,"E3731"),sQuery(id+"F0.wireOp",EDGE,"E3732"),sQuery(id+"F0.wireOp",EDGE,"E3733"),sQuery(id+"F0.wireOp",EDGE,"E3734"),sQuery(id+"F0.wireOp",EDGE,"E3735"),sQuery(id+"F0.wireOp",EDGE,"E3736"),sQuery(id+"F0.wireOp",EDGE,"E3737"),sQuery(id+"F0.wireOp",EDGE,"E3738"),sQuery(id+"F0.wireOp",EDGE,"E3739"),sQuery(id+"F0.wireOp",EDGE,"E3740"),sQuery(id+"F0.wireOp",EDGE,"E3741"),sQuery(id+"F0.wireOp",EDGE,"E3742"),sQuery(id+"F0.wireOp",EDGE,"E3743"),sQuery(id+"F0.wireOp",EDGE,"E3744"),sQuery(id+"F0.wireOp",EDGE,"E3745"),sQuery(id+"F0.wireOp",EDGE,"E3746"),sQuery(id+"F0.wireOp",EDGE,"E3747"),sQuery(id+"F0.wireOp",EDGE,"E3748"),sQuery(id+"F0.wireOp",EDGE,"E3749"),sQuery(id+"F0.wireOp",EDGE,"E3750"),sQuery(id+"F0.wireOp",EDGE,"E3751"),sQuery(id+"F0.wireOp",EDGE,"E3752"),sQuery(id+"F0.wireOp",EDGE,"E3753"),sQuery(id+"F0.wireOp",EDGE,"E3754"),sQuery(id+"F0.wireOp",EDGE,"E3755"),sQuery(id+"F0.wireOp",EDGE,"E3756"),sQuery(id+"F0.wireOp",EDGE,"E3757"),sQuery(id+"F0.wireOp",EDGE,"E3758"),sQuery(id+"F0.wireOp",EDGE,"E3759"),sQuery(id+"F0.wireOp",EDGE,"E3760"),sQuery(id+"F0.wireOp",EDGE,"E3761"),sQuery(id+"F0.wireOp",EDGE,"E3762"),sQuery(id+"F0.wireOp",EDGE,"E3763"),sQuery(id+"F0.wireOp",EDGE,"E3764"),sQuery(id+"F0.wireOp",EDGE,"E3765"),sQuery(id+"F0.wireOp",EDGE,"E3766"),sQuery(id+"F0.wireOp",EDGE,"E3767"),sQuery(id+"F0.wireOp",EDGE,"E3768"),sQuery(id+"F0.wireOp",EDGE,"E3769"),sQuery(id+"F0.wireOp",EDGE,"E3770"),sQuery(id+"F0.wireOp",EDGE,"E3771"),sQuery(id+"F0.wireOp",EDGE,"E3772"),sQuery(id+"F0.wireOp",EDGE,"E3773"),sQuery(id+"F0.wireOp",EDGE,"E3774"),sQuery(id+"F0.wireOp",EDGE,"E3775"),sQuery(id+"F0.wireOp",EDGE,"E3776"),sQuery(id+"F0.wireOp",EDGE,"E3777"),sQuery(id+"F0.wireOp",EDGE,"E3778"),sQuery(id+"F0.wireOp",EDGE,"E3779"),sQuery(id+"F0.wireOp",EDGE,"E3780"),sQuery(id+"F0.wireOp",EDGE,"E3781"),sQuery(id+"F0.wireOp",EDGE,"E3782"),sQuery(id+"F0.wireOp",EDGE,"E3783"),sQuery(id+"F0.wireOp",EDGE,"E3784"),sQuery(id+"F0.wireOp",EDGE,"E3785"),sQuery(id+"F0.wireOp",EDGE,"E3786"),sQuery(id+"F0.wireOp",EDGE,"E3787"),sQuery(id+"F0.wireOp",EDGE,"E3788"),sQuery(id+"F0.wireOp",EDGE,"E3789"),sQuery(id+"F0.wireOp",EDGE,"E3790"),sQuery(id+"F0.wireOp",EDGE,"E3791"),sQuery(id+"F0.wireOp",EDGE,"E3792"),sQuery(id+"F0.wireOp",EDGE,"E3793"),sQuery(id+"F0.wireOp",EDGE,"E3794"),sQuery(id+"F0.wireOp",EDGE,"E3795"),sQuery(id+"F0.wireOp",EDGE,"E3796"),sQuery(id+"F0.wireOp",EDGE,"E3797"),sQuery(id+"F0.wireOp",EDGE,"E3798"),sQuery(id+"F0.wireOp",EDGE,"E3799"),sQuery(id+"F0.wireOp",EDGE,"E3800"),sQuery(id+"F0.wireOp",EDGE,"E3801"),sQuery(id+"F0.wireOp",EDGE,"E3802"),sQuery(id+"F0.wireOp",EDGE,"E3803"),sQuery(id+"F0.wireOp",EDGE,"E3804"),sQuery(id+"F0.wireOp",EDGE,"E3805"),sQuery(id+"F0.wireOp",EDGE,"E3806"),sQuery(id+"F0.wireOp",EDGE,"E3807"),sQuery(id+"F0.wireOp",EDGE,"E3808"),sQuery(id+"F0.wireOp",EDGE,"E3809"),sQuery(id+"F0.wireOp",EDGE,"E3810"),sQuery(id+"F0.wireOp",EDGE,"E3811"),sQuery(id+"F0.wireOp",EDGE,"E3812"),sQuery(id+"F0.wireOp",EDGE,"E3813"),sQuery(id+"F0.wireOp",EDGE,"E3814"),sQuery(id+"F0.wireOp",EDGE,"E3815"),sQuery(id+"F0.wireOp",EDGE,"E3816"),sQuery(id+"F0.wireOp",EDGE,"E3817"),sQuery(id+"F0.wireOp",EDGE,"E3818"),sQuery(id+"F0.wireOp",EDGE,"E3819"),sQuery(id+"F0.wireOp",EDGE,"E3820"),sQuery(id+"F0.wireOp",EDGE,"E3821"),sQuery(id+"F0.wireOp",EDGE,"E3822"),sQuery(id+"F0.wireOp",EDGE,"E3823"),sQuery(id+"F0.wireOp",EDGE,"E3824"),sQuery(id+"F0.wireOp",EDGE,"E3825"),sQuery(id+"F0.wireOp",EDGE,"E3826"),sQuery(id+"F0.wireOp",EDGE,"E3827"),sQuery(id+"F0.wireOp",EDGE,"E3828"),sQuery(id+"F0.wireOp",EDGE,"E3829"),sQuery(id+"F0.wireOp",EDGE,"E3830"),sQuery(id+"F0.wireOp",EDGE,"E3831"),sQuery(id+"F0.wireOp",EDGE,"E3832"),sQuery(id+"F0.wireOp",EDGE,"E3833"),sQuery(id+"F0.wireOp",EDGE,"E3834"),sQuery(id+"F0.wireOp",EDGE,"E3835"),sQuery(id+"F0.wireOp",EDGE,"E3836"),sQuery(id+"F0.wireOp",EDGE,"E3837"),sQuery(id+"F0.wireOp",EDGE,"E3838"),sQuery(id+"F0.wireOp",EDGE,"E3839"),sQuery(id+"F0.wireOp",EDGE,"E3840"),sQuery(id+"F0.wireOp",EDGE,"E3841"),sQuery(id+"F0.wireOp",EDGE,"E3842"),sQuery(id+"F0.wireOp",EDGE,"E3843"),sQuery(id+"F0.wireOp",EDGE,"E3844"),sQuery(id+"F0.wireOp",EDGE,"E3845"),sQuery(id+"F0.wireOp",EDGE,"E3846"),sQuery(id+"F0.wireOp",EDGE,"E3847"),sQuery(id+"F0.wireOp",EDGE,"E3848"),sQuery(id+"F0.wireOp",EDGE,"E3849"),sQuery(id+"F0.wireOp",EDGE,"E3850"),sQuery(id+"F0.wireOp",EDGE,"E3851"),sQuery(id+"F0.wireOp",EDGE,"E3852"),sQuery(id+"F0.wireOp",EDGE,"E3853"),sQuery(id+"F0.wireOp",EDGE,"E3854"),sQuery(id+"F0.wireOp",EDGE,"E3855"),sQuery(id+"F0.wireOp",EDGE,"E3856"),sQuery(id+"F0.wireOp",EDGE,"E3857"),sQuery(id+"F0.wireOp",EDGE,"E3858"),sQuery(id+"F0.wireOp",EDGE,"E3859"),sQuery(id+"F0.wireOp",EDGE,"E3860"),sQuery(id+"F0.wireOp",EDGE,"E3861"),sQuery(id+"F0.wireOp",EDGE,"E3862"),sQuery(id+"F0.wireOp",EDGE,"E3863"),sQuery(id+"F0.wireOp",EDGE,"E3864"),sQuery(id+"F0.wireOp",EDGE,"E3865"),sQuery(id+"F0.wireOp",EDGE,"E3866"),sQuery(id+"F0.wireOp",EDGE,"E3867"),sQuery(id+"F0.wireOp",EDGE,"E3868"),sQuery(id+"F0.wireOp",EDGE,"E3869"),sQuery(id+"F0.wireOp",EDGE,"E3870"),sQuery(id+"F0.wireOp",EDGE,"E3871"),sQuery(id+"F0.wireOp",EDGE,"E3872"),sQuery(id+"F0.wireOp",EDGE,"E3873"),sQuery(id+"F0.wireOp",EDGE,"E3874"),sQuery(id+"F0.wireOp",EDGE,"E3875"),sQuery(id+"F0.wireOp",EDGE,"E3876"),sQuery(id+"F0.wireOp",EDGE,"E3877"),sQuery(id+"F0.wireOp",EDGE,"E3878"),sQuery(id+"F0.wireOp",EDGE,"E3879"),sQuery(id+"F0.wireOp",EDGE,"E3880"),sQuery(id+"F0.wireOp",EDGE,"E3881"),sQuery(id+"F0.wireOp",EDGE,"E3882"),sQuery(id+"F0.wireOp",EDGE,"E3883"),sQuery(id+"F0.wireOp",EDGE,"E3884"),sQuery(id+"F0.wireOp",EDGE,"E3885"),sQuery(id+"F0.wireOp",EDGE,"E3886"),sQuery(id+"F0.wireOp",EDGE,"E3887"),sQuery(id+"F0.wireOp",EDGE,"E3888"),sQuery(id+"F0.wireOp",EDGE,"E3889"),sQuery(id+"F0.wireOp",EDGE,"E3890"),sQuery(id+"F0.wireOp",EDGE,"E3891"),sQuery(id+"F0.wireOp",EDGE,"E3892"),sQuery(id+"F0.wireOp",EDGE,"E3893"),sQuery(id+"F0.wireOp",EDGE,"E3894"),sQuery(id+"F0.wireOp",EDGE,"E3895"),sQuery(id+"F0.wireOp",EDGE,"E3896"),sQuery(id+"F0.wireOp",EDGE,"E3897"),sQuery(id+"F0.wireOp",EDGE,"E3898"),sQuery(id+"F0.wireOp",EDGE,"E3899"),sQuery(id+"F0.wireOp",EDGE,"E3900"),sQuery(id+"F0.wireOp",EDGE,"E3901"),sQuery(id+"F0.wireOp",EDGE,"E3902"),sQuery(id+"F0.wireOp",EDGE,"E3903"),sQuery(id+"F0.wireOp",EDGE,"E3904"),sQuery(id+"F0.wireOp",EDGE,"E3905"),sQuery(id+"F0.wireOp",EDGE,"E3906"),sQuery(id+"F0.wireOp",EDGE,"E3907"),sQuery(id+"F0.wireOp",EDGE,"E3908"),sQuery(id+"F0.wireOp",EDGE,"E3909"),sQuery(id+"F0.wireOp",EDGE,"E3910"),sQuery(id+"F0.wireOp",EDGE,"E3911"),sQuery(id+"F0.wireOp",EDGE,"E3912"),sQuery(id+"F0.wireOp",EDGE,"E3913"),sQuery(id+"F0.wireOp",EDGE,"E3914"),sQuery(id+"F0.wireOp",EDGE,"E3915"),sQuery(id+"F0.wireOp",EDGE,"E3916"),sQuery(id+"F0.wireOp",EDGE,"E3917"),sQuery(id+"F0.wireOp",EDGE,"E3918"),sQuery(id+"F0.wireOp",EDGE,"E3919"),sQuery(id+"F0.wireOp",EDGE,"E3920"),sQuery(id+"F0.wireOp",EDGE,"E3921"),sQuery(id+"F0.wireOp",EDGE,"E3922"),sQuery(id+"F0.wireOp",EDGE,"E3923"),sQuery(id+"F0.wireOp",EDGE,"E3924"),sQuery(id+"F0.wireOp",EDGE,"E3925"),sQuery(id+"F0.wireOp",EDGE,"E3926"),sQuery(id+"F0.wireOp",EDGE,"E3927"),sQuery(id+"F0.wireOp",EDGE,"E3928"),sQuery(id+"F0.wireOp",EDGE,"E3929"),sQuery(id+"F0.wireOp",EDGE,"E3930"),sQuery(id+"F0.wireOp",EDGE,"E3931"),sQuery(id+"F0.wireOp",EDGE,"E3932"),sQuery(id+"F0.wireOp",EDGE,"E3933"),sQuery(id+"F0.wireOp",EDGE,"E3934"),sQuery(id+"F0.wireOp",EDGE,"E3935"),sQuery(id+"F0.wireOp",EDGE,"E3936"),sQuery(id+"F0.wireOp",EDGE,"E3937"),sQuery(id+"F0.wireOp",EDGE,"E3938"),sQuery(id+"F0.wireOp",EDGE,"E3939"),sQuery(id+"F0.wireOp",EDGE,"E3940"),sQuery(id+"F0.wireOp",EDGE,"E3941"),sQuery(id+"F0.wireOp",EDGE,"E3942"),sQuery(id+"F0.wireOp",EDGE,"E3943"),sQuery(id+"F0.wireOp",EDGE,"E3944"),sQuery(id+"F0.wireOp",EDGE,"E3945"),sQuery(id+"F0.wireOp",EDGE,"E3946"),sQuery(id+"F0.wireOp",EDGE,"E3947"),sQuery(id+"F0.wireOp",EDGE,"E3948"),sQuery(id+"F0.wireOp",EDGE,"E3949"),sQuery(id+"F0.wireOp",EDGE,"E3950"),sQuery(id+"F0.wireOp",EDGE,"E3951"),sQuery(id+"F0.wireOp",EDGE,"E3952"),sQuery(id+"F0.wireOp",EDGE,"E3953"),sQuery(id+"F0.wireOp",EDGE,"E3954"),sQuery(id+"F0.wireOp",EDGE,"E3955"),sQuery(id+"F0.wireOp",EDGE,"E3956"),sQuery(id+"F0.wireOp",EDGE,"E3957"),sQuery(id+"F0.wireOp",EDGE,"E3958"),sQuery(id+"F0.wireOp",EDGE,"E3959"),sQuery(id+"F0.wireOp",EDGE,"E3960"),sQuery(id+"F0.wireOp",EDGE,"E3961"),sQuery(id+"F0.wireOp",EDGE,"E3962"),sQuery(id+"F0.wireOp",EDGE,"E3963"),sQuery(id+"F0.wireOp",EDGE,"E3964"),sQuery(id+"F0.wireOp",EDGE,"E3965"),sQuery(id+"F0.wireOp",EDGE,"E3966"),sQuery(id+"F0.wireOp",EDGE,"E3967"),sQuery(id+"F0.wireOp",EDGE,"E3968"),sQuery(id+"F0.wireOp",EDGE,"E3969"),sQuery(id+"F0.wireOp",EDGE,"E3970"),sQuery(id+"F0.wireOp",EDGE,"E3971"),sQuery(id+"F0.wireOp",EDGE,"E3972"),sQuery(id+"F0.wireOp",EDGE,"E3973"),sQuery(id+"F0.wireOp",EDGE,"E3974"),sQuery(id+"F0.wireOp",EDGE,"E3975"),sQuery(id+"F0.wireOp",EDGE,"E3976"),sQuery(id+"F0.wireOp",EDGE,"E3977"),sQuery(id+"F0.wireOp",EDGE,"E3978"),sQuery(id+"F0.wireOp",EDGE,"E3979"),sQuery(id+"F0.wireOp",EDGE,"E3980"),sQuery(id+"F0.wireOp",EDGE,"E3981"),sQuery(id+"F0.wireOp",EDGE,"E3982"),sQuery(id+"F0.wireOp",EDGE,"E3983"),sQuery(id+"F0.wireOp",EDGE,"E3984"),sQuery(id+"F0.wireOp",EDGE,"E3985"),sQuery(id+"F0.wireOp",EDGE,"E3986"),sQuery(id+"F0.wireOp",EDGE,"E3987"),sQuery(id+"F0.wireOp",EDGE,"E3988"),sQuery(id+"F0.wireOp",EDGE,"E3989"),sQuery(id+"F0.wireOp",EDGE,"E3990"),sQuery(id+"F0.wireOp",EDGE,"E3991"),sQuery(id+"F0.wireOp",EDGE,"E3992"),sQuery(id+"F0.wireOp",EDGE,"E3993"),sQuery(id+"F0.wireOp",EDGE,"E3994"),sQuery(id+"F0.wireOp",EDGE,"E3995"),sQuery(id+"F0.wireOp",EDGE,"E3996"),sQuery(id+"F0.wireOp",EDGE,"E3997"),sQuery(id+"F0.wireOp",EDGE,"E3998"),sQuery(id+"F0.wireOp",EDGE,"E3999")])],"isStart":false});
            var sketch = newSketch(context, id + "F8", { "sketchPlane" : qUnion([Q0])});
            skCircle(sketch, "E4018", {"center": v(0, 0) * mm, "radius": 2.92 * mm});
            skCircle(sketch, "E4019", {"center": v(0, 0) * mm, "radius": 5.5 * mm});
            skCircle(sketch, "E4020", {"center": v(0, 0) * mm, "radius": 23 * mm});
            skCircle(sketch, "E4021", {"center": v(0, 0) * mm, "radius": 26.5 * mm});
            skSolve(sketch);
        }
        {
            var Q0;
            Q0=qSketchRegion(id+"F8",true);
            var Q1;
            Q1=makeQuery(id+"F8.imprint","IMPRINT",FACE,{"disambiguationData":[TD([[makeQuery(id+"F8.imprint","IMPRINT",EDGE,{"derivedFrom":sQuery(id+"F8.wireOp",EDGE,"E4018")}),-1.0]])]});
            extrude(context, id + "F9", {"entities" : qUnion([Q0, Q1]), "operationType" : NewBodyOperationType.ADD, "depth" : 2 * mm});
        }
    });
